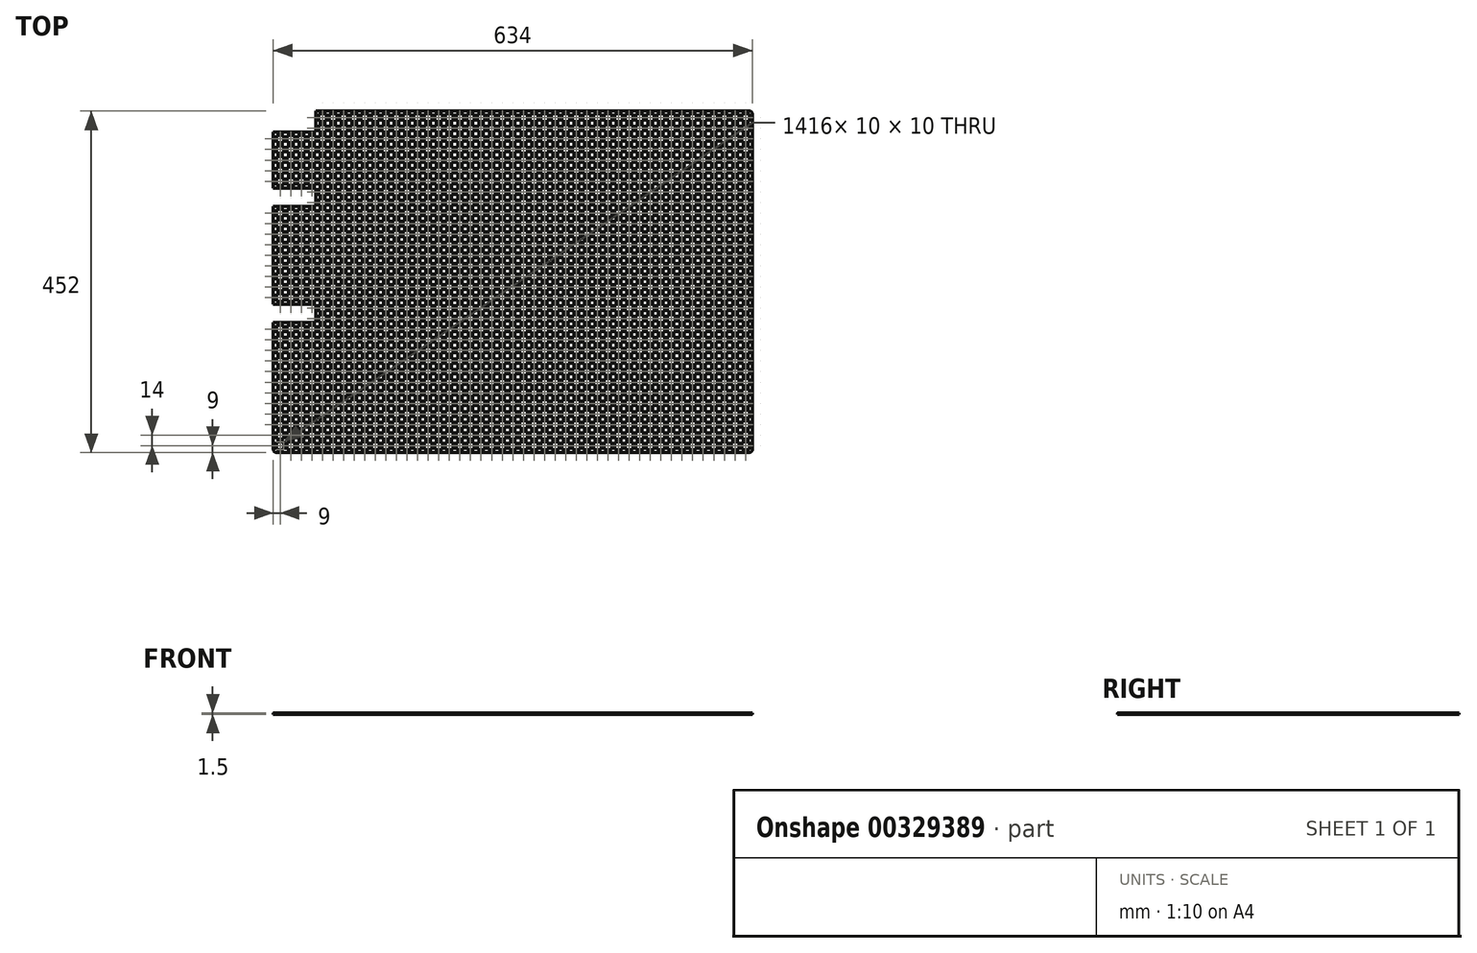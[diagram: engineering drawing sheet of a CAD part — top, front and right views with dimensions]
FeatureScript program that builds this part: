
annotation { "Feature Type Name" : "Feature", "Feature Type Description" : "" }
export const myFeature = defineFeature(function(context is Context, id is Id, definition is map)
    precondition{}
    {
        {
            var Q0;
            Q0=qCreatedBy(makeId("Top.planeOp"),FACE);
            var sketch = newSketch(context, id + "F0", { "sketchPlane" : qUnion([Q0])});
            skLineSegment(sketch, "E0.bottom", {"start": v(-313, 226) * mm, "end": v(313, 226) * mm});
            skLineSegment(sketch, "E0.top", {"start": v(-313, -226) * mm, "end": v(313, -226) * mm});
            skLineSegment(sketch, "E0.left", {"start": v(-317, 222) * mm, "end": v(-317, -222) * mm});
            skLineSegment(sketch, "E0.right", {"start": v(317, 222) * mm, "end": v(317, -222) * mm});
            skLineSegment(sketch, "E1.bottom", {"start": v(-313, -212) * mm, "end": v(-303, -212) * mm});
            skLineSegment(sketch, "E1.top", {"start": v(-313, -222) * mm, "end": v(-303, -222) * mm});
            skLineSegment(sketch, "E1.left", {"start": v(-313, -212) * mm, "end": v(-313, -222) * mm});
            skLineSegment(sketch, "E1.right", {"start": v(-303, -212) * mm, "end": v(-303, -222) * mm});
            skLineSegment(sketch, "E2", {"start": v(-317, 226) * mm, "end": v(317, -226) * mm, "construction": true});
            skLineSegment(sketch, "E3.0.1.0", {"start": v(-313, -198) * mm, "end": v(-313, -208) * mm});
            skLineSegment(sketch, "E3.0.1.1", {"start": v(-313, -208) * mm, "end": v(-303, -208) * mm});
            skLineSegment(sketch, "E3.0.1.2", {"start": v(-313, -198) * mm, "end": v(-303, -198) * mm});
            skLineSegment(sketch, "E3.0.1.3", {"start": v(-303, -198) * mm, "end": v(-303, -208) * mm});
            skLineSegment(sketch, "E3.1.0.0", {"start": v(-299, -212) * mm, "end": v(-299, -222) * mm});
            skLineSegment(sketch, "E3.1.0.1", {"start": v(-299, -222) * mm, "end": v(-289, -222) * mm});
            skLineSegment(sketch, "E3.1.0.2", {"start": v(-299, -212) * mm, "end": v(-289, -212) * mm});
            skLineSegment(sketch, "E3.1.0.3", {"start": v(-289, -212) * mm, "end": v(-289, -222) * mm});
            skLineSegment(sketch, "E3.1.1.0", {"start": v(-299, -198) * mm, "end": v(-299, -208) * mm});
            skLineSegment(sketch, "E3.1.1.1", {"start": v(-299, -208) * mm, "end": v(-289, -208) * mm});
            skLineSegment(sketch, "E3.1.1.2", {"start": v(-299, -198) * mm, "end": v(-289, -198) * mm});
            skLineSegment(sketch, "E3.1.1.3", {"start": v(-289, -198) * mm, "end": v(-289, -208) * mm});
            skLineSegment(sketch, "E3.direction1", {"start": v(-313, -222) * mm, "end": v(-299, -222) * mm, "construction": true});
            skLineSegment(sketch, "E3.direction2", {"start": v(-313, -222) * mm, "end": v(-313, -208) * mm, "construction": true});
            skPoint(sketch, "E4.visualSharp", {"position": v(317, 226) * mm});
            skArc(sketch, "E4.filletArc", {"start": v(317, 222) * mm, "mid": v(315.83, 224.83) * mm, "end": v(313, 226) * mm});
            skPoint(sketch, "E5.visualSharp", {"position": v(-317, 226) * mm});
            skArc(sketch, "E5.filletArc", {"start": v(-313, 226) * mm, "mid": v(-315.83, 224.83) * mm, "end": v(-317, 222) * mm});
            skPoint(sketch, "E6.visualSharp", {"position": v(-317, -226) * mm});
            skArc(sketch, "E6.filletArc", {"start": v(-317, -222) * mm, "mid": v(-315.83, -224.83) * mm, "end": v(-313, -226) * mm});
            skPoint(sketch, "E7.visualSharp", {"position": v(317, -226) * mm});
            skArc(sketch, "E7.filletArc", {"start": v(313, -226) * mm, "mid": v(315.83, -224.83) * mm, "end": v(317, -222) * mm});
            skLineSegment(sketch, "E8.0.0.2", {"start": v(-313, -184) * mm, "end": v(-313, -194) * mm});
            skLineSegment(sketch, "E8.3.0.2", {"start": v(-313, -194) * mm, "end": v(-303, -194) * mm});
            skLineSegment(sketch, "E8.6.0.2", {"start": v(-313, -184) * mm, "end": v(-303, -184) * mm});
            skLineSegment(sketch, "E8.9.0.2", {"start": v(-303, -184) * mm, "end": v(-303, -194) * mm});
            skLineSegment(sketch, "E8.0.0.3", {"start": v(-313, -170) * mm, "end": v(-313, -180) * mm});
            skLineSegment(sketch, "E8.3.0.3", {"start": v(-313, -180) * mm, "end": v(-303, -180) * mm});
            skLineSegment(sketch, "E8.6.0.3", {"start": v(-313, -170) * mm, "end": v(-303, -170) * mm});
            skLineSegment(sketch, "E8.9.0.3", {"start": v(-303, -170) * mm, "end": v(-303, -180) * mm});
            skLineSegment(sketch, "E8.0.0.4", {"start": v(-313, -156) * mm, "end": v(-313, -166) * mm});
            skLineSegment(sketch, "E8.3.0.4", {"start": v(-313, -166) * mm, "end": v(-303, -166) * mm});
            skLineSegment(sketch, "E8.6.0.4", {"start": v(-313, -156) * mm, "end": v(-303, -156) * mm});
            skLineSegment(sketch, "E8.9.0.4", {"start": v(-303, -156) * mm, "end": v(-303, -166) * mm});
            skLineSegment(sketch, "E8.0.0.5", {"start": v(-313, -142) * mm, "end": v(-313, -152) * mm});
            skLineSegment(sketch, "E8.3.0.5", {"start": v(-313, -152) * mm, "end": v(-303, -152) * mm});
            skLineSegment(sketch, "E8.6.0.5", {"start": v(-313, -142) * mm, "end": v(-303, -142) * mm});
            skLineSegment(sketch, "E8.9.0.5", {"start": v(-303, -142) * mm, "end": v(-303, -152) * mm});
            skLineSegment(sketch, "E8.0.0.6", {"start": v(-313, -128) * mm, "end": v(-313, -138) * mm});
            skLineSegment(sketch, "E8.3.0.6", {"start": v(-313, -138) * mm, "end": v(-303, -138) * mm});
            skLineSegment(sketch, "E8.6.0.6", {"start": v(-313, -128) * mm, "end": v(-303, -128) * mm});
            skLineSegment(sketch, "E8.9.0.6", {"start": v(-303, -128) * mm, "end": v(-303, -138) * mm});
            skLineSegment(sketch, "E8.0.0.7", {"start": v(-313, -114) * mm, "end": v(-313, -124) * mm});
            skLineSegment(sketch, "E8.3.0.7", {"start": v(-313, -124) * mm, "end": v(-303, -124) * mm});
            skLineSegment(sketch, "E8.6.0.7", {"start": v(-313, -114) * mm, "end": v(-303, -114) * mm});
            skLineSegment(sketch, "E8.9.0.7", {"start": v(-303, -114) * mm, "end": v(-303, -124) * mm});
            skLineSegment(sketch, "E8.0.0.8", {"start": v(-313, -100) * mm, "end": v(-313, -110) * mm});
            skLineSegment(sketch, "E8.3.0.8", {"start": v(-313, -110) * mm, "end": v(-303, -110) * mm});
            skLineSegment(sketch, "E8.6.0.8", {"start": v(-313, -100) * mm, "end": v(-303, -100) * mm});
            skLineSegment(sketch, "E8.9.0.8", {"start": v(-303, -100) * mm, "end": v(-303, -110) * mm});
            skLineSegment(sketch, "E8.0.0.9", {"start": v(-313, -86) * mm, "end": v(-313, -96) * mm});
            skLineSegment(sketch, "E8.3.0.9", {"start": v(-313, -96) * mm, "end": v(-303, -96) * mm});
            skLineSegment(sketch, "E8.6.0.9", {"start": v(-313, -86) * mm, "end": v(-303, -86) * mm});
            skLineSegment(sketch, "E8.9.0.9", {"start": v(-303, -86) * mm, "end": v(-303, -96) * mm});
            skLineSegment(sketch, "E8.0.0.10", {"start": v(-313, -72) * mm, "end": v(-313, -82) * mm});
            skLineSegment(sketch, "E8.3.0.10", {"start": v(-313, -82) * mm, "end": v(-303, -82) * mm});
            skLineSegment(sketch, "E8.6.0.10", {"start": v(-313, -72) * mm, "end": v(-303, -72) * mm});
            skLineSegment(sketch, "E8.9.0.10", {"start": v(-303, -72) * mm, "end": v(-303, -82) * mm});
            skLineSegment(sketch, "E8.0.0.11", {"start": v(-313, -58) * mm, "end": v(-313, -68) * mm});
            skLineSegment(sketch, "E8.3.0.11", {"start": v(-313, -68) * mm, "end": v(-303, -68) * mm});
            skLineSegment(sketch, "E8.6.0.11", {"start": v(-313, -58) * mm, "end": v(-303, -58) * mm});
            skLineSegment(sketch, "E8.9.0.11", {"start": v(-303, -58) * mm, "end": v(-303, -68) * mm});
            skLineSegment(sketch, "E8.0.0.12", {"start": v(-313, -44) * mm, "end": v(-313, -54) * mm});
            skLineSegment(sketch, "E8.3.0.12", {"start": v(-313, -54) * mm, "end": v(-303, -54) * mm});
            skLineSegment(sketch, "E8.6.0.12", {"start": v(-313, -44) * mm, "end": v(-303, -44) * mm});
            skLineSegment(sketch, "E8.9.0.12", {"start": v(-303, -44) * mm, "end": v(-303, -54) * mm});
            skLineSegment(sketch, "E8.0.0.13", {"start": v(-313, -30) * mm, "end": v(-313, -40) * mm});
            skLineSegment(sketch, "E8.3.0.13", {"start": v(-313, -40) * mm, "end": v(-303, -40) * mm});
            skLineSegment(sketch, "E8.6.0.13", {"start": v(-313, -30) * mm, "end": v(-303, -30) * mm});
            skLineSegment(sketch, "E8.9.0.13", {"start": v(-303, -30) * mm, "end": v(-303, -40) * mm});
            skLineSegment(sketch, "E8.0.0.14", {"start": v(-313, -16) * mm, "end": v(-313, -26) * mm});
            skLineSegment(sketch, "E8.3.0.14", {"start": v(-313, -26) * mm, "end": v(-303, -26) * mm});
            skLineSegment(sketch, "E8.6.0.14", {"start": v(-313, -16) * mm, "end": v(-303, -16) * mm});
            skLineSegment(sketch, "E8.9.0.14", {"start": v(-303, -16) * mm, "end": v(-303, -26) * mm});
            skLineSegment(sketch, "E8.0.0.15", {"start": v(-313, -2) * mm, "end": v(-313, -12) * mm});
            skLineSegment(sketch, "E8.3.0.15", {"start": v(-313, -12) * mm, "end": v(-303, -12) * mm});
            skLineSegment(sketch, "E8.6.0.15", {"start": v(-313, -2) * mm, "end": v(-303, -2) * mm});
            skLineSegment(sketch, "E8.9.0.15", {"start": v(-303, -2) * mm, "end": v(-303, -12) * mm});
            skLineSegment(sketch, "E8.0.0.16", {"start": v(-313, 12) * mm, "end": v(-313, 2) * mm});
            skLineSegment(sketch, "E8.3.0.16", {"start": v(-313, 2) * mm, "end": v(-303, 2) * mm});
            skLineSegment(sketch, "E8.6.0.16", {"start": v(-313, 12) * mm, "end": v(-303, 12) * mm});
            skLineSegment(sketch, "E8.9.0.16", {"start": v(-303, 12) * mm, "end": v(-303, 2) * mm});
            skLineSegment(sketch, "E8.0.0.17", {"start": v(-313, 26) * mm, "end": v(-313, 16) * mm});
            skLineSegment(sketch, "E8.3.0.17", {"start": v(-313, 16) * mm, "end": v(-303, 16) * mm});
            skLineSegment(sketch, "E8.6.0.17", {"start": v(-313, 26) * mm, "end": v(-303, 26) * mm});
            skLineSegment(sketch, "E8.9.0.17", {"start": v(-303, 26) * mm, "end": v(-303, 16) * mm});
            skLineSegment(sketch, "E8.0.0.18", {"start": v(-313, 40) * mm, "end": v(-313, 30) * mm});
            skLineSegment(sketch, "E8.3.0.18", {"start": v(-313, 30) * mm, "end": v(-303, 30) * mm});
            skLineSegment(sketch, "E8.6.0.18", {"start": v(-313, 40) * mm, "end": v(-303, 40) * mm});
            skLineSegment(sketch, "E8.9.0.18", {"start": v(-303, 40) * mm, "end": v(-303, 30) * mm});
            skLineSegment(sketch, "E8.0.0.19", {"start": v(-313, 54) * mm, "end": v(-313, 44) * mm});
            skLineSegment(sketch, "E8.3.0.19", {"start": v(-313, 44) * mm, "end": v(-303, 44) * mm});
            skLineSegment(sketch, "E8.6.0.19", {"start": v(-313, 54) * mm, "end": v(-303, 54) * mm});
            skLineSegment(sketch, "E8.9.0.19", {"start": v(-303, 54) * mm, "end": v(-303, 44) * mm});
            skLineSegment(sketch, "E8.0.0.20", {"start": v(-313, 68) * mm, "end": v(-313, 58) * mm});
            skLineSegment(sketch, "E8.3.0.20", {"start": v(-313, 58) * mm, "end": v(-303, 58) * mm});
            skLineSegment(sketch, "E8.6.0.20", {"start": v(-313, 68) * mm, "end": v(-303, 68) * mm});
            skLineSegment(sketch, "E8.9.0.20", {"start": v(-303, 68) * mm, "end": v(-303, 58) * mm});
            skLineSegment(sketch, "E8.0.0.21", {"start": v(-313, 82) * mm, "end": v(-313, 72) * mm});
            skLineSegment(sketch, "E8.3.0.21", {"start": v(-313, 72) * mm, "end": v(-303, 72) * mm});
            skLineSegment(sketch, "E8.6.0.21", {"start": v(-313, 82) * mm, "end": v(-303, 82) * mm});
            skLineSegment(sketch, "E8.9.0.21", {"start": v(-303, 82) * mm, "end": v(-303, 72) * mm});
            skLineSegment(sketch, "E8.0.0.22", {"start": v(-313, 96) * mm, "end": v(-313, 86) * mm});
            skLineSegment(sketch, "E8.3.0.22", {"start": v(-313, 86) * mm, "end": v(-303, 86) * mm});
            skLineSegment(sketch, "E8.6.0.22", {"start": v(-313, 96) * mm, "end": v(-303, 96) * mm});
            skLineSegment(sketch, "E8.9.0.22", {"start": v(-303, 96) * mm, "end": v(-303, 86) * mm});
            skLineSegment(sketch, "E8.0.0.23", {"start": v(-313, 110) * mm, "end": v(-313, 100) * mm});
            skLineSegment(sketch, "E8.3.0.23", {"start": v(-313, 100) * mm, "end": v(-303, 100) * mm});
            skLineSegment(sketch, "E8.6.0.23", {"start": v(-313, 110) * mm, "end": v(-303, 110) * mm});
            skLineSegment(sketch, "E8.9.0.23", {"start": v(-303, 110) * mm, "end": v(-303, 100) * mm});
            skLineSegment(sketch, "E8.0.0.24", {"start": v(-313, 124) * mm, "end": v(-313, 114) * mm});
            skLineSegment(sketch, "E8.3.0.24", {"start": v(-313, 114) * mm, "end": v(-303, 114) * mm});
            skLineSegment(sketch, "E8.6.0.24", {"start": v(-313, 124) * mm, "end": v(-303, 124) * mm});
            skLineSegment(sketch, "E8.9.0.24", {"start": v(-303, 124) * mm, "end": v(-303, 114) * mm});
            skLineSegment(sketch, "E8.0.0.25", {"start": v(-313, 138) * mm, "end": v(-313, 128) * mm});
            skLineSegment(sketch, "E8.3.0.25", {"start": v(-313, 128) * mm, "end": v(-303, 128) * mm});
            skLineSegment(sketch, "E8.6.0.25", {"start": v(-313, 138) * mm, "end": v(-303, 138) * mm});
            skLineSegment(sketch, "E8.9.0.25", {"start": v(-303, 138) * mm, "end": v(-303, 128) * mm});
            skLineSegment(sketch, "E8.0.0.26", {"start": v(-313, 152) * mm, "end": v(-313, 142) * mm});
            skLineSegment(sketch, "E8.3.0.26", {"start": v(-313, 142) * mm, "end": v(-303, 142) * mm});
            skLineSegment(sketch, "E8.6.0.26", {"start": v(-313, 152) * mm, "end": v(-303, 152) * mm});
            skLineSegment(sketch, "E8.9.0.26", {"start": v(-303, 152) * mm, "end": v(-303, 142) * mm});
            skLineSegment(sketch, "E8.0.0.27", {"start": v(-313, 166) * mm, "end": v(-313, 156) * mm});
            skLineSegment(sketch, "E8.3.0.27", {"start": v(-313, 156) * mm, "end": v(-303, 156) * mm});
            skLineSegment(sketch, "E8.6.0.27", {"start": v(-313, 166) * mm, "end": v(-303, 166) * mm});
            skLineSegment(sketch, "E8.9.0.27", {"start": v(-303, 166) * mm, "end": v(-303, 156) * mm});
            skLineSegment(sketch, "E8.0.0.28", {"start": v(-313, 180) * mm, "end": v(-313, 170) * mm});
            skLineSegment(sketch, "E8.3.0.28", {"start": v(-313, 170) * mm, "end": v(-303, 170) * mm});
            skLineSegment(sketch, "E8.6.0.28", {"start": v(-313, 180) * mm, "end": v(-303, 180) * mm});
            skLineSegment(sketch, "E8.9.0.28", {"start": v(-303, 180) * mm, "end": v(-303, 170) * mm});
            skLineSegment(sketch, "E8.0.0.29", {"start": v(-313, 194) * mm, "end": v(-313, 184) * mm});
            skLineSegment(sketch, "E8.3.0.29", {"start": v(-313, 184) * mm, "end": v(-303, 184) * mm});
            skLineSegment(sketch, "E8.6.0.29", {"start": v(-313, 194) * mm, "end": v(-303, 194) * mm});
            skLineSegment(sketch, "E8.9.0.29", {"start": v(-303, 194) * mm, "end": v(-303, 184) * mm});
            skLineSegment(sketch, "E8.0.0.30", {"start": v(-313, 208) * mm, "end": v(-313, 198) * mm});
            skLineSegment(sketch, "E8.3.0.30", {"start": v(-313, 198) * mm, "end": v(-303, 198) * mm});
            skLineSegment(sketch, "E8.6.0.30", {"start": v(-313, 208) * mm, "end": v(-303, 208) * mm});
            skLineSegment(sketch, "E8.9.0.30", {"start": v(-303, 208) * mm, "end": v(-303, 198) * mm});
            skLineSegment(sketch, "E8.0.0.31", {"start": v(-313, 222) * mm, "end": v(-313, 212) * mm});
            skLineSegment(sketch, "E8.3.0.31", {"start": v(-313, 212) * mm, "end": v(-303, 212) * mm});
            skLineSegment(sketch, "E8.6.0.31", {"start": v(-313, 222) * mm, "end": v(-303, 222) * mm});
            skLineSegment(sketch, "E8.9.0.31", {"start": v(-303, 222) * mm, "end": v(-303, 212) * mm});
            skLineSegment(sketch, "E8.0.1.2", {"start": v(-299, -184) * mm, "end": v(-299, -194) * mm});
            skLineSegment(sketch, "E8.3.1.2", {"start": v(-299, -194) * mm, "end": v(-289, -194) * mm});
            skLineSegment(sketch, "E8.6.1.2", {"start": v(-299, -184) * mm, "end": v(-289, -184) * mm});
            skLineSegment(sketch, "E8.9.1.2", {"start": v(-289, -184) * mm, "end": v(-289, -194) * mm});
            skLineSegment(sketch, "E8.0.1.3", {"start": v(-299, -170) * mm, "end": v(-299, -180) * mm});
            skLineSegment(sketch, "E8.3.1.3", {"start": v(-299, -180) * mm, "end": v(-289, -180) * mm});
            skLineSegment(sketch, "E8.6.1.3", {"start": v(-299, -170) * mm, "end": v(-289, -170) * mm});
            skLineSegment(sketch, "E8.9.1.3", {"start": v(-289, -170) * mm, "end": v(-289, -180) * mm});
            skLineSegment(sketch, "E8.0.1.4", {"start": v(-299, -156) * mm, "end": v(-299, -166) * mm});
            skLineSegment(sketch, "E8.3.1.4", {"start": v(-299, -166) * mm, "end": v(-289, -166) * mm});
            skLineSegment(sketch, "E8.6.1.4", {"start": v(-299, -156) * mm, "end": v(-289, -156) * mm});
            skLineSegment(sketch, "E8.9.1.4", {"start": v(-289, -156) * mm, "end": v(-289, -166) * mm});
            skLineSegment(sketch, "E8.0.1.5", {"start": v(-299, -142) * mm, "end": v(-299, -152) * mm});
            skLineSegment(sketch, "E8.3.1.5", {"start": v(-299, -152) * mm, "end": v(-289, -152) * mm});
            skLineSegment(sketch, "E8.6.1.5", {"start": v(-299, -142) * mm, "end": v(-289, -142) * mm});
            skLineSegment(sketch, "E8.9.1.5", {"start": v(-289, -142) * mm, "end": v(-289, -152) * mm});
            skLineSegment(sketch, "E8.0.1.6", {"start": v(-299, -128) * mm, "end": v(-299, -138) * mm});
            skLineSegment(sketch, "E8.3.1.6", {"start": v(-299, -138) * mm, "end": v(-289, -138) * mm});
            skLineSegment(sketch, "E8.6.1.6", {"start": v(-299, -128) * mm, "end": v(-289, -128) * mm});
            skLineSegment(sketch, "E8.9.1.6", {"start": v(-289, -128) * mm, "end": v(-289, -138) * mm});
            skLineSegment(sketch, "E8.0.1.7", {"start": v(-299, -114) * mm, "end": v(-299, -124) * mm});
            skLineSegment(sketch, "E8.3.1.7", {"start": v(-299, -124) * mm, "end": v(-289, -124) * mm});
            skLineSegment(sketch, "E8.6.1.7", {"start": v(-299, -114) * mm, "end": v(-289, -114) * mm});
            skLineSegment(sketch, "E8.9.1.7", {"start": v(-289, -114) * mm, "end": v(-289, -124) * mm});
            skLineSegment(sketch, "E8.0.1.8", {"start": v(-299, -100) * mm, "end": v(-299, -110) * mm});
            skLineSegment(sketch, "E8.3.1.8", {"start": v(-299, -110) * mm, "end": v(-289, -110) * mm});
            skLineSegment(sketch, "E8.6.1.8", {"start": v(-299, -100) * mm, "end": v(-289, -100) * mm});
            skLineSegment(sketch, "E8.9.1.8", {"start": v(-289, -100) * mm, "end": v(-289, -110) * mm});
            skLineSegment(sketch, "E8.0.1.9", {"start": v(-299, -86) * mm, "end": v(-299, -96) * mm});
            skLineSegment(sketch, "E8.3.1.9", {"start": v(-299, -96) * mm, "end": v(-289, -96) * mm});
            skLineSegment(sketch, "E8.6.1.9", {"start": v(-299, -86) * mm, "end": v(-289, -86) * mm});
            skLineSegment(sketch, "E8.9.1.9", {"start": v(-289, -86) * mm, "end": v(-289, -96) * mm});
            skLineSegment(sketch, "E8.0.1.10", {"start": v(-299, -72) * mm, "end": v(-299, -82) * mm});
            skLineSegment(sketch, "E8.3.1.10", {"start": v(-299, -82) * mm, "end": v(-289, -82) * mm});
            skLineSegment(sketch, "E8.6.1.10", {"start": v(-299, -72) * mm, "end": v(-289, -72) * mm});
            skLineSegment(sketch, "E8.9.1.10", {"start": v(-289, -72) * mm, "end": v(-289, -82) * mm});
            skLineSegment(sketch, "E8.0.1.11", {"start": v(-299, -58) * mm, "end": v(-299, -68) * mm});
            skLineSegment(sketch, "E8.3.1.11", {"start": v(-299, -68) * mm, "end": v(-289, -68) * mm});
            skLineSegment(sketch, "E8.6.1.11", {"start": v(-299, -58) * mm, "end": v(-289, -58) * mm});
            skLineSegment(sketch, "E8.9.1.11", {"start": v(-289, -58) * mm, "end": v(-289, -68) * mm});
            skLineSegment(sketch, "E8.0.1.12", {"start": v(-299, -44) * mm, "end": v(-299, -54) * mm});
            skLineSegment(sketch, "E8.3.1.12", {"start": v(-299, -54) * mm, "end": v(-289, -54) * mm});
            skLineSegment(sketch, "E8.6.1.12", {"start": v(-299, -44) * mm, "end": v(-289, -44) * mm});
            skLineSegment(sketch, "E8.9.1.12", {"start": v(-289, -44) * mm, "end": v(-289, -54) * mm});
            skLineSegment(sketch, "E8.0.1.13", {"start": v(-299, -30) * mm, "end": v(-299, -40) * mm});
            skLineSegment(sketch, "E8.3.1.13", {"start": v(-299, -40) * mm, "end": v(-289, -40) * mm});
            skLineSegment(sketch, "E8.6.1.13", {"start": v(-299, -30) * mm, "end": v(-289, -30) * mm});
            skLineSegment(sketch, "E8.9.1.13", {"start": v(-289, -30) * mm, "end": v(-289, -40) * mm});
            skLineSegment(sketch, "E8.0.1.14", {"start": v(-299, -16) * mm, "end": v(-299, -26) * mm});
            skLineSegment(sketch, "E8.3.1.14", {"start": v(-299, -26) * mm, "end": v(-289, -26) * mm});
            skLineSegment(sketch, "E8.6.1.14", {"start": v(-299, -16) * mm, "end": v(-289, -16) * mm});
            skLineSegment(sketch, "E8.9.1.14", {"start": v(-289, -16) * mm, "end": v(-289, -26) * mm});
            skLineSegment(sketch, "E8.0.1.15", {"start": v(-299, -2) * mm, "end": v(-299, -12) * mm});
            skLineSegment(sketch, "E8.3.1.15", {"start": v(-299, -12) * mm, "end": v(-289, -12) * mm});
            skLineSegment(sketch, "E8.6.1.15", {"start": v(-299, -2) * mm, "end": v(-289, -2) * mm});
            skLineSegment(sketch, "E8.9.1.15", {"start": v(-289, -2) * mm, "end": v(-289, -12) * mm});
            skLineSegment(sketch, "E8.0.1.16", {"start": v(-299, 12) * mm, "end": v(-299, 2) * mm});
            skLineSegment(sketch, "E8.3.1.16", {"start": v(-299, 2) * mm, "end": v(-289, 2) * mm});
            skLineSegment(sketch, "E8.6.1.16", {"start": v(-299, 12) * mm, "end": v(-289, 12) * mm});
            skLineSegment(sketch, "E8.9.1.16", {"start": v(-289, 12) * mm, "end": v(-289, 2) * mm});
            skLineSegment(sketch, "E8.0.1.17", {"start": v(-299, 26) * mm, "end": v(-299, 16) * mm});
            skLineSegment(sketch, "E8.3.1.17", {"start": v(-299, 16) * mm, "end": v(-289, 16) * mm});
            skLineSegment(sketch, "E8.6.1.17", {"start": v(-299, 26) * mm, "end": v(-289, 26) * mm});
            skLineSegment(sketch, "E8.9.1.17", {"start": v(-289, 26) * mm, "end": v(-289, 16) * mm});
            skLineSegment(sketch, "E8.0.1.18", {"start": v(-299, 40) * mm, "end": v(-299, 30) * mm});
            skLineSegment(sketch, "E8.3.1.18", {"start": v(-299, 30) * mm, "end": v(-289, 30) * mm});
            skLineSegment(sketch, "E8.6.1.18", {"start": v(-299, 40) * mm, "end": v(-289, 40) * mm});
            skLineSegment(sketch, "E8.9.1.18", {"start": v(-289, 40) * mm, "end": v(-289, 30) * mm});
            skLineSegment(sketch, "E8.0.1.19", {"start": v(-299, 54) * mm, "end": v(-299, 44) * mm});
            skLineSegment(sketch, "E8.3.1.19", {"start": v(-299, 44) * mm, "end": v(-289, 44) * mm});
            skLineSegment(sketch, "E8.6.1.19", {"start": v(-299, 54) * mm, "end": v(-289, 54) * mm});
            skLineSegment(sketch, "E8.9.1.19", {"start": v(-289, 54) * mm, "end": v(-289, 44) * mm});
            skLineSegment(sketch, "E8.0.1.20", {"start": v(-299, 68) * mm, "end": v(-299, 58) * mm});
            skLineSegment(sketch, "E8.3.1.20", {"start": v(-299, 58) * mm, "end": v(-289, 58) * mm});
            skLineSegment(sketch, "E8.6.1.20", {"start": v(-299, 68) * mm, "end": v(-289, 68) * mm});
            skLineSegment(sketch, "E8.9.1.20", {"start": v(-289, 68) * mm, "end": v(-289, 58) * mm});
            skLineSegment(sketch, "E8.0.1.21", {"start": v(-299, 82) * mm, "end": v(-299, 72) * mm});
            skLineSegment(sketch, "E8.3.1.21", {"start": v(-299, 72) * mm, "end": v(-289, 72) * mm});
            skLineSegment(sketch, "E8.6.1.21", {"start": v(-299, 82) * mm, "end": v(-289, 82) * mm});
            skLineSegment(sketch, "E8.9.1.21", {"start": v(-289, 82) * mm, "end": v(-289, 72) * mm});
            skLineSegment(sketch, "E8.0.1.22", {"start": v(-299, 96) * mm, "end": v(-299, 86) * mm});
            skLineSegment(sketch, "E8.3.1.22", {"start": v(-299, 86) * mm, "end": v(-289, 86) * mm});
            skLineSegment(sketch, "E8.6.1.22", {"start": v(-299, 96) * mm, "end": v(-289, 96) * mm});
            skLineSegment(sketch, "E8.9.1.22", {"start": v(-289, 96) * mm, "end": v(-289, 86) * mm});
            skLineSegment(sketch, "E8.0.1.23", {"start": v(-299, 110) * mm, "end": v(-299, 100) * mm});
            skLineSegment(sketch, "E8.3.1.23", {"start": v(-299, 100) * mm, "end": v(-289, 100) * mm});
            skLineSegment(sketch, "E8.6.1.23", {"start": v(-299, 110) * mm, "end": v(-289, 110) * mm});
            skLineSegment(sketch, "E8.9.1.23", {"start": v(-289, 110) * mm, "end": v(-289, 100) * mm});
            skLineSegment(sketch, "E8.0.1.24", {"start": v(-299, 124) * mm, "end": v(-299, 114) * mm});
            skLineSegment(sketch, "E8.3.1.24", {"start": v(-299, 114) * mm, "end": v(-289, 114) * mm});
            skLineSegment(sketch, "E8.6.1.24", {"start": v(-299, 124) * mm, "end": v(-289, 124) * mm});
            skLineSegment(sketch, "E8.9.1.24", {"start": v(-289, 124) * mm, "end": v(-289, 114) * mm});
            skLineSegment(sketch, "E8.0.1.25", {"start": v(-299, 138) * mm, "end": v(-299, 128) * mm});
            skLineSegment(sketch, "E8.3.1.25", {"start": v(-299, 128) * mm, "end": v(-289, 128) * mm});
            skLineSegment(sketch, "E8.6.1.25", {"start": v(-299, 138) * mm, "end": v(-289, 138) * mm});
            skLineSegment(sketch, "E8.9.1.25", {"start": v(-289, 138) * mm, "end": v(-289, 128) * mm});
            skLineSegment(sketch, "E8.0.1.26", {"start": v(-299, 152) * mm, "end": v(-299, 142) * mm});
            skLineSegment(sketch, "E8.3.1.26", {"start": v(-299, 142) * mm, "end": v(-289, 142) * mm});
            skLineSegment(sketch, "E8.6.1.26", {"start": v(-299, 152) * mm, "end": v(-289, 152) * mm});
            skLineSegment(sketch, "E8.9.1.26", {"start": v(-289, 152) * mm, "end": v(-289, 142) * mm});
            skLineSegment(sketch, "E8.0.1.27", {"start": v(-299, 166) * mm, "end": v(-299, 156) * mm});
            skLineSegment(sketch, "E8.3.1.27", {"start": v(-299, 156) * mm, "end": v(-289, 156) * mm});
            skLineSegment(sketch, "E8.6.1.27", {"start": v(-299, 166) * mm, "end": v(-289, 166) * mm});
            skLineSegment(sketch, "E8.9.1.27", {"start": v(-289, 166) * mm, "end": v(-289, 156) * mm});
            skLineSegment(sketch, "E8.0.1.28", {"start": v(-299, 180) * mm, "end": v(-299, 170) * mm});
            skLineSegment(sketch, "E8.3.1.28", {"start": v(-299, 170) * mm, "end": v(-289, 170) * mm});
            skLineSegment(sketch, "E8.6.1.28", {"start": v(-299, 180) * mm, "end": v(-289, 180) * mm});
            skLineSegment(sketch, "E8.9.1.28", {"start": v(-289, 180) * mm, "end": v(-289, 170) * mm});
            skLineSegment(sketch, "E8.0.1.29", {"start": v(-299, 194) * mm, "end": v(-299, 184) * mm});
            skLineSegment(sketch, "E8.3.1.29", {"start": v(-299, 184) * mm, "end": v(-289, 184) * mm});
            skLineSegment(sketch, "E8.6.1.29", {"start": v(-299, 194) * mm, "end": v(-289, 194) * mm});
            skLineSegment(sketch, "E8.9.1.29", {"start": v(-289, 194) * mm, "end": v(-289, 184) * mm});
            skLineSegment(sketch, "E8.0.1.30", {"start": v(-299, 208) * mm, "end": v(-299, 198) * mm});
            skLineSegment(sketch, "E8.3.1.30", {"start": v(-299, 198) * mm, "end": v(-289, 198) * mm});
            skLineSegment(sketch, "E8.6.1.30", {"start": v(-299, 208) * mm, "end": v(-289, 208) * mm});
            skLineSegment(sketch, "E8.9.1.30", {"start": v(-289, 208) * mm, "end": v(-289, 198) * mm});
            skLineSegment(sketch, "E8.0.1.31", {"start": v(-299, 222) * mm, "end": v(-299, 212) * mm});
            skLineSegment(sketch, "E8.3.1.31", {"start": v(-299, 212) * mm, "end": v(-289, 212) * mm});
            skLineSegment(sketch, "E8.6.1.31", {"start": v(-299, 222) * mm, "end": v(-289, 222) * mm});
            skLineSegment(sketch, "E8.9.1.31", {"start": v(-289, 222) * mm, "end": v(-289, 212) * mm});
            skLineSegment(sketch, "E9.0.2.0", {"start": v(-285, -212) * mm, "end": v(-285, -222) * mm});
            skLineSegment(sketch, "E9.3.2.0", {"start": v(-285, -222) * mm, "end": v(-275, -222) * mm});
            skLineSegment(sketch, "E9.6.2.0", {"start": v(-285, -212) * mm, "end": v(-275, -212) * mm});
            skLineSegment(sketch, "E9.9.2.0", {"start": v(-275, -212) * mm, "end": v(-275, -222) * mm});
            skLineSegment(sketch, "E9.0.2.1", {"start": v(-285, -198) * mm, "end": v(-285, -208) * mm});
            skLineSegment(sketch, "E9.3.2.1", {"start": v(-285, -208) * mm, "end": v(-275, -208) * mm});
            skLineSegment(sketch, "E9.6.2.1", {"start": v(-285, -198) * mm, "end": v(-275, -198) * mm});
            skLineSegment(sketch, "E9.9.2.1", {"start": v(-275, -198) * mm, "end": v(-275, -208) * mm});
            skLineSegment(sketch, "E9.0.2.2", {"start": v(-285, -184) * mm, "end": v(-285, -194) * mm});
            skLineSegment(sketch, "E9.3.2.2", {"start": v(-285, -194) * mm, "end": v(-275, -194) * mm});
            skLineSegment(sketch, "E9.6.2.2", {"start": v(-285, -184) * mm, "end": v(-275, -184) * mm});
            skLineSegment(sketch, "E9.9.2.2", {"start": v(-275, -184) * mm, "end": v(-275, -194) * mm});
            skLineSegment(sketch, "E9.0.2.3", {"start": v(-285, -170) * mm, "end": v(-285, -180) * mm});
            skLineSegment(sketch, "E9.3.2.3", {"start": v(-285, -180) * mm, "end": v(-275, -180) * mm});
            skLineSegment(sketch, "E9.6.2.3", {"start": v(-285, -170) * mm, "end": v(-275, -170) * mm});
            skLineSegment(sketch, "E9.9.2.3", {"start": v(-275, -170) * mm, "end": v(-275, -180) * mm});
            skLineSegment(sketch, "E9.0.2.4", {"start": v(-285, -156) * mm, "end": v(-285, -166) * mm});
            skLineSegment(sketch, "E9.3.2.4", {"start": v(-285, -166) * mm, "end": v(-275, -166) * mm});
            skLineSegment(sketch, "E9.6.2.4", {"start": v(-285, -156) * mm, "end": v(-275, -156) * mm});
            skLineSegment(sketch, "E9.9.2.4", {"start": v(-275, -156) * mm, "end": v(-275, -166) * mm});
            skLineSegment(sketch, "E9.0.2.5", {"start": v(-285, -142) * mm, "end": v(-285, -152) * mm});
            skLineSegment(sketch, "E9.3.2.5", {"start": v(-285, -152) * mm, "end": v(-275, -152) * mm});
            skLineSegment(sketch, "E9.6.2.5", {"start": v(-285, -142) * mm, "end": v(-275, -142) * mm});
            skLineSegment(sketch, "E9.9.2.5", {"start": v(-275, -142) * mm, "end": v(-275, -152) * mm});
            skLineSegment(sketch, "E9.0.2.6", {"start": v(-285, -128) * mm, "end": v(-285, -138) * mm});
            skLineSegment(sketch, "E9.3.2.6", {"start": v(-285, -138) * mm, "end": v(-275, -138) * mm});
            skLineSegment(sketch, "E9.6.2.6", {"start": v(-285, -128) * mm, "end": v(-275, -128) * mm});
            skLineSegment(sketch, "E9.9.2.6", {"start": v(-275, -128) * mm, "end": v(-275, -138) * mm});
            skLineSegment(sketch, "E9.0.2.7", {"start": v(-285, -114) * mm, "end": v(-285, -124) * mm});
            skLineSegment(sketch, "E9.3.2.7", {"start": v(-285, -124) * mm, "end": v(-275, -124) * mm});
            skLineSegment(sketch, "E9.6.2.7", {"start": v(-285, -114) * mm, "end": v(-275, -114) * mm});
            skLineSegment(sketch, "E9.9.2.7", {"start": v(-275, -114) * mm, "end": v(-275, -124) * mm});
            skLineSegment(sketch, "E9.0.2.8", {"start": v(-285, -100) * mm, "end": v(-285, -110) * mm});
            skLineSegment(sketch, "E9.3.2.8", {"start": v(-285, -110) * mm, "end": v(-275, -110) * mm});
            skLineSegment(sketch, "E9.6.2.8", {"start": v(-285, -100) * mm, "end": v(-275, -100) * mm});
            skLineSegment(sketch, "E9.9.2.8", {"start": v(-275, -100) * mm, "end": v(-275, -110) * mm});
            skLineSegment(sketch, "E9.0.2.9", {"start": v(-285, -86) * mm, "end": v(-285, -96) * mm});
            skLineSegment(sketch, "E9.3.2.9", {"start": v(-285, -96) * mm, "end": v(-275, -96) * mm});
            skLineSegment(sketch, "E9.6.2.9", {"start": v(-285, -86) * mm, "end": v(-275, -86) * mm});
            skLineSegment(sketch, "E9.9.2.9", {"start": v(-275, -86) * mm, "end": v(-275, -96) * mm});
            skLineSegment(sketch, "E9.0.2.10", {"start": v(-285, -72) * mm, "end": v(-285, -82) * mm});
            skLineSegment(sketch, "E9.3.2.10", {"start": v(-285, -82) * mm, "end": v(-275, -82) * mm});
            skLineSegment(sketch, "E9.6.2.10", {"start": v(-285, -72) * mm, "end": v(-275, -72) * mm});
            skLineSegment(sketch, "E9.9.2.10", {"start": v(-275, -72) * mm, "end": v(-275, -82) * mm});
            skLineSegment(sketch, "E9.0.2.11", {"start": v(-285, -58) * mm, "end": v(-285, -68) * mm});
            skLineSegment(sketch, "E9.3.2.11", {"start": v(-285, -68) * mm, "end": v(-275, -68) * mm});
            skLineSegment(sketch, "E9.6.2.11", {"start": v(-285, -58) * mm, "end": v(-275, -58) * mm});
            skLineSegment(sketch, "E9.9.2.11", {"start": v(-275, -58) * mm, "end": v(-275, -68) * mm});
            skLineSegment(sketch, "E9.0.2.12", {"start": v(-285, -44) * mm, "end": v(-285, -54) * mm});
            skLineSegment(sketch, "E9.3.2.12", {"start": v(-285, -54) * mm, "end": v(-275, -54) * mm});
            skLineSegment(sketch, "E9.6.2.12", {"start": v(-285, -44) * mm, "end": v(-275, -44) * mm});
            skLineSegment(sketch, "E9.9.2.12", {"start": v(-275, -44) * mm, "end": v(-275, -54) * mm});
            skLineSegment(sketch, "E9.0.2.13", {"start": v(-285, -30) * mm, "end": v(-285, -40) * mm});
            skLineSegment(sketch, "E9.3.2.13", {"start": v(-285, -40) * mm, "end": v(-275, -40) * mm});
            skLineSegment(sketch, "E9.6.2.13", {"start": v(-285, -30) * mm, "end": v(-275, -30) * mm});
            skLineSegment(sketch, "E9.9.2.13", {"start": v(-275, -30) * mm, "end": v(-275, -40) * mm});
            skLineSegment(sketch, "E9.0.2.14", {"start": v(-285, -16) * mm, "end": v(-285, -26) * mm});
            skLineSegment(sketch, "E9.3.2.14", {"start": v(-285, -26) * mm, "end": v(-275, -26) * mm});
            skLineSegment(sketch, "E9.6.2.14", {"start": v(-285, -16) * mm, "end": v(-275, -16) * mm});
            skLineSegment(sketch, "E9.9.2.14", {"start": v(-275, -16) * mm, "end": v(-275, -26) * mm});
            skLineSegment(sketch, "E9.0.2.15", {"start": v(-285, -2) * mm, "end": v(-285, -12) * mm});
            skLineSegment(sketch, "E9.3.2.15", {"start": v(-285, -12) * mm, "end": v(-275, -12) * mm});
            skLineSegment(sketch, "E9.6.2.15", {"start": v(-285, -2) * mm, "end": v(-275, -2) * mm});
            skLineSegment(sketch, "E9.9.2.15", {"start": v(-275, -2) * mm, "end": v(-275, -12) * mm});
            skLineSegment(sketch, "E9.0.2.16", {"start": v(-285, 12) * mm, "end": v(-285, 2) * mm});
            skLineSegment(sketch, "E9.3.2.16", {"start": v(-285, 2) * mm, "end": v(-275, 2) * mm});
            skLineSegment(sketch, "E9.6.2.16", {"start": v(-285, 12) * mm, "end": v(-275, 12) * mm});
            skLineSegment(sketch, "E9.9.2.16", {"start": v(-275, 12) * mm, "end": v(-275, 2) * mm});
            skLineSegment(sketch, "E9.0.2.17", {"start": v(-285, 26) * mm, "end": v(-285, 16) * mm});
            skLineSegment(sketch, "E9.3.2.17", {"start": v(-285, 16) * mm, "end": v(-275, 16) * mm});
            skLineSegment(sketch, "E9.6.2.17", {"start": v(-285, 26) * mm, "end": v(-275, 26) * mm});
            skLineSegment(sketch, "E9.9.2.17", {"start": v(-275, 26) * mm, "end": v(-275, 16) * mm});
            skLineSegment(sketch, "E9.0.2.18", {"start": v(-285, 40) * mm, "end": v(-285, 30) * mm});
            skLineSegment(sketch, "E9.3.2.18", {"start": v(-285, 30) * mm, "end": v(-275, 30) * mm});
            skLineSegment(sketch, "E9.6.2.18", {"start": v(-285, 40) * mm, "end": v(-275, 40) * mm});
            skLineSegment(sketch, "E9.9.2.18", {"start": v(-275, 40) * mm, "end": v(-275, 30) * mm});
            skLineSegment(sketch, "E9.0.2.19", {"start": v(-285, 54) * mm, "end": v(-285, 44) * mm});
            skLineSegment(sketch, "E9.3.2.19", {"start": v(-285, 44) * mm, "end": v(-275, 44) * mm});
            skLineSegment(sketch, "E9.6.2.19", {"start": v(-285, 54) * mm, "end": v(-275, 54) * mm});
            skLineSegment(sketch, "E9.9.2.19", {"start": v(-275, 54) * mm, "end": v(-275, 44) * mm});
            skLineSegment(sketch, "E9.0.2.20", {"start": v(-285, 68) * mm, "end": v(-285, 58) * mm});
            skLineSegment(sketch, "E9.3.2.20", {"start": v(-285, 58) * mm, "end": v(-275, 58) * mm});
            skLineSegment(sketch, "E9.6.2.20", {"start": v(-285, 68) * mm, "end": v(-275, 68) * mm});
            skLineSegment(sketch, "E9.9.2.20", {"start": v(-275, 68) * mm, "end": v(-275, 58) * mm});
            skLineSegment(sketch, "E9.0.2.21", {"start": v(-285, 82) * mm, "end": v(-285, 72) * mm});
            skLineSegment(sketch, "E9.3.2.21", {"start": v(-285, 72) * mm, "end": v(-275, 72) * mm});
            skLineSegment(sketch, "E9.6.2.21", {"start": v(-285, 82) * mm, "end": v(-275, 82) * mm});
            skLineSegment(sketch, "E9.9.2.21", {"start": v(-275, 82) * mm, "end": v(-275, 72) * mm});
            skLineSegment(sketch, "E9.0.2.22", {"start": v(-285, 96) * mm, "end": v(-285, 86) * mm});
            skLineSegment(sketch, "E9.3.2.22", {"start": v(-285, 86) * mm, "end": v(-275, 86) * mm});
            skLineSegment(sketch, "E9.6.2.22", {"start": v(-285, 96) * mm, "end": v(-275, 96) * mm});
            skLineSegment(sketch, "E9.9.2.22", {"start": v(-275, 96) * mm, "end": v(-275, 86) * mm});
            skLineSegment(sketch, "E9.0.2.23", {"start": v(-285, 110) * mm, "end": v(-285, 100) * mm});
            skLineSegment(sketch, "E9.3.2.23", {"start": v(-285, 100) * mm, "end": v(-275, 100) * mm});
            skLineSegment(sketch, "E9.6.2.23", {"start": v(-285, 110) * mm, "end": v(-275, 110) * mm});
            skLineSegment(sketch, "E9.9.2.23", {"start": v(-275, 110) * mm, "end": v(-275, 100) * mm});
            skLineSegment(sketch, "E9.0.2.24", {"start": v(-285, 124) * mm, "end": v(-285, 114) * mm});
            skLineSegment(sketch, "E9.3.2.24", {"start": v(-285, 114) * mm, "end": v(-275, 114) * mm});
            skLineSegment(sketch, "E9.6.2.24", {"start": v(-285, 124) * mm, "end": v(-275, 124) * mm});
            skLineSegment(sketch, "E9.9.2.24", {"start": v(-275, 124) * mm, "end": v(-275, 114) * mm});
            skLineSegment(sketch, "E9.0.2.25", {"start": v(-285, 138) * mm, "end": v(-285, 128) * mm});
            skLineSegment(sketch, "E9.3.2.25", {"start": v(-285, 128) * mm, "end": v(-275, 128) * mm});
            skLineSegment(sketch, "E9.6.2.25", {"start": v(-285, 138) * mm, "end": v(-275, 138) * mm});
            skLineSegment(sketch, "E9.9.2.25", {"start": v(-275, 138) * mm, "end": v(-275, 128) * mm});
            skLineSegment(sketch, "E9.0.2.26", {"start": v(-285, 152) * mm, "end": v(-285, 142) * mm});
            skLineSegment(sketch, "E9.3.2.26", {"start": v(-285, 142) * mm, "end": v(-275, 142) * mm});
            skLineSegment(sketch, "E9.6.2.26", {"start": v(-285, 152) * mm, "end": v(-275, 152) * mm});
            skLineSegment(sketch, "E9.9.2.26", {"start": v(-275, 152) * mm, "end": v(-275, 142) * mm});
            skLineSegment(sketch, "E9.0.2.27", {"start": v(-285, 166) * mm, "end": v(-285, 156) * mm});
            skLineSegment(sketch, "E9.3.2.27", {"start": v(-285, 156) * mm, "end": v(-275, 156) * mm});
            skLineSegment(sketch, "E9.6.2.27", {"start": v(-285, 166) * mm, "end": v(-275, 166) * mm});
            skLineSegment(sketch, "E9.9.2.27", {"start": v(-275, 166) * mm, "end": v(-275, 156) * mm});
            skLineSegment(sketch, "E9.0.2.28", {"start": v(-285, 180) * mm, "end": v(-285, 170) * mm});
            skLineSegment(sketch, "E9.3.2.28", {"start": v(-285, 170) * mm, "end": v(-275, 170) * mm});
            skLineSegment(sketch, "E9.6.2.28", {"start": v(-285, 180) * mm, "end": v(-275, 180) * mm});
            skLineSegment(sketch, "E9.9.2.28", {"start": v(-275, 180) * mm, "end": v(-275, 170) * mm});
            skLineSegment(sketch, "E9.0.2.29", {"start": v(-285, 194) * mm, "end": v(-285, 184) * mm});
            skLineSegment(sketch, "E9.3.2.29", {"start": v(-285, 184) * mm, "end": v(-275, 184) * mm});
            skLineSegment(sketch, "E9.6.2.29", {"start": v(-285, 194) * mm, "end": v(-275, 194) * mm});
            skLineSegment(sketch, "E9.9.2.29", {"start": v(-275, 194) * mm, "end": v(-275, 184) * mm});
            skLineSegment(sketch, "E9.0.2.30", {"start": v(-285, 208) * mm, "end": v(-285, 198) * mm});
            skLineSegment(sketch, "E9.3.2.30", {"start": v(-285, 198) * mm, "end": v(-275, 198) * mm});
            skLineSegment(sketch, "E9.6.2.30", {"start": v(-285, 208) * mm, "end": v(-275, 208) * mm});
            skLineSegment(sketch, "E9.9.2.30", {"start": v(-275, 208) * mm, "end": v(-275, 198) * mm});
            skLineSegment(sketch, "E9.0.2.31", {"start": v(-285, 222) * mm, "end": v(-285, 212) * mm});
            skLineSegment(sketch, "E9.3.2.31", {"start": v(-285, 212) * mm, "end": v(-275, 212) * mm});
            skLineSegment(sketch, "E9.6.2.31", {"start": v(-285, 222) * mm, "end": v(-275, 222) * mm});
            skLineSegment(sketch, "E9.9.2.31", {"start": v(-275, 222) * mm, "end": v(-275, 212) * mm});
            skLineSegment(sketch, "E9.0.3.0", {"start": v(-271, -212) * mm, "end": v(-271, -222) * mm});
            skLineSegment(sketch, "E9.3.3.0", {"start": v(-271, -222) * mm, "end": v(-261, -222) * mm});
            skLineSegment(sketch, "E9.6.3.0", {"start": v(-271, -212) * mm, "end": v(-261, -212) * mm});
            skLineSegment(sketch, "E9.9.3.0", {"start": v(-261, -212) * mm, "end": v(-261, -222) * mm});
            skLineSegment(sketch, "E9.0.3.1", {"start": v(-271, -198) * mm, "end": v(-271, -208) * mm});
            skLineSegment(sketch, "E9.3.3.1", {"start": v(-271, -208) * mm, "end": v(-261, -208) * mm});
            skLineSegment(sketch, "E9.6.3.1", {"start": v(-271, -198) * mm, "end": v(-261, -198) * mm});
            skLineSegment(sketch, "E9.9.3.1", {"start": v(-261, -198) * mm, "end": v(-261, -208) * mm});
            skLineSegment(sketch, "E9.0.3.2", {"start": v(-271, -184) * mm, "end": v(-271, -194) * mm});
            skLineSegment(sketch, "E9.3.3.2", {"start": v(-271, -194) * mm, "end": v(-261, -194) * mm});
            skLineSegment(sketch, "E9.6.3.2", {"start": v(-271, -184) * mm, "end": v(-261, -184) * mm});
            skLineSegment(sketch, "E9.9.3.2", {"start": v(-261, -184) * mm, "end": v(-261, -194) * mm});
            skLineSegment(sketch, "E9.0.3.3", {"start": v(-271, -170) * mm, "end": v(-271, -180) * mm});
            skLineSegment(sketch, "E9.3.3.3", {"start": v(-271, -180) * mm, "end": v(-261, -180) * mm});
            skLineSegment(sketch, "E9.6.3.3", {"start": v(-271, -170) * mm, "end": v(-261, -170) * mm});
            skLineSegment(sketch, "E9.9.3.3", {"start": v(-261, -170) * mm, "end": v(-261, -180) * mm});
            skLineSegment(sketch, "E9.0.3.4", {"start": v(-271, -156) * mm, "end": v(-271, -166) * mm});
            skLineSegment(sketch, "E9.3.3.4", {"start": v(-271, -166) * mm, "end": v(-261, -166) * mm});
            skLineSegment(sketch, "E9.6.3.4", {"start": v(-271, -156) * mm, "end": v(-261, -156) * mm});
            skLineSegment(sketch, "E9.9.3.4", {"start": v(-261, -156) * mm, "end": v(-261, -166) * mm});
            skLineSegment(sketch, "E9.0.3.5", {"start": v(-271, -142) * mm, "end": v(-271, -152) * mm});
            skLineSegment(sketch, "E9.3.3.5", {"start": v(-271, -152) * mm, "end": v(-261, -152) * mm});
            skLineSegment(sketch, "E9.6.3.5", {"start": v(-271, -142) * mm, "end": v(-261, -142) * mm});
            skLineSegment(sketch, "E9.9.3.5", {"start": v(-261, -142) * mm, "end": v(-261, -152) * mm});
            skLineSegment(sketch, "E9.0.3.6", {"start": v(-271, -128) * mm, "end": v(-271, -138) * mm});
            skLineSegment(sketch, "E9.3.3.6", {"start": v(-271, -138) * mm, "end": v(-261, -138) * mm});
            skLineSegment(sketch, "E9.6.3.6", {"start": v(-271, -128) * mm, "end": v(-261, -128) * mm});
            skLineSegment(sketch, "E9.9.3.6", {"start": v(-261, -128) * mm, "end": v(-261, -138) * mm});
            skLineSegment(sketch, "E9.0.3.7", {"start": v(-271, -114) * mm, "end": v(-271, -124) * mm});
            skLineSegment(sketch, "E9.3.3.7", {"start": v(-271, -124) * mm, "end": v(-261, -124) * mm});
            skLineSegment(sketch, "E9.6.3.7", {"start": v(-271, -114) * mm, "end": v(-261, -114) * mm});
            skLineSegment(sketch, "E9.9.3.7", {"start": v(-261, -114) * mm, "end": v(-261, -124) * mm});
            skLineSegment(sketch, "E9.0.3.8", {"start": v(-271, -100) * mm, "end": v(-271, -110) * mm});
            skLineSegment(sketch, "E9.3.3.8", {"start": v(-271, -110) * mm, "end": v(-261, -110) * mm});
            skLineSegment(sketch, "E9.6.3.8", {"start": v(-271, -100) * mm, "end": v(-261, -100) * mm});
            skLineSegment(sketch, "E9.9.3.8", {"start": v(-261, -100) * mm, "end": v(-261, -110) * mm});
            skLineSegment(sketch, "E9.0.3.9", {"start": v(-271, -86) * mm, "end": v(-271, -96) * mm});
            skLineSegment(sketch, "E9.3.3.9", {"start": v(-271, -96) * mm, "end": v(-261, -96) * mm});
            skLineSegment(sketch, "E9.6.3.9", {"start": v(-271, -86) * mm, "end": v(-261, -86) * mm});
            skLineSegment(sketch, "E9.9.3.9", {"start": v(-261, -86) * mm, "end": v(-261, -96) * mm});
            skLineSegment(sketch, "E9.0.3.10", {"start": v(-271, -72) * mm, "end": v(-271, -82) * mm});
            skLineSegment(sketch, "E9.3.3.10", {"start": v(-271, -82) * mm, "end": v(-261, -82) * mm});
            skLineSegment(sketch, "E9.6.3.10", {"start": v(-271, -72) * mm, "end": v(-261, -72) * mm});
            skLineSegment(sketch, "E9.9.3.10", {"start": v(-261, -72) * mm, "end": v(-261, -82) * mm});
            skLineSegment(sketch, "E9.0.3.11", {"start": v(-271, -58) * mm, "end": v(-271, -68) * mm});
            skLineSegment(sketch, "E9.3.3.11", {"start": v(-271, -68) * mm, "end": v(-261, -68) * mm});
            skLineSegment(sketch, "E9.6.3.11", {"start": v(-271, -58) * mm, "end": v(-261, -58) * mm});
            skLineSegment(sketch, "E9.9.3.11", {"start": v(-261, -58) * mm, "end": v(-261, -68) * mm});
            skLineSegment(sketch, "E9.0.3.12", {"start": v(-271, -44) * mm, "end": v(-271, -54) * mm});
            skLineSegment(sketch, "E9.3.3.12", {"start": v(-271, -54) * mm, "end": v(-261, -54) * mm});
            skLineSegment(sketch, "E9.6.3.12", {"start": v(-271, -44) * mm, "end": v(-261, -44) * mm});
            skLineSegment(sketch, "E9.9.3.12", {"start": v(-261, -44) * mm, "end": v(-261, -54) * mm});
            skLineSegment(sketch, "E9.0.3.13", {"start": v(-271, -30) * mm, "end": v(-271, -40) * mm});
            skLineSegment(sketch, "E9.3.3.13", {"start": v(-271, -40) * mm, "end": v(-261, -40) * mm});
            skLineSegment(sketch, "E9.6.3.13", {"start": v(-271, -30) * mm, "end": v(-261, -30) * mm});
            skLineSegment(sketch, "E9.9.3.13", {"start": v(-261, -30) * mm, "end": v(-261, -40) * mm});
            skLineSegment(sketch, "E9.0.3.14", {"start": v(-271, -16) * mm, "end": v(-271, -26) * mm});
            skLineSegment(sketch, "E9.3.3.14", {"start": v(-271, -26) * mm, "end": v(-261, -26) * mm});
            skLineSegment(sketch, "E9.6.3.14", {"start": v(-271, -16) * mm, "end": v(-261, -16) * mm});
            skLineSegment(sketch, "E9.9.3.14", {"start": v(-261, -16) * mm, "end": v(-261, -26) * mm});
            skLineSegment(sketch, "E9.0.3.15", {"start": v(-271, -2) * mm, "end": v(-271, -12) * mm});
            skLineSegment(sketch, "E9.3.3.15", {"start": v(-271, -12) * mm, "end": v(-261, -12) * mm});
            skLineSegment(sketch, "E9.6.3.15", {"start": v(-271, -2) * mm, "end": v(-261, -2) * mm});
            skLineSegment(sketch, "E9.9.3.15", {"start": v(-261, -2) * mm, "end": v(-261, -12) * mm});
            skLineSegment(sketch, "E9.0.3.16", {"start": v(-271, 12) * mm, "end": v(-271, 2) * mm});
            skLineSegment(sketch, "E9.3.3.16", {"start": v(-271, 2) * mm, "end": v(-261, 2) * mm});
            skLineSegment(sketch, "E9.6.3.16", {"start": v(-271, 12) * mm, "end": v(-261, 12) * mm});
            skLineSegment(sketch, "E9.9.3.16", {"start": v(-261, 12) * mm, "end": v(-261, 2) * mm});
            skLineSegment(sketch, "E9.0.3.17", {"start": v(-271, 26) * mm, "end": v(-271, 16) * mm});
            skLineSegment(sketch, "E9.3.3.17", {"start": v(-271, 16) * mm, "end": v(-261, 16) * mm});
            skLineSegment(sketch, "E9.6.3.17", {"start": v(-271, 26) * mm, "end": v(-261, 26) * mm});
            skLineSegment(sketch, "E9.9.3.17", {"start": v(-261, 26) * mm, "end": v(-261, 16) * mm});
            skLineSegment(sketch, "E9.0.3.18", {"start": v(-271, 40) * mm, "end": v(-271, 30) * mm});
            skLineSegment(sketch, "E9.3.3.18", {"start": v(-271, 30) * mm, "end": v(-261, 30) * mm});
            skLineSegment(sketch, "E9.6.3.18", {"start": v(-271, 40) * mm, "end": v(-261, 40) * mm});
            skLineSegment(sketch, "E9.9.3.18", {"start": v(-261, 40) * mm, "end": v(-261, 30) * mm});
            skLineSegment(sketch, "E9.0.3.19", {"start": v(-271, 54) * mm, "end": v(-271, 44) * mm});
            skLineSegment(sketch, "E9.3.3.19", {"start": v(-271, 44) * mm, "end": v(-261, 44) * mm});
            skLineSegment(sketch, "E9.6.3.19", {"start": v(-271, 54) * mm, "end": v(-261, 54) * mm});
            skLineSegment(sketch, "E9.9.3.19", {"start": v(-261, 54) * mm, "end": v(-261, 44) * mm});
            skLineSegment(sketch, "E9.0.3.20", {"start": v(-271, 68) * mm, "end": v(-271, 58) * mm});
            skLineSegment(sketch, "E9.3.3.20", {"start": v(-271, 58) * mm, "end": v(-261, 58) * mm});
            skLineSegment(sketch, "E9.6.3.20", {"start": v(-271, 68) * mm, "end": v(-261, 68) * mm});
            skLineSegment(sketch, "E9.9.3.20", {"start": v(-261, 68) * mm, "end": v(-261, 58) * mm});
            skLineSegment(sketch, "E9.0.3.21", {"start": v(-271, 82) * mm, "end": v(-271, 72) * mm});
            skLineSegment(sketch, "E9.3.3.21", {"start": v(-271, 72) * mm, "end": v(-261, 72) * mm});
            skLineSegment(sketch, "E9.6.3.21", {"start": v(-271, 82) * mm, "end": v(-261, 82) * mm});
            skLineSegment(sketch, "E9.9.3.21", {"start": v(-261, 82) * mm, "end": v(-261, 72) * mm});
            skLineSegment(sketch, "E9.0.3.22", {"start": v(-271, 96) * mm, "end": v(-271, 86) * mm});
            skLineSegment(sketch, "E9.3.3.22", {"start": v(-271, 86) * mm, "end": v(-261, 86) * mm});
            skLineSegment(sketch, "E9.6.3.22", {"start": v(-271, 96) * mm, "end": v(-261, 96) * mm});
            skLineSegment(sketch, "E9.9.3.22", {"start": v(-261, 96) * mm, "end": v(-261, 86) * mm});
            skLineSegment(sketch, "E9.0.3.23", {"start": v(-271, 110) * mm, "end": v(-271, 100) * mm});
            skLineSegment(sketch, "E9.3.3.23", {"start": v(-271, 100) * mm, "end": v(-261, 100) * mm});
            skLineSegment(sketch, "E9.6.3.23", {"start": v(-271, 110) * mm, "end": v(-261, 110) * mm});
            skLineSegment(sketch, "E9.9.3.23", {"start": v(-261, 110) * mm, "end": v(-261, 100) * mm});
            skLineSegment(sketch, "E9.0.3.24", {"start": v(-271, 124) * mm, "end": v(-271, 114) * mm});
            skLineSegment(sketch, "E9.3.3.24", {"start": v(-271, 114) * mm, "end": v(-261, 114) * mm});
            skLineSegment(sketch, "E9.6.3.24", {"start": v(-271, 124) * mm, "end": v(-261, 124) * mm});
            skLineSegment(sketch, "E9.9.3.24", {"start": v(-261, 124) * mm, "end": v(-261, 114) * mm});
            skLineSegment(sketch, "E9.0.3.25", {"start": v(-271, 138) * mm, "end": v(-271, 128) * mm});
            skLineSegment(sketch, "E9.3.3.25", {"start": v(-271, 128) * mm, "end": v(-261, 128) * mm});
            skLineSegment(sketch, "E9.6.3.25", {"start": v(-271, 138) * mm, "end": v(-261, 138) * mm});
            skLineSegment(sketch, "E9.9.3.25", {"start": v(-261, 138) * mm, "end": v(-261, 128) * mm});
            skLineSegment(sketch, "E9.0.3.26", {"start": v(-271, 152) * mm, "end": v(-271, 142) * mm});
            skLineSegment(sketch, "E9.3.3.26", {"start": v(-271, 142) * mm, "end": v(-261, 142) * mm});
            skLineSegment(sketch, "E9.6.3.26", {"start": v(-271, 152) * mm, "end": v(-261, 152) * mm});
            skLineSegment(sketch, "E9.9.3.26", {"start": v(-261, 152) * mm, "end": v(-261, 142) * mm});
            skLineSegment(sketch, "E9.0.3.27", {"start": v(-271, 166) * mm, "end": v(-271, 156) * mm});
            skLineSegment(sketch, "E9.3.3.27", {"start": v(-271, 156) * mm, "end": v(-261, 156) * mm});
            skLineSegment(sketch, "E9.6.3.27", {"start": v(-271, 166) * mm, "end": v(-261, 166) * mm});
            skLineSegment(sketch, "E9.9.3.27", {"start": v(-261, 166) * mm, "end": v(-261, 156) * mm});
            skLineSegment(sketch, "E9.0.3.28", {"start": v(-271, 180) * mm, "end": v(-271, 170) * mm});
            skLineSegment(sketch, "E9.3.3.28", {"start": v(-271, 170) * mm, "end": v(-261, 170) * mm});
            skLineSegment(sketch, "E9.6.3.28", {"start": v(-271, 180) * mm, "end": v(-261, 180) * mm});
            skLineSegment(sketch, "E9.9.3.28", {"start": v(-261, 180) * mm, "end": v(-261, 170) * mm});
            skLineSegment(sketch, "E9.0.3.29", {"start": v(-271, 194) * mm, "end": v(-271, 184) * mm});
            skLineSegment(sketch, "E9.3.3.29", {"start": v(-271, 184) * mm, "end": v(-261, 184) * mm});
            skLineSegment(sketch, "E9.6.3.29", {"start": v(-271, 194) * mm, "end": v(-261, 194) * mm});
            skLineSegment(sketch, "E9.9.3.29", {"start": v(-261, 194) * mm, "end": v(-261, 184) * mm});
            skLineSegment(sketch, "E9.0.3.30", {"start": v(-271, 208) * mm, "end": v(-271, 198) * mm});
            skLineSegment(sketch, "E9.3.3.30", {"start": v(-271, 198) * mm, "end": v(-261, 198) * mm});
            skLineSegment(sketch, "E9.6.3.30", {"start": v(-271, 208) * mm, "end": v(-261, 208) * mm});
            skLineSegment(sketch, "E9.9.3.30", {"start": v(-261, 208) * mm, "end": v(-261, 198) * mm});
            skLineSegment(sketch, "E9.0.3.31", {"start": v(-271, 222) * mm, "end": v(-271, 212) * mm});
            skLineSegment(sketch, "E9.3.3.31", {"start": v(-271, 212) * mm, "end": v(-261, 212) * mm});
            skLineSegment(sketch, "E9.6.3.31", {"start": v(-271, 222) * mm, "end": v(-261, 222) * mm});
            skLineSegment(sketch, "E9.9.3.31", {"start": v(-261, 222) * mm, "end": v(-261, 212) * mm});
            skLineSegment(sketch, "E9.0.4.0", {"start": v(-257, -212) * mm, "end": v(-257, -222) * mm});
            skLineSegment(sketch, "E9.3.4.0", {"start": v(-257, -222) * mm, "end": v(-247, -222) * mm});
            skLineSegment(sketch, "E9.6.4.0", {"start": v(-257, -212) * mm, "end": v(-247, -212) * mm});
            skLineSegment(sketch, "E9.9.4.0", {"start": v(-247, -212) * mm, "end": v(-247, -222) * mm});
            skLineSegment(sketch, "E9.0.4.1", {"start": v(-257, -198) * mm, "end": v(-257, -208) * mm});
            skLineSegment(sketch, "E9.3.4.1", {"start": v(-257, -208) * mm, "end": v(-247, -208) * mm});
            skLineSegment(sketch, "E9.6.4.1", {"start": v(-257, -198) * mm, "end": v(-247, -198) * mm});
            skLineSegment(sketch, "E9.9.4.1", {"start": v(-247, -198) * mm, "end": v(-247, -208) * mm});
            skLineSegment(sketch, "E9.0.4.2", {"start": v(-257, -184) * mm, "end": v(-257, -194) * mm});
            skLineSegment(sketch, "E9.3.4.2", {"start": v(-257, -194) * mm, "end": v(-247, -194) * mm});
            skLineSegment(sketch, "E9.6.4.2", {"start": v(-257, -184) * mm, "end": v(-247, -184) * mm});
            skLineSegment(sketch, "E9.9.4.2", {"start": v(-247, -184) * mm, "end": v(-247, -194) * mm});
            skLineSegment(sketch, "E9.0.4.3", {"start": v(-257, -170) * mm, "end": v(-257, -180) * mm});
            skLineSegment(sketch, "E9.3.4.3", {"start": v(-257, -180) * mm, "end": v(-247, -180) * mm});
            skLineSegment(sketch, "E9.6.4.3", {"start": v(-257, -170) * mm, "end": v(-247, -170) * mm});
            skLineSegment(sketch, "E9.9.4.3", {"start": v(-247, -170) * mm, "end": v(-247, -180) * mm});
            skLineSegment(sketch, "E9.0.4.4", {"start": v(-257, -156) * mm, "end": v(-257, -166) * mm});
            skLineSegment(sketch, "E9.3.4.4", {"start": v(-257, -166) * mm, "end": v(-247, -166) * mm});
            skLineSegment(sketch, "E9.6.4.4", {"start": v(-257, -156) * mm, "end": v(-247, -156) * mm});
            skLineSegment(sketch, "E9.9.4.4", {"start": v(-247, -156) * mm, "end": v(-247, -166) * mm});
            skLineSegment(sketch, "E9.0.4.5", {"start": v(-257, -142) * mm, "end": v(-257, -152) * mm});
            skLineSegment(sketch, "E9.3.4.5", {"start": v(-257, -152) * mm, "end": v(-247, -152) * mm});
            skLineSegment(sketch, "E9.6.4.5", {"start": v(-257, -142) * mm, "end": v(-247, -142) * mm});
            skLineSegment(sketch, "E9.9.4.5", {"start": v(-247, -142) * mm, "end": v(-247, -152) * mm});
            skLineSegment(sketch, "E9.0.4.6", {"start": v(-257, -128) * mm, "end": v(-257, -138) * mm});
            skLineSegment(sketch, "E9.3.4.6", {"start": v(-257, -138) * mm, "end": v(-247, -138) * mm});
            skLineSegment(sketch, "E9.6.4.6", {"start": v(-257, -128) * mm, "end": v(-247, -128) * mm});
            skLineSegment(sketch, "E9.9.4.6", {"start": v(-247, -128) * mm, "end": v(-247, -138) * mm});
            skLineSegment(sketch, "E9.0.4.7", {"start": v(-257, -114) * mm, "end": v(-257, -124) * mm});
            skLineSegment(sketch, "E9.3.4.7", {"start": v(-257, -124) * mm, "end": v(-247, -124) * mm});
            skLineSegment(sketch, "E9.6.4.7", {"start": v(-257, -114) * mm, "end": v(-247, -114) * mm});
            skLineSegment(sketch, "E9.9.4.7", {"start": v(-247, -114) * mm, "end": v(-247, -124) * mm});
            skLineSegment(sketch, "E9.0.4.8", {"start": v(-257, -100) * mm, "end": v(-257, -110) * mm});
            skLineSegment(sketch, "E9.3.4.8", {"start": v(-257, -110) * mm, "end": v(-247, -110) * mm});
            skLineSegment(sketch, "E9.6.4.8", {"start": v(-257, -100) * mm, "end": v(-247, -100) * mm});
            skLineSegment(sketch, "E9.9.4.8", {"start": v(-247, -100) * mm, "end": v(-247, -110) * mm});
            skLineSegment(sketch, "E9.0.4.9", {"start": v(-257, -86) * mm, "end": v(-257, -96) * mm});
            skLineSegment(sketch, "E9.3.4.9", {"start": v(-257, -96) * mm, "end": v(-247, -96) * mm});
            skLineSegment(sketch, "E9.6.4.9", {"start": v(-257, -86) * mm, "end": v(-247, -86) * mm});
            skLineSegment(sketch, "E9.9.4.9", {"start": v(-247, -86) * mm, "end": v(-247, -96) * mm});
            skLineSegment(sketch, "E9.0.4.10", {"start": v(-257, -72) * mm, "end": v(-257, -82) * mm});
            skLineSegment(sketch, "E9.3.4.10", {"start": v(-257, -82) * mm, "end": v(-247, -82) * mm});
            skLineSegment(sketch, "E9.6.4.10", {"start": v(-257, -72) * mm, "end": v(-247, -72) * mm});
            skLineSegment(sketch, "E9.9.4.10", {"start": v(-247, -72) * mm, "end": v(-247, -82) * mm});
            skLineSegment(sketch, "E9.0.4.11", {"start": v(-257, -58) * mm, "end": v(-257, -68) * mm});
            skLineSegment(sketch, "E9.3.4.11", {"start": v(-257, -68) * mm, "end": v(-247, -68) * mm});
            skLineSegment(sketch, "E9.6.4.11", {"start": v(-257, -58) * mm, "end": v(-247, -58) * mm});
            skLineSegment(sketch, "E9.9.4.11", {"start": v(-247, -58) * mm, "end": v(-247, -68) * mm});
            skLineSegment(sketch, "E9.0.4.12", {"start": v(-257, -44) * mm, "end": v(-257, -54) * mm});
            skLineSegment(sketch, "E9.3.4.12", {"start": v(-257, -54) * mm, "end": v(-247, -54) * mm});
            skLineSegment(sketch, "E9.6.4.12", {"start": v(-257, -44) * mm, "end": v(-247, -44) * mm});
            skLineSegment(sketch, "E9.9.4.12", {"start": v(-247, -44) * mm, "end": v(-247, -54) * mm});
            skLineSegment(sketch, "E9.0.4.13", {"start": v(-257, -30) * mm, "end": v(-257, -40) * mm});
            skLineSegment(sketch, "E9.3.4.13", {"start": v(-257, -40) * mm, "end": v(-247, -40) * mm});
            skLineSegment(sketch, "E9.6.4.13", {"start": v(-257, -30) * mm, "end": v(-247, -30) * mm});
            skLineSegment(sketch, "E9.9.4.13", {"start": v(-247, -30) * mm, "end": v(-247, -40) * mm});
            skLineSegment(sketch, "E9.0.4.14", {"start": v(-257, -16) * mm, "end": v(-257, -26) * mm});
            skLineSegment(sketch, "E9.3.4.14", {"start": v(-257, -26) * mm, "end": v(-247, -26) * mm});
            skLineSegment(sketch, "E9.6.4.14", {"start": v(-257, -16) * mm, "end": v(-247, -16) * mm});
            skLineSegment(sketch, "E9.9.4.14", {"start": v(-247, -16) * mm, "end": v(-247, -26) * mm});
            skLineSegment(sketch, "E9.0.4.15", {"start": v(-257, -2) * mm, "end": v(-257, -12) * mm});
            skLineSegment(sketch, "E9.3.4.15", {"start": v(-257, -12) * mm, "end": v(-247, -12) * mm});
            skLineSegment(sketch, "E9.6.4.15", {"start": v(-257, -2) * mm, "end": v(-247, -2) * mm});
            skLineSegment(sketch, "E9.9.4.15", {"start": v(-247, -2) * mm, "end": v(-247, -12) * mm});
            skLineSegment(sketch, "E9.0.4.16", {"start": v(-257, 12) * mm, "end": v(-257, 2) * mm});
            skLineSegment(sketch, "E9.3.4.16", {"start": v(-257, 2) * mm, "end": v(-247, 2) * mm});
            skLineSegment(sketch, "E9.6.4.16", {"start": v(-257, 12) * mm, "end": v(-247, 12) * mm});
            skLineSegment(sketch, "E9.9.4.16", {"start": v(-247, 12) * mm, "end": v(-247, 2) * mm});
            skLineSegment(sketch, "E9.0.4.17", {"start": v(-257, 26) * mm, "end": v(-257, 16) * mm});
            skLineSegment(sketch, "E9.3.4.17", {"start": v(-257, 16) * mm, "end": v(-247, 16) * mm});
            skLineSegment(sketch, "E9.6.4.17", {"start": v(-257, 26) * mm, "end": v(-247, 26) * mm});
            skLineSegment(sketch, "E9.9.4.17", {"start": v(-247, 26) * mm, "end": v(-247, 16) * mm});
            skLineSegment(sketch, "E9.0.4.18", {"start": v(-257, 40) * mm, "end": v(-257, 30) * mm});
            skLineSegment(sketch, "E9.3.4.18", {"start": v(-257, 30) * mm, "end": v(-247, 30) * mm});
            skLineSegment(sketch, "E9.6.4.18", {"start": v(-257, 40) * mm, "end": v(-247, 40) * mm});
            skLineSegment(sketch, "E9.9.4.18", {"start": v(-247, 40) * mm, "end": v(-247, 30) * mm});
            skLineSegment(sketch, "E9.0.4.19", {"start": v(-257, 54) * mm, "end": v(-257, 44) * mm});
            skLineSegment(sketch, "E9.3.4.19", {"start": v(-257, 44) * mm, "end": v(-247, 44) * mm});
            skLineSegment(sketch, "E9.6.4.19", {"start": v(-257, 54) * mm, "end": v(-247, 54) * mm});
            skLineSegment(sketch, "E9.9.4.19", {"start": v(-247, 54) * mm, "end": v(-247, 44) * mm});
            skLineSegment(sketch, "E9.0.4.20", {"start": v(-257, 68) * mm, "end": v(-257, 58) * mm});
            skLineSegment(sketch, "E9.3.4.20", {"start": v(-257, 58) * mm, "end": v(-247, 58) * mm});
            skLineSegment(sketch, "E9.6.4.20", {"start": v(-257, 68) * mm, "end": v(-247, 68) * mm});
            skLineSegment(sketch, "E9.9.4.20", {"start": v(-247, 68) * mm, "end": v(-247, 58) * mm});
            skLineSegment(sketch, "E9.0.4.21", {"start": v(-257, 82) * mm, "end": v(-257, 72) * mm});
            skLineSegment(sketch, "E9.3.4.21", {"start": v(-257, 72) * mm, "end": v(-247, 72) * mm});
            skLineSegment(sketch, "E9.6.4.21", {"start": v(-257, 82) * mm, "end": v(-247, 82) * mm});
            skLineSegment(sketch, "E9.9.4.21", {"start": v(-247, 82) * mm, "end": v(-247, 72) * mm});
            skLineSegment(sketch, "E9.0.4.22", {"start": v(-257, 96) * mm, "end": v(-257, 86) * mm});
            skLineSegment(sketch, "E9.3.4.22", {"start": v(-257, 86) * mm, "end": v(-247, 86) * mm});
            skLineSegment(sketch, "E9.6.4.22", {"start": v(-257, 96) * mm, "end": v(-247, 96) * mm});
            skLineSegment(sketch, "E9.9.4.22", {"start": v(-247, 96) * mm, "end": v(-247, 86) * mm});
            skLineSegment(sketch, "E9.0.4.23", {"start": v(-257, 110) * mm, "end": v(-257, 100) * mm});
            skLineSegment(sketch, "E9.3.4.23", {"start": v(-257, 100) * mm, "end": v(-247, 100) * mm});
            skLineSegment(sketch, "E9.6.4.23", {"start": v(-257, 110) * mm, "end": v(-247, 110) * mm});
            skLineSegment(sketch, "E9.9.4.23", {"start": v(-247, 110) * mm, "end": v(-247, 100) * mm});
            skLineSegment(sketch, "E9.0.4.24", {"start": v(-257, 124) * mm, "end": v(-257, 114) * mm});
            skLineSegment(sketch, "E9.3.4.24", {"start": v(-257, 114) * mm, "end": v(-247, 114) * mm});
            skLineSegment(sketch, "E9.6.4.24", {"start": v(-257, 124) * mm, "end": v(-247, 124) * mm});
            skLineSegment(sketch, "E9.9.4.24", {"start": v(-247, 124) * mm, "end": v(-247, 114) * mm});
            skLineSegment(sketch, "E9.0.4.25", {"start": v(-257, 138) * mm, "end": v(-257, 128) * mm});
            skLineSegment(sketch, "E9.3.4.25", {"start": v(-257, 128) * mm, "end": v(-247, 128) * mm});
            skLineSegment(sketch, "E9.6.4.25", {"start": v(-257, 138) * mm, "end": v(-247, 138) * mm});
            skLineSegment(sketch, "E9.9.4.25", {"start": v(-247, 138) * mm, "end": v(-247, 128) * mm});
            skLineSegment(sketch, "E9.0.4.26", {"start": v(-257, 152) * mm, "end": v(-257, 142) * mm});
            skLineSegment(sketch, "E9.3.4.26", {"start": v(-257, 142) * mm, "end": v(-247, 142) * mm});
            skLineSegment(sketch, "E9.6.4.26", {"start": v(-257, 152) * mm, "end": v(-247, 152) * mm});
            skLineSegment(sketch, "E9.9.4.26", {"start": v(-247, 152) * mm, "end": v(-247, 142) * mm});
            skLineSegment(sketch, "E9.0.4.27", {"start": v(-257, 166) * mm, "end": v(-257, 156) * mm});
            skLineSegment(sketch, "E9.3.4.27", {"start": v(-257, 156) * mm, "end": v(-247, 156) * mm});
            skLineSegment(sketch, "E9.6.4.27", {"start": v(-257, 166) * mm, "end": v(-247, 166) * mm});
            skLineSegment(sketch, "E9.9.4.27", {"start": v(-247, 166) * mm, "end": v(-247, 156) * mm});
            skLineSegment(sketch, "E9.0.4.28", {"start": v(-257, 180) * mm, "end": v(-257, 170) * mm});
            skLineSegment(sketch, "E9.3.4.28", {"start": v(-257, 170) * mm, "end": v(-247, 170) * mm});
            skLineSegment(sketch, "E9.6.4.28", {"start": v(-257, 180) * mm, "end": v(-247, 180) * mm});
            skLineSegment(sketch, "E9.9.4.28", {"start": v(-247, 180) * mm, "end": v(-247, 170) * mm});
            skLineSegment(sketch, "E9.0.4.29", {"start": v(-257, 194) * mm, "end": v(-257, 184) * mm});
            skLineSegment(sketch, "E9.3.4.29", {"start": v(-257, 184) * mm, "end": v(-247, 184) * mm});
            skLineSegment(sketch, "E9.6.4.29", {"start": v(-257, 194) * mm, "end": v(-247, 194) * mm});
            skLineSegment(sketch, "E9.9.4.29", {"start": v(-247, 194) * mm, "end": v(-247, 184) * mm});
            skLineSegment(sketch, "E9.0.4.30", {"start": v(-257, 208) * mm, "end": v(-257, 198) * mm});
            skLineSegment(sketch, "E9.3.4.30", {"start": v(-257, 198) * mm, "end": v(-247, 198) * mm});
            skLineSegment(sketch, "E9.6.4.30", {"start": v(-257, 208) * mm, "end": v(-247, 208) * mm});
            skLineSegment(sketch, "E9.9.4.30", {"start": v(-247, 208) * mm, "end": v(-247, 198) * mm});
            skLineSegment(sketch, "E9.0.4.31", {"start": v(-257, 222) * mm, "end": v(-257, 212) * mm});
            skLineSegment(sketch, "E9.3.4.31", {"start": v(-257, 212) * mm, "end": v(-247, 212) * mm});
            skLineSegment(sketch, "E9.6.4.31", {"start": v(-257, 222) * mm, "end": v(-247, 222) * mm});
            skLineSegment(sketch, "E9.9.4.31", {"start": v(-247, 222) * mm, "end": v(-247, 212) * mm});
            skLineSegment(sketch, "E10.0.5.0", {"start": v(-243, -212) * mm, "end": v(-243, -222) * mm});
            skLineSegment(sketch, "E10.3.5.0", {"start": v(-243, -222) * mm, "end": v(-233, -222) * mm});
            skLineSegment(sketch, "E10.6.5.0", {"start": v(-243, -212) * mm, "end": v(-233, -212) * mm});
            skLineSegment(sketch, "E10.9.5.0", {"start": v(-233, -212) * mm, "end": v(-233, -222) * mm});
            skLineSegment(sketch, "E10.0.5.1", {"start": v(-243, -198) * mm, "end": v(-243, -208) * mm});
            skLineSegment(sketch, "E10.3.5.1", {"start": v(-243, -208) * mm, "end": v(-233, -208) * mm});
            skLineSegment(sketch, "E10.6.5.1", {"start": v(-243, -198) * mm, "end": v(-233, -198) * mm});
            skLineSegment(sketch, "E10.9.5.1", {"start": v(-233, -198) * mm, "end": v(-233, -208) * mm});
            skLineSegment(sketch, "E10.0.5.2", {"start": v(-243, -184) * mm, "end": v(-243, -194) * mm});
            skLineSegment(sketch, "E10.3.5.2", {"start": v(-243, -194) * mm, "end": v(-233, -194) * mm});
            skLineSegment(sketch, "E10.6.5.2", {"start": v(-243, -184) * mm, "end": v(-233, -184) * mm});
            skLineSegment(sketch, "E10.9.5.2", {"start": v(-233, -184) * mm, "end": v(-233, -194) * mm});
            skLineSegment(sketch, "E10.0.5.3", {"start": v(-243, -170) * mm, "end": v(-243, -180) * mm});
            skLineSegment(sketch, "E10.3.5.3", {"start": v(-243, -180) * mm, "end": v(-233, -180) * mm});
            skLineSegment(sketch, "E10.6.5.3", {"start": v(-243, -170) * mm, "end": v(-233, -170) * mm});
            skLineSegment(sketch, "E10.9.5.3", {"start": v(-233, -170) * mm, "end": v(-233, -180) * mm});
            skLineSegment(sketch, "E10.0.5.4", {"start": v(-243, -156) * mm, "end": v(-243, -166) * mm});
            skLineSegment(sketch, "E10.3.5.4", {"start": v(-243, -166) * mm, "end": v(-233, -166) * mm});
            skLineSegment(sketch, "E10.6.5.4", {"start": v(-243, -156) * mm, "end": v(-233, -156) * mm});
            skLineSegment(sketch, "E10.9.5.4", {"start": v(-233, -156) * mm, "end": v(-233, -166) * mm});
            skLineSegment(sketch, "E10.0.5.5", {"start": v(-243, -142) * mm, "end": v(-243, -152) * mm});
            skLineSegment(sketch, "E10.3.5.5", {"start": v(-243, -152) * mm, "end": v(-233, -152) * mm});
            skLineSegment(sketch, "E10.6.5.5", {"start": v(-243, -142) * mm, "end": v(-233, -142) * mm});
            skLineSegment(sketch, "E10.9.5.5", {"start": v(-233, -142) * mm, "end": v(-233, -152) * mm});
            skLineSegment(sketch, "E10.0.5.6", {"start": v(-243, -128) * mm, "end": v(-243, -138) * mm});
            skLineSegment(sketch, "E10.3.5.6", {"start": v(-243, -138) * mm, "end": v(-233, -138) * mm});
            skLineSegment(sketch, "E10.6.5.6", {"start": v(-243, -128) * mm, "end": v(-233, -128) * mm});
            skLineSegment(sketch, "E10.9.5.6", {"start": v(-233, -128) * mm, "end": v(-233, -138) * mm});
            skLineSegment(sketch, "E10.0.5.7", {"start": v(-243, -114) * mm, "end": v(-243, -124) * mm});
            skLineSegment(sketch, "E10.3.5.7", {"start": v(-243, -124) * mm, "end": v(-233, -124) * mm});
            skLineSegment(sketch, "E10.6.5.7", {"start": v(-243, -114) * mm, "end": v(-233, -114) * mm});
            skLineSegment(sketch, "E10.9.5.7", {"start": v(-233, -114) * mm, "end": v(-233, -124) * mm});
            skLineSegment(sketch, "E10.0.5.8", {"start": v(-243, -100) * mm, "end": v(-243, -110) * mm});
            skLineSegment(sketch, "E10.3.5.8", {"start": v(-243, -110) * mm, "end": v(-233, -110) * mm});
            skLineSegment(sketch, "E10.6.5.8", {"start": v(-243, -100) * mm, "end": v(-233, -100) * mm});
            skLineSegment(sketch, "E10.9.5.8", {"start": v(-233, -100) * mm, "end": v(-233, -110) * mm});
            skLineSegment(sketch, "E10.0.5.9", {"start": v(-243, -86) * mm, "end": v(-243, -96) * mm});
            skLineSegment(sketch, "E10.3.5.9", {"start": v(-243, -96) * mm, "end": v(-233, -96) * mm});
            skLineSegment(sketch, "E10.6.5.9", {"start": v(-243, -86) * mm, "end": v(-233, -86) * mm});
            skLineSegment(sketch, "E10.9.5.9", {"start": v(-233, -86) * mm, "end": v(-233, -96) * mm});
            skLineSegment(sketch, "E10.0.5.10", {"start": v(-243, -72) * mm, "end": v(-243, -82) * mm});
            skLineSegment(sketch, "E10.3.5.10", {"start": v(-243, -82) * mm, "end": v(-233, -82) * mm});
            skLineSegment(sketch, "E10.6.5.10", {"start": v(-243, -72) * mm, "end": v(-233, -72) * mm});
            skLineSegment(sketch, "E10.9.5.10", {"start": v(-233, -72) * mm, "end": v(-233, -82) * mm});
            skLineSegment(sketch, "E10.0.5.11", {"start": v(-243, -58) * mm, "end": v(-243, -68) * mm});
            skLineSegment(sketch, "E10.3.5.11", {"start": v(-243, -68) * mm, "end": v(-233, -68) * mm});
            skLineSegment(sketch, "E10.6.5.11", {"start": v(-243, -58) * mm, "end": v(-233, -58) * mm});
            skLineSegment(sketch, "E10.9.5.11", {"start": v(-233, -58) * mm, "end": v(-233, -68) * mm});
            skLineSegment(sketch, "E10.0.5.12", {"start": v(-243, -44) * mm, "end": v(-243, -54) * mm});
            skLineSegment(sketch, "E10.3.5.12", {"start": v(-243, -54) * mm, "end": v(-233, -54) * mm});
            skLineSegment(sketch, "E10.6.5.12", {"start": v(-243, -44) * mm, "end": v(-233, -44) * mm});
            skLineSegment(sketch, "E10.9.5.12", {"start": v(-233, -44) * mm, "end": v(-233, -54) * mm});
            skLineSegment(sketch, "E10.0.5.13", {"start": v(-243, -30) * mm, "end": v(-243, -40) * mm});
            skLineSegment(sketch, "E10.3.5.13", {"start": v(-243, -40) * mm, "end": v(-233, -40) * mm});
            skLineSegment(sketch, "E10.6.5.13", {"start": v(-243, -30) * mm, "end": v(-233, -30) * mm});
            skLineSegment(sketch, "E10.9.5.13", {"start": v(-233, -30) * mm, "end": v(-233, -40) * mm});
            skLineSegment(sketch, "E10.0.5.14", {"start": v(-243, -16) * mm, "end": v(-243, -26) * mm});
            skLineSegment(sketch, "E10.3.5.14", {"start": v(-243, -26) * mm, "end": v(-233, -26) * mm});
            skLineSegment(sketch, "E10.6.5.14", {"start": v(-243, -16) * mm, "end": v(-233, -16) * mm});
            skLineSegment(sketch, "E10.9.5.14", {"start": v(-233, -16) * mm, "end": v(-233, -26) * mm});
            skLineSegment(sketch, "E10.0.5.15", {"start": v(-243, -2) * mm, "end": v(-243, -12) * mm});
            skLineSegment(sketch, "E10.3.5.15", {"start": v(-243, -12) * mm, "end": v(-233, -12) * mm});
            skLineSegment(sketch, "E10.6.5.15", {"start": v(-243, -2) * mm, "end": v(-233, -2) * mm});
            skLineSegment(sketch, "E10.9.5.15", {"start": v(-233, -2) * mm, "end": v(-233, -12) * mm});
            skLineSegment(sketch, "E10.0.5.16", {"start": v(-243, 12) * mm, "end": v(-243, 2) * mm});
            skLineSegment(sketch, "E10.3.5.16", {"start": v(-243, 2) * mm, "end": v(-233, 2) * mm});
            skLineSegment(sketch, "E10.6.5.16", {"start": v(-243, 12) * mm, "end": v(-233, 12) * mm});
            skLineSegment(sketch, "E10.9.5.16", {"start": v(-233, 12) * mm, "end": v(-233, 2) * mm});
            skLineSegment(sketch, "E10.0.5.17", {"start": v(-243, 26) * mm, "end": v(-243, 16) * mm});
            skLineSegment(sketch, "E10.3.5.17", {"start": v(-243, 16) * mm, "end": v(-233, 16) * mm});
            skLineSegment(sketch, "E10.6.5.17", {"start": v(-243, 26) * mm, "end": v(-233, 26) * mm});
            skLineSegment(sketch, "E10.9.5.17", {"start": v(-233, 26) * mm, "end": v(-233, 16) * mm});
            skLineSegment(sketch, "E10.0.5.18", {"start": v(-243, 40) * mm, "end": v(-243, 30) * mm});
            skLineSegment(sketch, "E10.3.5.18", {"start": v(-243, 30) * mm, "end": v(-233, 30) * mm});
            skLineSegment(sketch, "E10.6.5.18", {"start": v(-243, 40) * mm, "end": v(-233, 40) * mm});
            skLineSegment(sketch, "E10.9.5.18", {"start": v(-233, 40) * mm, "end": v(-233, 30) * mm});
            skLineSegment(sketch, "E10.0.5.19", {"start": v(-243, 54) * mm, "end": v(-243, 44) * mm});
            skLineSegment(sketch, "E10.3.5.19", {"start": v(-243, 44) * mm, "end": v(-233, 44) * mm});
            skLineSegment(sketch, "E10.6.5.19", {"start": v(-243, 54) * mm, "end": v(-233, 54) * mm});
            skLineSegment(sketch, "E10.9.5.19", {"start": v(-233, 54) * mm, "end": v(-233, 44) * mm});
            skLineSegment(sketch, "E10.0.5.20", {"start": v(-243, 68) * mm, "end": v(-243, 58) * mm});
            skLineSegment(sketch, "E10.3.5.20", {"start": v(-243, 58) * mm, "end": v(-233, 58) * mm});
            skLineSegment(sketch, "E10.6.5.20", {"start": v(-243, 68) * mm, "end": v(-233, 68) * mm});
            skLineSegment(sketch, "E10.9.5.20", {"start": v(-233, 68) * mm, "end": v(-233, 58) * mm});
            skLineSegment(sketch, "E10.0.5.21", {"start": v(-243, 82) * mm, "end": v(-243, 72) * mm});
            skLineSegment(sketch, "E10.3.5.21", {"start": v(-243, 72) * mm, "end": v(-233, 72) * mm});
            skLineSegment(sketch, "E10.6.5.21", {"start": v(-243, 82) * mm, "end": v(-233, 82) * mm});
            skLineSegment(sketch, "E10.9.5.21", {"start": v(-233, 82) * mm, "end": v(-233, 72) * mm});
            skLineSegment(sketch, "E10.0.5.22", {"start": v(-243, 96) * mm, "end": v(-243, 86) * mm});
            skLineSegment(sketch, "E10.3.5.22", {"start": v(-243, 86) * mm, "end": v(-233, 86) * mm});
            skLineSegment(sketch, "E10.6.5.22", {"start": v(-243, 96) * mm, "end": v(-233, 96) * mm});
            skLineSegment(sketch, "E10.9.5.22", {"start": v(-233, 96) * mm, "end": v(-233, 86) * mm});
            skLineSegment(sketch, "E10.0.5.23", {"start": v(-243, 110) * mm, "end": v(-243, 100) * mm});
            skLineSegment(sketch, "E10.3.5.23", {"start": v(-243, 100) * mm, "end": v(-233, 100) * mm});
            skLineSegment(sketch, "E10.6.5.23", {"start": v(-243, 110) * mm, "end": v(-233, 110) * mm});
            skLineSegment(sketch, "E10.9.5.23", {"start": v(-233, 110) * mm, "end": v(-233, 100) * mm});
            skLineSegment(sketch, "E10.0.5.24", {"start": v(-243, 124) * mm, "end": v(-243, 114) * mm});
            skLineSegment(sketch, "E10.3.5.24", {"start": v(-243, 114) * mm, "end": v(-233, 114) * mm});
            skLineSegment(sketch, "E10.6.5.24", {"start": v(-243, 124) * mm, "end": v(-233, 124) * mm});
            skLineSegment(sketch, "E10.9.5.24", {"start": v(-233, 124) * mm, "end": v(-233, 114) * mm});
            skLineSegment(sketch, "E10.0.5.25", {"start": v(-243, 138) * mm, "end": v(-243, 128) * mm});
            skLineSegment(sketch, "E10.3.5.25", {"start": v(-243, 128) * mm, "end": v(-233, 128) * mm});
            skLineSegment(sketch, "E10.6.5.25", {"start": v(-243, 138) * mm, "end": v(-233, 138) * mm});
            skLineSegment(sketch, "E10.9.5.25", {"start": v(-233, 138) * mm, "end": v(-233, 128) * mm});
            skLineSegment(sketch, "E10.0.5.26", {"start": v(-243, 152) * mm, "end": v(-243, 142) * mm});
            skLineSegment(sketch, "E10.3.5.26", {"start": v(-243, 142) * mm, "end": v(-233, 142) * mm});
            skLineSegment(sketch, "E10.6.5.26", {"start": v(-243, 152) * mm, "end": v(-233, 152) * mm});
            skLineSegment(sketch, "E10.9.5.26", {"start": v(-233, 152) * mm, "end": v(-233, 142) * mm});
            skLineSegment(sketch, "E10.0.5.27", {"start": v(-243, 166) * mm, "end": v(-243, 156) * mm});
            skLineSegment(sketch, "E10.3.5.27", {"start": v(-243, 156) * mm, "end": v(-233, 156) * mm});
            skLineSegment(sketch, "E10.6.5.27", {"start": v(-243, 166) * mm, "end": v(-233, 166) * mm});
            skLineSegment(sketch, "E10.9.5.27", {"start": v(-233, 166) * mm, "end": v(-233, 156) * mm});
            skLineSegment(sketch, "E10.0.5.28", {"start": v(-243, 180) * mm, "end": v(-243, 170) * mm});
            skLineSegment(sketch, "E10.3.5.28", {"start": v(-243, 170) * mm, "end": v(-233, 170) * mm});
            skLineSegment(sketch, "E10.6.5.28", {"start": v(-243, 180) * mm, "end": v(-233, 180) * mm});
            skLineSegment(sketch, "E10.9.5.28", {"start": v(-233, 180) * mm, "end": v(-233, 170) * mm});
            skLineSegment(sketch, "E10.0.5.29", {"start": v(-243, 194) * mm, "end": v(-243, 184) * mm});
            skLineSegment(sketch, "E10.3.5.29", {"start": v(-243, 184) * mm, "end": v(-233, 184) * mm});
            skLineSegment(sketch, "E10.6.5.29", {"start": v(-243, 194) * mm, "end": v(-233, 194) * mm});
            skLineSegment(sketch, "E10.9.5.29", {"start": v(-233, 194) * mm, "end": v(-233, 184) * mm});
            skLineSegment(sketch, "E10.0.5.30", {"start": v(-243, 208) * mm, "end": v(-243, 198) * mm});
            skLineSegment(sketch, "E10.3.5.30", {"start": v(-243, 198) * mm, "end": v(-233, 198) * mm});
            skLineSegment(sketch, "E10.6.5.30", {"start": v(-243, 208) * mm, "end": v(-233, 208) * mm});
            skLineSegment(sketch, "E10.9.5.30", {"start": v(-233, 208) * mm, "end": v(-233, 198) * mm});
            skLineSegment(sketch, "E10.0.5.31", {"start": v(-243, 222) * mm, "end": v(-243, 212) * mm});
            skLineSegment(sketch, "E10.3.5.31", {"start": v(-243, 212) * mm, "end": v(-233, 212) * mm});
            skLineSegment(sketch, "E10.6.5.31", {"start": v(-243, 222) * mm, "end": v(-233, 222) * mm});
            skLineSegment(sketch, "E10.9.5.31", {"start": v(-233, 222) * mm, "end": v(-233, 212) * mm});
            skLineSegment(sketch, "E10.0.6.0", {"start": v(-229, -212) * mm, "end": v(-229, -222) * mm});
            skLineSegment(sketch, "E10.3.6.0", {"start": v(-229, -222) * mm, "end": v(-219, -222) * mm});
            skLineSegment(sketch, "E10.6.6.0", {"start": v(-229, -212) * mm, "end": v(-219, -212) * mm});
            skLineSegment(sketch, "E10.9.6.0", {"start": v(-219, -212) * mm, "end": v(-219, -222) * mm});
            skLineSegment(sketch, "E10.0.6.1", {"start": v(-229, -198) * mm, "end": v(-229, -208) * mm});
            skLineSegment(sketch, "E10.3.6.1", {"start": v(-229, -208) * mm, "end": v(-219, -208) * mm});
            skLineSegment(sketch, "E10.6.6.1", {"start": v(-229, -198) * mm, "end": v(-219, -198) * mm});
            skLineSegment(sketch, "E10.9.6.1", {"start": v(-219, -198) * mm, "end": v(-219, -208) * mm});
            skLineSegment(sketch, "E10.0.6.2", {"start": v(-229, -184) * mm, "end": v(-229, -194) * mm});
            skLineSegment(sketch, "E10.3.6.2", {"start": v(-229, -194) * mm, "end": v(-219, -194) * mm});
            skLineSegment(sketch, "E10.6.6.2", {"start": v(-229, -184) * mm, "end": v(-219, -184) * mm});
            skLineSegment(sketch, "E10.9.6.2", {"start": v(-219, -184) * mm, "end": v(-219, -194) * mm});
            skLineSegment(sketch, "E10.0.6.3", {"start": v(-229, -170) * mm, "end": v(-229, -180) * mm});
            skLineSegment(sketch, "E10.3.6.3", {"start": v(-229, -180) * mm, "end": v(-219, -180) * mm});
            skLineSegment(sketch, "E10.6.6.3", {"start": v(-229, -170) * mm, "end": v(-219, -170) * mm});
            skLineSegment(sketch, "E10.9.6.3", {"start": v(-219, -170) * mm, "end": v(-219, -180) * mm});
            skLineSegment(sketch, "E10.0.6.4", {"start": v(-229, -156) * mm, "end": v(-229, -166) * mm});
            skLineSegment(sketch, "E10.3.6.4", {"start": v(-229, -166) * mm, "end": v(-219, -166) * mm});
            skLineSegment(sketch, "E10.6.6.4", {"start": v(-229, -156) * mm, "end": v(-219, -156) * mm});
            skLineSegment(sketch, "E10.9.6.4", {"start": v(-219, -156) * mm, "end": v(-219, -166) * mm});
            skLineSegment(sketch, "E10.0.6.5", {"start": v(-229, -142) * mm, "end": v(-229, -152) * mm});
            skLineSegment(sketch, "E10.3.6.5", {"start": v(-229, -152) * mm, "end": v(-219, -152) * mm});
            skLineSegment(sketch, "E10.6.6.5", {"start": v(-229, -142) * mm, "end": v(-219, -142) * mm});
            skLineSegment(sketch, "E10.9.6.5", {"start": v(-219, -142) * mm, "end": v(-219, -152) * mm});
            skLineSegment(sketch, "E10.0.6.6", {"start": v(-229, -128) * mm, "end": v(-229, -138) * mm});
            skLineSegment(sketch, "E10.3.6.6", {"start": v(-229, -138) * mm, "end": v(-219, -138) * mm});
            skLineSegment(sketch, "E10.6.6.6", {"start": v(-229, -128) * mm, "end": v(-219, -128) * mm});
            skLineSegment(sketch, "E10.9.6.6", {"start": v(-219, -128) * mm, "end": v(-219, -138) * mm});
            skLineSegment(sketch, "E10.0.6.7", {"start": v(-229, -114) * mm, "end": v(-229, -124) * mm});
            skLineSegment(sketch, "E10.3.6.7", {"start": v(-229, -124) * mm, "end": v(-219, -124) * mm});
            skLineSegment(sketch, "E10.6.6.7", {"start": v(-229, -114) * mm, "end": v(-219, -114) * mm});
            skLineSegment(sketch, "E10.9.6.7", {"start": v(-219, -114) * mm, "end": v(-219, -124) * mm});
            skLineSegment(sketch, "E10.0.6.8", {"start": v(-229, -100) * mm, "end": v(-229, -110) * mm});
            skLineSegment(sketch, "E10.3.6.8", {"start": v(-229, -110) * mm, "end": v(-219, -110) * mm});
            skLineSegment(sketch, "E10.6.6.8", {"start": v(-229, -100) * mm, "end": v(-219, -100) * mm});
            skLineSegment(sketch, "E10.9.6.8", {"start": v(-219, -100) * mm, "end": v(-219, -110) * mm});
            skLineSegment(sketch, "E10.0.6.9", {"start": v(-229, -86) * mm, "end": v(-229, -96) * mm});
            skLineSegment(sketch, "E10.3.6.9", {"start": v(-229, -96) * mm, "end": v(-219, -96) * mm});
            skLineSegment(sketch, "E10.6.6.9", {"start": v(-229, -86) * mm, "end": v(-219, -86) * mm});
            skLineSegment(sketch, "E10.9.6.9", {"start": v(-219, -86) * mm, "end": v(-219, -96) * mm});
            skLineSegment(sketch, "E10.0.6.10", {"start": v(-229, -72) * mm, "end": v(-229, -82) * mm});
            skLineSegment(sketch, "E10.3.6.10", {"start": v(-229, -82) * mm, "end": v(-219, -82) * mm});
            skLineSegment(sketch, "E10.6.6.10", {"start": v(-229, -72) * mm, "end": v(-219, -72) * mm});
            skLineSegment(sketch, "E10.9.6.10", {"start": v(-219, -72) * mm, "end": v(-219, -82) * mm});
            skLineSegment(sketch, "E10.0.6.11", {"start": v(-229, -58) * mm, "end": v(-229, -68) * mm});
            skLineSegment(sketch, "E10.3.6.11", {"start": v(-229, -68) * mm, "end": v(-219, -68) * mm});
            skLineSegment(sketch, "E10.6.6.11", {"start": v(-229, -58) * mm, "end": v(-219, -58) * mm});
            skLineSegment(sketch, "E10.9.6.11", {"start": v(-219, -58) * mm, "end": v(-219, -68) * mm});
            skLineSegment(sketch, "E10.0.6.12", {"start": v(-229, -44) * mm, "end": v(-229, -54) * mm});
            skLineSegment(sketch, "E10.3.6.12", {"start": v(-229, -54) * mm, "end": v(-219, -54) * mm});
            skLineSegment(sketch, "E10.6.6.12", {"start": v(-229, -44) * mm, "end": v(-219, -44) * mm});
            skLineSegment(sketch, "E10.9.6.12", {"start": v(-219, -44) * mm, "end": v(-219, -54) * mm});
            skLineSegment(sketch, "E10.0.6.13", {"start": v(-229, -30) * mm, "end": v(-229, -40) * mm});
            skLineSegment(sketch, "E10.3.6.13", {"start": v(-229, -40) * mm, "end": v(-219, -40) * mm});
            skLineSegment(sketch, "E10.6.6.13", {"start": v(-229, -30) * mm, "end": v(-219, -30) * mm});
            skLineSegment(sketch, "E10.9.6.13", {"start": v(-219, -30) * mm, "end": v(-219, -40) * mm});
            skLineSegment(sketch, "E10.0.6.14", {"start": v(-229, -16) * mm, "end": v(-229, -26) * mm});
            skLineSegment(sketch, "E10.3.6.14", {"start": v(-229, -26) * mm, "end": v(-219, -26) * mm});
            skLineSegment(sketch, "E10.6.6.14", {"start": v(-229, -16) * mm, "end": v(-219, -16) * mm});
            skLineSegment(sketch, "E10.9.6.14", {"start": v(-219, -16) * mm, "end": v(-219, -26) * mm});
            skLineSegment(sketch, "E10.0.6.15", {"start": v(-229, -2) * mm, "end": v(-229, -12) * mm});
            skLineSegment(sketch, "E10.3.6.15", {"start": v(-229, -12) * mm, "end": v(-219, -12) * mm});
            skLineSegment(sketch, "E10.6.6.15", {"start": v(-229, -2) * mm, "end": v(-219, -2) * mm});
            skLineSegment(sketch, "E10.9.6.15", {"start": v(-219, -2) * mm, "end": v(-219, -12) * mm});
            skLineSegment(sketch, "E10.0.6.16", {"start": v(-229, 12) * mm, "end": v(-229, 2) * mm});
            skLineSegment(sketch, "E10.3.6.16", {"start": v(-229, 2) * mm, "end": v(-219, 2) * mm});
            skLineSegment(sketch, "E10.6.6.16", {"start": v(-229, 12) * mm, "end": v(-219, 12) * mm});
            skLineSegment(sketch, "E10.9.6.16", {"start": v(-219, 12) * mm, "end": v(-219, 2) * mm});
            skLineSegment(sketch, "E10.0.6.17", {"start": v(-229, 26) * mm, "end": v(-229, 16) * mm});
            skLineSegment(sketch, "E10.3.6.17", {"start": v(-229, 16) * mm, "end": v(-219, 16) * mm});
            skLineSegment(sketch, "E10.6.6.17", {"start": v(-229, 26) * mm, "end": v(-219, 26) * mm});
            skLineSegment(sketch, "E10.9.6.17", {"start": v(-219, 26) * mm, "end": v(-219, 16) * mm});
            skLineSegment(sketch, "E10.0.6.18", {"start": v(-229, 40) * mm, "end": v(-229, 30) * mm});
            skLineSegment(sketch, "E10.3.6.18", {"start": v(-229, 30) * mm, "end": v(-219, 30) * mm});
            skLineSegment(sketch, "E10.6.6.18", {"start": v(-229, 40) * mm, "end": v(-219, 40) * mm});
            skLineSegment(sketch, "E10.9.6.18", {"start": v(-219, 40) * mm, "end": v(-219, 30) * mm});
            skLineSegment(sketch, "E10.0.6.19", {"start": v(-229, 54) * mm, "end": v(-229, 44) * mm});
            skLineSegment(sketch, "E10.3.6.19", {"start": v(-229, 44) * mm, "end": v(-219, 44) * mm});
            skLineSegment(sketch, "E10.6.6.19", {"start": v(-229, 54) * mm, "end": v(-219, 54) * mm});
            skLineSegment(sketch, "E10.9.6.19", {"start": v(-219, 54) * mm, "end": v(-219, 44) * mm});
            skLineSegment(sketch, "E10.0.6.20", {"start": v(-229, 68) * mm, "end": v(-229, 58) * mm});
            skLineSegment(sketch, "E10.3.6.20", {"start": v(-229, 58) * mm, "end": v(-219, 58) * mm});
            skLineSegment(sketch, "E10.6.6.20", {"start": v(-229, 68) * mm, "end": v(-219, 68) * mm});
            skLineSegment(sketch, "E10.9.6.20", {"start": v(-219, 68) * mm, "end": v(-219, 58) * mm});
            skLineSegment(sketch, "E10.0.6.21", {"start": v(-229, 82) * mm, "end": v(-229, 72) * mm});
            skLineSegment(sketch, "E10.3.6.21", {"start": v(-229, 72) * mm, "end": v(-219, 72) * mm});
            skLineSegment(sketch, "E10.6.6.21", {"start": v(-229, 82) * mm, "end": v(-219, 82) * mm});
            skLineSegment(sketch, "E10.9.6.21", {"start": v(-219, 82) * mm, "end": v(-219, 72) * mm});
            skLineSegment(sketch, "E10.0.6.22", {"start": v(-229, 96) * mm, "end": v(-229, 86) * mm});
            skLineSegment(sketch, "E10.3.6.22", {"start": v(-229, 86) * mm, "end": v(-219, 86) * mm});
            skLineSegment(sketch, "E10.6.6.22", {"start": v(-229, 96) * mm, "end": v(-219, 96) * mm});
            skLineSegment(sketch, "E10.9.6.22", {"start": v(-219, 96) * mm, "end": v(-219, 86) * mm});
            skLineSegment(sketch, "E10.0.6.23", {"start": v(-229, 110) * mm, "end": v(-229, 100) * mm});
            skLineSegment(sketch, "E10.3.6.23", {"start": v(-229, 100) * mm, "end": v(-219, 100) * mm});
            skLineSegment(sketch, "E10.6.6.23", {"start": v(-229, 110) * mm, "end": v(-219, 110) * mm});
            skLineSegment(sketch, "E10.9.6.23", {"start": v(-219, 110) * mm, "end": v(-219, 100) * mm});
            skLineSegment(sketch, "E10.0.6.24", {"start": v(-229, 124) * mm, "end": v(-229, 114) * mm});
            skLineSegment(sketch, "E10.3.6.24", {"start": v(-229, 114) * mm, "end": v(-219, 114) * mm});
            skLineSegment(sketch, "E10.6.6.24", {"start": v(-229, 124) * mm, "end": v(-219, 124) * mm});
            skLineSegment(sketch, "E10.9.6.24", {"start": v(-219, 124) * mm, "end": v(-219, 114) * mm});
            skLineSegment(sketch, "E10.0.6.25", {"start": v(-229, 138) * mm, "end": v(-229, 128) * mm});
            skLineSegment(sketch, "E10.3.6.25", {"start": v(-229, 128) * mm, "end": v(-219, 128) * mm});
            skLineSegment(sketch, "E10.6.6.25", {"start": v(-229, 138) * mm, "end": v(-219, 138) * mm});
            skLineSegment(sketch, "E10.9.6.25", {"start": v(-219, 138) * mm, "end": v(-219, 128) * mm});
            skLineSegment(sketch, "E10.0.6.26", {"start": v(-229, 152) * mm, "end": v(-229, 142) * mm});
            skLineSegment(sketch, "E10.3.6.26", {"start": v(-229, 142) * mm, "end": v(-219, 142) * mm});
            skLineSegment(sketch, "E10.6.6.26", {"start": v(-229, 152) * mm, "end": v(-219, 152) * mm});
            skLineSegment(sketch, "E10.9.6.26", {"start": v(-219, 152) * mm, "end": v(-219, 142) * mm});
            skLineSegment(sketch, "E10.0.6.27", {"start": v(-229, 166) * mm, "end": v(-229, 156) * mm});
            skLineSegment(sketch, "E10.3.6.27", {"start": v(-229, 156) * mm, "end": v(-219, 156) * mm});
            skLineSegment(sketch, "E10.6.6.27", {"start": v(-229, 166) * mm, "end": v(-219, 166) * mm});
            skLineSegment(sketch, "E10.9.6.27", {"start": v(-219, 166) * mm, "end": v(-219, 156) * mm});
            skLineSegment(sketch, "E10.0.6.28", {"start": v(-229, 180) * mm, "end": v(-229, 170) * mm});
            skLineSegment(sketch, "E10.3.6.28", {"start": v(-229, 170) * mm, "end": v(-219, 170) * mm});
            skLineSegment(sketch, "E10.6.6.28", {"start": v(-229, 180) * mm, "end": v(-219, 180) * mm});
            skLineSegment(sketch, "E10.9.6.28", {"start": v(-219, 180) * mm, "end": v(-219, 170) * mm});
            skLineSegment(sketch, "E10.0.6.29", {"start": v(-229, 194) * mm, "end": v(-229, 184) * mm});
            skLineSegment(sketch, "E10.3.6.29", {"start": v(-229, 184) * mm, "end": v(-219, 184) * mm});
            skLineSegment(sketch, "E10.6.6.29", {"start": v(-229, 194) * mm, "end": v(-219, 194) * mm});
            skLineSegment(sketch, "E10.9.6.29", {"start": v(-219, 194) * mm, "end": v(-219, 184) * mm});
            skLineSegment(sketch, "E10.0.6.30", {"start": v(-229, 208) * mm, "end": v(-229, 198) * mm});
            skLineSegment(sketch, "E10.3.6.30", {"start": v(-229, 198) * mm, "end": v(-219, 198) * mm});
            skLineSegment(sketch, "E10.6.6.30", {"start": v(-229, 208) * mm, "end": v(-219, 208) * mm});
            skLineSegment(sketch, "E10.9.6.30", {"start": v(-219, 208) * mm, "end": v(-219, 198) * mm});
            skLineSegment(sketch, "E10.0.6.31", {"start": v(-229, 222) * mm, "end": v(-229, 212) * mm});
            skLineSegment(sketch, "E10.3.6.31", {"start": v(-229, 212) * mm, "end": v(-219, 212) * mm});
            skLineSegment(sketch, "E10.6.6.31", {"start": v(-229, 222) * mm, "end": v(-219, 222) * mm});
            skLineSegment(sketch, "E10.9.6.31", {"start": v(-219, 222) * mm, "end": v(-219, 212) * mm});
            skLineSegment(sketch, "E10.0.7.0", {"start": v(-215, -212) * mm, "end": v(-215, -222) * mm});
            skLineSegment(sketch, "E10.3.7.0", {"start": v(-215, -222) * mm, "end": v(-205, -222) * mm});
            skLineSegment(sketch, "E10.6.7.0", {"start": v(-215, -212) * mm, "end": v(-205, -212) * mm});
            skLineSegment(sketch, "E10.9.7.0", {"start": v(-205, -212) * mm, "end": v(-205, -222) * mm});
            skLineSegment(sketch, "E10.0.7.1", {"start": v(-215, -198) * mm, "end": v(-215, -208) * mm});
            skLineSegment(sketch, "E10.3.7.1", {"start": v(-215, -208) * mm, "end": v(-205, -208) * mm});
            skLineSegment(sketch, "E10.6.7.1", {"start": v(-215, -198) * mm, "end": v(-205, -198) * mm});
            skLineSegment(sketch, "E10.9.7.1", {"start": v(-205, -198) * mm, "end": v(-205, -208) * mm});
            skLineSegment(sketch, "E10.0.7.2", {"start": v(-215, -184) * mm, "end": v(-215, -194) * mm});
            skLineSegment(sketch, "E10.3.7.2", {"start": v(-215, -194) * mm, "end": v(-205, -194) * mm});
            skLineSegment(sketch, "E10.6.7.2", {"start": v(-215, -184) * mm, "end": v(-205, -184) * mm});
            skLineSegment(sketch, "E10.9.7.2", {"start": v(-205, -184) * mm, "end": v(-205, -194) * mm});
            skLineSegment(sketch, "E10.0.7.3", {"start": v(-215, -170) * mm, "end": v(-215, -180) * mm});
            skLineSegment(sketch, "E10.3.7.3", {"start": v(-215, -180) * mm, "end": v(-205, -180) * mm});
            skLineSegment(sketch, "E10.6.7.3", {"start": v(-215, -170) * mm, "end": v(-205, -170) * mm});
            skLineSegment(sketch, "E10.9.7.3", {"start": v(-205, -170) * mm, "end": v(-205, -180) * mm});
            skLineSegment(sketch, "E10.0.7.4", {"start": v(-215, -156) * mm, "end": v(-215, -166) * mm});
            skLineSegment(sketch, "E10.3.7.4", {"start": v(-215, -166) * mm, "end": v(-205, -166) * mm});
            skLineSegment(sketch, "E10.6.7.4", {"start": v(-215, -156) * mm, "end": v(-205, -156) * mm});
            skLineSegment(sketch, "E10.9.7.4", {"start": v(-205, -156) * mm, "end": v(-205, -166) * mm});
            skLineSegment(sketch, "E10.0.7.5", {"start": v(-215, -142) * mm, "end": v(-215, -152) * mm});
            skLineSegment(sketch, "E10.3.7.5", {"start": v(-215, -152) * mm, "end": v(-205, -152) * mm});
            skLineSegment(sketch, "E10.6.7.5", {"start": v(-215, -142) * mm, "end": v(-205, -142) * mm});
            skLineSegment(sketch, "E10.9.7.5", {"start": v(-205, -142) * mm, "end": v(-205, -152) * mm});
            skLineSegment(sketch, "E10.0.7.6", {"start": v(-215, -128) * mm, "end": v(-215, -138) * mm});
            skLineSegment(sketch, "E10.3.7.6", {"start": v(-215, -138) * mm, "end": v(-205, -138) * mm});
            skLineSegment(sketch, "E10.6.7.6", {"start": v(-215, -128) * mm, "end": v(-205, -128) * mm});
            skLineSegment(sketch, "E10.9.7.6", {"start": v(-205, -128) * mm, "end": v(-205, -138) * mm});
            skLineSegment(sketch, "E10.0.7.7", {"start": v(-215, -114) * mm, "end": v(-215, -124) * mm});
            skLineSegment(sketch, "E10.3.7.7", {"start": v(-215, -124) * mm, "end": v(-205, -124) * mm});
            skLineSegment(sketch, "E10.6.7.7", {"start": v(-215, -114) * mm, "end": v(-205, -114) * mm});
            skLineSegment(sketch, "E10.9.7.7", {"start": v(-205, -114) * mm, "end": v(-205, -124) * mm});
            skLineSegment(sketch, "E10.0.7.8", {"start": v(-215, -100) * mm, "end": v(-215, -110) * mm});
            skLineSegment(sketch, "E10.3.7.8", {"start": v(-215, -110) * mm, "end": v(-205, -110) * mm});
            skLineSegment(sketch, "E10.6.7.8", {"start": v(-215, -100) * mm, "end": v(-205, -100) * mm});
            skLineSegment(sketch, "E10.9.7.8", {"start": v(-205, -100) * mm, "end": v(-205, -110) * mm});
            skLineSegment(sketch, "E10.0.7.9", {"start": v(-215, -86) * mm, "end": v(-215, -96) * mm});
            skLineSegment(sketch, "E10.3.7.9", {"start": v(-215, -96) * mm, "end": v(-205, -96) * mm});
            skLineSegment(sketch, "E10.6.7.9", {"start": v(-215, -86) * mm, "end": v(-205, -86) * mm});
            skLineSegment(sketch, "E10.9.7.9", {"start": v(-205, -86) * mm, "end": v(-205, -96) * mm});
            skLineSegment(sketch, "E10.0.7.10", {"start": v(-215, -72) * mm, "end": v(-215, -82) * mm});
            skLineSegment(sketch, "E10.3.7.10", {"start": v(-215, -82) * mm, "end": v(-205, -82) * mm});
            skLineSegment(sketch, "E10.6.7.10", {"start": v(-215, -72) * mm, "end": v(-205, -72) * mm});
            skLineSegment(sketch, "E10.9.7.10", {"start": v(-205, -72) * mm, "end": v(-205, -82) * mm});
            skLineSegment(sketch, "E10.0.7.11", {"start": v(-215, -58) * mm, "end": v(-215, -68) * mm});
            skLineSegment(sketch, "E10.3.7.11", {"start": v(-215, -68) * mm, "end": v(-205, -68) * mm});
            skLineSegment(sketch, "E10.6.7.11", {"start": v(-215, -58) * mm, "end": v(-205, -58) * mm});
            skLineSegment(sketch, "E10.9.7.11", {"start": v(-205, -58) * mm, "end": v(-205, -68) * mm});
            skLineSegment(sketch, "E10.0.7.12", {"start": v(-215, -44) * mm, "end": v(-215, -54) * mm});
            skLineSegment(sketch, "E10.3.7.12", {"start": v(-215, -54) * mm, "end": v(-205, -54) * mm});
            skLineSegment(sketch, "E10.6.7.12", {"start": v(-215, -44) * mm, "end": v(-205, -44) * mm});
            skLineSegment(sketch, "E10.9.7.12", {"start": v(-205, -44) * mm, "end": v(-205, -54) * mm});
            skLineSegment(sketch, "E10.0.7.13", {"start": v(-215, -30) * mm, "end": v(-215, -40) * mm});
            skLineSegment(sketch, "E10.3.7.13", {"start": v(-215, -40) * mm, "end": v(-205, -40) * mm});
            skLineSegment(sketch, "E10.6.7.13", {"start": v(-215, -30) * mm, "end": v(-205, -30) * mm});
            skLineSegment(sketch, "E10.9.7.13", {"start": v(-205, -30) * mm, "end": v(-205, -40) * mm});
            skLineSegment(sketch, "E10.0.7.14", {"start": v(-215, -16) * mm, "end": v(-215, -26) * mm});
            skLineSegment(sketch, "E10.3.7.14", {"start": v(-215, -26) * mm, "end": v(-205, -26) * mm});
            skLineSegment(sketch, "E10.6.7.14", {"start": v(-215, -16) * mm, "end": v(-205, -16) * mm});
            skLineSegment(sketch, "E10.9.7.14", {"start": v(-205, -16) * mm, "end": v(-205, -26) * mm});
            skLineSegment(sketch, "E10.0.7.15", {"start": v(-215, -2) * mm, "end": v(-215, -12) * mm});
            skLineSegment(sketch, "E10.3.7.15", {"start": v(-215, -12) * mm, "end": v(-205, -12) * mm});
            skLineSegment(sketch, "E10.6.7.15", {"start": v(-215, -2) * mm, "end": v(-205, -2) * mm});
            skLineSegment(sketch, "E10.9.7.15", {"start": v(-205, -2) * mm, "end": v(-205, -12) * mm});
            skLineSegment(sketch, "E10.0.7.16", {"start": v(-215, 12) * mm, "end": v(-215, 2) * mm});
            skLineSegment(sketch, "E10.3.7.16", {"start": v(-215, 2) * mm, "end": v(-205, 2) * mm});
            skLineSegment(sketch, "E10.6.7.16", {"start": v(-215, 12) * mm, "end": v(-205, 12) * mm});
            skLineSegment(sketch, "E10.9.7.16", {"start": v(-205, 12) * mm, "end": v(-205, 2) * mm});
            skLineSegment(sketch, "E10.0.7.17", {"start": v(-215, 26) * mm, "end": v(-215, 16) * mm});
            skLineSegment(sketch, "E10.3.7.17", {"start": v(-215, 16) * mm, "end": v(-205, 16) * mm});
            skLineSegment(sketch, "E10.6.7.17", {"start": v(-215, 26) * mm, "end": v(-205, 26) * mm});
            skLineSegment(sketch, "E10.9.7.17", {"start": v(-205, 26) * mm, "end": v(-205, 16) * mm});
            skLineSegment(sketch, "E10.0.7.18", {"start": v(-215, 40) * mm, "end": v(-215, 30) * mm});
            skLineSegment(sketch, "E10.3.7.18", {"start": v(-215, 30) * mm, "end": v(-205, 30) * mm});
            skLineSegment(sketch, "E10.6.7.18", {"start": v(-215, 40) * mm, "end": v(-205, 40) * mm});
            skLineSegment(sketch, "E10.9.7.18", {"start": v(-205, 40) * mm, "end": v(-205, 30) * mm});
            skLineSegment(sketch, "E10.0.7.19", {"start": v(-215, 54) * mm, "end": v(-215, 44) * mm});
            skLineSegment(sketch, "E10.3.7.19", {"start": v(-215, 44) * mm, "end": v(-205, 44) * mm});
            skLineSegment(sketch, "E10.6.7.19", {"start": v(-215, 54) * mm, "end": v(-205, 54) * mm});
            skLineSegment(sketch, "E10.9.7.19", {"start": v(-205, 54) * mm, "end": v(-205, 44) * mm});
            skLineSegment(sketch, "E10.0.7.20", {"start": v(-215, 68) * mm, "end": v(-215, 58) * mm});
            skLineSegment(sketch, "E10.3.7.20", {"start": v(-215, 58) * mm, "end": v(-205, 58) * mm});
            skLineSegment(sketch, "E10.6.7.20", {"start": v(-215, 68) * mm, "end": v(-205, 68) * mm});
            skLineSegment(sketch, "E10.9.7.20", {"start": v(-205, 68) * mm, "end": v(-205, 58) * mm});
            skLineSegment(sketch, "E10.0.7.21", {"start": v(-215, 82) * mm, "end": v(-215, 72) * mm});
            skLineSegment(sketch, "E10.3.7.21", {"start": v(-215, 72) * mm, "end": v(-205, 72) * mm});
            skLineSegment(sketch, "E10.6.7.21", {"start": v(-215, 82) * mm, "end": v(-205, 82) * mm});
            skLineSegment(sketch, "E10.9.7.21", {"start": v(-205, 82) * mm, "end": v(-205, 72) * mm});
            skLineSegment(sketch, "E10.0.7.22", {"start": v(-215, 96) * mm, "end": v(-215, 86) * mm});
            skLineSegment(sketch, "E10.3.7.22", {"start": v(-215, 86) * mm, "end": v(-205, 86) * mm});
            skLineSegment(sketch, "E10.6.7.22", {"start": v(-215, 96) * mm, "end": v(-205, 96) * mm});
            skLineSegment(sketch, "E10.9.7.22", {"start": v(-205, 96) * mm, "end": v(-205, 86) * mm});
            skLineSegment(sketch, "E10.0.7.23", {"start": v(-215, 110) * mm, "end": v(-215, 100) * mm});
            skLineSegment(sketch, "E10.3.7.23", {"start": v(-215, 100) * mm, "end": v(-205, 100) * mm});
            skLineSegment(sketch, "E10.6.7.23", {"start": v(-215, 110) * mm, "end": v(-205, 110) * mm});
            skLineSegment(sketch, "E10.9.7.23", {"start": v(-205, 110) * mm, "end": v(-205, 100) * mm});
            skLineSegment(sketch, "E10.0.7.24", {"start": v(-215, 124) * mm, "end": v(-215, 114) * mm});
            skLineSegment(sketch, "E10.3.7.24", {"start": v(-215, 114) * mm, "end": v(-205, 114) * mm});
            skLineSegment(sketch, "E10.6.7.24", {"start": v(-215, 124) * mm, "end": v(-205, 124) * mm});
            skLineSegment(sketch, "E10.9.7.24", {"start": v(-205, 124) * mm, "end": v(-205, 114) * mm});
            skLineSegment(sketch, "E10.0.7.25", {"start": v(-215, 138) * mm, "end": v(-215, 128) * mm});
            skLineSegment(sketch, "E10.3.7.25", {"start": v(-215, 128) * mm, "end": v(-205, 128) * mm});
            skLineSegment(sketch, "E10.6.7.25", {"start": v(-215, 138) * mm, "end": v(-205, 138) * mm});
            skLineSegment(sketch, "E10.9.7.25", {"start": v(-205, 138) * mm, "end": v(-205, 128) * mm});
            skLineSegment(sketch, "E10.0.7.26", {"start": v(-215, 152) * mm, "end": v(-215, 142) * mm});
            skLineSegment(sketch, "E10.3.7.26", {"start": v(-215, 142) * mm, "end": v(-205, 142) * mm});
            skLineSegment(sketch, "E10.6.7.26", {"start": v(-215, 152) * mm, "end": v(-205, 152) * mm});
            skLineSegment(sketch, "E10.9.7.26", {"start": v(-205, 152) * mm, "end": v(-205, 142) * mm});
            skLineSegment(sketch, "E10.0.7.27", {"start": v(-215, 166) * mm, "end": v(-215, 156) * mm});
            skLineSegment(sketch, "E10.3.7.27", {"start": v(-215, 156) * mm, "end": v(-205, 156) * mm});
            skLineSegment(sketch, "E10.6.7.27", {"start": v(-215, 166) * mm, "end": v(-205, 166) * mm});
            skLineSegment(sketch, "E10.9.7.27", {"start": v(-205, 166) * mm, "end": v(-205, 156) * mm});
            skLineSegment(sketch, "E10.0.7.28", {"start": v(-215, 180) * mm, "end": v(-215, 170) * mm});
            skLineSegment(sketch, "E10.3.7.28", {"start": v(-215, 170) * mm, "end": v(-205, 170) * mm});
            skLineSegment(sketch, "E10.6.7.28", {"start": v(-215, 180) * mm, "end": v(-205, 180) * mm});
            skLineSegment(sketch, "E10.9.7.28", {"start": v(-205, 180) * mm, "end": v(-205, 170) * mm});
            skLineSegment(sketch, "E10.0.7.29", {"start": v(-215, 194) * mm, "end": v(-215, 184) * mm});
            skLineSegment(sketch, "E10.3.7.29", {"start": v(-215, 184) * mm, "end": v(-205, 184) * mm});
            skLineSegment(sketch, "E10.6.7.29", {"start": v(-215, 194) * mm, "end": v(-205, 194) * mm});
            skLineSegment(sketch, "E10.9.7.29", {"start": v(-205, 194) * mm, "end": v(-205, 184) * mm});
            skLineSegment(sketch, "E10.0.7.30", {"start": v(-215, 208) * mm, "end": v(-215, 198) * mm});
            skLineSegment(sketch, "E10.3.7.30", {"start": v(-215, 198) * mm, "end": v(-205, 198) * mm});
            skLineSegment(sketch, "E10.6.7.30", {"start": v(-215, 208) * mm, "end": v(-205, 208) * mm});
            skLineSegment(sketch, "E10.9.7.30", {"start": v(-205, 208) * mm, "end": v(-205, 198) * mm});
            skLineSegment(sketch, "E10.0.7.31", {"start": v(-215, 222) * mm, "end": v(-215, 212) * mm});
            skLineSegment(sketch, "E10.3.7.31", {"start": v(-215, 212) * mm, "end": v(-205, 212) * mm});
            skLineSegment(sketch, "E10.6.7.31", {"start": v(-215, 222) * mm, "end": v(-205, 222) * mm});
            skLineSegment(sketch, "E10.9.7.31", {"start": v(-205, 222) * mm, "end": v(-205, 212) * mm});
            skLineSegment(sketch, "E10.0.8.0", {"start": v(-201, -212) * mm, "end": v(-201, -222) * mm});
            skLineSegment(sketch, "E10.3.8.0", {"start": v(-201, -222) * mm, "end": v(-191, -222) * mm});
            skLineSegment(sketch, "E10.6.8.0", {"start": v(-201, -212) * mm, "end": v(-191, -212) * mm});
            skLineSegment(sketch, "E10.9.8.0", {"start": v(-191, -212) * mm, "end": v(-191, -222) * mm});
            skLineSegment(sketch, "E10.0.8.1", {"start": v(-201, -198) * mm, "end": v(-201, -208) * mm});
            skLineSegment(sketch, "E10.3.8.1", {"start": v(-201, -208) * mm, "end": v(-191, -208) * mm});
            skLineSegment(sketch, "E10.6.8.1", {"start": v(-201, -198) * mm, "end": v(-191, -198) * mm});
            skLineSegment(sketch, "E10.9.8.1", {"start": v(-191, -198) * mm, "end": v(-191, -208) * mm});
            skLineSegment(sketch, "E10.0.8.2", {"start": v(-201, -184) * mm, "end": v(-201, -194) * mm});
            skLineSegment(sketch, "E10.3.8.2", {"start": v(-201, -194) * mm, "end": v(-191, -194) * mm});
            skLineSegment(sketch, "E10.6.8.2", {"start": v(-201, -184) * mm, "end": v(-191, -184) * mm});
            skLineSegment(sketch, "E10.9.8.2", {"start": v(-191, -184) * mm, "end": v(-191, -194) * mm});
            skLineSegment(sketch, "E10.0.8.3", {"start": v(-201, -170) * mm, "end": v(-201, -180) * mm});
            skLineSegment(sketch, "E10.3.8.3", {"start": v(-201, -180) * mm, "end": v(-191, -180) * mm});
            skLineSegment(sketch, "E10.6.8.3", {"start": v(-201, -170) * mm, "end": v(-191, -170) * mm});
            skLineSegment(sketch, "E10.9.8.3", {"start": v(-191, -170) * mm, "end": v(-191, -180) * mm});
            skLineSegment(sketch, "E10.0.8.4", {"start": v(-201, -156) * mm, "end": v(-201, -166) * mm});
            skLineSegment(sketch, "E10.3.8.4", {"start": v(-201, -166) * mm, "end": v(-191, -166) * mm});
            skLineSegment(sketch, "E10.6.8.4", {"start": v(-201, -156) * mm, "end": v(-191, -156) * mm});
            skLineSegment(sketch, "E10.9.8.4", {"start": v(-191, -156) * mm, "end": v(-191, -166) * mm});
            skLineSegment(sketch, "E10.0.8.5", {"start": v(-201, -142) * mm, "end": v(-201, -152) * mm});
            skLineSegment(sketch, "E10.3.8.5", {"start": v(-201, -152) * mm, "end": v(-191, -152) * mm});
            skLineSegment(sketch, "E10.6.8.5", {"start": v(-201, -142) * mm, "end": v(-191, -142) * mm});
            skLineSegment(sketch, "E10.9.8.5", {"start": v(-191, -142) * mm, "end": v(-191, -152) * mm});
            skLineSegment(sketch, "E10.0.8.6", {"start": v(-201, -128) * mm, "end": v(-201, -138) * mm});
            skLineSegment(sketch, "E10.3.8.6", {"start": v(-201, -138) * mm, "end": v(-191, -138) * mm});
            skLineSegment(sketch, "E10.6.8.6", {"start": v(-201, -128) * mm, "end": v(-191, -128) * mm});
            skLineSegment(sketch, "E10.9.8.6", {"start": v(-191, -128) * mm, "end": v(-191, -138) * mm});
            skLineSegment(sketch, "E10.0.8.7", {"start": v(-201, -114) * mm, "end": v(-201, -124) * mm});
            skLineSegment(sketch, "E10.3.8.7", {"start": v(-201, -124) * mm, "end": v(-191, -124) * mm});
            skLineSegment(sketch, "E10.6.8.7", {"start": v(-201, -114) * mm, "end": v(-191, -114) * mm});
            skLineSegment(sketch, "E10.9.8.7", {"start": v(-191, -114) * mm, "end": v(-191, -124) * mm});
            skLineSegment(sketch, "E10.0.8.8", {"start": v(-201, -100) * mm, "end": v(-201, -110) * mm});
            skLineSegment(sketch, "E10.3.8.8", {"start": v(-201, -110) * mm, "end": v(-191, -110) * mm});
            skLineSegment(sketch, "E10.6.8.8", {"start": v(-201, -100) * mm, "end": v(-191, -100) * mm});
            skLineSegment(sketch, "E10.9.8.8", {"start": v(-191, -100) * mm, "end": v(-191, -110) * mm});
            skLineSegment(sketch, "E10.0.8.9", {"start": v(-201, -86) * mm, "end": v(-201, -96) * mm});
            skLineSegment(sketch, "E10.3.8.9", {"start": v(-201, -96) * mm, "end": v(-191, -96) * mm});
            skLineSegment(sketch, "E10.6.8.9", {"start": v(-201, -86) * mm, "end": v(-191, -86) * mm});
            skLineSegment(sketch, "E10.9.8.9", {"start": v(-191, -86) * mm, "end": v(-191, -96) * mm});
            skLineSegment(sketch, "E10.0.8.10", {"start": v(-201, -72) * mm, "end": v(-201, -82) * mm});
            skLineSegment(sketch, "E10.3.8.10", {"start": v(-201, -82) * mm, "end": v(-191, -82) * mm});
            skLineSegment(sketch, "E10.6.8.10", {"start": v(-201, -72) * mm, "end": v(-191, -72) * mm});
            skLineSegment(sketch, "E10.9.8.10", {"start": v(-191, -72) * mm, "end": v(-191, -82) * mm});
            skLineSegment(sketch, "E10.0.8.11", {"start": v(-201, -58) * mm, "end": v(-201, -68) * mm});
            skLineSegment(sketch, "E10.3.8.11", {"start": v(-201, -68) * mm, "end": v(-191, -68) * mm});
            skLineSegment(sketch, "E10.6.8.11", {"start": v(-201, -58) * mm, "end": v(-191, -58) * mm});
            skLineSegment(sketch, "E10.9.8.11", {"start": v(-191, -58) * mm, "end": v(-191, -68) * mm});
            skLineSegment(sketch, "E10.0.8.12", {"start": v(-201, -44) * mm, "end": v(-201, -54) * mm});
            skLineSegment(sketch, "E10.3.8.12", {"start": v(-201, -54) * mm, "end": v(-191, -54) * mm});
            skLineSegment(sketch, "E10.6.8.12", {"start": v(-201, -44) * mm, "end": v(-191, -44) * mm});
            skLineSegment(sketch, "E10.9.8.12", {"start": v(-191, -44) * mm, "end": v(-191, -54) * mm});
            skLineSegment(sketch, "E10.0.8.13", {"start": v(-201, -30) * mm, "end": v(-201, -40) * mm});
            skLineSegment(sketch, "E10.3.8.13", {"start": v(-201, -40) * mm, "end": v(-191, -40) * mm});
            skLineSegment(sketch, "E10.6.8.13", {"start": v(-201, -30) * mm, "end": v(-191, -30) * mm});
            skLineSegment(sketch, "E10.9.8.13", {"start": v(-191, -30) * mm, "end": v(-191, -40) * mm});
            skLineSegment(sketch, "E10.0.8.14", {"start": v(-201, -16) * mm, "end": v(-201, -26) * mm});
            skLineSegment(sketch, "E10.3.8.14", {"start": v(-201, -26) * mm, "end": v(-191, -26) * mm});
            skLineSegment(sketch, "E10.6.8.14", {"start": v(-201, -16) * mm, "end": v(-191, -16) * mm});
            skLineSegment(sketch, "E10.9.8.14", {"start": v(-191, -16) * mm, "end": v(-191, -26) * mm});
            skLineSegment(sketch, "E10.0.8.15", {"start": v(-201, -2) * mm, "end": v(-201, -12) * mm});
            skLineSegment(sketch, "E10.3.8.15", {"start": v(-201, -12) * mm, "end": v(-191, -12) * mm});
            skLineSegment(sketch, "E10.6.8.15", {"start": v(-201, -2) * mm, "end": v(-191, -2) * mm});
            skLineSegment(sketch, "E10.9.8.15", {"start": v(-191, -2) * mm, "end": v(-191, -12) * mm});
            skLineSegment(sketch, "E10.0.8.16", {"start": v(-201, 12) * mm, "end": v(-201, 2) * mm});
            skLineSegment(sketch, "E10.3.8.16", {"start": v(-201, 2) * mm, "end": v(-191, 2) * mm});
            skLineSegment(sketch, "E10.6.8.16", {"start": v(-201, 12) * mm, "end": v(-191, 12) * mm});
            skLineSegment(sketch, "E10.9.8.16", {"start": v(-191, 12) * mm, "end": v(-191, 2) * mm});
            skLineSegment(sketch, "E10.0.8.17", {"start": v(-201, 26) * mm, "end": v(-201, 16) * mm});
            skLineSegment(sketch, "E10.3.8.17", {"start": v(-201, 16) * mm, "end": v(-191, 16) * mm});
            skLineSegment(sketch, "E10.6.8.17", {"start": v(-201, 26) * mm, "end": v(-191, 26) * mm});
            skLineSegment(sketch, "E10.9.8.17", {"start": v(-191, 26) * mm, "end": v(-191, 16) * mm});
            skLineSegment(sketch, "E10.0.8.18", {"start": v(-201, 40) * mm, "end": v(-201, 30) * mm});
            skLineSegment(sketch, "E10.3.8.18", {"start": v(-201, 30) * mm, "end": v(-191, 30) * mm});
            skLineSegment(sketch, "E10.6.8.18", {"start": v(-201, 40) * mm, "end": v(-191, 40) * mm});
            skLineSegment(sketch, "E10.9.8.18", {"start": v(-191, 40) * mm, "end": v(-191, 30) * mm});
            skLineSegment(sketch, "E10.0.8.19", {"start": v(-201, 54) * mm, "end": v(-201, 44) * mm});
            skLineSegment(sketch, "E10.3.8.19", {"start": v(-201, 44) * mm, "end": v(-191, 44) * mm});
            skLineSegment(sketch, "E10.6.8.19", {"start": v(-201, 54) * mm, "end": v(-191, 54) * mm});
            skLineSegment(sketch, "E10.9.8.19", {"start": v(-191, 54) * mm, "end": v(-191, 44) * mm});
            skLineSegment(sketch, "E10.0.8.20", {"start": v(-201, 68) * mm, "end": v(-201, 58) * mm});
            skLineSegment(sketch, "E10.3.8.20", {"start": v(-201, 58) * mm, "end": v(-191, 58) * mm});
            skLineSegment(sketch, "E10.6.8.20", {"start": v(-201, 68) * mm, "end": v(-191, 68) * mm});
            skLineSegment(sketch, "E10.9.8.20", {"start": v(-191, 68) * mm, "end": v(-191, 58) * mm});
            skLineSegment(sketch, "E10.0.8.21", {"start": v(-201, 82) * mm, "end": v(-201, 72) * mm});
            skLineSegment(sketch, "E10.3.8.21", {"start": v(-201, 72) * mm, "end": v(-191, 72) * mm});
            skLineSegment(sketch, "E10.6.8.21", {"start": v(-201, 82) * mm, "end": v(-191, 82) * mm});
            skLineSegment(sketch, "E10.9.8.21", {"start": v(-191, 82) * mm, "end": v(-191, 72) * mm});
            skLineSegment(sketch, "E10.0.8.22", {"start": v(-201, 96) * mm, "end": v(-201, 86) * mm});
            skLineSegment(sketch, "E10.3.8.22", {"start": v(-201, 86) * mm, "end": v(-191, 86) * mm});
            skLineSegment(sketch, "E10.6.8.22", {"start": v(-201, 96) * mm, "end": v(-191, 96) * mm});
            skLineSegment(sketch, "E10.9.8.22", {"start": v(-191, 96) * mm, "end": v(-191, 86) * mm});
            skLineSegment(sketch, "E10.0.8.23", {"start": v(-201, 110) * mm, "end": v(-201, 100) * mm});
            skLineSegment(sketch, "E10.3.8.23", {"start": v(-201, 100) * mm, "end": v(-191, 100) * mm});
            skLineSegment(sketch, "E10.6.8.23", {"start": v(-201, 110) * mm, "end": v(-191, 110) * mm});
            skLineSegment(sketch, "E10.9.8.23", {"start": v(-191, 110) * mm, "end": v(-191, 100) * mm});
            skLineSegment(sketch, "E10.0.8.24", {"start": v(-201, 124) * mm, "end": v(-201, 114) * mm});
            skLineSegment(sketch, "E10.3.8.24", {"start": v(-201, 114) * mm, "end": v(-191, 114) * mm});
            skLineSegment(sketch, "E10.6.8.24", {"start": v(-201, 124) * mm, "end": v(-191, 124) * mm});
            skLineSegment(sketch, "E10.9.8.24", {"start": v(-191, 124) * mm, "end": v(-191, 114) * mm});
            skLineSegment(sketch, "E10.0.8.25", {"start": v(-201, 138) * mm, "end": v(-201, 128) * mm});
            skLineSegment(sketch, "E10.3.8.25", {"start": v(-201, 128) * mm, "end": v(-191, 128) * mm});
            skLineSegment(sketch, "E10.6.8.25", {"start": v(-201, 138) * mm, "end": v(-191, 138) * mm});
            skLineSegment(sketch, "E10.9.8.25", {"start": v(-191, 138) * mm, "end": v(-191, 128) * mm});
            skLineSegment(sketch, "E10.0.8.26", {"start": v(-201, 152) * mm, "end": v(-201, 142) * mm});
            skLineSegment(sketch, "E10.3.8.26", {"start": v(-201, 142) * mm, "end": v(-191, 142) * mm});
            skLineSegment(sketch, "E10.6.8.26", {"start": v(-201, 152) * mm, "end": v(-191, 152) * mm});
            skLineSegment(sketch, "E10.9.8.26", {"start": v(-191, 152) * mm, "end": v(-191, 142) * mm});
            skLineSegment(sketch, "E10.0.8.27", {"start": v(-201, 166) * mm, "end": v(-201, 156) * mm});
            skLineSegment(sketch, "E10.3.8.27", {"start": v(-201, 156) * mm, "end": v(-191, 156) * mm});
            skLineSegment(sketch, "E10.6.8.27", {"start": v(-201, 166) * mm, "end": v(-191, 166) * mm});
            skLineSegment(sketch, "E10.9.8.27", {"start": v(-191, 166) * mm, "end": v(-191, 156) * mm});
            skLineSegment(sketch, "E10.0.8.28", {"start": v(-201, 180) * mm, "end": v(-201, 170) * mm});
            skLineSegment(sketch, "E10.3.8.28", {"start": v(-201, 170) * mm, "end": v(-191, 170) * mm});
            skLineSegment(sketch, "E10.6.8.28", {"start": v(-201, 180) * mm, "end": v(-191, 180) * mm});
            skLineSegment(sketch, "E10.9.8.28", {"start": v(-191, 180) * mm, "end": v(-191, 170) * mm});
            skLineSegment(sketch, "E10.0.8.29", {"start": v(-201, 194) * mm, "end": v(-201, 184) * mm});
            skLineSegment(sketch, "E10.3.8.29", {"start": v(-201, 184) * mm, "end": v(-191, 184) * mm});
            skLineSegment(sketch, "E10.6.8.29", {"start": v(-201, 194) * mm, "end": v(-191, 194) * mm});
            skLineSegment(sketch, "E10.9.8.29", {"start": v(-191, 194) * mm, "end": v(-191, 184) * mm});
            skLineSegment(sketch, "E10.0.8.30", {"start": v(-201, 208) * mm, "end": v(-201, 198) * mm});
            skLineSegment(sketch, "E10.3.8.30", {"start": v(-201, 198) * mm, "end": v(-191, 198) * mm});
            skLineSegment(sketch, "E10.6.8.30", {"start": v(-201, 208) * mm, "end": v(-191, 208) * mm});
            skLineSegment(sketch, "E10.9.8.30", {"start": v(-191, 208) * mm, "end": v(-191, 198) * mm});
            skLineSegment(sketch, "E10.0.8.31", {"start": v(-201, 222) * mm, "end": v(-201, 212) * mm});
            skLineSegment(sketch, "E10.3.8.31", {"start": v(-201, 212) * mm, "end": v(-191, 212) * mm});
            skLineSegment(sketch, "E10.6.8.31", {"start": v(-201, 222) * mm, "end": v(-191, 222) * mm});
            skLineSegment(sketch, "E10.9.8.31", {"start": v(-191, 222) * mm, "end": v(-191, 212) * mm});
            skLineSegment(sketch, "E10.0.9.0", {"start": v(-187, -212) * mm, "end": v(-187, -222) * mm});
            skLineSegment(sketch, "E10.3.9.0", {"start": v(-187, -222) * mm, "end": v(-177, -222) * mm});
            skLineSegment(sketch, "E10.6.9.0", {"start": v(-187, -212) * mm, "end": v(-177, -212) * mm});
            skLineSegment(sketch, "E10.9.9.0", {"start": v(-177, -212) * mm, "end": v(-177, -222) * mm});
            skLineSegment(sketch, "E10.0.9.1", {"start": v(-187, -198) * mm, "end": v(-187, -208) * mm});
            skLineSegment(sketch, "E10.3.9.1", {"start": v(-187, -208) * mm, "end": v(-177, -208) * mm});
            skLineSegment(sketch, "E10.6.9.1", {"start": v(-187, -198) * mm, "end": v(-177, -198) * mm});
            skLineSegment(sketch, "E10.9.9.1", {"start": v(-177, -198) * mm, "end": v(-177, -208) * mm});
            skLineSegment(sketch, "E10.0.9.2", {"start": v(-187, -184) * mm, "end": v(-187, -194) * mm});
            skLineSegment(sketch, "E10.3.9.2", {"start": v(-187, -194) * mm, "end": v(-177, -194) * mm});
            skLineSegment(sketch, "E10.6.9.2", {"start": v(-187, -184) * mm, "end": v(-177, -184) * mm});
            skLineSegment(sketch, "E10.9.9.2", {"start": v(-177, -184) * mm, "end": v(-177, -194) * mm});
            skLineSegment(sketch, "E10.0.9.3", {"start": v(-187, -170) * mm, "end": v(-187, -180) * mm});
            skLineSegment(sketch, "E10.3.9.3", {"start": v(-187, -180) * mm, "end": v(-177, -180) * mm});
            skLineSegment(sketch, "E10.6.9.3", {"start": v(-187, -170) * mm, "end": v(-177, -170) * mm});
            skLineSegment(sketch, "E10.9.9.3", {"start": v(-177, -170) * mm, "end": v(-177, -180) * mm});
            skLineSegment(sketch, "E10.0.9.4", {"start": v(-187, -156) * mm, "end": v(-187, -166) * mm});
            skLineSegment(sketch, "E10.3.9.4", {"start": v(-187, -166) * mm, "end": v(-177, -166) * mm});
            skLineSegment(sketch, "E10.6.9.4", {"start": v(-187, -156) * mm, "end": v(-177, -156) * mm});
            skLineSegment(sketch, "E10.9.9.4", {"start": v(-177, -156) * mm, "end": v(-177, -166) * mm});
            skLineSegment(sketch, "E10.0.9.5", {"start": v(-187, -142) * mm, "end": v(-187, -152) * mm});
            skLineSegment(sketch, "E10.3.9.5", {"start": v(-187, -152) * mm, "end": v(-177, -152) * mm});
            skLineSegment(sketch, "E10.6.9.5", {"start": v(-187, -142) * mm, "end": v(-177, -142) * mm});
            skLineSegment(sketch, "E10.9.9.5", {"start": v(-177, -142) * mm, "end": v(-177, -152) * mm});
            skLineSegment(sketch, "E10.0.9.6", {"start": v(-187, -128) * mm, "end": v(-187, -138) * mm});
            skLineSegment(sketch, "E10.3.9.6", {"start": v(-187, -138) * mm, "end": v(-177, -138) * mm});
            skLineSegment(sketch, "E10.6.9.6", {"start": v(-187, -128) * mm, "end": v(-177, -128) * mm});
            skLineSegment(sketch, "E10.9.9.6", {"start": v(-177, -128) * mm, "end": v(-177, -138) * mm});
            skLineSegment(sketch, "E10.0.9.7", {"start": v(-187, -114) * mm, "end": v(-187, -124) * mm});
            skLineSegment(sketch, "E10.3.9.7", {"start": v(-187, -124) * mm, "end": v(-177, -124) * mm});
            skLineSegment(sketch, "E10.6.9.7", {"start": v(-187, -114) * mm, "end": v(-177, -114) * mm});
            skLineSegment(sketch, "E10.9.9.7", {"start": v(-177, -114) * mm, "end": v(-177, -124) * mm});
            skLineSegment(sketch, "E10.0.9.8", {"start": v(-187, -100) * mm, "end": v(-187, -110) * mm});
            skLineSegment(sketch, "E10.3.9.8", {"start": v(-187, -110) * mm, "end": v(-177, -110) * mm});
            skLineSegment(sketch, "E10.6.9.8", {"start": v(-187, -100) * mm, "end": v(-177, -100) * mm});
            skLineSegment(sketch, "E10.9.9.8", {"start": v(-177, -100) * mm, "end": v(-177, -110) * mm});
            skLineSegment(sketch, "E10.0.9.9", {"start": v(-187, -86) * mm, "end": v(-187, -96) * mm});
            skLineSegment(sketch, "E10.3.9.9", {"start": v(-187, -96) * mm, "end": v(-177, -96) * mm});
            skLineSegment(sketch, "E10.6.9.9", {"start": v(-187, -86) * mm, "end": v(-177, -86) * mm});
            skLineSegment(sketch, "E10.9.9.9", {"start": v(-177, -86) * mm, "end": v(-177, -96) * mm});
            skLineSegment(sketch, "E10.0.9.10", {"start": v(-187, -72) * mm, "end": v(-187, -82) * mm});
            skLineSegment(sketch, "E10.3.9.10", {"start": v(-187, -82) * mm, "end": v(-177, -82) * mm});
            skLineSegment(sketch, "E10.6.9.10", {"start": v(-187, -72) * mm, "end": v(-177, -72) * mm});
            skLineSegment(sketch, "E10.9.9.10", {"start": v(-177, -72) * mm, "end": v(-177, -82) * mm});
            skLineSegment(sketch, "E10.0.9.11", {"start": v(-187, -58) * mm, "end": v(-187, -68) * mm});
            skLineSegment(sketch, "E10.3.9.11", {"start": v(-187, -68) * mm, "end": v(-177, -68) * mm});
            skLineSegment(sketch, "E10.6.9.11", {"start": v(-187, -58) * mm, "end": v(-177, -58) * mm});
            skLineSegment(sketch, "E10.9.9.11", {"start": v(-177, -58) * mm, "end": v(-177, -68) * mm});
            skLineSegment(sketch, "E10.0.9.12", {"start": v(-187, -44) * mm, "end": v(-187, -54) * mm});
            skLineSegment(sketch, "E10.3.9.12", {"start": v(-187, -54) * mm, "end": v(-177, -54) * mm});
            skLineSegment(sketch, "E10.6.9.12", {"start": v(-187, -44) * mm, "end": v(-177, -44) * mm});
            skLineSegment(sketch, "E10.9.9.12", {"start": v(-177, -44) * mm, "end": v(-177, -54) * mm});
            skLineSegment(sketch, "E10.0.9.13", {"start": v(-187, -30) * mm, "end": v(-187, -40) * mm});
            skLineSegment(sketch, "E10.3.9.13", {"start": v(-187, -40) * mm, "end": v(-177, -40) * mm});
            skLineSegment(sketch, "E10.6.9.13", {"start": v(-187, -30) * mm, "end": v(-177, -30) * mm});
            skLineSegment(sketch, "E10.9.9.13", {"start": v(-177, -30) * mm, "end": v(-177, -40) * mm});
            skLineSegment(sketch, "E10.0.9.14", {"start": v(-187, -16) * mm, "end": v(-187, -26) * mm});
            skLineSegment(sketch, "E10.3.9.14", {"start": v(-187, -26) * mm, "end": v(-177, -26) * mm});
            skLineSegment(sketch, "E10.6.9.14", {"start": v(-187, -16) * mm, "end": v(-177, -16) * mm});
            skLineSegment(sketch, "E10.9.9.14", {"start": v(-177, -16) * mm, "end": v(-177, -26) * mm});
            skLineSegment(sketch, "E10.0.9.15", {"start": v(-187, -2) * mm, "end": v(-187, -12) * mm});
            skLineSegment(sketch, "E10.3.9.15", {"start": v(-187, -12) * mm, "end": v(-177, -12) * mm});
            skLineSegment(sketch, "E10.6.9.15", {"start": v(-187, -2) * mm, "end": v(-177, -2) * mm});
            skLineSegment(sketch, "E10.9.9.15", {"start": v(-177, -2) * mm, "end": v(-177, -12) * mm});
            skLineSegment(sketch, "E10.0.9.16", {"start": v(-187, 12) * mm, "end": v(-187, 2) * mm});
            skLineSegment(sketch, "E10.3.9.16", {"start": v(-187, 2) * mm, "end": v(-177, 2) * mm});
            skLineSegment(sketch, "E10.6.9.16", {"start": v(-187, 12) * mm, "end": v(-177, 12) * mm});
            skLineSegment(sketch, "E10.9.9.16", {"start": v(-177, 12) * mm, "end": v(-177, 2) * mm});
            skLineSegment(sketch, "E10.0.9.17", {"start": v(-187, 26) * mm, "end": v(-187, 16) * mm});
            skLineSegment(sketch, "E10.3.9.17", {"start": v(-187, 16) * mm, "end": v(-177, 16) * mm});
            skLineSegment(sketch, "E10.6.9.17", {"start": v(-187, 26) * mm, "end": v(-177, 26) * mm});
            skLineSegment(sketch, "E10.9.9.17", {"start": v(-177, 26) * mm, "end": v(-177, 16) * mm});
            skLineSegment(sketch, "E10.0.9.18", {"start": v(-187, 40) * mm, "end": v(-187, 30) * mm});
            skLineSegment(sketch, "E10.3.9.18", {"start": v(-187, 30) * mm, "end": v(-177, 30) * mm});
            skLineSegment(sketch, "E10.6.9.18", {"start": v(-187, 40) * mm, "end": v(-177, 40) * mm});
            skLineSegment(sketch, "E10.9.9.18", {"start": v(-177, 40) * mm, "end": v(-177, 30) * mm});
            skLineSegment(sketch, "E10.0.9.19", {"start": v(-187, 54) * mm, "end": v(-187, 44) * mm});
            skLineSegment(sketch, "E10.3.9.19", {"start": v(-187, 44) * mm, "end": v(-177, 44) * mm});
            skLineSegment(sketch, "E10.6.9.19", {"start": v(-187, 54) * mm, "end": v(-177, 54) * mm});
            skLineSegment(sketch, "E10.9.9.19", {"start": v(-177, 54) * mm, "end": v(-177, 44) * mm});
            skLineSegment(sketch, "E10.0.9.20", {"start": v(-187, 68) * mm, "end": v(-187, 58) * mm});
            skLineSegment(sketch, "E10.3.9.20", {"start": v(-187, 58) * mm, "end": v(-177, 58) * mm});
            skLineSegment(sketch, "E10.6.9.20", {"start": v(-187, 68) * mm, "end": v(-177, 68) * mm});
            skLineSegment(sketch, "E10.9.9.20", {"start": v(-177, 68) * mm, "end": v(-177, 58) * mm});
            skLineSegment(sketch, "E10.0.9.21", {"start": v(-187, 82) * mm, "end": v(-187, 72) * mm});
            skLineSegment(sketch, "E10.3.9.21", {"start": v(-187, 72) * mm, "end": v(-177, 72) * mm});
            skLineSegment(sketch, "E10.6.9.21", {"start": v(-187, 82) * mm, "end": v(-177, 82) * mm});
            skLineSegment(sketch, "E10.9.9.21", {"start": v(-177, 82) * mm, "end": v(-177, 72) * mm});
            skLineSegment(sketch, "E10.0.9.22", {"start": v(-187, 96) * mm, "end": v(-187, 86) * mm});
            skLineSegment(sketch, "E10.3.9.22", {"start": v(-187, 86) * mm, "end": v(-177, 86) * mm});
            skLineSegment(sketch, "E10.6.9.22", {"start": v(-187, 96) * mm, "end": v(-177, 96) * mm});
            skLineSegment(sketch, "E10.9.9.22", {"start": v(-177, 96) * mm, "end": v(-177, 86) * mm});
            skLineSegment(sketch, "E10.0.9.23", {"start": v(-187, 110) * mm, "end": v(-187, 100) * mm});
            skLineSegment(sketch, "E10.3.9.23", {"start": v(-187, 100) * mm, "end": v(-177, 100) * mm});
            skLineSegment(sketch, "E10.6.9.23", {"start": v(-187, 110) * mm, "end": v(-177, 110) * mm});
            skLineSegment(sketch, "E10.9.9.23", {"start": v(-177, 110) * mm, "end": v(-177, 100) * mm});
            skLineSegment(sketch, "E10.0.9.24", {"start": v(-187, 124) * mm, "end": v(-187, 114) * mm});
            skLineSegment(sketch, "E10.3.9.24", {"start": v(-187, 114) * mm, "end": v(-177, 114) * mm});
            skLineSegment(sketch, "E10.6.9.24", {"start": v(-187, 124) * mm, "end": v(-177, 124) * mm});
            skLineSegment(sketch, "E10.9.9.24", {"start": v(-177, 124) * mm, "end": v(-177, 114) * mm});
            skLineSegment(sketch, "E10.0.9.25", {"start": v(-187, 138) * mm, "end": v(-187, 128) * mm});
            skLineSegment(sketch, "E10.3.9.25", {"start": v(-187, 128) * mm, "end": v(-177, 128) * mm});
            skLineSegment(sketch, "E10.6.9.25", {"start": v(-187, 138) * mm, "end": v(-177, 138) * mm});
            skLineSegment(sketch, "E10.9.9.25", {"start": v(-177, 138) * mm, "end": v(-177, 128) * mm});
            skLineSegment(sketch, "E10.0.9.26", {"start": v(-187, 152) * mm, "end": v(-187, 142) * mm});
            skLineSegment(sketch, "E10.3.9.26", {"start": v(-187, 142) * mm, "end": v(-177, 142) * mm});
            skLineSegment(sketch, "E10.6.9.26", {"start": v(-187, 152) * mm, "end": v(-177, 152) * mm});
            skLineSegment(sketch, "E10.9.9.26", {"start": v(-177, 152) * mm, "end": v(-177, 142) * mm});
            skLineSegment(sketch, "E10.0.9.27", {"start": v(-187, 166) * mm, "end": v(-187, 156) * mm});
            skLineSegment(sketch, "E10.3.9.27", {"start": v(-187, 156) * mm, "end": v(-177, 156) * mm});
            skLineSegment(sketch, "E10.6.9.27", {"start": v(-187, 166) * mm, "end": v(-177, 166) * mm});
            skLineSegment(sketch, "E10.9.9.27", {"start": v(-177, 166) * mm, "end": v(-177, 156) * mm});
            skLineSegment(sketch, "E10.0.9.28", {"start": v(-187, 180) * mm, "end": v(-187, 170) * mm});
            skLineSegment(sketch, "E10.3.9.28", {"start": v(-187, 170) * mm, "end": v(-177, 170) * mm});
            skLineSegment(sketch, "E10.6.9.28", {"start": v(-187, 180) * mm, "end": v(-177, 180) * mm});
            skLineSegment(sketch, "E10.9.9.28", {"start": v(-177, 180) * mm, "end": v(-177, 170) * mm});
            skLineSegment(sketch, "E10.0.9.29", {"start": v(-187, 194) * mm, "end": v(-187, 184) * mm});
            skLineSegment(sketch, "E10.3.9.29", {"start": v(-187, 184) * mm, "end": v(-177, 184) * mm});
            skLineSegment(sketch, "E10.6.9.29", {"start": v(-187, 194) * mm, "end": v(-177, 194) * mm});
            skLineSegment(sketch, "E10.9.9.29", {"start": v(-177, 194) * mm, "end": v(-177, 184) * mm});
            skLineSegment(sketch, "E10.0.9.30", {"start": v(-187, 208) * mm, "end": v(-187, 198) * mm});
            skLineSegment(sketch, "E10.3.9.30", {"start": v(-187, 198) * mm, "end": v(-177, 198) * mm});
            skLineSegment(sketch, "E10.6.9.30", {"start": v(-187, 208) * mm, "end": v(-177, 208) * mm});
            skLineSegment(sketch, "E10.9.9.30", {"start": v(-177, 208) * mm, "end": v(-177, 198) * mm});
            skLineSegment(sketch, "E10.0.9.31", {"start": v(-187, 222) * mm, "end": v(-187, 212) * mm});
            skLineSegment(sketch, "E10.3.9.31", {"start": v(-187, 212) * mm, "end": v(-177, 212) * mm});
            skLineSegment(sketch, "E10.6.9.31", {"start": v(-187, 222) * mm, "end": v(-177, 222) * mm});
            skLineSegment(sketch, "E10.9.9.31", {"start": v(-177, 222) * mm, "end": v(-177, 212) * mm});
            skLineSegment(sketch, "E10.0.10.0", {"start": v(-173, -212) * mm, "end": v(-173, -222) * mm});
            skLineSegment(sketch, "E10.3.10.0", {"start": v(-173, -222) * mm, "end": v(-163, -222) * mm});
            skLineSegment(sketch, "E10.6.10.0", {"start": v(-173, -212) * mm, "end": v(-163, -212) * mm});
            skLineSegment(sketch, "E10.9.10.0", {"start": v(-163, -212) * mm, "end": v(-163, -222) * mm});
            skLineSegment(sketch, "E10.0.10.1", {"start": v(-173, -198) * mm, "end": v(-173, -208) * mm});
            skLineSegment(sketch, "E10.3.10.1", {"start": v(-173, -208) * mm, "end": v(-163, -208) * mm});
            skLineSegment(sketch, "E10.6.10.1", {"start": v(-173, -198) * mm, "end": v(-163, -198) * mm});
            skLineSegment(sketch, "E10.9.10.1", {"start": v(-163, -198) * mm, "end": v(-163, -208) * mm});
            skLineSegment(sketch, "E10.0.10.2", {"start": v(-173, -184) * mm, "end": v(-173, -194) * mm});
            skLineSegment(sketch, "E10.3.10.2", {"start": v(-173, -194) * mm, "end": v(-163, -194) * mm});
            skLineSegment(sketch, "E10.6.10.2", {"start": v(-173, -184) * mm, "end": v(-163, -184) * mm});
            skLineSegment(sketch, "E10.9.10.2", {"start": v(-163, -184) * mm, "end": v(-163, -194) * mm});
            skLineSegment(sketch, "E10.0.10.3", {"start": v(-173, -170) * mm, "end": v(-173, -180) * mm});
            skLineSegment(sketch, "E10.3.10.3", {"start": v(-173, -180) * mm, "end": v(-163, -180) * mm});
            skLineSegment(sketch, "E10.6.10.3", {"start": v(-173, -170) * mm, "end": v(-163, -170) * mm});
            skLineSegment(sketch, "E10.9.10.3", {"start": v(-163, -170) * mm, "end": v(-163, -180) * mm});
            skLineSegment(sketch, "E10.0.10.4", {"start": v(-173, -156) * mm, "end": v(-173, -166) * mm});
            skLineSegment(sketch, "E10.3.10.4", {"start": v(-173, -166) * mm, "end": v(-163, -166) * mm});
            skLineSegment(sketch, "E10.6.10.4", {"start": v(-173, -156) * mm, "end": v(-163, -156) * mm});
            skLineSegment(sketch, "E10.9.10.4", {"start": v(-163, -156) * mm, "end": v(-163, -166) * mm});
            skLineSegment(sketch, "E10.0.10.5", {"start": v(-173, -142) * mm, "end": v(-173, -152) * mm});
            skLineSegment(sketch, "E10.3.10.5", {"start": v(-173, -152) * mm, "end": v(-163, -152) * mm});
            skLineSegment(sketch, "E10.6.10.5", {"start": v(-173, -142) * mm, "end": v(-163, -142) * mm});
            skLineSegment(sketch, "E10.9.10.5", {"start": v(-163, -142) * mm, "end": v(-163, -152) * mm});
            skLineSegment(sketch, "E10.0.10.6", {"start": v(-173, -128) * mm, "end": v(-173, -138) * mm});
            skLineSegment(sketch, "E10.3.10.6", {"start": v(-173, -138) * mm, "end": v(-163, -138) * mm});
            skLineSegment(sketch, "E10.6.10.6", {"start": v(-173, -128) * mm, "end": v(-163, -128) * mm});
            skLineSegment(sketch, "E10.9.10.6", {"start": v(-163, -128) * mm, "end": v(-163, -138) * mm});
            skLineSegment(sketch, "E10.0.10.7", {"start": v(-173, -114) * mm, "end": v(-173, -124) * mm});
            skLineSegment(sketch, "E10.3.10.7", {"start": v(-173, -124) * mm, "end": v(-163, -124) * mm});
            skLineSegment(sketch, "E10.6.10.7", {"start": v(-173, -114) * mm, "end": v(-163, -114) * mm});
            skLineSegment(sketch, "E10.9.10.7", {"start": v(-163, -114) * mm, "end": v(-163, -124) * mm});
            skLineSegment(sketch, "E10.0.10.8", {"start": v(-173, -100) * mm, "end": v(-173, -110) * mm});
            skLineSegment(sketch, "E10.3.10.8", {"start": v(-173, -110) * mm, "end": v(-163, -110) * mm});
            skLineSegment(sketch, "E10.6.10.8", {"start": v(-173, -100) * mm, "end": v(-163, -100) * mm});
            skLineSegment(sketch, "E10.9.10.8", {"start": v(-163, -100) * mm, "end": v(-163, -110) * mm});
            skLineSegment(sketch, "E10.0.10.9", {"start": v(-173, -86) * mm, "end": v(-173, -96) * mm});
            skLineSegment(sketch, "E10.3.10.9", {"start": v(-173, -96) * mm, "end": v(-163, -96) * mm});
            skLineSegment(sketch, "E10.6.10.9", {"start": v(-173, -86) * mm, "end": v(-163, -86) * mm});
            skLineSegment(sketch, "E10.9.10.9", {"start": v(-163, -86) * mm, "end": v(-163, -96) * mm});
            skLineSegment(sketch, "E10.0.10.10", {"start": v(-173, -72) * mm, "end": v(-173, -82) * mm});
            skLineSegment(sketch, "E10.3.10.10", {"start": v(-173, -82) * mm, "end": v(-163, -82) * mm});
            skLineSegment(sketch, "E10.6.10.10", {"start": v(-173, -72) * mm, "end": v(-163, -72) * mm});
            skLineSegment(sketch, "E10.9.10.10", {"start": v(-163, -72) * mm, "end": v(-163, -82) * mm});
            skLineSegment(sketch, "E10.0.10.11", {"start": v(-173, -58) * mm, "end": v(-173, -68) * mm});
            skLineSegment(sketch, "E10.3.10.11", {"start": v(-173, -68) * mm, "end": v(-163, -68) * mm});
            skLineSegment(sketch, "E10.6.10.11", {"start": v(-173, -58) * mm, "end": v(-163, -58) * mm});
            skLineSegment(sketch, "E10.9.10.11", {"start": v(-163, -58) * mm, "end": v(-163, -68) * mm});
            skLineSegment(sketch, "E10.0.10.12", {"start": v(-173, -44) * mm, "end": v(-173, -54) * mm});
            skLineSegment(sketch, "E10.3.10.12", {"start": v(-173, -54) * mm, "end": v(-163, -54) * mm});
            skLineSegment(sketch, "E10.6.10.12", {"start": v(-173, -44) * mm, "end": v(-163, -44) * mm});
            skLineSegment(sketch, "E10.9.10.12", {"start": v(-163, -44) * mm, "end": v(-163, -54) * mm});
            skLineSegment(sketch, "E10.0.10.13", {"start": v(-173, -30) * mm, "end": v(-173, -40) * mm});
            skLineSegment(sketch, "E10.3.10.13", {"start": v(-173, -40) * mm, "end": v(-163, -40) * mm});
            skLineSegment(sketch, "E10.6.10.13", {"start": v(-173, -30) * mm, "end": v(-163, -30) * mm});
            skLineSegment(sketch, "E10.9.10.13", {"start": v(-163, -30) * mm, "end": v(-163, -40) * mm});
            skLineSegment(sketch, "E10.0.10.14", {"start": v(-173, -16) * mm, "end": v(-173, -26) * mm});
            skLineSegment(sketch, "E10.3.10.14", {"start": v(-173, -26) * mm, "end": v(-163, -26) * mm});
            skLineSegment(sketch, "E10.6.10.14", {"start": v(-173, -16) * mm, "end": v(-163, -16) * mm});
            skLineSegment(sketch, "E10.9.10.14", {"start": v(-163, -16) * mm, "end": v(-163, -26) * mm});
            skLineSegment(sketch, "E10.0.10.15", {"start": v(-173, -2) * mm, "end": v(-173, -12) * mm});
            skLineSegment(sketch, "E10.3.10.15", {"start": v(-173, -12) * mm, "end": v(-163, -12) * mm});
            skLineSegment(sketch, "E10.6.10.15", {"start": v(-173, -2) * mm, "end": v(-163, -2) * mm});
            skLineSegment(sketch, "E10.9.10.15", {"start": v(-163, -2) * mm, "end": v(-163, -12) * mm});
            skLineSegment(sketch, "E10.0.10.16", {"start": v(-173, 12) * mm, "end": v(-173, 2) * mm});
            skLineSegment(sketch, "E10.3.10.16", {"start": v(-173, 2) * mm, "end": v(-163, 2) * mm});
            skLineSegment(sketch, "E10.6.10.16", {"start": v(-173, 12) * mm, "end": v(-163, 12) * mm});
            skLineSegment(sketch, "E10.9.10.16", {"start": v(-163, 12) * mm, "end": v(-163, 2) * mm});
            skLineSegment(sketch, "E10.0.10.17", {"start": v(-173, 26) * mm, "end": v(-173, 16) * mm});
            skLineSegment(sketch, "E10.3.10.17", {"start": v(-173, 16) * mm, "end": v(-163, 16) * mm});
            skLineSegment(sketch, "E10.6.10.17", {"start": v(-173, 26) * mm, "end": v(-163, 26) * mm});
            skLineSegment(sketch, "E10.9.10.17", {"start": v(-163, 26) * mm, "end": v(-163, 16) * mm});
            skLineSegment(sketch, "E10.0.10.18", {"start": v(-173, 40) * mm, "end": v(-173, 30) * mm});
            skLineSegment(sketch, "E10.3.10.18", {"start": v(-173, 30) * mm, "end": v(-163, 30) * mm});
            skLineSegment(sketch, "E10.6.10.18", {"start": v(-173, 40) * mm, "end": v(-163, 40) * mm});
            skLineSegment(sketch, "E10.9.10.18", {"start": v(-163, 40) * mm, "end": v(-163, 30) * mm});
            skLineSegment(sketch, "E10.0.10.19", {"start": v(-173, 54) * mm, "end": v(-173, 44) * mm});
            skLineSegment(sketch, "E10.3.10.19", {"start": v(-173, 44) * mm, "end": v(-163, 44) * mm});
            skLineSegment(sketch, "E10.6.10.19", {"start": v(-173, 54) * mm, "end": v(-163, 54) * mm});
            skLineSegment(sketch, "E10.9.10.19", {"start": v(-163, 54) * mm, "end": v(-163, 44) * mm});
            skLineSegment(sketch, "E10.0.10.20", {"start": v(-173, 68) * mm, "end": v(-173, 58) * mm});
            skLineSegment(sketch, "E10.3.10.20", {"start": v(-173, 58) * mm, "end": v(-163, 58) * mm});
            skLineSegment(sketch, "E10.6.10.20", {"start": v(-173, 68) * mm, "end": v(-163, 68) * mm});
            skLineSegment(sketch, "E10.9.10.20", {"start": v(-163, 68) * mm, "end": v(-163, 58) * mm});
            skLineSegment(sketch, "E10.0.10.21", {"start": v(-173, 82) * mm, "end": v(-173, 72) * mm});
            skLineSegment(sketch, "E10.3.10.21", {"start": v(-173, 72) * mm, "end": v(-163, 72) * mm});
            skLineSegment(sketch, "E10.6.10.21", {"start": v(-173, 82) * mm, "end": v(-163, 82) * mm});
            skLineSegment(sketch, "E10.9.10.21", {"start": v(-163, 82) * mm, "end": v(-163, 72) * mm});
            skLineSegment(sketch, "E10.0.10.22", {"start": v(-173, 96) * mm, "end": v(-173, 86) * mm});
            skLineSegment(sketch, "E10.3.10.22", {"start": v(-173, 86) * mm, "end": v(-163, 86) * mm});
            skLineSegment(sketch, "E10.6.10.22", {"start": v(-173, 96) * mm, "end": v(-163, 96) * mm});
            skLineSegment(sketch, "E10.9.10.22", {"start": v(-163, 96) * mm, "end": v(-163, 86) * mm});
            skLineSegment(sketch, "E10.0.10.23", {"start": v(-173, 110) * mm, "end": v(-173, 100) * mm});
            skLineSegment(sketch, "E10.3.10.23", {"start": v(-173, 100) * mm, "end": v(-163, 100) * mm});
            skLineSegment(sketch, "E10.6.10.23", {"start": v(-173, 110) * mm, "end": v(-163, 110) * mm});
            skLineSegment(sketch, "E10.9.10.23", {"start": v(-163, 110) * mm, "end": v(-163, 100) * mm});
            skLineSegment(sketch, "E10.0.10.24", {"start": v(-173, 124) * mm, "end": v(-173, 114) * mm});
            skLineSegment(sketch, "E10.3.10.24", {"start": v(-173, 114) * mm, "end": v(-163, 114) * mm});
            skLineSegment(sketch, "E10.6.10.24", {"start": v(-173, 124) * mm, "end": v(-163, 124) * mm});
            skLineSegment(sketch, "E10.9.10.24", {"start": v(-163, 124) * mm, "end": v(-163, 114) * mm});
            skLineSegment(sketch, "E10.0.10.25", {"start": v(-173, 138) * mm, "end": v(-173, 128) * mm});
            skLineSegment(sketch, "E10.3.10.25", {"start": v(-173, 128) * mm, "end": v(-163, 128) * mm});
            skLineSegment(sketch, "E10.6.10.25", {"start": v(-173, 138) * mm, "end": v(-163, 138) * mm});
            skLineSegment(sketch, "E10.9.10.25", {"start": v(-163, 138) * mm, "end": v(-163, 128) * mm});
            skLineSegment(sketch, "E10.0.10.26", {"start": v(-173, 152) * mm, "end": v(-173, 142) * mm});
            skLineSegment(sketch, "E10.3.10.26", {"start": v(-173, 142) * mm, "end": v(-163, 142) * mm});
            skLineSegment(sketch, "E10.6.10.26", {"start": v(-173, 152) * mm, "end": v(-163, 152) * mm});
            skLineSegment(sketch, "E10.9.10.26", {"start": v(-163, 152) * mm, "end": v(-163, 142) * mm});
            skLineSegment(sketch, "E10.0.10.27", {"start": v(-173, 166) * mm, "end": v(-173, 156) * mm});
            skLineSegment(sketch, "E10.3.10.27", {"start": v(-173, 156) * mm, "end": v(-163, 156) * mm});
            skLineSegment(sketch, "E10.6.10.27", {"start": v(-173, 166) * mm, "end": v(-163, 166) * mm});
            skLineSegment(sketch, "E10.9.10.27", {"start": v(-163, 166) * mm, "end": v(-163, 156) * mm});
            skLineSegment(sketch, "E10.0.10.28", {"start": v(-173, 180) * mm, "end": v(-173, 170) * mm});
            skLineSegment(sketch, "E10.3.10.28", {"start": v(-173, 170) * mm, "end": v(-163, 170) * mm});
            skLineSegment(sketch, "E10.6.10.28", {"start": v(-173, 180) * mm, "end": v(-163, 180) * mm});
            skLineSegment(sketch, "E10.9.10.28", {"start": v(-163, 180) * mm, "end": v(-163, 170) * mm});
            skLineSegment(sketch, "E10.0.10.29", {"start": v(-173, 194) * mm, "end": v(-173, 184) * mm});
            skLineSegment(sketch, "E10.3.10.29", {"start": v(-173, 184) * mm, "end": v(-163, 184) * mm});
            skLineSegment(sketch, "E10.6.10.29", {"start": v(-173, 194) * mm, "end": v(-163, 194) * mm});
            skLineSegment(sketch, "E10.9.10.29", {"start": v(-163, 194) * mm, "end": v(-163, 184) * mm});
            skLineSegment(sketch, "E10.0.10.30", {"start": v(-173, 208) * mm, "end": v(-173, 198) * mm});
            skLineSegment(sketch, "E10.3.10.30", {"start": v(-173, 198) * mm, "end": v(-163, 198) * mm});
            skLineSegment(sketch, "E10.6.10.30", {"start": v(-173, 208) * mm, "end": v(-163, 208) * mm});
            skLineSegment(sketch, "E10.9.10.30", {"start": v(-163, 208) * mm, "end": v(-163, 198) * mm});
            skLineSegment(sketch, "E10.0.10.31", {"start": v(-173, 222) * mm, "end": v(-173, 212) * mm});
            skLineSegment(sketch, "E10.3.10.31", {"start": v(-173, 212) * mm, "end": v(-163, 212) * mm});
            skLineSegment(sketch, "E10.6.10.31", {"start": v(-173, 222) * mm, "end": v(-163, 222) * mm});
            skLineSegment(sketch, "E10.9.10.31", {"start": v(-163, 222) * mm, "end": v(-163, 212) * mm});
            skLineSegment(sketch, "E10.0.11.0", {"start": v(-159, -212) * mm, "end": v(-159, -222) * mm});
            skLineSegment(sketch, "E10.3.11.0", {"start": v(-159, -222) * mm, "end": v(-149, -222) * mm});
            skLineSegment(sketch, "E10.6.11.0", {"start": v(-159, -212) * mm, "end": v(-149, -212) * mm});
            skLineSegment(sketch, "E10.9.11.0", {"start": v(-149, -212) * mm, "end": v(-149, -222) * mm});
            skLineSegment(sketch, "E10.0.11.1", {"start": v(-159, -198) * mm, "end": v(-159, -208) * mm});
            skLineSegment(sketch, "E10.3.11.1", {"start": v(-159, -208) * mm, "end": v(-149, -208) * mm});
            skLineSegment(sketch, "E10.6.11.1", {"start": v(-159, -198) * mm, "end": v(-149, -198) * mm});
            skLineSegment(sketch, "E10.9.11.1", {"start": v(-149, -198) * mm, "end": v(-149, -208) * mm});
            skLineSegment(sketch, "E10.0.11.2", {"start": v(-159, -184) * mm, "end": v(-159, -194) * mm});
            skLineSegment(sketch, "E10.3.11.2", {"start": v(-159, -194) * mm, "end": v(-149, -194) * mm});
            skLineSegment(sketch, "E10.6.11.2", {"start": v(-159, -184) * mm, "end": v(-149, -184) * mm});
            skLineSegment(sketch, "E10.9.11.2", {"start": v(-149, -184) * mm, "end": v(-149, -194) * mm});
            skLineSegment(sketch, "E10.0.11.3", {"start": v(-159, -170) * mm, "end": v(-159, -180) * mm});
            skLineSegment(sketch, "E10.3.11.3", {"start": v(-159, -180) * mm, "end": v(-149, -180) * mm});
            skLineSegment(sketch, "E10.6.11.3", {"start": v(-159, -170) * mm, "end": v(-149, -170) * mm});
            skLineSegment(sketch, "E10.9.11.3", {"start": v(-149, -170) * mm, "end": v(-149, -180) * mm});
            skLineSegment(sketch, "E10.0.11.4", {"start": v(-159, -156) * mm, "end": v(-159, -166) * mm});
            skLineSegment(sketch, "E10.3.11.4", {"start": v(-159, -166) * mm, "end": v(-149, -166) * mm});
            skLineSegment(sketch, "E10.6.11.4", {"start": v(-159, -156) * mm, "end": v(-149, -156) * mm});
            skLineSegment(sketch, "E10.9.11.4", {"start": v(-149, -156) * mm, "end": v(-149, -166) * mm});
            skLineSegment(sketch, "E10.0.11.5", {"start": v(-159, -142) * mm, "end": v(-159, -152) * mm});
            skLineSegment(sketch, "E10.3.11.5", {"start": v(-159, -152) * mm, "end": v(-149, -152) * mm});
            skLineSegment(sketch, "E10.6.11.5", {"start": v(-159, -142) * mm, "end": v(-149, -142) * mm});
            skLineSegment(sketch, "E10.9.11.5", {"start": v(-149, -142) * mm, "end": v(-149, -152) * mm});
            skLineSegment(sketch, "E10.0.11.6", {"start": v(-159, -128) * mm, "end": v(-159, -138) * mm});
            skLineSegment(sketch, "E10.3.11.6", {"start": v(-159, -138) * mm, "end": v(-149, -138) * mm});
            skLineSegment(sketch, "E10.6.11.6", {"start": v(-159, -128) * mm, "end": v(-149, -128) * mm});
            skLineSegment(sketch, "E10.9.11.6", {"start": v(-149, -128) * mm, "end": v(-149, -138) * mm});
            skLineSegment(sketch, "E10.0.11.7", {"start": v(-159, -114) * mm, "end": v(-159, -124) * mm});
            skLineSegment(sketch, "E10.3.11.7", {"start": v(-159, -124) * mm, "end": v(-149, -124) * mm});
            skLineSegment(sketch, "E10.6.11.7", {"start": v(-159, -114) * mm, "end": v(-149, -114) * mm});
            skLineSegment(sketch, "E10.9.11.7", {"start": v(-149, -114) * mm, "end": v(-149, -124) * mm});
            skLineSegment(sketch, "E10.0.11.8", {"start": v(-159, -100) * mm, "end": v(-159, -110) * mm});
            skLineSegment(sketch, "E10.3.11.8", {"start": v(-159, -110) * mm, "end": v(-149, -110) * mm});
            skLineSegment(sketch, "E10.6.11.8", {"start": v(-159, -100) * mm, "end": v(-149, -100) * mm});
            skLineSegment(sketch, "E10.9.11.8", {"start": v(-149, -100) * mm, "end": v(-149, -110) * mm});
            skLineSegment(sketch, "E10.0.11.9", {"start": v(-159, -86) * mm, "end": v(-159, -96) * mm});
            skLineSegment(sketch, "E10.3.11.9", {"start": v(-159, -96) * mm, "end": v(-149, -96) * mm});
            skLineSegment(sketch, "E10.6.11.9", {"start": v(-159, -86) * mm, "end": v(-149, -86) * mm});
            skLineSegment(sketch, "E10.9.11.9", {"start": v(-149, -86) * mm, "end": v(-149, -96) * mm});
            skLineSegment(sketch, "E10.0.11.10", {"start": v(-159, -72) * mm, "end": v(-159, -82) * mm});
            skLineSegment(sketch, "E10.3.11.10", {"start": v(-159, -82) * mm, "end": v(-149, -82) * mm});
            skLineSegment(sketch, "E10.6.11.10", {"start": v(-159, -72) * mm, "end": v(-149, -72) * mm});
            skLineSegment(sketch, "E10.9.11.10", {"start": v(-149, -72) * mm, "end": v(-149, -82) * mm});
            skLineSegment(sketch, "E10.0.11.11", {"start": v(-159, -58) * mm, "end": v(-159, -68) * mm});
            skLineSegment(sketch, "E10.3.11.11", {"start": v(-159, -68) * mm, "end": v(-149, -68) * mm});
            skLineSegment(sketch, "E10.6.11.11", {"start": v(-159, -58) * mm, "end": v(-149, -58) * mm});
            skLineSegment(sketch, "E10.9.11.11", {"start": v(-149, -58) * mm, "end": v(-149, -68) * mm});
            skLineSegment(sketch, "E10.0.11.12", {"start": v(-159, -44) * mm, "end": v(-159, -54) * mm});
            skLineSegment(sketch, "E10.3.11.12", {"start": v(-159, -54) * mm, "end": v(-149, -54) * mm});
            skLineSegment(sketch, "E10.6.11.12", {"start": v(-159, -44) * mm, "end": v(-149, -44) * mm});
            skLineSegment(sketch, "E10.9.11.12", {"start": v(-149, -44) * mm, "end": v(-149, -54) * mm});
            skLineSegment(sketch, "E10.0.11.13", {"start": v(-159, -30) * mm, "end": v(-159, -40) * mm});
            skLineSegment(sketch, "E10.3.11.13", {"start": v(-159, -40) * mm, "end": v(-149, -40) * mm});
            skLineSegment(sketch, "E10.6.11.13", {"start": v(-159, -30) * mm, "end": v(-149, -30) * mm});
            skLineSegment(sketch, "E10.9.11.13", {"start": v(-149, -30) * mm, "end": v(-149, -40) * mm});
            skLineSegment(sketch, "E10.0.11.14", {"start": v(-159, -16) * mm, "end": v(-159, -26) * mm});
            skLineSegment(sketch, "E10.3.11.14", {"start": v(-159, -26) * mm, "end": v(-149, -26) * mm});
            skLineSegment(sketch, "E10.6.11.14", {"start": v(-159, -16) * mm, "end": v(-149, -16) * mm});
            skLineSegment(sketch, "E10.9.11.14", {"start": v(-149, -16) * mm, "end": v(-149, -26) * mm});
            skLineSegment(sketch, "E10.0.11.15", {"start": v(-159, -2) * mm, "end": v(-159, -12) * mm});
            skLineSegment(sketch, "E10.3.11.15", {"start": v(-159, -12) * mm, "end": v(-149, -12) * mm});
            skLineSegment(sketch, "E10.6.11.15", {"start": v(-159, -2) * mm, "end": v(-149, -2) * mm});
            skLineSegment(sketch, "E10.9.11.15", {"start": v(-149, -2) * mm, "end": v(-149, -12) * mm});
            skLineSegment(sketch, "E10.0.11.16", {"start": v(-159, 12) * mm, "end": v(-159, 2) * mm});
            skLineSegment(sketch, "E10.3.11.16", {"start": v(-159, 2) * mm, "end": v(-149, 2) * mm});
            skLineSegment(sketch, "E10.6.11.16", {"start": v(-159, 12) * mm, "end": v(-149, 12) * mm});
            skLineSegment(sketch, "E10.9.11.16", {"start": v(-149, 12) * mm, "end": v(-149, 2) * mm});
            skLineSegment(sketch, "E10.0.11.17", {"start": v(-159, 26) * mm, "end": v(-159, 16) * mm});
            skLineSegment(sketch, "E10.3.11.17", {"start": v(-159, 16) * mm, "end": v(-149, 16) * mm});
            skLineSegment(sketch, "E10.6.11.17", {"start": v(-159, 26) * mm, "end": v(-149, 26) * mm});
            skLineSegment(sketch, "E10.9.11.17", {"start": v(-149, 26) * mm, "end": v(-149, 16) * mm});
            skLineSegment(sketch, "E10.0.11.18", {"start": v(-159, 40) * mm, "end": v(-159, 30) * mm});
            skLineSegment(sketch, "E10.3.11.18", {"start": v(-159, 30) * mm, "end": v(-149, 30) * mm});
            skLineSegment(sketch, "E10.6.11.18", {"start": v(-159, 40) * mm, "end": v(-149, 40) * mm});
            skLineSegment(sketch, "E10.9.11.18", {"start": v(-149, 40) * mm, "end": v(-149, 30) * mm});
            skLineSegment(sketch, "E10.0.11.19", {"start": v(-159, 54) * mm, "end": v(-159, 44) * mm});
            skLineSegment(sketch, "E10.3.11.19", {"start": v(-159, 44) * mm, "end": v(-149, 44) * mm});
            skLineSegment(sketch, "E10.6.11.19", {"start": v(-159, 54) * mm, "end": v(-149, 54) * mm});
            skLineSegment(sketch, "E10.9.11.19", {"start": v(-149, 54) * mm, "end": v(-149, 44) * mm});
            skLineSegment(sketch, "E10.0.11.20", {"start": v(-159, 68) * mm, "end": v(-159, 58) * mm});
            skLineSegment(sketch, "E10.3.11.20", {"start": v(-159, 58) * mm, "end": v(-149, 58) * mm});
            skLineSegment(sketch, "E10.6.11.20", {"start": v(-159, 68) * mm, "end": v(-149, 68) * mm});
            skLineSegment(sketch, "E10.9.11.20", {"start": v(-149, 68) * mm, "end": v(-149, 58) * mm});
            skLineSegment(sketch, "E10.0.11.21", {"start": v(-159, 82) * mm, "end": v(-159, 72) * mm});
            skLineSegment(sketch, "E10.3.11.21", {"start": v(-159, 72) * mm, "end": v(-149, 72) * mm});
            skLineSegment(sketch, "E10.6.11.21", {"start": v(-159, 82) * mm, "end": v(-149, 82) * mm});
            skLineSegment(sketch, "E10.9.11.21", {"start": v(-149, 82) * mm, "end": v(-149, 72) * mm});
            skLineSegment(sketch, "E10.0.11.22", {"start": v(-159, 96) * mm, "end": v(-159, 86) * mm});
            skLineSegment(sketch, "E10.3.11.22", {"start": v(-159, 86) * mm, "end": v(-149, 86) * mm});
            skLineSegment(sketch, "E10.6.11.22", {"start": v(-159, 96) * mm, "end": v(-149, 96) * mm});
            skLineSegment(sketch, "E10.9.11.22", {"start": v(-149, 96) * mm, "end": v(-149, 86) * mm});
            skLineSegment(sketch, "E10.0.11.23", {"start": v(-159, 110) * mm, "end": v(-159, 100) * mm});
            skLineSegment(sketch, "E10.3.11.23", {"start": v(-159, 100) * mm, "end": v(-149, 100) * mm});
            skLineSegment(sketch, "E10.6.11.23", {"start": v(-159, 110) * mm, "end": v(-149, 110) * mm});
            skLineSegment(sketch, "E10.9.11.23", {"start": v(-149, 110) * mm, "end": v(-149, 100) * mm});
            skLineSegment(sketch, "E10.0.11.24", {"start": v(-159, 124) * mm, "end": v(-159, 114) * mm});
            skLineSegment(sketch, "E10.3.11.24", {"start": v(-159, 114) * mm, "end": v(-149, 114) * mm});
            skLineSegment(sketch, "E10.6.11.24", {"start": v(-159, 124) * mm, "end": v(-149, 124) * mm});
            skLineSegment(sketch, "E10.9.11.24", {"start": v(-149, 124) * mm, "end": v(-149, 114) * mm});
            skLineSegment(sketch, "E10.0.11.25", {"start": v(-159, 138) * mm, "end": v(-159, 128) * mm});
            skLineSegment(sketch, "E10.3.11.25", {"start": v(-159, 128) * mm, "end": v(-149, 128) * mm});
            skLineSegment(sketch, "E10.6.11.25", {"start": v(-159, 138) * mm, "end": v(-149, 138) * mm});
            skLineSegment(sketch, "E10.9.11.25", {"start": v(-149, 138) * mm, "end": v(-149, 128) * mm});
            skLineSegment(sketch, "E10.0.11.26", {"start": v(-159, 152) * mm, "end": v(-159, 142) * mm});
            skLineSegment(sketch, "E10.3.11.26", {"start": v(-159, 142) * mm, "end": v(-149, 142) * mm});
            skLineSegment(sketch, "E10.6.11.26", {"start": v(-159, 152) * mm, "end": v(-149, 152) * mm});
            skLineSegment(sketch, "E10.9.11.26", {"start": v(-149, 152) * mm, "end": v(-149, 142) * mm});
            skLineSegment(sketch, "E10.0.11.27", {"start": v(-159, 166) * mm, "end": v(-159, 156) * mm});
            skLineSegment(sketch, "E10.3.11.27", {"start": v(-159, 156) * mm, "end": v(-149, 156) * mm});
            skLineSegment(sketch, "E10.6.11.27", {"start": v(-159, 166) * mm, "end": v(-149, 166) * mm});
            skLineSegment(sketch, "E10.9.11.27", {"start": v(-149, 166) * mm, "end": v(-149, 156) * mm});
            skLineSegment(sketch, "E10.0.11.28", {"start": v(-159, 180) * mm, "end": v(-159, 170) * mm});
            skLineSegment(sketch, "E10.3.11.28", {"start": v(-159, 170) * mm, "end": v(-149, 170) * mm});
            skLineSegment(sketch, "E10.6.11.28", {"start": v(-159, 180) * mm, "end": v(-149, 180) * mm});
            skLineSegment(sketch, "E10.9.11.28", {"start": v(-149, 180) * mm, "end": v(-149, 170) * mm});
            skLineSegment(sketch, "E10.0.11.29", {"start": v(-159, 194) * mm, "end": v(-159, 184) * mm});
            skLineSegment(sketch, "E10.3.11.29", {"start": v(-159, 184) * mm, "end": v(-149, 184) * mm});
            skLineSegment(sketch, "E10.6.11.29", {"start": v(-159, 194) * mm, "end": v(-149, 194) * mm});
            skLineSegment(sketch, "E10.9.11.29", {"start": v(-149, 194) * mm, "end": v(-149, 184) * mm});
            skLineSegment(sketch, "E10.0.11.30", {"start": v(-159, 208) * mm, "end": v(-159, 198) * mm});
            skLineSegment(sketch, "E10.3.11.30", {"start": v(-159, 198) * mm, "end": v(-149, 198) * mm});
            skLineSegment(sketch, "E10.6.11.30", {"start": v(-159, 208) * mm, "end": v(-149, 208) * mm});
            skLineSegment(sketch, "E10.9.11.30", {"start": v(-149, 208) * mm, "end": v(-149, 198) * mm});
            skLineSegment(sketch, "E10.0.11.31", {"start": v(-159, 222) * mm, "end": v(-159, 212) * mm});
            skLineSegment(sketch, "E10.3.11.31", {"start": v(-159, 212) * mm, "end": v(-149, 212) * mm});
            skLineSegment(sketch, "E10.6.11.31", {"start": v(-159, 222) * mm, "end": v(-149, 222) * mm});
            skLineSegment(sketch, "E10.9.11.31", {"start": v(-149, 222) * mm, "end": v(-149, 212) * mm});
            skLineSegment(sketch, "E10.0.12.0", {"start": v(-145, -212) * mm, "end": v(-145, -222) * mm});
            skLineSegment(sketch, "E10.3.12.0", {"start": v(-145, -222) * mm, "end": v(-135, -222) * mm});
            skLineSegment(sketch, "E10.6.12.0", {"start": v(-145, -212) * mm, "end": v(-135, -212) * mm});
            skLineSegment(sketch, "E10.9.12.0", {"start": v(-135, -212) * mm, "end": v(-135, -222) * mm});
            skLineSegment(sketch, "E10.0.12.1", {"start": v(-145, -198) * mm, "end": v(-145, -208) * mm});
            skLineSegment(sketch, "E10.3.12.1", {"start": v(-145, -208) * mm, "end": v(-135, -208) * mm});
            skLineSegment(sketch, "E10.6.12.1", {"start": v(-145, -198) * mm, "end": v(-135, -198) * mm});
            skLineSegment(sketch, "E10.9.12.1", {"start": v(-135, -198) * mm, "end": v(-135, -208) * mm});
            skLineSegment(sketch, "E10.0.12.2", {"start": v(-145, -184) * mm, "end": v(-145, -194) * mm});
            skLineSegment(sketch, "E10.3.12.2", {"start": v(-145, -194) * mm, "end": v(-135, -194) * mm});
            skLineSegment(sketch, "E10.6.12.2", {"start": v(-145, -184) * mm, "end": v(-135, -184) * mm});
            skLineSegment(sketch, "E10.9.12.2", {"start": v(-135, -184) * mm, "end": v(-135, -194) * mm});
            skLineSegment(sketch, "E10.0.12.3", {"start": v(-145, -170) * mm, "end": v(-145, -180) * mm});
            skLineSegment(sketch, "E10.3.12.3", {"start": v(-145, -180) * mm, "end": v(-135, -180) * mm});
            skLineSegment(sketch, "E10.6.12.3", {"start": v(-145, -170) * mm, "end": v(-135, -170) * mm});
            skLineSegment(sketch, "E10.9.12.3", {"start": v(-135, -170) * mm, "end": v(-135, -180) * mm});
            skLineSegment(sketch, "E10.0.12.4", {"start": v(-145, -156) * mm, "end": v(-145, -166) * mm});
            skLineSegment(sketch, "E10.3.12.4", {"start": v(-145, -166) * mm, "end": v(-135, -166) * mm});
            skLineSegment(sketch, "E10.6.12.4", {"start": v(-145, -156) * mm, "end": v(-135, -156) * mm});
            skLineSegment(sketch, "E10.9.12.4", {"start": v(-135, -156) * mm, "end": v(-135, -166) * mm});
            skLineSegment(sketch, "E10.0.12.5", {"start": v(-145, -142) * mm, "end": v(-145, -152) * mm});
            skLineSegment(sketch, "E10.3.12.5", {"start": v(-145, -152) * mm, "end": v(-135, -152) * mm});
            skLineSegment(sketch, "E10.6.12.5", {"start": v(-145, -142) * mm, "end": v(-135, -142) * mm});
            skLineSegment(sketch, "E10.9.12.5", {"start": v(-135, -142) * mm, "end": v(-135, -152) * mm});
            skLineSegment(sketch, "E10.0.12.6", {"start": v(-145, -128) * mm, "end": v(-145, -138) * mm});
            skLineSegment(sketch, "E10.3.12.6", {"start": v(-145, -138) * mm, "end": v(-135, -138) * mm});
            skLineSegment(sketch, "E10.6.12.6", {"start": v(-145, -128) * mm, "end": v(-135, -128) * mm});
            skLineSegment(sketch, "E10.9.12.6", {"start": v(-135, -128) * mm, "end": v(-135, -138) * mm});
            skLineSegment(sketch, "E10.0.12.7", {"start": v(-145, -114) * mm, "end": v(-145, -124) * mm});
            skLineSegment(sketch, "E10.3.12.7", {"start": v(-145, -124) * mm, "end": v(-135, -124) * mm});
            skLineSegment(sketch, "E10.6.12.7", {"start": v(-145, -114) * mm, "end": v(-135, -114) * mm});
            skLineSegment(sketch, "E10.9.12.7", {"start": v(-135, -114) * mm, "end": v(-135, -124) * mm});
            skLineSegment(sketch, "E10.0.12.8", {"start": v(-145, -100) * mm, "end": v(-145, -110) * mm});
            skLineSegment(sketch, "E10.3.12.8", {"start": v(-145, -110) * mm, "end": v(-135, -110) * mm});
            skLineSegment(sketch, "E10.6.12.8", {"start": v(-145, -100) * mm, "end": v(-135, -100) * mm});
            skLineSegment(sketch, "E10.9.12.8", {"start": v(-135, -100) * mm, "end": v(-135, -110) * mm});
            skLineSegment(sketch, "E10.0.12.9", {"start": v(-145, -86) * mm, "end": v(-145, -96) * mm});
            skLineSegment(sketch, "E10.3.12.9", {"start": v(-145, -96) * mm, "end": v(-135, -96) * mm});
            skLineSegment(sketch, "E10.6.12.9", {"start": v(-145, -86) * mm, "end": v(-135, -86) * mm});
            skLineSegment(sketch, "E10.9.12.9", {"start": v(-135, -86) * mm, "end": v(-135, -96) * mm});
            skLineSegment(sketch, "E10.0.12.10", {"start": v(-145, -72) * mm, "end": v(-145, -82) * mm});
            skLineSegment(sketch, "E10.3.12.10", {"start": v(-145, -82) * mm, "end": v(-135, -82) * mm});
            skLineSegment(sketch, "E10.6.12.10", {"start": v(-145, -72) * mm, "end": v(-135, -72) * mm});
            skLineSegment(sketch, "E10.9.12.10", {"start": v(-135, -72) * mm, "end": v(-135, -82) * mm});
            skLineSegment(sketch, "E10.0.12.11", {"start": v(-145, -58) * mm, "end": v(-145, -68) * mm});
            skLineSegment(sketch, "E10.3.12.11", {"start": v(-145, -68) * mm, "end": v(-135, -68) * mm});
            skLineSegment(sketch, "E10.6.12.11", {"start": v(-145, -58) * mm, "end": v(-135, -58) * mm});
            skLineSegment(sketch, "E10.9.12.11", {"start": v(-135, -58) * mm, "end": v(-135, -68) * mm});
            skLineSegment(sketch, "E10.0.12.12", {"start": v(-145, -44) * mm, "end": v(-145, -54) * mm});
            skLineSegment(sketch, "E10.3.12.12", {"start": v(-145, -54) * mm, "end": v(-135, -54) * mm});
            skLineSegment(sketch, "E10.6.12.12", {"start": v(-145, -44) * mm, "end": v(-135, -44) * mm});
            skLineSegment(sketch, "E10.9.12.12", {"start": v(-135, -44) * mm, "end": v(-135, -54) * mm});
            skLineSegment(sketch, "E10.0.12.13", {"start": v(-145, -30) * mm, "end": v(-145, -40) * mm});
            skLineSegment(sketch, "E10.3.12.13", {"start": v(-145, -40) * mm, "end": v(-135, -40) * mm});
            skLineSegment(sketch, "E10.6.12.13", {"start": v(-145, -30) * mm, "end": v(-135, -30) * mm});
            skLineSegment(sketch, "E10.9.12.13", {"start": v(-135, -30) * mm, "end": v(-135, -40) * mm});
            skLineSegment(sketch, "E10.0.12.14", {"start": v(-145, -16) * mm, "end": v(-145, -26) * mm});
            skLineSegment(sketch, "E10.3.12.14", {"start": v(-145, -26) * mm, "end": v(-135, -26) * mm});
            skLineSegment(sketch, "E10.6.12.14", {"start": v(-145, -16) * mm, "end": v(-135, -16) * mm});
            skLineSegment(sketch, "E10.9.12.14", {"start": v(-135, -16) * mm, "end": v(-135, -26) * mm});
            skLineSegment(sketch, "E10.0.12.15", {"start": v(-145, -2) * mm, "end": v(-145, -12) * mm});
            skLineSegment(sketch, "E10.3.12.15", {"start": v(-145, -12) * mm, "end": v(-135, -12) * mm});
            skLineSegment(sketch, "E10.6.12.15", {"start": v(-145, -2) * mm, "end": v(-135, -2) * mm});
            skLineSegment(sketch, "E10.9.12.15", {"start": v(-135, -2) * mm, "end": v(-135, -12) * mm});
            skLineSegment(sketch, "E10.0.12.16", {"start": v(-145, 12) * mm, "end": v(-145, 2) * mm});
            skLineSegment(sketch, "E10.3.12.16", {"start": v(-145, 2) * mm, "end": v(-135, 2) * mm});
            skLineSegment(sketch, "E10.6.12.16", {"start": v(-145, 12) * mm, "end": v(-135, 12) * mm});
            skLineSegment(sketch, "E10.9.12.16", {"start": v(-135, 12) * mm, "end": v(-135, 2) * mm});
            skLineSegment(sketch, "E10.0.12.17", {"start": v(-145, 26) * mm, "end": v(-145, 16) * mm});
            skLineSegment(sketch, "E10.3.12.17", {"start": v(-145, 16) * mm, "end": v(-135, 16) * mm});
            skLineSegment(sketch, "E10.6.12.17", {"start": v(-145, 26) * mm, "end": v(-135, 26) * mm});
            skLineSegment(sketch, "E10.9.12.17", {"start": v(-135, 26) * mm, "end": v(-135, 16) * mm});
            skLineSegment(sketch, "E10.0.12.18", {"start": v(-145, 40) * mm, "end": v(-145, 30) * mm});
            skLineSegment(sketch, "E10.3.12.18", {"start": v(-145, 30) * mm, "end": v(-135, 30) * mm});
            skLineSegment(sketch, "E10.6.12.18", {"start": v(-145, 40) * mm, "end": v(-135, 40) * mm});
            skLineSegment(sketch, "E10.9.12.18", {"start": v(-135, 40) * mm, "end": v(-135, 30) * mm});
            skLineSegment(sketch, "E10.0.12.19", {"start": v(-145, 54) * mm, "end": v(-145, 44) * mm});
            skLineSegment(sketch, "E10.3.12.19", {"start": v(-145, 44) * mm, "end": v(-135, 44) * mm});
            skLineSegment(sketch, "E10.6.12.19", {"start": v(-145, 54) * mm, "end": v(-135, 54) * mm});
            skLineSegment(sketch, "E10.9.12.19", {"start": v(-135, 54) * mm, "end": v(-135, 44) * mm});
            skLineSegment(sketch, "E10.0.12.20", {"start": v(-145, 68) * mm, "end": v(-145, 58) * mm});
            skLineSegment(sketch, "E10.3.12.20", {"start": v(-145, 58) * mm, "end": v(-135, 58) * mm});
            skLineSegment(sketch, "E10.6.12.20", {"start": v(-145, 68) * mm, "end": v(-135, 68) * mm});
            skLineSegment(sketch, "E10.9.12.20", {"start": v(-135, 68) * mm, "end": v(-135, 58) * mm});
            skLineSegment(sketch, "E10.0.12.21", {"start": v(-145, 82) * mm, "end": v(-145, 72) * mm});
            skLineSegment(sketch, "E10.3.12.21", {"start": v(-145, 72) * mm, "end": v(-135, 72) * mm});
            skLineSegment(sketch, "E10.6.12.21", {"start": v(-145, 82) * mm, "end": v(-135, 82) * mm});
            skLineSegment(sketch, "E10.9.12.21", {"start": v(-135, 82) * mm, "end": v(-135, 72) * mm});
            skLineSegment(sketch, "E10.0.12.22", {"start": v(-145, 96) * mm, "end": v(-145, 86) * mm});
            skLineSegment(sketch, "E10.3.12.22", {"start": v(-145, 86) * mm, "end": v(-135, 86) * mm});
            skLineSegment(sketch, "E10.6.12.22", {"start": v(-145, 96) * mm, "end": v(-135, 96) * mm});
            skLineSegment(sketch, "E10.9.12.22", {"start": v(-135, 96) * mm, "end": v(-135, 86) * mm});
            skLineSegment(sketch, "E10.0.12.23", {"start": v(-145, 110) * mm, "end": v(-145, 100) * mm});
            skLineSegment(sketch, "E10.3.12.23", {"start": v(-145, 100) * mm, "end": v(-135, 100) * mm});
            skLineSegment(sketch, "E10.6.12.23", {"start": v(-145, 110) * mm, "end": v(-135, 110) * mm});
            skLineSegment(sketch, "E10.9.12.23", {"start": v(-135, 110) * mm, "end": v(-135, 100) * mm});
            skLineSegment(sketch, "E10.0.12.24", {"start": v(-145, 124) * mm, "end": v(-145, 114) * mm});
            skLineSegment(sketch, "E10.3.12.24", {"start": v(-145, 114) * mm, "end": v(-135, 114) * mm});
            skLineSegment(sketch, "E10.6.12.24", {"start": v(-145, 124) * mm, "end": v(-135, 124) * mm});
            skLineSegment(sketch, "E10.9.12.24", {"start": v(-135, 124) * mm, "end": v(-135, 114) * mm});
            skLineSegment(sketch, "E10.0.12.25", {"start": v(-145, 138) * mm, "end": v(-145, 128) * mm});
            skLineSegment(sketch, "E10.3.12.25", {"start": v(-145, 128) * mm, "end": v(-135, 128) * mm});
            skLineSegment(sketch, "E10.6.12.25", {"start": v(-145, 138) * mm, "end": v(-135, 138) * mm});
            skLineSegment(sketch, "E10.9.12.25", {"start": v(-135, 138) * mm, "end": v(-135, 128) * mm});
            skLineSegment(sketch, "E10.0.12.26", {"start": v(-145, 152) * mm, "end": v(-145, 142) * mm});
            skLineSegment(sketch, "E10.3.12.26", {"start": v(-145, 142) * mm, "end": v(-135, 142) * mm});
            skLineSegment(sketch, "E10.6.12.26", {"start": v(-145, 152) * mm, "end": v(-135, 152) * mm});
            skLineSegment(sketch, "E10.9.12.26", {"start": v(-135, 152) * mm, "end": v(-135, 142) * mm});
            skLineSegment(sketch, "E10.0.12.27", {"start": v(-145, 166) * mm, "end": v(-145, 156) * mm});
            skLineSegment(sketch, "E10.3.12.27", {"start": v(-145, 156) * mm, "end": v(-135, 156) * mm});
            skLineSegment(sketch, "E10.6.12.27", {"start": v(-145, 166) * mm, "end": v(-135, 166) * mm});
            skLineSegment(sketch, "E10.9.12.27", {"start": v(-135, 166) * mm, "end": v(-135, 156) * mm});
            skLineSegment(sketch, "E10.0.12.28", {"start": v(-145, 180) * mm, "end": v(-145, 170) * mm});
            skLineSegment(sketch, "E10.3.12.28", {"start": v(-145, 170) * mm, "end": v(-135, 170) * mm});
            skLineSegment(sketch, "E10.6.12.28", {"start": v(-145, 180) * mm, "end": v(-135, 180) * mm});
            skLineSegment(sketch, "E10.9.12.28", {"start": v(-135, 180) * mm, "end": v(-135, 170) * mm});
            skLineSegment(sketch, "E10.0.12.29", {"start": v(-145, 194) * mm, "end": v(-145, 184) * mm});
            skLineSegment(sketch, "E10.3.12.29", {"start": v(-145, 184) * mm, "end": v(-135, 184) * mm});
            skLineSegment(sketch, "E10.6.12.29", {"start": v(-145, 194) * mm, "end": v(-135, 194) * mm});
            skLineSegment(sketch, "E10.9.12.29", {"start": v(-135, 194) * mm, "end": v(-135, 184) * mm});
            skLineSegment(sketch, "E10.0.12.30", {"start": v(-145, 208) * mm, "end": v(-145, 198) * mm});
            skLineSegment(sketch, "E10.3.12.30", {"start": v(-145, 198) * mm, "end": v(-135, 198) * mm});
            skLineSegment(sketch, "E10.6.12.30", {"start": v(-145, 208) * mm, "end": v(-135, 208) * mm});
            skLineSegment(sketch, "E10.9.12.30", {"start": v(-135, 208) * mm, "end": v(-135, 198) * mm});
            skLineSegment(sketch, "E10.0.12.31", {"start": v(-145, 222) * mm, "end": v(-145, 212) * mm});
            skLineSegment(sketch, "E10.3.12.31", {"start": v(-145, 212) * mm, "end": v(-135, 212) * mm});
            skLineSegment(sketch, "E10.6.12.31", {"start": v(-145, 222) * mm, "end": v(-135, 222) * mm});
            skLineSegment(sketch, "E10.9.12.31", {"start": v(-135, 222) * mm, "end": v(-135, 212) * mm});
            skLineSegment(sketch, "E10.0.13.0", {"start": v(-131, -212) * mm, "end": v(-131, -222) * mm});
            skLineSegment(sketch, "E10.3.13.0", {"start": v(-131, -222) * mm, "end": v(-121, -222) * mm});
            skLineSegment(sketch, "E10.6.13.0", {"start": v(-131, -212) * mm, "end": v(-121, -212) * mm});
            skLineSegment(sketch, "E10.9.13.0", {"start": v(-121, -212) * mm, "end": v(-121, -222) * mm});
            skLineSegment(sketch, "E10.0.13.1", {"start": v(-131, -198) * mm, "end": v(-131, -208) * mm});
            skLineSegment(sketch, "E10.3.13.1", {"start": v(-131, -208) * mm, "end": v(-121, -208) * mm});
            skLineSegment(sketch, "E10.6.13.1", {"start": v(-131, -198) * mm, "end": v(-121, -198) * mm});
            skLineSegment(sketch, "E10.9.13.1", {"start": v(-121, -198) * mm, "end": v(-121, -208) * mm});
            skLineSegment(sketch, "E10.0.13.2", {"start": v(-131, -184) * mm, "end": v(-131, -194) * mm});
            skLineSegment(sketch, "E10.3.13.2", {"start": v(-131, -194) * mm, "end": v(-121, -194) * mm});
            skLineSegment(sketch, "E10.6.13.2", {"start": v(-131, -184) * mm, "end": v(-121, -184) * mm});
            skLineSegment(sketch, "E10.9.13.2", {"start": v(-121, -184) * mm, "end": v(-121, -194) * mm});
            skLineSegment(sketch, "E10.0.13.3", {"start": v(-131, -170) * mm, "end": v(-131, -180) * mm});
            skLineSegment(sketch, "E10.3.13.3", {"start": v(-131, -180) * mm, "end": v(-121, -180) * mm});
            skLineSegment(sketch, "E10.6.13.3", {"start": v(-131, -170) * mm, "end": v(-121, -170) * mm});
            skLineSegment(sketch, "E10.9.13.3", {"start": v(-121, -170) * mm, "end": v(-121, -180) * mm});
            skLineSegment(sketch, "E10.0.13.4", {"start": v(-131, -156) * mm, "end": v(-131, -166) * mm});
            skLineSegment(sketch, "E10.3.13.4", {"start": v(-131, -166) * mm, "end": v(-121, -166) * mm});
            skLineSegment(sketch, "E10.6.13.4", {"start": v(-131, -156) * mm, "end": v(-121, -156) * mm});
            skLineSegment(sketch, "E10.9.13.4", {"start": v(-121, -156) * mm, "end": v(-121, -166) * mm});
            skLineSegment(sketch, "E10.0.13.5", {"start": v(-131, -142) * mm, "end": v(-131, -152) * mm});
            skLineSegment(sketch, "E10.3.13.5", {"start": v(-131, -152) * mm, "end": v(-121, -152) * mm});
            skLineSegment(sketch, "E10.6.13.5", {"start": v(-131, -142) * mm, "end": v(-121, -142) * mm});
            skLineSegment(sketch, "E10.9.13.5", {"start": v(-121, -142) * mm, "end": v(-121, -152) * mm});
            skLineSegment(sketch, "E10.0.13.6", {"start": v(-131, -128) * mm, "end": v(-131, -138) * mm});
            skLineSegment(sketch, "E10.3.13.6", {"start": v(-131, -138) * mm, "end": v(-121, -138) * mm});
            skLineSegment(sketch, "E10.6.13.6", {"start": v(-131, -128) * mm, "end": v(-121, -128) * mm});
            skLineSegment(sketch, "E10.9.13.6", {"start": v(-121, -128) * mm, "end": v(-121, -138) * mm});
            skLineSegment(sketch, "E10.0.13.7", {"start": v(-131, -114) * mm, "end": v(-131, -124) * mm});
            skLineSegment(sketch, "E10.3.13.7", {"start": v(-131, -124) * mm, "end": v(-121, -124) * mm});
            skLineSegment(sketch, "E10.6.13.7", {"start": v(-131, -114) * mm, "end": v(-121, -114) * mm});
            skLineSegment(sketch, "E10.9.13.7", {"start": v(-121, -114) * mm, "end": v(-121, -124) * mm});
            skLineSegment(sketch, "E10.0.13.8", {"start": v(-131, -100) * mm, "end": v(-131, -110) * mm});
            skLineSegment(sketch, "E10.3.13.8", {"start": v(-131, -110) * mm, "end": v(-121, -110) * mm});
            skLineSegment(sketch, "E10.6.13.8", {"start": v(-131, -100) * mm, "end": v(-121, -100) * mm});
            skLineSegment(sketch, "E10.9.13.8", {"start": v(-121, -100) * mm, "end": v(-121, -110) * mm});
            skLineSegment(sketch, "E10.0.13.9", {"start": v(-131, -86) * mm, "end": v(-131, -96) * mm});
            skLineSegment(sketch, "E10.3.13.9", {"start": v(-131, -96) * mm, "end": v(-121, -96) * mm});
            skLineSegment(sketch, "E10.6.13.9", {"start": v(-131, -86) * mm, "end": v(-121, -86) * mm});
            skLineSegment(sketch, "E10.9.13.9", {"start": v(-121, -86) * mm, "end": v(-121, -96) * mm});
            skLineSegment(sketch, "E10.0.13.10", {"start": v(-131, -72) * mm, "end": v(-131, -82) * mm});
            skLineSegment(sketch, "E10.3.13.10", {"start": v(-131, -82) * mm, "end": v(-121, -82) * mm});
            skLineSegment(sketch, "E10.6.13.10", {"start": v(-131, -72) * mm, "end": v(-121, -72) * mm});
            skLineSegment(sketch, "E10.9.13.10", {"start": v(-121, -72) * mm, "end": v(-121, -82) * mm});
            skLineSegment(sketch, "E10.0.13.11", {"start": v(-131, -58) * mm, "end": v(-131, -68) * mm});
            skLineSegment(sketch, "E10.3.13.11", {"start": v(-131, -68) * mm, "end": v(-121, -68) * mm});
            skLineSegment(sketch, "E10.6.13.11", {"start": v(-131, -58) * mm, "end": v(-121, -58) * mm});
            skLineSegment(sketch, "E10.9.13.11", {"start": v(-121, -58) * mm, "end": v(-121, -68) * mm});
            skLineSegment(sketch, "E10.0.13.12", {"start": v(-131, -44) * mm, "end": v(-131, -54) * mm});
            skLineSegment(sketch, "E10.3.13.12", {"start": v(-131, -54) * mm, "end": v(-121, -54) * mm});
            skLineSegment(sketch, "E10.6.13.12", {"start": v(-131, -44) * mm, "end": v(-121, -44) * mm});
            skLineSegment(sketch, "E10.9.13.12", {"start": v(-121, -44) * mm, "end": v(-121, -54) * mm});
            skLineSegment(sketch, "E10.0.13.13", {"start": v(-131, -30) * mm, "end": v(-131, -40) * mm});
            skLineSegment(sketch, "E10.3.13.13", {"start": v(-131, -40) * mm, "end": v(-121, -40) * mm});
            skLineSegment(sketch, "E10.6.13.13", {"start": v(-131, -30) * mm, "end": v(-121, -30) * mm});
            skLineSegment(sketch, "E10.9.13.13", {"start": v(-121, -30) * mm, "end": v(-121, -40) * mm});
            skLineSegment(sketch, "E10.0.13.14", {"start": v(-131, -16) * mm, "end": v(-131, -26) * mm});
            skLineSegment(sketch, "E10.3.13.14", {"start": v(-131, -26) * mm, "end": v(-121, -26) * mm});
            skLineSegment(sketch, "E10.6.13.14", {"start": v(-131, -16) * mm, "end": v(-121, -16) * mm});
            skLineSegment(sketch, "E10.9.13.14", {"start": v(-121, -16) * mm, "end": v(-121, -26) * mm});
            skLineSegment(sketch, "E10.0.13.15", {"start": v(-131, -2) * mm, "end": v(-131, -12) * mm});
            skLineSegment(sketch, "E10.3.13.15", {"start": v(-131, -12) * mm, "end": v(-121, -12) * mm});
            skLineSegment(sketch, "E10.6.13.15", {"start": v(-131, -2) * mm, "end": v(-121, -2) * mm});
            skLineSegment(sketch, "E10.9.13.15", {"start": v(-121, -2) * mm, "end": v(-121, -12) * mm});
            skLineSegment(sketch, "E10.0.13.16", {"start": v(-131, 12) * mm, "end": v(-131, 2) * mm});
            skLineSegment(sketch, "E10.3.13.16", {"start": v(-131, 2) * mm, "end": v(-121, 2) * mm});
            skLineSegment(sketch, "E10.6.13.16", {"start": v(-131, 12) * mm, "end": v(-121, 12) * mm});
            skLineSegment(sketch, "E10.9.13.16", {"start": v(-121, 12) * mm, "end": v(-121, 2) * mm});
            skLineSegment(sketch, "E10.0.13.17", {"start": v(-131, 26) * mm, "end": v(-131, 16) * mm});
            skLineSegment(sketch, "E10.3.13.17", {"start": v(-131, 16) * mm, "end": v(-121, 16) * mm});
            skLineSegment(sketch, "E10.6.13.17", {"start": v(-131, 26) * mm, "end": v(-121, 26) * mm});
            skLineSegment(sketch, "E10.9.13.17", {"start": v(-121, 26) * mm, "end": v(-121, 16) * mm});
            skLineSegment(sketch, "E10.0.13.18", {"start": v(-131, 40) * mm, "end": v(-131, 30) * mm});
            skLineSegment(sketch, "E10.3.13.18", {"start": v(-131, 30) * mm, "end": v(-121, 30) * mm});
            skLineSegment(sketch, "E10.6.13.18", {"start": v(-131, 40) * mm, "end": v(-121, 40) * mm});
            skLineSegment(sketch, "E10.9.13.18", {"start": v(-121, 40) * mm, "end": v(-121, 30) * mm});
            skLineSegment(sketch, "E10.0.13.19", {"start": v(-131, 54) * mm, "end": v(-131, 44) * mm});
            skLineSegment(sketch, "E10.3.13.19", {"start": v(-131, 44) * mm, "end": v(-121, 44) * mm});
            skLineSegment(sketch, "E10.6.13.19", {"start": v(-131, 54) * mm, "end": v(-121, 54) * mm});
            skLineSegment(sketch, "E10.9.13.19", {"start": v(-121, 54) * mm, "end": v(-121, 44) * mm});
            skLineSegment(sketch, "E10.0.13.20", {"start": v(-131, 68) * mm, "end": v(-131, 58) * mm});
            skLineSegment(sketch, "E10.3.13.20", {"start": v(-131, 58) * mm, "end": v(-121, 58) * mm});
            skLineSegment(sketch, "E10.6.13.20", {"start": v(-131, 68) * mm, "end": v(-121, 68) * mm});
            skLineSegment(sketch, "E10.9.13.20", {"start": v(-121, 68) * mm, "end": v(-121, 58) * mm});
            skLineSegment(sketch, "E10.0.13.21", {"start": v(-131, 82) * mm, "end": v(-131, 72) * mm});
            skLineSegment(sketch, "E10.3.13.21", {"start": v(-131, 72) * mm, "end": v(-121, 72) * mm});
            skLineSegment(sketch, "E10.6.13.21", {"start": v(-131, 82) * mm, "end": v(-121, 82) * mm});
            skLineSegment(sketch, "E10.9.13.21", {"start": v(-121, 82) * mm, "end": v(-121, 72) * mm});
            skLineSegment(sketch, "E10.0.13.22", {"start": v(-131, 96) * mm, "end": v(-131, 86) * mm});
            skLineSegment(sketch, "E10.3.13.22", {"start": v(-131, 86) * mm, "end": v(-121, 86) * mm});
            skLineSegment(sketch, "E10.6.13.22", {"start": v(-131, 96) * mm, "end": v(-121, 96) * mm});
            skLineSegment(sketch, "E10.9.13.22", {"start": v(-121, 96) * mm, "end": v(-121, 86) * mm});
            skLineSegment(sketch, "E10.0.13.23", {"start": v(-131, 110) * mm, "end": v(-131, 100) * mm});
            skLineSegment(sketch, "E10.3.13.23", {"start": v(-131, 100) * mm, "end": v(-121, 100) * mm});
            skLineSegment(sketch, "E10.6.13.23", {"start": v(-131, 110) * mm, "end": v(-121, 110) * mm});
            skLineSegment(sketch, "E10.9.13.23", {"start": v(-121, 110) * mm, "end": v(-121, 100) * mm});
            skLineSegment(sketch, "E10.0.13.24", {"start": v(-131, 124) * mm, "end": v(-131, 114) * mm});
            skLineSegment(sketch, "E10.3.13.24", {"start": v(-131, 114) * mm, "end": v(-121, 114) * mm});
            skLineSegment(sketch, "E10.6.13.24", {"start": v(-131, 124) * mm, "end": v(-121, 124) * mm});
            skLineSegment(sketch, "E10.9.13.24", {"start": v(-121, 124) * mm, "end": v(-121, 114) * mm});
            skLineSegment(sketch, "E10.0.13.25", {"start": v(-131, 138) * mm, "end": v(-131, 128) * mm});
            skLineSegment(sketch, "E10.3.13.25", {"start": v(-131, 128) * mm, "end": v(-121, 128) * mm});
            skLineSegment(sketch, "E10.6.13.25", {"start": v(-131, 138) * mm, "end": v(-121, 138) * mm});
            skLineSegment(sketch, "E10.9.13.25", {"start": v(-121, 138) * mm, "end": v(-121, 128) * mm});
            skLineSegment(sketch, "E10.0.13.26", {"start": v(-131, 152) * mm, "end": v(-131, 142) * mm});
            skLineSegment(sketch, "E10.3.13.26", {"start": v(-131, 142) * mm, "end": v(-121, 142) * mm});
            skLineSegment(sketch, "E10.6.13.26", {"start": v(-131, 152) * mm, "end": v(-121, 152) * mm});
            skLineSegment(sketch, "E10.9.13.26", {"start": v(-121, 152) * mm, "end": v(-121, 142) * mm});
            skLineSegment(sketch, "E10.0.13.27", {"start": v(-131, 166) * mm, "end": v(-131, 156) * mm});
            skLineSegment(sketch, "E10.3.13.27", {"start": v(-131, 156) * mm, "end": v(-121, 156) * mm});
            skLineSegment(sketch, "E10.6.13.27", {"start": v(-131, 166) * mm, "end": v(-121, 166) * mm});
            skLineSegment(sketch, "E10.9.13.27", {"start": v(-121, 166) * mm, "end": v(-121, 156) * mm});
            skLineSegment(sketch, "E10.0.13.28", {"start": v(-131, 180) * mm, "end": v(-131, 170) * mm});
            skLineSegment(sketch, "E10.3.13.28", {"start": v(-131, 170) * mm, "end": v(-121, 170) * mm});
            skLineSegment(sketch, "E10.6.13.28", {"start": v(-131, 180) * mm, "end": v(-121, 180) * mm});
            skLineSegment(sketch, "E10.9.13.28", {"start": v(-121, 180) * mm, "end": v(-121, 170) * mm});
            skLineSegment(sketch, "E10.0.13.29", {"start": v(-131, 194) * mm, "end": v(-131, 184) * mm});
            skLineSegment(sketch, "E10.3.13.29", {"start": v(-131, 184) * mm, "end": v(-121, 184) * mm});
            skLineSegment(sketch, "E10.6.13.29", {"start": v(-131, 194) * mm, "end": v(-121, 194) * mm});
            skLineSegment(sketch, "E10.9.13.29", {"start": v(-121, 194) * mm, "end": v(-121, 184) * mm});
            skLineSegment(sketch, "E10.0.13.30", {"start": v(-131, 208) * mm, "end": v(-131, 198) * mm});
            skLineSegment(sketch, "E10.3.13.30", {"start": v(-131, 198) * mm, "end": v(-121, 198) * mm});
            skLineSegment(sketch, "E10.6.13.30", {"start": v(-131, 208) * mm, "end": v(-121, 208) * mm});
            skLineSegment(sketch, "E10.9.13.30", {"start": v(-121, 208) * mm, "end": v(-121, 198) * mm});
            skLineSegment(sketch, "E10.0.13.31", {"start": v(-131, 222) * mm, "end": v(-131, 212) * mm});
            skLineSegment(sketch, "E10.3.13.31", {"start": v(-131, 212) * mm, "end": v(-121, 212) * mm});
            skLineSegment(sketch, "E10.6.13.31", {"start": v(-131, 222) * mm, "end": v(-121, 222) * mm});
            skLineSegment(sketch, "E10.9.13.31", {"start": v(-121, 222) * mm, "end": v(-121, 212) * mm});
            skLineSegment(sketch, "E10.0.14.0", {"start": v(-117, -212) * mm, "end": v(-117, -222) * mm});
            skLineSegment(sketch, "E10.3.14.0", {"start": v(-117, -222) * mm, "end": v(-107, -222) * mm});
            skLineSegment(sketch, "E10.6.14.0", {"start": v(-117, -212) * mm, "end": v(-107, -212) * mm});
            skLineSegment(sketch, "E10.9.14.0", {"start": v(-107, -212) * mm, "end": v(-107, -222) * mm});
            skLineSegment(sketch, "E10.0.14.1", {"start": v(-117, -198) * mm, "end": v(-117, -208) * mm});
            skLineSegment(sketch, "E10.3.14.1", {"start": v(-117, -208) * mm, "end": v(-107, -208) * mm});
            skLineSegment(sketch, "E10.6.14.1", {"start": v(-117, -198) * mm, "end": v(-107, -198) * mm});
            skLineSegment(sketch, "E10.9.14.1", {"start": v(-107, -198) * mm, "end": v(-107, -208) * mm});
            skLineSegment(sketch, "E10.0.14.2", {"start": v(-117, -184) * mm, "end": v(-117, -194) * mm});
            skLineSegment(sketch, "E10.3.14.2", {"start": v(-117, -194) * mm, "end": v(-107, -194) * mm});
            skLineSegment(sketch, "E10.6.14.2", {"start": v(-117, -184) * mm, "end": v(-107, -184) * mm});
            skLineSegment(sketch, "E10.9.14.2", {"start": v(-107, -184) * mm, "end": v(-107, -194) * mm});
            skLineSegment(sketch, "E10.0.14.3", {"start": v(-117, -170) * mm, "end": v(-117, -180) * mm});
            skLineSegment(sketch, "E10.3.14.3", {"start": v(-117, -180) * mm, "end": v(-107, -180) * mm});
            skLineSegment(sketch, "E10.6.14.3", {"start": v(-117, -170) * mm, "end": v(-107, -170) * mm});
            skLineSegment(sketch, "E10.9.14.3", {"start": v(-107, -170) * mm, "end": v(-107, -180) * mm});
            skLineSegment(sketch, "E10.0.14.4", {"start": v(-117, -156) * mm, "end": v(-117, -166) * mm});
            skLineSegment(sketch, "E10.3.14.4", {"start": v(-117, -166) * mm, "end": v(-107, -166) * mm});
            skLineSegment(sketch, "E10.6.14.4", {"start": v(-117, -156) * mm, "end": v(-107, -156) * mm});
            skLineSegment(sketch, "E10.9.14.4", {"start": v(-107, -156) * mm, "end": v(-107, -166) * mm});
            skLineSegment(sketch, "E10.0.14.5", {"start": v(-117, -142) * mm, "end": v(-117, -152) * mm});
            skLineSegment(sketch, "E10.3.14.5", {"start": v(-117, -152) * mm, "end": v(-107, -152) * mm});
            skLineSegment(sketch, "E10.6.14.5", {"start": v(-117, -142) * mm, "end": v(-107, -142) * mm});
            skLineSegment(sketch, "E10.9.14.5", {"start": v(-107, -142) * mm, "end": v(-107, -152) * mm});
            skLineSegment(sketch, "E10.0.14.6", {"start": v(-117, -128) * mm, "end": v(-117, -138) * mm});
            skLineSegment(sketch, "E10.3.14.6", {"start": v(-117, -138) * mm, "end": v(-107, -138) * mm});
            skLineSegment(sketch, "E10.6.14.6", {"start": v(-117, -128) * mm, "end": v(-107, -128) * mm});
            skLineSegment(sketch, "E10.9.14.6", {"start": v(-107, -128) * mm, "end": v(-107, -138) * mm});
            skLineSegment(sketch, "E10.0.14.7", {"start": v(-117, -114) * mm, "end": v(-117, -124) * mm});
            skLineSegment(sketch, "E10.3.14.7", {"start": v(-117, -124) * mm, "end": v(-107, -124) * mm});
            skLineSegment(sketch, "E10.6.14.7", {"start": v(-117, -114) * mm, "end": v(-107, -114) * mm});
            skLineSegment(sketch, "E10.9.14.7", {"start": v(-107, -114) * mm, "end": v(-107, -124) * mm});
            skLineSegment(sketch, "E10.0.14.8", {"start": v(-117, -100) * mm, "end": v(-117, -110) * mm});
            skLineSegment(sketch, "E10.3.14.8", {"start": v(-117, -110) * mm, "end": v(-107, -110) * mm});
            skLineSegment(sketch, "E10.6.14.8", {"start": v(-117, -100) * mm, "end": v(-107, -100) * mm});
            skLineSegment(sketch, "E10.9.14.8", {"start": v(-107, -100) * mm, "end": v(-107, -110) * mm});
            skLineSegment(sketch, "E10.0.14.9", {"start": v(-117, -86) * mm, "end": v(-117, -96) * mm});
            skLineSegment(sketch, "E10.3.14.9", {"start": v(-117, -96) * mm, "end": v(-107, -96) * mm});
            skLineSegment(sketch, "E10.6.14.9", {"start": v(-117, -86) * mm, "end": v(-107, -86) * mm});
            skLineSegment(sketch, "E10.9.14.9", {"start": v(-107, -86) * mm, "end": v(-107, -96) * mm});
            skLineSegment(sketch, "E10.0.14.10", {"start": v(-117, -72) * mm, "end": v(-117, -82) * mm});
            skLineSegment(sketch, "E10.3.14.10", {"start": v(-117, -82) * mm, "end": v(-107, -82) * mm});
            skLineSegment(sketch, "E10.6.14.10", {"start": v(-117, -72) * mm, "end": v(-107, -72) * mm});
            skLineSegment(sketch, "E10.9.14.10", {"start": v(-107, -72) * mm, "end": v(-107, -82) * mm});
            skLineSegment(sketch, "E10.0.14.11", {"start": v(-117, -58) * mm, "end": v(-117, -68) * mm});
            skLineSegment(sketch, "E10.3.14.11", {"start": v(-117, -68) * mm, "end": v(-107, -68) * mm});
            skLineSegment(sketch, "E10.6.14.11", {"start": v(-117, -58) * mm, "end": v(-107, -58) * mm});
            skLineSegment(sketch, "E10.9.14.11", {"start": v(-107, -58) * mm, "end": v(-107, -68) * mm});
            skLineSegment(sketch, "E10.0.14.12", {"start": v(-117, -44) * mm, "end": v(-117, -54) * mm});
            skLineSegment(sketch, "E10.3.14.12", {"start": v(-117, -54) * mm, "end": v(-107, -54) * mm});
            skLineSegment(sketch, "E10.6.14.12", {"start": v(-117, -44) * mm, "end": v(-107, -44) * mm});
            skLineSegment(sketch, "E10.9.14.12", {"start": v(-107, -44) * mm, "end": v(-107, -54) * mm});
            skLineSegment(sketch, "E10.0.14.13", {"start": v(-117, -30) * mm, "end": v(-117, -40) * mm});
            skLineSegment(sketch, "E10.3.14.13", {"start": v(-117, -40) * mm, "end": v(-107, -40) * mm});
            skLineSegment(sketch, "E10.6.14.13", {"start": v(-117, -30) * mm, "end": v(-107, -30) * mm});
            skLineSegment(sketch, "E10.9.14.13", {"start": v(-107, -30) * mm, "end": v(-107, -40) * mm});
            skLineSegment(sketch, "E10.0.14.14", {"start": v(-117, -16) * mm, "end": v(-117, -26) * mm});
            skLineSegment(sketch, "E10.3.14.14", {"start": v(-117, -26) * mm, "end": v(-107, -26) * mm});
            skLineSegment(sketch, "E10.6.14.14", {"start": v(-117, -16) * mm, "end": v(-107, -16) * mm});
            skLineSegment(sketch, "E10.9.14.14", {"start": v(-107, -16) * mm, "end": v(-107, -26) * mm});
            skLineSegment(sketch, "E10.0.14.15", {"start": v(-117, -2) * mm, "end": v(-117, -12) * mm});
            skLineSegment(sketch, "E10.3.14.15", {"start": v(-117, -12) * mm, "end": v(-107, -12) * mm});
            skLineSegment(sketch, "E10.6.14.15", {"start": v(-117, -2) * mm, "end": v(-107, -2) * mm});
            skLineSegment(sketch, "E10.9.14.15", {"start": v(-107, -2) * mm, "end": v(-107, -12) * mm});
            skLineSegment(sketch, "E10.0.14.16", {"start": v(-117, 12) * mm, "end": v(-117, 2) * mm});
            skLineSegment(sketch, "E10.3.14.16", {"start": v(-117, 2) * mm, "end": v(-107, 2) * mm});
            skLineSegment(sketch, "E10.6.14.16", {"start": v(-117, 12) * mm, "end": v(-107, 12) * mm});
            skLineSegment(sketch, "E10.9.14.16", {"start": v(-107, 12) * mm, "end": v(-107, 2) * mm});
            skLineSegment(sketch, "E10.0.14.17", {"start": v(-117, 26) * mm, "end": v(-117, 16) * mm});
            skLineSegment(sketch, "E10.3.14.17", {"start": v(-117, 16) * mm, "end": v(-107, 16) * mm});
            skLineSegment(sketch, "E10.6.14.17", {"start": v(-117, 26) * mm, "end": v(-107, 26) * mm});
            skLineSegment(sketch, "E10.9.14.17", {"start": v(-107, 26) * mm, "end": v(-107, 16) * mm});
            skLineSegment(sketch, "E10.0.14.18", {"start": v(-117, 40) * mm, "end": v(-117, 30) * mm});
            skLineSegment(sketch, "E10.3.14.18", {"start": v(-117, 30) * mm, "end": v(-107, 30) * mm});
            skLineSegment(sketch, "E10.6.14.18", {"start": v(-117, 40) * mm, "end": v(-107, 40) * mm});
            skLineSegment(sketch, "E10.9.14.18", {"start": v(-107, 40) * mm, "end": v(-107, 30) * mm});
            skLineSegment(sketch, "E10.0.14.19", {"start": v(-117, 54) * mm, "end": v(-117, 44) * mm});
            skLineSegment(sketch, "E10.3.14.19", {"start": v(-117, 44) * mm, "end": v(-107, 44) * mm});
            skLineSegment(sketch, "E10.6.14.19", {"start": v(-117, 54) * mm, "end": v(-107, 54) * mm});
            skLineSegment(sketch, "E10.9.14.19", {"start": v(-107, 54) * mm, "end": v(-107, 44) * mm});
            skLineSegment(sketch, "E10.0.14.20", {"start": v(-117, 68) * mm, "end": v(-117, 58) * mm});
            skLineSegment(sketch, "E10.3.14.20", {"start": v(-117, 58) * mm, "end": v(-107, 58) * mm});
            skLineSegment(sketch, "E10.6.14.20", {"start": v(-117, 68) * mm, "end": v(-107, 68) * mm});
            skLineSegment(sketch, "E10.9.14.20", {"start": v(-107, 68) * mm, "end": v(-107, 58) * mm});
            skLineSegment(sketch, "E10.0.14.21", {"start": v(-117, 82) * mm, "end": v(-117, 72) * mm});
            skLineSegment(sketch, "E10.3.14.21", {"start": v(-117, 72) * mm, "end": v(-107, 72) * mm});
            skLineSegment(sketch, "E10.6.14.21", {"start": v(-117, 82) * mm, "end": v(-107, 82) * mm});
            skLineSegment(sketch, "E10.9.14.21", {"start": v(-107, 82) * mm, "end": v(-107, 72) * mm});
            skLineSegment(sketch, "E10.0.14.22", {"start": v(-117, 96) * mm, "end": v(-117, 86) * mm});
            skLineSegment(sketch, "E10.3.14.22", {"start": v(-117, 86) * mm, "end": v(-107, 86) * mm});
            skLineSegment(sketch, "E10.6.14.22", {"start": v(-117, 96) * mm, "end": v(-107, 96) * mm});
            skLineSegment(sketch, "E10.9.14.22", {"start": v(-107, 96) * mm, "end": v(-107, 86) * mm});
            skLineSegment(sketch, "E10.0.14.23", {"start": v(-117, 110) * mm, "end": v(-117, 100) * mm});
            skLineSegment(sketch, "E10.3.14.23", {"start": v(-117, 100) * mm, "end": v(-107, 100) * mm});
            skLineSegment(sketch, "E10.6.14.23", {"start": v(-117, 110) * mm, "end": v(-107, 110) * mm});
            skLineSegment(sketch, "E10.9.14.23", {"start": v(-107, 110) * mm, "end": v(-107, 100) * mm});
            skLineSegment(sketch, "E10.0.14.24", {"start": v(-117, 124) * mm, "end": v(-117, 114) * mm});
            skLineSegment(sketch, "E10.3.14.24", {"start": v(-117, 114) * mm, "end": v(-107, 114) * mm});
            skLineSegment(sketch, "E10.6.14.24", {"start": v(-117, 124) * mm, "end": v(-107, 124) * mm});
            skLineSegment(sketch, "E10.9.14.24", {"start": v(-107, 124) * mm, "end": v(-107, 114) * mm});
            skLineSegment(sketch, "E10.0.14.25", {"start": v(-117, 138) * mm, "end": v(-117, 128) * mm});
            skLineSegment(sketch, "E10.3.14.25", {"start": v(-117, 128) * mm, "end": v(-107, 128) * mm});
            skLineSegment(sketch, "E10.6.14.25", {"start": v(-117, 138) * mm, "end": v(-107, 138) * mm});
            skLineSegment(sketch, "E10.9.14.25", {"start": v(-107, 138) * mm, "end": v(-107, 128) * mm});
            skLineSegment(sketch, "E10.0.14.26", {"start": v(-117, 152) * mm, "end": v(-117, 142) * mm});
            skLineSegment(sketch, "E10.3.14.26", {"start": v(-117, 142) * mm, "end": v(-107, 142) * mm});
            skLineSegment(sketch, "E10.6.14.26", {"start": v(-117, 152) * mm, "end": v(-107, 152) * mm});
            skLineSegment(sketch, "E10.9.14.26", {"start": v(-107, 152) * mm, "end": v(-107, 142) * mm});
            skLineSegment(sketch, "E10.0.14.27", {"start": v(-117, 166) * mm, "end": v(-117, 156) * mm});
            skLineSegment(sketch, "E10.3.14.27", {"start": v(-117, 156) * mm, "end": v(-107, 156) * mm});
            skLineSegment(sketch, "E10.6.14.27", {"start": v(-117, 166) * mm, "end": v(-107, 166) * mm});
            skLineSegment(sketch, "E10.9.14.27", {"start": v(-107, 166) * mm, "end": v(-107, 156) * mm});
            skLineSegment(sketch, "E10.0.14.28", {"start": v(-117, 180) * mm, "end": v(-117, 170) * mm});
            skLineSegment(sketch, "E10.3.14.28", {"start": v(-117, 170) * mm, "end": v(-107, 170) * mm});
            skLineSegment(sketch, "E10.6.14.28", {"start": v(-117, 180) * mm, "end": v(-107, 180) * mm});
            skLineSegment(sketch, "E10.9.14.28", {"start": v(-107, 180) * mm, "end": v(-107, 170) * mm});
            skLineSegment(sketch, "E10.0.14.29", {"start": v(-117, 194) * mm, "end": v(-117, 184) * mm});
            skLineSegment(sketch, "E10.3.14.29", {"start": v(-117, 184) * mm, "end": v(-107, 184) * mm});
            skLineSegment(sketch, "E10.6.14.29", {"start": v(-117, 194) * mm, "end": v(-107, 194) * mm});
            skLineSegment(sketch, "E10.9.14.29", {"start": v(-107, 194) * mm, "end": v(-107, 184) * mm});
            skLineSegment(sketch, "E10.0.14.30", {"start": v(-117, 208) * mm, "end": v(-117, 198) * mm});
            skLineSegment(sketch, "E10.3.14.30", {"start": v(-117, 198) * mm, "end": v(-107, 198) * mm});
            skLineSegment(sketch, "E10.6.14.30", {"start": v(-117, 208) * mm, "end": v(-107, 208) * mm});
            skLineSegment(sketch, "E10.9.14.30", {"start": v(-107, 208) * mm, "end": v(-107, 198) * mm});
            skLineSegment(sketch, "E10.0.14.31", {"start": v(-117, 222) * mm, "end": v(-117, 212) * mm});
            skLineSegment(sketch, "E10.3.14.31", {"start": v(-117, 212) * mm, "end": v(-107, 212) * mm});
            skLineSegment(sketch, "E10.6.14.31", {"start": v(-117, 222) * mm, "end": v(-107, 222) * mm});
            skLineSegment(sketch, "E10.9.14.31", {"start": v(-107, 222) * mm, "end": v(-107, 212) * mm});
            skLineSegment(sketch, "E11.bottom", {"start": v(-103, -212) * mm, "end": v(-93, -212) * mm});
            skLineSegment(sketch, "E11.top", {"start": v(-103, -222) * mm, "end": v(-93, -222) * mm});
            skLineSegment(sketch, "E11.left", {"start": v(-103, -212) * mm, "end": v(-103, -222) * mm});
            skLineSegment(sketch, "E11.right", {"start": v(-93, -212) * mm, "end": v(-93, -222) * mm});
            skLineSegment(sketch, "E12.0.1.0", {"start": v(-103, -198) * mm, "end": v(-93, -198) * mm});
            skLineSegment(sketch, "E12.0.1.1", {"start": v(-93, -198) * mm, "end": v(-93, -208) * mm});
            skLineSegment(sketch, "E12.0.1.2", {"start": v(-103, -208) * mm, "end": v(-93, -208) * mm});
            skLineSegment(sketch, "E12.0.1.3", {"start": v(-103, -198) * mm, "end": v(-103, -208) * mm});
            skLineSegment(sketch, "E12.0.2.0", {"start": v(-103, -184) * mm, "end": v(-93, -184) * mm});
            skLineSegment(sketch, "E12.0.2.1", {"start": v(-93, -184) * mm, "end": v(-93, -194) * mm});
            skLineSegment(sketch, "E12.0.2.2", {"start": v(-103, -194) * mm, "end": v(-93, -194) * mm});
            skLineSegment(sketch, "E12.0.2.3", {"start": v(-103, -184) * mm, "end": v(-103, -194) * mm});
            skLineSegment(sketch, "E12.0.3.0", {"start": v(-103, -170) * mm, "end": v(-93, -170) * mm});
            skLineSegment(sketch, "E12.0.3.1", {"start": v(-93, -170) * mm, "end": v(-93, -180) * mm});
            skLineSegment(sketch, "E12.0.3.2", {"start": v(-103, -180) * mm, "end": v(-93, -180) * mm});
            skLineSegment(sketch, "E12.0.3.3", {"start": v(-103, -170) * mm, "end": v(-103, -180) * mm});
            skLineSegment(sketch, "E12.0.4.0", {"start": v(-103, -156) * mm, "end": v(-93, -156) * mm});
            skLineSegment(sketch, "E12.0.4.1", {"start": v(-93, -156) * mm, "end": v(-93, -166) * mm});
            skLineSegment(sketch, "E12.0.4.2", {"start": v(-103, -166) * mm, "end": v(-93, -166) * mm});
            skLineSegment(sketch, "E12.0.4.3", {"start": v(-103, -156) * mm, "end": v(-103, -166) * mm});
            skLineSegment(sketch, "E12.0.5.0", {"start": v(-103, -142) * mm, "end": v(-93, -142) * mm});
            skLineSegment(sketch, "E12.0.5.1", {"start": v(-93, -142) * mm, "end": v(-93, -152) * mm});
            skLineSegment(sketch, "E12.0.5.2", {"start": v(-103, -152) * mm, "end": v(-93, -152) * mm});
            skLineSegment(sketch, "E12.0.5.3", {"start": v(-103, -142) * mm, "end": v(-103, -152) * mm});
            skLineSegment(sketch, "E12.0.6.0", {"start": v(-103, -128) * mm, "end": v(-93, -128) * mm});
            skLineSegment(sketch, "E12.0.6.1", {"start": v(-93, -128) * mm, "end": v(-93, -138) * mm});
            skLineSegment(sketch, "E12.0.6.2", {"start": v(-103, -138) * mm, "end": v(-93, -138) * mm});
            skLineSegment(sketch, "E12.0.6.3", {"start": v(-103, -128) * mm, "end": v(-103, -138) * mm});
            skLineSegment(sketch, "E12.0.7.0", {"start": v(-103, -114) * mm, "end": v(-93, -114) * mm});
            skLineSegment(sketch, "E12.0.7.1", {"start": v(-93, -114) * mm, "end": v(-93, -124) * mm});
            skLineSegment(sketch, "E12.0.7.2", {"start": v(-103, -124) * mm, "end": v(-93, -124) * mm});
            skLineSegment(sketch, "E12.0.7.3", {"start": v(-103, -114) * mm, "end": v(-103, -124) * mm});
            skLineSegment(sketch, "E12.0.8.0", {"start": v(-103, -100) * mm, "end": v(-93, -100) * mm});
            skLineSegment(sketch, "E12.0.8.1", {"start": v(-93, -100) * mm, "end": v(-93, -110) * mm});
            skLineSegment(sketch, "E12.0.8.2", {"start": v(-103, -110) * mm, "end": v(-93, -110) * mm});
            skLineSegment(sketch, "E12.0.8.3", {"start": v(-103, -100) * mm, "end": v(-103, -110) * mm});
            skLineSegment(sketch, "E12.0.9.0", {"start": v(-103, -86) * mm, "end": v(-93, -86) * mm});
            skLineSegment(sketch, "E12.0.9.1", {"start": v(-93, -86) * mm, "end": v(-93, -96) * mm});
            skLineSegment(sketch, "E12.0.9.2", {"start": v(-103, -96) * mm, "end": v(-93, -96) * mm});
            skLineSegment(sketch, "E12.0.9.3", {"start": v(-103, -86) * mm, "end": v(-103, -96) * mm});
            skLineSegment(sketch, "E12.0.10.0", {"start": v(-103, -72) * mm, "end": v(-93, -72) * mm});
            skLineSegment(sketch, "E12.0.10.1", {"start": v(-93, -72) * mm, "end": v(-93, -82) * mm});
            skLineSegment(sketch, "E12.0.10.2", {"start": v(-103, -82) * mm, "end": v(-93, -82) * mm});
            skLineSegment(sketch, "E12.0.10.3", {"start": v(-103, -72) * mm, "end": v(-103, -82) * mm});
            skLineSegment(sketch, "E12.0.11.0", {"start": v(-103, -58) * mm, "end": v(-93, -58) * mm});
            skLineSegment(sketch, "E12.0.11.1", {"start": v(-93, -58) * mm, "end": v(-93, -68) * mm});
            skLineSegment(sketch, "E12.0.11.2", {"start": v(-103, -68) * mm, "end": v(-93, -68) * mm});
            skLineSegment(sketch, "E12.0.11.3", {"start": v(-103, -58) * mm, "end": v(-103, -68) * mm});
            skLineSegment(sketch, "E12.0.12.0", {"start": v(-103, -44) * mm, "end": v(-93, -44) * mm});
            skLineSegment(sketch, "E12.0.12.1", {"start": v(-93, -44) * mm, "end": v(-93, -54) * mm});
            skLineSegment(sketch, "E12.0.12.2", {"start": v(-103, -54) * mm, "end": v(-93, -54) * mm});
            skLineSegment(sketch, "E12.0.12.3", {"start": v(-103, -44) * mm, "end": v(-103, -54) * mm});
            skLineSegment(sketch, "E12.0.13.0", {"start": v(-103, -30) * mm, "end": v(-93, -30) * mm});
            skLineSegment(sketch, "E12.0.13.1", {"start": v(-93, -30) * mm, "end": v(-93, -40) * mm});
            skLineSegment(sketch, "E12.0.13.2", {"start": v(-103, -40) * mm, "end": v(-93, -40) * mm});
            skLineSegment(sketch, "E12.0.13.3", {"start": v(-103, -30) * mm, "end": v(-103, -40) * mm});
            skLineSegment(sketch, "E12.0.14.0", {"start": v(-103, -16) * mm, "end": v(-93, -16) * mm});
            skLineSegment(sketch, "E12.0.14.1", {"start": v(-93, -16) * mm, "end": v(-93, -26) * mm});
            skLineSegment(sketch, "E12.0.14.2", {"start": v(-103, -26) * mm, "end": v(-93, -26) * mm});
            skLineSegment(sketch, "E12.0.14.3", {"start": v(-103, -16) * mm, "end": v(-103, -26) * mm});
            skLineSegment(sketch, "E12.0.15.0", {"start": v(-103, -2) * mm, "end": v(-93, -2) * mm});
            skLineSegment(sketch, "E12.0.15.1", {"start": v(-93, -2) * mm, "end": v(-93, -12) * mm});
            skLineSegment(sketch, "E12.0.15.2", {"start": v(-103, -12) * mm, "end": v(-93, -12) * mm});
            skLineSegment(sketch, "E12.0.15.3", {"start": v(-103, -2) * mm, "end": v(-103, -12) * mm});
            skLineSegment(sketch, "E12.0.16.0", {"start": v(-103, 12) * mm, "end": v(-93, 12) * mm});
            skLineSegment(sketch, "E12.0.16.1", {"start": v(-93, 12) * mm, "end": v(-93, 2) * mm});
            skLineSegment(sketch, "E12.0.16.2", {"start": v(-103, 2) * mm, "end": v(-93, 2) * mm});
            skLineSegment(sketch, "E12.0.16.3", {"start": v(-103, 12) * mm, "end": v(-103, 2) * mm});
            skLineSegment(sketch, "E12.0.17.0", {"start": v(-103, 26) * mm, "end": v(-93, 26) * mm});
            skLineSegment(sketch, "E12.0.17.1", {"start": v(-93, 26) * mm, "end": v(-93, 16) * mm});
            skLineSegment(sketch, "E12.0.17.2", {"start": v(-103, 16) * mm, "end": v(-93, 16) * mm});
            skLineSegment(sketch, "E12.0.17.3", {"start": v(-103, 26) * mm, "end": v(-103, 16) * mm});
            skLineSegment(sketch, "E12.0.18.0", {"start": v(-103, 40) * mm, "end": v(-93, 40) * mm});
            skLineSegment(sketch, "E12.0.18.1", {"start": v(-93, 40) * mm, "end": v(-93, 30) * mm});
            skLineSegment(sketch, "E12.0.18.2", {"start": v(-103, 30) * mm, "end": v(-93, 30) * mm});
            skLineSegment(sketch, "E12.0.18.3", {"start": v(-103, 40) * mm, "end": v(-103, 30) * mm});
            skLineSegment(sketch, "E12.0.19.0", {"start": v(-103, 54) * mm, "end": v(-93, 54) * mm});
            skLineSegment(sketch, "E12.0.19.1", {"start": v(-93, 54) * mm, "end": v(-93, 44) * mm});
            skLineSegment(sketch, "E12.0.19.2", {"start": v(-103, 44) * mm, "end": v(-93, 44) * mm});
            skLineSegment(sketch, "E12.0.19.3", {"start": v(-103, 54) * mm, "end": v(-103, 44) * mm});
            skLineSegment(sketch, "E12.0.20.0", {"start": v(-103, 68) * mm, "end": v(-93, 68) * mm});
            skLineSegment(sketch, "E12.0.20.1", {"start": v(-93, 68) * mm, "end": v(-93, 58) * mm});
            skLineSegment(sketch, "E12.0.20.2", {"start": v(-103, 58) * mm, "end": v(-93, 58) * mm});
            skLineSegment(sketch, "E12.0.20.3", {"start": v(-103, 68) * mm, "end": v(-103, 58) * mm});
            skLineSegment(sketch, "E12.0.21.0", {"start": v(-103, 82) * mm, "end": v(-93, 82) * mm});
            skLineSegment(sketch, "E12.0.21.1", {"start": v(-93, 82) * mm, "end": v(-93, 72) * mm});
            skLineSegment(sketch, "E12.0.21.2", {"start": v(-103, 72) * mm, "end": v(-93, 72) * mm});
            skLineSegment(sketch, "E12.0.21.3", {"start": v(-103, 82) * mm, "end": v(-103, 72) * mm});
            skLineSegment(sketch, "E12.0.22.0", {"start": v(-103, 96) * mm, "end": v(-93, 96) * mm});
            skLineSegment(sketch, "E12.0.22.1", {"start": v(-93, 96) * mm, "end": v(-93, 86) * mm});
            skLineSegment(sketch, "E12.0.22.2", {"start": v(-103, 86) * mm, "end": v(-93, 86) * mm});
            skLineSegment(sketch, "E12.0.22.3", {"start": v(-103, 96) * mm, "end": v(-103, 86) * mm});
            skLineSegment(sketch, "E12.0.23.0", {"start": v(-103, 110) * mm, "end": v(-93, 110) * mm});
            skLineSegment(sketch, "E12.0.23.1", {"start": v(-93, 110) * mm, "end": v(-93, 100) * mm});
            skLineSegment(sketch, "E12.0.23.2", {"start": v(-103, 100) * mm, "end": v(-93, 100) * mm});
            skLineSegment(sketch, "E12.0.23.3", {"start": v(-103, 110) * mm, "end": v(-103, 100) * mm});
            skLineSegment(sketch, "E12.0.24.0", {"start": v(-103, 124) * mm, "end": v(-93, 124) * mm});
            skLineSegment(sketch, "E12.0.24.1", {"start": v(-93, 124) * mm, "end": v(-93, 114) * mm});
            skLineSegment(sketch, "E12.0.24.2", {"start": v(-103, 114) * mm, "end": v(-93, 114) * mm});
            skLineSegment(sketch, "E12.0.24.3", {"start": v(-103, 124) * mm, "end": v(-103, 114) * mm});
            skLineSegment(sketch, "E12.0.25.0", {"start": v(-103, 138) * mm, "end": v(-93, 138) * mm});
            skLineSegment(sketch, "E12.0.25.1", {"start": v(-93, 138) * mm, "end": v(-93, 128) * mm});
            skLineSegment(sketch, "E12.0.25.2", {"start": v(-103, 128) * mm, "end": v(-93, 128) * mm});
            skLineSegment(sketch, "E12.0.25.3", {"start": v(-103, 138) * mm, "end": v(-103, 128) * mm});
            skLineSegment(sketch, "E12.0.26.0", {"start": v(-103, 152) * mm, "end": v(-93, 152) * mm});
            skLineSegment(sketch, "E12.0.26.1", {"start": v(-93, 152) * mm, "end": v(-93, 142) * mm});
            skLineSegment(sketch, "E12.0.26.2", {"start": v(-103, 142) * mm, "end": v(-93, 142) * mm});
            skLineSegment(sketch, "E12.0.26.3", {"start": v(-103, 152) * mm, "end": v(-103, 142) * mm});
            skLineSegment(sketch, "E12.0.27.0", {"start": v(-103, 166) * mm, "end": v(-93, 166) * mm});
            skLineSegment(sketch, "E12.0.27.1", {"start": v(-93, 166) * mm, "end": v(-93, 156) * mm});
            skLineSegment(sketch, "E12.0.27.2", {"start": v(-103, 156) * mm, "end": v(-93, 156) * mm});
            skLineSegment(sketch, "E12.0.27.3", {"start": v(-103, 166) * mm, "end": v(-103, 156) * mm});
            skLineSegment(sketch, "E12.0.28.0", {"start": v(-103, 180) * mm, "end": v(-93, 180) * mm});
            skLineSegment(sketch, "E12.0.28.1", {"start": v(-93, 180) * mm, "end": v(-93, 170) * mm});
            skLineSegment(sketch, "E12.0.28.2", {"start": v(-103, 170) * mm, "end": v(-93, 170) * mm});
            skLineSegment(sketch, "E12.0.28.3", {"start": v(-103, 180) * mm, "end": v(-103, 170) * mm});
            skLineSegment(sketch, "E12.0.29.0", {"start": v(-103, 194) * mm, "end": v(-93, 194) * mm});
            skLineSegment(sketch, "E12.0.29.1", {"start": v(-93, 194) * mm, "end": v(-93, 184) * mm});
            skLineSegment(sketch, "E12.0.29.2", {"start": v(-103, 184) * mm, "end": v(-93, 184) * mm});
            skLineSegment(sketch, "E12.0.29.3", {"start": v(-103, 194) * mm, "end": v(-103, 184) * mm});
            skLineSegment(sketch, "E12.0.30.0", {"start": v(-103, 208) * mm, "end": v(-93, 208) * mm});
            skLineSegment(sketch, "E12.0.30.1", {"start": v(-93, 208) * mm, "end": v(-93, 198) * mm});
            skLineSegment(sketch, "E12.0.30.2", {"start": v(-103, 198) * mm, "end": v(-93, 198) * mm});
            skLineSegment(sketch, "E12.0.30.3", {"start": v(-103, 208) * mm, "end": v(-103, 198) * mm});
            skLineSegment(sketch, "E12.0.31.0", {"start": v(-103, 222) * mm, "end": v(-93, 222) * mm});
            skLineSegment(sketch, "E12.0.31.1", {"start": v(-93, 222) * mm, "end": v(-93, 212) * mm});
            skLineSegment(sketch, "E12.0.31.2", {"start": v(-103, 212) * mm, "end": v(-93, 212) * mm});
            skLineSegment(sketch, "E12.0.31.3", {"start": v(-103, 222) * mm, "end": v(-103, 212) * mm});
            skLineSegment(sketch, "E12.1.0.0", {"start": v(-89, -212) * mm, "end": v(-79, -212) * mm});
            skLineSegment(sketch, "E12.1.0.1", {"start": v(-79, -212) * mm, "end": v(-79, -222) * mm});
            skLineSegment(sketch, "E12.1.0.2", {"start": v(-89, -222) * mm, "end": v(-79, -222) * mm});
            skLineSegment(sketch, "E12.1.0.3", {"start": v(-89, -212) * mm, "end": v(-89, -222) * mm});
            skLineSegment(sketch, "E12.1.1.0", {"start": v(-89, -198) * mm, "end": v(-79, -198) * mm});
            skLineSegment(sketch, "E12.1.1.1", {"start": v(-79, -198) * mm, "end": v(-79, -208) * mm});
            skLineSegment(sketch, "E12.1.1.2", {"start": v(-89, -208) * mm, "end": v(-79, -208) * mm});
            skLineSegment(sketch, "E12.1.1.3", {"start": v(-89, -198) * mm, "end": v(-89, -208) * mm});
            skLineSegment(sketch, "E12.1.2.0", {"start": v(-89, -184) * mm, "end": v(-79, -184) * mm});
            skLineSegment(sketch, "E12.1.2.1", {"start": v(-79, -184) * mm, "end": v(-79, -194) * mm});
            skLineSegment(sketch, "E12.1.2.2", {"start": v(-89, -194) * mm, "end": v(-79, -194) * mm});
            skLineSegment(sketch, "E12.1.2.3", {"start": v(-89, -184) * mm, "end": v(-89, -194) * mm});
            skLineSegment(sketch, "E12.1.3.0", {"start": v(-89, -170) * mm, "end": v(-79, -170) * mm});
            skLineSegment(sketch, "E12.1.3.1", {"start": v(-79, -170) * mm, "end": v(-79, -180) * mm});
            skLineSegment(sketch, "E12.1.3.2", {"start": v(-89, -180) * mm, "end": v(-79, -180) * mm});
            skLineSegment(sketch, "E12.1.3.3", {"start": v(-89, -170) * mm, "end": v(-89, -180) * mm});
            skLineSegment(sketch, "E12.1.4.0", {"start": v(-89, -156) * mm, "end": v(-79, -156) * mm});
            skLineSegment(sketch, "E12.1.4.1", {"start": v(-79, -156) * mm, "end": v(-79, -166) * mm});
            skLineSegment(sketch, "E12.1.4.2", {"start": v(-89, -166) * mm, "end": v(-79, -166) * mm});
            skLineSegment(sketch, "E12.1.4.3", {"start": v(-89, -156) * mm, "end": v(-89, -166) * mm});
            skLineSegment(sketch, "E12.1.5.0", {"start": v(-89, -142) * mm, "end": v(-79, -142) * mm});
            skLineSegment(sketch, "E12.1.5.1", {"start": v(-79, -142) * mm, "end": v(-79, -152) * mm});
            skLineSegment(sketch, "E12.1.5.2", {"start": v(-89, -152) * mm, "end": v(-79, -152) * mm});
            skLineSegment(sketch, "E12.1.5.3", {"start": v(-89, -142) * mm, "end": v(-89, -152) * mm});
            skLineSegment(sketch, "E12.1.6.0", {"start": v(-89, -128) * mm, "end": v(-79, -128) * mm});
            skLineSegment(sketch, "E12.1.6.1", {"start": v(-79, -128) * mm, "end": v(-79, -138) * mm});
            skLineSegment(sketch, "E12.1.6.2", {"start": v(-89, -138) * mm, "end": v(-79, -138) * mm});
            skLineSegment(sketch, "E12.1.6.3", {"start": v(-89, -128) * mm, "end": v(-89, -138) * mm});
            skLineSegment(sketch, "E12.1.7.0", {"start": v(-89, -114) * mm, "end": v(-79, -114) * mm});
            skLineSegment(sketch, "E12.1.7.1", {"start": v(-79, -114) * mm, "end": v(-79, -124) * mm});
            skLineSegment(sketch, "E12.1.7.2", {"start": v(-89, -124) * mm, "end": v(-79, -124) * mm});
            skLineSegment(sketch, "E12.1.7.3", {"start": v(-89, -114) * mm, "end": v(-89, -124) * mm});
            skLineSegment(sketch, "E12.1.8.0", {"start": v(-89, -100) * mm, "end": v(-79, -100) * mm});
            skLineSegment(sketch, "E12.1.8.1", {"start": v(-79, -100) * mm, "end": v(-79, -110) * mm});
            skLineSegment(sketch, "E12.1.8.2", {"start": v(-89, -110) * mm, "end": v(-79, -110) * mm});
            skLineSegment(sketch, "E12.1.8.3", {"start": v(-89, -100) * mm, "end": v(-89, -110) * mm});
            skLineSegment(sketch, "E12.1.9.0", {"start": v(-89, -86) * mm, "end": v(-79, -86) * mm});
            skLineSegment(sketch, "E12.1.9.1", {"start": v(-79, -86) * mm, "end": v(-79, -96) * mm});
            skLineSegment(sketch, "E12.1.9.2", {"start": v(-89, -96) * mm, "end": v(-79, -96) * mm});
            skLineSegment(sketch, "E12.1.9.3", {"start": v(-89, -86) * mm, "end": v(-89, -96) * mm});
            skLineSegment(sketch, "E12.1.10.0", {"start": v(-89, -72) * mm, "end": v(-79, -72) * mm});
            skLineSegment(sketch, "E12.1.10.1", {"start": v(-79, -72) * mm, "end": v(-79, -82) * mm});
            skLineSegment(sketch, "E12.1.10.2", {"start": v(-89, -82) * mm, "end": v(-79, -82) * mm});
            skLineSegment(sketch, "E12.1.10.3", {"start": v(-89, -72) * mm, "end": v(-89, -82) * mm});
            skLineSegment(sketch, "E12.1.11.0", {"start": v(-89, -58) * mm, "end": v(-79, -58) * mm});
            skLineSegment(sketch, "E12.1.11.1", {"start": v(-79, -58) * mm, "end": v(-79, -68) * mm});
            skLineSegment(sketch, "E12.1.11.2", {"start": v(-89, -68) * mm, "end": v(-79, -68) * mm});
            skLineSegment(sketch, "E12.1.11.3", {"start": v(-89, -58) * mm, "end": v(-89, -68) * mm});
            skLineSegment(sketch, "E12.1.12.0", {"start": v(-89, -44) * mm, "end": v(-79, -44) * mm});
            skLineSegment(sketch, "E12.1.12.1", {"start": v(-79, -44) * mm, "end": v(-79, -54) * mm});
            skLineSegment(sketch, "E12.1.12.2", {"start": v(-89, -54) * mm, "end": v(-79, -54) * mm});
            skLineSegment(sketch, "E12.1.12.3", {"start": v(-89, -44) * mm, "end": v(-89, -54) * mm});
            skLineSegment(sketch, "E12.1.13.0", {"start": v(-89, -30) * mm, "end": v(-79, -30) * mm});
            skLineSegment(sketch, "E12.1.13.1", {"start": v(-79, -30) * mm, "end": v(-79, -40) * mm});
            skLineSegment(sketch, "E12.1.13.2", {"start": v(-89, -40) * mm, "end": v(-79, -40) * mm});
            skLineSegment(sketch, "E12.1.13.3", {"start": v(-89, -30) * mm, "end": v(-89, -40) * mm});
            skLineSegment(sketch, "E12.1.14.0", {"start": v(-89, -16) * mm, "end": v(-79, -16) * mm});
            skLineSegment(sketch, "E12.1.14.1", {"start": v(-79, -16) * mm, "end": v(-79, -26) * mm});
            skLineSegment(sketch, "E12.1.14.2", {"start": v(-89, -26) * mm, "end": v(-79, -26) * mm});
            skLineSegment(sketch, "E12.1.14.3", {"start": v(-89, -16) * mm, "end": v(-89, -26) * mm});
            skLineSegment(sketch, "E12.1.15.0", {"start": v(-89, -2) * mm, "end": v(-79, -2) * mm});
            skLineSegment(sketch, "E12.1.15.1", {"start": v(-79, -2) * mm, "end": v(-79, -12) * mm});
            skLineSegment(sketch, "E12.1.15.2", {"start": v(-89, -12) * mm, "end": v(-79, -12) * mm});
            skLineSegment(sketch, "E12.1.15.3", {"start": v(-89, -2) * mm, "end": v(-89, -12) * mm});
            skLineSegment(sketch, "E12.1.16.0", {"start": v(-89, 12) * mm, "end": v(-79, 12) * mm});
            skLineSegment(sketch, "E12.1.16.1", {"start": v(-79, 12) * mm, "end": v(-79, 2) * mm});
            skLineSegment(sketch, "E12.1.16.2", {"start": v(-89, 2) * mm, "end": v(-79, 2) * mm});
            skLineSegment(sketch, "E12.1.16.3", {"start": v(-89, 12) * mm, "end": v(-89, 2) * mm});
            skLineSegment(sketch, "E12.1.17.0", {"start": v(-89, 26) * mm, "end": v(-79, 26) * mm});
            skLineSegment(sketch, "E12.1.17.1", {"start": v(-79, 26) * mm, "end": v(-79, 16) * mm});
            skLineSegment(sketch, "E12.1.17.2", {"start": v(-89, 16) * mm, "end": v(-79, 16) * mm});
            skLineSegment(sketch, "E12.1.17.3", {"start": v(-89, 26) * mm, "end": v(-89, 16) * mm});
            skLineSegment(sketch, "E12.1.18.0", {"start": v(-89, 40) * mm, "end": v(-79, 40) * mm});
            skLineSegment(sketch, "E12.1.18.1", {"start": v(-79, 40) * mm, "end": v(-79, 30) * mm});
            skLineSegment(sketch, "E12.1.18.2", {"start": v(-89, 30) * mm, "end": v(-79, 30) * mm});
            skLineSegment(sketch, "E12.1.18.3", {"start": v(-89, 40) * mm, "end": v(-89, 30) * mm});
            skLineSegment(sketch, "E12.1.19.0", {"start": v(-89, 54) * mm, "end": v(-79, 54) * mm});
            skLineSegment(sketch, "E12.1.19.1", {"start": v(-79, 54) * mm, "end": v(-79, 44) * mm});
            skLineSegment(sketch, "E12.1.19.2", {"start": v(-89, 44) * mm, "end": v(-79, 44) * mm});
            skLineSegment(sketch, "E12.1.19.3", {"start": v(-89, 54) * mm, "end": v(-89, 44) * mm});
            skLineSegment(sketch, "E12.1.20.0", {"start": v(-89, 68) * mm, "end": v(-79, 68) * mm});
            skLineSegment(sketch, "E12.1.20.1", {"start": v(-79, 68) * mm, "end": v(-79, 58) * mm});
            skLineSegment(sketch, "E12.1.20.2", {"start": v(-89, 58) * mm, "end": v(-79, 58) * mm});
            skLineSegment(sketch, "E12.1.20.3", {"start": v(-89, 68) * mm, "end": v(-89, 58) * mm});
            skLineSegment(sketch, "E12.1.21.0", {"start": v(-89, 82) * mm, "end": v(-79, 82) * mm});
            skLineSegment(sketch, "E12.1.21.1", {"start": v(-79, 82) * mm, "end": v(-79, 72) * mm});
            skLineSegment(sketch, "E12.1.21.2", {"start": v(-89, 72) * mm, "end": v(-79, 72) * mm});
            skLineSegment(sketch, "E12.1.21.3", {"start": v(-89, 82) * mm, "end": v(-89, 72) * mm});
            skLineSegment(sketch, "E12.1.22.0", {"start": v(-89, 96) * mm, "end": v(-79, 96) * mm});
            skLineSegment(sketch, "E12.1.22.1", {"start": v(-79, 96) * mm, "end": v(-79, 86) * mm});
            skLineSegment(sketch, "E12.1.22.2", {"start": v(-89, 86) * mm, "end": v(-79, 86) * mm});
            skLineSegment(sketch, "E12.1.22.3", {"start": v(-89, 96) * mm, "end": v(-89, 86) * mm});
            skLineSegment(sketch, "E12.1.23.0", {"start": v(-89, 110) * mm, "end": v(-79, 110) * mm});
            skLineSegment(sketch, "E12.1.23.1", {"start": v(-79, 110) * mm, "end": v(-79, 100) * mm});
            skLineSegment(sketch, "E12.1.23.2", {"start": v(-89, 100) * mm, "end": v(-79, 100) * mm});
            skLineSegment(sketch, "E12.1.23.3", {"start": v(-89, 110) * mm, "end": v(-89, 100) * mm});
            skLineSegment(sketch, "E12.1.24.0", {"start": v(-89, 124) * mm, "end": v(-79, 124) * mm});
            skLineSegment(sketch, "E12.1.24.1", {"start": v(-79, 124) * mm, "end": v(-79, 114) * mm});
            skLineSegment(sketch, "E12.1.24.2", {"start": v(-89, 114) * mm, "end": v(-79, 114) * mm});
            skLineSegment(sketch, "E12.1.24.3", {"start": v(-89, 124) * mm, "end": v(-89, 114) * mm});
            skLineSegment(sketch, "E12.1.25.0", {"start": v(-89, 138) * mm, "end": v(-79, 138) * mm});
            skLineSegment(sketch, "E12.1.25.1", {"start": v(-79, 138) * mm, "end": v(-79, 128) * mm});
            skLineSegment(sketch, "E12.1.25.2", {"start": v(-89, 128) * mm, "end": v(-79, 128) * mm});
            skLineSegment(sketch, "E12.1.25.3", {"start": v(-89, 138) * mm, "end": v(-89, 128) * mm});
            skLineSegment(sketch, "E12.1.26.0", {"start": v(-89, 152) * mm, "end": v(-79, 152) * mm});
            skLineSegment(sketch, "E12.1.26.1", {"start": v(-79, 152) * mm, "end": v(-79, 142) * mm});
            skLineSegment(sketch, "E12.1.26.2", {"start": v(-89, 142) * mm, "end": v(-79, 142) * mm});
            skLineSegment(sketch, "E12.1.26.3", {"start": v(-89, 152) * mm, "end": v(-89, 142) * mm});
            skLineSegment(sketch, "E12.1.27.0", {"start": v(-89, 166) * mm, "end": v(-79, 166) * mm});
            skLineSegment(sketch, "E12.1.27.1", {"start": v(-79, 166) * mm, "end": v(-79, 156) * mm});
            skLineSegment(sketch, "E12.1.27.2", {"start": v(-89, 156) * mm, "end": v(-79, 156) * mm});
            skLineSegment(sketch, "E12.1.27.3", {"start": v(-89, 166) * mm, "end": v(-89, 156) * mm});
            skLineSegment(sketch, "E12.1.28.0", {"start": v(-89, 180) * mm, "end": v(-79, 180) * mm});
            skLineSegment(sketch, "E12.1.28.1", {"start": v(-79, 180) * mm, "end": v(-79, 170) * mm});
            skLineSegment(sketch, "E12.1.28.2", {"start": v(-89, 170) * mm, "end": v(-79, 170) * mm});
            skLineSegment(sketch, "E12.1.28.3", {"start": v(-89, 180) * mm, "end": v(-89, 170) * mm});
            skLineSegment(sketch, "E12.1.29.0", {"start": v(-89, 194) * mm, "end": v(-79, 194) * mm});
            skLineSegment(sketch, "E12.1.29.1", {"start": v(-79, 194) * mm, "end": v(-79, 184) * mm});
            skLineSegment(sketch, "E12.1.29.2", {"start": v(-89, 184) * mm, "end": v(-79, 184) * mm});
            skLineSegment(sketch, "E12.1.29.3", {"start": v(-89, 194) * mm, "end": v(-89, 184) * mm});
            skLineSegment(sketch, "E12.1.30.0", {"start": v(-89, 208) * mm, "end": v(-79, 208) * mm});
            skLineSegment(sketch, "E12.1.30.1", {"start": v(-79, 208) * mm, "end": v(-79, 198) * mm});
            skLineSegment(sketch, "E12.1.30.2", {"start": v(-89, 198) * mm, "end": v(-79, 198) * mm});
            skLineSegment(sketch, "E12.1.30.3", {"start": v(-89, 208) * mm, "end": v(-89, 198) * mm});
            skLineSegment(sketch, "E12.1.31.0", {"start": v(-89, 222) * mm, "end": v(-79, 222) * mm});
            skLineSegment(sketch, "E12.1.31.1", {"start": v(-79, 222) * mm, "end": v(-79, 212) * mm});
            skLineSegment(sketch, "E12.1.31.2", {"start": v(-89, 212) * mm, "end": v(-79, 212) * mm});
            skLineSegment(sketch, "E12.1.31.3", {"start": v(-89, 222) * mm, "end": v(-89, 212) * mm});
            skLineSegment(sketch, "E12.2.0.0", {"start": v(-75, -212) * mm, "end": v(-65, -212) * mm});
            skLineSegment(sketch, "E12.2.0.1", {"start": v(-65, -212) * mm, "end": v(-65, -222) * mm});
            skLineSegment(sketch, "E12.2.0.2", {"start": v(-75, -222) * mm, "end": v(-65, -222) * mm});
            skLineSegment(sketch, "E12.2.0.3", {"start": v(-75, -212) * mm, "end": v(-75, -222) * mm});
            skLineSegment(sketch, "E12.2.1.0", {"start": v(-75, -198) * mm, "end": v(-65, -198) * mm});
            skLineSegment(sketch, "E12.2.1.1", {"start": v(-65, -198) * mm, "end": v(-65, -208) * mm});
            skLineSegment(sketch, "E12.2.1.2", {"start": v(-75, -208) * mm, "end": v(-65, -208) * mm});
            skLineSegment(sketch, "E12.2.1.3", {"start": v(-75, -198) * mm, "end": v(-75, -208) * mm});
            skLineSegment(sketch, "E12.2.2.0", {"start": v(-75, -184) * mm, "end": v(-65, -184) * mm});
            skLineSegment(sketch, "E12.2.2.1", {"start": v(-65, -184) * mm, "end": v(-65, -194) * mm});
            skLineSegment(sketch, "E12.2.2.2", {"start": v(-75, -194) * mm, "end": v(-65, -194) * mm});
            skLineSegment(sketch, "E12.2.2.3", {"start": v(-75, -184) * mm, "end": v(-75, -194) * mm});
            skLineSegment(sketch, "E12.2.3.0", {"start": v(-75, -170) * mm, "end": v(-65, -170) * mm});
            skLineSegment(sketch, "E12.2.3.1", {"start": v(-65, -170) * mm, "end": v(-65, -180) * mm});
            skLineSegment(sketch, "E12.2.3.2", {"start": v(-75, -180) * mm, "end": v(-65, -180) * mm});
            skLineSegment(sketch, "E12.2.3.3", {"start": v(-75, -170) * mm, "end": v(-75, -180) * mm});
            skLineSegment(sketch, "E12.2.4.0", {"start": v(-75, -156) * mm, "end": v(-65, -156) * mm});
            skLineSegment(sketch, "E12.2.4.1", {"start": v(-65, -156) * mm, "end": v(-65, -166) * mm});
            skLineSegment(sketch, "E12.2.4.2", {"start": v(-75, -166) * mm, "end": v(-65, -166) * mm});
            skLineSegment(sketch, "E12.2.4.3", {"start": v(-75, -156) * mm, "end": v(-75, -166) * mm});
            skLineSegment(sketch, "E12.2.5.0", {"start": v(-75, -142) * mm, "end": v(-65, -142) * mm});
            skLineSegment(sketch, "E12.2.5.1", {"start": v(-65, -142) * mm, "end": v(-65, -152) * mm});
            skLineSegment(sketch, "E12.2.5.2", {"start": v(-75, -152) * mm, "end": v(-65, -152) * mm});
            skLineSegment(sketch, "E12.2.5.3", {"start": v(-75, -142) * mm, "end": v(-75, -152) * mm});
            skLineSegment(sketch, "E12.2.6.0", {"start": v(-75, -128) * mm, "end": v(-65, -128) * mm});
            skLineSegment(sketch, "E12.2.6.1", {"start": v(-65, -128) * mm, "end": v(-65, -138) * mm});
            skLineSegment(sketch, "E12.2.6.2", {"start": v(-75, -138) * mm, "end": v(-65, -138) * mm});
            skLineSegment(sketch, "E12.2.6.3", {"start": v(-75, -128) * mm, "end": v(-75, -138) * mm});
            skLineSegment(sketch, "E12.2.7.0", {"start": v(-75, -114) * mm, "end": v(-65, -114) * mm});
            skLineSegment(sketch, "E12.2.7.1", {"start": v(-65, -114) * mm, "end": v(-65, -124) * mm});
            skLineSegment(sketch, "E12.2.7.2", {"start": v(-75, -124) * mm, "end": v(-65, -124) * mm});
            skLineSegment(sketch, "E12.2.7.3", {"start": v(-75, -114) * mm, "end": v(-75, -124) * mm});
            skLineSegment(sketch, "E12.2.8.0", {"start": v(-75, -100) * mm, "end": v(-65, -100) * mm});
            skLineSegment(sketch, "E12.2.8.1", {"start": v(-65, -100) * mm, "end": v(-65, -110) * mm});
            skLineSegment(sketch, "E12.2.8.2", {"start": v(-75, -110) * mm, "end": v(-65, -110) * mm});
            skLineSegment(sketch, "E12.2.8.3", {"start": v(-75, -100) * mm, "end": v(-75, -110) * mm});
            skLineSegment(sketch, "E12.2.9.0", {"start": v(-75, -86) * mm, "end": v(-65, -86) * mm});
            skLineSegment(sketch, "E12.2.9.1", {"start": v(-65, -86) * mm, "end": v(-65, -96) * mm});
            skLineSegment(sketch, "E12.2.9.2", {"start": v(-75, -96) * mm, "end": v(-65, -96) * mm});
            skLineSegment(sketch, "E12.2.9.3", {"start": v(-75, -86) * mm, "end": v(-75, -96) * mm});
            skLineSegment(sketch, "E12.2.10.0", {"start": v(-75, -72) * mm, "end": v(-65, -72) * mm});
            skLineSegment(sketch, "E12.2.10.1", {"start": v(-65, -72) * mm, "end": v(-65, -82) * mm});
            skLineSegment(sketch, "E12.2.10.2", {"start": v(-75, -82) * mm, "end": v(-65, -82) * mm});
            skLineSegment(sketch, "E12.2.10.3", {"start": v(-75, -72) * mm, "end": v(-75, -82) * mm});
            skLineSegment(sketch, "E12.2.11.0", {"start": v(-75, -58) * mm, "end": v(-65, -58) * mm});
            skLineSegment(sketch, "E12.2.11.1", {"start": v(-65, -58) * mm, "end": v(-65, -68) * mm});
            skLineSegment(sketch, "E12.2.11.2", {"start": v(-75, -68) * mm, "end": v(-65, -68) * mm});
            skLineSegment(sketch, "E12.2.11.3", {"start": v(-75, -58) * mm, "end": v(-75, -68) * mm});
            skLineSegment(sketch, "E12.2.12.0", {"start": v(-75, -44) * mm, "end": v(-65, -44) * mm});
            skLineSegment(sketch, "E12.2.12.1", {"start": v(-65, -44) * mm, "end": v(-65, -54) * mm});
            skLineSegment(sketch, "E12.2.12.2", {"start": v(-75, -54) * mm, "end": v(-65, -54) * mm});
            skLineSegment(sketch, "E12.2.12.3", {"start": v(-75, -44) * mm, "end": v(-75, -54) * mm});
            skLineSegment(sketch, "E12.2.13.0", {"start": v(-75, -30) * mm, "end": v(-65, -30) * mm});
            skLineSegment(sketch, "E12.2.13.1", {"start": v(-65, -30) * mm, "end": v(-65, -40) * mm});
            skLineSegment(sketch, "E12.2.13.2", {"start": v(-75, -40) * mm, "end": v(-65, -40) * mm});
            skLineSegment(sketch, "E12.2.13.3", {"start": v(-75, -30) * mm, "end": v(-75, -40) * mm});
            skLineSegment(sketch, "E12.2.14.0", {"start": v(-75, -16) * mm, "end": v(-65, -16) * mm});
            skLineSegment(sketch, "E12.2.14.1", {"start": v(-65, -16) * mm, "end": v(-65, -26) * mm});
            skLineSegment(sketch, "E12.2.14.2", {"start": v(-75, -26) * mm, "end": v(-65, -26) * mm});
            skLineSegment(sketch, "E12.2.14.3", {"start": v(-75, -16) * mm, "end": v(-75, -26) * mm});
            skLineSegment(sketch, "E12.2.15.0", {"start": v(-75, -2) * mm, "end": v(-65, -2) * mm});
            skLineSegment(sketch, "E12.2.15.1", {"start": v(-65, -2) * mm, "end": v(-65, -12) * mm});
            skLineSegment(sketch, "E12.2.15.2", {"start": v(-75, -12) * mm, "end": v(-65, -12) * mm});
            skLineSegment(sketch, "E12.2.15.3", {"start": v(-75, -2) * mm, "end": v(-75, -12) * mm});
            skLineSegment(sketch, "E12.2.16.0", {"start": v(-75, 12) * mm, "end": v(-65, 12) * mm});
            skLineSegment(sketch, "E12.2.16.1", {"start": v(-65, 12) * mm, "end": v(-65, 2) * mm});
            skLineSegment(sketch, "E12.2.16.2", {"start": v(-75, 2) * mm, "end": v(-65, 2) * mm});
            skLineSegment(sketch, "E12.2.16.3", {"start": v(-75, 12) * mm, "end": v(-75, 2) * mm});
            skLineSegment(sketch, "E12.2.17.0", {"start": v(-75, 26) * mm, "end": v(-65, 26) * mm});
            skLineSegment(sketch, "E12.2.17.1", {"start": v(-65, 26) * mm, "end": v(-65, 16) * mm});
            skLineSegment(sketch, "E12.2.17.2", {"start": v(-75, 16) * mm, "end": v(-65, 16) * mm});
            skLineSegment(sketch, "E12.2.17.3", {"start": v(-75, 26) * mm, "end": v(-75, 16) * mm});
            skLineSegment(sketch, "E12.2.18.0", {"start": v(-75, 40) * mm, "end": v(-65, 40) * mm});
            skLineSegment(sketch, "E12.2.18.1", {"start": v(-65, 40) * mm, "end": v(-65, 30) * mm});
            skLineSegment(sketch, "E12.2.18.2", {"start": v(-75, 30) * mm, "end": v(-65, 30) * mm});
            skLineSegment(sketch, "E12.2.18.3", {"start": v(-75, 40) * mm, "end": v(-75, 30) * mm});
            skLineSegment(sketch, "E12.2.19.0", {"start": v(-75, 54) * mm, "end": v(-65, 54) * mm});
            skLineSegment(sketch, "E12.2.19.1", {"start": v(-65, 54) * mm, "end": v(-65, 44) * mm});
            skLineSegment(sketch, "E12.2.19.2", {"start": v(-75, 44) * mm, "end": v(-65, 44) * mm});
            skLineSegment(sketch, "E12.2.19.3", {"start": v(-75, 54) * mm, "end": v(-75, 44) * mm});
            skLineSegment(sketch, "E12.2.20.0", {"start": v(-75, 68) * mm, "end": v(-65, 68) * mm});
            skLineSegment(sketch, "E12.2.20.1", {"start": v(-65, 68) * mm, "end": v(-65, 58) * mm});
            skLineSegment(sketch, "E12.2.20.2", {"start": v(-75, 58) * mm, "end": v(-65, 58) * mm});
            skLineSegment(sketch, "E12.2.20.3", {"start": v(-75, 68) * mm, "end": v(-75, 58) * mm});
            skLineSegment(sketch, "E12.2.21.0", {"start": v(-75, 82) * mm, "end": v(-65, 82) * mm});
            skLineSegment(sketch, "E12.2.21.1", {"start": v(-65, 82) * mm, "end": v(-65, 72) * mm});
            skLineSegment(sketch, "E12.2.21.2", {"start": v(-75, 72) * mm, "end": v(-65, 72) * mm});
            skLineSegment(sketch, "E12.2.21.3", {"start": v(-75, 82) * mm, "end": v(-75, 72) * mm});
            skLineSegment(sketch, "E12.2.22.0", {"start": v(-75, 96) * mm, "end": v(-65, 96) * mm});
            skLineSegment(sketch, "E12.2.22.1", {"start": v(-65, 96) * mm, "end": v(-65, 86) * mm});
            skLineSegment(sketch, "E12.2.22.2", {"start": v(-75, 86) * mm, "end": v(-65, 86) * mm});
            skLineSegment(sketch, "E12.2.22.3", {"start": v(-75, 96) * mm, "end": v(-75, 86) * mm});
            skLineSegment(sketch, "E12.2.23.0", {"start": v(-75, 110) * mm, "end": v(-65, 110) * mm});
            skLineSegment(sketch, "E12.2.23.1", {"start": v(-65, 110) * mm, "end": v(-65, 100) * mm});
            skLineSegment(sketch, "E12.2.23.2", {"start": v(-75, 100) * mm, "end": v(-65, 100) * mm});
            skLineSegment(sketch, "E12.2.23.3", {"start": v(-75, 110) * mm, "end": v(-75, 100) * mm});
            skLineSegment(sketch, "E12.2.24.0", {"start": v(-75, 124) * mm, "end": v(-65, 124) * mm});
            skLineSegment(sketch, "E12.2.24.1", {"start": v(-65, 124) * mm, "end": v(-65, 114) * mm});
            skLineSegment(sketch, "E12.2.24.2", {"start": v(-75, 114) * mm, "end": v(-65, 114) * mm});
            skLineSegment(sketch, "E12.2.24.3", {"start": v(-75, 124) * mm, "end": v(-75, 114) * mm});
            skLineSegment(sketch, "E12.2.25.0", {"start": v(-75, 138) * mm, "end": v(-65, 138) * mm});
            skLineSegment(sketch, "E12.2.25.1", {"start": v(-65, 138) * mm, "end": v(-65, 128) * mm});
            skLineSegment(sketch, "E12.2.25.2", {"start": v(-75, 128) * mm, "end": v(-65, 128) * mm});
            skLineSegment(sketch, "E12.2.25.3", {"start": v(-75, 138) * mm, "end": v(-75, 128) * mm});
            skLineSegment(sketch, "E12.2.26.0", {"start": v(-75, 152) * mm, "end": v(-65, 152) * mm});
            skLineSegment(sketch, "E12.2.26.1", {"start": v(-65, 152) * mm, "end": v(-65, 142) * mm});
            skLineSegment(sketch, "E12.2.26.2", {"start": v(-75, 142) * mm, "end": v(-65, 142) * mm});
            skLineSegment(sketch, "E12.2.26.3", {"start": v(-75, 152) * mm, "end": v(-75, 142) * mm});
            skLineSegment(sketch, "E12.2.27.0", {"start": v(-75, 166) * mm, "end": v(-65, 166) * mm});
            skLineSegment(sketch, "E12.2.27.1", {"start": v(-65, 166) * mm, "end": v(-65, 156) * mm});
            skLineSegment(sketch, "E12.2.27.2", {"start": v(-75, 156) * mm, "end": v(-65, 156) * mm});
            skLineSegment(sketch, "E12.2.27.3", {"start": v(-75, 166) * mm, "end": v(-75, 156) * mm});
            skLineSegment(sketch, "E12.2.28.0", {"start": v(-75, 180) * mm, "end": v(-65, 180) * mm});
            skLineSegment(sketch, "E12.2.28.1", {"start": v(-65, 180) * mm, "end": v(-65, 170) * mm});
            skLineSegment(sketch, "E12.2.28.2", {"start": v(-75, 170) * mm, "end": v(-65, 170) * mm});
            skLineSegment(sketch, "E12.2.28.3", {"start": v(-75, 180) * mm, "end": v(-75, 170) * mm});
            skLineSegment(sketch, "E12.2.29.0", {"start": v(-75, 194) * mm, "end": v(-65, 194) * mm});
            skLineSegment(sketch, "E12.2.29.1", {"start": v(-65, 194) * mm, "end": v(-65, 184) * mm});
            skLineSegment(sketch, "E12.2.29.2", {"start": v(-75, 184) * mm, "end": v(-65, 184) * mm});
            skLineSegment(sketch, "E12.2.29.3", {"start": v(-75, 194) * mm, "end": v(-75, 184) * mm});
            skLineSegment(sketch, "E12.2.30.0", {"start": v(-75, 208) * mm, "end": v(-65, 208) * mm});
            skLineSegment(sketch, "E12.2.30.1", {"start": v(-65, 208) * mm, "end": v(-65, 198) * mm});
            skLineSegment(sketch, "E12.2.30.2", {"start": v(-75, 198) * mm, "end": v(-65, 198) * mm});
            skLineSegment(sketch, "E12.2.30.3", {"start": v(-75, 208) * mm, "end": v(-75, 198) * mm});
            skLineSegment(sketch, "E12.2.31.0", {"start": v(-75, 222) * mm, "end": v(-65, 222) * mm});
            skLineSegment(sketch, "E12.2.31.1", {"start": v(-65, 222) * mm, "end": v(-65, 212) * mm});
            skLineSegment(sketch, "E12.2.31.2", {"start": v(-75, 212) * mm, "end": v(-65, 212) * mm});
            skLineSegment(sketch, "E12.2.31.3", {"start": v(-75, 222) * mm, "end": v(-75, 212) * mm});
            skLineSegment(sketch, "E12.3.0.0", {"start": v(-61, -212) * mm, "end": v(-51, -212) * mm});
            skLineSegment(sketch, "E12.3.0.1", {"start": v(-51, -212) * mm, "end": v(-51, -222) * mm});
            skLineSegment(sketch, "E12.3.0.2", {"start": v(-61, -222) * mm, "end": v(-51, -222) * mm});
            skLineSegment(sketch, "E12.3.0.3", {"start": v(-61, -212) * mm, "end": v(-61, -222) * mm});
            skLineSegment(sketch, "E12.3.1.0", {"start": v(-61, -198) * mm, "end": v(-51, -198) * mm});
            skLineSegment(sketch, "E12.3.1.1", {"start": v(-51, -198) * mm, "end": v(-51, -208) * mm});
            skLineSegment(sketch, "E12.3.1.2", {"start": v(-61, -208) * mm, "end": v(-51, -208) * mm});
            skLineSegment(sketch, "E12.3.1.3", {"start": v(-61, -198) * mm, "end": v(-61, -208) * mm});
            skLineSegment(sketch, "E12.3.2.0", {"start": v(-61, -184) * mm, "end": v(-51, -184) * mm});
            skLineSegment(sketch, "E12.3.2.1", {"start": v(-51, -184) * mm, "end": v(-51, -194) * mm});
            skLineSegment(sketch, "E12.3.2.2", {"start": v(-61, -194) * mm, "end": v(-51, -194) * mm});
            skLineSegment(sketch, "E12.3.2.3", {"start": v(-61, -184) * mm, "end": v(-61, -194) * mm});
            skLineSegment(sketch, "E12.3.3.0", {"start": v(-61, -170) * mm, "end": v(-51, -170) * mm});
            skLineSegment(sketch, "E12.3.3.1", {"start": v(-51, -170) * mm, "end": v(-51, -180) * mm});
            skLineSegment(sketch, "E12.3.3.2", {"start": v(-61, -180) * mm, "end": v(-51, -180) * mm});
            skLineSegment(sketch, "E12.3.3.3", {"start": v(-61, -170) * mm, "end": v(-61, -180) * mm});
            skLineSegment(sketch, "E12.3.4.0", {"start": v(-61, -156) * mm, "end": v(-51, -156) * mm});
            skLineSegment(sketch, "E12.3.4.1", {"start": v(-51, -156) * mm, "end": v(-51, -166) * mm});
            skLineSegment(sketch, "E12.3.4.2", {"start": v(-61, -166) * mm, "end": v(-51, -166) * mm});
            skLineSegment(sketch, "E12.3.4.3", {"start": v(-61, -156) * mm, "end": v(-61, -166) * mm});
            skLineSegment(sketch, "E12.3.5.0", {"start": v(-61, -142) * mm, "end": v(-51, -142) * mm});
            skLineSegment(sketch, "E12.3.5.1", {"start": v(-51, -142) * mm, "end": v(-51, -152) * mm});
            skLineSegment(sketch, "E12.3.5.2", {"start": v(-61, -152) * mm, "end": v(-51, -152) * mm});
            skLineSegment(sketch, "E12.3.5.3", {"start": v(-61, -142) * mm, "end": v(-61, -152) * mm});
            skLineSegment(sketch, "E12.3.6.0", {"start": v(-61, -128) * mm, "end": v(-51, -128) * mm});
            skLineSegment(sketch, "E12.3.6.1", {"start": v(-51, -128) * mm, "end": v(-51, -138) * mm});
            skLineSegment(sketch, "E12.3.6.2", {"start": v(-61, -138) * mm, "end": v(-51, -138) * mm});
            skLineSegment(sketch, "E12.3.6.3", {"start": v(-61, -128) * mm, "end": v(-61, -138) * mm});
            skLineSegment(sketch, "E12.3.7.0", {"start": v(-61, -114) * mm, "end": v(-51, -114) * mm});
            skLineSegment(sketch, "E12.3.7.1", {"start": v(-51, -114) * mm, "end": v(-51, -124) * mm});
            skLineSegment(sketch, "E12.3.7.2", {"start": v(-61, -124) * mm, "end": v(-51, -124) * mm});
            skLineSegment(sketch, "E12.3.7.3", {"start": v(-61, -114) * mm, "end": v(-61, -124) * mm});
            skLineSegment(sketch, "E12.3.8.0", {"start": v(-61, -100) * mm, "end": v(-51, -100) * mm});
            skLineSegment(sketch, "E12.3.8.1", {"start": v(-51, -100) * mm, "end": v(-51, -110) * mm});
            skLineSegment(sketch, "E12.3.8.2", {"start": v(-61, -110) * mm, "end": v(-51, -110) * mm});
            skLineSegment(sketch, "E12.3.8.3", {"start": v(-61, -100) * mm, "end": v(-61, -110) * mm});
            skLineSegment(sketch, "E12.3.9.0", {"start": v(-61, -86) * mm, "end": v(-51, -86) * mm});
            skLineSegment(sketch, "E12.3.9.1", {"start": v(-51, -86) * mm, "end": v(-51, -96) * mm});
            skLineSegment(sketch, "E12.3.9.2", {"start": v(-61, -96) * mm, "end": v(-51, -96) * mm});
            skLineSegment(sketch, "E12.3.9.3", {"start": v(-61, -86) * mm, "end": v(-61, -96) * mm});
            skLineSegment(sketch, "E12.3.10.0", {"start": v(-61, -72) * mm, "end": v(-51, -72) * mm});
            skLineSegment(sketch, "E12.3.10.1", {"start": v(-51, -72) * mm, "end": v(-51, -82) * mm});
            skLineSegment(sketch, "E12.3.10.2", {"start": v(-61, -82) * mm, "end": v(-51, -82) * mm});
            skLineSegment(sketch, "E12.3.10.3", {"start": v(-61, -72) * mm, "end": v(-61, -82) * mm});
            skLineSegment(sketch, "E12.3.11.0", {"start": v(-61, -58) * mm, "end": v(-51, -58) * mm});
            skLineSegment(sketch, "E12.3.11.1", {"start": v(-51, -58) * mm, "end": v(-51, -68) * mm});
            skLineSegment(sketch, "E12.3.11.2", {"start": v(-61, -68) * mm, "end": v(-51, -68) * mm});
            skLineSegment(sketch, "E12.3.11.3", {"start": v(-61, -58) * mm, "end": v(-61, -68) * mm});
            skLineSegment(sketch, "E12.3.12.0", {"start": v(-61, -44) * mm, "end": v(-51, -44) * mm});
            skLineSegment(sketch, "E12.3.12.1", {"start": v(-51, -44) * mm, "end": v(-51, -54) * mm});
            skLineSegment(sketch, "E12.3.12.2", {"start": v(-61, -54) * mm, "end": v(-51, -54) * mm});
            skLineSegment(sketch, "E12.3.12.3", {"start": v(-61, -44) * mm, "end": v(-61, -54) * mm});
            skLineSegment(sketch, "E12.3.13.0", {"start": v(-61, -30) * mm, "end": v(-51, -30) * mm});
            skLineSegment(sketch, "E12.3.13.1", {"start": v(-51, -30) * mm, "end": v(-51, -40) * mm});
            skLineSegment(sketch, "E12.3.13.2", {"start": v(-61, -40) * mm, "end": v(-51, -40) * mm});
            skLineSegment(sketch, "E12.3.13.3", {"start": v(-61, -30) * mm, "end": v(-61, -40) * mm});
            skLineSegment(sketch, "E12.3.14.0", {"start": v(-61, -16) * mm, "end": v(-51, -16) * mm});
            skLineSegment(sketch, "E12.3.14.1", {"start": v(-51, -16) * mm, "end": v(-51, -26) * mm});
            skLineSegment(sketch, "E12.3.14.2", {"start": v(-61, -26) * mm, "end": v(-51, -26) * mm});
            skLineSegment(sketch, "E12.3.14.3", {"start": v(-61, -16) * mm, "end": v(-61, -26) * mm});
            skLineSegment(sketch, "E12.3.15.0", {"start": v(-61, -2) * mm, "end": v(-51, -2) * mm});
            skLineSegment(sketch, "E12.3.15.1", {"start": v(-51, -2) * mm, "end": v(-51, -12) * mm});
            skLineSegment(sketch, "E12.3.15.2", {"start": v(-61, -12) * mm, "end": v(-51, -12) * mm});
            skLineSegment(sketch, "E12.3.15.3", {"start": v(-61, -2) * mm, "end": v(-61, -12) * mm});
            skLineSegment(sketch, "E12.3.16.0", {"start": v(-61, 12) * mm, "end": v(-51, 12) * mm});
            skLineSegment(sketch, "E12.3.16.1", {"start": v(-51, 12) * mm, "end": v(-51, 2) * mm});
            skLineSegment(sketch, "E12.3.16.2", {"start": v(-61, 2) * mm, "end": v(-51, 2) * mm});
            skLineSegment(sketch, "E12.3.16.3", {"start": v(-61, 12) * mm, "end": v(-61, 2) * mm});
            skLineSegment(sketch, "E12.3.17.0", {"start": v(-61, 26) * mm, "end": v(-51, 26) * mm});
            skLineSegment(sketch, "E12.3.17.1", {"start": v(-51, 26) * mm, "end": v(-51, 16) * mm});
            skLineSegment(sketch, "E12.3.17.2", {"start": v(-61, 16) * mm, "end": v(-51, 16) * mm});
            skLineSegment(sketch, "E12.3.17.3", {"start": v(-61, 26) * mm, "end": v(-61, 16) * mm});
            skLineSegment(sketch, "E12.3.18.0", {"start": v(-61, 40) * mm, "end": v(-51, 40) * mm});
            skLineSegment(sketch, "E12.3.18.1", {"start": v(-51, 40) * mm, "end": v(-51, 30) * mm});
            skLineSegment(sketch, "E12.3.18.2", {"start": v(-61, 30) * mm, "end": v(-51, 30) * mm});
            skLineSegment(sketch, "E12.3.18.3", {"start": v(-61, 40) * mm, "end": v(-61, 30) * mm});
            skLineSegment(sketch, "E12.3.19.0", {"start": v(-61, 54) * mm, "end": v(-51, 54) * mm});
            skLineSegment(sketch, "E12.3.19.1", {"start": v(-51, 54) * mm, "end": v(-51, 44) * mm});
            skLineSegment(sketch, "E12.3.19.2", {"start": v(-61, 44) * mm, "end": v(-51, 44) * mm});
            skLineSegment(sketch, "E12.3.19.3", {"start": v(-61, 54) * mm, "end": v(-61, 44) * mm});
            skLineSegment(sketch, "E12.3.20.0", {"start": v(-61, 68) * mm, "end": v(-51, 68) * mm});
            skLineSegment(sketch, "E12.3.20.1", {"start": v(-51, 68) * mm, "end": v(-51, 58) * mm});
            skLineSegment(sketch, "E12.3.20.2", {"start": v(-61, 58) * mm, "end": v(-51, 58) * mm});
            skLineSegment(sketch, "E12.3.20.3", {"start": v(-61, 68) * mm, "end": v(-61, 58) * mm});
            skLineSegment(sketch, "E12.3.21.0", {"start": v(-61, 82) * mm, "end": v(-51, 82) * mm});
            skLineSegment(sketch, "E12.3.21.1", {"start": v(-51, 82) * mm, "end": v(-51, 72) * mm});
            skLineSegment(sketch, "E12.3.21.2", {"start": v(-61, 72) * mm, "end": v(-51, 72) * mm});
            skLineSegment(sketch, "E12.3.21.3", {"start": v(-61, 82) * mm, "end": v(-61, 72) * mm});
            skLineSegment(sketch, "E12.3.22.0", {"start": v(-61, 96) * mm, "end": v(-51, 96) * mm});
            skLineSegment(sketch, "E12.3.22.1", {"start": v(-51, 96) * mm, "end": v(-51, 86) * mm});
            skLineSegment(sketch, "E12.3.22.2", {"start": v(-61, 86) * mm, "end": v(-51, 86) * mm});
            skLineSegment(sketch, "E12.3.22.3", {"start": v(-61, 96) * mm, "end": v(-61, 86) * mm});
            skLineSegment(sketch, "E12.3.23.0", {"start": v(-61, 110) * mm, "end": v(-51, 110) * mm});
            skLineSegment(sketch, "E12.3.23.1", {"start": v(-51, 110) * mm, "end": v(-51, 100) * mm});
            skLineSegment(sketch, "E12.3.23.2", {"start": v(-61, 100) * mm, "end": v(-51, 100) * mm});
            skLineSegment(sketch, "E12.3.23.3", {"start": v(-61, 110) * mm, "end": v(-61, 100) * mm});
            skLineSegment(sketch, "E12.3.24.0", {"start": v(-61, 124) * mm, "end": v(-51, 124) * mm});
            skLineSegment(sketch, "E12.3.24.1", {"start": v(-51, 124) * mm, "end": v(-51, 114) * mm});
            skLineSegment(sketch, "E12.3.24.2", {"start": v(-61, 114) * mm, "end": v(-51, 114) * mm});
            skLineSegment(sketch, "E12.3.24.3", {"start": v(-61, 124) * mm, "end": v(-61, 114) * mm});
            skLineSegment(sketch, "E12.3.25.0", {"start": v(-61, 138) * mm, "end": v(-51, 138) * mm});
            skLineSegment(sketch, "E12.3.25.1", {"start": v(-51, 138) * mm, "end": v(-51, 128) * mm});
            skLineSegment(sketch, "E12.3.25.2", {"start": v(-61, 128) * mm, "end": v(-51, 128) * mm});
            skLineSegment(sketch, "E12.3.25.3", {"start": v(-61, 138) * mm, "end": v(-61, 128) * mm});
            skLineSegment(sketch, "E12.3.26.0", {"start": v(-61, 152) * mm, "end": v(-51, 152) * mm});
            skLineSegment(sketch, "E12.3.26.1", {"start": v(-51, 152) * mm, "end": v(-51, 142) * mm});
            skLineSegment(sketch, "E12.3.26.2", {"start": v(-61, 142) * mm, "end": v(-51, 142) * mm});
            skLineSegment(sketch, "E12.3.26.3", {"start": v(-61, 152) * mm, "end": v(-61, 142) * mm});
            skLineSegment(sketch, "E12.3.27.0", {"start": v(-61, 166) * mm, "end": v(-51, 166) * mm});
            skLineSegment(sketch, "E12.3.27.1", {"start": v(-51, 166) * mm, "end": v(-51, 156) * mm});
            skLineSegment(sketch, "E12.3.27.2", {"start": v(-61, 156) * mm, "end": v(-51, 156) * mm});
            skLineSegment(sketch, "E12.3.27.3", {"start": v(-61, 166) * mm, "end": v(-61, 156) * mm});
            skLineSegment(sketch, "E12.3.28.0", {"start": v(-61, 180) * mm, "end": v(-51, 180) * mm});
            skLineSegment(sketch, "E12.3.28.1", {"start": v(-51, 180) * mm, "end": v(-51, 170) * mm});
            skLineSegment(sketch, "E12.3.28.2", {"start": v(-61, 170) * mm, "end": v(-51, 170) * mm});
            skLineSegment(sketch, "E12.3.28.3", {"start": v(-61, 180) * mm, "end": v(-61, 170) * mm});
            skLineSegment(sketch, "E12.3.29.0", {"start": v(-61, 194) * mm, "end": v(-51, 194) * mm});
            skLineSegment(sketch, "E12.3.29.1", {"start": v(-51, 194) * mm, "end": v(-51, 184) * mm});
            skLineSegment(sketch, "E12.3.29.2", {"start": v(-61, 184) * mm, "end": v(-51, 184) * mm});
            skLineSegment(sketch, "E12.3.29.3", {"start": v(-61, 194) * mm, "end": v(-61, 184) * mm});
            skLineSegment(sketch, "E12.3.30.0", {"start": v(-61, 208) * mm, "end": v(-51, 208) * mm});
            skLineSegment(sketch, "E12.3.30.1", {"start": v(-51, 208) * mm, "end": v(-51, 198) * mm});
            skLineSegment(sketch, "E12.3.30.2", {"start": v(-61, 198) * mm, "end": v(-51, 198) * mm});
            skLineSegment(sketch, "E12.3.30.3", {"start": v(-61, 208) * mm, "end": v(-61, 198) * mm});
            skLineSegment(sketch, "E12.3.31.0", {"start": v(-61, 222) * mm, "end": v(-51, 222) * mm});
            skLineSegment(sketch, "E12.3.31.1", {"start": v(-51, 222) * mm, "end": v(-51, 212) * mm});
            skLineSegment(sketch, "E12.3.31.2", {"start": v(-61, 212) * mm, "end": v(-51, 212) * mm});
            skLineSegment(sketch, "E12.3.31.3", {"start": v(-61, 222) * mm, "end": v(-61, 212) * mm});
            skLineSegment(sketch, "E12.4.0.0", {"start": v(-47, -212) * mm, "end": v(-37, -212) * mm});
            skLineSegment(sketch, "E12.4.0.1", {"start": v(-37, -212) * mm, "end": v(-37, -222) * mm});
            skLineSegment(sketch, "E12.4.0.2", {"start": v(-47, -222) * mm, "end": v(-37, -222) * mm});
            skLineSegment(sketch, "E12.4.0.3", {"start": v(-47, -212) * mm, "end": v(-47, -222) * mm});
            skLineSegment(sketch, "E12.4.1.0", {"start": v(-47, -198) * mm, "end": v(-37, -198) * mm});
            skLineSegment(sketch, "E12.4.1.1", {"start": v(-37, -198) * mm, "end": v(-37, -208) * mm});
            skLineSegment(sketch, "E12.4.1.2", {"start": v(-47, -208) * mm, "end": v(-37, -208) * mm});
            skLineSegment(sketch, "E12.4.1.3", {"start": v(-47, -198) * mm, "end": v(-47, -208) * mm});
            skLineSegment(sketch, "E12.4.2.0", {"start": v(-47, -184) * mm, "end": v(-37, -184) * mm});
            skLineSegment(sketch, "E12.4.2.1", {"start": v(-37, -184) * mm, "end": v(-37, -194) * mm});
            skLineSegment(sketch, "E12.4.2.2", {"start": v(-47, -194) * mm, "end": v(-37, -194) * mm});
            skLineSegment(sketch, "E12.4.2.3", {"start": v(-47, -184) * mm, "end": v(-47, -194) * mm});
            skLineSegment(sketch, "E12.4.3.0", {"start": v(-47, -170) * mm, "end": v(-37, -170) * mm});
            skLineSegment(sketch, "E12.4.3.1", {"start": v(-37, -170) * mm, "end": v(-37, -180) * mm});
            skLineSegment(sketch, "E12.4.3.2", {"start": v(-47, -180) * mm, "end": v(-37, -180) * mm});
            skLineSegment(sketch, "E12.4.3.3", {"start": v(-47, -170) * mm, "end": v(-47, -180) * mm});
            skLineSegment(sketch, "E12.4.4.0", {"start": v(-47, -156) * mm, "end": v(-37, -156) * mm});
            skLineSegment(sketch, "E12.4.4.1", {"start": v(-37, -156) * mm, "end": v(-37, -166) * mm});
            skLineSegment(sketch, "E12.4.4.2", {"start": v(-47, -166) * mm, "end": v(-37, -166) * mm});
            skLineSegment(sketch, "E12.4.4.3", {"start": v(-47, -156) * mm, "end": v(-47, -166) * mm});
            skLineSegment(sketch, "E12.4.5.0", {"start": v(-47, -142) * mm, "end": v(-37, -142) * mm});
            skLineSegment(sketch, "E12.4.5.1", {"start": v(-37, -142) * mm, "end": v(-37, -152) * mm});
            skLineSegment(sketch, "E12.4.5.2", {"start": v(-47, -152) * mm, "end": v(-37, -152) * mm});
            skLineSegment(sketch, "E12.4.5.3", {"start": v(-47, -142) * mm, "end": v(-47, -152) * mm});
            skLineSegment(sketch, "E12.4.6.0", {"start": v(-47, -128) * mm, "end": v(-37, -128) * mm});
            skLineSegment(sketch, "E12.4.6.1", {"start": v(-37, -128) * mm, "end": v(-37, -138) * mm});
            skLineSegment(sketch, "E12.4.6.2", {"start": v(-47, -138) * mm, "end": v(-37, -138) * mm});
            skLineSegment(sketch, "E12.4.6.3", {"start": v(-47, -128) * mm, "end": v(-47, -138) * mm});
            skLineSegment(sketch, "E12.4.7.0", {"start": v(-47, -114) * mm, "end": v(-37, -114) * mm});
            skLineSegment(sketch, "E12.4.7.1", {"start": v(-37, -114) * mm, "end": v(-37, -124) * mm});
            skLineSegment(sketch, "E12.4.7.2", {"start": v(-47, -124) * mm, "end": v(-37, -124) * mm});
            skLineSegment(sketch, "E12.4.7.3", {"start": v(-47, -114) * mm, "end": v(-47, -124) * mm});
            skLineSegment(sketch, "E12.4.8.0", {"start": v(-47, -100) * mm, "end": v(-37, -100) * mm});
            skLineSegment(sketch, "E12.4.8.1", {"start": v(-37, -100) * mm, "end": v(-37, -110) * mm});
            skLineSegment(sketch, "E12.4.8.2", {"start": v(-47, -110) * mm, "end": v(-37, -110) * mm});
            skLineSegment(sketch, "E12.4.8.3", {"start": v(-47, -100) * mm, "end": v(-47, -110) * mm});
            skLineSegment(sketch, "E12.4.9.0", {"start": v(-47, -86) * mm, "end": v(-37, -86) * mm});
            skLineSegment(sketch, "E12.4.9.1", {"start": v(-37, -86) * mm, "end": v(-37, -96) * mm});
            skLineSegment(sketch, "E12.4.9.2", {"start": v(-47, -96) * mm, "end": v(-37, -96) * mm});
            skLineSegment(sketch, "E12.4.9.3", {"start": v(-47, -86) * mm, "end": v(-47, -96) * mm});
            skLineSegment(sketch, "E12.4.10.0", {"start": v(-47, -72) * mm, "end": v(-37, -72) * mm});
            skLineSegment(sketch, "E12.4.10.1", {"start": v(-37, -72) * mm, "end": v(-37, -82) * mm});
            skLineSegment(sketch, "E12.4.10.2", {"start": v(-47, -82) * mm, "end": v(-37, -82) * mm});
            skLineSegment(sketch, "E12.4.10.3", {"start": v(-47, -72) * mm, "end": v(-47, -82) * mm});
            skLineSegment(sketch, "E12.4.11.0", {"start": v(-47, -58) * mm, "end": v(-37, -58) * mm});
            skLineSegment(sketch, "E12.4.11.1", {"start": v(-37, -58) * mm, "end": v(-37, -68) * mm});
            skLineSegment(sketch, "E12.4.11.2", {"start": v(-47, -68) * mm, "end": v(-37, -68) * mm});
            skLineSegment(sketch, "E12.4.11.3", {"start": v(-47, -58) * mm, "end": v(-47, -68) * mm});
            skLineSegment(sketch, "E12.4.12.0", {"start": v(-47, -44) * mm, "end": v(-37, -44) * mm});
            skLineSegment(sketch, "E12.4.12.1", {"start": v(-37, -44) * mm, "end": v(-37, -54) * mm});
            skLineSegment(sketch, "E12.4.12.2", {"start": v(-47, -54) * mm, "end": v(-37, -54) * mm});
            skLineSegment(sketch, "E12.4.12.3", {"start": v(-47, -44) * mm, "end": v(-47, -54) * mm});
            skLineSegment(sketch, "E12.4.13.0", {"start": v(-47, -30) * mm, "end": v(-37, -30) * mm});
            skLineSegment(sketch, "E12.4.13.1", {"start": v(-37, -30) * mm, "end": v(-37, -40) * mm});
            skLineSegment(sketch, "E12.4.13.2", {"start": v(-47, -40) * mm, "end": v(-37, -40) * mm});
            skLineSegment(sketch, "E12.4.13.3", {"start": v(-47, -30) * mm, "end": v(-47, -40) * mm});
            skLineSegment(sketch, "E12.4.14.0", {"start": v(-47, -16) * mm, "end": v(-37, -16) * mm});
            skLineSegment(sketch, "E12.4.14.1", {"start": v(-37, -16) * mm, "end": v(-37, -26) * mm});
            skLineSegment(sketch, "E12.4.14.2", {"start": v(-47, -26) * mm, "end": v(-37, -26) * mm});
            skLineSegment(sketch, "E12.4.14.3", {"start": v(-47, -16) * mm, "end": v(-47, -26) * mm});
            skLineSegment(sketch, "E12.4.15.0", {"start": v(-47, -2) * mm, "end": v(-37, -2) * mm});
            skLineSegment(sketch, "E12.4.15.1", {"start": v(-37, -2) * mm, "end": v(-37, -12) * mm});
            skLineSegment(sketch, "E12.4.15.2", {"start": v(-47, -12) * mm, "end": v(-37, -12) * mm});
            skLineSegment(sketch, "E12.4.15.3", {"start": v(-47, -2) * mm, "end": v(-47, -12) * mm});
            skLineSegment(sketch, "E12.4.16.0", {"start": v(-47, 12) * mm, "end": v(-37, 12) * mm});
            skLineSegment(sketch, "E12.4.16.1", {"start": v(-37, 12) * mm, "end": v(-37, 2) * mm});
            skLineSegment(sketch, "E12.4.16.2", {"start": v(-47, 2) * mm, "end": v(-37, 2) * mm});
            skLineSegment(sketch, "E12.4.16.3", {"start": v(-47, 12) * mm, "end": v(-47, 2) * mm});
            skLineSegment(sketch, "E12.4.17.0", {"start": v(-47, 26) * mm, "end": v(-37, 26) * mm});
            skLineSegment(sketch, "E12.4.17.1", {"start": v(-37, 26) * mm, "end": v(-37, 16) * mm});
            skLineSegment(sketch, "E12.4.17.2", {"start": v(-47, 16) * mm, "end": v(-37, 16) * mm});
            skLineSegment(sketch, "E12.4.17.3", {"start": v(-47, 26) * mm, "end": v(-47, 16) * mm});
            skLineSegment(sketch, "E12.4.18.0", {"start": v(-47, 40) * mm, "end": v(-37, 40) * mm});
            skLineSegment(sketch, "E12.4.18.1", {"start": v(-37, 40) * mm, "end": v(-37, 30) * mm});
            skLineSegment(sketch, "E12.4.18.2", {"start": v(-47, 30) * mm, "end": v(-37, 30) * mm});
            skLineSegment(sketch, "E12.4.18.3", {"start": v(-47, 40) * mm, "end": v(-47, 30) * mm});
            skLineSegment(sketch, "E12.4.19.0", {"start": v(-47, 54) * mm, "end": v(-37, 54) * mm});
            skLineSegment(sketch, "E12.4.19.1", {"start": v(-37, 54) * mm, "end": v(-37, 44) * mm});
            skLineSegment(sketch, "E12.4.19.2", {"start": v(-47, 44) * mm, "end": v(-37, 44) * mm});
            skLineSegment(sketch, "E12.4.19.3", {"start": v(-47, 54) * mm, "end": v(-47, 44) * mm});
            skLineSegment(sketch, "E12.4.20.0", {"start": v(-47, 68) * mm, "end": v(-37, 68) * mm});
            skLineSegment(sketch, "E12.4.20.1", {"start": v(-37, 68) * mm, "end": v(-37, 58) * mm});
            skLineSegment(sketch, "E12.4.20.2", {"start": v(-47, 58) * mm, "end": v(-37, 58) * mm});
            skLineSegment(sketch, "E12.4.20.3", {"start": v(-47, 68) * mm, "end": v(-47, 58) * mm});
            skLineSegment(sketch, "E12.4.21.0", {"start": v(-47, 82) * mm, "end": v(-37, 82) * mm});
            skLineSegment(sketch, "E12.4.21.1", {"start": v(-37, 82) * mm, "end": v(-37, 72) * mm});
            skLineSegment(sketch, "E12.4.21.2", {"start": v(-47, 72) * mm, "end": v(-37, 72) * mm});
            skLineSegment(sketch, "E12.4.21.3", {"start": v(-47, 82) * mm, "end": v(-47, 72) * mm});
            skLineSegment(sketch, "E12.4.22.0", {"start": v(-47, 96) * mm, "end": v(-37, 96) * mm});
            skLineSegment(sketch, "E12.4.22.1", {"start": v(-37, 96) * mm, "end": v(-37, 86) * mm});
            skLineSegment(sketch, "E12.4.22.2", {"start": v(-47, 86) * mm, "end": v(-37, 86) * mm});
            skLineSegment(sketch, "E12.4.22.3", {"start": v(-47, 96) * mm, "end": v(-47, 86) * mm});
            skLineSegment(sketch, "E12.4.23.0", {"start": v(-47, 110) * mm, "end": v(-37, 110) * mm});
            skLineSegment(sketch, "E12.4.23.1", {"start": v(-37, 110) * mm, "end": v(-37, 100) * mm});
            skLineSegment(sketch, "E12.4.23.2", {"start": v(-47, 100) * mm, "end": v(-37, 100) * mm});
            skLineSegment(sketch, "E12.4.23.3", {"start": v(-47, 110) * mm, "end": v(-47, 100) * mm});
            skLineSegment(sketch, "E12.4.24.0", {"start": v(-47, 124) * mm, "end": v(-37, 124) * mm});
            skLineSegment(sketch, "E12.4.24.1", {"start": v(-37, 124) * mm, "end": v(-37, 114) * mm});
            skLineSegment(sketch, "E12.4.24.2", {"start": v(-47, 114) * mm, "end": v(-37, 114) * mm});
            skLineSegment(sketch, "E12.4.24.3", {"start": v(-47, 124) * mm, "end": v(-47, 114) * mm});
            skLineSegment(sketch, "E12.4.25.0", {"start": v(-47, 138) * mm, "end": v(-37, 138) * mm});
            skLineSegment(sketch, "E12.4.25.1", {"start": v(-37, 138) * mm, "end": v(-37, 128) * mm});
            skLineSegment(sketch, "E12.4.25.2", {"start": v(-47, 128) * mm, "end": v(-37, 128) * mm});
            skLineSegment(sketch, "E12.4.25.3", {"start": v(-47, 138) * mm, "end": v(-47, 128) * mm});
            skLineSegment(sketch, "E12.4.26.0", {"start": v(-47, 152) * mm, "end": v(-37, 152) * mm});
            skLineSegment(sketch, "E12.4.26.1", {"start": v(-37, 152) * mm, "end": v(-37, 142) * mm});
            skLineSegment(sketch, "E12.4.26.2", {"start": v(-47, 142) * mm, "end": v(-37, 142) * mm});
            skLineSegment(sketch, "E12.4.26.3", {"start": v(-47, 152) * mm, "end": v(-47, 142) * mm});
            skLineSegment(sketch, "E12.4.27.0", {"start": v(-47, 166) * mm, "end": v(-37, 166) * mm});
            skLineSegment(sketch, "E12.4.27.1", {"start": v(-37, 166) * mm, "end": v(-37, 156) * mm});
            skLineSegment(sketch, "E12.4.27.2", {"start": v(-47, 156) * mm, "end": v(-37, 156) * mm});
            skLineSegment(sketch, "E12.4.27.3", {"start": v(-47, 166) * mm, "end": v(-47, 156) * mm});
            skLineSegment(sketch, "E12.4.28.0", {"start": v(-47, 180) * mm, "end": v(-37, 180) * mm});
            skLineSegment(sketch, "E12.4.28.1", {"start": v(-37, 180) * mm, "end": v(-37, 170) * mm});
            skLineSegment(sketch, "E12.4.28.2", {"start": v(-47, 170) * mm, "end": v(-37, 170) * mm});
            skLineSegment(sketch, "E12.4.28.3", {"start": v(-47, 180) * mm, "end": v(-47, 170) * mm});
            skLineSegment(sketch, "E12.4.29.0", {"start": v(-47, 194) * mm, "end": v(-37, 194) * mm});
            skLineSegment(sketch, "E12.4.29.1", {"start": v(-37, 194) * mm, "end": v(-37, 184) * mm});
            skLineSegment(sketch, "E12.4.29.2", {"start": v(-47, 184) * mm, "end": v(-37, 184) * mm});
            skLineSegment(sketch, "E12.4.29.3", {"start": v(-47, 194) * mm, "end": v(-47, 184) * mm});
            skLineSegment(sketch, "E12.4.30.0", {"start": v(-47, 208) * mm, "end": v(-37, 208) * mm});
            skLineSegment(sketch, "E12.4.30.1", {"start": v(-37, 208) * mm, "end": v(-37, 198) * mm});
            skLineSegment(sketch, "E12.4.30.2", {"start": v(-47, 198) * mm, "end": v(-37, 198) * mm});
            skLineSegment(sketch, "E12.4.30.3", {"start": v(-47, 208) * mm, "end": v(-47, 198) * mm});
            skLineSegment(sketch, "E12.4.31.0", {"start": v(-47, 222) * mm, "end": v(-37, 222) * mm});
            skLineSegment(sketch, "E12.4.31.1", {"start": v(-37, 222) * mm, "end": v(-37, 212) * mm});
            skLineSegment(sketch, "E12.4.31.2", {"start": v(-47, 212) * mm, "end": v(-37, 212) * mm});
            skLineSegment(sketch, "E12.4.31.3", {"start": v(-47, 222) * mm, "end": v(-47, 212) * mm});
            skLineSegment(sketch, "E12.5.0.0", {"start": v(-33, -212) * mm, "end": v(-23, -212) * mm});
            skLineSegment(sketch, "E12.5.0.1", {"start": v(-23, -212) * mm, "end": v(-23, -222) * mm});
            skLineSegment(sketch, "E12.5.0.2", {"start": v(-33, -222) * mm, "end": v(-23, -222) * mm});
            skLineSegment(sketch, "E12.5.0.3", {"start": v(-33, -212) * mm, "end": v(-33, -222) * mm});
            skLineSegment(sketch, "E12.5.1.0", {"start": v(-33, -198) * mm, "end": v(-23, -198) * mm});
            skLineSegment(sketch, "E12.5.1.1", {"start": v(-23, -198) * mm, "end": v(-23, -208) * mm});
            skLineSegment(sketch, "E12.5.1.2", {"start": v(-33, -208) * mm, "end": v(-23, -208) * mm});
            skLineSegment(sketch, "E12.5.1.3", {"start": v(-33, -198) * mm, "end": v(-33, -208) * mm});
            skLineSegment(sketch, "E12.5.2.0", {"start": v(-33, -184) * mm, "end": v(-23, -184) * mm});
            skLineSegment(sketch, "E12.5.2.1", {"start": v(-23, -184) * mm, "end": v(-23, -194) * mm});
            skLineSegment(sketch, "E12.5.2.2", {"start": v(-33, -194) * mm, "end": v(-23, -194) * mm});
            skLineSegment(sketch, "E12.5.2.3", {"start": v(-33, -184) * mm, "end": v(-33, -194) * mm});
            skLineSegment(sketch, "E12.5.3.0", {"start": v(-33, -170) * mm, "end": v(-23, -170) * mm});
            skLineSegment(sketch, "E12.5.3.1", {"start": v(-23, -170) * mm, "end": v(-23, -180) * mm});
            skLineSegment(sketch, "E12.5.3.2", {"start": v(-33, -180) * mm, "end": v(-23, -180) * mm});
            skLineSegment(sketch, "E12.5.3.3", {"start": v(-33, -170) * mm, "end": v(-33, -180) * mm});
            skLineSegment(sketch, "E12.5.4.0", {"start": v(-33, -156) * mm, "end": v(-23, -156) * mm});
            skLineSegment(sketch, "E12.5.4.1", {"start": v(-23, -156) * mm, "end": v(-23, -166) * mm});
            skLineSegment(sketch, "E12.5.4.2", {"start": v(-33, -166) * mm, "end": v(-23, -166) * mm});
            skLineSegment(sketch, "E12.5.4.3", {"start": v(-33, -156) * mm, "end": v(-33, -166) * mm});
            skLineSegment(sketch, "E12.5.5.0", {"start": v(-33, -142) * mm, "end": v(-23, -142) * mm});
            skLineSegment(sketch, "E12.5.5.1", {"start": v(-23, -142) * mm, "end": v(-23, -152) * mm});
            skLineSegment(sketch, "E12.5.5.2", {"start": v(-33, -152) * mm, "end": v(-23, -152) * mm});
            skLineSegment(sketch, "E12.5.5.3", {"start": v(-33, -142) * mm, "end": v(-33, -152) * mm});
            skLineSegment(sketch, "E12.5.6.0", {"start": v(-33, -128) * mm, "end": v(-23, -128) * mm});
            skLineSegment(sketch, "E12.5.6.1", {"start": v(-23, -128) * mm, "end": v(-23, -138) * mm});
            skLineSegment(sketch, "E12.5.6.2", {"start": v(-33, -138) * mm, "end": v(-23, -138) * mm});
            skLineSegment(sketch, "E12.5.6.3", {"start": v(-33, -128) * mm, "end": v(-33, -138) * mm});
            skLineSegment(sketch, "E12.5.7.0", {"start": v(-33, -114) * mm, "end": v(-23, -114) * mm});
            skLineSegment(sketch, "E12.5.7.1", {"start": v(-23, -114) * mm, "end": v(-23, -124) * mm});
            skLineSegment(sketch, "E12.5.7.2", {"start": v(-33, -124) * mm, "end": v(-23, -124) * mm});
            skLineSegment(sketch, "E12.5.7.3", {"start": v(-33, -114) * mm, "end": v(-33, -124) * mm});
            skLineSegment(sketch, "E12.5.8.0", {"start": v(-33, -100) * mm, "end": v(-23, -100) * mm});
            skLineSegment(sketch, "E12.5.8.1", {"start": v(-23, -100) * mm, "end": v(-23, -110) * mm});
            skLineSegment(sketch, "E12.5.8.2", {"start": v(-33, -110) * mm, "end": v(-23, -110) * mm});
            skLineSegment(sketch, "E12.5.8.3", {"start": v(-33, -100) * mm, "end": v(-33, -110) * mm});
            skLineSegment(sketch, "E12.5.9.0", {"start": v(-33, -86) * mm, "end": v(-23, -86) * mm});
            skLineSegment(sketch, "E12.5.9.1", {"start": v(-23, -86) * mm, "end": v(-23, -96) * mm});
            skLineSegment(sketch, "E12.5.9.2", {"start": v(-33, -96) * mm, "end": v(-23, -96) * mm});
            skLineSegment(sketch, "E12.5.9.3", {"start": v(-33, -86) * mm, "end": v(-33, -96) * mm});
            skLineSegment(sketch, "E12.5.10.0", {"start": v(-33, -72) * mm, "end": v(-23, -72) * mm});
            skLineSegment(sketch, "E12.5.10.1", {"start": v(-23, -72) * mm, "end": v(-23, -82) * mm});
            skLineSegment(sketch, "E12.5.10.2", {"start": v(-33, -82) * mm, "end": v(-23, -82) * mm});
            skLineSegment(sketch, "E12.5.10.3", {"start": v(-33, -72) * mm, "end": v(-33, -82) * mm});
            skLineSegment(sketch, "E12.5.11.0", {"start": v(-33, -58) * mm, "end": v(-23, -58) * mm});
            skLineSegment(sketch, "E12.5.11.1", {"start": v(-23, -58) * mm, "end": v(-23, -68) * mm});
            skLineSegment(sketch, "E12.5.11.2", {"start": v(-33, -68) * mm, "end": v(-23, -68) * mm});
            skLineSegment(sketch, "E12.5.11.3", {"start": v(-33, -58) * mm, "end": v(-33, -68) * mm});
            skLineSegment(sketch, "E12.5.12.0", {"start": v(-33, -44) * mm, "end": v(-23, -44) * mm});
            skLineSegment(sketch, "E12.5.12.1", {"start": v(-23, -44) * mm, "end": v(-23, -54) * mm});
            skLineSegment(sketch, "E12.5.12.2", {"start": v(-33, -54) * mm, "end": v(-23, -54) * mm});
            skLineSegment(sketch, "E12.5.12.3", {"start": v(-33, -44) * mm, "end": v(-33, -54) * mm});
            skLineSegment(sketch, "E12.5.13.0", {"start": v(-33, -30) * mm, "end": v(-23, -30) * mm});
            skLineSegment(sketch, "E12.5.13.1", {"start": v(-23, -30) * mm, "end": v(-23, -40) * mm});
            skLineSegment(sketch, "E12.5.13.2", {"start": v(-33, -40) * mm, "end": v(-23, -40) * mm});
            skLineSegment(sketch, "E12.5.13.3", {"start": v(-33, -30) * mm, "end": v(-33, -40) * mm});
            skLineSegment(sketch, "E12.5.14.0", {"start": v(-33, -16) * mm, "end": v(-23, -16) * mm});
            skLineSegment(sketch, "E12.5.14.1", {"start": v(-23, -16) * mm, "end": v(-23, -26) * mm});
            skLineSegment(sketch, "E12.5.14.2", {"start": v(-33, -26) * mm, "end": v(-23, -26) * mm});
            skLineSegment(sketch, "E12.5.14.3", {"start": v(-33, -16) * mm, "end": v(-33, -26) * mm});
            skLineSegment(sketch, "E12.5.15.0", {"start": v(-33, -2) * mm, "end": v(-23, -2) * mm});
            skLineSegment(sketch, "E12.5.15.1", {"start": v(-23, -2) * mm, "end": v(-23, -12) * mm});
            skLineSegment(sketch, "E12.5.15.2", {"start": v(-33, -12) * mm, "end": v(-23, -12) * mm});
            skLineSegment(sketch, "E12.5.15.3", {"start": v(-33, -2) * mm, "end": v(-33, -12) * mm});
            skLineSegment(sketch, "E12.5.16.0", {"start": v(-33, 12) * mm, "end": v(-23, 12) * mm});
            skLineSegment(sketch, "E12.5.16.1", {"start": v(-23, 12) * mm, "end": v(-23, 2) * mm});
            skLineSegment(sketch, "E12.5.16.2", {"start": v(-33, 2) * mm, "end": v(-23, 2) * mm});
            skLineSegment(sketch, "E12.5.16.3", {"start": v(-33, 12) * mm, "end": v(-33, 2) * mm});
            skLineSegment(sketch, "E12.5.17.0", {"start": v(-33, 26) * mm, "end": v(-23, 26) * mm});
            skLineSegment(sketch, "E12.5.17.1", {"start": v(-23, 26) * mm, "end": v(-23, 16) * mm});
            skLineSegment(sketch, "E12.5.17.2", {"start": v(-33, 16) * mm, "end": v(-23, 16) * mm});
            skLineSegment(sketch, "E12.5.17.3", {"start": v(-33, 26) * mm, "end": v(-33, 16) * mm});
            skLineSegment(sketch, "E12.5.18.0", {"start": v(-33, 40) * mm, "end": v(-23, 40) * mm});
            skLineSegment(sketch, "E12.5.18.1", {"start": v(-23, 40) * mm, "end": v(-23, 30) * mm});
            skLineSegment(sketch, "E12.5.18.2", {"start": v(-33, 30) * mm, "end": v(-23, 30) * mm});
            skLineSegment(sketch, "E12.5.18.3", {"start": v(-33, 40) * mm, "end": v(-33, 30) * mm});
            skLineSegment(sketch, "E12.5.19.0", {"start": v(-33, 54) * mm, "end": v(-23, 54) * mm});
            skLineSegment(sketch, "E12.5.19.1", {"start": v(-23, 54) * mm, "end": v(-23, 44) * mm});
            skLineSegment(sketch, "E12.5.19.2", {"start": v(-33, 44) * mm, "end": v(-23, 44) * mm});
            skLineSegment(sketch, "E12.5.19.3", {"start": v(-33, 54) * mm, "end": v(-33, 44) * mm});
            skLineSegment(sketch, "E12.5.20.0", {"start": v(-33, 68) * mm, "end": v(-23, 68) * mm});
            skLineSegment(sketch, "E12.5.20.1", {"start": v(-23, 68) * mm, "end": v(-23, 58) * mm});
            skLineSegment(sketch, "E12.5.20.2", {"start": v(-33, 58) * mm, "end": v(-23, 58) * mm});
            skLineSegment(sketch, "E12.5.20.3", {"start": v(-33, 68) * mm, "end": v(-33, 58) * mm});
            skLineSegment(sketch, "E12.5.21.0", {"start": v(-33, 82) * mm, "end": v(-23, 82) * mm});
            skLineSegment(sketch, "E12.5.21.1", {"start": v(-23, 82) * mm, "end": v(-23, 72) * mm});
            skLineSegment(sketch, "E12.5.21.2", {"start": v(-33, 72) * mm, "end": v(-23, 72) * mm});
            skLineSegment(sketch, "E12.5.21.3", {"start": v(-33, 82) * mm, "end": v(-33, 72) * mm});
            skLineSegment(sketch, "E12.5.22.0", {"start": v(-33, 96) * mm, "end": v(-23, 96) * mm});
            skLineSegment(sketch, "E12.5.22.1", {"start": v(-23, 96) * mm, "end": v(-23, 86) * mm});
            skLineSegment(sketch, "E12.5.22.2", {"start": v(-33, 86) * mm, "end": v(-23, 86) * mm});
            skLineSegment(sketch, "E12.5.22.3", {"start": v(-33, 96) * mm, "end": v(-33, 86) * mm});
            skLineSegment(sketch, "E12.5.23.0", {"start": v(-33, 110) * mm, "end": v(-23, 110) * mm});
            skLineSegment(sketch, "E12.5.23.1", {"start": v(-23, 110) * mm, "end": v(-23, 100) * mm});
            skLineSegment(sketch, "E12.5.23.2", {"start": v(-33, 100) * mm, "end": v(-23, 100) * mm});
            skLineSegment(sketch, "E12.5.23.3", {"start": v(-33, 110) * mm, "end": v(-33, 100) * mm});
            skLineSegment(sketch, "E12.5.24.0", {"start": v(-33, 124) * mm, "end": v(-23, 124) * mm});
            skLineSegment(sketch, "E12.5.24.1", {"start": v(-23, 124) * mm, "end": v(-23, 114) * mm});
            skLineSegment(sketch, "E12.5.24.2", {"start": v(-33, 114) * mm, "end": v(-23, 114) * mm});
            skLineSegment(sketch, "E12.5.24.3", {"start": v(-33, 124) * mm, "end": v(-33, 114) * mm});
            skLineSegment(sketch, "E12.5.25.0", {"start": v(-33, 138) * mm, "end": v(-23, 138) * mm});
            skLineSegment(sketch, "E12.5.25.1", {"start": v(-23, 138) * mm, "end": v(-23, 128) * mm});
            skLineSegment(sketch, "E12.5.25.2", {"start": v(-33, 128) * mm, "end": v(-23, 128) * mm});
            skLineSegment(sketch, "E12.5.25.3", {"start": v(-33, 138) * mm, "end": v(-33, 128) * mm});
            skLineSegment(sketch, "E12.5.26.0", {"start": v(-33, 152) * mm, "end": v(-23, 152) * mm});
            skLineSegment(sketch, "E12.5.26.1", {"start": v(-23, 152) * mm, "end": v(-23, 142) * mm});
            skLineSegment(sketch, "E12.5.26.2", {"start": v(-33, 142) * mm, "end": v(-23, 142) * mm});
            skLineSegment(sketch, "E12.5.26.3", {"start": v(-33, 152) * mm, "end": v(-33, 142) * mm});
            skLineSegment(sketch, "E12.5.27.0", {"start": v(-33, 166) * mm, "end": v(-23, 166) * mm});
            skLineSegment(sketch, "E12.5.27.1", {"start": v(-23, 166) * mm, "end": v(-23, 156) * mm});
            skLineSegment(sketch, "E12.5.27.2", {"start": v(-33, 156) * mm, "end": v(-23, 156) * mm});
            skLineSegment(sketch, "E12.5.27.3", {"start": v(-33, 166) * mm, "end": v(-33, 156) * mm});
            skLineSegment(sketch, "E12.5.28.0", {"start": v(-33, 180) * mm, "end": v(-23, 180) * mm});
            skLineSegment(sketch, "E12.5.28.1", {"start": v(-23, 180) * mm, "end": v(-23, 170) * mm});
            skLineSegment(sketch, "E12.5.28.2", {"start": v(-33, 170) * mm, "end": v(-23, 170) * mm});
            skLineSegment(sketch, "E12.5.28.3", {"start": v(-33, 180) * mm, "end": v(-33, 170) * mm});
            skLineSegment(sketch, "E12.5.29.0", {"start": v(-33, 194) * mm, "end": v(-23, 194) * mm});
            skLineSegment(sketch, "E12.5.29.1", {"start": v(-23, 194) * mm, "end": v(-23, 184) * mm});
            skLineSegment(sketch, "E12.5.29.2", {"start": v(-33, 184) * mm, "end": v(-23, 184) * mm});
            skLineSegment(sketch, "E12.5.29.3", {"start": v(-33, 194) * mm, "end": v(-33, 184) * mm});
            skLineSegment(sketch, "E12.5.30.0", {"start": v(-33, 208) * mm, "end": v(-23, 208) * mm});
            skLineSegment(sketch, "E12.5.30.1", {"start": v(-23, 208) * mm, "end": v(-23, 198) * mm});
            skLineSegment(sketch, "E12.5.30.2", {"start": v(-33, 198) * mm, "end": v(-23, 198) * mm});
            skLineSegment(sketch, "E12.5.30.3", {"start": v(-33, 208) * mm, "end": v(-33, 198) * mm});
            skLineSegment(sketch, "E12.5.31.0", {"start": v(-33, 222) * mm, "end": v(-23, 222) * mm});
            skLineSegment(sketch, "E12.5.31.1", {"start": v(-23, 222) * mm, "end": v(-23, 212) * mm});
            skLineSegment(sketch, "E12.5.31.2", {"start": v(-33, 212) * mm, "end": v(-23, 212) * mm});
            skLineSegment(sketch, "E12.5.31.3", {"start": v(-33, 222) * mm, "end": v(-33, 212) * mm});
            skLineSegment(sketch, "E12.6.0.0", {"start": v(-19, -212) * mm, "end": v(-9, -212) * mm});
            skLineSegment(sketch, "E12.6.0.1", {"start": v(-9, -212) * mm, "end": v(-9, -222) * mm});
            skLineSegment(sketch, "E12.6.0.2", {"start": v(-19, -222) * mm, "end": v(-9, -222) * mm});
            skLineSegment(sketch, "E12.6.0.3", {"start": v(-19, -212) * mm, "end": v(-19, -222) * mm});
            skLineSegment(sketch, "E12.6.1.0", {"start": v(-19, -198) * mm, "end": v(-9, -198) * mm});
            skLineSegment(sketch, "E12.6.1.1", {"start": v(-9, -198) * mm, "end": v(-9, -208) * mm});
            skLineSegment(sketch, "E12.6.1.2", {"start": v(-19, -208) * mm, "end": v(-9, -208) * mm});
            skLineSegment(sketch, "E12.6.1.3", {"start": v(-19, -198) * mm, "end": v(-19, -208) * mm});
            skLineSegment(sketch, "E12.6.2.0", {"start": v(-19, -184) * mm, "end": v(-9, -184) * mm});
            skLineSegment(sketch, "E12.6.2.1", {"start": v(-9, -184) * mm, "end": v(-9, -194) * mm});
            skLineSegment(sketch, "E12.6.2.2", {"start": v(-19, -194) * mm, "end": v(-9, -194) * mm});
            skLineSegment(sketch, "E12.6.2.3", {"start": v(-19, -184) * mm, "end": v(-19, -194) * mm});
            skLineSegment(sketch, "E12.6.3.0", {"start": v(-19, -170) * mm, "end": v(-9, -170) * mm});
            skLineSegment(sketch, "E12.6.3.1", {"start": v(-9, -170) * mm, "end": v(-9, -180) * mm});
            skLineSegment(sketch, "E12.6.3.2", {"start": v(-19, -180) * mm, "end": v(-9, -180) * mm});
            skLineSegment(sketch, "E12.6.3.3", {"start": v(-19, -170) * mm, "end": v(-19, -180) * mm});
            skLineSegment(sketch, "E12.6.4.0", {"start": v(-19, -156) * mm, "end": v(-9, -156) * mm});
            skLineSegment(sketch, "E12.6.4.1", {"start": v(-9, -156) * mm, "end": v(-9, -166) * mm});
            skLineSegment(sketch, "E12.6.4.2", {"start": v(-19, -166) * mm, "end": v(-9, -166) * mm});
            skLineSegment(sketch, "E12.6.4.3", {"start": v(-19, -156) * mm, "end": v(-19, -166) * mm});
            skLineSegment(sketch, "E12.6.5.0", {"start": v(-19, -142) * mm, "end": v(-9, -142) * mm});
            skLineSegment(sketch, "E12.6.5.1", {"start": v(-9, -142) * mm, "end": v(-9, -152) * mm});
            skLineSegment(sketch, "E12.6.5.2", {"start": v(-19, -152) * mm, "end": v(-9, -152) * mm});
            skLineSegment(sketch, "E12.6.5.3", {"start": v(-19, -142) * mm, "end": v(-19, -152) * mm});
            skLineSegment(sketch, "E12.6.6.0", {"start": v(-19, -128) * mm, "end": v(-9, -128) * mm});
            skLineSegment(sketch, "E12.6.6.1", {"start": v(-9, -128) * mm, "end": v(-9, -138) * mm});
            skLineSegment(sketch, "E12.6.6.2", {"start": v(-19, -138) * mm, "end": v(-9, -138) * mm});
            skLineSegment(sketch, "E12.6.6.3", {"start": v(-19, -128) * mm, "end": v(-19, -138) * mm});
            skLineSegment(sketch, "E12.6.7.0", {"start": v(-19, -114) * mm, "end": v(-9, -114) * mm});
            skLineSegment(sketch, "E12.6.7.1", {"start": v(-9, -114) * mm, "end": v(-9, -124) * mm});
            skLineSegment(sketch, "E12.6.7.2", {"start": v(-19, -124) * mm, "end": v(-9, -124) * mm});
            skLineSegment(sketch, "E12.6.7.3", {"start": v(-19, -114) * mm, "end": v(-19, -124) * mm});
            skLineSegment(sketch, "E12.6.8.0", {"start": v(-19, -100) * mm, "end": v(-9, -100) * mm});
            skLineSegment(sketch, "E12.6.8.1", {"start": v(-9, -100) * mm, "end": v(-9, -110) * mm});
            skLineSegment(sketch, "E12.6.8.2", {"start": v(-19, -110) * mm, "end": v(-9, -110) * mm});
            skLineSegment(sketch, "E12.6.8.3", {"start": v(-19, -100) * mm, "end": v(-19, -110) * mm});
            skLineSegment(sketch, "E12.6.9.0", {"start": v(-19, -86) * mm, "end": v(-9, -86) * mm});
            skLineSegment(sketch, "E12.6.9.1", {"start": v(-9, -86) * mm, "end": v(-9, -96) * mm});
            skLineSegment(sketch, "E12.6.9.2", {"start": v(-19, -96) * mm, "end": v(-9, -96) * mm});
            skLineSegment(sketch, "E12.6.9.3", {"start": v(-19, -86) * mm, "end": v(-19, -96) * mm});
            skLineSegment(sketch, "E12.6.10.0", {"start": v(-19, -72) * mm, "end": v(-9, -72) * mm});
            skLineSegment(sketch, "E12.6.10.1", {"start": v(-9, -72) * mm, "end": v(-9, -82) * mm});
            skLineSegment(sketch, "E12.6.10.2", {"start": v(-19, -82) * mm, "end": v(-9, -82) * mm});
            skLineSegment(sketch, "E12.6.10.3", {"start": v(-19, -72) * mm, "end": v(-19, -82) * mm});
            skLineSegment(sketch, "E12.6.11.0", {"start": v(-19, -58) * mm, "end": v(-9, -58) * mm});
            skLineSegment(sketch, "E12.6.11.1", {"start": v(-9, -58) * mm, "end": v(-9, -68) * mm});
            skLineSegment(sketch, "E12.6.11.2", {"start": v(-19, -68) * mm, "end": v(-9, -68) * mm});
            skLineSegment(sketch, "E12.6.11.3", {"start": v(-19, -58) * mm, "end": v(-19, -68) * mm});
            skLineSegment(sketch, "E12.6.12.0", {"start": v(-19, -44) * mm, "end": v(-9, -44) * mm});
            skLineSegment(sketch, "E12.6.12.1", {"start": v(-9, -44) * mm, "end": v(-9, -54) * mm});
            skLineSegment(sketch, "E12.6.12.2", {"start": v(-19, -54) * mm, "end": v(-9, -54) * mm});
            skLineSegment(sketch, "E12.6.12.3", {"start": v(-19, -44) * mm, "end": v(-19, -54) * mm});
            skLineSegment(sketch, "E12.6.13.0", {"start": v(-19, -30) * mm, "end": v(-9, -30) * mm});
            skLineSegment(sketch, "E12.6.13.1", {"start": v(-9, -30) * mm, "end": v(-9, -40) * mm});
            skLineSegment(sketch, "E12.6.13.2", {"start": v(-19, -40) * mm, "end": v(-9, -40) * mm});
            skLineSegment(sketch, "E12.6.13.3", {"start": v(-19, -30) * mm, "end": v(-19, -40) * mm});
            skLineSegment(sketch, "E12.6.14.0", {"start": v(-19, -16) * mm, "end": v(-9, -16) * mm});
            skLineSegment(sketch, "E12.6.14.1", {"start": v(-9, -16) * mm, "end": v(-9, -26) * mm});
            skLineSegment(sketch, "E12.6.14.2", {"start": v(-19, -26) * mm, "end": v(-9, -26) * mm});
            skLineSegment(sketch, "E12.6.14.3", {"start": v(-19, -16) * mm, "end": v(-19, -26) * mm});
            skLineSegment(sketch, "E12.6.15.0", {"start": v(-19, -2) * mm, "end": v(-9, -2) * mm});
            skLineSegment(sketch, "E12.6.15.1", {"start": v(-9, -2) * mm, "end": v(-9, -12) * mm});
            skLineSegment(sketch, "E12.6.15.2", {"start": v(-19, -12) * mm, "end": v(-9, -12) * mm});
            skLineSegment(sketch, "E12.6.15.3", {"start": v(-19, -2) * mm, "end": v(-19, -12) * mm});
            skLineSegment(sketch, "E12.6.16.0", {"start": v(-19, 12) * mm, "end": v(-9, 12) * mm});
            skLineSegment(sketch, "E12.6.16.1", {"start": v(-9, 12) * mm, "end": v(-9, 2) * mm});
            skLineSegment(sketch, "E12.6.16.2", {"start": v(-19, 2) * mm, "end": v(-9, 2) * mm});
            skLineSegment(sketch, "E12.6.16.3", {"start": v(-19, 12) * mm, "end": v(-19, 2) * mm});
            skLineSegment(sketch, "E12.6.17.0", {"start": v(-19, 26) * mm, "end": v(-9, 26) * mm});
            skLineSegment(sketch, "E12.6.17.1", {"start": v(-9, 26) * mm, "end": v(-9, 16) * mm});
            skLineSegment(sketch, "E12.6.17.2", {"start": v(-19, 16) * mm, "end": v(-9, 16) * mm});
            skLineSegment(sketch, "E12.6.17.3", {"start": v(-19, 26) * mm, "end": v(-19, 16) * mm});
            skLineSegment(sketch, "E12.6.18.0", {"start": v(-19, 40) * mm, "end": v(-9, 40) * mm});
            skLineSegment(sketch, "E12.6.18.1", {"start": v(-9, 40) * mm, "end": v(-9, 30) * mm});
            skLineSegment(sketch, "E12.6.18.2", {"start": v(-19, 30) * mm, "end": v(-9, 30) * mm});
            skLineSegment(sketch, "E12.6.18.3", {"start": v(-19, 40) * mm, "end": v(-19, 30) * mm});
            skLineSegment(sketch, "E12.6.19.0", {"start": v(-19, 54) * mm, "end": v(-9, 54) * mm});
            skLineSegment(sketch, "E12.6.19.1", {"start": v(-9, 54) * mm, "end": v(-9, 44) * mm});
            skLineSegment(sketch, "E12.6.19.2", {"start": v(-19, 44) * mm, "end": v(-9, 44) * mm});
            skLineSegment(sketch, "E12.6.19.3", {"start": v(-19, 54) * mm, "end": v(-19, 44) * mm});
            skLineSegment(sketch, "E12.6.20.0", {"start": v(-19, 68) * mm, "end": v(-9, 68) * mm});
            skLineSegment(sketch, "E12.6.20.1", {"start": v(-9, 68) * mm, "end": v(-9, 58) * mm});
            skLineSegment(sketch, "E12.6.20.2", {"start": v(-19, 58) * mm, "end": v(-9, 58) * mm});
            skLineSegment(sketch, "E12.6.20.3", {"start": v(-19, 68) * mm, "end": v(-19, 58) * mm});
            skLineSegment(sketch, "E12.6.21.0", {"start": v(-19, 82) * mm, "end": v(-9, 82) * mm});
            skLineSegment(sketch, "E12.6.21.1", {"start": v(-9, 82) * mm, "end": v(-9, 72) * mm});
            skLineSegment(sketch, "E12.6.21.2", {"start": v(-19, 72) * mm, "end": v(-9, 72) * mm});
            skLineSegment(sketch, "E12.6.21.3", {"start": v(-19, 82) * mm, "end": v(-19, 72) * mm});
            skLineSegment(sketch, "E12.6.22.0", {"start": v(-19, 96) * mm, "end": v(-9, 96) * mm});
            skLineSegment(sketch, "E12.6.22.1", {"start": v(-9, 96) * mm, "end": v(-9, 86) * mm});
            skLineSegment(sketch, "E12.6.22.2", {"start": v(-19, 86) * mm, "end": v(-9, 86) * mm});
            skLineSegment(sketch, "E12.6.22.3", {"start": v(-19, 96) * mm, "end": v(-19, 86) * mm});
            skLineSegment(sketch, "E12.6.23.0", {"start": v(-19, 110) * mm, "end": v(-9, 110) * mm});
            skLineSegment(sketch, "E12.6.23.1", {"start": v(-9, 110) * mm, "end": v(-9, 100) * mm});
            skLineSegment(sketch, "E12.6.23.2", {"start": v(-19, 100) * mm, "end": v(-9, 100) * mm});
            skLineSegment(sketch, "E12.6.23.3", {"start": v(-19, 110) * mm, "end": v(-19, 100) * mm});
            skLineSegment(sketch, "E12.6.24.0", {"start": v(-19, 124) * mm, "end": v(-9, 124) * mm});
            skLineSegment(sketch, "E12.6.24.1", {"start": v(-9, 124) * mm, "end": v(-9, 114) * mm});
            skLineSegment(sketch, "E12.6.24.2", {"start": v(-19, 114) * mm, "end": v(-9, 114) * mm});
            skLineSegment(sketch, "E12.6.24.3", {"start": v(-19, 124) * mm, "end": v(-19, 114) * mm});
            skLineSegment(sketch, "E12.6.25.0", {"start": v(-19, 138) * mm, "end": v(-9, 138) * mm});
            skLineSegment(sketch, "E12.6.25.1", {"start": v(-9, 138) * mm, "end": v(-9, 128) * mm});
            skLineSegment(sketch, "E12.6.25.2", {"start": v(-19, 128) * mm, "end": v(-9, 128) * mm});
            skLineSegment(sketch, "E12.6.25.3", {"start": v(-19, 138) * mm, "end": v(-19, 128) * mm});
            skLineSegment(sketch, "E12.6.26.0", {"start": v(-19, 152) * mm, "end": v(-9, 152) * mm});
            skLineSegment(sketch, "E12.6.26.1", {"start": v(-9, 152) * mm, "end": v(-9, 142) * mm});
            skLineSegment(sketch, "E12.6.26.2", {"start": v(-19, 142) * mm, "end": v(-9, 142) * mm});
            skLineSegment(sketch, "E12.6.26.3", {"start": v(-19, 152) * mm, "end": v(-19, 142) * mm});
            skLineSegment(sketch, "E12.6.27.0", {"start": v(-19, 166) * mm, "end": v(-9, 166) * mm});
            skLineSegment(sketch, "E12.6.27.1", {"start": v(-9, 166) * mm, "end": v(-9, 156) * mm});
            skLineSegment(sketch, "E12.6.27.2", {"start": v(-19, 156) * mm, "end": v(-9, 156) * mm});
            skLineSegment(sketch, "E12.6.27.3", {"start": v(-19, 166) * mm, "end": v(-19, 156) * mm});
            skLineSegment(sketch, "E12.6.28.0", {"start": v(-19, 180) * mm, "end": v(-9, 180) * mm});
            skLineSegment(sketch, "E12.6.28.1", {"start": v(-9, 180) * mm, "end": v(-9, 170) * mm});
            skLineSegment(sketch, "E12.6.28.2", {"start": v(-19, 170) * mm, "end": v(-9, 170) * mm});
            skLineSegment(sketch, "E12.6.28.3", {"start": v(-19, 180) * mm, "end": v(-19, 170) * mm});
            skLineSegment(sketch, "E12.6.29.0", {"start": v(-19, 194) * mm, "end": v(-9, 194) * mm});
            skLineSegment(sketch, "E12.6.29.1", {"start": v(-9, 194) * mm, "end": v(-9, 184) * mm});
            skLineSegment(sketch, "E12.6.29.2", {"start": v(-19, 184) * mm, "end": v(-9, 184) * mm});
            skLineSegment(sketch, "E12.6.29.3", {"start": v(-19, 194) * mm, "end": v(-19, 184) * mm});
            skLineSegment(sketch, "E12.6.30.0", {"start": v(-19, 208) * mm, "end": v(-9, 208) * mm});
            skLineSegment(sketch, "E12.6.30.1", {"start": v(-9, 208) * mm, "end": v(-9, 198) * mm});
            skLineSegment(sketch, "E12.6.30.2", {"start": v(-19, 198) * mm, "end": v(-9, 198) * mm});
            skLineSegment(sketch, "E12.6.30.3", {"start": v(-19, 208) * mm, "end": v(-19, 198) * mm});
            skLineSegment(sketch, "E12.6.31.0", {"start": v(-19, 222) * mm, "end": v(-9, 222) * mm});
            skLineSegment(sketch, "E12.6.31.1", {"start": v(-9, 222) * mm, "end": v(-9, 212) * mm});
            skLineSegment(sketch, "E12.6.31.2", {"start": v(-19, 212) * mm, "end": v(-9, 212) * mm});
            skLineSegment(sketch, "E12.6.31.3", {"start": v(-19, 222) * mm, "end": v(-19, 212) * mm});
            skLineSegment(sketch, "E12.7.0.0", {"start": v(-5, -212) * mm, "end": v(5, -212) * mm});
            skLineSegment(sketch, "E12.7.0.1", {"start": v(5, -212) * mm, "end": v(5, -222) * mm});
            skLineSegment(sketch, "E12.7.0.2", {"start": v(-5, -222) * mm, "end": v(5, -222) * mm});
            skLineSegment(sketch, "E12.7.0.3", {"start": v(-5, -212) * mm, "end": v(-5, -222) * mm});
            skLineSegment(sketch, "E12.7.1.0", {"start": v(-5, -198) * mm, "end": v(5, -198) * mm});
            skLineSegment(sketch, "E12.7.1.1", {"start": v(5, -198) * mm, "end": v(5, -208) * mm});
            skLineSegment(sketch, "E12.7.1.2", {"start": v(-5, -208) * mm, "end": v(5, -208) * mm});
            skLineSegment(sketch, "E12.7.1.3", {"start": v(-5, -198) * mm, "end": v(-5, -208) * mm});
            skLineSegment(sketch, "E12.7.2.0", {"start": v(-5, -184) * mm, "end": v(5, -184) * mm});
            skLineSegment(sketch, "E12.7.2.1", {"start": v(5, -184) * mm, "end": v(5, -194) * mm});
            skLineSegment(sketch, "E12.7.2.2", {"start": v(-5, -194) * mm, "end": v(5, -194) * mm});
            skLineSegment(sketch, "E12.7.2.3", {"start": v(-5, -184) * mm, "end": v(-5, -194) * mm});
            skLineSegment(sketch, "E12.7.3.0", {"start": v(-5, -170) * mm, "end": v(5, -170) * mm});
            skLineSegment(sketch, "E12.7.3.1", {"start": v(5, -170) * mm, "end": v(5, -180) * mm});
            skLineSegment(sketch, "E12.7.3.2", {"start": v(-5, -180) * mm, "end": v(5, -180) * mm});
            skLineSegment(sketch, "E12.7.3.3", {"start": v(-5, -170) * mm, "end": v(-5, -180) * mm});
            skLineSegment(sketch, "E12.7.4.0", {"start": v(-5, -156) * mm, "end": v(5, -156) * mm});
            skLineSegment(sketch, "E12.7.4.1", {"start": v(5, -156) * mm, "end": v(5, -166) * mm});
            skLineSegment(sketch, "E12.7.4.2", {"start": v(-5, -166) * mm, "end": v(5, -166) * mm});
            skLineSegment(sketch, "E12.7.4.3", {"start": v(-5, -156) * mm, "end": v(-5, -166) * mm});
            skLineSegment(sketch, "E12.7.5.0", {"start": v(-5, -142) * mm, "end": v(5, -142) * mm});
            skLineSegment(sketch, "E12.7.5.1", {"start": v(5, -142) * mm, "end": v(5, -152) * mm});
            skLineSegment(sketch, "E12.7.5.2", {"start": v(-5, -152) * mm, "end": v(5, -152) * mm});
            skLineSegment(sketch, "E12.7.5.3", {"start": v(-5, -142) * mm, "end": v(-5, -152) * mm});
            skLineSegment(sketch, "E12.7.6.0", {"start": v(-5, -128) * mm, "end": v(5, -128) * mm});
            skLineSegment(sketch, "E12.7.6.1", {"start": v(5, -128) * mm, "end": v(5, -138) * mm});
            skLineSegment(sketch, "E12.7.6.2", {"start": v(-5, -138) * mm, "end": v(5, -138) * mm});
            skLineSegment(sketch, "E12.7.6.3", {"start": v(-5, -128) * mm, "end": v(-5, -138) * mm});
            skLineSegment(sketch, "E12.7.7.0", {"start": v(-5, -114) * mm, "end": v(5, -114) * mm});
            skLineSegment(sketch, "E12.7.7.1", {"start": v(5, -114) * mm, "end": v(5, -124) * mm});
            skLineSegment(sketch, "E12.7.7.2", {"start": v(-5, -124) * mm, "end": v(5, -124) * mm});
            skLineSegment(sketch, "E12.7.7.3", {"start": v(-5, -114) * mm, "end": v(-5, -124) * mm});
            skLineSegment(sketch, "E12.7.8.0", {"start": v(-5, -100) * mm, "end": v(5, -100) * mm});
            skLineSegment(sketch, "E12.7.8.1", {"start": v(5, -100) * mm, "end": v(5, -110) * mm});
            skLineSegment(sketch, "E12.7.8.2", {"start": v(-5, -110) * mm, "end": v(5, -110) * mm});
            skLineSegment(sketch, "E12.7.8.3", {"start": v(-5, -100) * mm, "end": v(-5, -110) * mm});
            skLineSegment(sketch, "E12.7.9.0", {"start": v(-5, -86) * mm, "end": v(5, -86) * mm});
            skLineSegment(sketch, "E12.7.9.1", {"start": v(5, -86) * mm, "end": v(5, -96) * mm});
            skLineSegment(sketch, "E12.7.9.2", {"start": v(-5, -96) * mm, "end": v(5, -96) * mm});
            skLineSegment(sketch, "E12.7.9.3", {"start": v(-5, -86) * mm, "end": v(-5, -96) * mm});
            skLineSegment(sketch, "E12.7.10.0", {"start": v(-5, -72) * mm, "end": v(5, -72) * mm});
            skLineSegment(sketch, "E12.7.10.1", {"start": v(5, -72) * mm, "end": v(5, -82) * mm});
            skLineSegment(sketch, "E12.7.10.2", {"start": v(-5, -82) * mm, "end": v(5, -82) * mm});
            skLineSegment(sketch, "E12.7.10.3", {"start": v(-5, -72) * mm, "end": v(-5, -82) * mm});
            skLineSegment(sketch, "E12.7.11.0", {"start": v(-5, -58) * mm, "end": v(5, -58) * mm});
            skLineSegment(sketch, "E12.7.11.1", {"start": v(5, -58) * mm, "end": v(5, -68) * mm});
            skLineSegment(sketch, "E12.7.11.2", {"start": v(-5, -68) * mm, "end": v(5, -68) * mm});
            skLineSegment(sketch, "E12.7.11.3", {"start": v(-5, -58) * mm, "end": v(-5, -68) * mm});
            skLineSegment(sketch, "E12.7.12.0", {"start": v(-5, -44) * mm, "end": v(5, -44) * mm});
            skLineSegment(sketch, "E12.7.12.1", {"start": v(5, -44) * mm, "end": v(5, -54) * mm});
            skLineSegment(sketch, "E12.7.12.2", {"start": v(-5, -54) * mm, "end": v(5, -54) * mm});
            skLineSegment(sketch, "E12.7.12.3", {"start": v(-5, -44) * mm, "end": v(-5, -54) * mm});
            skLineSegment(sketch, "E12.7.13.0", {"start": v(-5, -30) * mm, "end": v(5, -30) * mm});
            skLineSegment(sketch, "E12.7.13.1", {"start": v(5, -30) * mm, "end": v(5, -40) * mm});
            skLineSegment(sketch, "E12.7.13.2", {"start": v(-5, -40) * mm, "end": v(5, -40) * mm});
            skLineSegment(sketch, "E12.7.13.3", {"start": v(-5, -30) * mm, "end": v(-5, -40) * mm});
            skLineSegment(sketch, "E12.7.14.0", {"start": v(-5, -16) * mm, "end": v(5, -16) * mm});
            skLineSegment(sketch, "E12.7.14.1", {"start": v(5, -16) * mm, "end": v(5, -26) * mm});
            skLineSegment(sketch, "E12.7.14.2", {"start": v(-5, -26) * mm, "end": v(5, -26) * mm});
            skLineSegment(sketch, "E12.7.14.3", {"start": v(-5, -16) * mm, "end": v(-5, -26) * mm});
            skLineSegment(sketch, "E12.7.15.0", {"start": v(-5, -2) * mm, "end": v(5, -2) * mm});
            skLineSegment(sketch, "E12.7.15.1", {"start": v(5, -2) * mm, "end": v(5, -12) * mm});
            skLineSegment(sketch, "E12.7.15.2", {"start": v(-5, -12) * mm, "end": v(5, -12) * mm});
            skLineSegment(sketch, "E12.7.15.3", {"start": v(-5, -2) * mm, "end": v(-5, -12) * mm});
            skLineSegment(sketch, "E12.7.16.0", {"start": v(-5, 12) * mm, "end": v(5, 12) * mm});
            skLineSegment(sketch, "E12.7.16.1", {"start": v(5, 12) * mm, "end": v(5, 2) * mm});
            skLineSegment(sketch, "E12.7.16.2", {"start": v(-5, 2) * mm, "end": v(5, 2) * mm});
            skLineSegment(sketch, "E12.7.16.3", {"start": v(-5, 12) * mm, "end": v(-5, 2) * mm});
            skLineSegment(sketch, "E12.7.17.0", {"start": v(-5, 26) * mm, "end": v(5, 26) * mm});
            skLineSegment(sketch, "E12.7.17.1", {"start": v(5, 26) * mm, "end": v(5, 16) * mm});
            skLineSegment(sketch, "E12.7.17.2", {"start": v(-5, 16) * mm, "end": v(5, 16) * mm});
            skLineSegment(sketch, "E12.7.17.3", {"start": v(-5, 26) * mm, "end": v(-5, 16) * mm});
            skLineSegment(sketch, "E12.7.18.0", {"start": v(-5, 40) * mm, "end": v(5, 40) * mm});
            skLineSegment(sketch, "E12.7.18.1", {"start": v(5, 40) * mm, "end": v(5, 30) * mm});
            skLineSegment(sketch, "E12.7.18.2", {"start": v(-5, 30) * mm, "end": v(5, 30) * mm});
            skLineSegment(sketch, "E12.7.18.3", {"start": v(-5, 40) * mm, "end": v(-5, 30) * mm});
            skLineSegment(sketch, "E12.7.19.0", {"start": v(-5, 54) * mm, "end": v(5, 54) * mm});
            skLineSegment(sketch, "E12.7.19.1", {"start": v(5, 54) * mm, "end": v(5, 44) * mm});
            skLineSegment(sketch, "E12.7.19.2", {"start": v(-5, 44) * mm, "end": v(5, 44) * mm});
            skLineSegment(sketch, "E12.7.19.3", {"start": v(-5, 54) * mm, "end": v(-5, 44) * mm});
            skLineSegment(sketch, "E12.7.20.0", {"start": v(-5, 68) * mm, "end": v(5, 68) * mm});
            skLineSegment(sketch, "E12.7.20.1", {"start": v(5, 68) * mm, "end": v(5, 58) * mm});
            skLineSegment(sketch, "E12.7.20.2", {"start": v(-5, 58) * mm, "end": v(5, 58) * mm});
            skLineSegment(sketch, "E12.7.20.3", {"start": v(-5, 68) * mm, "end": v(-5, 58) * mm});
            skLineSegment(sketch, "E12.7.21.0", {"start": v(-5, 82) * mm, "end": v(5, 82) * mm});
            skLineSegment(sketch, "E12.7.21.1", {"start": v(5, 82) * mm, "end": v(5, 72) * mm});
            skLineSegment(sketch, "E12.7.21.2", {"start": v(-5, 72) * mm, "end": v(5, 72) * mm});
            skLineSegment(sketch, "E12.7.21.3", {"start": v(-5, 82) * mm, "end": v(-5, 72) * mm});
            skLineSegment(sketch, "E12.7.22.0", {"start": v(-5, 96) * mm, "end": v(5, 96) * mm});
            skLineSegment(sketch, "E12.7.22.1", {"start": v(5, 96) * mm, "end": v(5, 86) * mm});
            skLineSegment(sketch, "E12.7.22.2", {"start": v(-5, 86) * mm, "end": v(5, 86) * mm});
            skLineSegment(sketch, "E12.7.22.3", {"start": v(-5, 96) * mm, "end": v(-5, 86) * mm});
            skLineSegment(sketch, "E12.7.23.0", {"start": v(-5, 110) * mm, "end": v(5, 110) * mm});
            skLineSegment(sketch, "E12.7.23.1", {"start": v(5, 110) * mm, "end": v(5, 100) * mm});
            skLineSegment(sketch, "E12.7.23.2", {"start": v(-5, 100) * mm, "end": v(5, 100) * mm});
            skLineSegment(sketch, "E12.7.23.3", {"start": v(-5, 110) * mm, "end": v(-5, 100) * mm});
            skLineSegment(sketch, "E12.7.24.0", {"start": v(-5, 124) * mm, "end": v(5, 124) * mm});
            skLineSegment(sketch, "E12.7.24.1", {"start": v(5, 124) * mm, "end": v(5, 114) * mm});
            skLineSegment(sketch, "E12.7.24.2", {"start": v(-5, 114) * mm, "end": v(5, 114) * mm});
            skLineSegment(sketch, "E12.7.24.3", {"start": v(-5, 124) * mm, "end": v(-5, 114) * mm});
            skLineSegment(sketch, "E12.7.25.0", {"start": v(-5, 138) * mm, "end": v(5, 138) * mm});
            skLineSegment(sketch, "E12.7.25.1", {"start": v(5, 138) * mm, "end": v(5, 128) * mm});
            skLineSegment(sketch, "E12.7.25.2", {"start": v(-5, 128) * mm, "end": v(5, 128) * mm});
            skLineSegment(sketch, "E12.7.25.3", {"start": v(-5, 138) * mm, "end": v(-5, 128) * mm});
            skLineSegment(sketch, "E12.7.26.0", {"start": v(-5, 152) * mm, "end": v(5, 152) * mm});
            skLineSegment(sketch, "E12.7.26.1", {"start": v(5, 152) * mm, "end": v(5, 142) * mm});
            skLineSegment(sketch, "E12.7.26.2", {"start": v(-5, 142) * mm, "end": v(5, 142) * mm});
            skLineSegment(sketch, "E12.7.26.3", {"start": v(-5, 152) * mm, "end": v(-5, 142) * mm});
            skLineSegment(sketch, "E12.7.27.0", {"start": v(-5, 166) * mm, "end": v(5, 166) * mm});
            skLineSegment(sketch, "E12.7.27.1", {"start": v(5, 166) * mm, "end": v(5, 156) * mm});
            skLineSegment(sketch, "E12.7.27.2", {"start": v(-5, 156) * mm, "end": v(5, 156) * mm});
            skLineSegment(sketch, "E12.7.27.3", {"start": v(-5, 166) * mm, "end": v(-5, 156) * mm});
            skLineSegment(sketch, "E12.7.28.0", {"start": v(-5, 180) * mm, "end": v(5, 180) * mm});
            skLineSegment(sketch, "E12.7.28.1", {"start": v(5, 180) * mm, "end": v(5, 170) * mm});
            skLineSegment(sketch, "E12.7.28.2", {"start": v(-5, 170) * mm, "end": v(5, 170) * mm});
            skLineSegment(sketch, "E12.7.28.3", {"start": v(-5, 180) * mm, "end": v(-5, 170) * mm});
            skLineSegment(sketch, "E12.7.29.0", {"start": v(-5, 194) * mm, "end": v(5, 194) * mm});
            skLineSegment(sketch, "E12.7.29.1", {"start": v(5, 194) * mm, "end": v(5, 184) * mm});
            skLineSegment(sketch, "E12.7.29.2", {"start": v(-5, 184) * mm, "end": v(5, 184) * mm});
            skLineSegment(sketch, "E12.7.29.3", {"start": v(-5, 194) * mm, "end": v(-5, 184) * mm});
            skLineSegment(sketch, "E12.7.30.0", {"start": v(-5, 208) * mm, "end": v(5, 208) * mm});
            skLineSegment(sketch, "E12.7.30.1", {"start": v(5, 208) * mm, "end": v(5, 198) * mm});
            skLineSegment(sketch, "E12.7.30.2", {"start": v(-5, 198) * mm, "end": v(5, 198) * mm});
            skLineSegment(sketch, "E12.7.30.3", {"start": v(-5, 208) * mm, "end": v(-5, 198) * mm});
            skLineSegment(sketch, "E12.7.31.0", {"start": v(-5, 222) * mm, "end": v(5, 222) * mm});
            skLineSegment(sketch, "E12.7.31.1", {"start": v(5, 222) * mm, "end": v(5, 212) * mm});
            skLineSegment(sketch, "E12.7.31.2", {"start": v(-5, 212) * mm, "end": v(5, 212) * mm});
            skLineSegment(sketch, "E12.7.31.3", {"start": v(-5, 222) * mm, "end": v(-5, 212) * mm});
            skLineSegment(sketch, "E12.8.0.0", {"start": v(9, -212) * mm, "end": v(19, -212) * mm});
            skLineSegment(sketch, "E12.8.0.1", {"start": v(19, -212) * mm, "end": v(19, -222) * mm});
            skLineSegment(sketch, "E12.8.0.2", {"start": v(9, -222) * mm, "end": v(19, -222) * mm});
            skLineSegment(sketch, "E12.8.0.3", {"start": v(9, -212) * mm, "end": v(9, -222) * mm});
            skLineSegment(sketch, "E12.8.1.0", {"start": v(9, -198) * mm, "end": v(19, -198) * mm});
            skLineSegment(sketch, "E12.8.1.1", {"start": v(19, -198) * mm, "end": v(19, -208) * mm});
            skLineSegment(sketch, "E12.8.1.2", {"start": v(9, -208) * mm, "end": v(19, -208) * mm});
            skLineSegment(sketch, "E12.8.1.3", {"start": v(9, -198) * mm, "end": v(9, -208) * mm});
            skLineSegment(sketch, "E12.8.2.0", {"start": v(9, -184) * mm, "end": v(19, -184) * mm});
            skLineSegment(sketch, "E12.8.2.1", {"start": v(19, -184) * mm, "end": v(19, -194) * mm});
            skLineSegment(sketch, "E12.8.2.2", {"start": v(9, -194) * mm, "end": v(19, -194) * mm});
            skLineSegment(sketch, "E12.8.2.3", {"start": v(9, -184) * mm, "end": v(9, -194) * mm});
            skLineSegment(sketch, "E12.8.3.0", {"start": v(9, -170) * mm, "end": v(19, -170) * mm});
            skLineSegment(sketch, "E12.8.3.1", {"start": v(19, -170) * mm, "end": v(19, -180) * mm});
            skLineSegment(sketch, "E12.8.3.2", {"start": v(9, -180) * mm, "end": v(19, -180) * mm});
            skLineSegment(sketch, "E12.8.3.3", {"start": v(9, -170) * mm, "end": v(9, -180) * mm});
            skLineSegment(sketch, "E12.8.4.0", {"start": v(9, -156) * mm, "end": v(19, -156) * mm});
            skLineSegment(sketch, "E12.8.4.1", {"start": v(19, -156) * mm, "end": v(19, -166) * mm});
            skLineSegment(sketch, "E12.8.4.2", {"start": v(9, -166) * mm, "end": v(19, -166) * mm});
            skLineSegment(sketch, "E12.8.4.3", {"start": v(9, -156) * mm, "end": v(9, -166) * mm});
            skLineSegment(sketch, "E12.8.5.0", {"start": v(9, -142) * mm, "end": v(19, -142) * mm});
            skLineSegment(sketch, "E12.8.5.1", {"start": v(19, -142) * mm, "end": v(19, -152) * mm});
            skLineSegment(sketch, "E12.8.5.2", {"start": v(9, -152) * mm, "end": v(19, -152) * mm});
            skLineSegment(sketch, "E12.8.5.3", {"start": v(9, -142) * mm, "end": v(9, -152) * mm});
            skLineSegment(sketch, "E12.8.6.0", {"start": v(9, -128) * mm, "end": v(19, -128) * mm});
            skLineSegment(sketch, "E12.8.6.1", {"start": v(19, -128) * mm, "end": v(19, -138) * mm});
            skLineSegment(sketch, "E12.8.6.2", {"start": v(9, -138) * mm, "end": v(19, -138) * mm});
            skLineSegment(sketch, "E12.8.6.3", {"start": v(9, -128) * mm, "end": v(9, -138) * mm});
            skLineSegment(sketch, "E12.8.7.0", {"start": v(9, -114) * mm, "end": v(19, -114) * mm});
            skLineSegment(sketch, "E12.8.7.1", {"start": v(19, -114) * mm, "end": v(19, -124) * mm});
            skLineSegment(sketch, "E12.8.7.2", {"start": v(9, -124) * mm, "end": v(19, -124) * mm});
            skLineSegment(sketch, "E12.8.7.3", {"start": v(9, -114) * mm, "end": v(9, -124) * mm});
            skLineSegment(sketch, "E12.8.8.0", {"start": v(9, -100) * mm, "end": v(19, -100) * mm});
            skLineSegment(sketch, "E12.8.8.1", {"start": v(19, -100) * mm, "end": v(19, -110) * mm});
            skLineSegment(sketch, "E12.8.8.2", {"start": v(9, -110) * mm, "end": v(19, -110) * mm});
            skLineSegment(sketch, "E12.8.8.3", {"start": v(9, -100) * mm, "end": v(9, -110) * mm});
            skLineSegment(sketch, "E12.8.9.0", {"start": v(9, -86) * mm, "end": v(19, -86) * mm});
            skLineSegment(sketch, "E12.8.9.1", {"start": v(19, -86) * mm, "end": v(19, -96) * mm});
            skLineSegment(sketch, "E12.8.9.2", {"start": v(9, -96) * mm, "end": v(19, -96) * mm});
            skLineSegment(sketch, "E12.8.9.3", {"start": v(9, -86) * mm, "end": v(9, -96) * mm});
            skLineSegment(sketch, "E12.8.10.0", {"start": v(9, -72) * mm, "end": v(19, -72) * mm});
            skLineSegment(sketch, "E12.8.10.1", {"start": v(19, -72) * mm, "end": v(19, -82) * mm});
            skLineSegment(sketch, "E12.8.10.2", {"start": v(9, -82) * mm, "end": v(19, -82) * mm});
            skLineSegment(sketch, "E12.8.10.3", {"start": v(9, -72) * mm, "end": v(9, -82) * mm});
            skLineSegment(sketch, "E12.8.11.0", {"start": v(9, -58) * mm, "end": v(19, -58) * mm});
            skLineSegment(sketch, "E12.8.11.1", {"start": v(19, -58) * mm, "end": v(19, -68) * mm});
            skLineSegment(sketch, "E12.8.11.2", {"start": v(9, -68) * mm, "end": v(19, -68) * mm});
            skLineSegment(sketch, "E12.8.11.3", {"start": v(9, -58) * mm, "end": v(9, -68) * mm});
            skLineSegment(sketch, "E12.8.12.0", {"start": v(9, -44) * mm, "end": v(19, -44) * mm});
            skLineSegment(sketch, "E12.8.12.1", {"start": v(19, -44) * mm, "end": v(19, -54) * mm});
            skLineSegment(sketch, "E12.8.12.2", {"start": v(9, -54) * mm, "end": v(19, -54) * mm});
            skLineSegment(sketch, "E12.8.12.3", {"start": v(9, -44) * mm, "end": v(9, -54) * mm});
            skLineSegment(sketch, "E12.8.13.0", {"start": v(9, -30) * mm, "end": v(19, -30) * mm});
            skLineSegment(sketch, "E12.8.13.1", {"start": v(19, -30) * mm, "end": v(19, -40) * mm});
            skLineSegment(sketch, "E12.8.13.2", {"start": v(9, -40) * mm, "end": v(19, -40) * mm});
            skLineSegment(sketch, "E12.8.13.3", {"start": v(9, -30) * mm, "end": v(9, -40) * mm});
            skLineSegment(sketch, "E12.8.14.0", {"start": v(9, -16) * mm, "end": v(19, -16) * mm});
            skLineSegment(sketch, "E12.8.14.1", {"start": v(19, -16) * mm, "end": v(19, -26) * mm});
            skLineSegment(sketch, "E12.8.14.2", {"start": v(9, -26) * mm, "end": v(19, -26) * mm});
            skLineSegment(sketch, "E12.8.14.3", {"start": v(9, -16) * mm, "end": v(9, -26) * mm});
            skLineSegment(sketch, "E12.8.15.0", {"start": v(9, -2) * mm, "end": v(19, -2) * mm});
            skLineSegment(sketch, "E12.8.15.1", {"start": v(19, -2) * mm, "end": v(19, -12) * mm});
            skLineSegment(sketch, "E12.8.15.2", {"start": v(9, -12) * mm, "end": v(19, -12) * mm});
            skLineSegment(sketch, "E12.8.15.3", {"start": v(9, -2) * mm, "end": v(9, -12) * mm});
            skLineSegment(sketch, "E12.8.16.0", {"start": v(9, 12) * mm, "end": v(19, 12) * mm});
            skLineSegment(sketch, "E12.8.16.1", {"start": v(19, 12) * mm, "end": v(19, 2) * mm});
            skLineSegment(sketch, "E12.8.16.2", {"start": v(9, 2) * mm, "end": v(19, 2) * mm});
            skLineSegment(sketch, "E12.8.16.3", {"start": v(9, 12) * mm, "end": v(9, 2) * mm});
            skLineSegment(sketch, "E12.8.17.0", {"start": v(9, 26) * mm, "end": v(19, 26) * mm});
            skLineSegment(sketch, "E12.8.17.1", {"start": v(19, 26) * mm, "end": v(19, 16) * mm});
            skLineSegment(sketch, "E12.8.17.2", {"start": v(9, 16) * mm, "end": v(19, 16) * mm});
            skLineSegment(sketch, "E12.8.17.3", {"start": v(9, 26) * mm, "end": v(9, 16) * mm});
            skLineSegment(sketch, "E12.8.18.0", {"start": v(9, 40) * mm, "end": v(19, 40) * mm});
            skLineSegment(sketch, "E12.8.18.1", {"start": v(19, 40) * mm, "end": v(19, 30) * mm});
            skLineSegment(sketch, "E12.8.18.2", {"start": v(9, 30) * mm, "end": v(19, 30) * mm});
            skLineSegment(sketch, "E12.8.18.3", {"start": v(9, 40) * mm, "end": v(9, 30) * mm});
            skLineSegment(sketch, "E12.8.19.0", {"start": v(9, 54) * mm, "end": v(19, 54) * mm});
            skLineSegment(sketch, "E12.8.19.1", {"start": v(19, 54) * mm, "end": v(19, 44) * mm});
            skLineSegment(sketch, "E12.8.19.2", {"start": v(9, 44) * mm, "end": v(19, 44) * mm});
            skLineSegment(sketch, "E12.8.19.3", {"start": v(9, 54) * mm, "end": v(9, 44) * mm});
            skLineSegment(sketch, "E12.8.20.0", {"start": v(9, 68) * mm, "end": v(19, 68) * mm});
            skLineSegment(sketch, "E12.8.20.1", {"start": v(19, 68) * mm, "end": v(19, 58) * mm});
            skLineSegment(sketch, "E12.8.20.2", {"start": v(9, 58) * mm, "end": v(19, 58) * mm});
            skLineSegment(sketch, "E12.8.20.3", {"start": v(9, 68) * mm, "end": v(9, 58) * mm});
            skLineSegment(sketch, "E12.8.21.0", {"start": v(9, 82) * mm, "end": v(19, 82) * mm});
            skLineSegment(sketch, "E12.8.21.1", {"start": v(19, 82) * mm, "end": v(19, 72) * mm});
            skLineSegment(sketch, "E12.8.21.2", {"start": v(9, 72) * mm, "end": v(19, 72) * mm});
            skLineSegment(sketch, "E12.8.21.3", {"start": v(9, 82) * mm, "end": v(9, 72) * mm});
            skLineSegment(sketch, "E12.8.22.0", {"start": v(9, 96) * mm, "end": v(19, 96) * mm});
            skLineSegment(sketch, "E12.8.22.1", {"start": v(19, 96) * mm, "end": v(19, 86) * mm});
            skLineSegment(sketch, "E12.8.22.2", {"start": v(9, 86) * mm, "end": v(19, 86) * mm});
            skLineSegment(sketch, "E12.8.22.3", {"start": v(9, 96) * mm, "end": v(9, 86) * mm});
            skLineSegment(sketch, "E12.8.23.0", {"start": v(9, 110) * mm, "end": v(19, 110) * mm});
            skLineSegment(sketch, "E12.8.23.1", {"start": v(19, 110) * mm, "end": v(19, 100) * mm});
            skLineSegment(sketch, "E12.8.23.2", {"start": v(9, 100) * mm, "end": v(19, 100) * mm});
            skLineSegment(sketch, "E12.8.23.3", {"start": v(9, 110) * mm, "end": v(9, 100) * mm});
            skLineSegment(sketch, "E12.8.24.0", {"start": v(9, 124) * mm, "end": v(19, 124) * mm});
            skLineSegment(sketch, "E12.8.24.1", {"start": v(19, 124) * mm, "end": v(19, 114) * mm});
            skLineSegment(sketch, "E12.8.24.2", {"start": v(9, 114) * mm, "end": v(19, 114) * mm});
            skLineSegment(sketch, "E12.8.24.3", {"start": v(9, 124) * mm, "end": v(9, 114) * mm});
            skLineSegment(sketch, "E12.8.25.0", {"start": v(9, 138) * mm, "end": v(19, 138) * mm});
            skLineSegment(sketch, "E12.8.25.1", {"start": v(19, 138) * mm, "end": v(19, 128) * mm});
            skLineSegment(sketch, "E12.8.25.2", {"start": v(9, 128) * mm, "end": v(19, 128) * mm});
            skLineSegment(sketch, "E12.8.25.3", {"start": v(9, 138) * mm, "end": v(9, 128) * mm});
            skLineSegment(sketch, "E12.8.26.0", {"start": v(9, 152) * mm, "end": v(19, 152) * mm});
            skLineSegment(sketch, "E12.8.26.1", {"start": v(19, 152) * mm, "end": v(19, 142) * mm});
            skLineSegment(sketch, "E12.8.26.2", {"start": v(9, 142) * mm, "end": v(19, 142) * mm});
            skLineSegment(sketch, "E12.8.26.3", {"start": v(9, 152) * mm, "end": v(9, 142) * mm});
            skLineSegment(sketch, "E12.8.27.0", {"start": v(9, 166) * mm, "end": v(19, 166) * mm});
            skLineSegment(sketch, "E12.8.27.1", {"start": v(19, 166) * mm, "end": v(19, 156) * mm});
            skLineSegment(sketch, "E12.8.27.2", {"start": v(9, 156) * mm, "end": v(19, 156) * mm});
            skLineSegment(sketch, "E12.8.27.3", {"start": v(9, 166) * mm, "end": v(9, 156) * mm});
            skLineSegment(sketch, "E12.8.28.0", {"start": v(9, 180) * mm, "end": v(19, 180) * mm});
            skLineSegment(sketch, "E12.8.28.1", {"start": v(19, 180) * mm, "end": v(19, 170) * mm});
            skLineSegment(sketch, "E12.8.28.2", {"start": v(9, 170) * mm, "end": v(19, 170) * mm});
            skLineSegment(sketch, "E12.8.28.3", {"start": v(9, 180) * mm, "end": v(9, 170) * mm});
            skLineSegment(sketch, "E12.8.29.0", {"start": v(9, 194) * mm, "end": v(19, 194) * mm});
            skLineSegment(sketch, "E12.8.29.1", {"start": v(19, 194) * mm, "end": v(19, 184) * mm});
            skLineSegment(sketch, "E12.8.29.2", {"start": v(9, 184) * mm, "end": v(19, 184) * mm});
            skLineSegment(sketch, "E12.8.29.3", {"start": v(9, 194) * mm, "end": v(9, 184) * mm});
            skLineSegment(sketch, "E12.8.30.0", {"start": v(9, 208) * mm, "end": v(19, 208) * mm});
            skLineSegment(sketch, "E12.8.30.1", {"start": v(19, 208) * mm, "end": v(19, 198) * mm});
            skLineSegment(sketch, "E12.8.30.2", {"start": v(9, 198) * mm, "end": v(19, 198) * mm});
            skLineSegment(sketch, "E12.8.30.3", {"start": v(9, 208) * mm, "end": v(9, 198) * mm});
            skLineSegment(sketch, "E12.8.31.0", {"start": v(9, 222) * mm, "end": v(19, 222) * mm});
            skLineSegment(sketch, "E12.8.31.1", {"start": v(19, 222) * mm, "end": v(19, 212) * mm});
            skLineSegment(sketch, "E12.8.31.2", {"start": v(9, 212) * mm, "end": v(19, 212) * mm});
            skLineSegment(sketch, "E12.8.31.3", {"start": v(9, 222) * mm, "end": v(9, 212) * mm});
            skLineSegment(sketch, "E12.9.0.0", {"start": v(23, -212) * mm, "end": v(33, -212) * mm});
            skLineSegment(sketch, "E12.9.0.1", {"start": v(33, -212) * mm, "end": v(33, -222) * mm});
            skLineSegment(sketch, "E12.9.0.2", {"start": v(23, -222) * mm, "end": v(33, -222) * mm});
            skLineSegment(sketch, "E12.9.0.3", {"start": v(23, -212) * mm, "end": v(23, -222) * mm});
            skLineSegment(sketch, "E12.9.1.0", {"start": v(23, -198) * mm, "end": v(33, -198) * mm});
            skLineSegment(sketch, "E12.9.1.1", {"start": v(33, -198) * mm, "end": v(33, -208) * mm});
            skLineSegment(sketch, "E12.9.1.2", {"start": v(23, -208) * mm, "end": v(33, -208) * mm});
            skLineSegment(sketch, "E12.9.1.3", {"start": v(23, -198) * mm, "end": v(23, -208) * mm});
            skLineSegment(sketch, "E12.9.2.0", {"start": v(23, -184) * mm, "end": v(33, -184) * mm});
            skLineSegment(sketch, "E12.9.2.1", {"start": v(33, -184) * mm, "end": v(33, -194) * mm});
            skLineSegment(sketch, "E12.9.2.2", {"start": v(23, -194) * mm, "end": v(33, -194) * mm});
            skLineSegment(sketch, "E12.9.2.3", {"start": v(23, -184) * mm, "end": v(23, -194) * mm});
            skLineSegment(sketch, "E12.9.3.0", {"start": v(23, -170) * mm, "end": v(33, -170) * mm});
            skLineSegment(sketch, "E12.9.3.1", {"start": v(33, -170) * mm, "end": v(33, -180) * mm});
            skLineSegment(sketch, "E12.9.3.2", {"start": v(23, -180) * mm, "end": v(33, -180) * mm});
            skLineSegment(sketch, "E12.9.3.3", {"start": v(23, -170) * mm, "end": v(23, -180) * mm});
            skLineSegment(sketch, "E12.9.4.0", {"start": v(23, -156) * mm, "end": v(33, -156) * mm});
            skLineSegment(sketch, "E12.9.4.1", {"start": v(33, -156) * mm, "end": v(33, -166) * mm});
            skLineSegment(sketch, "E12.9.4.2", {"start": v(23, -166) * mm, "end": v(33, -166) * mm});
            skLineSegment(sketch, "E12.9.4.3", {"start": v(23, -156) * mm, "end": v(23, -166) * mm});
            skLineSegment(sketch, "E12.9.5.0", {"start": v(23, -142) * mm, "end": v(33, -142) * mm});
            skLineSegment(sketch, "E12.9.5.1", {"start": v(33, -142) * mm, "end": v(33, -152) * mm});
            skLineSegment(sketch, "E12.9.5.2", {"start": v(23, -152) * mm, "end": v(33, -152) * mm});
            skLineSegment(sketch, "E12.9.5.3", {"start": v(23, -142) * mm, "end": v(23, -152) * mm});
            skLineSegment(sketch, "E12.9.6.0", {"start": v(23, -128) * mm, "end": v(33, -128) * mm});
            skLineSegment(sketch, "E12.9.6.1", {"start": v(33, -128) * mm, "end": v(33, -138) * mm});
            skLineSegment(sketch, "E12.9.6.2", {"start": v(23, -138) * mm, "end": v(33, -138) * mm});
            skLineSegment(sketch, "E12.9.6.3", {"start": v(23, -128) * mm, "end": v(23, -138) * mm});
            skLineSegment(sketch, "E12.9.7.0", {"start": v(23, -114) * mm, "end": v(33, -114) * mm});
            skLineSegment(sketch, "E12.9.7.1", {"start": v(33, -114) * mm, "end": v(33, -124) * mm});
            skLineSegment(sketch, "E12.9.7.2", {"start": v(23, -124) * mm, "end": v(33, -124) * mm});
            skLineSegment(sketch, "E12.9.7.3", {"start": v(23, -114) * mm, "end": v(23, -124) * mm});
            skLineSegment(sketch, "E12.9.8.0", {"start": v(23, -100) * mm, "end": v(33, -100) * mm});
            skLineSegment(sketch, "E12.9.8.1", {"start": v(33, -100) * mm, "end": v(33, -110) * mm});
            skLineSegment(sketch, "E12.9.8.2", {"start": v(23, -110) * mm, "end": v(33, -110) * mm});
            skLineSegment(sketch, "E12.9.8.3", {"start": v(23, -100) * mm, "end": v(23, -110) * mm});
            skLineSegment(sketch, "E12.9.9.0", {"start": v(23, -86) * mm, "end": v(33, -86) * mm});
            skLineSegment(sketch, "E12.9.9.1", {"start": v(33, -86) * mm, "end": v(33, -96) * mm});
            skLineSegment(sketch, "E12.9.9.2", {"start": v(23, -96) * mm, "end": v(33, -96) * mm});
            skLineSegment(sketch, "E12.9.9.3", {"start": v(23, -86) * mm, "end": v(23, -96) * mm});
            skLineSegment(sketch, "E12.9.10.0", {"start": v(23, -72) * mm, "end": v(33, -72) * mm});
            skLineSegment(sketch, "E12.9.10.1", {"start": v(33, -72) * mm, "end": v(33, -82) * mm});
            skLineSegment(sketch, "E12.9.10.2", {"start": v(23, -82) * mm, "end": v(33, -82) * mm});
            skLineSegment(sketch, "E12.9.10.3", {"start": v(23, -72) * mm, "end": v(23, -82) * mm});
            skLineSegment(sketch, "E12.9.11.0", {"start": v(23, -58) * mm, "end": v(33, -58) * mm});
            skLineSegment(sketch, "E12.9.11.1", {"start": v(33, -58) * mm, "end": v(33, -68) * mm});
            skLineSegment(sketch, "E12.9.11.2", {"start": v(23, -68) * mm, "end": v(33, -68) * mm});
            skLineSegment(sketch, "E12.9.11.3", {"start": v(23, -58) * mm, "end": v(23, -68) * mm});
            skLineSegment(sketch, "E12.9.12.0", {"start": v(23, -44) * mm, "end": v(33, -44) * mm});
            skLineSegment(sketch, "E12.9.12.1", {"start": v(33, -44) * mm, "end": v(33, -54) * mm});
            skLineSegment(sketch, "E12.9.12.2", {"start": v(23, -54) * mm, "end": v(33, -54) * mm});
            skLineSegment(sketch, "E12.9.12.3", {"start": v(23, -44) * mm, "end": v(23, -54) * mm});
            skLineSegment(sketch, "E12.9.13.0", {"start": v(23, -30) * mm, "end": v(33, -30) * mm});
            skLineSegment(sketch, "E12.9.13.1", {"start": v(33, -30) * mm, "end": v(33, -40) * mm});
            skLineSegment(sketch, "E12.9.13.2", {"start": v(23, -40) * mm, "end": v(33, -40) * mm});
            skLineSegment(sketch, "E12.9.13.3", {"start": v(23, -30) * mm, "end": v(23, -40) * mm});
            skLineSegment(sketch, "E12.9.14.0", {"start": v(23, -16) * mm, "end": v(33, -16) * mm});
            skLineSegment(sketch, "E12.9.14.1", {"start": v(33, -16) * mm, "end": v(33, -26) * mm});
            skLineSegment(sketch, "E12.9.14.2", {"start": v(23, -26) * mm, "end": v(33, -26) * mm});
            skLineSegment(sketch, "E12.9.14.3", {"start": v(23, -16) * mm, "end": v(23, -26) * mm});
            skLineSegment(sketch, "E12.9.15.0", {"start": v(23, -2) * mm, "end": v(33, -2) * mm});
            skLineSegment(sketch, "E12.9.15.1", {"start": v(33, -2) * mm, "end": v(33, -12) * mm});
            skLineSegment(sketch, "E12.9.15.2", {"start": v(23, -12) * mm, "end": v(33, -12) * mm});
            skLineSegment(sketch, "E12.9.15.3", {"start": v(23, -2) * mm, "end": v(23, -12) * mm});
            skLineSegment(sketch, "E12.9.16.0", {"start": v(23, 12) * mm, "end": v(33, 12) * mm});
            skLineSegment(sketch, "E12.9.16.1", {"start": v(33, 12) * mm, "end": v(33, 2) * mm});
            skLineSegment(sketch, "E12.9.16.2", {"start": v(23, 2) * mm, "end": v(33, 2) * mm});
            skLineSegment(sketch, "E12.9.16.3", {"start": v(23, 12) * mm, "end": v(23, 2) * mm});
            skLineSegment(sketch, "E12.9.17.0", {"start": v(23, 26) * mm, "end": v(33, 26) * mm});
            skLineSegment(sketch, "E12.9.17.1", {"start": v(33, 26) * mm, "end": v(33, 16) * mm});
            skLineSegment(sketch, "E12.9.17.2", {"start": v(23, 16) * mm, "end": v(33, 16) * mm});
            skLineSegment(sketch, "E12.9.17.3", {"start": v(23, 26) * mm, "end": v(23, 16) * mm});
            skLineSegment(sketch, "E12.9.18.0", {"start": v(23, 40) * mm, "end": v(33, 40) * mm});
            skLineSegment(sketch, "E12.9.18.1", {"start": v(33, 40) * mm, "end": v(33, 30) * mm});
            skLineSegment(sketch, "E12.9.18.2", {"start": v(23, 30) * mm, "end": v(33, 30) * mm});
            skLineSegment(sketch, "E12.9.18.3", {"start": v(23, 40) * mm, "end": v(23, 30) * mm});
            skLineSegment(sketch, "E12.9.19.0", {"start": v(23, 54) * mm, "end": v(33, 54) * mm});
            skLineSegment(sketch, "E12.9.19.1", {"start": v(33, 54) * mm, "end": v(33, 44) * mm});
            skLineSegment(sketch, "E12.9.19.2", {"start": v(23, 44) * mm, "end": v(33, 44) * mm});
            skLineSegment(sketch, "E12.9.19.3", {"start": v(23, 54) * mm, "end": v(23, 44) * mm});
            skLineSegment(sketch, "E12.9.20.0", {"start": v(23, 68) * mm, "end": v(33, 68) * mm});
            skLineSegment(sketch, "E12.9.20.1", {"start": v(33, 68) * mm, "end": v(33, 58) * mm});
            skLineSegment(sketch, "E12.9.20.2", {"start": v(23, 58) * mm, "end": v(33, 58) * mm});
            skLineSegment(sketch, "E12.9.20.3", {"start": v(23, 68) * mm, "end": v(23, 58) * mm});
            skLineSegment(sketch, "E12.9.21.0", {"start": v(23, 82) * mm, "end": v(33, 82) * mm});
            skLineSegment(sketch, "E12.9.21.1", {"start": v(33, 82) * mm, "end": v(33, 72) * mm});
            skLineSegment(sketch, "E12.9.21.2", {"start": v(23, 72) * mm, "end": v(33, 72) * mm});
            skLineSegment(sketch, "E12.9.21.3", {"start": v(23, 82) * mm, "end": v(23, 72) * mm});
            skLineSegment(sketch, "E12.9.22.0", {"start": v(23, 96) * mm, "end": v(33, 96) * mm});
            skLineSegment(sketch, "E12.9.22.1", {"start": v(33, 96) * mm, "end": v(33, 86) * mm});
            skLineSegment(sketch, "E12.9.22.2", {"start": v(23, 86) * mm, "end": v(33, 86) * mm});
            skLineSegment(sketch, "E12.9.22.3", {"start": v(23, 96) * mm, "end": v(23, 86) * mm});
            skLineSegment(sketch, "E12.9.23.0", {"start": v(23, 110) * mm, "end": v(33, 110) * mm});
            skLineSegment(sketch, "E12.9.23.1", {"start": v(33, 110) * mm, "end": v(33, 100) * mm});
            skLineSegment(sketch, "E12.9.23.2", {"start": v(23, 100) * mm, "end": v(33, 100) * mm});
            skLineSegment(sketch, "E12.9.23.3", {"start": v(23, 110) * mm, "end": v(23, 100) * mm});
            skLineSegment(sketch, "E12.9.24.0", {"start": v(23, 124) * mm, "end": v(33, 124) * mm});
            skLineSegment(sketch, "E12.9.24.1", {"start": v(33, 124) * mm, "end": v(33, 114) * mm});
            skLineSegment(sketch, "E12.9.24.2", {"start": v(23, 114) * mm, "end": v(33, 114) * mm});
            skLineSegment(sketch, "E12.9.24.3", {"start": v(23, 124) * mm, "end": v(23, 114) * mm});
            skLineSegment(sketch, "E12.9.25.0", {"start": v(23, 138) * mm, "end": v(33, 138) * mm});
            skLineSegment(sketch, "E12.9.25.1", {"start": v(33, 138) * mm, "end": v(33, 128) * mm});
            skLineSegment(sketch, "E12.9.25.2", {"start": v(23, 128) * mm, "end": v(33, 128) * mm});
            skLineSegment(sketch, "E12.9.25.3", {"start": v(23, 138) * mm, "end": v(23, 128) * mm});
            skLineSegment(sketch, "E12.9.26.0", {"start": v(23, 152) * mm, "end": v(33, 152) * mm});
            skLineSegment(sketch, "E12.9.26.1", {"start": v(33, 152) * mm, "end": v(33, 142) * mm});
            skLineSegment(sketch, "E12.9.26.2", {"start": v(23, 142) * mm, "end": v(33, 142) * mm});
            skLineSegment(sketch, "E12.9.26.3", {"start": v(23, 152) * mm, "end": v(23, 142) * mm});
            skLineSegment(sketch, "E12.9.27.0", {"start": v(23, 166) * mm, "end": v(33, 166) * mm});
            skLineSegment(sketch, "E12.9.27.1", {"start": v(33, 166) * mm, "end": v(33, 156) * mm});
            skLineSegment(sketch, "E12.9.27.2", {"start": v(23, 156) * mm, "end": v(33, 156) * mm});
            skLineSegment(sketch, "E12.9.27.3", {"start": v(23, 166) * mm, "end": v(23, 156) * mm});
            skLineSegment(sketch, "E12.9.28.0", {"start": v(23, 180) * mm, "end": v(33, 180) * mm});
            skLineSegment(sketch, "E12.9.28.1", {"start": v(33, 180) * mm, "end": v(33, 170) * mm});
            skLineSegment(sketch, "E12.9.28.2", {"start": v(23, 170) * mm, "end": v(33, 170) * mm});
            skLineSegment(sketch, "E12.9.28.3", {"start": v(23, 180) * mm, "end": v(23, 170) * mm});
            skLineSegment(sketch, "E12.9.29.0", {"start": v(23, 194) * mm, "end": v(33, 194) * mm});
            skLineSegment(sketch, "E12.9.29.1", {"start": v(33, 194) * mm, "end": v(33, 184) * mm});
            skLineSegment(sketch, "E12.9.29.2", {"start": v(23, 184) * mm, "end": v(33, 184) * mm});
            skLineSegment(sketch, "E12.9.29.3", {"start": v(23, 194) * mm, "end": v(23, 184) * mm});
            skLineSegment(sketch, "E12.9.30.0", {"start": v(23, 208) * mm, "end": v(33, 208) * mm});
            skLineSegment(sketch, "E12.9.30.1", {"start": v(33, 208) * mm, "end": v(33, 198) * mm});
            skLineSegment(sketch, "E12.9.30.2", {"start": v(23, 198) * mm, "end": v(33, 198) * mm});
            skLineSegment(sketch, "E12.9.30.3", {"start": v(23, 208) * mm, "end": v(23, 198) * mm});
            skLineSegment(sketch, "E12.9.31.0", {"start": v(23, 222) * mm, "end": v(33, 222) * mm});
            skLineSegment(sketch, "E12.9.31.1", {"start": v(33, 222) * mm, "end": v(33, 212) * mm});
            skLineSegment(sketch, "E12.9.31.2", {"start": v(23, 212) * mm, "end": v(33, 212) * mm});
            skLineSegment(sketch, "E12.9.31.3", {"start": v(23, 222) * mm, "end": v(23, 212) * mm});
            skLineSegment(sketch, "E12.10.0.0", {"start": v(37, -212) * mm, "end": v(47, -212) * mm});
            skLineSegment(sketch, "E12.10.0.1", {"start": v(47, -212) * mm, "end": v(47, -222) * mm});
            skLineSegment(sketch, "E12.10.0.2", {"start": v(37, -222) * mm, "end": v(47, -222) * mm});
            skLineSegment(sketch, "E12.10.0.3", {"start": v(37, -212) * mm, "end": v(37, -222) * mm});
            skLineSegment(sketch, "E12.10.1.0", {"start": v(37, -198) * mm, "end": v(47, -198) * mm});
            skLineSegment(sketch, "E12.10.1.1", {"start": v(47, -198) * mm, "end": v(47, -208) * mm});
            skLineSegment(sketch, "E12.10.1.2", {"start": v(37, -208) * mm, "end": v(47, -208) * mm});
            skLineSegment(sketch, "E12.10.1.3", {"start": v(37, -198) * mm, "end": v(37, -208) * mm});
            skLineSegment(sketch, "E12.10.2.0", {"start": v(37, -184) * mm, "end": v(47, -184) * mm});
            skLineSegment(sketch, "E12.10.2.1", {"start": v(47, -184) * mm, "end": v(47, -194) * mm});
            skLineSegment(sketch, "E12.10.2.2", {"start": v(37, -194) * mm, "end": v(47, -194) * mm});
            skLineSegment(sketch, "E12.10.2.3", {"start": v(37, -184) * mm, "end": v(37, -194) * mm});
            skLineSegment(sketch, "E12.10.3.0", {"start": v(37, -170) * mm, "end": v(47, -170) * mm});
            skLineSegment(sketch, "E12.10.3.1", {"start": v(47, -170) * mm, "end": v(47, -180) * mm});
            skLineSegment(sketch, "E12.10.3.2", {"start": v(37, -180) * mm, "end": v(47, -180) * mm});
            skLineSegment(sketch, "E12.10.3.3", {"start": v(37, -170) * mm, "end": v(37, -180) * mm});
            skLineSegment(sketch, "E12.10.4.0", {"start": v(37, -156) * mm, "end": v(47, -156) * mm});
            skLineSegment(sketch, "E12.10.4.1", {"start": v(47, -156) * mm, "end": v(47, -166) * mm});
            skLineSegment(sketch, "E12.10.4.2", {"start": v(37, -166) * mm, "end": v(47, -166) * mm});
            skLineSegment(sketch, "E12.10.4.3", {"start": v(37, -156) * mm, "end": v(37, -166) * mm});
            skLineSegment(sketch, "E12.10.5.0", {"start": v(37, -142) * mm, "end": v(47, -142) * mm});
            skLineSegment(sketch, "E12.10.5.1", {"start": v(47, -142) * mm, "end": v(47, -152) * mm});
            skLineSegment(sketch, "E12.10.5.2", {"start": v(37, -152) * mm, "end": v(47, -152) * mm});
            skLineSegment(sketch, "E12.10.5.3", {"start": v(37, -142) * mm, "end": v(37, -152) * mm});
            skLineSegment(sketch, "E12.10.6.0", {"start": v(37, -128) * mm, "end": v(47, -128) * mm});
            skLineSegment(sketch, "E12.10.6.1", {"start": v(47, -128) * mm, "end": v(47, -138) * mm});
            skLineSegment(sketch, "E12.10.6.2", {"start": v(37, -138) * mm, "end": v(47, -138) * mm});
            skLineSegment(sketch, "E12.10.6.3", {"start": v(37, -128) * mm, "end": v(37, -138) * mm});
            skLineSegment(sketch, "E12.10.7.0", {"start": v(37, -114) * mm, "end": v(47, -114) * mm});
            skLineSegment(sketch, "E12.10.7.1", {"start": v(47, -114) * mm, "end": v(47, -124) * mm});
            skLineSegment(sketch, "E12.10.7.2", {"start": v(37, -124) * mm, "end": v(47, -124) * mm});
            skLineSegment(sketch, "E12.10.7.3", {"start": v(37, -114) * mm, "end": v(37, -124) * mm});
            skLineSegment(sketch, "E12.10.8.0", {"start": v(37, -100) * mm, "end": v(47, -100) * mm});
            skLineSegment(sketch, "E12.10.8.1", {"start": v(47, -100) * mm, "end": v(47, -110) * mm});
            skLineSegment(sketch, "E12.10.8.2", {"start": v(37, -110) * mm, "end": v(47, -110) * mm});
            skLineSegment(sketch, "E12.10.8.3", {"start": v(37, -100) * mm, "end": v(37, -110) * mm});
            skLineSegment(sketch, "E12.10.9.0", {"start": v(37, -86) * mm, "end": v(47, -86) * mm});
            skLineSegment(sketch, "E12.10.9.1", {"start": v(47, -86) * mm, "end": v(47, -96) * mm});
            skLineSegment(sketch, "E12.10.9.2", {"start": v(37, -96) * mm, "end": v(47, -96) * mm});
            skLineSegment(sketch, "E12.10.9.3", {"start": v(37, -86) * mm, "end": v(37, -96) * mm});
            skLineSegment(sketch, "E12.10.10.0", {"start": v(37, -72) * mm, "end": v(47, -72) * mm});
            skLineSegment(sketch, "E12.10.10.1", {"start": v(47, -72) * mm, "end": v(47, -82) * mm});
            skLineSegment(sketch, "E12.10.10.2", {"start": v(37, -82) * mm, "end": v(47, -82) * mm});
            skLineSegment(sketch, "E12.10.10.3", {"start": v(37, -72) * mm, "end": v(37, -82) * mm});
            skLineSegment(sketch, "E12.10.11.0", {"start": v(37, -58) * mm, "end": v(47, -58) * mm});
            skLineSegment(sketch, "E12.10.11.1", {"start": v(47, -58) * mm, "end": v(47, -68) * mm});
            skLineSegment(sketch, "E12.10.11.2", {"start": v(37, -68) * mm, "end": v(47, -68) * mm});
            skLineSegment(sketch, "E12.10.11.3", {"start": v(37, -58) * mm, "end": v(37, -68) * mm});
            skLineSegment(sketch, "E12.10.12.0", {"start": v(37, -44) * mm, "end": v(47, -44) * mm});
            skLineSegment(sketch, "E12.10.12.1", {"start": v(47, -44) * mm, "end": v(47, -54) * mm});
            skLineSegment(sketch, "E12.10.12.2", {"start": v(37, -54) * mm, "end": v(47, -54) * mm});
            skLineSegment(sketch, "E12.10.12.3", {"start": v(37, -44) * mm, "end": v(37, -54) * mm});
            skLineSegment(sketch, "E12.10.13.0", {"start": v(37, -30) * mm, "end": v(47, -30) * mm});
            skLineSegment(sketch, "E12.10.13.1", {"start": v(47, -30) * mm, "end": v(47, -40) * mm});
            skLineSegment(sketch, "E12.10.13.2", {"start": v(37, -40) * mm, "end": v(47, -40) * mm});
            skLineSegment(sketch, "E12.10.13.3", {"start": v(37, -30) * mm, "end": v(37, -40) * mm});
            skLineSegment(sketch, "E12.10.14.0", {"start": v(37, -16) * mm, "end": v(47, -16) * mm});
            skLineSegment(sketch, "E12.10.14.1", {"start": v(47, -16) * mm, "end": v(47, -26) * mm});
            skLineSegment(sketch, "E12.10.14.2", {"start": v(37, -26) * mm, "end": v(47, -26) * mm});
            skLineSegment(sketch, "E12.10.14.3", {"start": v(37, -16) * mm, "end": v(37, -26) * mm});
            skLineSegment(sketch, "E12.10.15.0", {"start": v(37, -2) * mm, "end": v(47, -2) * mm});
            skLineSegment(sketch, "E12.10.15.1", {"start": v(47, -2) * mm, "end": v(47, -12) * mm});
            skLineSegment(sketch, "E12.10.15.2", {"start": v(37, -12) * mm, "end": v(47, -12) * mm});
            skLineSegment(sketch, "E12.10.15.3", {"start": v(37, -2) * mm, "end": v(37, -12) * mm});
            skLineSegment(sketch, "E12.10.16.0", {"start": v(37, 12) * mm, "end": v(47, 12) * mm});
            skLineSegment(sketch, "E12.10.16.1", {"start": v(47, 12) * mm, "end": v(47, 2) * mm});
            skLineSegment(sketch, "E12.10.16.2", {"start": v(37, 2) * mm, "end": v(47, 2) * mm});
            skLineSegment(sketch, "E12.10.16.3", {"start": v(37, 12) * mm, "end": v(37, 2) * mm});
            skLineSegment(sketch, "E12.10.17.0", {"start": v(37, 26) * mm, "end": v(47, 26) * mm});
            skLineSegment(sketch, "E12.10.17.1", {"start": v(47, 26) * mm, "end": v(47, 16) * mm});
            skLineSegment(sketch, "E12.10.17.2", {"start": v(37, 16) * mm, "end": v(47, 16) * mm});
            skLineSegment(sketch, "E12.10.17.3", {"start": v(37, 26) * mm, "end": v(37, 16) * mm});
            skLineSegment(sketch, "E12.10.18.0", {"start": v(37, 40) * mm, "end": v(47, 40) * mm});
            skLineSegment(sketch, "E12.10.18.1", {"start": v(47, 40) * mm, "end": v(47, 30) * mm});
            skLineSegment(sketch, "E12.10.18.2", {"start": v(37, 30) * mm, "end": v(47, 30) * mm});
            skLineSegment(sketch, "E12.10.18.3", {"start": v(37, 40) * mm, "end": v(37, 30) * mm});
            skLineSegment(sketch, "E12.10.19.0", {"start": v(37, 54) * mm, "end": v(47, 54) * mm});
            skLineSegment(sketch, "E12.10.19.1", {"start": v(47, 54) * mm, "end": v(47, 44) * mm});
            skLineSegment(sketch, "E12.10.19.2", {"start": v(37, 44) * mm, "end": v(47, 44) * mm});
            skLineSegment(sketch, "E12.10.19.3", {"start": v(37, 54) * mm, "end": v(37, 44) * mm});
            skLineSegment(sketch, "E12.10.20.0", {"start": v(37, 68) * mm, "end": v(47, 68) * mm});
            skLineSegment(sketch, "E12.10.20.1", {"start": v(47, 68) * mm, "end": v(47, 58) * mm});
            skLineSegment(sketch, "E12.10.20.2", {"start": v(37, 58) * mm, "end": v(47, 58) * mm});
            skLineSegment(sketch, "E12.10.20.3", {"start": v(37, 68) * mm, "end": v(37, 58) * mm});
            skLineSegment(sketch, "E12.10.21.0", {"start": v(37, 82) * mm, "end": v(47, 82) * mm});
            skLineSegment(sketch, "E12.10.21.1", {"start": v(47, 82) * mm, "end": v(47, 72) * mm});
            skLineSegment(sketch, "E12.10.21.2", {"start": v(37, 72) * mm, "end": v(47, 72) * mm});
            skLineSegment(sketch, "E12.10.21.3", {"start": v(37, 82) * mm, "end": v(37, 72) * mm});
            skLineSegment(sketch, "E12.10.22.0", {"start": v(37, 96) * mm, "end": v(47, 96) * mm});
            skLineSegment(sketch, "E12.10.22.1", {"start": v(47, 96) * mm, "end": v(47, 86) * mm});
            skLineSegment(sketch, "E12.10.22.2", {"start": v(37, 86) * mm, "end": v(47, 86) * mm});
            skLineSegment(sketch, "E12.10.22.3", {"start": v(37, 96) * mm, "end": v(37, 86) * mm});
            skLineSegment(sketch, "E12.10.23.0", {"start": v(37, 110) * mm, "end": v(47, 110) * mm});
            skLineSegment(sketch, "E12.10.23.1", {"start": v(47, 110) * mm, "end": v(47, 100) * mm});
            skLineSegment(sketch, "E12.10.23.2", {"start": v(37, 100) * mm, "end": v(47, 100) * mm});
            skLineSegment(sketch, "E12.10.23.3", {"start": v(37, 110) * mm, "end": v(37, 100) * mm});
            skLineSegment(sketch, "E12.10.24.0", {"start": v(37, 124) * mm, "end": v(47, 124) * mm});
            skLineSegment(sketch, "E12.10.24.1", {"start": v(47, 124) * mm, "end": v(47, 114) * mm});
            skLineSegment(sketch, "E12.10.24.2", {"start": v(37, 114) * mm, "end": v(47, 114) * mm});
            skLineSegment(sketch, "E12.10.24.3", {"start": v(37, 124) * mm, "end": v(37, 114) * mm});
            skLineSegment(sketch, "E12.10.25.0", {"start": v(37, 138) * mm, "end": v(47, 138) * mm});
            skLineSegment(sketch, "E12.10.25.1", {"start": v(47, 138) * mm, "end": v(47, 128) * mm});
            skLineSegment(sketch, "E12.10.25.2", {"start": v(37, 128) * mm, "end": v(47, 128) * mm});
            skLineSegment(sketch, "E12.10.25.3", {"start": v(37, 138) * mm, "end": v(37, 128) * mm});
            skLineSegment(sketch, "E12.10.26.0", {"start": v(37, 152) * mm, "end": v(47, 152) * mm});
            skLineSegment(sketch, "E12.10.26.1", {"start": v(47, 152) * mm, "end": v(47, 142) * mm});
            skLineSegment(sketch, "E12.10.26.2", {"start": v(37, 142) * mm, "end": v(47, 142) * mm});
            skLineSegment(sketch, "E12.10.26.3", {"start": v(37, 152) * mm, "end": v(37, 142) * mm});
            skLineSegment(sketch, "E12.10.27.0", {"start": v(37, 166) * mm, "end": v(47, 166) * mm});
            skLineSegment(sketch, "E12.10.27.1", {"start": v(47, 166) * mm, "end": v(47, 156) * mm});
            skLineSegment(sketch, "E12.10.27.2", {"start": v(37, 156) * mm, "end": v(47, 156) * mm});
            skLineSegment(sketch, "E12.10.27.3", {"start": v(37, 166) * mm, "end": v(37, 156) * mm});
            skLineSegment(sketch, "E12.10.28.0", {"start": v(37, 180) * mm, "end": v(47, 180) * mm});
            skLineSegment(sketch, "E12.10.28.1", {"start": v(47, 180) * mm, "end": v(47, 170) * mm});
            skLineSegment(sketch, "E12.10.28.2", {"start": v(37, 170) * mm, "end": v(47, 170) * mm});
            skLineSegment(sketch, "E12.10.28.3", {"start": v(37, 180) * mm, "end": v(37, 170) * mm});
            skLineSegment(sketch, "E12.10.29.0", {"start": v(37, 194) * mm, "end": v(47, 194) * mm});
            skLineSegment(sketch, "E12.10.29.1", {"start": v(47, 194) * mm, "end": v(47, 184) * mm});
            skLineSegment(sketch, "E12.10.29.2", {"start": v(37, 184) * mm, "end": v(47, 184) * mm});
            skLineSegment(sketch, "E12.10.29.3", {"start": v(37, 194) * mm, "end": v(37, 184) * mm});
            skLineSegment(sketch, "E12.10.30.0", {"start": v(37, 208) * mm, "end": v(47, 208) * mm});
            skLineSegment(sketch, "E12.10.30.1", {"start": v(47, 208) * mm, "end": v(47, 198) * mm});
            skLineSegment(sketch, "E12.10.30.2", {"start": v(37, 198) * mm, "end": v(47, 198) * mm});
            skLineSegment(sketch, "E12.10.30.3", {"start": v(37, 208) * mm, "end": v(37, 198) * mm});
            skLineSegment(sketch, "E12.10.31.0", {"start": v(37, 222) * mm, "end": v(47, 222) * mm});
            skLineSegment(sketch, "E12.10.31.1", {"start": v(47, 222) * mm, "end": v(47, 212) * mm});
            skLineSegment(sketch, "E12.10.31.2", {"start": v(37, 212) * mm, "end": v(47, 212) * mm});
            skLineSegment(sketch, "E12.10.31.3", {"start": v(37, 222) * mm, "end": v(37, 212) * mm});
            skLineSegment(sketch, "E12.11.0.0", {"start": v(51, -212) * mm, "end": v(61, -212) * mm});
            skLineSegment(sketch, "E12.11.0.1", {"start": v(61, -212) * mm, "end": v(61, -222) * mm});
            skLineSegment(sketch, "E12.11.0.2", {"start": v(51, -222) * mm, "end": v(61, -222) * mm});
            skLineSegment(sketch, "E12.11.0.3", {"start": v(51, -212) * mm, "end": v(51, -222) * mm});
            skLineSegment(sketch, "E12.11.1.0", {"start": v(51, -198) * mm, "end": v(61, -198) * mm});
            skLineSegment(sketch, "E12.11.1.1", {"start": v(61, -198) * mm, "end": v(61, -208) * mm});
            skLineSegment(sketch, "E12.11.1.2", {"start": v(51, -208) * mm, "end": v(61, -208) * mm});
            skLineSegment(sketch, "E12.11.1.3", {"start": v(51, -198) * mm, "end": v(51, -208) * mm});
            skLineSegment(sketch, "E12.11.2.0", {"start": v(51, -184) * mm, "end": v(61, -184) * mm});
            skLineSegment(sketch, "E12.11.2.1", {"start": v(61, -184) * mm, "end": v(61, -194) * mm});
            skLineSegment(sketch, "E12.11.2.2", {"start": v(51, -194) * mm, "end": v(61, -194) * mm});
            skLineSegment(sketch, "E12.11.2.3", {"start": v(51, -184) * mm, "end": v(51, -194) * mm});
            skLineSegment(sketch, "E12.11.3.0", {"start": v(51, -170) * mm, "end": v(61, -170) * mm});
            skLineSegment(sketch, "E12.11.3.1", {"start": v(61, -170) * mm, "end": v(61, -180) * mm});
            skLineSegment(sketch, "E12.11.3.2", {"start": v(51, -180) * mm, "end": v(61, -180) * mm});
            skLineSegment(sketch, "E12.11.3.3", {"start": v(51, -170) * mm, "end": v(51, -180) * mm});
            skLineSegment(sketch, "E12.11.4.0", {"start": v(51, -156) * mm, "end": v(61, -156) * mm});
            skLineSegment(sketch, "E12.11.4.1", {"start": v(61, -156) * mm, "end": v(61, -166) * mm});
            skLineSegment(sketch, "E12.11.4.2", {"start": v(51, -166) * mm, "end": v(61, -166) * mm});
            skLineSegment(sketch, "E12.11.4.3", {"start": v(51, -156) * mm, "end": v(51, -166) * mm});
            skLineSegment(sketch, "E12.11.5.0", {"start": v(51, -142) * mm, "end": v(61, -142) * mm});
            skLineSegment(sketch, "E12.11.5.1", {"start": v(61, -142) * mm, "end": v(61, -152) * mm});
            skLineSegment(sketch, "E12.11.5.2", {"start": v(51, -152) * mm, "end": v(61, -152) * mm});
            skLineSegment(sketch, "E12.11.5.3", {"start": v(51, -142) * mm, "end": v(51, -152) * mm});
            skLineSegment(sketch, "E12.11.6.0", {"start": v(51, -128) * mm, "end": v(61, -128) * mm});
            skLineSegment(sketch, "E12.11.6.1", {"start": v(61, -128) * mm, "end": v(61, -138) * mm});
            skLineSegment(sketch, "E12.11.6.2", {"start": v(51, -138) * mm, "end": v(61, -138) * mm});
            skLineSegment(sketch, "E12.11.6.3", {"start": v(51, -128) * mm, "end": v(51, -138) * mm});
            skLineSegment(sketch, "E12.11.7.0", {"start": v(51, -114) * mm, "end": v(61, -114) * mm});
            skLineSegment(sketch, "E12.11.7.1", {"start": v(61, -114) * mm, "end": v(61, -124) * mm});
            skLineSegment(sketch, "E12.11.7.2", {"start": v(51, -124) * mm, "end": v(61, -124) * mm});
            skLineSegment(sketch, "E12.11.7.3", {"start": v(51, -114) * mm, "end": v(51, -124) * mm});
            skLineSegment(sketch, "E12.11.8.0", {"start": v(51, -100) * mm, "end": v(61, -100) * mm});
            skLineSegment(sketch, "E12.11.8.1", {"start": v(61, -100) * mm, "end": v(61, -110) * mm});
            skLineSegment(sketch, "E12.11.8.2", {"start": v(51, -110) * mm, "end": v(61, -110) * mm});
            skLineSegment(sketch, "E12.11.8.3", {"start": v(51, -100) * mm, "end": v(51, -110) * mm});
            skLineSegment(sketch, "E12.11.9.0", {"start": v(51, -86) * mm, "end": v(61, -86) * mm});
            skLineSegment(sketch, "E12.11.9.1", {"start": v(61, -86) * mm, "end": v(61, -96) * mm});
            skLineSegment(sketch, "E12.11.9.2", {"start": v(51, -96) * mm, "end": v(61, -96) * mm});
            skLineSegment(sketch, "E12.11.9.3", {"start": v(51, -86) * mm, "end": v(51, -96) * mm});
            skLineSegment(sketch, "E12.11.10.0", {"start": v(51, -72) * mm, "end": v(61, -72) * mm});
            skLineSegment(sketch, "E12.11.10.1", {"start": v(61, -72) * mm, "end": v(61, -82) * mm});
            skLineSegment(sketch, "E12.11.10.2", {"start": v(51, -82) * mm, "end": v(61, -82) * mm});
            skLineSegment(sketch, "E12.11.10.3", {"start": v(51, -72) * mm, "end": v(51, -82) * mm});
            skLineSegment(sketch, "E12.11.11.0", {"start": v(51, -58) * mm, "end": v(61, -58) * mm});
            skLineSegment(sketch, "E12.11.11.1", {"start": v(61, -58) * mm, "end": v(61, -68) * mm});
            skLineSegment(sketch, "E12.11.11.2", {"start": v(51, -68) * mm, "end": v(61, -68) * mm});
            skLineSegment(sketch, "E12.11.11.3", {"start": v(51, -58) * mm, "end": v(51, -68) * mm});
            skLineSegment(sketch, "E12.11.12.0", {"start": v(51, -44) * mm, "end": v(61, -44) * mm});
            skLineSegment(sketch, "E12.11.12.1", {"start": v(61, -44) * mm, "end": v(61, -54) * mm});
            skLineSegment(sketch, "E12.11.12.2", {"start": v(51, -54) * mm, "end": v(61, -54) * mm});
            skLineSegment(sketch, "E12.11.12.3", {"start": v(51, -44) * mm, "end": v(51, -54) * mm});
            skLineSegment(sketch, "E12.11.13.0", {"start": v(51, -30) * mm, "end": v(61, -30) * mm});
            skLineSegment(sketch, "E12.11.13.1", {"start": v(61, -30) * mm, "end": v(61, -40) * mm});
            skLineSegment(sketch, "E12.11.13.2", {"start": v(51, -40) * mm, "end": v(61, -40) * mm});
            skLineSegment(sketch, "E12.11.13.3", {"start": v(51, -30) * mm, "end": v(51, -40) * mm});
            skLineSegment(sketch, "E12.11.14.0", {"start": v(51, -16) * mm, "end": v(61, -16) * mm});
            skLineSegment(sketch, "E12.11.14.1", {"start": v(61, -16) * mm, "end": v(61, -26) * mm});
            skLineSegment(sketch, "E12.11.14.2", {"start": v(51, -26) * mm, "end": v(61, -26) * mm});
            skLineSegment(sketch, "E12.11.14.3", {"start": v(51, -16) * mm, "end": v(51, -26) * mm});
            skLineSegment(sketch, "E12.11.15.0", {"start": v(51, -2) * mm, "end": v(61, -2) * mm});
            skLineSegment(sketch, "E12.11.15.1", {"start": v(61, -2) * mm, "end": v(61, -12) * mm});
            skLineSegment(sketch, "E12.11.15.2", {"start": v(51, -12) * mm, "end": v(61, -12) * mm});
            skLineSegment(sketch, "E12.11.15.3", {"start": v(51, -2) * mm, "end": v(51, -12) * mm});
            skLineSegment(sketch, "E12.11.16.0", {"start": v(51, 12) * mm, "end": v(61, 12) * mm});
            skLineSegment(sketch, "E12.11.16.1", {"start": v(61, 12) * mm, "end": v(61, 2) * mm});
            skLineSegment(sketch, "E12.11.16.2", {"start": v(51, 2) * mm, "end": v(61, 2) * mm});
            skLineSegment(sketch, "E12.11.16.3", {"start": v(51, 12) * mm, "end": v(51, 2) * mm});
            skLineSegment(sketch, "E12.11.17.0", {"start": v(51, 26) * mm, "end": v(61, 26) * mm});
            skLineSegment(sketch, "E12.11.17.1", {"start": v(61, 26) * mm, "end": v(61, 16) * mm});
            skLineSegment(sketch, "E12.11.17.2", {"start": v(51, 16) * mm, "end": v(61, 16) * mm});
            skLineSegment(sketch, "E12.11.17.3", {"start": v(51, 26) * mm, "end": v(51, 16) * mm});
            skLineSegment(sketch, "E12.11.18.0", {"start": v(51, 40) * mm, "end": v(61, 40) * mm});
            skLineSegment(sketch, "E12.11.18.1", {"start": v(61, 40) * mm, "end": v(61, 30) * mm});
            skLineSegment(sketch, "E12.11.18.2", {"start": v(51, 30) * mm, "end": v(61, 30) * mm});
            skLineSegment(sketch, "E12.11.18.3", {"start": v(51, 40) * mm, "end": v(51, 30) * mm});
            skLineSegment(sketch, "E12.11.19.0", {"start": v(51, 54) * mm, "end": v(61, 54) * mm});
            skLineSegment(sketch, "E12.11.19.1", {"start": v(61, 54) * mm, "end": v(61, 44) * mm});
            skLineSegment(sketch, "E12.11.19.2", {"start": v(51, 44) * mm, "end": v(61, 44) * mm});
            skLineSegment(sketch, "E12.11.19.3", {"start": v(51, 54) * mm, "end": v(51, 44) * mm});
            skLineSegment(sketch, "E12.11.20.0", {"start": v(51, 68) * mm, "end": v(61, 68) * mm});
            skLineSegment(sketch, "E12.11.20.1", {"start": v(61, 68) * mm, "end": v(61, 58) * mm});
            skLineSegment(sketch, "E12.11.20.2", {"start": v(51, 58) * mm, "end": v(61, 58) * mm});
            skLineSegment(sketch, "E12.11.20.3", {"start": v(51, 68) * mm, "end": v(51, 58) * mm});
            skLineSegment(sketch, "E12.11.21.0", {"start": v(51, 82) * mm, "end": v(61, 82) * mm});
            skLineSegment(sketch, "E12.11.21.1", {"start": v(61, 82) * mm, "end": v(61, 72) * mm});
            skLineSegment(sketch, "E12.11.21.2", {"start": v(51, 72) * mm, "end": v(61, 72) * mm});
            skLineSegment(sketch, "E12.11.21.3", {"start": v(51, 82) * mm, "end": v(51, 72) * mm});
            skLineSegment(sketch, "E12.11.22.0", {"start": v(51, 96) * mm, "end": v(61, 96) * mm});
            skLineSegment(sketch, "E12.11.22.1", {"start": v(61, 96) * mm, "end": v(61, 86) * mm});
            skLineSegment(sketch, "E12.11.22.2", {"start": v(51, 86) * mm, "end": v(61, 86) * mm});
            skLineSegment(sketch, "E12.11.22.3", {"start": v(51, 96) * mm, "end": v(51, 86) * mm});
            skLineSegment(sketch, "E12.11.23.0", {"start": v(51, 110) * mm, "end": v(61, 110) * mm});
            skLineSegment(sketch, "E12.11.23.1", {"start": v(61, 110) * mm, "end": v(61, 100) * mm});
            skLineSegment(sketch, "E12.11.23.2", {"start": v(51, 100) * mm, "end": v(61, 100) * mm});
            skLineSegment(sketch, "E12.11.23.3", {"start": v(51, 110) * mm, "end": v(51, 100) * mm});
            skLineSegment(sketch, "E12.11.24.0", {"start": v(51, 124) * mm, "end": v(61, 124) * mm});
            skLineSegment(sketch, "E12.11.24.1", {"start": v(61, 124) * mm, "end": v(61, 114) * mm});
            skLineSegment(sketch, "E12.11.24.2", {"start": v(51, 114) * mm, "end": v(61, 114) * mm});
            skLineSegment(sketch, "E12.11.24.3", {"start": v(51, 124) * mm, "end": v(51, 114) * mm});
            skLineSegment(sketch, "E12.11.25.0", {"start": v(51, 138) * mm, "end": v(61, 138) * mm});
            skLineSegment(sketch, "E12.11.25.1", {"start": v(61, 138) * mm, "end": v(61, 128) * mm});
            skLineSegment(sketch, "E12.11.25.2", {"start": v(51, 128) * mm, "end": v(61, 128) * mm});
            skLineSegment(sketch, "E12.11.25.3", {"start": v(51, 138) * mm, "end": v(51, 128) * mm});
            skLineSegment(sketch, "E12.11.26.0", {"start": v(51, 152) * mm, "end": v(61, 152) * mm});
            skLineSegment(sketch, "E12.11.26.1", {"start": v(61, 152) * mm, "end": v(61, 142) * mm});
            skLineSegment(sketch, "E12.11.26.2", {"start": v(51, 142) * mm, "end": v(61, 142) * mm});
            skLineSegment(sketch, "E12.11.26.3", {"start": v(51, 152) * mm, "end": v(51, 142) * mm});
            skLineSegment(sketch, "E12.11.27.0", {"start": v(51, 166) * mm, "end": v(61, 166) * mm});
            skLineSegment(sketch, "E12.11.27.1", {"start": v(61, 166) * mm, "end": v(61, 156) * mm});
            skLineSegment(sketch, "E12.11.27.2", {"start": v(51, 156) * mm, "end": v(61, 156) * mm});
            skLineSegment(sketch, "E12.11.27.3", {"start": v(51, 166) * mm, "end": v(51, 156) * mm});
            skLineSegment(sketch, "E12.11.28.0", {"start": v(51, 180) * mm, "end": v(61, 180) * mm});
            skLineSegment(sketch, "E12.11.28.1", {"start": v(61, 180) * mm, "end": v(61, 170) * mm});
            skLineSegment(sketch, "E12.11.28.2", {"start": v(51, 170) * mm, "end": v(61, 170) * mm});
            skLineSegment(sketch, "E12.11.28.3", {"start": v(51, 180) * mm, "end": v(51, 170) * mm});
            skLineSegment(sketch, "E12.11.29.0", {"start": v(51, 194) * mm, "end": v(61, 194) * mm});
            skLineSegment(sketch, "E12.11.29.1", {"start": v(61, 194) * mm, "end": v(61, 184) * mm});
            skLineSegment(sketch, "E12.11.29.2", {"start": v(51, 184) * mm, "end": v(61, 184) * mm});
            skLineSegment(sketch, "E12.11.29.3", {"start": v(51, 194) * mm, "end": v(51, 184) * mm});
            skLineSegment(sketch, "E12.11.30.0", {"start": v(51, 208) * mm, "end": v(61, 208) * mm});
            skLineSegment(sketch, "E12.11.30.1", {"start": v(61, 208) * mm, "end": v(61, 198) * mm});
            skLineSegment(sketch, "E12.11.30.2", {"start": v(51, 198) * mm, "end": v(61, 198) * mm});
            skLineSegment(sketch, "E12.11.30.3", {"start": v(51, 208) * mm, "end": v(51, 198) * mm});
            skLineSegment(sketch, "E12.11.31.0", {"start": v(51, 222) * mm, "end": v(61, 222) * mm});
            skLineSegment(sketch, "E12.11.31.1", {"start": v(61, 222) * mm, "end": v(61, 212) * mm});
            skLineSegment(sketch, "E12.11.31.2", {"start": v(51, 212) * mm, "end": v(61, 212) * mm});
            skLineSegment(sketch, "E12.11.31.3", {"start": v(51, 222) * mm, "end": v(51, 212) * mm});
            skLineSegment(sketch, "E12.12.0.0", {"start": v(65, -212) * mm, "end": v(75, -212) * mm});
            skLineSegment(sketch, "E12.12.0.1", {"start": v(75, -212) * mm, "end": v(75, -222) * mm});
            skLineSegment(sketch, "E12.12.0.2", {"start": v(65, -222) * mm, "end": v(75, -222) * mm});
            skLineSegment(sketch, "E12.12.0.3", {"start": v(65, -212) * mm, "end": v(65, -222) * mm});
            skLineSegment(sketch, "E12.12.1.0", {"start": v(65, -198) * mm, "end": v(75, -198) * mm});
            skLineSegment(sketch, "E12.12.1.1", {"start": v(75, -198) * mm, "end": v(75, -208) * mm});
            skLineSegment(sketch, "E12.12.1.2", {"start": v(65, -208) * mm, "end": v(75, -208) * mm});
            skLineSegment(sketch, "E12.12.1.3", {"start": v(65, -198) * mm, "end": v(65, -208) * mm});
            skLineSegment(sketch, "E12.12.2.0", {"start": v(65, -184) * mm, "end": v(75, -184) * mm});
            skLineSegment(sketch, "E12.12.2.1", {"start": v(75, -184) * mm, "end": v(75, -194) * mm});
            skLineSegment(sketch, "E12.12.2.2", {"start": v(65, -194) * mm, "end": v(75, -194) * mm});
            skLineSegment(sketch, "E12.12.2.3", {"start": v(65, -184) * mm, "end": v(65, -194) * mm});
            skLineSegment(sketch, "E12.12.3.0", {"start": v(65, -170) * mm, "end": v(75, -170) * mm});
            skLineSegment(sketch, "E12.12.3.1", {"start": v(75, -170) * mm, "end": v(75, -180) * mm});
            skLineSegment(sketch, "E12.12.3.2", {"start": v(65, -180) * mm, "end": v(75, -180) * mm});
            skLineSegment(sketch, "E12.12.3.3", {"start": v(65, -170) * mm, "end": v(65, -180) * mm});
            skLineSegment(sketch, "E12.12.4.0", {"start": v(65, -156) * mm, "end": v(75, -156) * mm});
            skLineSegment(sketch, "E12.12.4.1", {"start": v(75, -156) * mm, "end": v(75, -166) * mm});
            skLineSegment(sketch, "E12.12.4.2", {"start": v(65, -166) * mm, "end": v(75, -166) * mm});
            skLineSegment(sketch, "E12.12.4.3", {"start": v(65, -156) * mm, "end": v(65, -166) * mm});
            skLineSegment(sketch, "E12.12.5.0", {"start": v(65, -142) * mm, "end": v(75, -142) * mm});
            skLineSegment(sketch, "E12.12.5.1", {"start": v(75, -142) * mm, "end": v(75, -152) * mm});
            skLineSegment(sketch, "E12.12.5.2", {"start": v(65, -152) * mm, "end": v(75, -152) * mm});
            skLineSegment(sketch, "E12.12.5.3", {"start": v(65, -142) * mm, "end": v(65, -152) * mm});
            skLineSegment(sketch, "E12.12.6.0", {"start": v(65, -128) * mm, "end": v(75, -128) * mm});
            skLineSegment(sketch, "E12.12.6.1", {"start": v(75, -128) * mm, "end": v(75, -138) * mm});
            skLineSegment(sketch, "E12.12.6.2", {"start": v(65, -138) * mm, "end": v(75, -138) * mm});
            skLineSegment(sketch, "E12.12.6.3", {"start": v(65, -128) * mm, "end": v(65, -138) * mm});
            skLineSegment(sketch, "E12.12.7.0", {"start": v(65, -114) * mm, "end": v(75, -114) * mm});
            skLineSegment(sketch, "E12.12.7.1", {"start": v(75, -114) * mm, "end": v(75, -124) * mm});
            skLineSegment(sketch, "E12.12.7.2", {"start": v(65, -124) * mm, "end": v(75, -124) * mm});
            skLineSegment(sketch, "E12.12.7.3", {"start": v(65, -114) * mm, "end": v(65, -124) * mm});
            skLineSegment(sketch, "E12.12.8.0", {"start": v(65, -100) * mm, "end": v(75, -100) * mm});
            skLineSegment(sketch, "E12.12.8.1", {"start": v(75, -100) * mm, "end": v(75, -110) * mm});
            skLineSegment(sketch, "E12.12.8.2", {"start": v(65, -110) * mm, "end": v(75, -110) * mm});
            skLineSegment(sketch, "E12.12.8.3", {"start": v(65, -100) * mm, "end": v(65, -110) * mm});
            skLineSegment(sketch, "E12.12.9.0", {"start": v(65, -86) * mm, "end": v(75, -86) * mm});
            skLineSegment(sketch, "E12.12.9.1", {"start": v(75, -86) * mm, "end": v(75, -96) * mm});
            skLineSegment(sketch, "E12.12.9.2", {"start": v(65, -96) * mm, "end": v(75, -96) * mm});
            skLineSegment(sketch, "E12.12.9.3", {"start": v(65, -86) * mm, "end": v(65, -96) * mm});
            skLineSegment(sketch, "E12.12.10.0", {"start": v(65, -72) * mm, "end": v(75, -72) * mm});
            skLineSegment(sketch, "E12.12.10.1", {"start": v(75, -72) * mm, "end": v(75, -82) * mm});
            skLineSegment(sketch, "E12.12.10.2", {"start": v(65, -82) * mm, "end": v(75, -82) * mm});
            skLineSegment(sketch, "E12.12.10.3", {"start": v(65, -72) * mm, "end": v(65, -82) * mm});
            skLineSegment(sketch, "E12.12.11.0", {"start": v(65, -58) * mm, "end": v(75, -58) * mm});
            skLineSegment(sketch, "E12.12.11.1", {"start": v(75, -58) * mm, "end": v(75, -68) * mm});
            skLineSegment(sketch, "E12.12.11.2", {"start": v(65, -68) * mm, "end": v(75, -68) * mm});
            skLineSegment(sketch, "E12.12.11.3", {"start": v(65, -58) * mm, "end": v(65, -68) * mm});
            skLineSegment(sketch, "E12.12.12.0", {"start": v(65, -44) * mm, "end": v(75, -44) * mm});
            skLineSegment(sketch, "E12.12.12.1", {"start": v(75, -44) * mm, "end": v(75, -54) * mm});
            skLineSegment(sketch, "E12.12.12.2", {"start": v(65, -54) * mm, "end": v(75, -54) * mm});
            skLineSegment(sketch, "E12.12.12.3", {"start": v(65, -44) * mm, "end": v(65, -54) * mm});
            skLineSegment(sketch, "E12.12.13.0", {"start": v(65, -30) * mm, "end": v(75, -30) * mm});
            skLineSegment(sketch, "E12.12.13.1", {"start": v(75, -30) * mm, "end": v(75, -40) * mm});
            skLineSegment(sketch, "E12.12.13.2", {"start": v(65, -40) * mm, "end": v(75, -40) * mm});
            skLineSegment(sketch, "E12.12.13.3", {"start": v(65, -30) * mm, "end": v(65, -40) * mm});
            skLineSegment(sketch, "E12.12.14.0", {"start": v(65, -16) * mm, "end": v(75, -16) * mm});
            skLineSegment(sketch, "E12.12.14.1", {"start": v(75, -16) * mm, "end": v(75, -26) * mm});
            skLineSegment(sketch, "E12.12.14.2", {"start": v(65, -26) * mm, "end": v(75, -26) * mm});
            skLineSegment(sketch, "E12.12.14.3", {"start": v(65, -16) * mm, "end": v(65, -26) * mm});
            skLineSegment(sketch, "E12.12.15.0", {"start": v(65, -2) * mm, "end": v(75, -2) * mm});
            skLineSegment(sketch, "E12.12.15.1", {"start": v(75, -2) * mm, "end": v(75, -12) * mm});
            skLineSegment(sketch, "E12.12.15.2", {"start": v(65, -12) * mm, "end": v(75, -12) * mm});
            skLineSegment(sketch, "E12.12.15.3", {"start": v(65, -2) * mm, "end": v(65, -12) * mm});
            skLineSegment(sketch, "E12.12.16.0", {"start": v(65, 12) * mm, "end": v(75, 12) * mm});
            skLineSegment(sketch, "E12.12.16.1", {"start": v(75, 12) * mm, "end": v(75, 2) * mm});
            skLineSegment(sketch, "E12.12.16.2", {"start": v(65, 2) * mm, "end": v(75, 2) * mm});
            skLineSegment(sketch, "E12.12.16.3", {"start": v(65, 12) * mm, "end": v(65, 2) * mm});
            skLineSegment(sketch, "E12.12.17.0", {"start": v(65, 26) * mm, "end": v(75, 26) * mm});
            skLineSegment(sketch, "E12.12.17.1", {"start": v(75, 26) * mm, "end": v(75, 16) * mm});
            skLineSegment(sketch, "E12.12.17.2", {"start": v(65, 16) * mm, "end": v(75, 16) * mm});
            skLineSegment(sketch, "E12.12.17.3", {"start": v(65, 26) * mm, "end": v(65, 16) * mm});
            skLineSegment(sketch, "E12.12.18.0", {"start": v(65, 40) * mm, "end": v(75, 40) * mm});
            skLineSegment(sketch, "E12.12.18.1", {"start": v(75, 40) * mm, "end": v(75, 30) * mm});
            skLineSegment(sketch, "E12.12.18.2", {"start": v(65, 30) * mm, "end": v(75, 30) * mm});
            skLineSegment(sketch, "E12.12.18.3", {"start": v(65, 40) * mm, "end": v(65, 30) * mm});
            skLineSegment(sketch, "E12.12.19.0", {"start": v(65, 54) * mm, "end": v(75, 54) * mm});
            skLineSegment(sketch, "E12.12.19.1", {"start": v(75, 54) * mm, "end": v(75, 44) * mm});
            skLineSegment(sketch, "E12.12.19.2", {"start": v(65, 44) * mm, "end": v(75, 44) * mm});
            skLineSegment(sketch, "E12.12.19.3", {"start": v(65, 54) * mm, "end": v(65, 44) * mm});
            skLineSegment(sketch, "E12.12.20.0", {"start": v(65, 68) * mm, "end": v(75, 68) * mm});
            skLineSegment(sketch, "E12.12.20.1", {"start": v(75, 68) * mm, "end": v(75, 58) * mm});
            skLineSegment(sketch, "E12.12.20.2", {"start": v(65, 58) * mm, "end": v(75, 58) * mm});
            skLineSegment(sketch, "E12.12.20.3", {"start": v(65, 68) * mm, "end": v(65, 58) * mm});
            skLineSegment(sketch, "E12.12.21.0", {"start": v(65, 82) * mm, "end": v(75, 82) * mm});
            skLineSegment(sketch, "E12.12.21.1", {"start": v(75, 82) * mm, "end": v(75, 72) * mm});
            skLineSegment(sketch, "E12.12.21.2", {"start": v(65, 72) * mm, "end": v(75, 72) * mm});
            skLineSegment(sketch, "E12.12.21.3", {"start": v(65, 82) * mm, "end": v(65, 72) * mm});
            skLineSegment(sketch, "E12.12.22.0", {"start": v(65, 96) * mm, "end": v(75, 96) * mm});
            skLineSegment(sketch, "E12.12.22.1", {"start": v(75, 96) * mm, "end": v(75, 86) * mm});
            skLineSegment(sketch, "E12.12.22.2", {"start": v(65, 86) * mm, "end": v(75, 86) * mm});
            skLineSegment(sketch, "E12.12.22.3", {"start": v(65, 96) * mm, "end": v(65, 86) * mm});
            skLineSegment(sketch, "E12.12.23.0", {"start": v(65, 110) * mm, "end": v(75, 110) * mm});
            skLineSegment(sketch, "E12.12.23.1", {"start": v(75, 110) * mm, "end": v(75, 100) * mm});
            skLineSegment(sketch, "E12.12.23.2", {"start": v(65, 100) * mm, "end": v(75, 100) * mm});
            skLineSegment(sketch, "E12.12.23.3", {"start": v(65, 110) * mm, "end": v(65, 100) * mm});
            skLineSegment(sketch, "E12.12.24.0", {"start": v(65, 124) * mm, "end": v(75, 124) * mm});
            skLineSegment(sketch, "E12.12.24.1", {"start": v(75, 124) * mm, "end": v(75, 114) * mm});
            skLineSegment(sketch, "E12.12.24.2", {"start": v(65, 114) * mm, "end": v(75, 114) * mm});
            skLineSegment(sketch, "E12.12.24.3", {"start": v(65, 124) * mm, "end": v(65, 114) * mm});
            skLineSegment(sketch, "E12.12.25.0", {"start": v(65, 138) * mm, "end": v(75, 138) * mm});
            skLineSegment(sketch, "E12.12.25.1", {"start": v(75, 138) * mm, "end": v(75, 128) * mm});
            skLineSegment(sketch, "E12.12.25.2", {"start": v(65, 128) * mm, "end": v(75, 128) * mm});
            skLineSegment(sketch, "E12.12.25.3", {"start": v(65, 138) * mm, "end": v(65, 128) * mm});
            skLineSegment(sketch, "E12.12.26.0", {"start": v(65, 152) * mm, "end": v(75, 152) * mm});
            skLineSegment(sketch, "E12.12.26.1", {"start": v(75, 152) * mm, "end": v(75, 142) * mm});
            skLineSegment(sketch, "E12.12.26.2", {"start": v(65, 142) * mm, "end": v(75, 142) * mm});
            skLineSegment(sketch, "E12.12.26.3", {"start": v(65, 152) * mm, "end": v(65, 142) * mm});
            skLineSegment(sketch, "E12.12.27.0", {"start": v(65, 166) * mm, "end": v(75, 166) * mm});
            skLineSegment(sketch, "E12.12.27.1", {"start": v(75, 166) * mm, "end": v(75, 156) * mm});
            skLineSegment(sketch, "E12.12.27.2", {"start": v(65, 156) * mm, "end": v(75, 156) * mm});
            skLineSegment(sketch, "E12.12.27.3", {"start": v(65, 166) * mm, "end": v(65, 156) * mm});
            skLineSegment(sketch, "E12.12.28.0", {"start": v(65, 180) * mm, "end": v(75, 180) * mm});
            skLineSegment(sketch, "E12.12.28.1", {"start": v(75, 180) * mm, "end": v(75, 170) * mm});
            skLineSegment(sketch, "E12.12.28.2", {"start": v(65, 170) * mm, "end": v(75, 170) * mm});
            skLineSegment(sketch, "E12.12.28.3", {"start": v(65, 180) * mm, "end": v(65, 170) * mm});
            skLineSegment(sketch, "E12.12.29.0", {"start": v(65, 194) * mm, "end": v(75, 194) * mm});
            skLineSegment(sketch, "E12.12.29.1", {"start": v(75, 194) * mm, "end": v(75, 184) * mm});
            skLineSegment(sketch, "E12.12.29.2", {"start": v(65, 184) * mm, "end": v(75, 184) * mm});
            skLineSegment(sketch, "E12.12.29.3", {"start": v(65, 194) * mm, "end": v(65, 184) * mm});
            skLineSegment(sketch, "E12.12.30.0", {"start": v(65, 208) * mm, "end": v(75, 208) * mm});
            skLineSegment(sketch, "E12.12.30.1", {"start": v(75, 208) * mm, "end": v(75, 198) * mm});
            skLineSegment(sketch, "E12.12.30.2", {"start": v(65, 198) * mm, "end": v(75, 198) * mm});
            skLineSegment(sketch, "E12.12.30.3", {"start": v(65, 208) * mm, "end": v(65, 198) * mm});
            skLineSegment(sketch, "E12.12.31.0", {"start": v(65, 222) * mm, "end": v(75, 222) * mm});
            skLineSegment(sketch, "E12.12.31.1", {"start": v(75, 222) * mm, "end": v(75, 212) * mm});
            skLineSegment(sketch, "E12.12.31.2", {"start": v(65, 212) * mm, "end": v(75, 212) * mm});
            skLineSegment(sketch, "E12.12.31.3", {"start": v(65, 222) * mm, "end": v(65, 212) * mm});
            skLineSegment(sketch, "E12.13.0.0", {"start": v(79, -212) * mm, "end": v(89, -212) * mm});
            skLineSegment(sketch, "E12.13.0.1", {"start": v(89, -212) * mm, "end": v(89, -222) * mm});
            skLineSegment(sketch, "E12.13.0.2", {"start": v(79, -222) * mm, "end": v(89, -222) * mm});
            skLineSegment(sketch, "E12.13.0.3", {"start": v(79, -212) * mm, "end": v(79, -222) * mm});
            skLineSegment(sketch, "E12.13.1.0", {"start": v(79, -198) * mm, "end": v(89, -198) * mm});
            skLineSegment(sketch, "E12.13.1.1", {"start": v(89, -198) * mm, "end": v(89, -208) * mm});
            skLineSegment(sketch, "E12.13.1.2", {"start": v(79, -208) * mm, "end": v(89, -208) * mm});
            skLineSegment(sketch, "E12.13.1.3", {"start": v(79, -198) * mm, "end": v(79, -208) * mm});
            skLineSegment(sketch, "E12.13.2.0", {"start": v(79, -184) * mm, "end": v(89, -184) * mm});
            skLineSegment(sketch, "E12.13.2.1", {"start": v(89, -184) * mm, "end": v(89, -194) * mm});
            skLineSegment(sketch, "E12.13.2.2", {"start": v(79, -194) * mm, "end": v(89, -194) * mm});
            skLineSegment(sketch, "E12.13.2.3", {"start": v(79, -184) * mm, "end": v(79, -194) * mm});
            skLineSegment(sketch, "E12.13.3.0", {"start": v(79, -170) * mm, "end": v(89, -170) * mm});
            skLineSegment(sketch, "E12.13.3.1", {"start": v(89, -170) * mm, "end": v(89, -180) * mm});
            skLineSegment(sketch, "E12.13.3.2", {"start": v(79, -180) * mm, "end": v(89, -180) * mm});
            skLineSegment(sketch, "E12.13.3.3", {"start": v(79, -170) * mm, "end": v(79, -180) * mm});
            skLineSegment(sketch, "E12.13.4.0", {"start": v(79, -156) * mm, "end": v(89, -156) * mm});
            skLineSegment(sketch, "E12.13.4.1", {"start": v(89, -156) * mm, "end": v(89, -166) * mm});
            skLineSegment(sketch, "E12.13.4.2", {"start": v(79, -166) * mm, "end": v(89, -166) * mm});
            skLineSegment(sketch, "E12.13.4.3", {"start": v(79, -156) * mm, "end": v(79, -166) * mm});
            skLineSegment(sketch, "E12.13.5.0", {"start": v(79, -142) * mm, "end": v(89, -142) * mm});
            skLineSegment(sketch, "E12.13.5.1", {"start": v(89, -142) * mm, "end": v(89, -152) * mm});
            skLineSegment(sketch, "E12.13.5.2", {"start": v(79, -152) * mm, "end": v(89, -152) * mm});
            skLineSegment(sketch, "E12.13.5.3", {"start": v(79, -142) * mm, "end": v(79, -152) * mm});
            skLineSegment(sketch, "E12.13.6.0", {"start": v(79, -128) * mm, "end": v(89, -128) * mm});
            skLineSegment(sketch, "E12.13.6.1", {"start": v(89, -128) * mm, "end": v(89, -138) * mm});
            skLineSegment(sketch, "E12.13.6.2", {"start": v(79, -138) * mm, "end": v(89, -138) * mm});
            skLineSegment(sketch, "E12.13.6.3", {"start": v(79, -128) * mm, "end": v(79, -138) * mm});
            skLineSegment(sketch, "E12.13.7.0", {"start": v(79, -114) * mm, "end": v(89, -114) * mm});
            skLineSegment(sketch, "E12.13.7.1", {"start": v(89, -114) * mm, "end": v(89, -124) * mm});
            skLineSegment(sketch, "E12.13.7.2", {"start": v(79, -124) * mm, "end": v(89, -124) * mm});
            skLineSegment(sketch, "E12.13.7.3", {"start": v(79, -114) * mm, "end": v(79, -124) * mm});
            skLineSegment(sketch, "E12.13.8.0", {"start": v(79, -100) * mm, "end": v(89, -100) * mm});
            skLineSegment(sketch, "E12.13.8.1", {"start": v(89, -100) * mm, "end": v(89, -110) * mm});
            skLineSegment(sketch, "E12.13.8.2", {"start": v(79, -110) * mm, "end": v(89, -110) * mm});
            skLineSegment(sketch, "E12.13.8.3", {"start": v(79, -100) * mm, "end": v(79, -110) * mm});
            skLineSegment(sketch, "E12.13.9.0", {"start": v(79, -86) * mm, "end": v(89, -86) * mm});
            skLineSegment(sketch, "E12.13.9.1", {"start": v(89, -86) * mm, "end": v(89, -96) * mm});
            skLineSegment(sketch, "E12.13.9.2", {"start": v(79, -96) * mm, "end": v(89, -96) * mm});
            skLineSegment(sketch, "E12.13.9.3", {"start": v(79, -86) * mm, "end": v(79, -96) * mm});
            skLineSegment(sketch, "E12.13.10.0", {"start": v(79, -72) * mm, "end": v(89, -72) * mm});
            skLineSegment(sketch, "E12.13.10.1", {"start": v(89, -72) * mm, "end": v(89, -82) * mm});
            skLineSegment(sketch, "E12.13.10.2", {"start": v(79, -82) * mm, "end": v(89, -82) * mm});
            skLineSegment(sketch, "E12.13.10.3", {"start": v(79, -72) * mm, "end": v(79, -82) * mm});
            skLineSegment(sketch, "E12.13.11.0", {"start": v(79, -58) * mm, "end": v(89, -58) * mm});
            skLineSegment(sketch, "E12.13.11.1", {"start": v(89, -58) * mm, "end": v(89, -68) * mm});
            skLineSegment(sketch, "E12.13.11.2", {"start": v(79, -68) * mm, "end": v(89, -68) * mm});
            skLineSegment(sketch, "E12.13.11.3", {"start": v(79, -58) * mm, "end": v(79, -68) * mm});
            skLineSegment(sketch, "E12.13.12.0", {"start": v(79, -44) * mm, "end": v(89, -44) * mm});
            skLineSegment(sketch, "E12.13.12.1", {"start": v(89, -44) * mm, "end": v(89, -54) * mm});
            skLineSegment(sketch, "E12.13.12.2", {"start": v(79, -54) * mm, "end": v(89, -54) * mm});
            skLineSegment(sketch, "E12.13.12.3", {"start": v(79, -44) * mm, "end": v(79, -54) * mm});
            skLineSegment(sketch, "E12.13.13.0", {"start": v(79, -30) * mm, "end": v(89, -30) * mm});
            skLineSegment(sketch, "E12.13.13.1", {"start": v(89, -30) * mm, "end": v(89, -40) * mm});
            skLineSegment(sketch, "E12.13.13.2", {"start": v(79, -40) * mm, "end": v(89, -40) * mm});
            skLineSegment(sketch, "E12.13.13.3", {"start": v(79, -30) * mm, "end": v(79, -40) * mm});
            skLineSegment(sketch, "E12.13.14.0", {"start": v(79, -16) * mm, "end": v(89, -16) * mm});
            skLineSegment(sketch, "E12.13.14.1", {"start": v(89, -16) * mm, "end": v(89, -26) * mm});
            skLineSegment(sketch, "E12.13.14.2", {"start": v(79, -26) * mm, "end": v(89, -26) * mm});
            skLineSegment(sketch, "E12.13.14.3", {"start": v(79, -16) * mm, "end": v(79, -26) * mm});
            skLineSegment(sketch, "E12.13.15.0", {"start": v(79, -2) * mm, "end": v(89, -2) * mm});
            skLineSegment(sketch, "E12.13.15.1", {"start": v(89, -2) * mm, "end": v(89, -12) * mm});
            skLineSegment(sketch, "E12.13.15.2", {"start": v(79, -12) * mm, "end": v(89, -12) * mm});
            skLineSegment(sketch, "E12.13.15.3", {"start": v(79, -2) * mm, "end": v(79, -12) * mm});
            skLineSegment(sketch, "E12.13.16.0", {"start": v(79, 12) * mm, "end": v(89, 12) * mm});
            skLineSegment(sketch, "E12.13.16.1", {"start": v(89, 12) * mm, "end": v(89, 2) * mm});
            skLineSegment(sketch, "E12.13.16.2", {"start": v(79, 2) * mm, "end": v(89, 2) * mm});
            skLineSegment(sketch, "E12.13.16.3", {"start": v(79, 12) * mm, "end": v(79, 2) * mm});
            skLineSegment(sketch, "E12.13.17.0", {"start": v(79, 26) * mm, "end": v(89, 26) * mm});
            skLineSegment(sketch, "E12.13.17.1", {"start": v(89, 26) * mm, "end": v(89, 16) * mm});
            skLineSegment(sketch, "E12.13.17.2", {"start": v(79, 16) * mm, "end": v(89, 16) * mm});
            skLineSegment(sketch, "E12.13.17.3", {"start": v(79, 26) * mm, "end": v(79, 16) * mm});
            skLineSegment(sketch, "E12.13.18.0", {"start": v(79, 40) * mm, "end": v(89, 40) * mm});
            skLineSegment(sketch, "E12.13.18.1", {"start": v(89, 40) * mm, "end": v(89, 30) * mm});
            skLineSegment(sketch, "E12.13.18.2", {"start": v(79, 30) * mm, "end": v(89, 30) * mm});
            skLineSegment(sketch, "E12.13.18.3", {"start": v(79, 40) * mm, "end": v(79, 30) * mm});
            skLineSegment(sketch, "E12.13.19.0", {"start": v(79, 54) * mm, "end": v(89, 54) * mm});
            skLineSegment(sketch, "E12.13.19.1", {"start": v(89, 54) * mm, "end": v(89, 44) * mm});
            skLineSegment(sketch, "E12.13.19.2", {"start": v(79, 44) * mm, "end": v(89, 44) * mm});
            skLineSegment(sketch, "E12.13.19.3", {"start": v(79, 54) * mm, "end": v(79, 44) * mm});
            skLineSegment(sketch, "E12.13.20.0", {"start": v(79, 68) * mm, "end": v(89, 68) * mm});
            skLineSegment(sketch, "E12.13.20.1", {"start": v(89, 68) * mm, "end": v(89, 58) * mm});
            skLineSegment(sketch, "E12.13.20.2", {"start": v(79, 58) * mm, "end": v(89, 58) * mm});
            skLineSegment(sketch, "E12.13.20.3", {"start": v(79, 68) * mm, "end": v(79, 58) * mm});
            skLineSegment(sketch, "E12.13.21.0", {"start": v(79, 82) * mm, "end": v(89, 82) * mm});
            skLineSegment(sketch, "E12.13.21.1", {"start": v(89, 82) * mm, "end": v(89, 72) * mm});
            skLineSegment(sketch, "E12.13.21.2", {"start": v(79, 72) * mm, "end": v(89, 72) * mm});
            skLineSegment(sketch, "E12.13.21.3", {"start": v(79, 82) * mm, "end": v(79, 72) * mm});
            skLineSegment(sketch, "E12.13.22.0", {"start": v(79, 96) * mm, "end": v(89, 96) * mm});
            skLineSegment(sketch, "E12.13.22.1", {"start": v(89, 96) * mm, "end": v(89, 86) * mm});
            skLineSegment(sketch, "E12.13.22.2", {"start": v(79, 86) * mm, "end": v(89, 86) * mm});
            skLineSegment(sketch, "E12.13.22.3", {"start": v(79, 96) * mm, "end": v(79, 86) * mm});
            skLineSegment(sketch, "E12.13.23.0", {"start": v(79, 110) * mm, "end": v(89, 110) * mm});
            skLineSegment(sketch, "E12.13.23.1", {"start": v(89, 110) * mm, "end": v(89, 100) * mm});
            skLineSegment(sketch, "E12.13.23.2", {"start": v(79, 100) * mm, "end": v(89, 100) * mm});
            skLineSegment(sketch, "E12.13.23.3", {"start": v(79, 110) * mm, "end": v(79, 100) * mm});
            skLineSegment(sketch, "E12.13.24.0", {"start": v(79, 124) * mm, "end": v(89, 124) * mm});
            skLineSegment(sketch, "E12.13.24.1", {"start": v(89, 124) * mm, "end": v(89, 114) * mm});
            skLineSegment(sketch, "E12.13.24.2", {"start": v(79, 114) * mm, "end": v(89, 114) * mm});
            skLineSegment(sketch, "E12.13.24.3", {"start": v(79, 124) * mm, "end": v(79, 114) * mm});
            skLineSegment(sketch, "E12.13.25.0", {"start": v(79, 138) * mm, "end": v(89, 138) * mm});
            skLineSegment(sketch, "E12.13.25.1", {"start": v(89, 138) * mm, "end": v(89, 128) * mm});
            skLineSegment(sketch, "E12.13.25.2", {"start": v(79, 128) * mm, "end": v(89, 128) * mm});
            skLineSegment(sketch, "E12.13.25.3", {"start": v(79, 138) * mm, "end": v(79, 128) * mm});
            skLineSegment(sketch, "E12.13.26.0", {"start": v(79, 152) * mm, "end": v(89, 152) * mm});
            skLineSegment(sketch, "E12.13.26.1", {"start": v(89, 152) * mm, "end": v(89, 142) * mm});
            skLineSegment(sketch, "E12.13.26.2", {"start": v(79, 142) * mm, "end": v(89, 142) * mm});
            skLineSegment(sketch, "E12.13.26.3", {"start": v(79, 152) * mm, "end": v(79, 142) * mm});
            skLineSegment(sketch, "E12.13.27.0", {"start": v(79, 166) * mm, "end": v(89, 166) * mm});
            skLineSegment(sketch, "E12.13.27.1", {"start": v(89, 166) * mm, "end": v(89, 156) * mm});
            skLineSegment(sketch, "E12.13.27.2", {"start": v(79, 156) * mm, "end": v(89, 156) * mm});
            skLineSegment(sketch, "E12.13.27.3", {"start": v(79, 166) * mm, "end": v(79, 156) * mm});
            skLineSegment(sketch, "E12.13.28.0", {"start": v(79, 180) * mm, "end": v(89, 180) * mm});
            skLineSegment(sketch, "E12.13.28.1", {"start": v(89, 180) * mm, "end": v(89, 170) * mm});
            skLineSegment(sketch, "E12.13.28.2", {"start": v(79, 170) * mm, "end": v(89, 170) * mm});
            skLineSegment(sketch, "E12.13.28.3", {"start": v(79, 180) * mm, "end": v(79, 170) * mm});
            skLineSegment(sketch, "E12.13.29.0", {"start": v(79, 194) * mm, "end": v(89, 194) * mm});
            skLineSegment(sketch, "E12.13.29.1", {"start": v(89, 194) * mm, "end": v(89, 184) * mm});
            skLineSegment(sketch, "E12.13.29.2", {"start": v(79, 184) * mm, "end": v(89, 184) * mm});
            skLineSegment(sketch, "E12.13.29.3", {"start": v(79, 194) * mm, "end": v(79, 184) * mm});
            skLineSegment(sketch, "E12.13.30.0", {"start": v(79, 208) * mm, "end": v(89, 208) * mm});
            skLineSegment(sketch, "E12.13.30.1", {"start": v(89, 208) * mm, "end": v(89, 198) * mm});
            skLineSegment(sketch, "E12.13.30.2", {"start": v(79, 198) * mm, "end": v(89, 198) * mm});
            skLineSegment(sketch, "E12.13.30.3", {"start": v(79, 208) * mm, "end": v(79, 198) * mm});
            skLineSegment(sketch, "E12.13.31.0", {"start": v(79, 222) * mm, "end": v(89, 222) * mm});
            skLineSegment(sketch, "E12.13.31.1", {"start": v(89, 222) * mm, "end": v(89, 212) * mm});
            skLineSegment(sketch, "E12.13.31.2", {"start": v(79, 212) * mm, "end": v(89, 212) * mm});
            skLineSegment(sketch, "E12.13.31.3", {"start": v(79, 222) * mm, "end": v(79, 212) * mm});
            skLineSegment(sketch, "E12.14.0.0", {"start": v(93, -212) * mm, "end": v(103, -212) * mm});
            skLineSegment(sketch, "E12.14.0.1", {"start": v(103, -212) * mm, "end": v(103, -222) * mm});
            skLineSegment(sketch, "E12.14.0.2", {"start": v(93, -222) * mm, "end": v(103, -222) * mm});
            skLineSegment(sketch, "E12.14.0.3", {"start": v(93, -212) * mm, "end": v(93, -222) * mm});
            skLineSegment(sketch, "E12.14.1.0", {"start": v(93, -198) * mm, "end": v(103, -198) * mm});
            skLineSegment(sketch, "E12.14.1.1", {"start": v(103, -198) * mm, "end": v(103, -208) * mm});
            skLineSegment(sketch, "E12.14.1.2", {"start": v(93, -208) * mm, "end": v(103, -208) * mm});
            skLineSegment(sketch, "E12.14.1.3", {"start": v(93, -198) * mm, "end": v(93, -208) * mm});
            skLineSegment(sketch, "E12.14.2.0", {"start": v(93, -184) * mm, "end": v(103, -184) * mm});
            skLineSegment(sketch, "E12.14.2.1", {"start": v(103, -184) * mm, "end": v(103, -194) * mm});
            skLineSegment(sketch, "E12.14.2.2", {"start": v(93, -194) * mm, "end": v(103, -194) * mm});
            skLineSegment(sketch, "E12.14.2.3", {"start": v(93, -184) * mm, "end": v(93, -194) * mm});
            skLineSegment(sketch, "E12.14.3.0", {"start": v(93, -170) * mm, "end": v(103, -170) * mm});
            skLineSegment(sketch, "E12.14.3.1", {"start": v(103, -170) * mm, "end": v(103, -180) * mm});
            skLineSegment(sketch, "E12.14.3.2", {"start": v(93, -180) * mm, "end": v(103, -180) * mm});
            skLineSegment(sketch, "E12.14.3.3", {"start": v(93, -170) * mm, "end": v(93, -180) * mm});
            skLineSegment(sketch, "E12.14.4.0", {"start": v(93, -156) * mm, "end": v(103, -156) * mm});
            skLineSegment(sketch, "E12.14.4.1", {"start": v(103, -156) * mm, "end": v(103, -166) * mm});
            skLineSegment(sketch, "E12.14.4.2", {"start": v(93, -166) * mm, "end": v(103, -166) * mm});
            skLineSegment(sketch, "E12.14.4.3", {"start": v(93, -156) * mm, "end": v(93, -166) * mm});
            skLineSegment(sketch, "E12.14.5.0", {"start": v(93, -142) * mm, "end": v(103, -142) * mm});
            skLineSegment(sketch, "E12.14.5.1", {"start": v(103, -142) * mm, "end": v(103, -152) * mm});
            skLineSegment(sketch, "E12.14.5.2", {"start": v(93, -152) * mm, "end": v(103, -152) * mm});
            skLineSegment(sketch, "E12.14.5.3", {"start": v(93, -142) * mm, "end": v(93, -152) * mm});
            skLineSegment(sketch, "E12.14.6.0", {"start": v(93, -128) * mm, "end": v(103, -128) * mm});
            skLineSegment(sketch, "E12.14.6.1", {"start": v(103, -128) * mm, "end": v(103, -138) * mm});
            skLineSegment(sketch, "E12.14.6.2", {"start": v(93, -138) * mm, "end": v(103, -138) * mm});
            skLineSegment(sketch, "E12.14.6.3", {"start": v(93, -128) * mm, "end": v(93, -138) * mm});
            skLineSegment(sketch, "E12.14.7.0", {"start": v(93, -114) * mm, "end": v(103, -114) * mm});
            skLineSegment(sketch, "E12.14.7.1", {"start": v(103, -114) * mm, "end": v(103, -124) * mm});
            skLineSegment(sketch, "E12.14.7.2", {"start": v(93, -124) * mm, "end": v(103, -124) * mm});
            skLineSegment(sketch, "E12.14.7.3", {"start": v(93, -114) * mm, "end": v(93, -124) * mm});
            skLineSegment(sketch, "E12.14.8.0", {"start": v(93, -100) * mm, "end": v(103, -100) * mm});
            skLineSegment(sketch, "E12.14.8.1", {"start": v(103, -100) * mm, "end": v(103, -110) * mm});
            skLineSegment(sketch, "E12.14.8.2", {"start": v(93, -110) * mm, "end": v(103, -110) * mm});
            skLineSegment(sketch, "E12.14.8.3", {"start": v(93, -100) * mm, "end": v(93, -110) * mm});
            skLineSegment(sketch, "E12.14.9.0", {"start": v(93, -86) * mm, "end": v(103, -86) * mm});
            skLineSegment(sketch, "E12.14.9.1", {"start": v(103, -86) * mm, "end": v(103, -96) * mm});
            skLineSegment(sketch, "E12.14.9.2", {"start": v(93, -96) * mm, "end": v(103, -96) * mm});
            skLineSegment(sketch, "E12.14.9.3", {"start": v(93, -86) * mm, "end": v(93, -96) * mm});
            skLineSegment(sketch, "E12.14.10.0", {"start": v(93, -72) * mm, "end": v(103, -72) * mm});
            skLineSegment(sketch, "E12.14.10.1", {"start": v(103, -72) * mm, "end": v(103, -82) * mm});
            skLineSegment(sketch, "E12.14.10.2", {"start": v(93, -82) * mm, "end": v(103, -82) * mm});
            skLineSegment(sketch, "E12.14.10.3", {"start": v(93, -72) * mm, "end": v(93, -82) * mm});
            skLineSegment(sketch, "E12.14.11.0", {"start": v(93, -58) * mm, "end": v(103, -58) * mm});
            skLineSegment(sketch, "E12.14.11.1", {"start": v(103, -58) * mm, "end": v(103, -68) * mm});
            skLineSegment(sketch, "E12.14.11.2", {"start": v(93, -68) * mm, "end": v(103, -68) * mm});
            skLineSegment(sketch, "E12.14.11.3", {"start": v(93, -58) * mm, "end": v(93, -68) * mm});
            skLineSegment(sketch, "E12.14.12.0", {"start": v(93, -44) * mm, "end": v(103, -44) * mm});
            skLineSegment(sketch, "E12.14.12.1", {"start": v(103, -44) * mm, "end": v(103, -54) * mm});
            skLineSegment(sketch, "E12.14.12.2", {"start": v(93, -54) * mm, "end": v(103, -54) * mm});
            skLineSegment(sketch, "E12.14.12.3", {"start": v(93, -44) * mm, "end": v(93, -54) * mm});
            skLineSegment(sketch, "E12.14.13.0", {"start": v(93, -30) * mm, "end": v(103, -30) * mm});
            skLineSegment(sketch, "E12.14.13.1", {"start": v(103, -30) * mm, "end": v(103, -40) * mm});
            skLineSegment(sketch, "E12.14.13.2", {"start": v(93, -40) * mm, "end": v(103, -40) * mm});
            skLineSegment(sketch, "E12.14.13.3", {"start": v(93, -30) * mm, "end": v(93, -40) * mm});
            skLineSegment(sketch, "E12.14.14.0", {"start": v(93, -16) * mm, "end": v(103, -16) * mm});
            skLineSegment(sketch, "E12.14.14.1", {"start": v(103, -16) * mm, "end": v(103, -26) * mm});
            skLineSegment(sketch, "E12.14.14.2", {"start": v(93, -26) * mm, "end": v(103, -26) * mm});
            skLineSegment(sketch, "E12.14.14.3", {"start": v(93, -16) * mm, "end": v(93, -26) * mm});
            skLineSegment(sketch, "E12.14.15.0", {"start": v(93, -2) * mm, "end": v(103, -2) * mm});
            skLineSegment(sketch, "E12.14.15.1", {"start": v(103, -2) * mm, "end": v(103, -12) * mm});
            skLineSegment(sketch, "E12.14.15.2", {"start": v(93, -12) * mm, "end": v(103, -12) * mm});
            skLineSegment(sketch, "E12.14.15.3", {"start": v(93, -2) * mm, "end": v(93, -12) * mm});
            skLineSegment(sketch, "E12.14.16.0", {"start": v(93, 12) * mm, "end": v(103, 12) * mm});
            skLineSegment(sketch, "E12.14.16.1", {"start": v(103, 12) * mm, "end": v(103, 2) * mm});
            skLineSegment(sketch, "E12.14.16.2", {"start": v(93, 2) * mm, "end": v(103, 2) * mm});
            skLineSegment(sketch, "E12.14.16.3", {"start": v(93, 12) * mm, "end": v(93, 2) * mm});
            skLineSegment(sketch, "E12.14.17.0", {"start": v(93, 26) * mm, "end": v(103, 26) * mm});
            skLineSegment(sketch, "E12.14.17.1", {"start": v(103, 26) * mm, "end": v(103, 16) * mm});
            skLineSegment(sketch, "E12.14.17.2", {"start": v(93, 16) * mm, "end": v(103, 16) * mm});
            skLineSegment(sketch, "E12.14.17.3", {"start": v(93, 26) * mm, "end": v(93, 16) * mm});
            skLineSegment(sketch, "E12.14.18.0", {"start": v(93, 40) * mm, "end": v(103, 40) * mm});
            skLineSegment(sketch, "E12.14.18.1", {"start": v(103, 40) * mm, "end": v(103, 30) * mm});
            skLineSegment(sketch, "E12.14.18.2", {"start": v(93, 30) * mm, "end": v(103, 30) * mm});
            skLineSegment(sketch, "E12.14.18.3", {"start": v(93, 40) * mm, "end": v(93, 30) * mm});
            skLineSegment(sketch, "E12.14.19.0", {"start": v(93, 54) * mm, "end": v(103, 54) * mm});
            skLineSegment(sketch, "E12.14.19.1", {"start": v(103, 54) * mm, "end": v(103, 44) * mm});
            skLineSegment(sketch, "E12.14.19.2", {"start": v(93, 44) * mm, "end": v(103, 44) * mm});
            skLineSegment(sketch, "E12.14.19.3", {"start": v(93, 54) * mm, "end": v(93, 44) * mm});
            skLineSegment(sketch, "E12.14.20.0", {"start": v(93, 68) * mm, "end": v(103, 68) * mm});
            skLineSegment(sketch, "E12.14.20.1", {"start": v(103, 68) * mm, "end": v(103, 58) * mm});
            skLineSegment(sketch, "E12.14.20.2", {"start": v(93, 58) * mm, "end": v(103, 58) * mm});
            skLineSegment(sketch, "E12.14.20.3", {"start": v(93, 68) * mm, "end": v(93, 58) * mm});
            skLineSegment(sketch, "E12.14.21.0", {"start": v(93, 82) * mm, "end": v(103, 82) * mm});
            skLineSegment(sketch, "E12.14.21.1", {"start": v(103, 82) * mm, "end": v(103, 72) * mm});
            skLineSegment(sketch, "E12.14.21.2", {"start": v(93, 72) * mm, "end": v(103, 72) * mm});
            skLineSegment(sketch, "E12.14.21.3", {"start": v(93, 82) * mm, "end": v(93, 72) * mm});
            skLineSegment(sketch, "E12.14.22.0", {"start": v(93, 96) * mm, "end": v(103, 96) * mm});
            skLineSegment(sketch, "E12.14.22.1", {"start": v(103, 96) * mm, "end": v(103, 86) * mm});
            skLineSegment(sketch, "E12.14.22.2", {"start": v(93, 86) * mm, "end": v(103, 86) * mm});
            skLineSegment(sketch, "E12.14.22.3", {"start": v(93, 96) * mm, "end": v(93, 86) * mm});
            skLineSegment(sketch, "E12.14.23.0", {"start": v(93, 110) * mm, "end": v(103, 110) * mm});
            skLineSegment(sketch, "E12.14.23.1", {"start": v(103, 110) * mm, "end": v(103, 100) * mm});
            skLineSegment(sketch, "E12.14.23.2", {"start": v(93, 100) * mm, "end": v(103, 100) * mm});
            skLineSegment(sketch, "E12.14.23.3", {"start": v(93, 110) * mm, "end": v(93, 100) * mm});
            skLineSegment(sketch, "E12.14.24.0", {"start": v(93, 124) * mm, "end": v(103, 124) * mm});
            skLineSegment(sketch, "E12.14.24.1", {"start": v(103, 124) * mm, "end": v(103, 114) * mm});
            skLineSegment(sketch, "E12.14.24.2", {"start": v(93, 114) * mm, "end": v(103, 114) * mm});
            skLineSegment(sketch, "E12.14.24.3", {"start": v(93, 124) * mm, "end": v(93, 114) * mm});
            skLineSegment(sketch, "E12.14.25.0", {"start": v(93, 138) * mm, "end": v(103, 138) * mm});
            skLineSegment(sketch, "E12.14.25.1", {"start": v(103, 138) * mm, "end": v(103, 128) * mm});
            skLineSegment(sketch, "E12.14.25.2", {"start": v(93, 128) * mm, "end": v(103, 128) * mm});
            skLineSegment(sketch, "E12.14.25.3", {"start": v(93, 138) * mm, "end": v(93, 128) * mm});
            skLineSegment(sketch, "E12.14.26.0", {"start": v(93, 152) * mm, "end": v(103, 152) * mm});
            skLineSegment(sketch, "E12.14.26.1", {"start": v(103, 152) * mm, "end": v(103, 142) * mm});
            skLineSegment(sketch, "E12.14.26.2", {"start": v(93, 142) * mm, "end": v(103, 142) * mm});
            skLineSegment(sketch, "E12.14.26.3", {"start": v(93, 152) * mm, "end": v(93, 142) * mm});
            skLineSegment(sketch, "E12.14.27.0", {"start": v(93, 166) * mm, "end": v(103, 166) * mm});
            skLineSegment(sketch, "E12.14.27.1", {"start": v(103, 166) * mm, "end": v(103, 156) * mm});
            skLineSegment(sketch, "E12.14.27.2", {"start": v(93, 156) * mm, "end": v(103, 156) * mm});
            skLineSegment(sketch, "E12.14.27.3", {"start": v(93, 166) * mm, "end": v(93, 156) * mm});
            skLineSegment(sketch, "E12.14.28.0", {"start": v(93, 180) * mm, "end": v(103, 180) * mm});
            skLineSegment(sketch, "E12.14.28.1", {"start": v(103, 180) * mm, "end": v(103, 170) * mm});
            skLineSegment(sketch, "E12.14.28.2", {"start": v(93, 170) * mm, "end": v(103, 170) * mm});
            skLineSegment(sketch, "E12.14.28.3", {"start": v(93, 180) * mm, "end": v(93, 170) * mm});
            skLineSegment(sketch, "E12.14.29.0", {"start": v(93, 194) * mm, "end": v(103, 194) * mm});
            skLineSegment(sketch, "E12.14.29.1", {"start": v(103, 194) * mm, "end": v(103, 184) * mm});
            skLineSegment(sketch, "E12.14.29.2", {"start": v(93, 184) * mm, "end": v(103, 184) * mm});
            skLineSegment(sketch, "E12.14.29.3", {"start": v(93, 194) * mm, "end": v(93, 184) * mm});
            skLineSegment(sketch, "E12.14.30.0", {"start": v(93, 208) * mm, "end": v(103, 208) * mm});
            skLineSegment(sketch, "E12.14.30.1", {"start": v(103, 208) * mm, "end": v(103, 198) * mm});
            skLineSegment(sketch, "E12.14.30.2", {"start": v(93, 198) * mm, "end": v(103, 198) * mm});
            skLineSegment(sketch, "E12.14.30.3", {"start": v(93, 208) * mm, "end": v(93, 198) * mm});
            skLineSegment(sketch, "E12.14.31.0", {"start": v(93, 222) * mm, "end": v(103, 222) * mm});
            skLineSegment(sketch, "E12.14.31.1", {"start": v(103, 222) * mm, "end": v(103, 212) * mm});
            skLineSegment(sketch, "E12.14.31.2", {"start": v(93, 212) * mm, "end": v(103, 212) * mm});
            skLineSegment(sketch, "E12.14.31.3", {"start": v(93, 222) * mm, "end": v(93, 212) * mm});
            skLineSegment(sketch, "E12.direction1", {"start": v(-103, -222) * mm, "end": v(-89, -222) * mm, "construction": true});
            skLineSegment(sketch, "E12.direction2", {"start": v(-103, -222) * mm, "end": v(-103, -208) * mm, "construction": true});
            skLineSegment(sketch, "E13.bottom", {"start": v(107, -222) * mm, "end": v(117, -222) * mm});
            skLineSegment(sketch, "E13.top", {"start": v(107, -212) * mm, "end": v(117, -212) * mm});
            skLineSegment(sketch, "E13.left", {"start": v(107, -222) * mm, "end": v(107, -212) * mm});
            skLineSegment(sketch, "E13.right", {"start": v(117, -222) * mm, "end": v(117, -212) * mm});
            skLineSegment(sketch, "E14.0.1.0", {"start": v(117, -208) * mm, "end": v(117, -198) * mm});
            skLineSegment(sketch, "E14.0.1.1", {"start": v(107, -208) * mm, "end": v(107, -198) * mm});
            skLineSegment(sketch, "E14.0.1.2", {"start": v(107, -198) * mm, "end": v(117, -198) * mm});
            skLineSegment(sketch, "E14.0.1.3", {"start": v(107, -208) * mm, "end": v(117, -208) * mm});
            skLineSegment(sketch, "E14.0.2.0", {"start": v(117, -194) * mm, "end": v(117, -184) * mm});
            skLineSegment(sketch, "E14.0.2.1", {"start": v(107, -194) * mm, "end": v(107, -184) * mm});
            skLineSegment(sketch, "E14.0.2.2", {"start": v(107, -184) * mm, "end": v(117, -184) * mm});
            skLineSegment(sketch, "E14.0.2.3", {"start": v(107, -194) * mm, "end": v(117, -194) * mm});
            skLineSegment(sketch, "E14.0.3.0", {"start": v(117, -180) * mm, "end": v(117, -170) * mm});
            skLineSegment(sketch, "E14.0.3.1", {"start": v(107, -180) * mm, "end": v(107, -170) * mm});
            skLineSegment(sketch, "E14.0.3.2", {"start": v(107, -170) * mm, "end": v(117, -170) * mm});
            skLineSegment(sketch, "E14.0.3.3", {"start": v(107, -180) * mm, "end": v(117, -180) * mm});
            skLineSegment(sketch, "E14.0.4.0", {"start": v(117, -166) * mm, "end": v(117, -156) * mm});
            skLineSegment(sketch, "E14.0.4.1", {"start": v(107, -166) * mm, "end": v(107, -156) * mm});
            skLineSegment(sketch, "E14.0.4.2", {"start": v(107, -156) * mm, "end": v(117, -156) * mm});
            skLineSegment(sketch, "E14.0.4.3", {"start": v(107, -166) * mm, "end": v(117, -166) * mm});
            skLineSegment(sketch, "E14.0.5.0", {"start": v(117, -152) * mm, "end": v(117, -142) * mm});
            skLineSegment(sketch, "E14.0.5.1", {"start": v(107, -152) * mm, "end": v(107, -142) * mm});
            skLineSegment(sketch, "E14.0.5.2", {"start": v(107, -142) * mm, "end": v(117, -142) * mm});
            skLineSegment(sketch, "E14.0.5.3", {"start": v(107, -152) * mm, "end": v(117, -152) * mm});
            skLineSegment(sketch, "E14.0.6.0", {"start": v(117, -138) * mm, "end": v(117, -128) * mm});
            skLineSegment(sketch, "E14.0.6.1", {"start": v(107, -138) * mm, "end": v(107, -128) * mm});
            skLineSegment(sketch, "E14.0.6.2", {"start": v(107, -128) * mm, "end": v(117, -128) * mm});
            skLineSegment(sketch, "E14.0.6.3", {"start": v(107, -138) * mm, "end": v(117, -138) * mm});
            skLineSegment(sketch, "E14.0.7.0", {"start": v(117, -124) * mm, "end": v(117, -114) * mm});
            skLineSegment(sketch, "E14.0.7.1", {"start": v(107, -124) * mm, "end": v(107, -114) * mm});
            skLineSegment(sketch, "E14.0.7.2", {"start": v(107, -114) * mm, "end": v(117, -114) * mm});
            skLineSegment(sketch, "E14.0.7.3", {"start": v(107, -124) * mm, "end": v(117, -124) * mm});
            skLineSegment(sketch, "E14.0.8.0", {"start": v(117, -110) * mm, "end": v(117, -100) * mm});
            skLineSegment(sketch, "E14.0.8.1", {"start": v(107, -110) * mm, "end": v(107, -100) * mm});
            skLineSegment(sketch, "E14.0.8.2", {"start": v(107, -100) * mm, "end": v(117, -100) * mm});
            skLineSegment(sketch, "E14.0.8.3", {"start": v(107, -110) * mm, "end": v(117, -110) * mm});
            skLineSegment(sketch, "E14.0.9.0", {"start": v(117, -96) * mm, "end": v(117, -86) * mm});
            skLineSegment(sketch, "E14.0.9.1", {"start": v(107, -96) * mm, "end": v(107, -86) * mm});
            skLineSegment(sketch, "E14.0.9.2", {"start": v(107, -86) * mm, "end": v(117, -86) * mm});
            skLineSegment(sketch, "E14.0.9.3", {"start": v(107, -96) * mm, "end": v(117, -96) * mm});
            skLineSegment(sketch, "E14.0.10.0", {"start": v(117, -82) * mm, "end": v(117, -72) * mm});
            skLineSegment(sketch, "E14.0.10.1", {"start": v(107, -82) * mm, "end": v(107, -72) * mm});
            skLineSegment(sketch, "E14.0.10.2", {"start": v(107, -72) * mm, "end": v(117, -72) * mm});
            skLineSegment(sketch, "E14.0.10.3", {"start": v(107, -82) * mm, "end": v(117, -82) * mm});
            skLineSegment(sketch, "E14.0.11.0", {"start": v(117, -68) * mm, "end": v(117, -58) * mm});
            skLineSegment(sketch, "E14.0.11.1", {"start": v(107, -68) * mm, "end": v(107, -58) * mm});
            skLineSegment(sketch, "E14.0.11.2", {"start": v(107, -58) * mm, "end": v(117, -58) * mm});
            skLineSegment(sketch, "E14.0.11.3", {"start": v(107, -68) * mm, "end": v(117, -68) * mm});
            skLineSegment(sketch, "E14.0.12.0", {"start": v(117, -54) * mm, "end": v(117, -44) * mm});
            skLineSegment(sketch, "E14.0.12.1", {"start": v(107, -54) * mm, "end": v(107, -44) * mm});
            skLineSegment(sketch, "E14.0.12.2", {"start": v(107, -44) * mm, "end": v(117, -44) * mm});
            skLineSegment(sketch, "E14.0.12.3", {"start": v(107, -54) * mm, "end": v(117, -54) * mm});
            skLineSegment(sketch, "E14.0.13.0", {"start": v(117, -40) * mm, "end": v(117, -30) * mm});
            skLineSegment(sketch, "E14.0.13.1", {"start": v(107, -40) * mm, "end": v(107, -30) * mm});
            skLineSegment(sketch, "E14.0.13.2", {"start": v(107, -30) * mm, "end": v(117, -30) * mm});
            skLineSegment(sketch, "E14.0.13.3", {"start": v(107, -40) * mm, "end": v(117, -40) * mm});
            skLineSegment(sketch, "E14.0.14.0", {"start": v(117, -26) * mm, "end": v(117, -16) * mm});
            skLineSegment(sketch, "E14.0.14.1", {"start": v(107, -26) * mm, "end": v(107, -16) * mm});
            skLineSegment(sketch, "E14.0.14.2", {"start": v(107, -16) * mm, "end": v(117, -16) * mm});
            skLineSegment(sketch, "E14.0.14.3", {"start": v(107, -26) * mm, "end": v(117, -26) * mm});
            skLineSegment(sketch, "E14.0.15.0", {"start": v(117, -12) * mm, "end": v(117, -2) * mm});
            skLineSegment(sketch, "E14.0.15.1", {"start": v(107, -12) * mm, "end": v(107, -2) * mm});
            skLineSegment(sketch, "E14.0.15.2", {"start": v(107, -2) * mm, "end": v(117, -2) * mm});
            skLineSegment(sketch, "E14.0.15.3", {"start": v(107, -12) * mm, "end": v(117, -12) * mm});
            skLineSegment(sketch, "E14.0.16.0", {"start": v(117, 2) * mm, "end": v(117, 12) * mm});
            skLineSegment(sketch, "E14.0.16.1", {"start": v(107, 2) * mm, "end": v(107, 12) * mm});
            skLineSegment(sketch, "E14.0.16.2", {"start": v(107, 12) * mm, "end": v(117, 12) * mm});
            skLineSegment(sketch, "E14.0.16.3", {"start": v(107, 2) * mm, "end": v(117, 2) * mm});
            skLineSegment(sketch, "E14.0.17.0", {"start": v(117, 16) * mm, "end": v(117, 26) * mm});
            skLineSegment(sketch, "E14.0.17.1", {"start": v(107, 16) * mm, "end": v(107, 26) * mm});
            skLineSegment(sketch, "E14.0.17.2", {"start": v(107, 26) * mm, "end": v(117, 26) * mm});
            skLineSegment(sketch, "E14.0.17.3", {"start": v(107, 16) * mm, "end": v(117, 16) * mm});
            skLineSegment(sketch, "E14.0.18.0", {"start": v(117, 30) * mm, "end": v(117, 40) * mm});
            skLineSegment(sketch, "E14.0.18.1", {"start": v(107, 30) * mm, "end": v(107, 40) * mm});
            skLineSegment(sketch, "E14.0.18.2", {"start": v(107, 40) * mm, "end": v(117, 40) * mm});
            skLineSegment(sketch, "E14.0.18.3", {"start": v(107, 30) * mm, "end": v(117, 30) * mm});
            skLineSegment(sketch, "E14.0.19.0", {"start": v(117, 44) * mm, "end": v(117, 54) * mm});
            skLineSegment(sketch, "E14.0.19.1", {"start": v(107, 44) * mm, "end": v(107, 54) * mm});
            skLineSegment(sketch, "E14.0.19.2", {"start": v(107, 54) * mm, "end": v(117, 54) * mm});
            skLineSegment(sketch, "E14.0.19.3", {"start": v(107, 44) * mm, "end": v(117, 44) * mm});
            skLineSegment(sketch, "E14.0.20.0", {"start": v(117, 58) * mm, "end": v(117, 68) * mm});
            skLineSegment(sketch, "E14.0.20.1", {"start": v(107, 58) * mm, "end": v(107, 68) * mm});
            skLineSegment(sketch, "E14.0.20.2", {"start": v(107, 68) * mm, "end": v(117, 68) * mm});
            skLineSegment(sketch, "E14.0.20.3", {"start": v(107, 58) * mm, "end": v(117, 58) * mm});
            skLineSegment(sketch, "E14.0.21.0", {"start": v(117, 72) * mm, "end": v(117, 82) * mm});
            skLineSegment(sketch, "E14.0.21.1", {"start": v(107, 72) * mm, "end": v(107, 82) * mm});
            skLineSegment(sketch, "E14.0.21.2", {"start": v(107, 82) * mm, "end": v(117, 82) * mm});
            skLineSegment(sketch, "E14.0.21.3", {"start": v(107, 72) * mm, "end": v(117, 72) * mm});
            skLineSegment(sketch, "E14.0.22.0", {"start": v(117, 86) * mm, "end": v(117, 96) * mm});
            skLineSegment(sketch, "E14.0.22.1", {"start": v(107, 86) * mm, "end": v(107, 96) * mm});
            skLineSegment(sketch, "E14.0.22.2", {"start": v(107, 96) * mm, "end": v(117, 96) * mm});
            skLineSegment(sketch, "E14.0.22.3", {"start": v(107, 86) * mm, "end": v(117, 86) * mm});
            skLineSegment(sketch, "E14.0.23.0", {"start": v(117, 100) * mm, "end": v(117, 110) * mm});
            skLineSegment(sketch, "E14.0.23.1", {"start": v(107, 100) * mm, "end": v(107, 110) * mm});
            skLineSegment(sketch, "E14.0.23.2", {"start": v(107, 110) * mm, "end": v(117, 110) * mm});
            skLineSegment(sketch, "E14.0.23.3", {"start": v(107, 100) * mm, "end": v(117, 100) * mm});
            skLineSegment(sketch, "E14.0.24.0", {"start": v(117, 114) * mm, "end": v(117, 124) * mm});
            skLineSegment(sketch, "E14.0.24.1", {"start": v(107, 114) * mm, "end": v(107, 124) * mm});
            skLineSegment(sketch, "E14.0.24.2", {"start": v(107, 124) * mm, "end": v(117, 124) * mm});
            skLineSegment(sketch, "E14.0.24.3", {"start": v(107, 114) * mm, "end": v(117, 114) * mm});
            skLineSegment(sketch, "E14.0.25.0", {"start": v(117, 128) * mm, "end": v(117, 138) * mm});
            skLineSegment(sketch, "E14.0.25.1", {"start": v(107, 128) * mm, "end": v(107, 138) * mm});
            skLineSegment(sketch, "E14.0.25.2", {"start": v(107, 138) * mm, "end": v(117, 138) * mm});
            skLineSegment(sketch, "E14.0.25.3", {"start": v(107, 128) * mm, "end": v(117, 128) * mm});
            skLineSegment(sketch, "E14.0.26.0", {"start": v(117, 142) * mm, "end": v(117, 152) * mm});
            skLineSegment(sketch, "E14.0.26.1", {"start": v(107, 142) * mm, "end": v(107, 152) * mm});
            skLineSegment(sketch, "E14.0.26.2", {"start": v(107, 152) * mm, "end": v(117, 152) * mm});
            skLineSegment(sketch, "E14.0.26.3", {"start": v(107, 142) * mm, "end": v(117, 142) * mm});
            skLineSegment(sketch, "E14.0.27.0", {"start": v(117, 156) * mm, "end": v(117, 166) * mm});
            skLineSegment(sketch, "E14.0.27.1", {"start": v(107, 156) * mm, "end": v(107, 166) * mm});
            skLineSegment(sketch, "E14.0.27.2", {"start": v(107, 166) * mm, "end": v(117, 166) * mm});
            skLineSegment(sketch, "E14.0.27.3", {"start": v(107, 156) * mm, "end": v(117, 156) * mm});
            skLineSegment(sketch, "E14.0.28.0", {"start": v(117, 170) * mm, "end": v(117, 180) * mm});
            skLineSegment(sketch, "E14.0.28.1", {"start": v(107, 170) * mm, "end": v(107, 180) * mm});
            skLineSegment(sketch, "E14.0.28.2", {"start": v(107, 180) * mm, "end": v(117, 180) * mm});
            skLineSegment(sketch, "E14.0.28.3", {"start": v(107, 170) * mm, "end": v(117, 170) * mm});
            skLineSegment(sketch, "E14.0.29.0", {"start": v(117, 184) * mm, "end": v(117, 194) * mm});
            skLineSegment(sketch, "E14.0.29.1", {"start": v(107, 184) * mm, "end": v(107, 194) * mm});
            skLineSegment(sketch, "E14.0.29.2", {"start": v(107, 194) * mm, "end": v(117, 194) * mm});
            skLineSegment(sketch, "E14.0.29.3", {"start": v(107, 184) * mm, "end": v(117, 184) * mm});
            skLineSegment(sketch, "E14.0.30.0", {"start": v(117, 198) * mm, "end": v(117, 208) * mm});
            skLineSegment(sketch, "E14.0.30.1", {"start": v(107, 198) * mm, "end": v(107, 208) * mm});
            skLineSegment(sketch, "E14.0.30.2", {"start": v(107, 208) * mm, "end": v(117, 208) * mm});
            skLineSegment(sketch, "E14.0.30.3", {"start": v(107, 198) * mm, "end": v(117, 198) * mm});
            skLineSegment(sketch, "E14.0.31.0", {"start": v(117, 212) * mm, "end": v(117, 222) * mm});
            skLineSegment(sketch, "E14.0.31.1", {"start": v(107, 212) * mm, "end": v(107, 222) * mm});
            skLineSegment(sketch, "E14.0.31.2", {"start": v(107, 222) * mm, "end": v(117, 222) * mm});
            skLineSegment(sketch, "E14.0.31.3", {"start": v(107, 212) * mm, "end": v(117, 212) * mm});
            skLineSegment(sketch, "E14.1.0.0", {"start": v(131, -222) * mm, "end": v(131, -212) * mm});
            skLineSegment(sketch, "E14.1.0.1", {"start": v(121, -222) * mm, "end": v(121, -212) * mm});
            skLineSegment(sketch, "E14.1.0.2", {"start": v(121, -212) * mm, "end": v(131, -212) * mm});
            skLineSegment(sketch, "E14.1.0.3", {"start": v(121, -222) * mm, "end": v(131, -222) * mm});
            skLineSegment(sketch, "E14.1.1.0", {"start": v(131, -208) * mm, "end": v(131, -198) * mm});
            skLineSegment(sketch, "E14.1.1.1", {"start": v(121, -208) * mm, "end": v(121, -198) * mm});
            skLineSegment(sketch, "E14.1.1.2", {"start": v(121, -198) * mm, "end": v(131, -198) * mm});
            skLineSegment(sketch, "E14.1.1.3", {"start": v(121, -208) * mm, "end": v(131, -208) * mm});
            skLineSegment(sketch, "E14.1.2.0", {"start": v(131, -194) * mm, "end": v(131, -184) * mm});
            skLineSegment(sketch, "E14.1.2.1", {"start": v(121, -194) * mm, "end": v(121, -184) * mm});
            skLineSegment(sketch, "E14.1.2.2", {"start": v(121, -184) * mm, "end": v(131, -184) * mm});
            skLineSegment(sketch, "E14.1.2.3", {"start": v(121, -194) * mm, "end": v(131, -194) * mm});
            skLineSegment(sketch, "E14.1.3.0", {"start": v(131, -180) * mm, "end": v(131, -170) * mm});
            skLineSegment(sketch, "E14.1.3.1", {"start": v(121, -180) * mm, "end": v(121, -170) * mm});
            skLineSegment(sketch, "E14.1.3.2", {"start": v(121, -170) * mm, "end": v(131, -170) * mm});
            skLineSegment(sketch, "E14.1.3.3", {"start": v(121, -180) * mm, "end": v(131, -180) * mm});
            skLineSegment(sketch, "E14.1.4.0", {"start": v(131, -166) * mm, "end": v(131, -156) * mm});
            skLineSegment(sketch, "E14.1.4.1", {"start": v(121, -166) * mm, "end": v(121, -156) * mm});
            skLineSegment(sketch, "E14.1.4.2", {"start": v(121, -156) * mm, "end": v(131, -156) * mm});
            skLineSegment(sketch, "E14.1.4.3", {"start": v(121, -166) * mm, "end": v(131, -166) * mm});
            skLineSegment(sketch, "E14.1.5.0", {"start": v(131, -152) * mm, "end": v(131, -142) * mm});
            skLineSegment(sketch, "E14.1.5.1", {"start": v(121, -152) * mm, "end": v(121, -142) * mm});
            skLineSegment(sketch, "E14.1.5.2", {"start": v(121, -142) * mm, "end": v(131, -142) * mm});
            skLineSegment(sketch, "E14.1.5.3", {"start": v(121, -152) * mm, "end": v(131, -152) * mm});
            skLineSegment(sketch, "E14.1.6.0", {"start": v(131, -138) * mm, "end": v(131, -128) * mm});
            skLineSegment(sketch, "E14.1.6.1", {"start": v(121, -138) * mm, "end": v(121, -128) * mm});
            skLineSegment(sketch, "E14.1.6.2", {"start": v(121, -128) * mm, "end": v(131, -128) * mm});
            skLineSegment(sketch, "E14.1.6.3", {"start": v(121, -138) * mm, "end": v(131, -138) * mm});
            skLineSegment(sketch, "E14.1.7.0", {"start": v(131, -124) * mm, "end": v(131, -114) * mm});
            skLineSegment(sketch, "E14.1.7.1", {"start": v(121, -124) * mm, "end": v(121, -114) * mm});
            skLineSegment(sketch, "E14.1.7.2", {"start": v(121, -114) * mm, "end": v(131, -114) * mm});
            skLineSegment(sketch, "E14.1.7.3", {"start": v(121, -124) * mm, "end": v(131, -124) * mm});
            skLineSegment(sketch, "E14.1.8.0", {"start": v(131, -110) * mm, "end": v(131, -100) * mm});
            skLineSegment(sketch, "E14.1.8.1", {"start": v(121, -110) * mm, "end": v(121, -100) * mm});
            skLineSegment(sketch, "E14.1.8.2", {"start": v(121, -100) * mm, "end": v(131, -100) * mm});
            skLineSegment(sketch, "E14.1.8.3", {"start": v(121, -110) * mm, "end": v(131, -110) * mm});
            skLineSegment(sketch, "E14.1.9.0", {"start": v(131, -96) * mm, "end": v(131, -86) * mm});
            skLineSegment(sketch, "E14.1.9.1", {"start": v(121, -96) * mm, "end": v(121, -86) * mm});
            skLineSegment(sketch, "E14.1.9.2", {"start": v(121, -86) * mm, "end": v(131, -86) * mm});
            skLineSegment(sketch, "E14.1.9.3", {"start": v(121, -96) * mm, "end": v(131, -96) * mm});
            skLineSegment(sketch, "E14.1.10.0", {"start": v(131, -82) * mm, "end": v(131, -72) * mm});
            skLineSegment(sketch, "E14.1.10.1", {"start": v(121, -82) * mm, "end": v(121, -72) * mm});
            skLineSegment(sketch, "E14.1.10.2", {"start": v(121, -72) * mm, "end": v(131, -72) * mm});
            skLineSegment(sketch, "E14.1.10.3", {"start": v(121, -82) * mm, "end": v(131, -82) * mm});
            skLineSegment(sketch, "E14.1.11.0", {"start": v(131, -68) * mm, "end": v(131, -58) * mm});
            skLineSegment(sketch, "E14.1.11.1", {"start": v(121, -68) * mm, "end": v(121, -58) * mm});
            skLineSegment(sketch, "E14.1.11.2", {"start": v(121, -58) * mm, "end": v(131, -58) * mm});
            skLineSegment(sketch, "E14.1.11.3", {"start": v(121, -68) * mm, "end": v(131, -68) * mm});
            skLineSegment(sketch, "E14.1.12.0", {"start": v(131, -54) * mm, "end": v(131, -44) * mm});
            skLineSegment(sketch, "E14.1.12.1", {"start": v(121, -54) * mm, "end": v(121, -44) * mm});
            skLineSegment(sketch, "E14.1.12.2", {"start": v(121, -44) * mm, "end": v(131, -44) * mm});
            skLineSegment(sketch, "E14.1.12.3", {"start": v(121, -54) * mm, "end": v(131, -54) * mm});
            skLineSegment(sketch, "E14.1.13.0", {"start": v(131, -40) * mm, "end": v(131, -30) * mm});
            skLineSegment(sketch, "E14.1.13.1", {"start": v(121, -40) * mm, "end": v(121, -30) * mm});
            skLineSegment(sketch, "E14.1.13.2", {"start": v(121, -30) * mm, "end": v(131, -30) * mm});
            skLineSegment(sketch, "E14.1.13.3", {"start": v(121, -40) * mm, "end": v(131, -40) * mm});
            skLineSegment(sketch, "E14.1.14.0", {"start": v(131, -26) * mm, "end": v(131, -16) * mm});
            skLineSegment(sketch, "E14.1.14.1", {"start": v(121, -26) * mm, "end": v(121, -16) * mm});
            skLineSegment(sketch, "E14.1.14.2", {"start": v(121, -16) * mm, "end": v(131, -16) * mm});
            skLineSegment(sketch, "E14.1.14.3", {"start": v(121, -26) * mm, "end": v(131, -26) * mm});
            skLineSegment(sketch, "E14.1.15.0", {"start": v(131, -12) * mm, "end": v(131, -2) * mm});
            skLineSegment(sketch, "E14.1.15.1", {"start": v(121, -12) * mm, "end": v(121, -2) * mm});
            skLineSegment(sketch, "E14.1.15.2", {"start": v(121, -2) * mm, "end": v(131, -2) * mm});
            skLineSegment(sketch, "E14.1.15.3", {"start": v(121, -12) * mm, "end": v(131, -12) * mm});
            skLineSegment(sketch, "E14.1.16.0", {"start": v(131, 2) * mm, "end": v(131, 12) * mm});
            skLineSegment(sketch, "E14.1.16.1", {"start": v(121, 2) * mm, "end": v(121, 12) * mm});
            skLineSegment(sketch, "E14.1.16.2", {"start": v(121, 12) * mm, "end": v(131, 12) * mm});
            skLineSegment(sketch, "E14.1.16.3", {"start": v(121, 2) * mm, "end": v(131, 2) * mm});
            skLineSegment(sketch, "E14.1.17.0", {"start": v(131, 16) * mm, "end": v(131, 26) * mm});
            skLineSegment(sketch, "E14.1.17.1", {"start": v(121, 16) * mm, "end": v(121, 26) * mm});
            skLineSegment(sketch, "E14.1.17.2", {"start": v(121, 26) * mm, "end": v(131, 26) * mm});
            skLineSegment(sketch, "E14.1.17.3", {"start": v(121, 16) * mm, "end": v(131, 16) * mm});
            skLineSegment(sketch, "E14.1.18.0", {"start": v(131, 30) * mm, "end": v(131, 40) * mm});
            skLineSegment(sketch, "E14.1.18.1", {"start": v(121, 30) * mm, "end": v(121, 40) * mm});
            skLineSegment(sketch, "E14.1.18.2", {"start": v(121, 40) * mm, "end": v(131, 40) * mm});
            skLineSegment(sketch, "E14.1.18.3", {"start": v(121, 30) * mm, "end": v(131, 30) * mm});
            skLineSegment(sketch, "E14.1.19.0", {"start": v(131, 44) * mm, "end": v(131, 54) * mm});
            skLineSegment(sketch, "E14.1.19.1", {"start": v(121, 44) * mm, "end": v(121, 54) * mm});
            skLineSegment(sketch, "E14.1.19.2", {"start": v(121, 54) * mm, "end": v(131, 54) * mm});
            skLineSegment(sketch, "E14.1.19.3", {"start": v(121, 44) * mm, "end": v(131, 44) * mm});
            skLineSegment(sketch, "E14.1.20.0", {"start": v(131, 58) * mm, "end": v(131, 68) * mm});
            skLineSegment(sketch, "E14.1.20.1", {"start": v(121, 58) * mm, "end": v(121, 68) * mm});
            skLineSegment(sketch, "E14.1.20.2", {"start": v(121, 68) * mm, "end": v(131, 68) * mm});
            skLineSegment(sketch, "E14.1.20.3", {"start": v(121, 58) * mm, "end": v(131, 58) * mm});
            skLineSegment(sketch, "E14.1.21.0", {"start": v(131, 72) * mm, "end": v(131, 82) * mm});
            skLineSegment(sketch, "E14.1.21.1", {"start": v(121, 72) * mm, "end": v(121, 82) * mm});
            skLineSegment(sketch, "E14.1.21.2", {"start": v(121, 82) * mm, "end": v(131, 82) * mm});
            skLineSegment(sketch, "E14.1.21.3", {"start": v(121, 72) * mm, "end": v(131, 72) * mm});
            skLineSegment(sketch, "E14.1.22.0", {"start": v(131, 86) * mm, "end": v(131, 96) * mm});
            skLineSegment(sketch, "E14.1.22.1", {"start": v(121, 86) * mm, "end": v(121, 96) * mm});
            skLineSegment(sketch, "E14.1.22.2", {"start": v(121, 96) * mm, "end": v(131, 96) * mm});
            skLineSegment(sketch, "E14.1.22.3", {"start": v(121, 86) * mm, "end": v(131, 86) * mm});
            skLineSegment(sketch, "E14.1.23.0", {"start": v(131, 100) * mm, "end": v(131, 110) * mm});
            skLineSegment(sketch, "E14.1.23.1", {"start": v(121, 100) * mm, "end": v(121, 110) * mm});
            skLineSegment(sketch, "E14.1.23.2", {"start": v(121, 110) * mm, "end": v(131, 110) * mm});
            skLineSegment(sketch, "E14.1.23.3", {"start": v(121, 100) * mm, "end": v(131, 100) * mm});
            skLineSegment(sketch, "E14.1.24.0", {"start": v(131, 114) * mm, "end": v(131, 124) * mm});
            skLineSegment(sketch, "E14.1.24.1", {"start": v(121, 114) * mm, "end": v(121, 124) * mm});
            skLineSegment(sketch, "E14.1.24.2", {"start": v(121, 124) * mm, "end": v(131, 124) * mm});
            skLineSegment(sketch, "E14.1.24.3", {"start": v(121, 114) * mm, "end": v(131, 114) * mm});
            skLineSegment(sketch, "E14.1.25.0", {"start": v(131, 128) * mm, "end": v(131, 138) * mm});
            skLineSegment(sketch, "E14.1.25.1", {"start": v(121, 128) * mm, "end": v(121, 138) * mm});
            skLineSegment(sketch, "E14.1.25.2", {"start": v(121, 138) * mm, "end": v(131, 138) * mm});
            skLineSegment(sketch, "E14.1.25.3", {"start": v(121, 128) * mm, "end": v(131, 128) * mm});
            skLineSegment(sketch, "E14.1.26.0", {"start": v(131, 142) * mm, "end": v(131, 152) * mm});
            skLineSegment(sketch, "E14.1.26.1", {"start": v(121, 142) * mm, "end": v(121, 152) * mm});
            skLineSegment(sketch, "E14.1.26.2", {"start": v(121, 152) * mm, "end": v(131, 152) * mm});
            skLineSegment(sketch, "E14.1.26.3", {"start": v(121, 142) * mm, "end": v(131, 142) * mm});
            skLineSegment(sketch, "E14.1.27.0", {"start": v(131, 156) * mm, "end": v(131, 166) * mm});
            skLineSegment(sketch, "E14.1.27.1", {"start": v(121, 156) * mm, "end": v(121, 166) * mm});
            skLineSegment(sketch, "E14.1.27.2", {"start": v(121, 166) * mm, "end": v(131, 166) * mm});
            skLineSegment(sketch, "E14.1.27.3", {"start": v(121, 156) * mm, "end": v(131, 156) * mm});
            skLineSegment(sketch, "E14.1.28.0", {"start": v(131, 170) * mm, "end": v(131, 180) * mm});
            skLineSegment(sketch, "E14.1.28.1", {"start": v(121, 170) * mm, "end": v(121, 180) * mm});
            skLineSegment(sketch, "E14.1.28.2", {"start": v(121, 180) * mm, "end": v(131, 180) * mm});
            skLineSegment(sketch, "E14.1.28.3", {"start": v(121, 170) * mm, "end": v(131, 170) * mm});
            skLineSegment(sketch, "E14.1.29.0", {"start": v(131, 184) * mm, "end": v(131, 194) * mm});
            skLineSegment(sketch, "E14.1.29.1", {"start": v(121, 184) * mm, "end": v(121, 194) * mm});
            skLineSegment(sketch, "E14.1.29.2", {"start": v(121, 194) * mm, "end": v(131, 194) * mm});
            skLineSegment(sketch, "E14.1.29.3", {"start": v(121, 184) * mm, "end": v(131, 184) * mm});
            skLineSegment(sketch, "E14.1.30.0", {"start": v(131, 198) * mm, "end": v(131, 208) * mm});
            skLineSegment(sketch, "E14.1.30.1", {"start": v(121, 198) * mm, "end": v(121, 208) * mm});
            skLineSegment(sketch, "E14.1.30.2", {"start": v(121, 208) * mm, "end": v(131, 208) * mm});
            skLineSegment(sketch, "E14.1.30.3", {"start": v(121, 198) * mm, "end": v(131, 198) * mm});
            skLineSegment(sketch, "E14.1.31.0", {"start": v(131, 212) * mm, "end": v(131, 222) * mm});
            skLineSegment(sketch, "E14.1.31.1", {"start": v(121, 212) * mm, "end": v(121, 222) * mm});
            skLineSegment(sketch, "E14.1.31.2", {"start": v(121, 222) * mm, "end": v(131, 222) * mm});
            skLineSegment(sketch, "E14.1.31.3", {"start": v(121, 212) * mm, "end": v(131, 212) * mm});
            skLineSegment(sketch, "E14.2.0.0", {"start": v(145, -222) * mm, "end": v(145, -212) * mm});
            skLineSegment(sketch, "E14.2.0.1", {"start": v(135, -222) * mm, "end": v(135, -212) * mm});
            skLineSegment(sketch, "E14.2.0.2", {"start": v(135, -212) * mm, "end": v(145, -212) * mm});
            skLineSegment(sketch, "E14.2.0.3", {"start": v(135, -222) * mm, "end": v(145, -222) * mm});
            skLineSegment(sketch, "E14.2.1.0", {"start": v(145, -208) * mm, "end": v(145, -198) * mm});
            skLineSegment(sketch, "E14.2.1.1", {"start": v(135, -208) * mm, "end": v(135, -198) * mm});
            skLineSegment(sketch, "E14.2.1.2", {"start": v(135, -198) * mm, "end": v(145, -198) * mm});
            skLineSegment(sketch, "E14.2.1.3", {"start": v(135, -208) * mm, "end": v(145, -208) * mm});
            skLineSegment(sketch, "E14.2.2.0", {"start": v(145, -194) * mm, "end": v(145, -184) * mm});
            skLineSegment(sketch, "E14.2.2.1", {"start": v(135, -194) * mm, "end": v(135, -184) * mm});
            skLineSegment(sketch, "E14.2.2.2", {"start": v(135, -184) * mm, "end": v(145, -184) * mm});
            skLineSegment(sketch, "E14.2.2.3", {"start": v(135, -194) * mm, "end": v(145, -194) * mm});
            skLineSegment(sketch, "E14.2.3.0", {"start": v(145, -180) * mm, "end": v(145, -170) * mm});
            skLineSegment(sketch, "E14.2.3.1", {"start": v(135, -180) * mm, "end": v(135, -170) * mm});
            skLineSegment(sketch, "E14.2.3.2", {"start": v(135, -170) * mm, "end": v(145, -170) * mm});
            skLineSegment(sketch, "E14.2.3.3", {"start": v(135, -180) * mm, "end": v(145, -180) * mm});
            skLineSegment(sketch, "E14.2.4.0", {"start": v(145, -166) * mm, "end": v(145, -156) * mm});
            skLineSegment(sketch, "E14.2.4.1", {"start": v(135, -166) * mm, "end": v(135, -156) * mm});
            skLineSegment(sketch, "E14.2.4.2", {"start": v(135, -156) * mm, "end": v(145, -156) * mm});
            skLineSegment(sketch, "E14.2.4.3", {"start": v(135, -166) * mm, "end": v(145, -166) * mm});
            skLineSegment(sketch, "E14.2.5.0", {"start": v(145, -152) * mm, "end": v(145, -142) * mm});
            skLineSegment(sketch, "E14.2.5.1", {"start": v(135, -152) * mm, "end": v(135, -142) * mm});
            skLineSegment(sketch, "E14.2.5.2", {"start": v(135, -142) * mm, "end": v(145, -142) * mm});
            skLineSegment(sketch, "E14.2.5.3", {"start": v(135, -152) * mm, "end": v(145, -152) * mm});
            skLineSegment(sketch, "E14.2.6.0", {"start": v(145, -138) * mm, "end": v(145, -128) * mm});
            skLineSegment(sketch, "E14.2.6.1", {"start": v(135, -138) * mm, "end": v(135, -128) * mm});
            skLineSegment(sketch, "E14.2.6.2", {"start": v(135, -128) * mm, "end": v(145, -128) * mm});
            skLineSegment(sketch, "E14.2.6.3", {"start": v(135, -138) * mm, "end": v(145, -138) * mm});
            skLineSegment(sketch, "E14.2.7.0", {"start": v(145, -124) * mm, "end": v(145, -114) * mm});
            skLineSegment(sketch, "E14.2.7.1", {"start": v(135, -124) * mm, "end": v(135, -114) * mm});
            skLineSegment(sketch, "E14.2.7.2", {"start": v(135, -114) * mm, "end": v(145, -114) * mm});
            skLineSegment(sketch, "E14.2.7.3", {"start": v(135, -124) * mm, "end": v(145, -124) * mm});
            skLineSegment(sketch, "E14.2.8.0", {"start": v(145, -110) * mm, "end": v(145, -100) * mm});
            skLineSegment(sketch, "E14.2.8.1", {"start": v(135, -110) * mm, "end": v(135, -100) * mm});
            skLineSegment(sketch, "E14.2.8.2", {"start": v(135, -100) * mm, "end": v(145, -100) * mm});
            skLineSegment(sketch, "E14.2.8.3", {"start": v(135, -110) * mm, "end": v(145, -110) * mm});
            skLineSegment(sketch, "E14.2.9.0", {"start": v(145, -96) * mm, "end": v(145, -86) * mm});
            skLineSegment(sketch, "E14.2.9.1", {"start": v(135, -96) * mm, "end": v(135, -86) * mm});
            skLineSegment(sketch, "E14.2.9.2", {"start": v(135, -86) * mm, "end": v(145, -86) * mm});
            skLineSegment(sketch, "E14.2.9.3", {"start": v(135, -96) * mm, "end": v(145, -96) * mm});
            skLineSegment(sketch, "E14.2.10.0", {"start": v(145, -82) * mm, "end": v(145, -72) * mm});
            skLineSegment(sketch, "E14.2.10.1", {"start": v(135, -82) * mm, "end": v(135, -72) * mm});
            skLineSegment(sketch, "E14.2.10.2", {"start": v(135, -72) * mm, "end": v(145, -72) * mm});
            skLineSegment(sketch, "E14.2.10.3", {"start": v(135, -82) * mm, "end": v(145, -82) * mm});
            skLineSegment(sketch, "E14.2.11.0", {"start": v(145, -68) * mm, "end": v(145, -58) * mm});
            skLineSegment(sketch, "E14.2.11.1", {"start": v(135, -68) * mm, "end": v(135, -58) * mm});
            skLineSegment(sketch, "E14.2.11.2", {"start": v(135, -58) * mm, "end": v(145, -58) * mm});
            skLineSegment(sketch, "E14.2.11.3", {"start": v(135, -68) * mm, "end": v(145, -68) * mm});
            skLineSegment(sketch, "E14.2.12.0", {"start": v(145, -54) * mm, "end": v(145, -44) * mm});
            skLineSegment(sketch, "E14.2.12.1", {"start": v(135, -54) * mm, "end": v(135, -44) * mm});
            skLineSegment(sketch, "E14.2.12.2", {"start": v(135, -44) * mm, "end": v(145, -44) * mm});
            skLineSegment(sketch, "E14.2.12.3", {"start": v(135, -54) * mm, "end": v(145, -54) * mm});
            skLineSegment(sketch, "E14.2.13.0", {"start": v(145, -40) * mm, "end": v(145, -30) * mm});
            skLineSegment(sketch, "E14.2.13.1", {"start": v(135, -40) * mm, "end": v(135, -30) * mm});
            skLineSegment(sketch, "E14.2.13.2", {"start": v(135, -30) * mm, "end": v(145, -30) * mm});
            skLineSegment(sketch, "E14.2.13.3", {"start": v(135, -40) * mm, "end": v(145, -40) * mm});
            skLineSegment(sketch, "E14.2.14.0", {"start": v(145, -26) * mm, "end": v(145, -16) * mm});
            skLineSegment(sketch, "E14.2.14.1", {"start": v(135, -26) * mm, "end": v(135, -16) * mm});
            skLineSegment(sketch, "E14.2.14.2", {"start": v(135, -16) * mm, "end": v(145, -16) * mm});
            skLineSegment(sketch, "E14.2.14.3", {"start": v(135, -26) * mm, "end": v(145, -26) * mm});
            skLineSegment(sketch, "E14.2.15.0", {"start": v(145, -12) * mm, "end": v(145, -2) * mm});
            skLineSegment(sketch, "E14.2.15.1", {"start": v(135, -12) * mm, "end": v(135, -2) * mm});
            skLineSegment(sketch, "E14.2.15.2", {"start": v(135, -2) * mm, "end": v(145, -2) * mm});
            skLineSegment(sketch, "E14.2.15.3", {"start": v(135, -12) * mm, "end": v(145, -12) * mm});
            skLineSegment(sketch, "E14.2.16.0", {"start": v(145, 2) * mm, "end": v(145, 12) * mm});
            skLineSegment(sketch, "E14.2.16.1", {"start": v(135, 2) * mm, "end": v(135, 12) * mm});
            skLineSegment(sketch, "E14.2.16.2", {"start": v(135, 12) * mm, "end": v(145, 12) * mm});
            skLineSegment(sketch, "E14.2.16.3", {"start": v(135, 2) * mm, "end": v(145, 2) * mm});
            skLineSegment(sketch, "E14.2.17.0", {"start": v(145, 16) * mm, "end": v(145, 26) * mm});
            skLineSegment(sketch, "E14.2.17.1", {"start": v(135, 16) * mm, "end": v(135, 26) * mm});
            skLineSegment(sketch, "E14.2.17.2", {"start": v(135, 26) * mm, "end": v(145, 26) * mm});
            skLineSegment(sketch, "E14.2.17.3", {"start": v(135, 16) * mm, "end": v(145, 16) * mm});
            skLineSegment(sketch, "E14.2.18.0", {"start": v(145, 30) * mm, "end": v(145, 40) * mm});
            skLineSegment(sketch, "E14.2.18.1", {"start": v(135, 30) * mm, "end": v(135, 40) * mm});
            skLineSegment(sketch, "E14.2.18.2", {"start": v(135, 40) * mm, "end": v(145, 40) * mm});
            skLineSegment(sketch, "E14.2.18.3", {"start": v(135, 30) * mm, "end": v(145, 30) * mm});
            skLineSegment(sketch, "E14.2.19.0", {"start": v(145, 44) * mm, "end": v(145, 54) * mm});
            skLineSegment(sketch, "E14.2.19.1", {"start": v(135, 44) * mm, "end": v(135, 54) * mm});
            skLineSegment(sketch, "E14.2.19.2", {"start": v(135, 54) * mm, "end": v(145, 54) * mm});
            skLineSegment(sketch, "E14.2.19.3", {"start": v(135, 44) * mm, "end": v(145, 44) * mm});
            skLineSegment(sketch, "E14.2.20.0", {"start": v(145, 58) * mm, "end": v(145, 68) * mm});
            skLineSegment(sketch, "E14.2.20.1", {"start": v(135, 58) * mm, "end": v(135, 68) * mm});
            skLineSegment(sketch, "E14.2.20.2", {"start": v(135, 68) * mm, "end": v(145, 68) * mm});
            skLineSegment(sketch, "E14.2.20.3", {"start": v(135, 58) * mm, "end": v(145, 58) * mm});
            skLineSegment(sketch, "E14.2.21.0", {"start": v(145, 72) * mm, "end": v(145, 82) * mm});
            skLineSegment(sketch, "E14.2.21.1", {"start": v(135, 72) * mm, "end": v(135, 82) * mm});
            skLineSegment(sketch, "E14.2.21.2", {"start": v(135, 82) * mm, "end": v(145, 82) * mm});
            skLineSegment(sketch, "E14.2.21.3", {"start": v(135, 72) * mm, "end": v(145, 72) * mm});
            skLineSegment(sketch, "E14.2.22.0", {"start": v(145, 86) * mm, "end": v(145, 96) * mm});
            skLineSegment(sketch, "E14.2.22.1", {"start": v(135, 86) * mm, "end": v(135, 96) * mm});
            skLineSegment(sketch, "E14.2.22.2", {"start": v(135, 96) * mm, "end": v(145, 96) * mm});
            skLineSegment(sketch, "E14.2.22.3", {"start": v(135, 86) * mm, "end": v(145, 86) * mm});
            skLineSegment(sketch, "E14.2.23.0", {"start": v(145, 100) * mm, "end": v(145, 110) * mm});
            skLineSegment(sketch, "E14.2.23.1", {"start": v(135, 100) * mm, "end": v(135, 110) * mm});
            skLineSegment(sketch, "E14.2.23.2", {"start": v(135, 110) * mm, "end": v(145, 110) * mm});
            skLineSegment(sketch, "E14.2.23.3", {"start": v(135, 100) * mm, "end": v(145, 100) * mm});
            skLineSegment(sketch, "E14.2.24.0", {"start": v(145, 114) * mm, "end": v(145, 124) * mm});
            skLineSegment(sketch, "E14.2.24.1", {"start": v(135, 114) * mm, "end": v(135, 124) * mm});
            skLineSegment(sketch, "E14.2.24.2", {"start": v(135, 124) * mm, "end": v(145, 124) * mm});
            skLineSegment(sketch, "E14.2.24.3", {"start": v(135, 114) * mm, "end": v(145, 114) * mm});
            skLineSegment(sketch, "E14.2.25.0", {"start": v(145, 128) * mm, "end": v(145, 138) * mm});
            skLineSegment(sketch, "E14.2.25.1", {"start": v(135, 128) * mm, "end": v(135, 138) * mm});
            skLineSegment(sketch, "E14.2.25.2", {"start": v(135, 138) * mm, "end": v(145, 138) * mm});
            skLineSegment(sketch, "E14.2.25.3", {"start": v(135, 128) * mm, "end": v(145, 128) * mm});
            skLineSegment(sketch, "E14.2.26.0", {"start": v(145, 142) * mm, "end": v(145, 152) * mm});
            skLineSegment(sketch, "E14.2.26.1", {"start": v(135, 142) * mm, "end": v(135, 152) * mm});
            skLineSegment(sketch, "E14.2.26.2", {"start": v(135, 152) * mm, "end": v(145, 152) * mm});
            skLineSegment(sketch, "E14.2.26.3", {"start": v(135, 142) * mm, "end": v(145, 142) * mm});
            skLineSegment(sketch, "E14.2.27.0", {"start": v(145, 156) * mm, "end": v(145, 166) * mm});
            skLineSegment(sketch, "E14.2.27.1", {"start": v(135, 156) * mm, "end": v(135, 166) * mm});
            skLineSegment(sketch, "E14.2.27.2", {"start": v(135, 166) * mm, "end": v(145, 166) * mm});
            skLineSegment(sketch, "E14.2.27.3", {"start": v(135, 156) * mm, "end": v(145, 156) * mm});
            skLineSegment(sketch, "E14.2.28.0", {"start": v(145, 170) * mm, "end": v(145, 180) * mm});
            skLineSegment(sketch, "E14.2.28.1", {"start": v(135, 170) * mm, "end": v(135, 180) * mm});
            skLineSegment(sketch, "E14.2.28.2", {"start": v(135, 180) * mm, "end": v(145, 180) * mm});
            skLineSegment(sketch, "E14.2.28.3", {"start": v(135, 170) * mm, "end": v(145, 170) * mm});
            skLineSegment(sketch, "E14.2.29.0", {"start": v(145, 184) * mm, "end": v(145, 194) * mm});
            skLineSegment(sketch, "E14.2.29.1", {"start": v(135, 184) * mm, "end": v(135, 194) * mm});
            skLineSegment(sketch, "E14.2.29.2", {"start": v(135, 194) * mm, "end": v(145, 194) * mm});
            skLineSegment(sketch, "E14.2.29.3", {"start": v(135, 184) * mm, "end": v(145, 184) * mm});
            skLineSegment(sketch, "E14.2.30.0", {"start": v(145, 198) * mm, "end": v(145, 208) * mm});
            skLineSegment(sketch, "E14.2.30.1", {"start": v(135, 198) * mm, "end": v(135, 208) * mm});
            skLineSegment(sketch, "E14.2.30.2", {"start": v(135, 208) * mm, "end": v(145, 208) * mm});
            skLineSegment(sketch, "E14.2.30.3", {"start": v(135, 198) * mm, "end": v(145, 198) * mm});
            skLineSegment(sketch, "E14.2.31.0", {"start": v(145, 212) * mm, "end": v(145, 222) * mm});
            skLineSegment(sketch, "E14.2.31.1", {"start": v(135, 212) * mm, "end": v(135, 222) * mm});
            skLineSegment(sketch, "E14.2.31.2", {"start": v(135, 222) * mm, "end": v(145, 222) * mm});
            skLineSegment(sketch, "E14.2.31.3", {"start": v(135, 212) * mm, "end": v(145, 212) * mm});
            skLineSegment(sketch, "E14.3.0.0", {"start": v(159, -222) * mm, "end": v(159, -212) * mm});
            skLineSegment(sketch, "E14.3.0.1", {"start": v(149, -222) * mm, "end": v(149, -212) * mm});
            skLineSegment(sketch, "E14.3.0.2", {"start": v(149, -212) * mm, "end": v(159, -212) * mm});
            skLineSegment(sketch, "E14.3.0.3", {"start": v(149, -222) * mm, "end": v(159, -222) * mm});
            skLineSegment(sketch, "E14.3.1.0", {"start": v(159, -208) * mm, "end": v(159, -198) * mm});
            skLineSegment(sketch, "E14.3.1.1", {"start": v(149, -208) * mm, "end": v(149, -198) * mm});
            skLineSegment(sketch, "E14.3.1.2", {"start": v(149, -198) * mm, "end": v(159, -198) * mm});
            skLineSegment(sketch, "E14.3.1.3", {"start": v(149, -208) * mm, "end": v(159, -208) * mm});
            skLineSegment(sketch, "E14.3.2.0", {"start": v(159, -194) * mm, "end": v(159, -184) * mm});
            skLineSegment(sketch, "E14.3.2.1", {"start": v(149, -194) * mm, "end": v(149, -184) * mm});
            skLineSegment(sketch, "E14.3.2.2", {"start": v(149, -184) * mm, "end": v(159, -184) * mm});
            skLineSegment(sketch, "E14.3.2.3", {"start": v(149, -194) * mm, "end": v(159, -194) * mm});
            skLineSegment(sketch, "E14.3.3.0", {"start": v(159, -180) * mm, "end": v(159, -170) * mm});
            skLineSegment(sketch, "E14.3.3.1", {"start": v(149, -180) * mm, "end": v(149, -170) * mm});
            skLineSegment(sketch, "E14.3.3.2", {"start": v(149, -170) * mm, "end": v(159, -170) * mm});
            skLineSegment(sketch, "E14.3.3.3", {"start": v(149, -180) * mm, "end": v(159, -180) * mm});
            skLineSegment(sketch, "E14.3.4.0", {"start": v(159, -166) * mm, "end": v(159, -156) * mm});
            skLineSegment(sketch, "E14.3.4.1", {"start": v(149, -166) * mm, "end": v(149, -156) * mm});
            skLineSegment(sketch, "E14.3.4.2", {"start": v(149, -156) * mm, "end": v(159, -156) * mm});
            skLineSegment(sketch, "E14.3.4.3", {"start": v(149, -166) * mm, "end": v(159, -166) * mm});
            skLineSegment(sketch, "E14.3.5.0", {"start": v(159, -152) * mm, "end": v(159, -142) * mm});
            skLineSegment(sketch, "E14.3.5.1", {"start": v(149, -152) * mm, "end": v(149, -142) * mm});
            skLineSegment(sketch, "E14.3.5.2", {"start": v(149, -142) * mm, "end": v(159, -142) * mm});
            skLineSegment(sketch, "E14.3.5.3", {"start": v(149, -152) * mm, "end": v(159, -152) * mm});
            skLineSegment(sketch, "E14.3.6.0", {"start": v(159, -138) * mm, "end": v(159, -128) * mm});
            skLineSegment(sketch, "E14.3.6.1", {"start": v(149, -138) * mm, "end": v(149, -128) * mm});
            skLineSegment(sketch, "E14.3.6.2", {"start": v(149, -128) * mm, "end": v(159, -128) * mm});
            skLineSegment(sketch, "E14.3.6.3", {"start": v(149, -138) * mm, "end": v(159, -138) * mm});
            skLineSegment(sketch, "E14.3.7.0", {"start": v(159, -124) * mm, "end": v(159, -114) * mm});
            skLineSegment(sketch, "E14.3.7.1", {"start": v(149, -124) * mm, "end": v(149, -114) * mm});
            skLineSegment(sketch, "E14.3.7.2", {"start": v(149, -114) * mm, "end": v(159, -114) * mm});
            skLineSegment(sketch, "E14.3.7.3", {"start": v(149, -124) * mm, "end": v(159, -124) * mm});
            skLineSegment(sketch, "E14.3.8.0", {"start": v(159, -110) * mm, "end": v(159, -100) * mm});
            skLineSegment(sketch, "E14.3.8.1", {"start": v(149, -110) * mm, "end": v(149, -100) * mm});
            skLineSegment(sketch, "E14.3.8.2", {"start": v(149, -100) * mm, "end": v(159, -100) * mm});
            skLineSegment(sketch, "E14.3.8.3", {"start": v(149, -110) * mm, "end": v(159, -110) * mm});
            skLineSegment(sketch, "E14.3.9.0", {"start": v(159, -96) * mm, "end": v(159, -86) * mm});
            skLineSegment(sketch, "E14.3.9.1", {"start": v(149, -96) * mm, "end": v(149, -86) * mm});
            skLineSegment(sketch, "E14.3.9.2", {"start": v(149, -86) * mm, "end": v(159, -86) * mm});
            skLineSegment(sketch, "E14.3.9.3", {"start": v(149, -96) * mm, "end": v(159, -96) * mm});
            skLineSegment(sketch, "E14.3.10.0", {"start": v(159, -82) * mm, "end": v(159, -72) * mm});
            skLineSegment(sketch, "E14.3.10.1", {"start": v(149, -82) * mm, "end": v(149, -72) * mm});
            skLineSegment(sketch, "E14.3.10.2", {"start": v(149, -72) * mm, "end": v(159, -72) * mm});
            skLineSegment(sketch, "E14.3.10.3", {"start": v(149, -82) * mm, "end": v(159, -82) * mm});
            skLineSegment(sketch, "E14.3.11.0", {"start": v(159, -68) * mm, "end": v(159, -58) * mm});
            skLineSegment(sketch, "E14.3.11.1", {"start": v(149, -68) * mm, "end": v(149, -58) * mm});
            skLineSegment(sketch, "E14.3.11.2", {"start": v(149, -58) * mm, "end": v(159, -58) * mm});
            skLineSegment(sketch, "E14.3.11.3", {"start": v(149, -68) * mm, "end": v(159, -68) * mm});
            skLineSegment(sketch, "E14.3.12.0", {"start": v(159, -54) * mm, "end": v(159, -44) * mm});
            skLineSegment(sketch, "E14.3.12.1", {"start": v(149, -54) * mm, "end": v(149, -44) * mm});
            skLineSegment(sketch, "E14.3.12.2", {"start": v(149, -44) * mm, "end": v(159, -44) * mm});
            skLineSegment(sketch, "E14.3.12.3", {"start": v(149, -54) * mm, "end": v(159, -54) * mm});
            skLineSegment(sketch, "E14.3.13.0", {"start": v(159, -40) * mm, "end": v(159, -30) * mm});
            skLineSegment(sketch, "E14.3.13.1", {"start": v(149, -40) * mm, "end": v(149, -30) * mm});
            skLineSegment(sketch, "E14.3.13.2", {"start": v(149, -30) * mm, "end": v(159, -30) * mm});
            skLineSegment(sketch, "E14.3.13.3", {"start": v(149, -40) * mm, "end": v(159, -40) * mm});
            skLineSegment(sketch, "E14.3.14.0", {"start": v(159, -26) * mm, "end": v(159, -16) * mm});
            skLineSegment(sketch, "E14.3.14.1", {"start": v(149, -26) * mm, "end": v(149, -16) * mm});
            skLineSegment(sketch, "E14.3.14.2", {"start": v(149, -16) * mm, "end": v(159, -16) * mm});
            skLineSegment(sketch, "E14.3.14.3", {"start": v(149, -26) * mm, "end": v(159, -26) * mm});
            skLineSegment(sketch, "E14.3.15.0", {"start": v(159, -12) * mm, "end": v(159, -2) * mm});
            skLineSegment(sketch, "E14.3.15.1", {"start": v(149, -12) * mm, "end": v(149, -2) * mm});
            skLineSegment(sketch, "E14.3.15.2", {"start": v(149, -2) * mm, "end": v(159, -2) * mm});
            skLineSegment(sketch, "E14.3.15.3", {"start": v(149, -12) * mm, "end": v(159, -12) * mm});
            skLineSegment(sketch, "E14.3.16.0", {"start": v(159, 2) * mm, "end": v(159, 12) * mm});
            skLineSegment(sketch, "E14.3.16.1", {"start": v(149, 2) * mm, "end": v(149, 12) * mm});
            skLineSegment(sketch, "E14.3.16.2", {"start": v(149, 12) * mm, "end": v(159, 12) * mm});
            skLineSegment(sketch, "E14.3.16.3", {"start": v(149, 2) * mm, "end": v(159, 2) * mm});
            skLineSegment(sketch, "E14.3.17.0", {"start": v(159, 16) * mm, "end": v(159, 26) * mm});
            skLineSegment(sketch, "E14.3.17.1", {"start": v(149, 16) * mm, "end": v(149, 26) * mm});
            skLineSegment(sketch, "E14.3.17.2", {"start": v(149, 26) * mm, "end": v(159, 26) * mm});
            skLineSegment(sketch, "E14.3.17.3", {"start": v(149, 16) * mm, "end": v(159, 16) * mm});
            skLineSegment(sketch, "E14.3.18.0", {"start": v(159, 30) * mm, "end": v(159, 40) * mm});
            skLineSegment(sketch, "E14.3.18.1", {"start": v(149, 30) * mm, "end": v(149, 40) * mm});
            skLineSegment(sketch, "E14.3.18.2", {"start": v(149, 40) * mm, "end": v(159, 40) * mm});
            skLineSegment(sketch, "E14.3.18.3", {"start": v(149, 30) * mm, "end": v(159, 30) * mm});
            skLineSegment(sketch, "E14.3.19.0", {"start": v(159, 44) * mm, "end": v(159, 54) * mm});
            skLineSegment(sketch, "E14.3.19.1", {"start": v(149, 44) * mm, "end": v(149, 54) * mm});
            skLineSegment(sketch, "E14.3.19.2", {"start": v(149, 54) * mm, "end": v(159, 54) * mm});
            skLineSegment(sketch, "E14.3.19.3", {"start": v(149, 44) * mm, "end": v(159, 44) * mm});
            skLineSegment(sketch, "E14.3.20.0", {"start": v(159, 58) * mm, "end": v(159, 68) * mm});
            skLineSegment(sketch, "E14.3.20.1", {"start": v(149, 58) * mm, "end": v(149, 68) * mm});
            skLineSegment(sketch, "E14.3.20.2", {"start": v(149, 68) * mm, "end": v(159, 68) * mm});
            skLineSegment(sketch, "E14.3.20.3", {"start": v(149, 58) * mm, "end": v(159, 58) * mm});
            skLineSegment(sketch, "E14.3.21.0", {"start": v(159, 72) * mm, "end": v(159, 82) * mm});
            skLineSegment(sketch, "E14.3.21.1", {"start": v(149, 72) * mm, "end": v(149, 82) * mm});
            skLineSegment(sketch, "E14.3.21.2", {"start": v(149, 82) * mm, "end": v(159, 82) * mm});
            skLineSegment(sketch, "E14.3.21.3", {"start": v(149, 72) * mm, "end": v(159, 72) * mm});
            skLineSegment(sketch, "E14.3.22.0", {"start": v(159, 86) * mm, "end": v(159, 96) * mm});
            skLineSegment(sketch, "E14.3.22.1", {"start": v(149, 86) * mm, "end": v(149, 96) * mm});
            skLineSegment(sketch, "E14.3.22.2", {"start": v(149, 96) * mm, "end": v(159, 96) * mm});
            skLineSegment(sketch, "E14.3.22.3", {"start": v(149, 86) * mm, "end": v(159, 86) * mm});
            skLineSegment(sketch, "E14.3.23.0", {"start": v(159, 100) * mm, "end": v(159, 110) * mm});
            skLineSegment(sketch, "E14.3.23.1", {"start": v(149, 100) * mm, "end": v(149, 110) * mm});
            skLineSegment(sketch, "E14.3.23.2", {"start": v(149, 110) * mm, "end": v(159, 110) * mm});
            skLineSegment(sketch, "E14.3.23.3", {"start": v(149, 100) * mm, "end": v(159, 100) * mm});
            skLineSegment(sketch, "E14.3.24.0", {"start": v(159, 114) * mm, "end": v(159, 124) * mm});
            skLineSegment(sketch, "E14.3.24.1", {"start": v(149, 114) * mm, "end": v(149, 124) * mm});
            skLineSegment(sketch, "E14.3.24.2", {"start": v(149, 124) * mm, "end": v(159, 124) * mm});
            skLineSegment(sketch, "E14.3.24.3", {"start": v(149, 114) * mm, "end": v(159, 114) * mm});
            skLineSegment(sketch, "E14.3.25.0", {"start": v(159, 128) * mm, "end": v(159, 138) * mm});
            skLineSegment(sketch, "E14.3.25.1", {"start": v(149, 128) * mm, "end": v(149, 138) * mm});
            skLineSegment(sketch, "E14.3.25.2", {"start": v(149, 138) * mm, "end": v(159, 138) * mm});
            skLineSegment(sketch, "E14.3.25.3", {"start": v(149, 128) * mm, "end": v(159, 128) * mm});
            skLineSegment(sketch, "E14.3.26.0", {"start": v(159, 142) * mm, "end": v(159, 152) * mm});
            skLineSegment(sketch, "E14.3.26.1", {"start": v(149, 142) * mm, "end": v(149, 152) * mm});
            skLineSegment(sketch, "E14.3.26.2", {"start": v(149, 152) * mm, "end": v(159, 152) * mm});
            skLineSegment(sketch, "E14.3.26.3", {"start": v(149, 142) * mm, "end": v(159, 142) * mm});
            skLineSegment(sketch, "E14.3.27.0", {"start": v(159, 156) * mm, "end": v(159, 166) * mm});
            skLineSegment(sketch, "E14.3.27.1", {"start": v(149, 156) * mm, "end": v(149, 166) * mm});
            skLineSegment(sketch, "E14.3.27.2", {"start": v(149, 166) * mm, "end": v(159, 166) * mm});
            skLineSegment(sketch, "E14.3.27.3", {"start": v(149, 156) * mm, "end": v(159, 156) * mm});
            skLineSegment(sketch, "E14.3.28.0", {"start": v(159, 170) * mm, "end": v(159, 180) * mm});
            skLineSegment(sketch, "E14.3.28.1", {"start": v(149, 170) * mm, "end": v(149, 180) * mm});
            skLineSegment(sketch, "E14.3.28.2", {"start": v(149, 180) * mm, "end": v(159, 180) * mm});
            skLineSegment(sketch, "E14.3.28.3", {"start": v(149, 170) * mm, "end": v(159, 170) * mm});
            skLineSegment(sketch, "E14.3.29.0", {"start": v(159, 184) * mm, "end": v(159, 194) * mm});
            skLineSegment(sketch, "E14.3.29.1", {"start": v(149, 184) * mm, "end": v(149, 194) * mm});
            skLineSegment(sketch, "E14.3.29.2", {"start": v(149, 194) * mm, "end": v(159, 194) * mm});
            skLineSegment(sketch, "E14.3.29.3", {"start": v(149, 184) * mm, "end": v(159, 184) * mm});
            skLineSegment(sketch, "E14.3.30.0", {"start": v(159, 198) * mm, "end": v(159, 208) * mm});
            skLineSegment(sketch, "E14.3.30.1", {"start": v(149, 198) * mm, "end": v(149, 208) * mm});
            skLineSegment(sketch, "E14.3.30.2", {"start": v(149, 208) * mm, "end": v(159, 208) * mm});
            skLineSegment(sketch, "E14.3.30.3", {"start": v(149, 198) * mm, "end": v(159, 198) * mm});
            skLineSegment(sketch, "E14.3.31.0", {"start": v(159, 212) * mm, "end": v(159, 222) * mm});
            skLineSegment(sketch, "E14.3.31.1", {"start": v(149, 212) * mm, "end": v(149, 222) * mm});
            skLineSegment(sketch, "E14.3.31.2", {"start": v(149, 222) * mm, "end": v(159, 222) * mm});
            skLineSegment(sketch, "E14.3.31.3", {"start": v(149, 212) * mm, "end": v(159, 212) * mm});
            skLineSegment(sketch, "E14.4.0.0", {"start": v(173, -222) * mm, "end": v(173, -212) * mm});
            skLineSegment(sketch, "E14.4.0.1", {"start": v(163, -222) * mm, "end": v(163, -212) * mm});
            skLineSegment(sketch, "E14.4.0.2", {"start": v(163, -212) * mm, "end": v(173, -212) * mm});
            skLineSegment(sketch, "E14.4.0.3", {"start": v(163, -222) * mm, "end": v(173, -222) * mm});
            skLineSegment(sketch, "E14.4.1.0", {"start": v(173, -208) * mm, "end": v(173, -198) * mm});
            skLineSegment(sketch, "E14.4.1.1", {"start": v(163, -208) * mm, "end": v(163, -198) * mm});
            skLineSegment(sketch, "E14.4.1.2", {"start": v(163, -198) * mm, "end": v(173, -198) * mm});
            skLineSegment(sketch, "E14.4.1.3", {"start": v(163, -208) * mm, "end": v(173, -208) * mm});
            skLineSegment(sketch, "E14.4.2.0", {"start": v(173, -194) * mm, "end": v(173, -184) * mm});
            skLineSegment(sketch, "E14.4.2.1", {"start": v(163, -194) * mm, "end": v(163, -184) * mm});
            skLineSegment(sketch, "E14.4.2.2", {"start": v(163, -184) * mm, "end": v(173, -184) * mm});
            skLineSegment(sketch, "E14.4.2.3", {"start": v(163, -194) * mm, "end": v(173, -194) * mm});
            skLineSegment(sketch, "E14.4.3.0", {"start": v(173, -180) * mm, "end": v(173, -170) * mm});
            skLineSegment(sketch, "E14.4.3.1", {"start": v(163, -180) * mm, "end": v(163, -170) * mm});
            skLineSegment(sketch, "E14.4.3.2", {"start": v(163, -170) * mm, "end": v(173, -170) * mm});
            skLineSegment(sketch, "E14.4.3.3", {"start": v(163, -180) * mm, "end": v(173, -180) * mm});
            skLineSegment(sketch, "E14.4.4.0", {"start": v(173, -166) * mm, "end": v(173, -156) * mm});
            skLineSegment(sketch, "E14.4.4.1", {"start": v(163, -166) * mm, "end": v(163, -156) * mm});
            skLineSegment(sketch, "E14.4.4.2", {"start": v(163, -156) * mm, "end": v(173, -156) * mm});
            skLineSegment(sketch, "E14.4.4.3", {"start": v(163, -166) * mm, "end": v(173, -166) * mm});
            skLineSegment(sketch, "E14.4.5.0", {"start": v(173, -152) * mm, "end": v(173, -142) * mm});
            skLineSegment(sketch, "E14.4.5.1", {"start": v(163, -152) * mm, "end": v(163, -142) * mm});
            skLineSegment(sketch, "E14.4.5.2", {"start": v(163, -142) * mm, "end": v(173, -142) * mm});
            skLineSegment(sketch, "E14.4.5.3", {"start": v(163, -152) * mm, "end": v(173, -152) * mm});
            skLineSegment(sketch, "E14.4.6.0", {"start": v(173, -138) * mm, "end": v(173, -128) * mm});
            skLineSegment(sketch, "E14.4.6.1", {"start": v(163, -138) * mm, "end": v(163, -128) * mm});
            skLineSegment(sketch, "E14.4.6.2", {"start": v(163, -128) * mm, "end": v(173, -128) * mm});
            skLineSegment(sketch, "E14.4.6.3", {"start": v(163, -138) * mm, "end": v(173, -138) * mm});
            skLineSegment(sketch, "E14.4.7.0", {"start": v(173, -124) * mm, "end": v(173, -114) * mm});
            skLineSegment(sketch, "E14.4.7.1", {"start": v(163, -124) * mm, "end": v(163, -114) * mm});
            skLineSegment(sketch, "E14.4.7.2", {"start": v(163, -114) * mm, "end": v(173, -114) * mm});
            skLineSegment(sketch, "E14.4.7.3", {"start": v(163, -124) * mm, "end": v(173, -124) * mm});
            skLineSegment(sketch, "E14.4.8.0", {"start": v(173, -110) * mm, "end": v(173, -100) * mm});
            skLineSegment(sketch, "E14.4.8.1", {"start": v(163, -110) * mm, "end": v(163, -100) * mm});
            skLineSegment(sketch, "E14.4.8.2", {"start": v(163, -100) * mm, "end": v(173, -100) * mm});
            skLineSegment(sketch, "E14.4.8.3", {"start": v(163, -110) * mm, "end": v(173, -110) * mm});
            skLineSegment(sketch, "E14.4.9.0", {"start": v(173, -96) * mm, "end": v(173, -86) * mm});
            skLineSegment(sketch, "E14.4.9.1", {"start": v(163, -96) * mm, "end": v(163, -86) * mm});
            skLineSegment(sketch, "E14.4.9.2", {"start": v(163, -86) * mm, "end": v(173, -86) * mm});
            skLineSegment(sketch, "E14.4.9.3", {"start": v(163, -96) * mm, "end": v(173, -96) * mm});
            skLineSegment(sketch, "E14.4.10.0", {"start": v(173, -82) * mm, "end": v(173, -72) * mm});
            skLineSegment(sketch, "E14.4.10.1", {"start": v(163, -82) * mm, "end": v(163, -72) * mm});
            skLineSegment(sketch, "E14.4.10.2", {"start": v(163, -72) * mm, "end": v(173, -72) * mm});
            skLineSegment(sketch, "E14.4.10.3", {"start": v(163, -82) * mm, "end": v(173, -82) * mm});
            skLineSegment(sketch, "E14.4.11.0", {"start": v(173, -68) * mm, "end": v(173, -58) * mm});
            skLineSegment(sketch, "E14.4.11.1", {"start": v(163, -68) * mm, "end": v(163, -58) * mm});
            skLineSegment(sketch, "E14.4.11.2", {"start": v(163, -58) * mm, "end": v(173, -58) * mm});
            skLineSegment(sketch, "E14.4.11.3", {"start": v(163, -68) * mm, "end": v(173, -68) * mm});
            skLineSegment(sketch, "E14.4.12.0", {"start": v(173, -54) * mm, "end": v(173, -44) * mm});
            skLineSegment(sketch, "E14.4.12.1", {"start": v(163, -54) * mm, "end": v(163, -44) * mm});
            skLineSegment(sketch, "E14.4.12.2", {"start": v(163, -44) * mm, "end": v(173, -44) * mm});
            skLineSegment(sketch, "E14.4.12.3", {"start": v(163, -54) * mm, "end": v(173, -54) * mm});
            skLineSegment(sketch, "E14.4.13.0", {"start": v(173, -40) * mm, "end": v(173, -30) * mm});
            skLineSegment(sketch, "E14.4.13.1", {"start": v(163, -40) * mm, "end": v(163, -30) * mm});
            skLineSegment(sketch, "E14.4.13.2", {"start": v(163, -30) * mm, "end": v(173, -30) * mm});
            skLineSegment(sketch, "E14.4.13.3", {"start": v(163, -40) * mm, "end": v(173, -40) * mm});
            skLineSegment(sketch, "E14.4.14.0", {"start": v(173, -26) * mm, "end": v(173, -16) * mm});
            skLineSegment(sketch, "E14.4.14.1", {"start": v(163, -26) * mm, "end": v(163, -16) * mm});
            skLineSegment(sketch, "E14.4.14.2", {"start": v(163, -16) * mm, "end": v(173, -16) * mm});
            skLineSegment(sketch, "E14.4.14.3", {"start": v(163, -26) * mm, "end": v(173, -26) * mm});
            skLineSegment(sketch, "E14.4.15.0", {"start": v(173, -12) * mm, "end": v(173, -2) * mm});
            skLineSegment(sketch, "E14.4.15.1", {"start": v(163, -12) * mm, "end": v(163, -2) * mm});
            skLineSegment(sketch, "E14.4.15.2", {"start": v(163, -2) * mm, "end": v(173, -2) * mm});
            skLineSegment(sketch, "E14.4.15.3", {"start": v(163, -12) * mm, "end": v(173, -12) * mm});
            skLineSegment(sketch, "E14.4.16.0", {"start": v(173, 2) * mm, "end": v(173, 12) * mm});
            skLineSegment(sketch, "E14.4.16.1", {"start": v(163, 2) * mm, "end": v(163, 12) * mm});
            skLineSegment(sketch, "E14.4.16.2", {"start": v(163, 12) * mm, "end": v(173, 12) * mm});
            skLineSegment(sketch, "E14.4.16.3", {"start": v(163, 2) * mm, "end": v(173, 2) * mm});
            skLineSegment(sketch, "E14.4.17.0", {"start": v(173, 16) * mm, "end": v(173, 26) * mm});
            skLineSegment(sketch, "E14.4.17.1", {"start": v(163, 16) * mm, "end": v(163, 26) * mm});
            skLineSegment(sketch, "E14.4.17.2", {"start": v(163, 26) * mm, "end": v(173, 26) * mm});
            skLineSegment(sketch, "E14.4.17.3", {"start": v(163, 16) * mm, "end": v(173, 16) * mm});
            skLineSegment(sketch, "E14.4.18.0", {"start": v(173, 30) * mm, "end": v(173, 40) * mm});
            skLineSegment(sketch, "E14.4.18.1", {"start": v(163, 30) * mm, "end": v(163, 40) * mm});
            skLineSegment(sketch, "E14.4.18.2", {"start": v(163, 40) * mm, "end": v(173, 40) * mm});
            skLineSegment(sketch, "E14.4.18.3", {"start": v(163, 30) * mm, "end": v(173, 30) * mm});
            skLineSegment(sketch, "E14.4.19.0", {"start": v(173, 44) * mm, "end": v(173, 54) * mm});
            skLineSegment(sketch, "E14.4.19.1", {"start": v(163, 44) * mm, "end": v(163, 54) * mm});
            skLineSegment(sketch, "E14.4.19.2", {"start": v(163, 54) * mm, "end": v(173, 54) * mm});
            skLineSegment(sketch, "E14.4.19.3", {"start": v(163, 44) * mm, "end": v(173, 44) * mm});
            skLineSegment(sketch, "E14.4.20.0", {"start": v(173, 58) * mm, "end": v(173, 68) * mm});
            skLineSegment(sketch, "E14.4.20.1", {"start": v(163, 58) * mm, "end": v(163, 68) * mm});
            skLineSegment(sketch, "E14.4.20.2", {"start": v(163, 68) * mm, "end": v(173, 68) * mm});
            skLineSegment(sketch, "E14.4.20.3", {"start": v(163, 58) * mm, "end": v(173, 58) * mm});
            skLineSegment(sketch, "E14.4.21.0", {"start": v(173, 72) * mm, "end": v(173, 82) * mm});
            skLineSegment(sketch, "E14.4.21.1", {"start": v(163, 72) * mm, "end": v(163, 82) * mm});
            skLineSegment(sketch, "E14.4.21.2", {"start": v(163, 82) * mm, "end": v(173, 82) * mm});
            skLineSegment(sketch, "E14.4.21.3", {"start": v(163, 72) * mm, "end": v(173, 72) * mm});
            skLineSegment(sketch, "E14.4.22.0", {"start": v(173, 86) * mm, "end": v(173, 96) * mm});
            skLineSegment(sketch, "E14.4.22.1", {"start": v(163, 86) * mm, "end": v(163, 96) * mm});
            skLineSegment(sketch, "E14.4.22.2", {"start": v(163, 96) * mm, "end": v(173, 96) * mm});
            skLineSegment(sketch, "E14.4.22.3", {"start": v(163, 86) * mm, "end": v(173, 86) * mm});
            skLineSegment(sketch, "E14.4.23.0", {"start": v(173, 100) * mm, "end": v(173, 110) * mm});
            skLineSegment(sketch, "E14.4.23.1", {"start": v(163, 100) * mm, "end": v(163, 110) * mm});
            skLineSegment(sketch, "E14.4.23.2", {"start": v(163, 110) * mm, "end": v(173, 110) * mm});
            skLineSegment(sketch, "E14.4.23.3", {"start": v(163, 100) * mm, "end": v(173, 100) * mm});
            skLineSegment(sketch, "E14.4.24.0", {"start": v(173, 114) * mm, "end": v(173, 124) * mm});
            skLineSegment(sketch, "E14.4.24.1", {"start": v(163, 114) * mm, "end": v(163, 124) * mm});
            skLineSegment(sketch, "E14.4.24.2", {"start": v(163, 124) * mm, "end": v(173, 124) * mm});
            skLineSegment(sketch, "E14.4.24.3", {"start": v(163, 114) * mm, "end": v(173, 114) * mm});
            skLineSegment(sketch, "E14.4.25.0", {"start": v(173, 128) * mm, "end": v(173, 138) * mm});
            skLineSegment(sketch, "E14.4.25.1", {"start": v(163, 128) * mm, "end": v(163, 138) * mm});
            skLineSegment(sketch, "E14.4.25.2", {"start": v(163, 138) * mm, "end": v(173, 138) * mm});
            skLineSegment(sketch, "E14.4.25.3", {"start": v(163, 128) * mm, "end": v(173, 128) * mm});
            skLineSegment(sketch, "E14.4.26.0", {"start": v(173, 142) * mm, "end": v(173, 152) * mm});
            skLineSegment(sketch, "E14.4.26.1", {"start": v(163, 142) * mm, "end": v(163, 152) * mm});
            skLineSegment(sketch, "E14.4.26.2", {"start": v(163, 152) * mm, "end": v(173, 152) * mm});
            skLineSegment(sketch, "E14.4.26.3", {"start": v(163, 142) * mm, "end": v(173, 142) * mm});
            skLineSegment(sketch, "E14.4.27.0", {"start": v(173, 156) * mm, "end": v(173, 166) * mm});
            skLineSegment(sketch, "E14.4.27.1", {"start": v(163, 156) * mm, "end": v(163, 166) * mm});
            skLineSegment(sketch, "E14.4.27.2", {"start": v(163, 166) * mm, "end": v(173, 166) * mm});
            skLineSegment(sketch, "E14.4.27.3", {"start": v(163, 156) * mm, "end": v(173, 156) * mm});
            skLineSegment(sketch, "E14.4.28.0", {"start": v(173, 170) * mm, "end": v(173, 180) * mm});
            skLineSegment(sketch, "E14.4.28.1", {"start": v(163, 170) * mm, "end": v(163, 180) * mm});
            skLineSegment(sketch, "E14.4.28.2", {"start": v(163, 180) * mm, "end": v(173, 180) * mm});
            skLineSegment(sketch, "E14.4.28.3", {"start": v(163, 170) * mm, "end": v(173, 170) * mm});
            skLineSegment(sketch, "E14.4.29.0", {"start": v(173, 184) * mm, "end": v(173, 194) * mm});
            skLineSegment(sketch, "E14.4.29.1", {"start": v(163, 184) * mm, "end": v(163, 194) * mm});
            skLineSegment(sketch, "E14.4.29.2", {"start": v(163, 194) * mm, "end": v(173, 194) * mm});
            skLineSegment(sketch, "E14.4.29.3", {"start": v(163, 184) * mm, "end": v(173, 184) * mm});
            skLineSegment(sketch, "E14.4.30.0", {"start": v(173, 198) * mm, "end": v(173, 208) * mm});
            skLineSegment(sketch, "E14.4.30.1", {"start": v(163, 198) * mm, "end": v(163, 208) * mm});
            skLineSegment(sketch, "E14.4.30.2", {"start": v(163, 208) * mm, "end": v(173, 208) * mm});
            skLineSegment(sketch, "E14.4.30.3", {"start": v(163, 198) * mm, "end": v(173, 198) * mm});
            skLineSegment(sketch, "E14.4.31.0", {"start": v(173, 212) * mm, "end": v(173, 222) * mm});
            skLineSegment(sketch, "E14.4.31.1", {"start": v(163, 212) * mm, "end": v(163, 222) * mm});
            skLineSegment(sketch, "E14.4.31.2", {"start": v(163, 222) * mm, "end": v(173, 222) * mm});
            skLineSegment(sketch, "E14.4.31.3", {"start": v(163, 212) * mm, "end": v(173, 212) * mm});
            skLineSegment(sketch, "E14.5.0.0", {"start": v(187, -222) * mm, "end": v(187, -212) * mm});
            skLineSegment(sketch, "E14.5.0.1", {"start": v(177, -222) * mm, "end": v(177, -212) * mm});
            skLineSegment(sketch, "E14.5.0.2", {"start": v(177, -212) * mm, "end": v(187, -212) * mm});
            skLineSegment(sketch, "E14.5.0.3", {"start": v(177, -222) * mm, "end": v(187, -222) * mm});
            skLineSegment(sketch, "E14.5.1.0", {"start": v(187, -208) * mm, "end": v(187, -198) * mm});
            skLineSegment(sketch, "E14.5.1.1", {"start": v(177, -208) * mm, "end": v(177, -198) * mm});
            skLineSegment(sketch, "E14.5.1.2", {"start": v(177, -198) * mm, "end": v(187, -198) * mm});
            skLineSegment(sketch, "E14.5.1.3", {"start": v(177, -208) * mm, "end": v(187, -208) * mm});
            skLineSegment(sketch, "E14.5.2.0", {"start": v(187, -194) * mm, "end": v(187, -184) * mm});
            skLineSegment(sketch, "E14.5.2.1", {"start": v(177, -194) * mm, "end": v(177, -184) * mm});
            skLineSegment(sketch, "E14.5.2.2", {"start": v(177, -184) * mm, "end": v(187, -184) * mm});
            skLineSegment(sketch, "E14.5.2.3", {"start": v(177, -194) * mm, "end": v(187, -194) * mm});
            skLineSegment(sketch, "E14.5.3.0", {"start": v(187, -180) * mm, "end": v(187, -170) * mm});
            skLineSegment(sketch, "E14.5.3.1", {"start": v(177, -180) * mm, "end": v(177, -170) * mm});
            skLineSegment(sketch, "E14.5.3.2", {"start": v(177, -170) * mm, "end": v(187, -170) * mm});
            skLineSegment(sketch, "E14.5.3.3", {"start": v(177, -180) * mm, "end": v(187, -180) * mm});
            skLineSegment(sketch, "E14.5.4.0", {"start": v(187, -166) * mm, "end": v(187, -156) * mm});
            skLineSegment(sketch, "E14.5.4.1", {"start": v(177, -166) * mm, "end": v(177, -156) * mm});
            skLineSegment(sketch, "E14.5.4.2", {"start": v(177, -156) * mm, "end": v(187, -156) * mm});
            skLineSegment(sketch, "E14.5.4.3", {"start": v(177, -166) * mm, "end": v(187, -166) * mm});
            skLineSegment(sketch, "E14.5.5.0", {"start": v(187, -152) * mm, "end": v(187, -142) * mm});
            skLineSegment(sketch, "E14.5.5.1", {"start": v(177, -152) * mm, "end": v(177, -142) * mm});
            skLineSegment(sketch, "E14.5.5.2", {"start": v(177, -142) * mm, "end": v(187, -142) * mm});
            skLineSegment(sketch, "E14.5.5.3", {"start": v(177, -152) * mm, "end": v(187, -152) * mm});
            skLineSegment(sketch, "E14.5.6.0", {"start": v(187, -138) * mm, "end": v(187, -128) * mm});
            skLineSegment(sketch, "E14.5.6.1", {"start": v(177, -138) * mm, "end": v(177, -128) * mm});
            skLineSegment(sketch, "E14.5.6.2", {"start": v(177, -128) * mm, "end": v(187, -128) * mm});
            skLineSegment(sketch, "E14.5.6.3", {"start": v(177, -138) * mm, "end": v(187, -138) * mm});
            skLineSegment(sketch, "E14.5.7.0", {"start": v(187, -124) * mm, "end": v(187, -114) * mm});
            skLineSegment(sketch, "E14.5.7.1", {"start": v(177, -124) * mm, "end": v(177, -114) * mm});
            skLineSegment(sketch, "E14.5.7.2", {"start": v(177, -114) * mm, "end": v(187, -114) * mm});
            skLineSegment(sketch, "E14.5.7.3", {"start": v(177, -124) * mm, "end": v(187, -124) * mm});
            skLineSegment(sketch, "E14.5.8.0", {"start": v(187, -110) * mm, "end": v(187, -100) * mm});
            skLineSegment(sketch, "E14.5.8.1", {"start": v(177, -110) * mm, "end": v(177, -100) * mm});
            skLineSegment(sketch, "E14.5.8.2", {"start": v(177, -100) * mm, "end": v(187, -100) * mm});
            skLineSegment(sketch, "E14.5.8.3", {"start": v(177, -110) * mm, "end": v(187, -110) * mm});
            skLineSegment(sketch, "E14.5.9.0", {"start": v(187, -96) * mm, "end": v(187, -86) * mm});
            skLineSegment(sketch, "E14.5.9.1", {"start": v(177, -96) * mm, "end": v(177, -86) * mm});
            skLineSegment(sketch, "E14.5.9.2", {"start": v(177, -86) * mm, "end": v(187, -86) * mm});
            skLineSegment(sketch, "E14.5.9.3", {"start": v(177, -96) * mm, "end": v(187, -96) * mm});
            skLineSegment(sketch, "E14.5.10.0", {"start": v(187, -82) * mm, "end": v(187, -72) * mm});
            skLineSegment(sketch, "E14.5.10.1", {"start": v(177, -82) * mm, "end": v(177, -72) * mm});
            skLineSegment(sketch, "E14.5.10.2", {"start": v(177, -72) * mm, "end": v(187, -72) * mm});
            skLineSegment(sketch, "E14.5.10.3", {"start": v(177, -82) * mm, "end": v(187, -82) * mm});
            skLineSegment(sketch, "E14.5.11.0", {"start": v(187, -68) * mm, "end": v(187, -58) * mm});
            skLineSegment(sketch, "E14.5.11.1", {"start": v(177, -68) * mm, "end": v(177, -58) * mm});
            skLineSegment(sketch, "E14.5.11.2", {"start": v(177, -58) * mm, "end": v(187, -58) * mm});
            skLineSegment(sketch, "E14.5.11.3", {"start": v(177, -68) * mm, "end": v(187, -68) * mm});
            skLineSegment(sketch, "E14.5.12.0", {"start": v(187, -54) * mm, "end": v(187, -44) * mm});
            skLineSegment(sketch, "E14.5.12.1", {"start": v(177, -54) * mm, "end": v(177, -44) * mm});
            skLineSegment(sketch, "E14.5.12.2", {"start": v(177, -44) * mm, "end": v(187, -44) * mm});
            skLineSegment(sketch, "E14.5.12.3", {"start": v(177, -54) * mm, "end": v(187, -54) * mm});
            skLineSegment(sketch, "E14.5.13.0", {"start": v(187, -40) * mm, "end": v(187, -30) * mm});
            skLineSegment(sketch, "E14.5.13.1", {"start": v(177, -40) * mm, "end": v(177, -30) * mm});
            skLineSegment(sketch, "E14.5.13.2", {"start": v(177, -30) * mm, "end": v(187, -30) * mm});
            skLineSegment(sketch, "E14.5.13.3", {"start": v(177, -40) * mm, "end": v(187, -40) * mm});
            skLineSegment(sketch, "E14.5.14.0", {"start": v(187, -26) * mm, "end": v(187, -16) * mm});
            skLineSegment(sketch, "E14.5.14.1", {"start": v(177, -26) * mm, "end": v(177, -16) * mm});
            skLineSegment(sketch, "E14.5.14.2", {"start": v(177, -16) * mm, "end": v(187, -16) * mm});
            skLineSegment(sketch, "E14.5.14.3", {"start": v(177, -26) * mm, "end": v(187, -26) * mm});
            skLineSegment(sketch, "E14.5.15.0", {"start": v(187, -12) * mm, "end": v(187, -2) * mm});
            skLineSegment(sketch, "E14.5.15.1", {"start": v(177, -12) * mm, "end": v(177, -2) * mm});
            skLineSegment(sketch, "E14.5.15.2", {"start": v(177, -2) * mm, "end": v(187, -2) * mm});
            skLineSegment(sketch, "E14.5.15.3", {"start": v(177, -12) * mm, "end": v(187, -12) * mm});
            skLineSegment(sketch, "E14.5.16.0", {"start": v(187, 2) * mm, "end": v(187, 12) * mm});
            skLineSegment(sketch, "E14.5.16.1", {"start": v(177, 2) * mm, "end": v(177, 12) * mm});
            skLineSegment(sketch, "E14.5.16.2", {"start": v(177, 12) * mm, "end": v(187, 12) * mm});
            skLineSegment(sketch, "E14.5.16.3", {"start": v(177, 2) * mm, "end": v(187, 2) * mm});
            skLineSegment(sketch, "E14.5.17.0", {"start": v(187, 16) * mm, "end": v(187, 26) * mm});
            skLineSegment(sketch, "E14.5.17.1", {"start": v(177, 16) * mm, "end": v(177, 26) * mm});
            skLineSegment(sketch, "E14.5.17.2", {"start": v(177, 26) * mm, "end": v(187, 26) * mm});
            skLineSegment(sketch, "E14.5.17.3", {"start": v(177, 16) * mm, "end": v(187, 16) * mm});
            skLineSegment(sketch, "E14.5.18.0", {"start": v(187, 30) * mm, "end": v(187, 40) * mm});
            skLineSegment(sketch, "E14.5.18.1", {"start": v(177, 30) * mm, "end": v(177, 40) * mm});
            skLineSegment(sketch, "E14.5.18.2", {"start": v(177, 40) * mm, "end": v(187, 40) * mm});
            skLineSegment(sketch, "E14.5.18.3", {"start": v(177, 30) * mm, "end": v(187, 30) * mm});
            skLineSegment(sketch, "E14.5.19.0", {"start": v(187, 44) * mm, "end": v(187, 54) * mm});
            skLineSegment(sketch, "E14.5.19.1", {"start": v(177, 44) * mm, "end": v(177, 54) * mm});
            skLineSegment(sketch, "E14.5.19.2", {"start": v(177, 54) * mm, "end": v(187, 54) * mm});
            skLineSegment(sketch, "E14.5.19.3", {"start": v(177, 44) * mm, "end": v(187, 44) * mm});
            skLineSegment(sketch, "E14.5.20.0", {"start": v(187, 58) * mm, "end": v(187, 68) * mm});
            skLineSegment(sketch, "E14.5.20.1", {"start": v(177, 58) * mm, "end": v(177, 68) * mm});
            skLineSegment(sketch, "E14.5.20.2", {"start": v(177, 68) * mm, "end": v(187, 68) * mm});
            skLineSegment(sketch, "E14.5.20.3", {"start": v(177, 58) * mm, "end": v(187, 58) * mm});
            skLineSegment(sketch, "E14.5.21.0", {"start": v(187, 72) * mm, "end": v(187, 82) * mm});
            skLineSegment(sketch, "E14.5.21.1", {"start": v(177, 72) * mm, "end": v(177, 82) * mm});
            skLineSegment(sketch, "E14.5.21.2", {"start": v(177, 82) * mm, "end": v(187, 82) * mm});
            skLineSegment(sketch, "E14.5.21.3", {"start": v(177, 72) * mm, "end": v(187, 72) * mm});
            skLineSegment(sketch, "E14.5.22.0", {"start": v(187, 86) * mm, "end": v(187, 96) * mm});
            skLineSegment(sketch, "E14.5.22.1", {"start": v(177, 86) * mm, "end": v(177, 96) * mm});
            skLineSegment(sketch, "E14.5.22.2", {"start": v(177, 96) * mm, "end": v(187, 96) * mm});
            skLineSegment(sketch, "E14.5.22.3", {"start": v(177, 86) * mm, "end": v(187, 86) * mm});
            skLineSegment(sketch, "E14.5.23.0", {"start": v(187, 100) * mm, "end": v(187, 110) * mm});
            skLineSegment(sketch, "E14.5.23.1", {"start": v(177, 100) * mm, "end": v(177, 110) * mm});
            skLineSegment(sketch, "E14.5.23.2", {"start": v(177, 110) * mm, "end": v(187, 110) * mm});
            skLineSegment(sketch, "E14.5.23.3", {"start": v(177, 100) * mm, "end": v(187, 100) * mm});
            skLineSegment(sketch, "E14.5.24.0", {"start": v(187, 114) * mm, "end": v(187, 124) * mm});
            skLineSegment(sketch, "E14.5.24.1", {"start": v(177, 114) * mm, "end": v(177, 124) * mm});
            skLineSegment(sketch, "E14.5.24.2", {"start": v(177, 124) * mm, "end": v(187, 124) * mm});
            skLineSegment(sketch, "E14.5.24.3", {"start": v(177, 114) * mm, "end": v(187, 114) * mm});
            skLineSegment(sketch, "E14.5.25.0", {"start": v(187, 128) * mm, "end": v(187, 138) * mm});
            skLineSegment(sketch, "E14.5.25.1", {"start": v(177, 128) * mm, "end": v(177, 138) * mm});
            skLineSegment(sketch, "E14.5.25.2", {"start": v(177, 138) * mm, "end": v(187, 138) * mm});
            skLineSegment(sketch, "E14.5.25.3", {"start": v(177, 128) * mm, "end": v(187, 128) * mm});
            skLineSegment(sketch, "E14.5.26.0", {"start": v(187, 142) * mm, "end": v(187, 152) * mm});
            skLineSegment(sketch, "E14.5.26.1", {"start": v(177, 142) * mm, "end": v(177, 152) * mm});
            skLineSegment(sketch, "E14.5.26.2", {"start": v(177, 152) * mm, "end": v(187, 152) * mm});
            skLineSegment(sketch, "E14.5.26.3", {"start": v(177, 142) * mm, "end": v(187, 142) * mm});
            skLineSegment(sketch, "E14.5.27.0", {"start": v(187, 156) * mm, "end": v(187, 166) * mm});
            skLineSegment(sketch, "E14.5.27.1", {"start": v(177, 156) * mm, "end": v(177, 166) * mm});
            skLineSegment(sketch, "E14.5.27.2", {"start": v(177, 166) * mm, "end": v(187, 166) * mm});
            skLineSegment(sketch, "E14.5.27.3", {"start": v(177, 156) * mm, "end": v(187, 156) * mm});
            skLineSegment(sketch, "E14.5.28.0", {"start": v(187, 170) * mm, "end": v(187, 180) * mm});
            skLineSegment(sketch, "E14.5.28.1", {"start": v(177, 170) * mm, "end": v(177, 180) * mm});
            skLineSegment(sketch, "E14.5.28.2", {"start": v(177, 180) * mm, "end": v(187, 180) * mm});
            skLineSegment(sketch, "E14.5.28.3", {"start": v(177, 170) * mm, "end": v(187, 170) * mm});
            skLineSegment(sketch, "E14.5.29.0", {"start": v(187, 184) * mm, "end": v(187, 194) * mm});
            skLineSegment(sketch, "E14.5.29.1", {"start": v(177, 184) * mm, "end": v(177, 194) * mm});
            skLineSegment(sketch, "E14.5.29.2", {"start": v(177, 194) * mm, "end": v(187, 194) * mm});
            skLineSegment(sketch, "E14.5.29.3", {"start": v(177, 184) * mm, "end": v(187, 184) * mm});
            skLineSegment(sketch, "E14.5.30.0", {"start": v(187, 198) * mm, "end": v(187, 208) * mm});
            skLineSegment(sketch, "E14.5.30.1", {"start": v(177, 198) * mm, "end": v(177, 208) * mm});
            skLineSegment(sketch, "E14.5.30.2", {"start": v(177, 208) * mm, "end": v(187, 208) * mm});
            skLineSegment(sketch, "E14.5.30.3", {"start": v(177, 198) * mm, "end": v(187, 198) * mm});
            skLineSegment(sketch, "E14.5.31.0", {"start": v(187, 212) * mm, "end": v(187, 222) * mm});
            skLineSegment(sketch, "E14.5.31.1", {"start": v(177, 212) * mm, "end": v(177, 222) * mm});
            skLineSegment(sketch, "E14.5.31.2", {"start": v(177, 222) * mm, "end": v(187, 222) * mm});
            skLineSegment(sketch, "E14.5.31.3", {"start": v(177, 212) * mm, "end": v(187, 212) * mm});
            skLineSegment(sketch, "E14.6.0.0", {"start": v(201, -222) * mm, "end": v(201, -212) * mm});
            skLineSegment(sketch, "E14.6.0.1", {"start": v(191, -222) * mm, "end": v(191, -212) * mm});
            skLineSegment(sketch, "E14.6.0.2", {"start": v(191, -212) * mm, "end": v(201, -212) * mm});
            skLineSegment(sketch, "E14.6.0.3", {"start": v(191, -222) * mm, "end": v(201, -222) * mm});
            skLineSegment(sketch, "E14.6.1.0", {"start": v(201, -208) * mm, "end": v(201, -198) * mm});
            skLineSegment(sketch, "E14.6.1.1", {"start": v(191, -208) * mm, "end": v(191, -198) * mm});
            skLineSegment(sketch, "E14.6.1.2", {"start": v(191, -198) * mm, "end": v(201, -198) * mm});
            skLineSegment(sketch, "E14.6.1.3", {"start": v(191, -208) * mm, "end": v(201, -208) * mm});
            skLineSegment(sketch, "E14.6.2.0", {"start": v(201, -194) * mm, "end": v(201, -184) * mm});
            skLineSegment(sketch, "E14.6.2.1", {"start": v(191, -194) * mm, "end": v(191, -184) * mm});
            skLineSegment(sketch, "E14.6.2.2", {"start": v(191, -184) * mm, "end": v(201, -184) * mm});
            skLineSegment(sketch, "E14.6.2.3", {"start": v(191, -194) * mm, "end": v(201, -194) * mm});
            skLineSegment(sketch, "E14.6.3.0", {"start": v(201, -180) * mm, "end": v(201, -170) * mm});
            skLineSegment(sketch, "E14.6.3.1", {"start": v(191, -180) * mm, "end": v(191, -170) * mm});
            skLineSegment(sketch, "E14.6.3.2", {"start": v(191, -170) * mm, "end": v(201, -170) * mm});
            skLineSegment(sketch, "E14.6.3.3", {"start": v(191, -180) * mm, "end": v(201, -180) * mm});
            skLineSegment(sketch, "E14.6.4.0", {"start": v(201, -166) * mm, "end": v(201, -156) * mm});
            skLineSegment(sketch, "E14.6.4.1", {"start": v(191, -166) * mm, "end": v(191, -156) * mm});
            skLineSegment(sketch, "E14.6.4.2", {"start": v(191, -156) * mm, "end": v(201, -156) * mm});
            skLineSegment(sketch, "E14.6.4.3", {"start": v(191, -166) * mm, "end": v(201, -166) * mm});
            skLineSegment(sketch, "E14.6.5.0", {"start": v(201, -152) * mm, "end": v(201, -142) * mm});
            skLineSegment(sketch, "E14.6.5.1", {"start": v(191, -152) * mm, "end": v(191, -142) * mm});
            skLineSegment(sketch, "E14.6.5.2", {"start": v(191, -142) * mm, "end": v(201, -142) * mm});
            skLineSegment(sketch, "E14.6.5.3", {"start": v(191, -152) * mm, "end": v(201, -152) * mm});
            skLineSegment(sketch, "E14.6.6.0", {"start": v(201, -138) * mm, "end": v(201, -128) * mm});
            skLineSegment(sketch, "E14.6.6.1", {"start": v(191, -138) * mm, "end": v(191, -128) * mm});
            skLineSegment(sketch, "E14.6.6.2", {"start": v(191, -128) * mm, "end": v(201, -128) * mm});
            skLineSegment(sketch, "E14.6.6.3", {"start": v(191, -138) * mm, "end": v(201, -138) * mm});
            skLineSegment(sketch, "E14.6.7.0", {"start": v(201, -124) * mm, "end": v(201, -114) * mm});
            skLineSegment(sketch, "E14.6.7.1", {"start": v(191, -124) * mm, "end": v(191, -114) * mm});
            skLineSegment(sketch, "E14.6.7.2", {"start": v(191, -114) * mm, "end": v(201, -114) * mm});
            skLineSegment(sketch, "E14.6.7.3", {"start": v(191, -124) * mm, "end": v(201, -124) * mm});
            skLineSegment(sketch, "E14.6.8.0", {"start": v(201, -110) * mm, "end": v(201, -100) * mm});
            skLineSegment(sketch, "E14.6.8.1", {"start": v(191, -110) * mm, "end": v(191, -100) * mm});
            skLineSegment(sketch, "E14.6.8.2", {"start": v(191, -100) * mm, "end": v(201, -100) * mm});
            skLineSegment(sketch, "E14.6.8.3", {"start": v(191, -110) * mm, "end": v(201, -110) * mm});
            skLineSegment(sketch, "E14.6.9.0", {"start": v(201, -96) * mm, "end": v(201, -86) * mm});
            skLineSegment(sketch, "E14.6.9.1", {"start": v(191, -96) * mm, "end": v(191, -86) * mm});
            skLineSegment(sketch, "E14.6.9.2", {"start": v(191, -86) * mm, "end": v(201, -86) * mm});
            skLineSegment(sketch, "E14.6.9.3", {"start": v(191, -96) * mm, "end": v(201, -96) * mm});
            skLineSegment(sketch, "E14.6.10.0", {"start": v(201, -82) * mm, "end": v(201, -72) * mm});
            skLineSegment(sketch, "E14.6.10.1", {"start": v(191, -82) * mm, "end": v(191, -72) * mm});
            skLineSegment(sketch, "E14.6.10.2", {"start": v(191, -72) * mm, "end": v(201, -72) * mm});
            skLineSegment(sketch, "E14.6.10.3", {"start": v(191, -82) * mm, "end": v(201, -82) * mm});
            skLineSegment(sketch, "E14.6.11.0", {"start": v(201, -68) * mm, "end": v(201, -58) * mm});
            skLineSegment(sketch, "E14.6.11.1", {"start": v(191, -68) * mm, "end": v(191, -58) * mm});
            skLineSegment(sketch, "E14.6.11.2", {"start": v(191, -58) * mm, "end": v(201, -58) * mm});
            skLineSegment(sketch, "E14.6.11.3", {"start": v(191, -68) * mm, "end": v(201, -68) * mm});
            skLineSegment(sketch, "E14.6.12.0", {"start": v(201, -54) * mm, "end": v(201, -44) * mm});
            skLineSegment(sketch, "E14.6.12.1", {"start": v(191, -54) * mm, "end": v(191, -44) * mm});
            skLineSegment(sketch, "E14.6.12.2", {"start": v(191, -44) * mm, "end": v(201, -44) * mm});
            skLineSegment(sketch, "E14.6.12.3", {"start": v(191, -54) * mm, "end": v(201, -54) * mm});
            skLineSegment(sketch, "E14.6.13.0", {"start": v(201, -40) * mm, "end": v(201, -30) * mm});
            skLineSegment(sketch, "E14.6.13.1", {"start": v(191, -40) * mm, "end": v(191, -30) * mm});
            skLineSegment(sketch, "E14.6.13.2", {"start": v(191, -30) * mm, "end": v(201, -30) * mm});
            skLineSegment(sketch, "E14.6.13.3", {"start": v(191, -40) * mm, "end": v(201, -40) * mm});
            skLineSegment(sketch, "E14.6.14.0", {"start": v(201, -26) * mm, "end": v(201, -16) * mm});
            skLineSegment(sketch, "E14.6.14.1", {"start": v(191, -26) * mm, "end": v(191, -16) * mm});
            skLineSegment(sketch, "E14.6.14.2", {"start": v(191, -16) * mm, "end": v(201, -16) * mm});
            skLineSegment(sketch, "E14.6.14.3", {"start": v(191, -26) * mm, "end": v(201, -26) * mm});
            skLineSegment(sketch, "E14.6.15.0", {"start": v(201, -12) * mm, "end": v(201, -2) * mm});
            skLineSegment(sketch, "E14.6.15.1", {"start": v(191, -12) * mm, "end": v(191, -2) * mm});
            skLineSegment(sketch, "E14.6.15.2", {"start": v(191, -2) * mm, "end": v(201, -2) * mm});
            skLineSegment(sketch, "E14.6.15.3", {"start": v(191, -12) * mm, "end": v(201, -12) * mm});
            skLineSegment(sketch, "E14.6.16.0", {"start": v(201, 2) * mm, "end": v(201, 12) * mm});
            skLineSegment(sketch, "E14.6.16.1", {"start": v(191, 2) * mm, "end": v(191, 12) * mm});
            skLineSegment(sketch, "E14.6.16.2", {"start": v(191, 12) * mm, "end": v(201, 12) * mm});
            skLineSegment(sketch, "E14.6.16.3", {"start": v(191, 2) * mm, "end": v(201, 2) * mm});
            skLineSegment(sketch, "E14.6.17.0", {"start": v(201, 16) * mm, "end": v(201, 26) * mm});
            skLineSegment(sketch, "E14.6.17.1", {"start": v(191, 16) * mm, "end": v(191, 26) * mm});
            skLineSegment(sketch, "E14.6.17.2", {"start": v(191, 26) * mm, "end": v(201, 26) * mm});
            skLineSegment(sketch, "E14.6.17.3", {"start": v(191, 16) * mm, "end": v(201, 16) * mm});
            skLineSegment(sketch, "E14.6.18.0", {"start": v(201, 30) * mm, "end": v(201, 40) * mm});
            skLineSegment(sketch, "E14.6.18.1", {"start": v(191, 30) * mm, "end": v(191, 40) * mm});
            skLineSegment(sketch, "E14.6.18.2", {"start": v(191, 40) * mm, "end": v(201, 40) * mm});
            skLineSegment(sketch, "E14.6.18.3", {"start": v(191, 30) * mm, "end": v(201, 30) * mm});
            skLineSegment(sketch, "E14.6.19.0", {"start": v(201, 44) * mm, "end": v(201, 54) * mm});
            skLineSegment(sketch, "E14.6.19.1", {"start": v(191, 44) * mm, "end": v(191, 54) * mm});
            skLineSegment(sketch, "E14.6.19.2", {"start": v(191, 54) * mm, "end": v(201, 54) * mm});
            skLineSegment(sketch, "E14.6.19.3", {"start": v(191, 44) * mm, "end": v(201, 44) * mm});
            skLineSegment(sketch, "E14.6.20.0", {"start": v(201, 58) * mm, "end": v(201, 68) * mm});
            skLineSegment(sketch, "E14.6.20.1", {"start": v(191, 58) * mm, "end": v(191, 68) * mm});
            skLineSegment(sketch, "E14.6.20.2", {"start": v(191, 68) * mm, "end": v(201, 68) * mm});
            skLineSegment(sketch, "E14.6.20.3", {"start": v(191, 58) * mm, "end": v(201, 58) * mm});
            skLineSegment(sketch, "E14.6.21.0", {"start": v(201, 72) * mm, "end": v(201, 82) * mm});
            skLineSegment(sketch, "E14.6.21.1", {"start": v(191, 72) * mm, "end": v(191, 82) * mm});
            skLineSegment(sketch, "E14.6.21.2", {"start": v(191, 82) * mm, "end": v(201, 82) * mm});
            skLineSegment(sketch, "E14.6.21.3", {"start": v(191, 72) * mm, "end": v(201, 72) * mm});
            skLineSegment(sketch, "E14.6.22.0", {"start": v(201, 86) * mm, "end": v(201, 96) * mm});
            skLineSegment(sketch, "E14.6.22.1", {"start": v(191, 86) * mm, "end": v(191, 96) * mm});
            skLineSegment(sketch, "E14.6.22.2", {"start": v(191, 96) * mm, "end": v(201, 96) * mm});
            skLineSegment(sketch, "E14.6.22.3", {"start": v(191, 86) * mm, "end": v(201, 86) * mm});
            skLineSegment(sketch, "E14.6.23.0", {"start": v(201, 100) * mm, "end": v(201, 110) * mm});
            skLineSegment(sketch, "E14.6.23.1", {"start": v(191, 100) * mm, "end": v(191, 110) * mm});
            skLineSegment(sketch, "E14.6.23.2", {"start": v(191, 110) * mm, "end": v(201, 110) * mm});
            skLineSegment(sketch, "E14.6.23.3", {"start": v(191, 100) * mm, "end": v(201, 100) * mm});
            skLineSegment(sketch, "E14.6.24.0", {"start": v(201, 114) * mm, "end": v(201, 124) * mm});
            skLineSegment(sketch, "E14.6.24.1", {"start": v(191, 114) * mm, "end": v(191, 124) * mm});
            skLineSegment(sketch, "E14.6.24.2", {"start": v(191, 124) * mm, "end": v(201, 124) * mm});
            skLineSegment(sketch, "E14.6.24.3", {"start": v(191, 114) * mm, "end": v(201, 114) * mm});
            skLineSegment(sketch, "E14.6.25.0", {"start": v(201, 128) * mm, "end": v(201, 138) * mm});
            skLineSegment(sketch, "E14.6.25.1", {"start": v(191, 128) * mm, "end": v(191, 138) * mm});
            skLineSegment(sketch, "E14.6.25.2", {"start": v(191, 138) * mm, "end": v(201, 138) * mm});
            skLineSegment(sketch, "E14.6.25.3", {"start": v(191, 128) * mm, "end": v(201, 128) * mm});
            skLineSegment(sketch, "E14.6.26.0", {"start": v(201, 142) * mm, "end": v(201, 152) * mm});
            skLineSegment(sketch, "E14.6.26.1", {"start": v(191, 142) * mm, "end": v(191, 152) * mm});
            skLineSegment(sketch, "E14.6.26.2", {"start": v(191, 152) * mm, "end": v(201, 152) * mm});
            skLineSegment(sketch, "E14.6.26.3", {"start": v(191, 142) * mm, "end": v(201, 142) * mm});
            skLineSegment(sketch, "E14.6.27.0", {"start": v(201, 156) * mm, "end": v(201, 166) * mm});
            skLineSegment(sketch, "E14.6.27.1", {"start": v(191, 156) * mm, "end": v(191, 166) * mm});
            skLineSegment(sketch, "E14.6.27.2", {"start": v(191, 166) * mm, "end": v(201, 166) * mm});
            skLineSegment(sketch, "E14.6.27.3", {"start": v(191, 156) * mm, "end": v(201, 156) * mm});
            skLineSegment(sketch, "E14.6.28.0", {"start": v(201, 170) * mm, "end": v(201, 180) * mm});
            skLineSegment(sketch, "E14.6.28.1", {"start": v(191, 170) * mm, "end": v(191, 180) * mm});
            skLineSegment(sketch, "E14.6.28.2", {"start": v(191, 180) * mm, "end": v(201, 180) * mm});
            skLineSegment(sketch, "E14.6.28.3", {"start": v(191, 170) * mm, "end": v(201, 170) * mm});
            skLineSegment(sketch, "E14.6.29.0", {"start": v(201, 184) * mm, "end": v(201, 194) * mm});
            skLineSegment(sketch, "E14.6.29.1", {"start": v(191, 184) * mm, "end": v(191, 194) * mm});
            skLineSegment(sketch, "E14.6.29.2", {"start": v(191, 194) * mm, "end": v(201, 194) * mm});
            skLineSegment(sketch, "E14.6.29.3", {"start": v(191, 184) * mm, "end": v(201, 184) * mm});
            skLineSegment(sketch, "E14.6.30.0", {"start": v(201, 198) * mm, "end": v(201, 208) * mm});
            skLineSegment(sketch, "E14.6.30.1", {"start": v(191, 198) * mm, "end": v(191, 208) * mm});
            skLineSegment(sketch, "E14.6.30.2", {"start": v(191, 208) * mm, "end": v(201, 208) * mm});
            skLineSegment(sketch, "E14.6.30.3", {"start": v(191, 198) * mm, "end": v(201, 198) * mm});
            skLineSegment(sketch, "E14.6.31.0", {"start": v(201, 212) * mm, "end": v(201, 222) * mm});
            skLineSegment(sketch, "E14.6.31.1", {"start": v(191, 212) * mm, "end": v(191, 222) * mm});
            skLineSegment(sketch, "E14.6.31.2", {"start": v(191, 222) * mm, "end": v(201, 222) * mm});
            skLineSegment(sketch, "E14.6.31.3", {"start": v(191, 212) * mm, "end": v(201, 212) * mm});
            skLineSegment(sketch, "E14.7.0.0", {"start": v(215, -222) * mm, "end": v(215, -212) * mm});
            skLineSegment(sketch, "E14.7.0.1", {"start": v(205, -222) * mm, "end": v(205, -212) * mm});
            skLineSegment(sketch, "E14.7.0.2", {"start": v(205, -212) * mm, "end": v(215, -212) * mm});
            skLineSegment(sketch, "E14.7.0.3", {"start": v(205, -222) * mm, "end": v(215, -222) * mm});
            skLineSegment(sketch, "E14.7.1.0", {"start": v(215, -208) * mm, "end": v(215, -198) * mm});
            skLineSegment(sketch, "E14.7.1.1", {"start": v(205, -208) * mm, "end": v(205, -198) * mm});
            skLineSegment(sketch, "E14.7.1.2", {"start": v(205, -198) * mm, "end": v(215, -198) * mm});
            skLineSegment(sketch, "E14.7.1.3", {"start": v(205, -208) * mm, "end": v(215, -208) * mm});
            skLineSegment(sketch, "E14.7.2.0", {"start": v(215, -194) * mm, "end": v(215, -184) * mm});
            skLineSegment(sketch, "E14.7.2.1", {"start": v(205, -194) * mm, "end": v(205, -184) * mm});
            skLineSegment(sketch, "E14.7.2.2", {"start": v(205, -184) * mm, "end": v(215, -184) * mm});
            skLineSegment(sketch, "E14.7.2.3", {"start": v(205, -194) * mm, "end": v(215, -194) * mm});
            skLineSegment(sketch, "E14.7.3.0", {"start": v(215, -180) * mm, "end": v(215, -170) * mm});
            skLineSegment(sketch, "E14.7.3.1", {"start": v(205, -180) * mm, "end": v(205, -170) * mm});
            skLineSegment(sketch, "E14.7.3.2", {"start": v(205, -170) * mm, "end": v(215, -170) * mm});
            skLineSegment(sketch, "E14.7.3.3", {"start": v(205, -180) * mm, "end": v(215, -180) * mm});
            skLineSegment(sketch, "E14.7.4.0", {"start": v(215, -166) * mm, "end": v(215, -156) * mm});
            skLineSegment(sketch, "E14.7.4.1", {"start": v(205, -166) * mm, "end": v(205, -156) * mm});
            skLineSegment(sketch, "E14.7.4.2", {"start": v(205, -156) * mm, "end": v(215, -156) * mm});
            skLineSegment(sketch, "E14.7.4.3", {"start": v(205, -166) * mm, "end": v(215, -166) * mm});
            skLineSegment(sketch, "E14.7.5.0", {"start": v(215, -152) * mm, "end": v(215, -142) * mm});
            skLineSegment(sketch, "E14.7.5.1", {"start": v(205, -152) * mm, "end": v(205, -142) * mm});
            skLineSegment(sketch, "E14.7.5.2", {"start": v(205, -142) * mm, "end": v(215, -142) * mm});
            skLineSegment(sketch, "E14.7.5.3", {"start": v(205, -152) * mm, "end": v(215, -152) * mm});
            skLineSegment(sketch, "E14.7.6.0", {"start": v(215, -138) * mm, "end": v(215, -128) * mm});
            skLineSegment(sketch, "E14.7.6.1", {"start": v(205, -138) * mm, "end": v(205, -128) * mm});
            skLineSegment(sketch, "E14.7.6.2", {"start": v(205, -128) * mm, "end": v(215, -128) * mm});
            skLineSegment(sketch, "E14.7.6.3", {"start": v(205, -138) * mm, "end": v(215, -138) * mm});
            skLineSegment(sketch, "E14.7.7.0", {"start": v(215, -124) * mm, "end": v(215, -114) * mm});
            skLineSegment(sketch, "E14.7.7.1", {"start": v(205, -124) * mm, "end": v(205, -114) * mm});
            skLineSegment(sketch, "E14.7.7.2", {"start": v(205, -114) * mm, "end": v(215, -114) * mm});
            skLineSegment(sketch, "E14.7.7.3", {"start": v(205, -124) * mm, "end": v(215, -124) * mm});
            skLineSegment(sketch, "E14.7.8.0", {"start": v(215, -110) * mm, "end": v(215, -100) * mm});
            skLineSegment(sketch, "E14.7.8.1", {"start": v(205, -110) * mm, "end": v(205, -100) * mm});
            skLineSegment(sketch, "E14.7.8.2", {"start": v(205, -100) * mm, "end": v(215, -100) * mm});
            skLineSegment(sketch, "E14.7.8.3", {"start": v(205, -110) * mm, "end": v(215, -110) * mm});
            skLineSegment(sketch, "E14.7.9.0", {"start": v(215, -96) * mm, "end": v(215, -86) * mm});
            skLineSegment(sketch, "E14.7.9.1", {"start": v(205, -96) * mm, "end": v(205, -86) * mm});
            skLineSegment(sketch, "E14.7.9.2", {"start": v(205, -86) * mm, "end": v(215, -86) * mm});
            skLineSegment(sketch, "E14.7.9.3", {"start": v(205, -96) * mm, "end": v(215, -96) * mm});
            skLineSegment(sketch, "E14.7.10.0", {"start": v(215, -82) * mm, "end": v(215, -72) * mm});
            skLineSegment(sketch, "E14.7.10.1", {"start": v(205, -82) * mm, "end": v(205, -72) * mm});
            skLineSegment(sketch, "E14.7.10.2", {"start": v(205, -72) * mm, "end": v(215, -72) * mm});
            skLineSegment(sketch, "E14.7.10.3", {"start": v(205, -82) * mm, "end": v(215, -82) * mm});
            skLineSegment(sketch, "E14.7.11.0", {"start": v(215, -68) * mm, "end": v(215, -58) * mm});
            skLineSegment(sketch, "E14.7.11.1", {"start": v(205, -68) * mm, "end": v(205, -58) * mm});
            skLineSegment(sketch, "E14.7.11.2", {"start": v(205, -58) * mm, "end": v(215, -58) * mm});
            skLineSegment(sketch, "E14.7.11.3", {"start": v(205, -68) * mm, "end": v(215, -68) * mm});
            skLineSegment(sketch, "E14.7.12.0", {"start": v(215, -54) * mm, "end": v(215, -44) * mm});
            skLineSegment(sketch, "E14.7.12.1", {"start": v(205, -54) * mm, "end": v(205, -44) * mm});
            skLineSegment(sketch, "E14.7.12.2", {"start": v(205, -44) * mm, "end": v(215, -44) * mm});
            skLineSegment(sketch, "E14.7.12.3", {"start": v(205, -54) * mm, "end": v(215, -54) * mm});
            skLineSegment(sketch, "E14.7.13.0", {"start": v(215, -40) * mm, "end": v(215, -30) * mm});
            skLineSegment(sketch, "E14.7.13.1", {"start": v(205, -40) * mm, "end": v(205, -30) * mm});
            skLineSegment(sketch, "E14.7.13.2", {"start": v(205, -30) * mm, "end": v(215, -30) * mm});
            skLineSegment(sketch, "E14.7.13.3", {"start": v(205, -40) * mm, "end": v(215, -40) * mm});
            skLineSegment(sketch, "E14.7.14.0", {"start": v(215, -26) * mm, "end": v(215, -16) * mm});
            skLineSegment(sketch, "E14.7.14.1", {"start": v(205, -26) * mm, "end": v(205, -16) * mm});
            skLineSegment(sketch, "E14.7.14.2", {"start": v(205, -16) * mm, "end": v(215, -16) * mm});
            skLineSegment(sketch, "E14.7.14.3", {"start": v(205, -26) * mm, "end": v(215, -26) * mm});
            skLineSegment(sketch, "E14.7.15.0", {"start": v(215, -12) * mm, "end": v(215, -2) * mm});
            skLineSegment(sketch, "E14.7.15.1", {"start": v(205, -12) * mm, "end": v(205, -2) * mm});
            skLineSegment(sketch, "E14.7.15.2", {"start": v(205, -2) * mm, "end": v(215, -2) * mm});
            skLineSegment(sketch, "E14.7.15.3", {"start": v(205, -12) * mm, "end": v(215, -12) * mm});
            skLineSegment(sketch, "E14.7.16.0", {"start": v(215, 2) * mm, "end": v(215, 12) * mm});
            skLineSegment(sketch, "E14.7.16.1", {"start": v(205, 2) * mm, "end": v(205, 12) * mm});
            skLineSegment(sketch, "E14.7.16.2", {"start": v(205, 12) * mm, "end": v(215, 12) * mm});
            skLineSegment(sketch, "E14.7.16.3", {"start": v(205, 2) * mm, "end": v(215, 2) * mm});
            skLineSegment(sketch, "E14.7.17.0", {"start": v(215, 16) * mm, "end": v(215, 26) * mm});
            skLineSegment(sketch, "E14.7.17.1", {"start": v(205, 16) * mm, "end": v(205, 26) * mm});
            skLineSegment(sketch, "E14.7.17.2", {"start": v(205, 26) * mm, "end": v(215, 26) * mm});
            skLineSegment(sketch, "E14.7.17.3", {"start": v(205, 16) * mm, "end": v(215, 16) * mm});
            skLineSegment(sketch, "E14.7.18.0", {"start": v(215, 30) * mm, "end": v(215, 40) * mm});
            skLineSegment(sketch, "E14.7.18.1", {"start": v(205, 30) * mm, "end": v(205, 40) * mm});
            skLineSegment(sketch, "E14.7.18.2", {"start": v(205, 40) * mm, "end": v(215, 40) * mm});
            skLineSegment(sketch, "E14.7.18.3", {"start": v(205, 30) * mm, "end": v(215, 30) * mm});
            skLineSegment(sketch, "E14.7.19.0", {"start": v(215, 44) * mm, "end": v(215, 54) * mm});
            skLineSegment(sketch, "E14.7.19.1", {"start": v(205, 44) * mm, "end": v(205, 54) * mm});
            skLineSegment(sketch, "E14.7.19.2", {"start": v(205, 54) * mm, "end": v(215, 54) * mm});
            skLineSegment(sketch, "E14.7.19.3", {"start": v(205, 44) * mm, "end": v(215, 44) * mm});
            skLineSegment(sketch, "E14.7.20.0", {"start": v(215, 58) * mm, "end": v(215, 68) * mm});
            skLineSegment(sketch, "E14.7.20.1", {"start": v(205, 58) * mm, "end": v(205, 68) * mm});
            skLineSegment(sketch, "E14.7.20.2", {"start": v(205, 68) * mm, "end": v(215, 68) * mm});
            skLineSegment(sketch, "E14.7.20.3", {"start": v(205, 58) * mm, "end": v(215, 58) * mm});
            skLineSegment(sketch, "E14.7.21.0", {"start": v(215, 72) * mm, "end": v(215, 82) * mm});
            skLineSegment(sketch, "E14.7.21.1", {"start": v(205, 72) * mm, "end": v(205, 82) * mm});
            skLineSegment(sketch, "E14.7.21.2", {"start": v(205, 82) * mm, "end": v(215, 82) * mm});
            skLineSegment(sketch, "E14.7.21.3", {"start": v(205, 72) * mm, "end": v(215, 72) * mm});
            skLineSegment(sketch, "E14.7.22.0", {"start": v(215, 86) * mm, "end": v(215, 96) * mm});
            skLineSegment(sketch, "E14.7.22.1", {"start": v(205, 86) * mm, "end": v(205, 96) * mm});
            skLineSegment(sketch, "E14.7.22.2", {"start": v(205, 96) * mm, "end": v(215, 96) * mm});
            skLineSegment(sketch, "E14.7.22.3", {"start": v(205, 86) * mm, "end": v(215, 86) * mm});
            skLineSegment(sketch, "E14.7.23.0", {"start": v(215, 100) * mm, "end": v(215, 110) * mm});
            skLineSegment(sketch, "E14.7.23.1", {"start": v(205, 100) * mm, "end": v(205, 110) * mm});
            skLineSegment(sketch, "E14.7.23.2", {"start": v(205, 110) * mm, "end": v(215, 110) * mm});
            skLineSegment(sketch, "E14.7.23.3", {"start": v(205, 100) * mm, "end": v(215, 100) * mm});
            skLineSegment(sketch, "E14.7.24.0", {"start": v(215, 114) * mm, "end": v(215, 124) * mm});
            skLineSegment(sketch, "E14.7.24.1", {"start": v(205, 114) * mm, "end": v(205, 124) * mm});
            skLineSegment(sketch, "E14.7.24.2", {"start": v(205, 124) * mm, "end": v(215, 124) * mm});
            skLineSegment(sketch, "E14.7.24.3", {"start": v(205, 114) * mm, "end": v(215, 114) * mm});
            skLineSegment(sketch, "E14.7.25.0", {"start": v(215, 128) * mm, "end": v(215, 138) * mm});
            skLineSegment(sketch, "E14.7.25.1", {"start": v(205, 128) * mm, "end": v(205, 138) * mm});
            skLineSegment(sketch, "E14.7.25.2", {"start": v(205, 138) * mm, "end": v(215, 138) * mm});
            skLineSegment(sketch, "E14.7.25.3", {"start": v(205, 128) * mm, "end": v(215, 128) * mm});
            skLineSegment(sketch, "E14.7.26.0", {"start": v(215, 142) * mm, "end": v(215, 152) * mm});
            skLineSegment(sketch, "E14.7.26.1", {"start": v(205, 142) * mm, "end": v(205, 152) * mm});
            skLineSegment(sketch, "E14.7.26.2", {"start": v(205, 152) * mm, "end": v(215, 152) * mm});
            skLineSegment(sketch, "E14.7.26.3", {"start": v(205, 142) * mm, "end": v(215, 142) * mm});
            skLineSegment(sketch, "E14.7.27.0", {"start": v(215, 156) * mm, "end": v(215, 166) * mm});
            skLineSegment(sketch, "E14.7.27.1", {"start": v(205, 156) * mm, "end": v(205, 166) * mm});
            skLineSegment(sketch, "E14.7.27.2", {"start": v(205, 166) * mm, "end": v(215, 166) * mm});
            skLineSegment(sketch, "E14.7.27.3", {"start": v(205, 156) * mm, "end": v(215, 156) * mm});
            skLineSegment(sketch, "E14.7.28.0", {"start": v(215, 170) * mm, "end": v(215, 180) * mm});
            skLineSegment(sketch, "E14.7.28.1", {"start": v(205, 170) * mm, "end": v(205, 180) * mm});
            skLineSegment(sketch, "E14.7.28.2", {"start": v(205, 180) * mm, "end": v(215, 180) * mm});
            skLineSegment(sketch, "E14.7.28.3", {"start": v(205, 170) * mm, "end": v(215, 170) * mm});
            skLineSegment(sketch, "E14.7.29.0", {"start": v(215, 184) * mm, "end": v(215, 194) * mm});
            skLineSegment(sketch, "E14.7.29.1", {"start": v(205, 184) * mm, "end": v(205, 194) * mm});
            skLineSegment(sketch, "E14.7.29.2", {"start": v(205, 194) * mm, "end": v(215, 194) * mm});
            skLineSegment(sketch, "E14.7.29.3", {"start": v(205, 184) * mm, "end": v(215, 184) * mm});
            skLineSegment(sketch, "E14.7.30.0", {"start": v(215, 198) * mm, "end": v(215, 208) * mm});
            skLineSegment(sketch, "E14.7.30.1", {"start": v(205, 198) * mm, "end": v(205, 208) * mm});
            skLineSegment(sketch, "E14.7.30.2", {"start": v(205, 208) * mm, "end": v(215, 208) * mm});
            skLineSegment(sketch, "E14.7.30.3", {"start": v(205, 198) * mm, "end": v(215, 198) * mm});
            skLineSegment(sketch, "E14.7.31.0", {"start": v(215, 212) * mm, "end": v(215, 222) * mm});
            skLineSegment(sketch, "E14.7.31.1", {"start": v(205, 212) * mm, "end": v(205, 222) * mm});
            skLineSegment(sketch, "E14.7.31.2", {"start": v(205, 222) * mm, "end": v(215, 222) * mm});
            skLineSegment(sketch, "E14.7.31.3", {"start": v(205, 212) * mm, "end": v(215, 212) * mm});
            skLineSegment(sketch, "E14.8.0.0", {"start": v(229, -222) * mm, "end": v(229, -212) * mm});
            skLineSegment(sketch, "E14.8.0.1", {"start": v(219, -222) * mm, "end": v(219, -212) * mm});
            skLineSegment(sketch, "E14.8.0.2", {"start": v(219, -212) * mm, "end": v(229, -212) * mm});
            skLineSegment(sketch, "E14.8.0.3", {"start": v(219, -222) * mm, "end": v(229, -222) * mm});
            skLineSegment(sketch, "E14.8.1.0", {"start": v(229, -208) * mm, "end": v(229, -198) * mm});
            skLineSegment(sketch, "E14.8.1.1", {"start": v(219, -208) * mm, "end": v(219, -198) * mm});
            skLineSegment(sketch, "E14.8.1.2", {"start": v(219, -198) * mm, "end": v(229, -198) * mm});
            skLineSegment(sketch, "E14.8.1.3", {"start": v(219, -208) * mm, "end": v(229, -208) * mm});
            skLineSegment(sketch, "E14.8.2.0", {"start": v(229, -194) * mm, "end": v(229, -184) * mm});
            skLineSegment(sketch, "E14.8.2.1", {"start": v(219, -194) * mm, "end": v(219, -184) * mm});
            skLineSegment(sketch, "E14.8.2.2", {"start": v(219, -184) * mm, "end": v(229, -184) * mm});
            skLineSegment(sketch, "E14.8.2.3", {"start": v(219, -194) * mm, "end": v(229, -194) * mm});
            skLineSegment(sketch, "E14.8.3.0", {"start": v(229, -180) * mm, "end": v(229, -170) * mm});
            skLineSegment(sketch, "E14.8.3.1", {"start": v(219, -180) * mm, "end": v(219, -170) * mm});
            skLineSegment(sketch, "E14.8.3.2", {"start": v(219, -170) * mm, "end": v(229, -170) * mm});
            skLineSegment(sketch, "E14.8.3.3", {"start": v(219, -180) * mm, "end": v(229, -180) * mm});
            skLineSegment(sketch, "E14.8.4.0", {"start": v(229, -166) * mm, "end": v(229, -156) * mm});
            skLineSegment(sketch, "E14.8.4.1", {"start": v(219, -166) * mm, "end": v(219, -156) * mm});
            skLineSegment(sketch, "E14.8.4.2", {"start": v(219, -156) * mm, "end": v(229, -156) * mm});
            skLineSegment(sketch, "E14.8.4.3", {"start": v(219, -166) * mm, "end": v(229, -166) * mm});
            skLineSegment(sketch, "E14.8.5.0", {"start": v(229, -152) * mm, "end": v(229, -142) * mm});
            skLineSegment(sketch, "E14.8.5.1", {"start": v(219, -152) * mm, "end": v(219, -142) * mm});
            skLineSegment(sketch, "E14.8.5.2", {"start": v(219, -142) * mm, "end": v(229, -142) * mm});
            skLineSegment(sketch, "E14.8.5.3", {"start": v(219, -152) * mm, "end": v(229, -152) * mm});
            skLineSegment(sketch, "E14.8.6.0", {"start": v(229, -138) * mm, "end": v(229, -128) * mm});
            skLineSegment(sketch, "E14.8.6.1", {"start": v(219, -138) * mm, "end": v(219, -128) * mm});
            skLineSegment(sketch, "E14.8.6.2", {"start": v(219, -128) * mm, "end": v(229, -128) * mm});
            skLineSegment(sketch, "E14.8.6.3", {"start": v(219, -138) * mm, "end": v(229, -138) * mm});
            skLineSegment(sketch, "E14.8.7.0", {"start": v(229, -124) * mm, "end": v(229, -114) * mm});
            skLineSegment(sketch, "E14.8.7.1", {"start": v(219, -124) * mm, "end": v(219, -114) * mm});
            skLineSegment(sketch, "E14.8.7.2", {"start": v(219, -114) * mm, "end": v(229, -114) * mm});
            skLineSegment(sketch, "E14.8.7.3", {"start": v(219, -124) * mm, "end": v(229, -124) * mm});
            skLineSegment(sketch, "E14.8.8.0", {"start": v(229, -110) * mm, "end": v(229, -100) * mm});
            skLineSegment(sketch, "E14.8.8.1", {"start": v(219, -110) * mm, "end": v(219, -100) * mm});
            skLineSegment(sketch, "E14.8.8.2", {"start": v(219, -100) * mm, "end": v(229, -100) * mm});
            skLineSegment(sketch, "E14.8.8.3", {"start": v(219, -110) * mm, "end": v(229, -110) * mm});
            skLineSegment(sketch, "E14.8.9.0", {"start": v(229, -96) * mm, "end": v(229, -86) * mm});
            skLineSegment(sketch, "E14.8.9.1", {"start": v(219, -96) * mm, "end": v(219, -86) * mm});
            skLineSegment(sketch, "E14.8.9.2", {"start": v(219, -86) * mm, "end": v(229, -86) * mm});
            skLineSegment(sketch, "E14.8.9.3", {"start": v(219, -96) * mm, "end": v(229, -96) * mm});
            skLineSegment(sketch, "E14.8.10.0", {"start": v(229, -82) * mm, "end": v(229, -72) * mm});
            skLineSegment(sketch, "E14.8.10.1", {"start": v(219, -82) * mm, "end": v(219, -72) * mm});
            skLineSegment(sketch, "E14.8.10.2", {"start": v(219, -72) * mm, "end": v(229, -72) * mm});
            skLineSegment(sketch, "E14.8.10.3", {"start": v(219, -82) * mm, "end": v(229, -82) * mm});
            skLineSegment(sketch, "E14.8.11.0", {"start": v(229, -68) * mm, "end": v(229, -58) * mm});
            skLineSegment(sketch, "E14.8.11.1", {"start": v(219, -68) * mm, "end": v(219, -58) * mm});
            skLineSegment(sketch, "E14.8.11.2", {"start": v(219, -58) * mm, "end": v(229, -58) * mm});
            skLineSegment(sketch, "E14.8.11.3", {"start": v(219, -68) * mm, "end": v(229, -68) * mm});
            skLineSegment(sketch, "E14.8.12.0", {"start": v(229, -54) * mm, "end": v(229, -44) * mm});
            skLineSegment(sketch, "E14.8.12.1", {"start": v(219, -54) * mm, "end": v(219, -44) * mm});
            skLineSegment(sketch, "E14.8.12.2", {"start": v(219, -44) * mm, "end": v(229, -44) * mm});
            skLineSegment(sketch, "E14.8.12.3", {"start": v(219, -54) * mm, "end": v(229, -54) * mm});
            skLineSegment(sketch, "E14.8.13.0", {"start": v(229, -40) * mm, "end": v(229, -30) * mm});
            skLineSegment(sketch, "E14.8.13.1", {"start": v(219, -40) * mm, "end": v(219, -30) * mm});
            skLineSegment(sketch, "E14.8.13.2", {"start": v(219, -30) * mm, "end": v(229, -30) * mm});
            skLineSegment(sketch, "E14.8.13.3", {"start": v(219, -40) * mm, "end": v(229, -40) * mm});
            skLineSegment(sketch, "E14.8.14.0", {"start": v(229, -26) * mm, "end": v(229, -16) * mm});
            skLineSegment(sketch, "E14.8.14.1", {"start": v(219, -26) * mm, "end": v(219, -16) * mm});
            skLineSegment(sketch, "E14.8.14.2", {"start": v(219, -16) * mm, "end": v(229, -16) * mm});
            skLineSegment(sketch, "E14.8.14.3", {"start": v(219, -26) * mm, "end": v(229, -26) * mm});
            skLineSegment(sketch, "E14.8.15.0", {"start": v(229, -12) * mm, "end": v(229, -2) * mm});
            skLineSegment(sketch, "E14.8.15.1", {"start": v(219, -12) * mm, "end": v(219, -2) * mm});
            skLineSegment(sketch, "E14.8.15.2", {"start": v(219, -2) * mm, "end": v(229, -2) * mm});
            skLineSegment(sketch, "E14.8.15.3", {"start": v(219, -12) * mm, "end": v(229, -12) * mm});
            skLineSegment(sketch, "E14.8.16.0", {"start": v(229, 2) * mm, "end": v(229, 12) * mm});
            skLineSegment(sketch, "E14.8.16.1", {"start": v(219, 2) * mm, "end": v(219, 12) * mm});
            skLineSegment(sketch, "E14.8.16.2", {"start": v(219, 12) * mm, "end": v(229, 12) * mm});
            skLineSegment(sketch, "E14.8.16.3", {"start": v(219, 2) * mm, "end": v(229, 2) * mm});
            skLineSegment(sketch, "E14.8.17.0", {"start": v(229, 16) * mm, "end": v(229, 26) * mm});
            skLineSegment(sketch, "E14.8.17.1", {"start": v(219, 16) * mm, "end": v(219, 26) * mm});
            skLineSegment(sketch, "E14.8.17.2", {"start": v(219, 26) * mm, "end": v(229, 26) * mm});
            skLineSegment(sketch, "E14.8.17.3", {"start": v(219, 16) * mm, "end": v(229, 16) * mm});
            skLineSegment(sketch, "E14.8.18.0", {"start": v(229, 30) * mm, "end": v(229, 40) * mm});
            skLineSegment(sketch, "E14.8.18.1", {"start": v(219, 30) * mm, "end": v(219, 40) * mm});
            skLineSegment(sketch, "E14.8.18.2", {"start": v(219, 40) * mm, "end": v(229, 40) * mm});
            skLineSegment(sketch, "E14.8.18.3", {"start": v(219, 30) * mm, "end": v(229, 30) * mm});
            skLineSegment(sketch, "E14.8.19.0", {"start": v(229, 44) * mm, "end": v(229, 54) * mm});
            skLineSegment(sketch, "E14.8.19.1", {"start": v(219, 44) * mm, "end": v(219, 54) * mm});
            skLineSegment(sketch, "E14.8.19.2", {"start": v(219, 54) * mm, "end": v(229, 54) * mm});
            skLineSegment(sketch, "E14.8.19.3", {"start": v(219, 44) * mm, "end": v(229, 44) * mm});
            skLineSegment(sketch, "E14.8.20.0", {"start": v(229, 58) * mm, "end": v(229, 68) * mm});
            skLineSegment(sketch, "E14.8.20.1", {"start": v(219, 58) * mm, "end": v(219, 68) * mm});
            skLineSegment(sketch, "E14.8.20.2", {"start": v(219, 68) * mm, "end": v(229, 68) * mm});
            skLineSegment(sketch, "E14.8.20.3", {"start": v(219, 58) * mm, "end": v(229, 58) * mm});
            skLineSegment(sketch, "E14.8.21.0", {"start": v(229, 72) * mm, "end": v(229, 82) * mm});
            skLineSegment(sketch, "E14.8.21.1", {"start": v(219, 72) * mm, "end": v(219, 82) * mm});
            skLineSegment(sketch, "E14.8.21.2", {"start": v(219, 82) * mm, "end": v(229, 82) * mm});
            skLineSegment(sketch, "E14.8.21.3", {"start": v(219, 72) * mm, "end": v(229, 72) * mm});
            skLineSegment(sketch, "E14.8.22.0", {"start": v(229, 86) * mm, "end": v(229, 96) * mm});
            skLineSegment(sketch, "E14.8.22.1", {"start": v(219, 86) * mm, "end": v(219, 96) * mm});
            skLineSegment(sketch, "E14.8.22.2", {"start": v(219, 96) * mm, "end": v(229, 96) * mm});
            skLineSegment(sketch, "E14.8.22.3", {"start": v(219, 86) * mm, "end": v(229, 86) * mm});
            skLineSegment(sketch, "E14.8.23.0", {"start": v(229, 100) * mm, "end": v(229, 110) * mm});
            skLineSegment(sketch, "E14.8.23.1", {"start": v(219, 100) * mm, "end": v(219, 110) * mm});
            skLineSegment(sketch, "E14.8.23.2", {"start": v(219, 110) * mm, "end": v(229, 110) * mm});
            skLineSegment(sketch, "E14.8.23.3", {"start": v(219, 100) * mm, "end": v(229, 100) * mm});
            skLineSegment(sketch, "E14.8.24.0", {"start": v(229, 114) * mm, "end": v(229, 124) * mm});
            skLineSegment(sketch, "E14.8.24.1", {"start": v(219, 114) * mm, "end": v(219, 124) * mm});
            skLineSegment(sketch, "E14.8.24.2", {"start": v(219, 124) * mm, "end": v(229, 124) * mm});
            skLineSegment(sketch, "E14.8.24.3", {"start": v(219, 114) * mm, "end": v(229, 114) * mm});
            skLineSegment(sketch, "E14.8.25.0", {"start": v(229, 128) * mm, "end": v(229, 138) * mm});
            skLineSegment(sketch, "E14.8.25.1", {"start": v(219, 128) * mm, "end": v(219, 138) * mm});
            skLineSegment(sketch, "E14.8.25.2", {"start": v(219, 138) * mm, "end": v(229, 138) * mm});
            skLineSegment(sketch, "E14.8.25.3", {"start": v(219, 128) * mm, "end": v(229, 128) * mm});
            skLineSegment(sketch, "E14.8.26.0", {"start": v(229, 142) * mm, "end": v(229, 152) * mm});
            skLineSegment(sketch, "E14.8.26.1", {"start": v(219, 142) * mm, "end": v(219, 152) * mm});
            skLineSegment(sketch, "E14.8.26.2", {"start": v(219, 152) * mm, "end": v(229, 152) * mm});
            skLineSegment(sketch, "E14.8.26.3", {"start": v(219, 142) * mm, "end": v(229, 142) * mm});
            skLineSegment(sketch, "E14.8.27.0", {"start": v(229, 156) * mm, "end": v(229, 166) * mm});
            skLineSegment(sketch, "E14.8.27.1", {"start": v(219, 156) * mm, "end": v(219, 166) * mm});
            skLineSegment(sketch, "E14.8.27.2", {"start": v(219, 166) * mm, "end": v(229, 166) * mm});
            skLineSegment(sketch, "E14.8.27.3", {"start": v(219, 156) * mm, "end": v(229, 156) * mm});
            skLineSegment(sketch, "E14.8.28.0", {"start": v(229, 170) * mm, "end": v(229, 180) * mm});
            skLineSegment(sketch, "E14.8.28.1", {"start": v(219, 170) * mm, "end": v(219, 180) * mm});
            skLineSegment(sketch, "E14.8.28.2", {"start": v(219, 180) * mm, "end": v(229, 180) * mm});
            skLineSegment(sketch, "E14.8.28.3", {"start": v(219, 170) * mm, "end": v(229, 170) * mm});
            skLineSegment(sketch, "E14.8.29.0", {"start": v(229, 184) * mm, "end": v(229, 194) * mm});
            skLineSegment(sketch, "E14.8.29.1", {"start": v(219, 184) * mm, "end": v(219, 194) * mm});
            skLineSegment(sketch, "E14.8.29.2", {"start": v(219, 194) * mm, "end": v(229, 194) * mm});
            skLineSegment(sketch, "E14.8.29.3", {"start": v(219, 184) * mm, "end": v(229, 184) * mm});
            skLineSegment(sketch, "E14.8.30.0", {"start": v(229, 198) * mm, "end": v(229, 208) * mm});
            skLineSegment(sketch, "E14.8.30.1", {"start": v(219, 198) * mm, "end": v(219, 208) * mm});
            skLineSegment(sketch, "E14.8.30.2", {"start": v(219, 208) * mm, "end": v(229, 208) * mm});
            skLineSegment(sketch, "E14.8.30.3", {"start": v(219, 198) * mm, "end": v(229, 198) * mm});
            skLineSegment(sketch, "E14.8.31.0", {"start": v(229, 212) * mm, "end": v(229, 222) * mm});
            skLineSegment(sketch, "E14.8.31.1", {"start": v(219, 212) * mm, "end": v(219, 222) * mm});
            skLineSegment(sketch, "E14.8.31.2", {"start": v(219, 222) * mm, "end": v(229, 222) * mm});
            skLineSegment(sketch, "E14.8.31.3", {"start": v(219, 212) * mm, "end": v(229, 212) * mm});
            skLineSegment(sketch, "E14.9.0.0", {"start": v(243, -222) * mm, "end": v(243, -212) * mm});
            skLineSegment(sketch, "E14.9.0.1", {"start": v(233, -222) * mm, "end": v(233, -212) * mm});
            skLineSegment(sketch, "E14.9.0.2", {"start": v(233, -212) * mm, "end": v(243, -212) * mm});
            skLineSegment(sketch, "E14.9.0.3", {"start": v(233, -222) * mm, "end": v(243, -222) * mm});
            skLineSegment(sketch, "E14.9.1.0", {"start": v(243, -208) * mm, "end": v(243, -198) * mm});
            skLineSegment(sketch, "E14.9.1.1", {"start": v(233, -208) * mm, "end": v(233, -198) * mm});
            skLineSegment(sketch, "E14.9.1.2", {"start": v(233, -198) * mm, "end": v(243, -198) * mm});
            skLineSegment(sketch, "E14.9.1.3", {"start": v(233, -208) * mm, "end": v(243, -208) * mm});
            skLineSegment(sketch, "E14.9.2.0", {"start": v(243, -194) * mm, "end": v(243, -184) * mm});
            skLineSegment(sketch, "E14.9.2.1", {"start": v(233, -194) * mm, "end": v(233, -184) * mm});
            skLineSegment(sketch, "E14.9.2.2", {"start": v(233, -184) * mm, "end": v(243, -184) * mm});
            skLineSegment(sketch, "E14.9.2.3", {"start": v(233, -194) * mm, "end": v(243, -194) * mm});
            skLineSegment(sketch, "E14.9.3.0", {"start": v(243, -180) * mm, "end": v(243, -170) * mm});
            skLineSegment(sketch, "E14.9.3.1", {"start": v(233, -180) * mm, "end": v(233, -170) * mm});
            skLineSegment(sketch, "E14.9.3.2", {"start": v(233, -170) * mm, "end": v(243, -170) * mm});
            skLineSegment(sketch, "E14.9.3.3", {"start": v(233, -180) * mm, "end": v(243, -180) * mm});
            skLineSegment(sketch, "E14.9.4.0", {"start": v(243, -166) * mm, "end": v(243, -156) * mm});
            skLineSegment(sketch, "E14.9.4.1", {"start": v(233, -166) * mm, "end": v(233, -156) * mm});
            skLineSegment(sketch, "E14.9.4.2", {"start": v(233, -156) * mm, "end": v(243, -156) * mm});
            skLineSegment(sketch, "E14.9.4.3", {"start": v(233, -166) * mm, "end": v(243, -166) * mm});
            skLineSegment(sketch, "E14.9.5.0", {"start": v(243, -152) * mm, "end": v(243, -142) * mm});
            skLineSegment(sketch, "E14.9.5.1", {"start": v(233, -152) * mm, "end": v(233, -142) * mm});
            skLineSegment(sketch, "E14.9.5.2", {"start": v(233, -142) * mm, "end": v(243, -142) * mm});
            skLineSegment(sketch, "E14.9.5.3", {"start": v(233, -152) * mm, "end": v(243, -152) * mm});
            skLineSegment(sketch, "E14.9.6.0", {"start": v(243, -138) * mm, "end": v(243, -128) * mm});
            skLineSegment(sketch, "E14.9.6.1", {"start": v(233, -138) * mm, "end": v(233, -128) * mm});
            skLineSegment(sketch, "E14.9.6.2", {"start": v(233, -128) * mm, "end": v(243, -128) * mm});
            skLineSegment(sketch, "E14.9.6.3", {"start": v(233, -138) * mm, "end": v(243, -138) * mm});
            skLineSegment(sketch, "E14.9.7.0", {"start": v(243, -124) * mm, "end": v(243, -114) * mm});
            skLineSegment(sketch, "E14.9.7.1", {"start": v(233, -124) * mm, "end": v(233, -114) * mm});
            skLineSegment(sketch, "E14.9.7.2", {"start": v(233, -114) * mm, "end": v(243, -114) * mm});
            skLineSegment(sketch, "E14.9.7.3", {"start": v(233, -124) * mm, "end": v(243, -124) * mm});
            skLineSegment(sketch, "E14.9.8.0", {"start": v(243, -110) * mm, "end": v(243, -100) * mm});
            skLineSegment(sketch, "E14.9.8.1", {"start": v(233, -110) * mm, "end": v(233, -100) * mm});
            skLineSegment(sketch, "E14.9.8.2", {"start": v(233, -100) * mm, "end": v(243, -100) * mm});
            skLineSegment(sketch, "E14.9.8.3", {"start": v(233, -110) * mm, "end": v(243, -110) * mm});
            skLineSegment(sketch, "E14.9.9.0", {"start": v(243, -96) * mm, "end": v(243, -86) * mm});
            skLineSegment(sketch, "E14.9.9.1", {"start": v(233, -96) * mm, "end": v(233, -86) * mm});
            skLineSegment(sketch, "E14.9.9.2", {"start": v(233, -86) * mm, "end": v(243, -86) * mm});
            skLineSegment(sketch, "E14.9.9.3", {"start": v(233, -96) * mm, "end": v(243, -96) * mm});
            skLineSegment(sketch, "E14.9.10.0", {"start": v(243, -82) * mm, "end": v(243, -72) * mm});
            skLineSegment(sketch, "E14.9.10.1", {"start": v(233, -82) * mm, "end": v(233, -72) * mm});
            skLineSegment(sketch, "E14.9.10.2", {"start": v(233, -72) * mm, "end": v(243, -72) * mm});
            skLineSegment(sketch, "E14.9.10.3", {"start": v(233, -82) * mm, "end": v(243, -82) * mm});
            skLineSegment(sketch, "E14.9.11.0", {"start": v(243, -68) * mm, "end": v(243, -58) * mm});
            skLineSegment(sketch, "E14.9.11.1", {"start": v(233, -68) * mm, "end": v(233, -58) * mm});
            skLineSegment(sketch, "E14.9.11.2", {"start": v(233, -58) * mm, "end": v(243, -58) * mm});
            skLineSegment(sketch, "E14.9.11.3", {"start": v(233, -68) * mm, "end": v(243, -68) * mm});
            skLineSegment(sketch, "E14.9.12.0", {"start": v(243, -54) * mm, "end": v(243, -44) * mm});
            skLineSegment(sketch, "E14.9.12.1", {"start": v(233, -54) * mm, "end": v(233, -44) * mm});
            skLineSegment(sketch, "E14.9.12.2", {"start": v(233, -44) * mm, "end": v(243, -44) * mm});
            skLineSegment(sketch, "E14.9.12.3", {"start": v(233, -54) * mm, "end": v(243, -54) * mm});
            skLineSegment(sketch, "E14.9.13.0", {"start": v(243, -40) * mm, "end": v(243, -30) * mm});
            skLineSegment(sketch, "E14.9.13.1", {"start": v(233, -40) * mm, "end": v(233, -30) * mm});
            skLineSegment(sketch, "E14.9.13.2", {"start": v(233, -30) * mm, "end": v(243, -30) * mm});
            skLineSegment(sketch, "E14.9.13.3", {"start": v(233, -40) * mm, "end": v(243, -40) * mm});
            skLineSegment(sketch, "E14.9.14.0", {"start": v(243, -26) * mm, "end": v(243, -16) * mm});
            skLineSegment(sketch, "E14.9.14.1", {"start": v(233, -26) * mm, "end": v(233, -16) * mm});
            skLineSegment(sketch, "E14.9.14.2", {"start": v(233, -16) * mm, "end": v(243, -16) * mm});
            skLineSegment(sketch, "E14.9.14.3", {"start": v(233, -26) * mm, "end": v(243, -26) * mm});
            skLineSegment(sketch, "E14.9.15.0", {"start": v(243, -12) * mm, "end": v(243, -2) * mm});
            skLineSegment(sketch, "E14.9.15.1", {"start": v(233, -12) * mm, "end": v(233, -2) * mm});
            skLineSegment(sketch, "E14.9.15.2", {"start": v(233, -2) * mm, "end": v(243, -2) * mm});
            skLineSegment(sketch, "E14.9.15.3", {"start": v(233, -12) * mm, "end": v(243, -12) * mm});
            skLineSegment(sketch, "E14.9.16.0", {"start": v(243, 2) * mm, "end": v(243, 12) * mm});
            skLineSegment(sketch, "E14.9.16.1", {"start": v(233, 2) * mm, "end": v(233, 12) * mm});
            skLineSegment(sketch, "E14.9.16.2", {"start": v(233, 12) * mm, "end": v(243, 12) * mm});
            skLineSegment(sketch, "E14.9.16.3", {"start": v(233, 2) * mm, "end": v(243, 2) * mm});
            skLineSegment(sketch, "E14.9.17.0", {"start": v(243, 16) * mm, "end": v(243, 26) * mm});
            skLineSegment(sketch, "E14.9.17.1", {"start": v(233, 16) * mm, "end": v(233, 26) * mm});
            skLineSegment(sketch, "E14.9.17.2", {"start": v(233, 26) * mm, "end": v(243, 26) * mm});
            skLineSegment(sketch, "E14.9.17.3", {"start": v(233, 16) * mm, "end": v(243, 16) * mm});
            skLineSegment(sketch, "E14.9.18.0", {"start": v(243, 30) * mm, "end": v(243, 40) * mm});
            skLineSegment(sketch, "E14.9.18.1", {"start": v(233, 30) * mm, "end": v(233, 40) * mm});
            skLineSegment(sketch, "E14.9.18.2", {"start": v(233, 40) * mm, "end": v(243, 40) * mm});
            skLineSegment(sketch, "E14.9.18.3", {"start": v(233, 30) * mm, "end": v(243, 30) * mm});
            skLineSegment(sketch, "E14.9.19.0", {"start": v(243, 44) * mm, "end": v(243, 54) * mm});
            skLineSegment(sketch, "E14.9.19.1", {"start": v(233, 44) * mm, "end": v(233, 54) * mm});
            skLineSegment(sketch, "E14.9.19.2", {"start": v(233, 54) * mm, "end": v(243, 54) * mm});
            skLineSegment(sketch, "E14.9.19.3", {"start": v(233, 44) * mm, "end": v(243, 44) * mm});
            skLineSegment(sketch, "E14.9.20.0", {"start": v(243, 58) * mm, "end": v(243, 68) * mm});
            skLineSegment(sketch, "E14.9.20.1", {"start": v(233, 58) * mm, "end": v(233, 68) * mm});
            skLineSegment(sketch, "E14.9.20.2", {"start": v(233, 68) * mm, "end": v(243, 68) * mm});
            skLineSegment(sketch, "E14.9.20.3", {"start": v(233, 58) * mm, "end": v(243, 58) * mm});
            skLineSegment(sketch, "E14.9.21.0", {"start": v(243, 72) * mm, "end": v(243, 82) * mm});
            skLineSegment(sketch, "E14.9.21.1", {"start": v(233, 72) * mm, "end": v(233, 82) * mm});
            skLineSegment(sketch, "E14.9.21.2", {"start": v(233, 82) * mm, "end": v(243, 82) * mm});
            skLineSegment(sketch, "E14.9.21.3", {"start": v(233, 72) * mm, "end": v(243, 72) * mm});
            skLineSegment(sketch, "E14.9.22.0", {"start": v(243, 86) * mm, "end": v(243, 96) * mm});
            skLineSegment(sketch, "E14.9.22.1", {"start": v(233, 86) * mm, "end": v(233, 96) * mm});
            skLineSegment(sketch, "E14.9.22.2", {"start": v(233, 96) * mm, "end": v(243, 96) * mm});
            skLineSegment(sketch, "E14.9.22.3", {"start": v(233, 86) * mm, "end": v(243, 86) * mm});
            skLineSegment(sketch, "E14.9.23.0", {"start": v(243, 100) * mm, "end": v(243, 110) * mm});
            skLineSegment(sketch, "E14.9.23.1", {"start": v(233, 100) * mm, "end": v(233, 110) * mm});
            skLineSegment(sketch, "E14.9.23.2", {"start": v(233, 110) * mm, "end": v(243, 110) * mm});
            skLineSegment(sketch, "E14.9.23.3", {"start": v(233, 100) * mm, "end": v(243, 100) * mm});
            skLineSegment(sketch, "E14.9.24.0", {"start": v(243, 114) * mm, "end": v(243, 124) * mm});
            skLineSegment(sketch, "E14.9.24.1", {"start": v(233, 114) * mm, "end": v(233, 124) * mm});
            skLineSegment(sketch, "E14.9.24.2", {"start": v(233, 124) * mm, "end": v(243, 124) * mm});
            skLineSegment(sketch, "E14.9.24.3", {"start": v(233, 114) * mm, "end": v(243, 114) * mm});
            skLineSegment(sketch, "E14.9.25.0", {"start": v(243, 128) * mm, "end": v(243, 138) * mm});
            skLineSegment(sketch, "E14.9.25.1", {"start": v(233, 128) * mm, "end": v(233, 138) * mm});
            skLineSegment(sketch, "E14.9.25.2", {"start": v(233, 138) * mm, "end": v(243, 138) * mm});
            skLineSegment(sketch, "E14.9.25.3", {"start": v(233, 128) * mm, "end": v(243, 128) * mm});
            skLineSegment(sketch, "E14.9.26.0", {"start": v(243, 142) * mm, "end": v(243, 152) * mm});
            skLineSegment(sketch, "E14.9.26.1", {"start": v(233, 142) * mm, "end": v(233, 152) * mm});
            skLineSegment(sketch, "E14.9.26.2", {"start": v(233, 152) * mm, "end": v(243, 152) * mm});
            skLineSegment(sketch, "E14.9.26.3", {"start": v(233, 142) * mm, "end": v(243, 142) * mm});
            skLineSegment(sketch, "E14.9.27.0", {"start": v(243, 156) * mm, "end": v(243, 166) * mm});
            skLineSegment(sketch, "E14.9.27.1", {"start": v(233, 156) * mm, "end": v(233, 166) * mm});
            skLineSegment(sketch, "E14.9.27.2", {"start": v(233, 166) * mm, "end": v(243, 166) * mm});
            skLineSegment(sketch, "E14.9.27.3", {"start": v(233, 156) * mm, "end": v(243, 156) * mm});
            skLineSegment(sketch, "E14.9.28.0", {"start": v(243, 170) * mm, "end": v(243, 180) * mm});
            skLineSegment(sketch, "E14.9.28.1", {"start": v(233, 170) * mm, "end": v(233, 180) * mm});
            skLineSegment(sketch, "E14.9.28.2", {"start": v(233, 180) * mm, "end": v(243, 180) * mm});
            skLineSegment(sketch, "E14.9.28.3", {"start": v(233, 170) * mm, "end": v(243, 170) * mm});
            skLineSegment(sketch, "E14.9.29.0", {"start": v(243, 184) * mm, "end": v(243, 194) * mm});
            skLineSegment(sketch, "E14.9.29.1", {"start": v(233, 184) * mm, "end": v(233, 194) * mm});
            skLineSegment(sketch, "E14.9.29.2", {"start": v(233, 194) * mm, "end": v(243, 194) * mm});
            skLineSegment(sketch, "E14.9.29.3", {"start": v(233, 184) * mm, "end": v(243, 184) * mm});
            skLineSegment(sketch, "E14.9.30.0", {"start": v(243, 198) * mm, "end": v(243, 208) * mm});
            skLineSegment(sketch, "E14.9.30.1", {"start": v(233, 198) * mm, "end": v(233, 208) * mm});
            skLineSegment(sketch, "E14.9.30.2", {"start": v(233, 208) * mm, "end": v(243, 208) * mm});
            skLineSegment(sketch, "E14.9.30.3", {"start": v(233, 198) * mm, "end": v(243, 198) * mm});
            skLineSegment(sketch, "E14.9.31.0", {"start": v(243, 212) * mm, "end": v(243, 222) * mm});
            skLineSegment(sketch, "E14.9.31.1", {"start": v(233, 212) * mm, "end": v(233, 222) * mm});
            skLineSegment(sketch, "E14.9.31.2", {"start": v(233, 222) * mm, "end": v(243, 222) * mm});
            skLineSegment(sketch, "E14.9.31.3", {"start": v(233, 212) * mm, "end": v(243, 212) * mm});
            skLineSegment(sketch, "E14.10.0.0", {"start": v(257, -222) * mm, "end": v(257, -212) * mm});
            skLineSegment(sketch, "E14.10.0.1", {"start": v(247, -222) * mm, "end": v(247, -212) * mm});
            skLineSegment(sketch, "E14.10.0.2", {"start": v(247, -212) * mm, "end": v(257, -212) * mm});
            skLineSegment(sketch, "E14.10.0.3", {"start": v(247, -222) * mm, "end": v(257, -222) * mm});
            skLineSegment(sketch, "E14.10.1.0", {"start": v(257, -208) * mm, "end": v(257, -198) * mm});
            skLineSegment(sketch, "E14.10.1.1", {"start": v(247, -208) * mm, "end": v(247, -198) * mm});
            skLineSegment(sketch, "E14.10.1.2", {"start": v(247, -198) * mm, "end": v(257, -198) * mm});
            skLineSegment(sketch, "E14.10.1.3", {"start": v(247, -208) * mm, "end": v(257, -208) * mm});
            skLineSegment(sketch, "E14.10.2.0", {"start": v(257, -194) * mm, "end": v(257, -184) * mm});
            skLineSegment(sketch, "E14.10.2.1", {"start": v(247, -194) * mm, "end": v(247, -184) * mm});
            skLineSegment(sketch, "E14.10.2.2", {"start": v(247, -184) * mm, "end": v(257, -184) * mm});
            skLineSegment(sketch, "E14.10.2.3", {"start": v(247, -194) * mm, "end": v(257, -194) * mm});
            skLineSegment(sketch, "E14.10.3.0", {"start": v(257, -180) * mm, "end": v(257, -170) * mm});
            skLineSegment(sketch, "E14.10.3.1", {"start": v(247, -180) * mm, "end": v(247, -170) * mm});
            skLineSegment(sketch, "E14.10.3.2", {"start": v(247, -170) * mm, "end": v(257, -170) * mm});
            skLineSegment(sketch, "E14.10.3.3", {"start": v(247, -180) * mm, "end": v(257, -180) * mm});
            skLineSegment(sketch, "E14.10.4.0", {"start": v(257, -166) * mm, "end": v(257, -156) * mm});
            skLineSegment(sketch, "E14.10.4.1", {"start": v(247, -166) * mm, "end": v(247, -156) * mm});
            skLineSegment(sketch, "E14.10.4.2", {"start": v(247, -156) * mm, "end": v(257, -156) * mm});
            skLineSegment(sketch, "E14.10.4.3", {"start": v(247, -166) * mm, "end": v(257, -166) * mm});
            skLineSegment(sketch, "E14.10.5.0", {"start": v(257, -152) * mm, "end": v(257, -142) * mm});
            skLineSegment(sketch, "E14.10.5.1", {"start": v(247, -152) * mm, "end": v(247, -142) * mm});
            skLineSegment(sketch, "E14.10.5.2", {"start": v(247, -142) * mm, "end": v(257, -142) * mm});
            skLineSegment(sketch, "E14.10.5.3", {"start": v(247, -152) * mm, "end": v(257, -152) * mm});
            skLineSegment(sketch, "E14.10.6.0", {"start": v(257, -138) * mm, "end": v(257, -128) * mm});
            skLineSegment(sketch, "E14.10.6.1", {"start": v(247, -138) * mm, "end": v(247, -128) * mm});
            skLineSegment(sketch, "E14.10.6.2", {"start": v(247, -128) * mm, "end": v(257, -128) * mm});
            skLineSegment(sketch, "E14.10.6.3", {"start": v(247, -138) * mm, "end": v(257, -138) * mm});
            skLineSegment(sketch, "E14.10.7.0", {"start": v(257, -124) * mm, "end": v(257, -114) * mm});
            skLineSegment(sketch, "E14.10.7.1", {"start": v(247, -124) * mm, "end": v(247, -114) * mm});
            skLineSegment(sketch, "E14.10.7.2", {"start": v(247, -114) * mm, "end": v(257, -114) * mm});
            skLineSegment(sketch, "E14.10.7.3", {"start": v(247, -124) * mm, "end": v(257, -124) * mm});
            skLineSegment(sketch, "E14.10.8.0", {"start": v(257, -110) * mm, "end": v(257, -100) * mm});
            skLineSegment(sketch, "E14.10.8.1", {"start": v(247, -110) * mm, "end": v(247, -100) * mm});
            skLineSegment(sketch, "E14.10.8.2", {"start": v(247, -100) * mm, "end": v(257, -100) * mm});
            skLineSegment(sketch, "E14.10.8.3", {"start": v(247, -110) * mm, "end": v(257, -110) * mm});
            skLineSegment(sketch, "E14.10.9.0", {"start": v(257, -96) * mm, "end": v(257, -86) * mm});
            skLineSegment(sketch, "E14.10.9.1", {"start": v(247, -96) * mm, "end": v(247, -86) * mm});
            skLineSegment(sketch, "E14.10.9.2", {"start": v(247, -86) * mm, "end": v(257, -86) * mm});
            skLineSegment(sketch, "E14.10.9.3", {"start": v(247, -96) * mm, "end": v(257, -96) * mm});
            skLineSegment(sketch, "E14.10.10.0", {"start": v(257, -82) * mm, "end": v(257, -72) * mm});
            skLineSegment(sketch, "E14.10.10.1", {"start": v(247, -82) * mm, "end": v(247, -72) * mm});
            skLineSegment(sketch, "E14.10.10.2", {"start": v(247, -72) * mm, "end": v(257, -72) * mm});
            skLineSegment(sketch, "E14.10.10.3", {"start": v(247, -82) * mm, "end": v(257, -82) * mm});
            skLineSegment(sketch, "E14.10.11.0", {"start": v(257, -68) * mm, "end": v(257, -58) * mm});
            skLineSegment(sketch, "E14.10.11.1", {"start": v(247, -68) * mm, "end": v(247, -58) * mm});
            skLineSegment(sketch, "E14.10.11.2", {"start": v(247, -58) * mm, "end": v(257, -58) * mm});
            skLineSegment(sketch, "E14.10.11.3", {"start": v(247, -68) * mm, "end": v(257, -68) * mm});
            skLineSegment(sketch, "E14.10.12.0", {"start": v(257, -54) * mm, "end": v(257, -44) * mm});
            skLineSegment(sketch, "E14.10.12.1", {"start": v(247, -54) * mm, "end": v(247, -44) * mm});
            skLineSegment(sketch, "E14.10.12.2", {"start": v(247, -44) * mm, "end": v(257, -44) * mm});
            skLineSegment(sketch, "E14.10.12.3", {"start": v(247, -54) * mm, "end": v(257, -54) * mm});
            skLineSegment(sketch, "E14.10.13.0", {"start": v(257, -40) * mm, "end": v(257, -30) * mm});
            skLineSegment(sketch, "E14.10.13.1", {"start": v(247, -40) * mm, "end": v(247, -30) * mm});
            skLineSegment(sketch, "E14.10.13.2", {"start": v(247, -30) * mm, "end": v(257, -30) * mm});
            skLineSegment(sketch, "E14.10.13.3", {"start": v(247, -40) * mm, "end": v(257, -40) * mm});
            skLineSegment(sketch, "E14.10.14.0", {"start": v(257, -26) * mm, "end": v(257, -16) * mm});
            skLineSegment(sketch, "E14.10.14.1", {"start": v(247, -26) * mm, "end": v(247, -16) * mm});
            skLineSegment(sketch, "E14.10.14.2", {"start": v(247, -16) * mm, "end": v(257, -16) * mm});
            skLineSegment(sketch, "E14.10.14.3", {"start": v(247, -26) * mm, "end": v(257, -26) * mm});
            skLineSegment(sketch, "E14.10.15.0", {"start": v(257, -12) * mm, "end": v(257, -2) * mm});
            skLineSegment(sketch, "E14.10.15.1", {"start": v(247, -12) * mm, "end": v(247, -2) * mm});
            skLineSegment(sketch, "E14.10.15.2", {"start": v(247, -2) * mm, "end": v(257, -2) * mm});
            skLineSegment(sketch, "E14.10.15.3", {"start": v(247, -12) * mm, "end": v(257, -12) * mm});
            skLineSegment(sketch, "E14.10.16.0", {"start": v(257, 2) * mm, "end": v(257, 12) * mm});
            skLineSegment(sketch, "E14.10.16.1", {"start": v(247, 2) * mm, "end": v(247, 12) * mm});
            skLineSegment(sketch, "E14.10.16.2", {"start": v(247, 12) * mm, "end": v(257, 12) * mm});
            skLineSegment(sketch, "E14.10.16.3", {"start": v(247, 2) * mm, "end": v(257, 2) * mm});
            skLineSegment(sketch, "E14.10.17.0", {"start": v(257, 16) * mm, "end": v(257, 26) * mm});
            skLineSegment(sketch, "E14.10.17.1", {"start": v(247, 16) * mm, "end": v(247, 26) * mm});
            skLineSegment(sketch, "E14.10.17.2", {"start": v(247, 26) * mm, "end": v(257, 26) * mm});
            skLineSegment(sketch, "E14.10.17.3", {"start": v(247, 16) * mm, "end": v(257, 16) * mm});
            skLineSegment(sketch, "E14.10.18.0", {"start": v(257, 30) * mm, "end": v(257, 40) * mm});
            skLineSegment(sketch, "E14.10.18.1", {"start": v(247, 30) * mm, "end": v(247, 40) * mm});
            skLineSegment(sketch, "E14.10.18.2", {"start": v(247, 40) * mm, "end": v(257, 40) * mm});
            skLineSegment(sketch, "E14.10.18.3", {"start": v(247, 30) * mm, "end": v(257, 30) * mm});
            skLineSegment(sketch, "E14.10.19.0", {"start": v(257, 44) * mm, "end": v(257, 54) * mm});
            skLineSegment(sketch, "E14.10.19.1", {"start": v(247, 44) * mm, "end": v(247, 54) * mm});
            skLineSegment(sketch, "E14.10.19.2", {"start": v(247, 54) * mm, "end": v(257, 54) * mm});
            skLineSegment(sketch, "E14.10.19.3", {"start": v(247, 44) * mm, "end": v(257, 44) * mm});
            skLineSegment(sketch, "E14.10.20.0", {"start": v(257, 58) * mm, "end": v(257, 68) * mm});
            skLineSegment(sketch, "E14.10.20.1", {"start": v(247, 58) * mm, "end": v(247, 68) * mm});
            skLineSegment(sketch, "E14.10.20.2", {"start": v(247, 68) * mm, "end": v(257, 68) * mm});
            skLineSegment(sketch, "E14.10.20.3", {"start": v(247, 58) * mm, "end": v(257, 58) * mm});
            skLineSegment(sketch, "E14.10.21.0", {"start": v(257, 72) * mm, "end": v(257, 82) * mm});
            skLineSegment(sketch, "E14.10.21.1", {"start": v(247, 72) * mm, "end": v(247, 82) * mm});
            skLineSegment(sketch, "E14.10.21.2", {"start": v(247, 82) * mm, "end": v(257, 82) * mm});
            skLineSegment(sketch, "E14.10.21.3", {"start": v(247, 72) * mm, "end": v(257, 72) * mm});
            skLineSegment(sketch, "E14.10.22.0", {"start": v(257, 86) * mm, "end": v(257, 96) * mm});
            skLineSegment(sketch, "E14.10.22.1", {"start": v(247, 86) * mm, "end": v(247, 96) * mm});
            skLineSegment(sketch, "E14.10.22.2", {"start": v(247, 96) * mm, "end": v(257, 96) * mm});
            skLineSegment(sketch, "E14.10.22.3", {"start": v(247, 86) * mm, "end": v(257, 86) * mm});
            skLineSegment(sketch, "E14.10.23.0", {"start": v(257, 100) * mm, "end": v(257, 110) * mm});
            skLineSegment(sketch, "E14.10.23.1", {"start": v(247, 100) * mm, "end": v(247, 110) * mm});
            skLineSegment(sketch, "E14.10.23.2", {"start": v(247, 110) * mm, "end": v(257, 110) * mm});
            skLineSegment(sketch, "E14.10.23.3", {"start": v(247, 100) * mm, "end": v(257, 100) * mm});
            skLineSegment(sketch, "E14.10.24.0", {"start": v(257, 114) * mm, "end": v(257, 124) * mm});
            skLineSegment(sketch, "E14.10.24.1", {"start": v(247, 114) * mm, "end": v(247, 124) * mm});
            skLineSegment(sketch, "E14.10.24.2", {"start": v(247, 124) * mm, "end": v(257, 124) * mm});
            skLineSegment(sketch, "E14.10.24.3", {"start": v(247, 114) * mm, "end": v(257, 114) * mm});
            skLineSegment(sketch, "E14.10.25.0", {"start": v(257, 128) * mm, "end": v(257, 138) * mm});
            skLineSegment(sketch, "E14.10.25.1", {"start": v(247, 128) * mm, "end": v(247, 138) * mm});
            skLineSegment(sketch, "E14.10.25.2", {"start": v(247, 138) * mm, "end": v(257, 138) * mm});
            skLineSegment(sketch, "E14.10.25.3", {"start": v(247, 128) * mm, "end": v(257, 128) * mm});
            skLineSegment(sketch, "E14.10.26.0", {"start": v(257, 142) * mm, "end": v(257, 152) * mm});
            skLineSegment(sketch, "E14.10.26.1", {"start": v(247, 142) * mm, "end": v(247, 152) * mm});
            skLineSegment(sketch, "E14.10.26.2", {"start": v(247, 152) * mm, "end": v(257, 152) * mm});
            skLineSegment(sketch, "E14.10.26.3", {"start": v(247, 142) * mm, "end": v(257, 142) * mm});
            skLineSegment(sketch, "E14.10.27.0", {"start": v(257, 156) * mm, "end": v(257, 166) * mm});
            skLineSegment(sketch, "E14.10.27.1", {"start": v(247, 156) * mm, "end": v(247, 166) * mm});
            skLineSegment(sketch, "E14.10.27.2", {"start": v(247, 166) * mm, "end": v(257, 166) * mm});
            skLineSegment(sketch, "E14.10.27.3", {"start": v(247, 156) * mm, "end": v(257, 156) * mm});
            skLineSegment(sketch, "E14.10.28.0", {"start": v(257, 170) * mm, "end": v(257, 180) * mm});
            skLineSegment(sketch, "E14.10.28.1", {"start": v(247, 170) * mm, "end": v(247, 180) * mm});
            skLineSegment(sketch, "E14.10.28.2", {"start": v(247, 180) * mm, "end": v(257, 180) * mm});
            skLineSegment(sketch, "E14.10.28.3", {"start": v(247, 170) * mm, "end": v(257, 170) * mm});
            skLineSegment(sketch, "E14.10.29.0", {"start": v(257, 184) * mm, "end": v(257, 194) * mm});
            skLineSegment(sketch, "E14.10.29.1", {"start": v(247, 184) * mm, "end": v(247, 194) * mm});
            skLineSegment(sketch, "E14.10.29.2", {"start": v(247, 194) * mm, "end": v(257, 194) * mm});
            skLineSegment(sketch, "E14.10.29.3", {"start": v(247, 184) * mm, "end": v(257, 184) * mm});
            skLineSegment(sketch, "E14.10.30.0", {"start": v(257, 198) * mm, "end": v(257, 208) * mm});
            skLineSegment(sketch, "E14.10.30.1", {"start": v(247, 198) * mm, "end": v(247, 208) * mm});
            skLineSegment(sketch, "E14.10.30.2", {"start": v(247, 208) * mm, "end": v(257, 208) * mm});
            skLineSegment(sketch, "E14.10.30.3", {"start": v(247, 198) * mm, "end": v(257, 198) * mm});
            skLineSegment(sketch, "E14.10.31.0", {"start": v(257, 212) * mm, "end": v(257, 222) * mm});
            skLineSegment(sketch, "E14.10.31.1", {"start": v(247, 212) * mm, "end": v(247, 222) * mm});
            skLineSegment(sketch, "E14.10.31.2", {"start": v(247, 222) * mm, "end": v(257, 222) * mm});
            skLineSegment(sketch, "E14.10.31.3", {"start": v(247, 212) * mm, "end": v(257, 212) * mm});
            skLineSegment(sketch, "E14.11.0.0", {"start": v(271, -222) * mm, "end": v(271, -212) * mm});
            skLineSegment(sketch, "E14.11.0.1", {"start": v(261, -222) * mm, "end": v(261, -212) * mm});
            skLineSegment(sketch, "E14.11.0.2", {"start": v(261, -212) * mm, "end": v(271, -212) * mm});
            skLineSegment(sketch, "E14.11.0.3", {"start": v(261, -222) * mm, "end": v(271, -222) * mm});
            skLineSegment(sketch, "E14.11.1.0", {"start": v(271, -208) * mm, "end": v(271, -198) * mm});
            skLineSegment(sketch, "E14.11.1.1", {"start": v(261, -208) * mm, "end": v(261, -198) * mm});
            skLineSegment(sketch, "E14.11.1.2", {"start": v(261, -198) * mm, "end": v(271, -198) * mm});
            skLineSegment(sketch, "E14.11.1.3", {"start": v(261, -208) * mm, "end": v(271, -208) * mm});
            skLineSegment(sketch, "E14.11.2.0", {"start": v(271, -194) * mm, "end": v(271, -184) * mm});
            skLineSegment(sketch, "E14.11.2.1", {"start": v(261, -194) * mm, "end": v(261, -184) * mm});
            skLineSegment(sketch, "E14.11.2.2", {"start": v(261, -184) * mm, "end": v(271, -184) * mm});
            skLineSegment(sketch, "E14.11.2.3", {"start": v(261, -194) * mm, "end": v(271, -194) * mm});
            skLineSegment(sketch, "E14.11.3.0", {"start": v(271, -180) * mm, "end": v(271, -170) * mm});
            skLineSegment(sketch, "E14.11.3.1", {"start": v(261, -180) * mm, "end": v(261, -170) * mm});
            skLineSegment(sketch, "E14.11.3.2", {"start": v(261, -170) * mm, "end": v(271, -170) * mm});
            skLineSegment(sketch, "E14.11.3.3", {"start": v(261, -180) * mm, "end": v(271, -180) * mm});
            skLineSegment(sketch, "E14.11.4.0", {"start": v(271, -166) * mm, "end": v(271, -156) * mm});
            skLineSegment(sketch, "E14.11.4.1", {"start": v(261, -166) * mm, "end": v(261, -156) * mm});
            skLineSegment(sketch, "E14.11.4.2", {"start": v(261, -156) * mm, "end": v(271, -156) * mm});
            skLineSegment(sketch, "E14.11.4.3", {"start": v(261, -166) * mm, "end": v(271, -166) * mm});
            skLineSegment(sketch, "E14.11.5.0", {"start": v(271, -152) * mm, "end": v(271, -142) * mm});
            skLineSegment(sketch, "E14.11.5.1", {"start": v(261, -152) * mm, "end": v(261, -142) * mm});
            skLineSegment(sketch, "E14.11.5.2", {"start": v(261, -142) * mm, "end": v(271, -142) * mm});
            skLineSegment(sketch, "E14.11.5.3", {"start": v(261, -152) * mm, "end": v(271, -152) * mm});
            skLineSegment(sketch, "E14.11.6.0", {"start": v(271, -138) * mm, "end": v(271, -128) * mm});
            skLineSegment(sketch, "E14.11.6.1", {"start": v(261, -138) * mm, "end": v(261, -128) * mm});
            skLineSegment(sketch, "E14.11.6.2", {"start": v(261, -128) * mm, "end": v(271, -128) * mm});
            skLineSegment(sketch, "E14.11.6.3", {"start": v(261, -138) * mm, "end": v(271, -138) * mm});
            skLineSegment(sketch, "E14.11.7.0", {"start": v(271, -124) * mm, "end": v(271, -114) * mm});
            skLineSegment(sketch, "E14.11.7.1", {"start": v(261, -124) * mm, "end": v(261, -114) * mm});
            skLineSegment(sketch, "E14.11.7.2", {"start": v(261, -114) * mm, "end": v(271, -114) * mm});
            skLineSegment(sketch, "E14.11.7.3", {"start": v(261, -124) * mm, "end": v(271, -124) * mm});
            skLineSegment(sketch, "E14.11.8.0", {"start": v(271, -110) * mm, "end": v(271, -100) * mm});
            skLineSegment(sketch, "E14.11.8.1", {"start": v(261, -110) * mm, "end": v(261, -100) * mm});
            skLineSegment(sketch, "E14.11.8.2", {"start": v(261, -100) * mm, "end": v(271, -100) * mm});
            skLineSegment(sketch, "E14.11.8.3", {"start": v(261, -110) * mm, "end": v(271, -110) * mm});
            skLineSegment(sketch, "E14.11.9.0", {"start": v(271, -96) * mm, "end": v(271, -86) * mm});
            skLineSegment(sketch, "E14.11.9.1", {"start": v(261, -96) * mm, "end": v(261, -86) * mm});
            skLineSegment(sketch, "E14.11.9.2", {"start": v(261, -86) * mm, "end": v(271, -86) * mm});
            skLineSegment(sketch, "E14.11.9.3", {"start": v(261, -96) * mm, "end": v(271, -96) * mm});
            skLineSegment(sketch, "E14.11.10.0", {"start": v(271, -82) * mm, "end": v(271, -72) * mm});
            skLineSegment(sketch, "E14.11.10.1", {"start": v(261, -82) * mm, "end": v(261, -72) * mm});
            skLineSegment(sketch, "E14.11.10.2", {"start": v(261, -72) * mm, "end": v(271, -72) * mm});
            skLineSegment(sketch, "E14.11.10.3", {"start": v(261, -82) * mm, "end": v(271, -82) * mm});
            skLineSegment(sketch, "E14.11.11.0", {"start": v(271, -68) * mm, "end": v(271, -58) * mm});
            skLineSegment(sketch, "E14.11.11.1", {"start": v(261, -68) * mm, "end": v(261, -58) * mm});
            skLineSegment(sketch, "E14.11.11.2", {"start": v(261, -58) * mm, "end": v(271, -58) * mm});
            skLineSegment(sketch, "E14.11.11.3", {"start": v(261, -68) * mm, "end": v(271, -68) * mm});
            skLineSegment(sketch, "E14.11.12.0", {"start": v(271, -54) * mm, "end": v(271, -44) * mm});
            skLineSegment(sketch, "E14.11.12.1", {"start": v(261, -54) * mm, "end": v(261, -44) * mm});
            skLineSegment(sketch, "E14.11.12.2", {"start": v(261, -44) * mm, "end": v(271, -44) * mm});
            skLineSegment(sketch, "E14.11.12.3", {"start": v(261, -54) * mm, "end": v(271, -54) * mm});
            skLineSegment(sketch, "E14.11.13.0", {"start": v(271, -40) * mm, "end": v(271, -30) * mm});
            skLineSegment(sketch, "E14.11.13.1", {"start": v(261, -40) * mm, "end": v(261, -30) * mm});
            skLineSegment(sketch, "E14.11.13.2", {"start": v(261, -30) * mm, "end": v(271, -30) * mm});
            skLineSegment(sketch, "E14.11.13.3", {"start": v(261, -40) * mm, "end": v(271, -40) * mm});
            skLineSegment(sketch, "E14.11.14.0", {"start": v(271, -26) * mm, "end": v(271, -16) * mm});
            skLineSegment(sketch, "E14.11.14.1", {"start": v(261, -26) * mm, "end": v(261, -16) * mm});
            skLineSegment(sketch, "E14.11.14.2", {"start": v(261, -16) * mm, "end": v(271, -16) * mm});
            skLineSegment(sketch, "E14.11.14.3", {"start": v(261, -26) * mm, "end": v(271, -26) * mm});
            skLineSegment(sketch, "E14.11.15.0", {"start": v(271, -12) * mm, "end": v(271, -2) * mm});
            skLineSegment(sketch, "E14.11.15.1", {"start": v(261, -12) * mm, "end": v(261, -2) * mm});
            skLineSegment(sketch, "E14.11.15.2", {"start": v(261, -2) * mm, "end": v(271, -2) * mm});
            skLineSegment(sketch, "E14.11.15.3", {"start": v(261, -12) * mm, "end": v(271, -12) * mm});
            skLineSegment(sketch, "E14.11.16.0", {"start": v(271, 2) * mm, "end": v(271, 12) * mm});
            skLineSegment(sketch, "E14.11.16.1", {"start": v(261, 2) * mm, "end": v(261, 12) * mm});
            skLineSegment(sketch, "E14.11.16.2", {"start": v(261, 12) * mm, "end": v(271, 12) * mm});
            skLineSegment(sketch, "E14.11.16.3", {"start": v(261, 2) * mm, "end": v(271, 2) * mm});
            skLineSegment(sketch, "E14.11.17.0", {"start": v(271, 16) * mm, "end": v(271, 26) * mm});
            skLineSegment(sketch, "E14.11.17.1", {"start": v(261, 16) * mm, "end": v(261, 26) * mm});
            skLineSegment(sketch, "E14.11.17.2", {"start": v(261, 26) * mm, "end": v(271, 26) * mm});
            skLineSegment(sketch, "E14.11.17.3", {"start": v(261, 16) * mm, "end": v(271, 16) * mm});
            skLineSegment(sketch, "E14.11.18.0", {"start": v(271, 30) * mm, "end": v(271, 40) * mm});
            skLineSegment(sketch, "E14.11.18.1", {"start": v(261, 30) * mm, "end": v(261, 40) * mm});
            skLineSegment(sketch, "E14.11.18.2", {"start": v(261, 40) * mm, "end": v(271, 40) * mm});
            skLineSegment(sketch, "E14.11.18.3", {"start": v(261, 30) * mm, "end": v(271, 30) * mm});
            skLineSegment(sketch, "E14.11.19.0", {"start": v(271, 44) * mm, "end": v(271, 54) * mm});
            skLineSegment(sketch, "E14.11.19.1", {"start": v(261, 44) * mm, "end": v(261, 54) * mm});
            skLineSegment(sketch, "E14.11.19.2", {"start": v(261, 54) * mm, "end": v(271, 54) * mm});
            skLineSegment(sketch, "E14.11.19.3", {"start": v(261, 44) * mm, "end": v(271, 44) * mm});
            skLineSegment(sketch, "E14.11.20.0", {"start": v(271, 58) * mm, "end": v(271, 68) * mm});
            skLineSegment(sketch, "E14.11.20.1", {"start": v(261, 58) * mm, "end": v(261, 68) * mm});
            skLineSegment(sketch, "E14.11.20.2", {"start": v(261, 68) * mm, "end": v(271, 68) * mm});
            skLineSegment(sketch, "E14.11.20.3", {"start": v(261, 58) * mm, "end": v(271, 58) * mm});
            skLineSegment(sketch, "E14.11.21.0", {"start": v(271, 72) * mm, "end": v(271, 82) * mm});
            skLineSegment(sketch, "E14.11.21.1", {"start": v(261, 72) * mm, "end": v(261, 82) * mm});
            skLineSegment(sketch, "E14.11.21.2", {"start": v(261, 82) * mm, "end": v(271, 82) * mm});
            skLineSegment(sketch, "E14.11.21.3", {"start": v(261, 72) * mm, "end": v(271, 72) * mm});
            skLineSegment(sketch, "E14.11.22.0", {"start": v(271, 86) * mm, "end": v(271, 96) * mm});
            skLineSegment(sketch, "E14.11.22.1", {"start": v(261, 86) * mm, "end": v(261, 96) * mm});
            skLineSegment(sketch, "E14.11.22.2", {"start": v(261, 96) * mm, "end": v(271, 96) * mm});
            skLineSegment(sketch, "E14.11.22.3", {"start": v(261, 86) * mm, "end": v(271, 86) * mm});
            skLineSegment(sketch, "E14.11.23.0", {"start": v(271, 100) * mm, "end": v(271, 110) * mm});
            skLineSegment(sketch, "E14.11.23.1", {"start": v(261, 100) * mm, "end": v(261, 110) * mm});
            skLineSegment(sketch, "E14.11.23.2", {"start": v(261, 110) * mm, "end": v(271, 110) * mm});
            skLineSegment(sketch, "E14.11.23.3", {"start": v(261, 100) * mm, "end": v(271, 100) * mm});
            skLineSegment(sketch, "E14.11.24.0", {"start": v(271, 114) * mm, "end": v(271, 124) * mm});
            skLineSegment(sketch, "E14.11.24.1", {"start": v(261, 114) * mm, "end": v(261, 124) * mm});
            skLineSegment(sketch, "E14.11.24.2", {"start": v(261, 124) * mm, "end": v(271, 124) * mm});
            skLineSegment(sketch, "E14.11.24.3", {"start": v(261, 114) * mm, "end": v(271, 114) * mm});
            skLineSegment(sketch, "E14.11.25.0", {"start": v(271, 128) * mm, "end": v(271, 138) * mm});
            skLineSegment(sketch, "E14.11.25.1", {"start": v(261, 128) * mm, "end": v(261, 138) * mm});
            skLineSegment(sketch, "E14.11.25.2", {"start": v(261, 138) * mm, "end": v(271, 138) * mm});
            skLineSegment(sketch, "E14.11.25.3", {"start": v(261, 128) * mm, "end": v(271, 128) * mm});
            skLineSegment(sketch, "E14.11.26.0", {"start": v(271, 142) * mm, "end": v(271, 152) * mm});
            skLineSegment(sketch, "E14.11.26.1", {"start": v(261, 142) * mm, "end": v(261, 152) * mm});
            skLineSegment(sketch, "E14.11.26.2", {"start": v(261, 152) * mm, "end": v(271, 152) * mm});
            skLineSegment(sketch, "E14.11.26.3", {"start": v(261, 142) * mm, "end": v(271, 142) * mm});
            skLineSegment(sketch, "E14.11.27.0", {"start": v(271, 156) * mm, "end": v(271, 166) * mm});
            skLineSegment(sketch, "E14.11.27.1", {"start": v(261, 156) * mm, "end": v(261, 166) * mm});
            skLineSegment(sketch, "E14.11.27.2", {"start": v(261, 166) * mm, "end": v(271, 166) * mm});
            skLineSegment(sketch, "E14.11.27.3", {"start": v(261, 156) * mm, "end": v(271, 156) * mm});
            skLineSegment(sketch, "E14.11.28.0", {"start": v(271, 170) * mm, "end": v(271, 180) * mm});
            skLineSegment(sketch, "E14.11.28.1", {"start": v(261, 170) * mm, "end": v(261, 180) * mm});
            skLineSegment(sketch, "E14.11.28.2", {"start": v(261, 180) * mm, "end": v(271, 180) * mm});
            skLineSegment(sketch, "E14.11.28.3", {"start": v(261, 170) * mm, "end": v(271, 170) * mm});
            skLineSegment(sketch, "E14.11.29.0", {"start": v(271, 184) * mm, "end": v(271, 194) * mm});
            skLineSegment(sketch, "E14.11.29.1", {"start": v(261, 184) * mm, "end": v(261, 194) * mm});
            skLineSegment(sketch, "E14.11.29.2", {"start": v(261, 194) * mm, "end": v(271, 194) * mm});
            skLineSegment(sketch, "E14.11.29.3", {"start": v(261, 184) * mm, "end": v(271, 184) * mm});
            skLineSegment(sketch, "E14.11.30.0", {"start": v(271, 198) * mm, "end": v(271, 208) * mm});
            skLineSegment(sketch, "E14.11.30.1", {"start": v(261, 198) * mm, "end": v(261, 208) * mm});
            skLineSegment(sketch, "E14.11.30.2", {"start": v(261, 208) * mm, "end": v(271, 208) * mm});
            skLineSegment(sketch, "E14.11.30.3", {"start": v(261, 198) * mm, "end": v(271, 198) * mm});
            skLineSegment(sketch, "E14.11.31.0", {"start": v(271, 212) * mm, "end": v(271, 222) * mm});
            skLineSegment(sketch, "E14.11.31.1", {"start": v(261, 212) * mm, "end": v(261, 222) * mm});
            skLineSegment(sketch, "E14.11.31.2", {"start": v(261, 222) * mm, "end": v(271, 222) * mm});
            skLineSegment(sketch, "E14.11.31.3", {"start": v(261, 212) * mm, "end": v(271, 212) * mm});
            skLineSegment(sketch, "E14.12.0.0", {"start": v(285, -222) * mm, "end": v(285, -212) * mm});
            skLineSegment(sketch, "E14.12.0.1", {"start": v(275, -222) * mm, "end": v(275, -212) * mm});
            skLineSegment(sketch, "E14.12.0.2", {"start": v(275, -212) * mm, "end": v(285, -212) * mm});
            skLineSegment(sketch, "E14.12.0.3", {"start": v(275, -222) * mm, "end": v(285, -222) * mm});
            skLineSegment(sketch, "E14.12.1.0", {"start": v(285, -208) * mm, "end": v(285, -198) * mm});
            skLineSegment(sketch, "E14.12.1.1", {"start": v(275, -208) * mm, "end": v(275, -198) * mm});
            skLineSegment(sketch, "E14.12.1.2", {"start": v(275, -198) * mm, "end": v(285, -198) * mm});
            skLineSegment(sketch, "E14.12.1.3", {"start": v(275, -208) * mm, "end": v(285, -208) * mm});
            skLineSegment(sketch, "E14.12.2.0", {"start": v(285, -194) * mm, "end": v(285, -184) * mm});
            skLineSegment(sketch, "E14.12.2.1", {"start": v(275, -194) * mm, "end": v(275, -184) * mm});
            skLineSegment(sketch, "E14.12.2.2", {"start": v(275, -184) * mm, "end": v(285, -184) * mm});
            skLineSegment(sketch, "E14.12.2.3", {"start": v(275, -194) * mm, "end": v(285, -194) * mm});
            skLineSegment(sketch, "E14.12.3.0", {"start": v(285, -180) * mm, "end": v(285, -170) * mm});
            skLineSegment(sketch, "E14.12.3.1", {"start": v(275, -180) * mm, "end": v(275, -170) * mm});
            skLineSegment(sketch, "E14.12.3.2", {"start": v(275, -170) * mm, "end": v(285, -170) * mm});
            skLineSegment(sketch, "E14.12.3.3", {"start": v(275, -180) * mm, "end": v(285, -180) * mm});
            skLineSegment(sketch, "E14.12.4.0", {"start": v(285, -166) * mm, "end": v(285, -156) * mm});
            skLineSegment(sketch, "E14.12.4.1", {"start": v(275, -166) * mm, "end": v(275, -156) * mm});
            skLineSegment(sketch, "E14.12.4.2", {"start": v(275, -156) * mm, "end": v(285, -156) * mm});
            skLineSegment(sketch, "E14.12.4.3", {"start": v(275, -166) * mm, "end": v(285, -166) * mm});
            skLineSegment(sketch, "E14.12.5.0", {"start": v(285, -152) * mm, "end": v(285, -142) * mm});
            skLineSegment(sketch, "E14.12.5.1", {"start": v(275, -152) * mm, "end": v(275, -142) * mm});
            skLineSegment(sketch, "E14.12.5.2", {"start": v(275, -142) * mm, "end": v(285, -142) * mm});
            skLineSegment(sketch, "E14.12.5.3", {"start": v(275, -152) * mm, "end": v(285, -152) * mm});
            skLineSegment(sketch, "E14.12.6.0", {"start": v(285, -138) * mm, "end": v(285, -128) * mm});
            skLineSegment(sketch, "E14.12.6.1", {"start": v(275, -138) * mm, "end": v(275, -128) * mm});
            skLineSegment(sketch, "E14.12.6.2", {"start": v(275, -128) * mm, "end": v(285, -128) * mm});
            skLineSegment(sketch, "E14.12.6.3", {"start": v(275, -138) * mm, "end": v(285, -138) * mm});
            skLineSegment(sketch, "E14.12.7.0", {"start": v(285, -124) * mm, "end": v(285, -114) * mm});
            skLineSegment(sketch, "E14.12.7.1", {"start": v(275, -124) * mm, "end": v(275, -114) * mm});
            skLineSegment(sketch, "E14.12.7.2", {"start": v(275, -114) * mm, "end": v(285, -114) * mm});
            skLineSegment(sketch, "E14.12.7.3", {"start": v(275, -124) * mm, "end": v(285, -124) * mm});
            skLineSegment(sketch, "E14.12.8.0", {"start": v(285, -110) * mm, "end": v(285, -100) * mm});
            skLineSegment(sketch, "E14.12.8.1", {"start": v(275, -110) * mm, "end": v(275, -100) * mm});
            skLineSegment(sketch, "E14.12.8.2", {"start": v(275, -100) * mm, "end": v(285, -100) * mm});
            skLineSegment(sketch, "E14.12.8.3", {"start": v(275, -110) * mm, "end": v(285, -110) * mm});
            skLineSegment(sketch, "E14.12.9.0", {"start": v(285, -96) * mm, "end": v(285, -86) * mm});
            skLineSegment(sketch, "E14.12.9.1", {"start": v(275, -96) * mm, "end": v(275, -86) * mm});
            skLineSegment(sketch, "E14.12.9.2", {"start": v(275, -86) * mm, "end": v(285, -86) * mm});
            skLineSegment(sketch, "E14.12.9.3", {"start": v(275, -96) * mm, "end": v(285, -96) * mm});
            skLineSegment(sketch, "E14.12.10.0", {"start": v(285, -82) * mm, "end": v(285, -72) * mm});
            skLineSegment(sketch, "E14.12.10.1", {"start": v(275, -82) * mm, "end": v(275, -72) * mm});
            skLineSegment(sketch, "E14.12.10.2", {"start": v(275, -72) * mm, "end": v(285, -72) * mm});
            skLineSegment(sketch, "E14.12.10.3", {"start": v(275, -82) * mm, "end": v(285, -82) * mm});
            skLineSegment(sketch, "E14.12.11.0", {"start": v(285, -68) * mm, "end": v(285, -58) * mm});
            skLineSegment(sketch, "E14.12.11.1", {"start": v(275, -68) * mm, "end": v(275, -58) * mm});
            skLineSegment(sketch, "E14.12.11.2", {"start": v(275, -58) * mm, "end": v(285, -58) * mm});
            skLineSegment(sketch, "E14.12.11.3", {"start": v(275, -68) * mm, "end": v(285, -68) * mm});
            skLineSegment(sketch, "E14.12.12.0", {"start": v(285, -54) * mm, "end": v(285, -44) * mm});
            skLineSegment(sketch, "E14.12.12.1", {"start": v(275, -54) * mm, "end": v(275, -44) * mm});
            skLineSegment(sketch, "E14.12.12.2", {"start": v(275, -44) * mm, "end": v(285, -44) * mm});
            skLineSegment(sketch, "E14.12.12.3", {"start": v(275, -54) * mm, "end": v(285, -54) * mm});
            skLineSegment(sketch, "E14.12.13.0", {"start": v(285, -40) * mm, "end": v(285, -30) * mm});
            skLineSegment(sketch, "E14.12.13.1", {"start": v(275, -40) * mm, "end": v(275, -30) * mm});
            skLineSegment(sketch, "E14.12.13.2", {"start": v(275, -30) * mm, "end": v(285, -30) * mm});
            skLineSegment(sketch, "E14.12.13.3", {"start": v(275, -40) * mm, "end": v(285, -40) * mm});
            skLineSegment(sketch, "E14.12.14.0", {"start": v(285, -26) * mm, "end": v(285, -16) * mm});
            skLineSegment(sketch, "E14.12.14.1", {"start": v(275, -26) * mm, "end": v(275, -16) * mm});
            skLineSegment(sketch, "E14.12.14.2", {"start": v(275, -16) * mm, "end": v(285, -16) * mm});
            skLineSegment(sketch, "E14.12.14.3", {"start": v(275, -26) * mm, "end": v(285, -26) * mm});
            skLineSegment(sketch, "E14.12.15.0", {"start": v(285, -12) * mm, "end": v(285, -2) * mm});
            skLineSegment(sketch, "E14.12.15.1", {"start": v(275, -12) * mm, "end": v(275, -2) * mm});
            skLineSegment(sketch, "E14.12.15.2", {"start": v(275, -2) * mm, "end": v(285, -2) * mm});
            skLineSegment(sketch, "E14.12.15.3", {"start": v(275, -12) * mm, "end": v(285, -12) * mm});
            skLineSegment(sketch, "E14.12.16.0", {"start": v(285, 2) * mm, "end": v(285, 12) * mm});
            skLineSegment(sketch, "E14.12.16.1", {"start": v(275, 2) * mm, "end": v(275, 12) * mm});
            skLineSegment(sketch, "E14.12.16.2", {"start": v(275, 12) * mm, "end": v(285, 12) * mm});
            skLineSegment(sketch, "E14.12.16.3", {"start": v(275, 2) * mm, "end": v(285, 2) * mm});
            skLineSegment(sketch, "E14.12.17.0", {"start": v(285, 16) * mm, "end": v(285, 26) * mm});
            skLineSegment(sketch, "E14.12.17.1", {"start": v(275, 16) * mm, "end": v(275, 26) * mm});
            skLineSegment(sketch, "E14.12.17.2", {"start": v(275, 26) * mm, "end": v(285, 26) * mm});
            skLineSegment(sketch, "E14.12.17.3", {"start": v(275, 16) * mm, "end": v(285, 16) * mm});
            skLineSegment(sketch, "E14.12.18.0", {"start": v(285, 30) * mm, "end": v(285, 40) * mm});
            skLineSegment(sketch, "E14.12.18.1", {"start": v(275, 30) * mm, "end": v(275, 40) * mm});
            skLineSegment(sketch, "E14.12.18.2", {"start": v(275, 40) * mm, "end": v(285, 40) * mm});
            skLineSegment(sketch, "E14.12.18.3", {"start": v(275, 30) * mm, "end": v(285, 30) * mm});
            skLineSegment(sketch, "E14.12.19.0", {"start": v(285, 44) * mm, "end": v(285, 54) * mm});
            skLineSegment(sketch, "E14.12.19.1", {"start": v(275, 44) * mm, "end": v(275, 54) * mm});
            skLineSegment(sketch, "E14.12.19.2", {"start": v(275, 54) * mm, "end": v(285, 54) * mm});
            skLineSegment(sketch, "E14.12.19.3", {"start": v(275, 44) * mm, "end": v(285, 44) * mm});
            skLineSegment(sketch, "E14.12.20.0", {"start": v(285, 58) * mm, "end": v(285, 68) * mm});
            skLineSegment(sketch, "E14.12.20.1", {"start": v(275, 58) * mm, "end": v(275, 68) * mm});
            skLineSegment(sketch, "E14.12.20.2", {"start": v(275, 68) * mm, "end": v(285, 68) * mm});
            skLineSegment(sketch, "E14.12.20.3", {"start": v(275, 58) * mm, "end": v(285, 58) * mm});
            skLineSegment(sketch, "E14.12.21.0", {"start": v(285, 72) * mm, "end": v(285, 82) * mm});
            skLineSegment(sketch, "E14.12.21.1", {"start": v(275, 72) * mm, "end": v(275, 82) * mm});
            skLineSegment(sketch, "E14.12.21.2", {"start": v(275, 82) * mm, "end": v(285, 82) * mm});
            skLineSegment(sketch, "E14.12.21.3", {"start": v(275, 72) * mm, "end": v(285, 72) * mm});
            skLineSegment(sketch, "E14.12.22.0", {"start": v(285, 86) * mm, "end": v(285, 96) * mm});
            skLineSegment(sketch, "E14.12.22.1", {"start": v(275, 86) * mm, "end": v(275, 96) * mm});
            skLineSegment(sketch, "E14.12.22.2", {"start": v(275, 96) * mm, "end": v(285, 96) * mm});
            skLineSegment(sketch, "E14.12.22.3", {"start": v(275, 86) * mm, "end": v(285, 86) * mm});
            skLineSegment(sketch, "E14.12.23.0", {"start": v(285, 100) * mm, "end": v(285, 110) * mm});
            skLineSegment(sketch, "E14.12.23.1", {"start": v(275, 100) * mm, "end": v(275, 110) * mm});
            skLineSegment(sketch, "E14.12.23.2", {"start": v(275, 110) * mm, "end": v(285, 110) * mm});
            skLineSegment(sketch, "E14.12.23.3", {"start": v(275, 100) * mm, "end": v(285, 100) * mm});
            skLineSegment(sketch, "E14.12.24.0", {"start": v(285, 114) * mm, "end": v(285, 124) * mm});
            skLineSegment(sketch, "E14.12.24.1", {"start": v(275, 114) * mm, "end": v(275, 124) * mm});
            skLineSegment(sketch, "E14.12.24.2", {"start": v(275, 124) * mm, "end": v(285, 124) * mm});
            skLineSegment(sketch, "E14.12.24.3", {"start": v(275, 114) * mm, "end": v(285, 114) * mm});
            skLineSegment(sketch, "E14.12.25.0", {"start": v(285, 128) * mm, "end": v(285, 138) * mm});
            skLineSegment(sketch, "E14.12.25.1", {"start": v(275, 128) * mm, "end": v(275, 138) * mm});
            skLineSegment(sketch, "E14.12.25.2", {"start": v(275, 138) * mm, "end": v(285, 138) * mm});
            skLineSegment(sketch, "E14.12.25.3", {"start": v(275, 128) * mm, "end": v(285, 128) * mm});
            skLineSegment(sketch, "E14.12.26.0", {"start": v(285, 142) * mm, "end": v(285, 152) * mm});
            skLineSegment(sketch, "E14.12.26.1", {"start": v(275, 142) * mm, "end": v(275, 152) * mm});
            skLineSegment(sketch, "E14.12.26.2", {"start": v(275, 152) * mm, "end": v(285, 152) * mm});
            skLineSegment(sketch, "E14.12.26.3", {"start": v(275, 142) * mm, "end": v(285, 142) * mm});
            skLineSegment(sketch, "E14.12.27.0", {"start": v(285, 156) * mm, "end": v(285, 166) * mm});
            skLineSegment(sketch, "E14.12.27.1", {"start": v(275, 156) * mm, "end": v(275, 166) * mm});
            skLineSegment(sketch, "E14.12.27.2", {"start": v(275, 166) * mm, "end": v(285, 166) * mm});
            skLineSegment(sketch, "E14.12.27.3", {"start": v(275, 156) * mm, "end": v(285, 156) * mm});
            skLineSegment(sketch, "E14.12.28.0", {"start": v(285, 170) * mm, "end": v(285, 180) * mm});
            skLineSegment(sketch, "E14.12.28.1", {"start": v(275, 170) * mm, "end": v(275, 180) * mm});
            skLineSegment(sketch, "E14.12.28.2", {"start": v(275, 180) * mm, "end": v(285, 180) * mm});
            skLineSegment(sketch, "E14.12.28.3", {"start": v(275, 170) * mm, "end": v(285, 170) * mm});
            skLineSegment(sketch, "E14.12.29.0", {"start": v(285, 184) * mm, "end": v(285, 194) * mm});
            skLineSegment(sketch, "E14.12.29.1", {"start": v(275, 184) * mm, "end": v(275, 194) * mm});
            skLineSegment(sketch, "E14.12.29.2", {"start": v(275, 194) * mm, "end": v(285, 194) * mm});
            skLineSegment(sketch, "E14.12.29.3", {"start": v(275, 184) * mm, "end": v(285, 184) * mm});
            skLineSegment(sketch, "E14.12.30.0", {"start": v(285, 198) * mm, "end": v(285, 208) * mm});
            skLineSegment(sketch, "E14.12.30.1", {"start": v(275, 198) * mm, "end": v(275, 208) * mm});
            skLineSegment(sketch, "E14.12.30.2", {"start": v(275, 208) * mm, "end": v(285, 208) * mm});
            skLineSegment(sketch, "E14.12.30.3", {"start": v(275, 198) * mm, "end": v(285, 198) * mm});
            skLineSegment(sketch, "E14.12.31.0", {"start": v(285, 212) * mm, "end": v(285, 222) * mm});
            skLineSegment(sketch, "E14.12.31.1", {"start": v(275, 212) * mm, "end": v(275, 222) * mm});
            skLineSegment(sketch, "E14.12.31.2", {"start": v(275, 222) * mm, "end": v(285, 222) * mm});
            skLineSegment(sketch, "E14.12.31.3", {"start": v(275, 212) * mm, "end": v(285, 212) * mm});
            skLineSegment(sketch, "E14.13.0.0", {"start": v(299, -222) * mm, "end": v(299, -212) * mm});
            skLineSegment(sketch, "E14.13.0.1", {"start": v(289, -222) * mm, "end": v(289, -212) * mm});
            skLineSegment(sketch, "E14.13.0.2", {"start": v(289, -212) * mm, "end": v(299, -212) * mm});
            skLineSegment(sketch, "E14.13.0.3", {"start": v(289, -222) * mm, "end": v(299, -222) * mm});
            skLineSegment(sketch, "E14.13.1.0", {"start": v(299, -208) * mm, "end": v(299, -198) * mm});
            skLineSegment(sketch, "E14.13.1.1", {"start": v(289, -208) * mm, "end": v(289, -198) * mm});
            skLineSegment(sketch, "E14.13.1.2", {"start": v(289, -198) * mm, "end": v(299, -198) * mm});
            skLineSegment(sketch, "E14.13.1.3", {"start": v(289, -208) * mm, "end": v(299, -208) * mm});
            skLineSegment(sketch, "E14.13.2.0", {"start": v(299, -194) * mm, "end": v(299, -184) * mm});
            skLineSegment(sketch, "E14.13.2.1", {"start": v(289, -194) * mm, "end": v(289, -184) * mm});
            skLineSegment(sketch, "E14.13.2.2", {"start": v(289, -184) * mm, "end": v(299, -184) * mm});
            skLineSegment(sketch, "E14.13.2.3", {"start": v(289, -194) * mm, "end": v(299, -194) * mm});
            skLineSegment(sketch, "E14.13.3.0", {"start": v(299, -180) * mm, "end": v(299, -170) * mm});
            skLineSegment(sketch, "E14.13.3.1", {"start": v(289, -180) * mm, "end": v(289, -170) * mm});
            skLineSegment(sketch, "E14.13.3.2", {"start": v(289, -170) * mm, "end": v(299, -170) * mm});
            skLineSegment(sketch, "E14.13.3.3", {"start": v(289, -180) * mm, "end": v(299, -180) * mm});
            skLineSegment(sketch, "E14.13.4.0", {"start": v(299, -166) * mm, "end": v(299, -156) * mm});
            skLineSegment(sketch, "E14.13.4.1", {"start": v(289, -166) * mm, "end": v(289, -156) * mm});
            skLineSegment(sketch, "E14.13.4.2", {"start": v(289, -156) * mm, "end": v(299, -156) * mm});
            skLineSegment(sketch, "E14.13.4.3", {"start": v(289, -166) * mm, "end": v(299, -166) * mm});
            skLineSegment(sketch, "E14.13.5.0", {"start": v(299, -152) * mm, "end": v(299, -142) * mm});
            skLineSegment(sketch, "E14.13.5.1", {"start": v(289, -152) * mm, "end": v(289, -142) * mm});
            skLineSegment(sketch, "E14.13.5.2", {"start": v(289, -142) * mm, "end": v(299, -142) * mm});
            skLineSegment(sketch, "E14.13.5.3", {"start": v(289, -152) * mm, "end": v(299, -152) * mm});
            skLineSegment(sketch, "E14.13.6.0", {"start": v(299, -138) * mm, "end": v(299, -128) * mm});
            skLineSegment(sketch, "E14.13.6.1", {"start": v(289, -138) * mm, "end": v(289, -128) * mm});
            skLineSegment(sketch, "E14.13.6.2", {"start": v(289, -128) * mm, "end": v(299, -128) * mm});
            skLineSegment(sketch, "E14.13.6.3", {"start": v(289, -138) * mm, "end": v(299, -138) * mm});
            skLineSegment(sketch, "E14.13.7.0", {"start": v(299, -124) * mm, "end": v(299, -114) * mm});
            skLineSegment(sketch, "E14.13.7.1", {"start": v(289, -124) * mm, "end": v(289, -114) * mm});
            skLineSegment(sketch, "E14.13.7.2", {"start": v(289, -114) * mm, "end": v(299, -114) * mm});
            skLineSegment(sketch, "E14.13.7.3", {"start": v(289, -124) * mm, "end": v(299, -124) * mm});
            skLineSegment(sketch, "E14.13.8.0", {"start": v(299, -110) * mm, "end": v(299, -100) * mm});
            skLineSegment(sketch, "E14.13.8.1", {"start": v(289, -110) * mm, "end": v(289, -100) * mm});
            skLineSegment(sketch, "E14.13.8.2", {"start": v(289, -100) * mm, "end": v(299, -100) * mm});
            skLineSegment(sketch, "E14.13.8.3", {"start": v(289, -110) * mm, "end": v(299, -110) * mm});
            skLineSegment(sketch, "E14.13.9.0", {"start": v(299, -96) * mm, "end": v(299, -86) * mm});
            skLineSegment(sketch, "E14.13.9.1", {"start": v(289, -96) * mm, "end": v(289, -86) * mm});
            skLineSegment(sketch, "E14.13.9.2", {"start": v(289, -86) * mm, "end": v(299, -86) * mm});
            skLineSegment(sketch, "E14.13.9.3", {"start": v(289, -96) * mm, "end": v(299, -96) * mm});
            skLineSegment(sketch, "E14.13.10.0", {"start": v(299, -82) * mm, "end": v(299, -72) * mm});
            skLineSegment(sketch, "E14.13.10.1", {"start": v(289, -82) * mm, "end": v(289, -72) * mm});
            skLineSegment(sketch, "E14.13.10.2", {"start": v(289, -72) * mm, "end": v(299, -72) * mm});
            skLineSegment(sketch, "E14.13.10.3", {"start": v(289, -82) * mm, "end": v(299, -82) * mm});
            skLineSegment(sketch, "E14.13.11.0", {"start": v(299, -68) * mm, "end": v(299, -58) * mm});
            skLineSegment(sketch, "E14.13.11.1", {"start": v(289, -68) * mm, "end": v(289, -58) * mm});
            skLineSegment(sketch, "E14.13.11.2", {"start": v(289, -58) * mm, "end": v(299, -58) * mm});
            skLineSegment(sketch, "E14.13.11.3", {"start": v(289, -68) * mm, "end": v(299, -68) * mm});
            skLineSegment(sketch, "E14.13.12.0", {"start": v(299, -54) * mm, "end": v(299, -44) * mm});
            skLineSegment(sketch, "E14.13.12.1", {"start": v(289, -54) * mm, "end": v(289, -44) * mm});
            skLineSegment(sketch, "E14.13.12.2", {"start": v(289, -44) * mm, "end": v(299, -44) * mm});
            skLineSegment(sketch, "E14.13.12.3", {"start": v(289, -54) * mm, "end": v(299, -54) * mm});
            skLineSegment(sketch, "E14.13.13.0", {"start": v(299, -40) * mm, "end": v(299, -30) * mm});
            skLineSegment(sketch, "E14.13.13.1", {"start": v(289, -40) * mm, "end": v(289, -30) * mm});
            skLineSegment(sketch, "E14.13.13.2", {"start": v(289, -30) * mm, "end": v(299, -30) * mm});
            skLineSegment(sketch, "E14.13.13.3", {"start": v(289, -40) * mm, "end": v(299, -40) * mm});
            skLineSegment(sketch, "E14.13.14.0", {"start": v(299, -26) * mm, "end": v(299, -16) * mm});
            skLineSegment(sketch, "E14.13.14.1", {"start": v(289, -26) * mm, "end": v(289, -16) * mm});
            skLineSegment(sketch, "E14.13.14.2", {"start": v(289, -16) * mm, "end": v(299, -16) * mm});
            skLineSegment(sketch, "E14.13.14.3", {"start": v(289, -26) * mm, "end": v(299, -26) * mm});
            skLineSegment(sketch, "E14.13.15.0", {"start": v(299, -12) * mm, "end": v(299, -2) * mm});
            skLineSegment(sketch, "E14.13.15.1", {"start": v(289, -12) * mm, "end": v(289, -2) * mm});
            skLineSegment(sketch, "E14.13.15.2", {"start": v(289, -2) * mm, "end": v(299, -2) * mm});
            skLineSegment(sketch, "E14.13.15.3", {"start": v(289, -12) * mm, "end": v(299, -12) * mm});
            skLineSegment(sketch, "E14.13.16.0", {"start": v(299, 2) * mm, "end": v(299, 12) * mm});
            skLineSegment(sketch, "E14.13.16.1", {"start": v(289, 2) * mm, "end": v(289, 12) * mm});
            skLineSegment(sketch, "E14.13.16.2", {"start": v(289, 12) * mm, "end": v(299, 12) * mm});
            skLineSegment(sketch, "E14.13.16.3", {"start": v(289, 2) * mm, "end": v(299, 2) * mm});
            skLineSegment(sketch, "E14.13.17.0", {"start": v(299, 16) * mm, "end": v(299, 26) * mm});
            skLineSegment(sketch, "E14.13.17.1", {"start": v(289, 16) * mm, "end": v(289, 26) * mm});
            skLineSegment(sketch, "E14.13.17.2", {"start": v(289, 26) * mm, "end": v(299, 26) * mm});
            skLineSegment(sketch, "E14.13.17.3", {"start": v(289, 16) * mm, "end": v(299, 16) * mm});
            skLineSegment(sketch, "E14.13.18.0", {"start": v(299, 30) * mm, "end": v(299, 40) * mm});
            skLineSegment(sketch, "E14.13.18.1", {"start": v(289, 30) * mm, "end": v(289, 40) * mm});
            skLineSegment(sketch, "E14.13.18.2", {"start": v(289, 40) * mm, "end": v(299, 40) * mm});
            skLineSegment(sketch, "E14.13.18.3", {"start": v(289, 30) * mm, "end": v(299, 30) * mm});
            skLineSegment(sketch, "E14.13.19.0", {"start": v(299, 44) * mm, "end": v(299, 54) * mm});
            skLineSegment(sketch, "E14.13.19.1", {"start": v(289, 44) * mm, "end": v(289, 54) * mm});
            skLineSegment(sketch, "E14.13.19.2", {"start": v(289, 54) * mm, "end": v(299, 54) * mm});
            skLineSegment(sketch, "E14.13.19.3", {"start": v(289, 44) * mm, "end": v(299, 44) * mm});
            skLineSegment(sketch, "E14.13.20.0", {"start": v(299, 58) * mm, "end": v(299, 68) * mm});
            skLineSegment(sketch, "E14.13.20.1", {"start": v(289, 58) * mm, "end": v(289, 68) * mm});
            skLineSegment(sketch, "E14.13.20.2", {"start": v(289, 68) * mm, "end": v(299, 68) * mm});
            skLineSegment(sketch, "E14.13.20.3", {"start": v(289, 58) * mm, "end": v(299, 58) * mm});
            skLineSegment(sketch, "E14.13.21.0", {"start": v(299, 72) * mm, "end": v(299, 82) * mm});
            skLineSegment(sketch, "E14.13.21.1", {"start": v(289, 72) * mm, "end": v(289, 82) * mm});
            skLineSegment(sketch, "E14.13.21.2", {"start": v(289, 82) * mm, "end": v(299, 82) * mm});
            skLineSegment(sketch, "E14.13.21.3", {"start": v(289, 72) * mm, "end": v(299, 72) * mm});
            skLineSegment(sketch, "E14.13.22.0", {"start": v(299, 86) * mm, "end": v(299, 96) * mm});
            skLineSegment(sketch, "E14.13.22.1", {"start": v(289, 86) * mm, "end": v(289, 96) * mm});
            skLineSegment(sketch, "E14.13.22.2", {"start": v(289, 96) * mm, "end": v(299, 96) * mm});
            skLineSegment(sketch, "E14.13.22.3", {"start": v(289, 86) * mm, "end": v(299, 86) * mm});
            skLineSegment(sketch, "E14.13.23.0", {"start": v(299, 100) * mm, "end": v(299, 110) * mm});
            skLineSegment(sketch, "E14.13.23.1", {"start": v(289, 100) * mm, "end": v(289, 110) * mm});
            skLineSegment(sketch, "E14.13.23.2", {"start": v(289, 110) * mm, "end": v(299, 110) * mm});
            skLineSegment(sketch, "E14.13.23.3", {"start": v(289, 100) * mm, "end": v(299, 100) * mm});
            skLineSegment(sketch, "E14.13.24.0", {"start": v(299, 114) * mm, "end": v(299, 124) * mm});
            skLineSegment(sketch, "E14.13.24.1", {"start": v(289, 114) * mm, "end": v(289, 124) * mm});
            skLineSegment(sketch, "E14.13.24.2", {"start": v(289, 124) * mm, "end": v(299, 124) * mm});
            skLineSegment(sketch, "E14.13.24.3", {"start": v(289, 114) * mm, "end": v(299, 114) * mm});
            skLineSegment(sketch, "E14.13.25.0", {"start": v(299, 128) * mm, "end": v(299, 138) * mm});
            skLineSegment(sketch, "E14.13.25.1", {"start": v(289, 128) * mm, "end": v(289, 138) * mm});
            skLineSegment(sketch, "E14.13.25.2", {"start": v(289, 138) * mm, "end": v(299, 138) * mm});
            skLineSegment(sketch, "E14.13.25.3", {"start": v(289, 128) * mm, "end": v(299, 128) * mm});
            skLineSegment(sketch, "E14.13.26.0", {"start": v(299, 142) * mm, "end": v(299, 152) * mm});
            skLineSegment(sketch, "E14.13.26.1", {"start": v(289, 142) * mm, "end": v(289, 152) * mm});
            skLineSegment(sketch, "E14.13.26.2", {"start": v(289, 152) * mm, "end": v(299, 152) * mm});
            skLineSegment(sketch, "E14.13.26.3", {"start": v(289, 142) * mm, "end": v(299, 142) * mm});
            skLineSegment(sketch, "E14.13.27.0", {"start": v(299, 156) * mm, "end": v(299, 166) * mm});
            skLineSegment(sketch, "E14.13.27.1", {"start": v(289, 156) * mm, "end": v(289, 166) * mm});
            skLineSegment(sketch, "E14.13.27.2", {"start": v(289, 166) * mm, "end": v(299, 166) * mm});
            skLineSegment(sketch, "E14.13.27.3", {"start": v(289, 156) * mm, "end": v(299, 156) * mm});
            skLineSegment(sketch, "E14.13.28.0", {"start": v(299, 170) * mm, "end": v(299, 180) * mm});
            skLineSegment(sketch, "E14.13.28.1", {"start": v(289, 170) * mm, "end": v(289, 180) * mm});
            skLineSegment(sketch, "E14.13.28.2", {"start": v(289, 180) * mm, "end": v(299, 180) * mm});
            skLineSegment(sketch, "E14.13.28.3", {"start": v(289, 170) * mm, "end": v(299, 170) * mm});
            skLineSegment(sketch, "E14.13.29.0", {"start": v(299, 184) * mm, "end": v(299, 194) * mm});
            skLineSegment(sketch, "E14.13.29.1", {"start": v(289, 184) * mm, "end": v(289, 194) * mm});
            skLineSegment(sketch, "E14.13.29.2", {"start": v(289, 194) * mm, "end": v(299, 194) * mm});
            skLineSegment(sketch, "E14.13.29.3", {"start": v(289, 184) * mm, "end": v(299, 184) * mm});
            skLineSegment(sketch, "E14.13.30.0", {"start": v(299, 198) * mm, "end": v(299, 208) * mm});
            skLineSegment(sketch, "E14.13.30.1", {"start": v(289, 198) * mm, "end": v(289, 208) * mm});
            skLineSegment(sketch, "E14.13.30.2", {"start": v(289, 208) * mm, "end": v(299, 208) * mm});
            skLineSegment(sketch, "E14.13.30.3", {"start": v(289, 198) * mm, "end": v(299, 198) * mm});
            skLineSegment(sketch, "E14.13.31.0", {"start": v(299, 212) * mm, "end": v(299, 222) * mm});
            skLineSegment(sketch, "E14.13.31.1", {"start": v(289, 212) * mm, "end": v(289, 222) * mm});
            skLineSegment(sketch, "E14.13.31.2", {"start": v(289, 222) * mm, "end": v(299, 222) * mm});
            skLineSegment(sketch, "E14.13.31.3", {"start": v(289, 212) * mm, "end": v(299, 212) * mm});
            skLineSegment(sketch, "E14.14.0.0", {"start": v(313, -222) * mm, "end": v(313, -212) * mm});
            skLineSegment(sketch, "E14.14.0.1", {"start": v(303, -222) * mm, "end": v(303, -212) * mm});
            skLineSegment(sketch, "E14.14.0.2", {"start": v(303, -212) * mm, "end": v(313, -212) * mm});
            skLineSegment(sketch, "E14.14.0.3", {"start": v(303, -222) * mm, "end": v(313, -222) * mm});
            skLineSegment(sketch, "E14.14.1.0", {"start": v(313, -208) * mm, "end": v(313, -198) * mm});
            skLineSegment(sketch, "E14.14.1.1", {"start": v(303, -208) * mm, "end": v(303, -198) * mm});
            skLineSegment(sketch, "E14.14.1.2", {"start": v(303, -198) * mm, "end": v(313, -198) * mm});
            skLineSegment(sketch, "E14.14.1.3", {"start": v(303, -208) * mm, "end": v(313, -208) * mm});
            skLineSegment(sketch, "E14.14.2.0", {"start": v(313, -194) * mm, "end": v(313, -184) * mm});
            skLineSegment(sketch, "E14.14.2.1", {"start": v(303, -194) * mm, "end": v(303, -184) * mm});
            skLineSegment(sketch, "E14.14.2.2", {"start": v(303, -184) * mm, "end": v(313, -184) * mm});
            skLineSegment(sketch, "E14.14.2.3", {"start": v(303, -194) * mm, "end": v(313, -194) * mm});
            skLineSegment(sketch, "E14.14.3.0", {"start": v(313, -180) * mm, "end": v(313, -170) * mm});
            skLineSegment(sketch, "E14.14.3.1", {"start": v(303, -180) * mm, "end": v(303, -170) * mm});
            skLineSegment(sketch, "E14.14.3.2", {"start": v(303, -170) * mm, "end": v(313, -170) * mm});
            skLineSegment(sketch, "E14.14.3.3", {"start": v(303, -180) * mm, "end": v(313, -180) * mm});
            skLineSegment(sketch, "E14.14.4.0", {"start": v(313, -166) * mm, "end": v(313, -156) * mm});
            skLineSegment(sketch, "E14.14.4.1", {"start": v(303, -166) * mm, "end": v(303, -156) * mm});
            skLineSegment(sketch, "E14.14.4.2", {"start": v(303, -156) * mm, "end": v(313, -156) * mm});
            skLineSegment(sketch, "E14.14.4.3", {"start": v(303, -166) * mm, "end": v(313, -166) * mm});
            skLineSegment(sketch, "E14.14.5.0", {"start": v(313, -152) * mm, "end": v(313, -142) * mm});
            skLineSegment(sketch, "E14.14.5.1", {"start": v(303, -152) * mm, "end": v(303, -142) * mm});
            skLineSegment(sketch, "E14.14.5.2", {"start": v(303, -142) * mm, "end": v(313, -142) * mm});
            skLineSegment(sketch, "E14.14.5.3", {"start": v(303, -152) * mm, "end": v(313, -152) * mm});
            skLineSegment(sketch, "E14.14.6.0", {"start": v(313, -138) * mm, "end": v(313, -128) * mm});
            skLineSegment(sketch, "E14.14.6.1", {"start": v(303, -138) * mm, "end": v(303, -128) * mm});
            skLineSegment(sketch, "E14.14.6.2", {"start": v(303, -128) * mm, "end": v(313, -128) * mm});
            skLineSegment(sketch, "E14.14.6.3", {"start": v(303, -138) * mm, "end": v(313, -138) * mm});
            skLineSegment(sketch, "E14.14.7.0", {"start": v(313, -124) * mm, "end": v(313, -114) * mm});
            skLineSegment(sketch, "E14.14.7.1", {"start": v(303, -124) * mm, "end": v(303, -114) * mm});
            skLineSegment(sketch, "E14.14.7.2", {"start": v(303, -114) * mm, "end": v(313, -114) * mm});
            skLineSegment(sketch, "E14.14.7.3", {"start": v(303, -124) * mm, "end": v(313, -124) * mm});
            skLineSegment(sketch, "E14.14.8.0", {"start": v(313, -110) * mm, "end": v(313, -100) * mm});
            skLineSegment(sketch, "E14.14.8.1", {"start": v(303, -110) * mm, "end": v(303, -100) * mm});
            skLineSegment(sketch, "E14.14.8.2", {"start": v(303, -100) * mm, "end": v(313, -100) * mm});
            skLineSegment(sketch, "E14.14.8.3", {"start": v(303, -110) * mm, "end": v(313, -110) * mm});
            skLineSegment(sketch, "E14.14.9.0", {"start": v(313, -96) * mm, "end": v(313, -86) * mm});
            skLineSegment(sketch, "E14.14.9.1", {"start": v(303, -96) * mm, "end": v(303, -86) * mm});
            skLineSegment(sketch, "E14.14.9.2", {"start": v(303, -86) * mm, "end": v(313, -86) * mm});
            skLineSegment(sketch, "E14.14.9.3", {"start": v(303, -96) * mm, "end": v(313, -96) * mm});
            skLineSegment(sketch, "E14.14.10.0", {"start": v(313, -82) * mm, "end": v(313, -72) * mm});
            skLineSegment(sketch, "E14.14.10.1", {"start": v(303, -82) * mm, "end": v(303, -72) * mm});
            skLineSegment(sketch, "E14.14.10.2", {"start": v(303, -72) * mm, "end": v(313, -72) * mm});
            skLineSegment(sketch, "E14.14.10.3", {"start": v(303, -82) * mm, "end": v(313, -82) * mm});
            skLineSegment(sketch, "E14.14.11.0", {"start": v(313, -68) * mm, "end": v(313, -58) * mm});
            skLineSegment(sketch, "E14.14.11.1", {"start": v(303, -68) * mm, "end": v(303, -58) * mm});
            skLineSegment(sketch, "E14.14.11.2", {"start": v(303, -58) * mm, "end": v(313, -58) * mm});
            skLineSegment(sketch, "E14.14.11.3", {"start": v(303, -68) * mm, "end": v(313, -68) * mm});
            skLineSegment(sketch, "E14.14.12.0", {"start": v(313, -54) * mm, "end": v(313, -44) * mm});
            skLineSegment(sketch, "E14.14.12.1", {"start": v(303, -54) * mm, "end": v(303, -44) * mm});
            skLineSegment(sketch, "E14.14.12.2", {"start": v(303, -44) * mm, "end": v(313, -44) * mm});
            skLineSegment(sketch, "E14.14.12.3", {"start": v(303, -54) * mm, "end": v(313, -54) * mm});
            skLineSegment(sketch, "E14.14.13.0", {"start": v(313, -40) * mm, "end": v(313, -30) * mm});
            skLineSegment(sketch, "E14.14.13.1", {"start": v(303, -40) * mm, "end": v(303, -30) * mm});
            skLineSegment(sketch, "E14.14.13.2", {"start": v(303, -30) * mm, "end": v(313, -30) * mm});
            skLineSegment(sketch, "E14.14.13.3", {"start": v(303, -40) * mm, "end": v(313, -40) * mm});
            skLineSegment(sketch, "E14.14.14.0", {"start": v(313, -26) * mm, "end": v(313, -16) * mm});
            skLineSegment(sketch, "E14.14.14.1", {"start": v(303, -26) * mm, "end": v(303, -16) * mm});
            skLineSegment(sketch, "E14.14.14.2", {"start": v(303, -16) * mm, "end": v(313, -16) * mm});
            skLineSegment(sketch, "E14.14.14.3", {"start": v(303, -26) * mm, "end": v(313, -26) * mm});
            skLineSegment(sketch, "E14.14.15.0", {"start": v(313, -12) * mm, "end": v(313, -2) * mm});
            skLineSegment(sketch, "E14.14.15.1", {"start": v(303, -12) * mm, "end": v(303, -2) * mm});
            skLineSegment(sketch, "E14.14.15.2", {"start": v(303, -2) * mm, "end": v(313, -2) * mm});
            skLineSegment(sketch, "E14.14.15.3", {"start": v(303, -12) * mm, "end": v(313, -12) * mm});
            skLineSegment(sketch, "E14.14.16.0", {"start": v(313, 2) * mm, "end": v(313, 12) * mm});
            skLineSegment(sketch, "E14.14.16.1", {"start": v(303, 2) * mm, "end": v(303, 12) * mm});
            skLineSegment(sketch, "E14.14.16.2", {"start": v(303, 12) * mm, "end": v(313, 12) * mm});
            skLineSegment(sketch, "E14.14.16.3", {"start": v(303, 2) * mm, "end": v(313, 2) * mm});
            skLineSegment(sketch, "E14.14.17.0", {"start": v(313, 16) * mm, "end": v(313, 26) * mm});
            skLineSegment(sketch, "E14.14.17.1", {"start": v(303, 16) * mm, "end": v(303, 26) * mm});
            skLineSegment(sketch, "E14.14.17.2", {"start": v(303, 26) * mm, "end": v(313, 26) * mm});
            skLineSegment(sketch, "E14.14.17.3", {"start": v(303, 16) * mm, "end": v(313, 16) * mm});
            skLineSegment(sketch, "E14.14.18.0", {"start": v(313, 30) * mm, "end": v(313, 40) * mm});
            skLineSegment(sketch, "E14.14.18.1", {"start": v(303, 30) * mm, "end": v(303, 40) * mm});
            skLineSegment(sketch, "E14.14.18.2", {"start": v(303, 40) * mm, "end": v(313, 40) * mm});
            skLineSegment(sketch, "E14.14.18.3", {"start": v(303, 30) * mm, "end": v(313, 30) * mm});
            skLineSegment(sketch, "E14.14.19.0", {"start": v(313, 44) * mm, "end": v(313, 54) * mm});
            skLineSegment(sketch, "E14.14.19.1", {"start": v(303, 44) * mm, "end": v(303, 54) * mm});
            skLineSegment(sketch, "E14.14.19.2", {"start": v(303, 54) * mm, "end": v(313, 54) * mm});
            skLineSegment(sketch, "E14.14.19.3", {"start": v(303, 44) * mm, "end": v(313, 44) * mm});
            skLineSegment(sketch, "E14.14.20.0", {"start": v(313, 58) * mm, "end": v(313, 68) * mm});
            skLineSegment(sketch, "E14.14.20.1", {"start": v(303, 58) * mm, "end": v(303, 68) * mm});
            skLineSegment(sketch, "E14.14.20.2", {"start": v(303, 68) * mm, "end": v(313, 68) * mm});
            skLineSegment(sketch, "E14.14.20.3", {"start": v(303, 58) * mm, "end": v(313, 58) * mm});
            skLineSegment(sketch, "E14.14.21.0", {"start": v(313, 72) * mm, "end": v(313, 82) * mm});
            skLineSegment(sketch, "E14.14.21.1", {"start": v(303, 72) * mm, "end": v(303, 82) * mm});
            skLineSegment(sketch, "E14.14.21.2", {"start": v(303, 82) * mm, "end": v(313, 82) * mm});
            skLineSegment(sketch, "E14.14.21.3", {"start": v(303, 72) * mm, "end": v(313, 72) * mm});
            skLineSegment(sketch, "E14.14.22.0", {"start": v(313, 86) * mm, "end": v(313, 96) * mm});
            skLineSegment(sketch, "E14.14.22.1", {"start": v(303, 86) * mm, "end": v(303, 96) * mm});
            skLineSegment(sketch, "E14.14.22.2", {"start": v(303, 96) * mm, "end": v(313, 96) * mm});
            skLineSegment(sketch, "E14.14.22.3", {"start": v(303, 86) * mm, "end": v(313, 86) * mm});
            skLineSegment(sketch, "E14.14.23.0", {"start": v(313, 100) * mm, "end": v(313, 110) * mm});
            skLineSegment(sketch, "E14.14.23.1", {"start": v(303, 100) * mm, "end": v(303, 110) * mm});
            skLineSegment(sketch, "E14.14.23.2", {"start": v(303, 110) * mm, "end": v(313, 110) * mm});
            skLineSegment(sketch, "E14.14.23.3", {"start": v(303, 100) * mm, "end": v(313, 100) * mm});
            skLineSegment(sketch, "E14.14.24.0", {"start": v(313, 114) * mm, "end": v(313, 124) * mm});
            skLineSegment(sketch, "E14.14.24.1", {"start": v(303, 114) * mm, "end": v(303, 124) * mm});
            skLineSegment(sketch, "E14.14.24.2", {"start": v(303, 124) * mm, "end": v(313, 124) * mm});
            skLineSegment(sketch, "E14.14.24.3", {"start": v(303, 114) * mm, "end": v(313, 114) * mm});
            skLineSegment(sketch, "E14.14.25.0", {"start": v(313, 128) * mm, "end": v(313, 138) * mm});
            skLineSegment(sketch, "E14.14.25.1", {"start": v(303, 128) * mm, "end": v(303, 138) * mm});
            skLineSegment(sketch, "E14.14.25.2", {"start": v(303, 138) * mm, "end": v(313, 138) * mm});
            skLineSegment(sketch, "E14.14.25.3", {"start": v(303, 128) * mm, "end": v(313, 128) * mm});
            skLineSegment(sketch, "E14.14.26.0", {"start": v(313, 142) * mm, "end": v(313, 152) * mm});
            skLineSegment(sketch, "E14.14.26.1", {"start": v(303, 142) * mm, "end": v(303, 152) * mm});
            skLineSegment(sketch, "E14.14.26.2", {"start": v(303, 152) * mm, "end": v(313, 152) * mm});
            skLineSegment(sketch, "E14.14.26.3", {"start": v(303, 142) * mm, "end": v(313, 142) * mm});
            skLineSegment(sketch, "E14.14.27.0", {"start": v(313, 156) * mm, "end": v(313, 166) * mm});
            skLineSegment(sketch, "E14.14.27.1", {"start": v(303, 156) * mm, "end": v(303, 166) * mm});
            skLineSegment(sketch, "E14.14.27.2", {"start": v(303, 166) * mm, "end": v(313, 166) * mm});
            skLineSegment(sketch, "E14.14.27.3", {"start": v(303, 156) * mm, "end": v(313, 156) * mm});
            skLineSegment(sketch, "E14.14.28.0", {"start": v(313, 170) * mm, "end": v(313, 180) * mm});
            skLineSegment(sketch, "E14.14.28.1", {"start": v(303, 170) * mm, "end": v(303, 180) * mm});
            skLineSegment(sketch, "E14.14.28.2", {"start": v(303, 180) * mm, "end": v(313, 180) * mm});
            skLineSegment(sketch, "E14.14.28.3", {"start": v(303, 170) * mm, "end": v(313, 170) * mm});
            skLineSegment(sketch, "E14.14.29.0", {"start": v(313, 184) * mm, "end": v(313, 194) * mm});
            skLineSegment(sketch, "E14.14.29.1", {"start": v(303, 184) * mm, "end": v(303, 194) * mm});
            skLineSegment(sketch, "E14.14.29.2", {"start": v(303, 194) * mm, "end": v(313, 194) * mm});
            skLineSegment(sketch, "E14.14.29.3", {"start": v(303, 184) * mm, "end": v(313, 184) * mm});
            skLineSegment(sketch, "E14.14.30.0", {"start": v(313, 198) * mm, "end": v(313, 208) * mm});
            skLineSegment(sketch, "E14.14.30.1", {"start": v(303, 198) * mm, "end": v(303, 208) * mm});
            skLineSegment(sketch, "E14.14.30.2", {"start": v(303, 208) * mm, "end": v(313, 208) * mm});
            skLineSegment(sketch, "E14.14.30.3", {"start": v(303, 198) * mm, "end": v(313, 198) * mm});
            skLineSegment(sketch, "E14.14.31.0", {"start": v(313, 212) * mm, "end": v(313, 222) * mm});
            skLineSegment(sketch, "E14.14.31.1", {"start": v(303, 212) * mm, "end": v(303, 222) * mm});
            skLineSegment(sketch, "E14.14.31.2", {"start": v(303, 222) * mm, "end": v(313, 222) * mm});
            skLineSegment(sketch, "E14.14.31.3", {"start": v(303, 212) * mm, "end": v(313, 212) * mm});
            skLineSegment(sketch, "E14.direction1", {"start": v(107, -222) * mm, "end": v(121, -222) * mm, "construction": true});
            skLineSegment(sketch, "E14.direction2", {"start": v(107, -222) * mm, "end": v(107, -208) * mm, "construction": true});
            skSolve(sketch);
        }
        {
            var Q0;
            Q0 = qSketchRegion(id + "F0", true);
            extrude(context, id + "F1", {"entities" : qUnion([Q0]), "oppositeDirection" : true, "depth" : 1.5 * mm});
        }
        {
            var Q0;
            Q0=makeQuery(id+"F1.opExtrude","CAP_FACE",FACE,{"disambiguationData":[OSD([sQuery(id+"F0.wireOp",EDGE,"E0.bottom"),sQuery(id+"F0.wireOp",EDGE,"E0.top"),sQuery(id+"F0.wireOp",EDGE,"E0.left"),sQuery(id+"F0.wireOp",EDGE,"E0.right"),sQuery(id+"F0.wireOp",EDGE,"E1.bottom"),sQuery(id+"F0.wireOp",EDGE,"E1.top"),sQuery(id+"F0.wireOp",EDGE,"E1.left"),sQuery(id+"F0.wireOp",EDGE,"E1.right"),sQuery(id+"F0.wireOp",EDGE,"E3.0.1.0"),sQuery(id+"F0.wireOp",EDGE,"E3.0.1.1"),sQuery(id+"F0.wireOp",EDGE,"E3.0.1.2"),sQuery(id+"F0.wireOp",EDGE,"E3.0.1.3"),sQuery(id+"F0.wireOp",EDGE,"E3.1.0.0"),sQuery(id+"F0.wireOp",EDGE,"E3.1.0.1"),sQuery(id+"F0.wireOp",EDGE,"E3.1.0.2"),sQuery(id+"F0.wireOp",EDGE,"E3.1.0.3"),sQuery(id+"F0.wireOp",EDGE,"E3.1.1.0"),sQuery(id+"F0.wireOp",EDGE,"E3.1.1.1"),sQuery(id+"F0.wireOp",EDGE,"E3.1.1.2"),sQuery(id+"F0.wireOp",EDGE,"E3.1.1.3"),sQuery(id+"F0.wireOp",EDGE,"E4.filletArc"),sQuery(id+"F0.wireOp",EDGE,"E5.filletArc"),sQuery(id+"F0.wireOp",EDGE,"E6.filletArc"),sQuery(id+"F0.wireOp",EDGE,"E7.filletArc"),sQuery(id+"F0.wireOp",EDGE,"E8.0.0.2"),sQuery(id+"F0.wireOp",EDGE,"E8.3.0.2"),sQuery(id+"F0.wireOp",EDGE,"E8.6.0.2"),sQuery(id+"F0.wireOp",EDGE,"E8.9.0.2"),sQuery(id+"F0.wireOp",EDGE,"E8.0.0.3"),sQuery(id+"F0.wireOp",EDGE,"E8.3.0.3"),sQuery(id+"F0.wireOp",EDGE,"E8.6.0.3"),sQuery(id+"F0.wireOp",EDGE,"E8.9.0.3"),sQuery(id+"F0.wireOp",EDGE,"E8.0.0.4"),sQuery(id+"F0.wireOp",EDGE,"E8.3.0.4"),sQuery(id+"F0.wireOp",EDGE,"E8.6.0.4"),sQuery(id+"F0.wireOp",EDGE,"E8.9.0.4"),sQuery(id+"F0.wireOp",EDGE,"E8.0.0.5"),sQuery(id+"F0.wireOp",EDGE,"E8.3.0.5"),sQuery(id+"F0.wireOp",EDGE,"E8.6.0.5"),sQuery(id+"F0.wireOp",EDGE,"E8.9.0.5"),sQuery(id+"F0.wireOp",EDGE,"E8.0.0.6"),sQuery(id+"F0.wireOp",EDGE,"E8.3.0.6"),sQuery(id+"F0.wireOp",EDGE,"E8.6.0.6"),sQuery(id+"F0.wireOp",EDGE,"E8.9.0.6"),sQuery(id+"F0.wireOp",EDGE,"E8.0.0.7"),sQuery(id+"F0.wireOp",EDGE,"E8.3.0.7"),sQuery(id+"F0.wireOp",EDGE,"E8.6.0.7"),sQuery(id+"F0.wireOp",EDGE,"E8.9.0.7"),sQuery(id+"F0.wireOp",EDGE,"E8.0.0.8"),sQuery(id+"F0.wireOp",EDGE,"E8.3.0.8"),sQuery(id+"F0.wireOp",EDGE,"E8.6.0.8"),sQuery(id+"F0.wireOp",EDGE,"E8.9.0.8"),sQuery(id+"F0.wireOp",EDGE,"E8.0.0.9"),sQuery(id+"F0.wireOp",EDGE,"E8.3.0.9"),sQuery(id+"F0.wireOp",EDGE,"E8.6.0.9"),sQuery(id+"F0.wireOp",EDGE,"E8.9.0.9"),sQuery(id+"F0.wireOp",EDGE,"E8.0.0.10"),sQuery(id+"F0.wireOp",EDGE,"E8.3.0.10"),sQuery(id+"F0.wireOp",EDGE,"E8.6.0.10"),sQuery(id+"F0.wireOp",EDGE,"E8.9.0.10"),sQuery(id+"F0.wireOp",EDGE,"E8.0.0.11"),sQuery(id+"F0.wireOp",EDGE,"E8.3.0.11"),sQuery(id+"F0.wireOp",EDGE,"E8.6.0.11"),sQuery(id+"F0.wireOp",EDGE,"E8.9.0.11"),sQuery(id+"F0.wireOp",EDGE,"E8.0.0.12"),sQuery(id+"F0.wireOp",EDGE,"E8.3.0.12"),sQuery(id+"F0.wireOp",EDGE,"E8.6.0.12"),sQuery(id+"F0.wireOp",EDGE,"E8.9.0.12"),sQuery(id+"F0.wireOp",EDGE,"E8.0.0.13"),sQuery(id+"F0.wireOp",EDGE,"E8.3.0.13"),sQuery(id+"F0.wireOp",EDGE,"E8.6.0.13"),sQuery(id+"F0.wireOp",EDGE,"E8.9.0.13"),sQuery(id+"F0.wireOp",EDGE,"E8.0.0.14"),sQuery(id+"F0.wireOp",EDGE,"E8.3.0.14"),sQuery(id+"F0.wireOp",EDGE,"E8.6.0.14"),sQuery(id+"F0.wireOp",EDGE,"E8.9.0.14"),sQuery(id+"F0.wireOp",EDGE,"E8.0.0.15"),sQuery(id+"F0.wireOp",EDGE,"E8.3.0.15"),sQuery(id+"F0.wireOp",EDGE,"E8.6.0.15"),sQuery(id+"F0.wireOp",EDGE,"E8.9.0.15"),sQuery(id+"F0.wireOp",EDGE,"E8.0.0.16"),sQuery(id+"F0.wireOp",EDGE,"E8.3.0.16"),sQuery(id+"F0.wireOp",EDGE,"E8.6.0.16"),sQuery(id+"F0.wireOp",EDGE,"E8.9.0.16"),sQuery(id+"F0.wireOp",EDGE,"E8.0.0.17"),sQuery(id+"F0.wireOp",EDGE,"E8.3.0.17"),sQuery(id+"F0.wireOp",EDGE,"E8.6.0.17"),sQuery(id+"F0.wireOp",EDGE,"E8.9.0.17"),sQuery(id+"F0.wireOp",EDGE,"E8.0.0.18"),sQuery(id+"F0.wireOp",EDGE,"E8.3.0.18"),sQuery(id+"F0.wireOp",EDGE,"E8.6.0.18"),sQuery(id+"F0.wireOp",EDGE,"E8.9.0.18"),sQuery(id+"F0.wireOp",EDGE,"E8.0.0.19"),sQuery(id+"F0.wireOp",EDGE,"E8.3.0.19"),sQuery(id+"F0.wireOp",EDGE,"E8.6.0.19"),sQuery(id+"F0.wireOp",EDGE,"E8.9.0.19"),sQuery(id+"F0.wireOp",EDGE,"E8.0.0.20"),sQuery(id+"F0.wireOp",EDGE,"E8.3.0.20"),sQuery(id+"F0.wireOp",EDGE,"E8.6.0.20"),sQuery(id+"F0.wireOp",EDGE,"E8.9.0.20"),sQuery(id+"F0.wireOp",EDGE,"E8.0.0.21"),sQuery(id+"F0.wireOp",EDGE,"E8.3.0.21"),sQuery(id+"F0.wireOp",EDGE,"E8.6.0.21"),sQuery(id+"F0.wireOp",EDGE,"E8.9.0.21"),sQuery(id+"F0.wireOp",EDGE,"E8.0.0.22"),sQuery(id+"F0.wireOp",EDGE,"E8.3.0.22"),sQuery(id+"F0.wireOp",EDGE,"E8.6.0.22"),sQuery(id+"F0.wireOp",EDGE,"E8.9.0.22"),sQuery(id+"F0.wireOp",EDGE,"E8.0.0.23"),sQuery(id+"F0.wireOp",EDGE,"E8.3.0.23"),sQuery(id+"F0.wireOp",EDGE,"E8.6.0.23"),sQuery(id+"F0.wireOp",EDGE,"E8.9.0.23"),sQuery(id+"F0.wireOp",EDGE,"E8.0.0.24"),sQuery(id+"F0.wireOp",EDGE,"E8.3.0.24"),sQuery(id+"F0.wireOp",EDGE,"E8.6.0.24"),sQuery(id+"F0.wireOp",EDGE,"E8.9.0.24"),sQuery(id+"F0.wireOp",EDGE,"E8.0.0.25"),sQuery(id+"F0.wireOp",EDGE,"E8.3.0.25"),sQuery(id+"F0.wireOp",EDGE,"E8.6.0.25"),sQuery(id+"F0.wireOp",EDGE,"E8.9.0.25"),sQuery(id+"F0.wireOp",EDGE,"E8.0.0.26"),sQuery(id+"F0.wireOp",EDGE,"E8.3.0.26"),sQuery(id+"F0.wireOp",EDGE,"E8.6.0.26"),sQuery(id+"F0.wireOp",EDGE,"E8.9.0.26"),sQuery(id+"F0.wireOp",EDGE,"E8.0.0.27"),sQuery(id+"F0.wireOp",EDGE,"E8.3.0.27"),sQuery(id+"F0.wireOp",EDGE,"E8.6.0.27"),sQuery(id+"F0.wireOp",EDGE,"E8.9.0.27"),sQuery(id+"F0.wireOp",EDGE,"E8.0.0.28"),sQuery(id+"F0.wireOp",EDGE,"E8.3.0.28"),sQuery(id+"F0.wireOp",EDGE,"E8.6.0.28"),sQuery(id+"F0.wireOp",EDGE,"E8.9.0.28"),sQuery(id+"F0.wireOp",EDGE,"E8.0.0.29"),sQuery(id+"F0.wireOp",EDGE,"E8.3.0.29"),sQuery(id+"F0.wireOp",EDGE,"E8.6.0.29"),sQuery(id+"F0.wireOp",EDGE,"E8.9.0.29"),sQuery(id+"F0.wireOp",EDGE,"E8.0.0.30"),sQuery(id+"F0.wireOp",EDGE,"E8.3.0.30"),sQuery(id+"F0.wireOp",EDGE,"E8.6.0.30"),sQuery(id+"F0.wireOp",EDGE,"E8.9.0.30"),sQuery(id+"F0.wireOp",EDGE,"E8.0.0.31"),sQuery(id+"F0.wireOp",EDGE,"E8.3.0.31"),sQuery(id+"F0.wireOp",EDGE,"E8.6.0.31"),sQuery(id+"F0.wireOp",EDGE,"E8.9.0.31"),sQuery(id+"F0.wireOp",EDGE,"E8.0.1.2"),sQuery(id+"F0.wireOp",EDGE,"E8.3.1.2"),sQuery(id+"F0.wireOp",EDGE,"E8.6.1.2"),sQuery(id+"F0.wireOp",EDGE,"E8.9.1.2"),sQuery(id+"F0.wireOp",EDGE,"E8.0.1.3"),sQuery(id+"F0.wireOp",EDGE,"E8.3.1.3"),sQuery(id+"F0.wireOp",EDGE,"E8.6.1.3"),sQuery(id+"F0.wireOp",EDGE,"E8.9.1.3"),sQuery(id+"F0.wireOp",EDGE,"E8.0.1.4"),sQuery(id+"F0.wireOp",EDGE,"E8.3.1.4"),sQuery(id+"F0.wireOp",EDGE,"E8.6.1.4"),sQuery(id+"F0.wireOp",EDGE,"E8.9.1.4"),sQuery(id+"F0.wireOp",EDGE,"E8.0.1.5"),sQuery(id+"F0.wireOp",EDGE,"E8.3.1.5"),sQuery(id+"F0.wireOp",EDGE,"E8.6.1.5"),sQuery(id+"F0.wireOp",EDGE,"E8.9.1.5"),sQuery(id+"F0.wireOp",EDGE,"E8.0.1.6"),sQuery(id+"F0.wireOp",EDGE,"E8.3.1.6"),sQuery(id+"F0.wireOp",EDGE,"E8.6.1.6"),sQuery(id+"F0.wireOp",EDGE,"E8.9.1.6"),sQuery(id+"F0.wireOp",EDGE,"E8.0.1.7"),sQuery(id+"F0.wireOp",EDGE,"E8.3.1.7"),sQuery(id+"F0.wireOp",EDGE,"E8.6.1.7"),sQuery(id+"F0.wireOp",EDGE,"E8.9.1.7"),sQuery(id+"F0.wireOp",EDGE,"E8.0.1.8"),sQuery(id+"F0.wireOp",EDGE,"E8.3.1.8"),sQuery(id+"F0.wireOp",EDGE,"E8.6.1.8"),sQuery(id+"F0.wireOp",EDGE,"E8.9.1.8"),sQuery(id+"F0.wireOp",EDGE,"E8.0.1.9"),sQuery(id+"F0.wireOp",EDGE,"E8.3.1.9"),sQuery(id+"F0.wireOp",EDGE,"E8.6.1.9"),sQuery(id+"F0.wireOp",EDGE,"E8.9.1.9"),sQuery(id+"F0.wireOp",EDGE,"E8.0.1.10"),sQuery(id+"F0.wireOp",EDGE,"E8.3.1.10"),sQuery(id+"F0.wireOp",EDGE,"E8.6.1.10"),sQuery(id+"F0.wireOp",EDGE,"E8.9.1.10"),sQuery(id+"F0.wireOp",EDGE,"E8.0.1.11"),sQuery(id+"F0.wireOp",EDGE,"E8.3.1.11"),sQuery(id+"F0.wireOp",EDGE,"E8.6.1.11"),sQuery(id+"F0.wireOp",EDGE,"E8.9.1.11"),sQuery(id+"F0.wireOp",EDGE,"E8.0.1.12"),sQuery(id+"F0.wireOp",EDGE,"E8.3.1.12"),sQuery(id+"F0.wireOp",EDGE,"E8.6.1.12"),sQuery(id+"F0.wireOp",EDGE,"E8.9.1.12"),sQuery(id+"F0.wireOp",EDGE,"E8.0.1.13"),sQuery(id+"F0.wireOp",EDGE,"E8.3.1.13"),sQuery(id+"F0.wireOp",EDGE,"E8.6.1.13"),sQuery(id+"F0.wireOp",EDGE,"E8.9.1.13"),sQuery(id+"F0.wireOp",EDGE,"E8.0.1.14"),sQuery(id+"F0.wireOp",EDGE,"E8.3.1.14"),sQuery(id+"F0.wireOp",EDGE,"E8.6.1.14"),sQuery(id+"F0.wireOp",EDGE,"E8.9.1.14"),sQuery(id+"F0.wireOp",EDGE,"E8.0.1.15"),sQuery(id+"F0.wireOp",EDGE,"E8.3.1.15"),sQuery(id+"F0.wireOp",EDGE,"E8.6.1.15"),sQuery(id+"F0.wireOp",EDGE,"E8.9.1.15"),sQuery(id+"F0.wireOp",EDGE,"E8.0.1.16"),sQuery(id+"F0.wireOp",EDGE,"E8.3.1.16"),sQuery(id+"F0.wireOp",EDGE,"E8.6.1.16"),sQuery(id+"F0.wireOp",EDGE,"E8.9.1.16"),sQuery(id+"F0.wireOp",EDGE,"E8.0.1.17"),sQuery(id+"F0.wireOp",EDGE,"E8.3.1.17"),sQuery(id+"F0.wireOp",EDGE,"E8.6.1.17"),sQuery(id+"F0.wireOp",EDGE,"E8.9.1.17"),sQuery(id+"F0.wireOp",EDGE,"E8.0.1.18"),sQuery(id+"F0.wireOp",EDGE,"E8.3.1.18"),sQuery(id+"F0.wireOp",EDGE,"E8.6.1.18"),sQuery(id+"F0.wireOp",EDGE,"E8.9.1.18"),sQuery(id+"F0.wireOp",EDGE,"E8.0.1.19"),sQuery(id+"F0.wireOp",EDGE,"E8.3.1.19"),sQuery(id+"F0.wireOp",EDGE,"E8.6.1.19"),sQuery(id+"F0.wireOp",EDGE,"E8.9.1.19"),sQuery(id+"F0.wireOp",EDGE,"E8.0.1.20"),sQuery(id+"F0.wireOp",EDGE,"E8.3.1.20"),sQuery(id+"F0.wireOp",EDGE,"E8.6.1.20"),sQuery(id+"F0.wireOp",EDGE,"E8.9.1.20"),sQuery(id+"F0.wireOp",EDGE,"E8.0.1.21"),sQuery(id+"F0.wireOp",EDGE,"E8.3.1.21"),sQuery(id+"F0.wireOp",EDGE,"E8.6.1.21"),sQuery(id+"F0.wireOp",EDGE,"E8.9.1.21"),sQuery(id+"F0.wireOp",EDGE,"E8.0.1.22"),sQuery(id+"F0.wireOp",EDGE,"E8.3.1.22"),sQuery(id+"F0.wireOp",EDGE,"E8.6.1.22"),sQuery(id+"F0.wireOp",EDGE,"E8.9.1.22"),sQuery(id+"F0.wireOp",EDGE,"E8.0.1.23"),sQuery(id+"F0.wireOp",EDGE,"E8.3.1.23"),sQuery(id+"F0.wireOp",EDGE,"E8.6.1.23"),sQuery(id+"F0.wireOp",EDGE,"E8.9.1.23"),sQuery(id+"F0.wireOp",EDGE,"E8.0.1.24"),sQuery(id+"F0.wireOp",EDGE,"E8.3.1.24"),sQuery(id+"F0.wireOp",EDGE,"E8.6.1.24"),sQuery(id+"F0.wireOp",EDGE,"E8.9.1.24"),sQuery(id+"F0.wireOp",EDGE,"E8.0.1.25"),sQuery(id+"F0.wireOp",EDGE,"E8.3.1.25"),sQuery(id+"F0.wireOp",EDGE,"E8.6.1.25"),sQuery(id+"F0.wireOp",EDGE,"E8.9.1.25"),sQuery(id+"F0.wireOp",EDGE,"E8.0.1.26"),sQuery(id+"F0.wireOp",EDGE,"E8.3.1.26"),sQuery(id+"F0.wireOp",EDGE,"E8.6.1.26"),sQuery(id+"F0.wireOp",EDGE,"E8.9.1.26"),sQuery(id+"F0.wireOp",EDGE,"E8.0.1.27"),sQuery(id+"F0.wireOp",EDGE,"E8.3.1.27"),sQuery(id+"F0.wireOp",EDGE,"E8.6.1.27"),sQuery(id+"F0.wireOp",EDGE,"E8.9.1.27"),sQuery(id+"F0.wireOp",EDGE,"E8.0.1.28"),sQuery(id+"F0.wireOp",EDGE,"E8.3.1.28"),sQuery(id+"F0.wireOp",EDGE,"E8.6.1.28"),sQuery(id+"F0.wireOp",EDGE,"E8.9.1.28"),sQuery(id+"F0.wireOp",EDGE,"E8.0.1.29"),sQuery(id+"F0.wireOp",EDGE,"E8.3.1.29"),sQuery(id+"F0.wireOp",EDGE,"E8.6.1.29"),sQuery(id+"F0.wireOp",EDGE,"E8.9.1.29"),sQuery(id+"F0.wireOp",EDGE,"E8.0.1.30"),sQuery(id+"F0.wireOp",EDGE,"E8.3.1.30"),sQuery(id+"F0.wireOp",EDGE,"E8.6.1.30"),sQuery(id+"F0.wireOp",EDGE,"E8.9.1.30"),sQuery(id+"F0.wireOp",EDGE,"E8.0.1.31"),sQuery(id+"F0.wireOp",EDGE,"E8.3.1.31"),sQuery(id+"F0.wireOp",EDGE,"E8.6.1.31"),sQuery(id+"F0.wireOp",EDGE,"E8.9.1.31"),sQuery(id+"F0.wireOp",EDGE,"E9.0.2.0"),sQuery(id+"F0.wireOp",EDGE,"E9.3.2.0"),sQuery(id+"F0.wireOp",EDGE,"E9.6.2.0"),sQuery(id+"F0.wireOp",EDGE,"E9.9.2.0"),sQuery(id+"F0.wireOp",EDGE,"E9.0.2.1"),sQuery(id+"F0.wireOp",EDGE,"E9.3.2.1"),sQuery(id+"F0.wireOp",EDGE,"E9.6.2.1"),sQuery(id+"F0.wireOp",EDGE,"E9.9.2.1"),sQuery(id+"F0.wireOp",EDGE,"E9.0.2.2"),sQuery(id+"F0.wireOp",EDGE,"E9.3.2.2"),sQuery(id+"F0.wireOp",EDGE,"E9.6.2.2"),sQuery(id+"F0.wireOp",EDGE,"E9.9.2.2"),sQuery(id+"F0.wireOp",EDGE,"E9.0.2.3"),sQuery(id+"F0.wireOp",EDGE,"E9.3.2.3"),sQuery(id+"F0.wireOp",EDGE,"E9.6.2.3"),sQuery(id+"F0.wireOp",EDGE,"E9.9.2.3"),sQuery(id+"F0.wireOp",EDGE,"E9.0.2.4"),sQuery(id+"F0.wireOp",EDGE,"E9.3.2.4"),sQuery(id+"F0.wireOp",EDGE,"E9.6.2.4"),sQuery(id+"F0.wireOp",EDGE,"E9.9.2.4"),sQuery(id+"F0.wireOp",EDGE,"E9.0.2.5"),sQuery(id+"F0.wireOp",EDGE,"E9.3.2.5"),sQuery(id+"F0.wireOp",EDGE,"E9.6.2.5"),sQuery(id+"F0.wireOp",EDGE,"E9.9.2.5"),sQuery(id+"F0.wireOp",EDGE,"E9.0.2.6"),sQuery(id+"F0.wireOp",EDGE,"E9.3.2.6"),sQuery(id+"F0.wireOp",EDGE,"E9.6.2.6"),sQuery(id+"F0.wireOp",EDGE,"E9.9.2.6"),sQuery(id+"F0.wireOp",EDGE,"E9.0.2.7"),sQuery(id+"F0.wireOp",EDGE,"E9.3.2.7"),sQuery(id+"F0.wireOp",EDGE,"E9.6.2.7"),sQuery(id+"F0.wireOp",EDGE,"E9.9.2.7"),sQuery(id+"F0.wireOp",EDGE,"E9.0.2.8"),sQuery(id+"F0.wireOp",EDGE,"E9.3.2.8"),sQuery(id+"F0.wireOp",EDGE,"E9.6.2.8"),sQuery(id+"F0.wireOp",EDGE,"E9.9.2.8"),sQuery(id+"F0.wireOp",EDGE,"E9.0.2.9"),sQuery(id+"F0.wireOp",EDGE,"E9.3.2.9"),sQuery(id+"F0.wireOp",EDGE,"E9.6.2.9"),sQuery(id+"F0.wireOp",EDGE,"E9.9.2.9"),sQuery(id+"F0.wireOp",EDGE,"E9.0.2.10"),sQuery(id+"F0.wireOp",EDGE,"E9.3.2.10"),sQuery(id+"F0.wireOp",EDGE,"E9.6.2.10"),sQuery(id+"F0.wireOp",EDGE,"E9.9.2.10"),sQuery(id+"F0.wireOp",EDGE,"E9.0.2.11"),sQuery(id+"F0.wireOp",EDGE,"E9.3.2.11"),sQuery(id+"F0.wireOp",EDGE,"E9.6.2.11"),sQuery(id+"F0.wireOp",EDGE,"E9.9.2.11"),sQuery(id+"F0.wireOp",EDGE,"E9.0.2.12"),sQuery(id+"F0.wireOp",EDGE,"E9.3.2.12"),sQuery(id+"F0.wireOp",EDGE,"E9.6.2.12"),sQuery(id+"F0.wireOp",EDGE,"E9.9.2.12"),sQuery(id+"F0.wireOp",EDGE,"E9.0.2.13"),sQuery(id+"F0.wireOp",EDGE,"E9.3.2.13"),sQuery(id+"F0.wireOp",EDGE,"E9.6.2.13"),sQuery(id+"F0.wireOp",EDGE,"E9.9.2.13"),sQuery(id+"F0.wireOp",EDGE,"E9.0.2.14"),sQuery(id+"F0.wireOp",EDGE,"E9.3.2.14"),sQuery(id+"F0.wireOp",EDGE,"E9.6.2.14"),sQuery(id+"F0.wireOp",EDGE,"E9.9.2.14"),sQuery(id+"F0.wireOp",EDGE,"E9.0.2.15"),sQuery(id+"F0.wireOp",EDGE,"E9.3.2.15"),sQuery(id+"F0.wireOp",EDGE,"E9.6.2.15"),sQuery(id+"F0.wireOp",EDGE,"E9.9.2.15"),sQuery(id+"F0.wireOp",EDGE,"E9.0.2.16"),sQuery(id+"F0.wireOp",EDGE,"E9.3.2.16"),sQuery(id+"F0.wireOp",EDGE,"E9.6.2.16"),sQuery(id+"F0.wireOp",EDGE,"E9.9.2.16"),sQuery(id+"F0.wireOp",EDGE,"E9.0.2.17"),sQuery(id+"F0.wireOp",EDGE,"E9.3.2.17"),sQuery(id+"F0.wireOp",EDGE,"E9.6.2.17"),sQuery(id+"F0.wireOp",EDGE,"E9.9.2.17"),sQuery(id+"F0.wireOp",EDGE,"E9.0.2.18"),sQuery(id+"F0.wireOp",EDGE,"E9.3.2.18"),sQuery(id+"F0.wireOp",EDGE,"E9.6.2.18"),sQuery(id+"F0.wireOp",EDGE,"E9.9.2.18"),sQuery(id+"F0.wireOp",EDGE,"E9.0.2.19"),sQuery(id+"F0.wireOp",EDGE,"E9.3.2.19"),sQuery(id+"F0.wireOp",EDGE,"E9.6.2.19"),sQuery(id+"F0.wireOp",EDGE,"E9.9.2.19"),sQuery(id+"F0.wireOp",EDGE,"E9.0.2.20"),sQuery(id+"F0.wireOp",EDGE,"E9.3.2.20"),sQuery(id+"F0.wireOp",EDGE,"E9.6.2.20"),sQuery(id+"F0.wireOp",EDGE,"E9.9.2.20"),sQuery(id+"F0.wireOp",EDGE,"E9.0.2.21"),sQuery(id+"F0.wireOp",EDGE,"E9.3.2.21"),sQuery(id+"F0.wireOp",EDGE,"E9.6.2.21"),sQuery(id+"F0.wireOp",EDGE,"E9.9.2.21"),sQuery(id+"F0.wireOp",EDGE,"E9.0.2.22"),sQuery(id+"F0.wireOp",EDGE,"E9.3.2.22"),sQuery(id+"F0.wireOp",EDGE,"E9.6.2.22"),sQuery(id+"F0.wireOp",EDGE,"E9.9.2.22"),sQuery(id+"F0.wireOp",EDGE,"E9.0.2.23"),sQuery(id+"F0.wireOp",EDGE,"E9.3.2.23"),sQuery(id+"F0.wireOp",EDGE,"E9.6.2.23"),sQuery(id+"F0.wireOp",EDGE,"E9.9.2.23"),sQuery(id+"F0.wireOp",EDGE,"E9.0.2.24"),sQuery(id+"F0.wireOp",EDGE,"E9.3.2.24"),sQuery(id+"F0.wireOp",EDGE,"E9.6.2.24"),sQuery(id+"F0.wireOp",EDGE,"E9.9.2.24"),sQuery(id+"F0.wireOp",EDGE,"E9.0.2.25"),sQuery(id+"F0.wireOp",EDGE,"E9.3.2.25"),sQuery(id+"F0.wireOp",EDGE,"E9.6.2.25"),sQuery(id+"F0.wireOp",EDGE,"E9.9.2.25"),sQuery(id+"F0.wireOp",EDGE,"E9.0.2.26"),sQuery(id+"F0.wireOp",EDGE,"E9.3.2.26"),sQuery(id+"F0.wireOp",EDGE,"E9.6.2.26"),sQuery(id+"F0.wireOp",EDGE,"E9.9.2.26"),sQuery(id+"F0.wireOp",EDGE,"E9.0.2.27"),sQuery(id+"F0.wireOp",EDGE,"E9.3.2.27"),sQuery(id+"F0.wireOp",EDGE,"E9.6.2.27"),sQuery(id+"F0.wireOp",EDGE,"E9.9.2.27"),sQuery(id+"F0.wireOp",EDGE,"E9.0.2.28"),sQuery(id+"F0.wireOp",EDGE,"E9.3.2.28"),sQuery(id+"F0.wireOp",EDGE,"E9.6.2.28"),sQuery(id+"F0.wireOp",EDGE,"E9.9.2.28"),sQuery(id+"F0.wireOp",EDGE,"E9.0.2.29"),sQuery(id+"F0.wireOp",EDGE,"E9.3.2.29"),sQuery(id+"F0.wireOp",EDGE,"E9.6.2.29"),sQuery(id+"F0.wireOp",EDGE,"E9.9.2.29"),sQuery(id+"F0.wireOp",EDGE,"E9.0.2.30"),sQuery(id+"F0.wireOp",EDGE,"E9.3.2.30"),sQuery(id+"F0.wireOp",EDGE,"E9.6.2.30"),sQuery(id+"F0.wireOp",EDGE,"E9.9.2.30"),sQuery(id+"F0.wireOp",EDGE,"E9.0.2.31"),sQuery(id+"F0.wireOp",EDGE,"E9.3.2.31"),sQuery(id+"F0.wireOp",EDGE,"E9.6.2.31"),sQuery(id+"F0.wireOp",EDGE,"E9.9.2.31"),sQuery(id+"F0.wireOp",EDGE,"E9.0.3.0"),sQuery(id+"F0.wireOp",EDGE,"E9.3.3.0"),sQuery(id+"F0.wireOp",EDGE,"E9.6.3.0"),sQuery(id+"F0.wireOp",EDGE,"E9.9.3.0"),sQuery(id+"F0.wireOp",EDGE,"E9.0.3.1"),sQuery(id+"F0.wireOp",EDGE,"E9.3.3.1"),sQuery(id+"F0.wireOp",EDGE,"E9.6.3.1"),sQuery(id+"F0.wireOp",EDGE,"E9.9.3.1"),sQuery(id+"F0.wireOp",EDGE,"E9.0.3.2"),sQuery(id+"F0.wireOp",EDGE,"E9.3.3.2"),sQuery(id+"F0.wireOp",EDGE,"E9.6.3.2"),sQuery(id+"F0.wireOp",EDGE,"E9.9.3.2"),sQuery(id+"F0.wireOp",EDGE,"E9.0.3.3"),sQuery(id+"F0.wireOp",EDGE,"E9.3.3.3"),sQuery(id+"F0.wireOp",EDGE,"E9.6.3.3"),sQuery(id+"F0.wireOp",EDGE,"E9.9.3.3"),sQuery(id+"F0.wireOp",EDGE,"E9.0.3.4"),sQuery(id+"F0.wireOp",EDGE,"E9.3.3.4"),sQuery(id+"F0.wireOp",EDGE,"E9.6.3.4"),sQuery(id+"F0.wireOp",EDGE,"E9.9.3.4"),sQuery(id+"F0.wireOp",EDGE,"E9.0.3.5"),sQuery(id+"F0.wireOp",EDGE,"E9.3.3.5"),sQuery(id+"F0.wireOp",EDGE,"E9.6.3.5"),sQuery(id+"F0.wireOp",EDGE,"E9.9.3.5"),sQuery(id+"F0.wireOp",EDGE,"E9.0.3.6"),sQuery(id+"F0.wireOp",EDGE,"E9.3.3.6"),sQuery(id+"F0.wireOp",EDGE,"E9.6.3.6"),sQuery(id+"F0.wireOp",EDGE,"E9.9.3.6"),sQuery(id+"F0.wireOp",EDGE,"E9.0.3.7"),sQuery(id+"F0.wireOp",EDGE,"E9.3.3.7"),sQuery(id+"F0.wireOp",EDGE,"E9.6.3.7"),sQuery(id+"F0.wireOp",EDGE,"E9.9.3.7"),sQuery(id+"F0.wireOp",EDGE,"E9.0.3.8"),sQuery(id+"F0.wireOp",EDGE,"E9.3.3.8"),sQuery(id+"F0.wireOp",EDGE,"E9.6.3.8"),sQuery(id+"F0.wireOp",EDGE,"E9.9.3.8"),sQuery(id+"F0.wireOp",EDGE,"E9.0.3.9"),sQuery(id+"F0.wireOp",EDGE,"E9.3.3.9"),sQuery(id+"F0.wireOp",EDGE,"E9.6.3.9"),sQuery(id+"F0.wireOp",EDGE,"E9.9.3.9"),sQuery(id+"F0.wireOp",EDGE,"E9.0.3.10"),sQuery(id+"F0.wireOp",EDGE,"E9.3.3.10"),sQuery(id+"F0.wireOp",EDGE,"E9.6.3.10"),sQuery(id+"F0.wireOp",EDGE,"E9.9.3.10"),sQuery(id+"F0.wireOp",EDGE,"E9.0.3.11"),sQuery(id+"F0.wireOp",EDGE,"E9.3.3.11"),sQuery(id+"F0.wireOp",EDGE,"E9.6.3.11"),sQuery(id+"F0.wireOp",EDGE,"E9.9.3.11"),sQuery(id+"F0.wireOp",EDGE,"E9.0.3.12"),sQuery(id+"F0.wireOp",EDGE,"E9.3.3.12"),sQuery(id+"F0.wireOp",EDGE,"E9.6.3.12"),sQuery(id+"F0.wireOp",EDGE,"E9.9.3.12"),sQuery(id+"F0.wireOp",EDGE,"E9.0.3.13"),sQuery(id+"F0.wireOp",EDGE,"E9.3.3.13"),sQuery(id+"F0.wireOp",EDGE,"E9.6.3.13"),sQuery(id+"F0.wireOp",EDGE,"E9.9.3.13"),sQuery(id+"F0.wireOp",EDGE,"E9.0.3.14"),sQuery(id+"F0.wireOp",EDGE,"E9.3.3.14"),sQuery(id+"F0.wireOp",EDGE,"E9.6.3.14"),sQuery(id+"F0.wireOp",EDGE,"E9.9.3.14"),sQuery(id+"F0.wireOp",EDGE,"E9.0.3.15"),sQuery(id+"F0.wireOp",EDGE,"E9.3.3.15"),sQuery(id+"F0.wireOp",EDGE,"E9.6.3.15"),sQuery(id+"F0.wireOp",EDGE,"E9.9.3.15"),sQuery(id+"F0.wireOp",EDGE,"E9.0.3.16"),sQuery(id+"F0.wireOp",EDGE,"E9.3.3.16"),sQuery(id+"F0.wireOp",EDGE,"E9.6.3.16"),sQuery(id+"F0.wireOp",EDGE,"E9.9.3.16"),sQuery(id+"F0.wireOp",EDGE,"E9.0.3.17"),sQuery(id+"F0.wireOp",EDGE,"E9.3.3.17"),sQuery(id+"F0.wireOp",EDGE,"E9.6.3.17"),sQuery(id+"F0.wireOp",EDGE,"E9.9.3.17"),sQuery(id+"F0.wireOp",EDGE,"E9.0.3.18"),sQuery(id+"F0.wireOp",EDGE,"E9.3.3.18"),sQuery(id+"F0.wireOp",EDGE,"E9.6.3.18"),sQuery(id+"F0.wireOp",EDGE,"E9.9.3.18"),sQuery(id+"F0.wireOp",EDGE,"E9.0.3.19"),sQuery(id+"F0.wireOp",EDGE,"E9.3.3.19"),sQuery(id+"F0.wireOp",EDGE,"E9.6.3.19"),sQuery(id+"F0.wireOp",EDGE,"E9.9.3.19"),sQuery(id+"F0.wireOp",EDGE,"E9.0.3.20"),sQuery(id+"F0.wireOp",EDGE,"E9.3.3.20"),sQuery(id+"F0.wireOp",EDGE,"E9.6.3.20"),sQuery(id+"F0.wireOp",EDGE,"E9.9.3.20"),sQuery(id+"F0.wireOp",EDGE,"E9.0.3.21"),sQuery(id+"F0.wireOp",EDGE,"E9.3.3.21"),sQuery(id+"F0.wireOp",EDGE,"E9.6.3.21"),sQuery(id+"F0.wireOp",EDGE,"E9.9.3.21"),sQuery(id+"F0.wireOp",EDGE,"E9.0.3.22"),sQuery(id+"F0.wireOp",EDGE,"E9.3.3.22"),sQuery(id+"F0.wireOp",EDGE,"E9.6.3.22"),sQuery(id+"F0.wireOp",EDGE,"E9.9.3.22"),sQuery(id+"F0.wireOp",EDGE,"E9.0.3.23"),sQuery(id+"F0.wireOp",EDGE,"E9.3.3.23"),sQuery(id+"F0.wireOp",EDGE,"E9.6.3.23"),sQuery(id+"F0.wireOp",EDGE,"E9.9.3.23"),sQuery(id+"F0.wireOp",EDGE,"E9.0.3.24"),sQuery(id+"F0.wireOp",EDGE,"E9.3.3.24"),sQuery(id+"F0.wireOp",EDGE,"E9.6.3.24"),sQuery(id+"F0.wireOp",EDGE,"E9.9.3.24"),sQuery(id+"F0.wireOp",EDGE,"E9.0.3.25"),sQuery(id+"F0.wireOp",EDGE,"E9.3.3.25"),sQuery(id+"F0.wireOp",EDGE,"E9.6.3.25"),sQuery(id+"F0.wireOp",EDGE,"E9.9.3.25"),sQuery(id+"F0.wireOp",EDGE,"E9.0.3.26"),sQuery(id+"F0.wireOp",EDGE,"E9.3.3.26"),sQuery(id+"F0.wireOp",EDGE,"E9.6.3.26"),sQuery(id+"F0.wireOp",EDGE,"E9.9.3.26"),sQuery(id+"F0.wireOp",EDGE,"E9.0.3.27"),sQuery(id+"F0.wireOp",EDGE,"E9.3.3.27"),sQuery(id+"F0.wireOp",EDGE,"E9.6.3.27"),sQuery(id+"F0.wireOp",EDGE,"E9.9.3.27"),sQuery(id+"F0.wireOp",EDGE,"E9.0.3.28"),sQuery(id+"F0.wireOp",EDGE,"E9.3.3.28"),sQuery(id+"F0.wireOp",EDGE,"E9.6.3.28"),sQuery(id+"F0.wireOp",EDGE,"E9.9.3.28"),sQuery(id+"F0.wireOp",EDGE,"E9.0.3.29"),sQuery(id+"F0.wireOp",EDGE,"E9.3.3.29"),sQuery(id+"F0.wireOp",EDGE,"E9.6.3.29"),sQuery(id+"F0.wireOp",EDGE,"E9.9.3.29"),sQuery(id+"F0.wireOp",EDGE,"E9.0.3.30"),sQuery(id+"F0.wireOp",EDGE,"E9.3.3.30"),sQuery(id+"F0.wireOp",EDGE,"E9.6.3.30"),sQuery(id+"F0.wireOp",EDGE,"E9.9.3.30"),sQuery(id+"F0.wireOp",EDGE,"E9.0.3.31"),sQuery(id+"F0.wireOp",EDGE,"E9.3.3.31"),sQuery(id+"F0.wireOp",EDGE,"E9.6.3.31"),sQuery(id+"F0.wireOp",EDGE,"E9.9.3.31"),sQuery(id+"F0.wireOp",EDGE,"E9.0.4.0"),sQuery(id+"F0.wireOp",EDGE,"E9.3.4.0"),sQuery(id+"F0.wireOp",EDGE,"E9.6.4.0"),sQuery(id+"F0.wireOp",EDGE,"E9.9.4.0"),sQuery(id+"F0.wireOp",EDGE,"E9.0.4.1"),sQuery(id+"F0.wireOp",EDGE,"E9.3.4.1"),sQuery(id+"F0.wireOp",EDGE,"E9.6.4.1"),sQuery(id+"F0.wireOp",EDGE,"E9.9.4.1"),sQuery(id+"F0.wireOp",EDGE,"E9.0.4.2"),sQuery(id+"F0.wireOp",EDGE,"E9.3.4.2"),sQuery(id+"F0.wireOp",EDGE,"E9.6.4.2"),sQuery(id+"F0.wireOp",EDGE,"E9.9.4.2"),sQuery(id+"F0.wireOp",EDGE,"E9.0.4.3"),sQuery(id+"F0.wireOp",EDGE,"E9.3.4.3"),sQuery(id+"F0.wireOp",EDGE,"E9.6.4.3"),sQuery(id+"F0.wireOp",EDGE,"E9.9.4.3"),sQuery(id+"F0.wireOp",EDGE,"E9.0.4.4"),sQuery(id+"F0.wireOp",EDGE,"E9.3.4.4"),sQuery(id+"F0.wireOp",EDGE,"E9.6.4.4"),sQuery(id+"F0.wireOp",EDGE,"E9.9.4.4"),sQuery(id+"F0.wireOp",EDGE,"E9.0.4.5"),sQuery(id+"F0.wireOp",EDGE,"E9.3.4.5"),sQuery(id+"F0.wireOp",EDGE,"E9.6.4.5"),sQuery(id+"F0.wireOp",EDGE,"E9.9.4.5"),sQuery(id+"F0.wireOp",EDGE,"E9.0.4.6"),sQuery(id+"F0.wireOp",EDGE,"E9.3.4.6"),sQuery(id+"F0.wireOp",EDGE,"E9.6.4.6"),sQuery(id+"F0.wireOp",EDGE,"E9.9.4.6"),sQuery(id+"F0.wireOp",EDGE,"E9.0.4.7"),sQuery(id+"F0.wireOp",EDGE,"E9.3.4.7"),sQuery(id+"F0.wireOp",EDGE,"E9.6.4.7"),sQuery(id+"F0.wireOp",EDGE,"E9.9.4.7"),sQuery(id+"F0.wireOp",EDGE,"E9.0.4.8"),sQuery(id+"F0.wireOp",EDGE,"E9.3.4.8"),sQuery(id+"F0.wireOp",EDGE,"E9.6.4.8"),sQuery(id+"F0.wireOp",EDGE,"E9.9.4.8"),sQuery(id+"F0.wireOp",EDGE,"E9.0.4.9"),sQuery(id+"F0.wireOp",EDGE,"E9.3.4.9"),sQuery(id+"F0.wireOp",EDGE,"E9.6.4.9"),sQuery(id+"F0.wireOp",EDGE,"E9.9.4.9"),sQuery(id+"F0.wireOp",EDGE,"E9.0.4.10"),sQuery(id+"F0.wireOp",EDGE,"E9.3.4.10"),sQuery(id+"F0.wireOp",EDGE,"E9.6.4.10"),sQuery(id+"F0.wireOp",EDGE,"E9.9.4.10"),sQuery(id+"F0.wireOp",EDGE,"E9.0.4.11"),sQuery(id+"F0.wireOp",EDGE,"E9.3.4.11"),sQuery(id+"F0.wireOp",EDGE,"E9.6.4.11"),sQuery(id+"F0.wireOp",EDGE,"E9.9.4.11"),sQuery(id+"F0.wireOp",EDGE,"E9.0.4.12"),sQuery(id+"F0.wireOp",EDGE,"E9.3.4.12"),sQuery(id+"F0.wireOp",EDGE,"E9.6.4.12"),sQuery(id+"F0.wireOp",EDGE,"E9.9.4.12"),sQuery(id+"F0.wireOp",EDGE,"E9.0.4.13"),sQuery(id+"F0.wireOp",EDGE,"E9.3.4.13"),sQuery(id+"F0.wireOp",EDGE,"E9.6.4.13"),sQuery(id+"F0.wireOp",EDGE,"E9.9.4.13"),sQuery(id+"F0.wireOp",EDGE,"E9.0.4.14"),sQuery(id+"F0.wireOp",EDGE,"E9.3.4.14"),sQuery(id+"F0.wireOp",EDGE,"E9.6.4.14"),sQuery(id+"F0.wireOp",EDGE,"E9.9.4.14"),sQuery(id+"F0.wireOp",EDGE,"E9.0.4.15"),sQuery(id+"F0.wireOp",EDGE,"E9.3.4.15"),sQuery(id+"F0.wireOp",EDGE,"E9.6.4.15"),sQuery(id+"F0.wireOp",EDGE,"E9.9.4.15"),sQuery(id+"F0.wireOp",EDGE,"E9.0.4.16"),sQuery(id+"F0.wireOp",EDGE,"E9.3.4.16"),sQuery(id+"F0.wireOp",EDGE,"E9.6.4.16"),sQuery(id+"F0.wireOp",EDGE,"E9.9.4.16"),sQuery(id+"F0.wireOp",EDGE,"E9.0.4.17"),sQuery(id+"F0.wireOp",EDGE,"E9.3.4.17"),sQuery(id+"F0.wireOp",EDGE,"E9.6.4.17"),sQuery(id+"F0.wireOp",EDGE,"E9.9.4.17"),sQuery(id+"F0.wireOp",EDGE,"E9.0.4.18"),sQuery(id+"F0.wireOp",EDGE,"E9.3.4.18"),sQuery(id+"F0.wireOp",EDGE,"E9.6.4.18"),sQuery(id+"F0.wireOp",EDGE,"E9.9.4.18"),sQuery(id+"F0.wireOp",EDGE,"E9.0.4.19"),sQuery(id+"F0.wireOp",EDGE,"E9.3.4.19"),sQuery(id+"F0.wireOp",EDGE,"E9.6.4.19"),sQuery(id+"F0.wireOp",EDGE,"E9.9.4.19"),sQuery(id+"F0.wireOp",EDGE,"E9.0.4.20"),sQuery(id+"F0.wireOp",EDGE,"E9.3.4.20"),sQuery(id+"F0.wireOp",EDGE,"E9.6.4.20"),sQuery(id+"F0.wireOp",EDGE,"E9.9.4.20"),sQuery(id+"F0.wireOp",EDGE,"E9.0.4.21"),sQuery(id+"F0.wireOp",EDGE,"E9.3.4.21"),sQuery(id+"F0.wireOp",EDGE,"E9.6.4.21"),sQuery(id+"F0.wireOp",EDGE,"E9.9.4.21"),sQuery(id+"F0.wireOp",EDGE,"E9.0.4.22"),sQuery(id+"F0.wireOp",EDGE,"E9.3.4.22"),sQuery(id+"F0.wireOp",EDGE,"E9.6.4.22"),sQuery(id+"F0.wireOp",EDGE,"E9.9.4.22"),sQuery(id+"F0.wireOp",EDGE,"E9.0.4.23"),sQuery(id+"F0.wireOp",EDGE,"E9.3.4.23"),sQuery(id+"F0.wireOp",EDGE,"E9.6.4.23"),sQuery(id+"F0.wireOp",EDGE,"E9.9.4.23"),sQuery(id+"F0.wireOp",EDGE,"E9.0.4.24"),sQuery(id+"F0.wireOp",EDGE,"E9.3.4.24"),sQuery(id+"F0.wireOp",EDGE,"E9.6.4.24"),sQuery(id+"F0.wireOp",EDGE,"E9.9.4.24"),sQuery(id+"F0.wireOp",EDGE,"E9.0.4.25"),sQuery(id+"F0.wireOp",EDGE,"E9.3.4.25"),sQuery(id+"F0.wireOp",EDGE,"E9.6.4.25"),sQuery(id+"F0.wireOp",EDGE,"E9.9.4.25"),sQuery(id+"F0.wireOp",EDGE,"E9.0.4.26"),sQuery(id+"F0.wireOp",EDGE,"E9.3.4.26"),sQuery(id+"F0.wireOp",EDGE,"E9.6.4.26"),sQuery(id+"F0.wireOp",EDGE,"E9.9.4.26"),sQuery(id+"F0.wireOp",EDGE,"E9.0.4.27"),sQuery(id+"F0.wireOp",EDGE,"E9.3.4.27"),sQuery(id+"F0.wireOp",EDGE,"E9.6.4.27"),sQuery(id+"F0.wireOp",EDGE,"E9.9.4.27"),sQuery(id+"F0.wireOp",EDGE,"E9.0.4.28"),sQuery(id+"F0.wireOp",EDGE,"E9.3.4.28"),sQuery(id+"F0.wireOp",EDGE,"E9.6.4.28"),sQuery(id+"F0.wireOp",EDGE,"E9.9.4.28"),sQuery(id+"F0.wireOp",EDGE,"E9.0.4.29"),sQuery(id+"F0.wireOp",EDGE,"E9.3.4.29"),sQuery(id+"F0.wireOp",EDGE,"E9.6.4.29"),sQuery(id+"F0.wireOp",EDGE,"E9.9.4.29"),sQuery(id+"F0.wireOp",EDGE,"E9.0.4.30"),sQuery(id+"F0.wireOp",EDGE,"E9.3.4.30"),sQuery(id+"F0.wireOp",EDGE,"E9.6.4.30"),sQuery(id+"F0.wireOp",EDGE,"E9.9.4.30"),sQuery(id+"F0.wireOp",EDGE,"E9.0.4.31"),sQuery(id+"F0.wireOp",EDGE,"E9.3.4.31"),sQuery(id+"F0.wireOp",EDGE,"E9.6.4.31"),sQuery(id+"F0.wireOp",EDGE,"E9.9.4.31"),sQuery(id+"F0.wireOp",EDGE,"E9.0.5.0"),sQuery(id+"F0.wireOp",EDGE,"E9.3.5.0"),sQuery(id+"F0.wireOp",EDGE,"E9.6.5.0"),sQuery(id+"F0.wireOp",EDGE,"E9.9.5.0"),sQuery(id+"F0.wireOp",EDGE,"E9.0.5.1"),sQuery(id+"F0.wireOp",EDGE,"E9.3.5.1"),sQuery(id+"F0.wireOp",EDGE,"E9.6.5.1"),sQuery(id+"F0.wireOp",EDGE,"E9.9.5.1"),sQuery(id+"F0.wireOp",EDGE,"E9.0.5.2"),sQuery(id+"F0.wireOp",EDGE,"E9.3.5.2"),sQuery(id+"F0.wireOp",EDGE,"E9.6.5.2"),sQuery(id+"F0.wireOp",EDGE,"E9.9.5.2"),sQuery(id+"F0.wireOp",EDGE,"E9.0.5.3"),sQuery(id+"F0.wireOp",EDGE,"E9.3.5.3"),sQuery(id+"F0.wireOp",EDGE,"E9.6.5.3"),sQuery(id+"F0.wireOp",EDGE,"E9.9.5.3"),sQuery(id+"F0.wireOp",EDGE,"E9.0.5.4"),sQuery(id+"F0.wireOp",EDGE,"E9.3.5.4"),sQuery(id+"F0.wireOp",EDGE,"E9.6.5.4"),sQuery(id+"F0.wireOp",EDGE,"E9.9.5.4"),sQuery(id+"F0.wireOp",EDGE,"E9.0.5.5"),sQuery(id+"F0.wireOp",EDGE,"E9.3.5.5"),sQuery(id+"F0.wireOp",EDGE,"E9.6.5.5"),sQuery(id+"F0.wireOp",EDGE,"E9.9.5.5"),sQuery(id+"F0.wireOp",EDGE,"E9.0.5.6"),sQuery(id+"F0.wireOp",EDGE,"E9.3.5.6"),sQuery(id+"F0.wireOp",EDGE,"E9.6.5.6"),sQuery(id+"F0.wireOp",EDGE,"E9.9.5.6"),sQuery(id+"F0.wireOp",EDGE,"E9.0.5.7"),sQuery(id+"F0.wireOp",EDGE,"E9.3.5.7"),sQuery(id+"F0.wireOp",EDGE,"E9.6.5.7"),sQuery(id+"F0.wireOp",EDGE,"E9.9.5.7"),sQuery(id+"F0.wireOp",EDGE,"E9.0.5.8"),sQuery(id+"F0.wireOp",EDGE,"E9.3.5.8"),sQuery(id+"F0.wireOp",EDGE,"E9.6.5.8"),sQuery(id+"F0.wireOp",EDGE,"E9.9.5.8"),sQuery(id+"F0.wireOp",EDGE,"E9.0.5.9"),sQuery(id+"F0.wireOp",EDGE,"E9.3.5.9"),sQuery(id+"F0.wireOp",EDGE,"E9.6.5.9"),sQuery(id+"F0.wireOp",EDGE,"E9.9.5.9"),sQuery(id+"F0.wireOp",EDGE,"E9.0.5.10"),sQuery(id+"F0.wireOp",EDGE,"E9.3.5.10"),sQuery(id+"F0.wireOp",EDGE,"E9.6.5.10"),sQuery(id+"F0.wireOp",EDGE,"E9.9.5.10"),sQuery(id+"F0.wireOp",EDGE,"E9.0.5.11"),sQuery(id+"F0.wireOp",EDGE,"E9.3.5.11"),sQuery(id+"F0.wireOp",EDGE,"E9.6.5.11"),sQuery(id+"F0.wireOp",EDGE,"E9.9.5.11"),sQuery(id+"F0.wireOp",EDGE,"E9.0.5.12"),sQuery(id+"F0.wireOp",EDGE,"E9.3.5.12"),sQuery(id+"F0.wireOp",EDGE,"E9.6.5.12"),sQuery(id+"F0.wireOp",EDGE,"E9.9.5.12"),sQuery(id+"F0.wireOp",EDGE,"E9.0.5.13"),sQuery(id+"F0.wireOp",EDGE,"E9.3.5.13"),sQuery(id+"F0.wireOp",EDGE,"E9.6.5.13"),sQuery(id+"F0.wireOp",EDGE,"E9.9.5.13"),sQuery(id+"F0.wireOp",EDGE,"E9.0.5.14"),sQuery(id+"F0.wireOp",EDGE,"E9.3.5.14"),sQuery(id+"F0.wireOp",EDGE,"E9.6.5.14"),sQuery(id+"F0.wireOp",EDGE,"E9.9.5.14"),sQuery(id+"F0.wireOp",EDGE,"E9.0.5.15"),sQuery(id+"F0.wireOp",EDGE,"E9.3.5.15"),sQuery(id+"F0.wireOp",EDGE,"E9.6.5.15"),sQuery(id+"F0.wireOp",EDGE,"E9.9.5.15"),sQuery(id+"F0.wireOp",EDGE,"E9.0.5.16"),sQuery(id+"F0.wireOp",EDGE,"E9.3.5.16"),sQuery(id+"F0.wireOp",EDGE,"E9.6.5.16"),sQuery(id+"F0.wireOp",EDGE,"E9.9.5.16"),sQuery(id+"F0.wireOp",EDGE,"E9.0.5.17"),sQuery(id+"F0.wireOp",EDGE,"E9.3.5.17"),sQuery(id+"F0.wireOp",EDGE,"E9.6.5.17"),sQuery(id+"F0.wireOp",EDGE,"E9.9.5.17"),sQuery(id+"F0.wireOp",EDGE,"E9.0.5.18"),sQuery(id+"F0.wireOp",EDGE,"E9.3.5.18"),sQuery(id+"F0.wireOp",EDGE,"E9.6.5.18"),sQuery(id+"F0.wireOp",EDGE,"E9.9.5.18"),sQuery(id+"F0.wireOp",EDGE,"E9.0.5.19"),sQuery(id+"F0.wireOp",EDGE,"E9.3.5.19"),sQuery(id+"F0.wireOp",EDGE,"E9.6.5.19"),sQuery(id+"F0.wireOp",EDGE,"E9.9.5.19"),sQuery(id+"F0.wireOp",EDGE,"E9.0.5.20"),sQuery(id+"F0.wireOp",EDGE,"E9.3.5.20"),sQuery(id+"F0.wireOp",EDGE,"E9.6.5.20"),sQuery(id+"F0.wireOp",EDGE,"E9.9.5.20"),sQuery(id+"F0.wireOp",EDGE,"E9.0.5.21"),sQuery(id+"F0.wireOp",EDGE,"E9.3.5.21"),sQuery(id+"F0.wireOp",EDGE,"E9.6.5.21"),sQuery(id+"F0.wireOp",EDGE,"E9.9.5.21"),sQuery(id+"F0.wireOp",EDGE,"E9.0.5.22"),sQuery(id+"F0.wireOp",EDGE,"E9.3.5.22"),sQuery(id+"F0.wireOp",EDGE,"E9.6.5.22"),sQuery(id+"F0.wireOp",EDGE,"E9.9.5.22"),sQuery(id+"F0.wireOp",EDGE,"E9.0.5.23"),sQuery(id+"F0.wireOp",EDGE,"E9.3.5.23"),sQuery(id+"F0.wireOp",EDGE,"E9.6.5.23"),sQuery(id+"F0.wireOp",EDGE,"E9.9.5.23"),sQuery(id+"F0.wireOp",EDGE,"E9.0.5.24"),sQuery(id+"F0.wireOp",EDGE,"E9.3.5.24"),sQuery(id+"F0.wireOp",EDGE,"E9.6.5.24"),sQuery(id+"F0.wireOp",EDGE,"E9.9.5.24"),sQuery(id+"F0.wireOp",EDGE,"E9.0.5.25"),sQuery(id+"F0.wireOp",EDGE,"E9.3.5.25"),sQuery(id+"F0.wireOp",EDGE,"E9.6.5.25"),sQuery(id+"F0.wireOp",EDGE,"E9.9.5.25"),sQuery(id+"F0.wireOp",EDGE,"E9.0.5.26"),sQuery(id+"F0.wireOp",EDGE,"E9.3.5.26"),sQuery(id+"F0.wireOp",EDGE,"E9.6.5.26"),sQuery(id+"F0.wireOp",EDGE,"E9.9.5.26"),sQuery(id+"F0.wireOp",EDGE,"E9.0.5.27"),sQuery(id+"F0.wireOp",EDGE,"E9.3.5.27"),sQuery(id+"F0.wireOp",EDGE,"E9.6.5.27"),sQuery(id+"F0.wireOp",EDGE,"E9.9.5.27"),sQuery(id+"F0.wireOp",EDGE,"E9.0.5.28"),sQuery(id+"F0.wireOp",EDGE,"E9.3.5.28"),sQuery(id+"F0.wireOp",EDGE,"E9.6.5.28"),sQuery(id+"F0.wireOp",EDGE,"E9.9.5.28"),sQuery(id+"F0.wireOp",EDGE,"E9.0.5.29"),sQuery(id+"F0.wireOp",EDGE,"E9.3.5.29"),sQuery(id+"F0.wireOp",EDGE,"E9.6.5.29"),sQuery(id+"F0.wireOp",EDGE,"E9.9.5.29"),sQuery(id+"F0.wireOp",EDGE,"E9.0.5.30"),sQuery(id+"F0.wireOp",EDGE,"E9.3.5.30"),sQuery(id+"F0.wireOp",EDGE,"E9.6.5.30"),sQuery(id+"F0.wireOp",EDGE,"E9.9.5.30"),sQuery(id+"F0.wireOp",EDGE,"E9.0.5.31"),sQuery(id+"F0.wireOp",EDGE,"E9.3.5.31"),sQuery(id+"F0.wireOp",EDGE,"E9.6.5.31"),sQuery(id+"F0.wireOp",EDGE,"E9.9.5.31"),sQuery(id+"F0.wireOp",EDGE,"E9.0.6.0"),sQuery(id+"F0.wireOp",EDGE,"E9.3.6.0"),sQuery(id+"F0.wireOp",EDGE,"E9.6.6.0"),sQuery(id+"F0.wireOp",EDGE,"E9.9.6.0"),sQuery(id+"F0.wireOp",EDGE,"E9.0.6.1"),sQuery(id+"F0.wireOp",EDGE,"E9.3.6.1"),sQuery(id+"F0.wireOp",EDGE,"E9.6.6.1"),sQuery(id+"F0.wireOp",EDGE,"E9.9.6.1"),sQuery(id+"F0.wireOp",EDGE,"E9.0.6.2"),sQuery(id+"F0.wireOp",EDGE,"E9.3.6.2"),sQuery(id+"F0.wireOp",EDGE,"E9.6.6.2"),sQuery(id+"F0.wireOp",EDGE,"E9.9.6.2"),sQuery(id+"F0.wireOp",EDGE,"E9.0.6.3"),sQuery(id+"F0.wireOp",EDGE,"E9.3.6.3"),sQuery(id+"F0.wireOp",EDGE,"E9.6.6.3"),sQuery(id+"F0.wireOp",EDGE,"E9.9.6.3"),sQuery(id+"F0.wireOp",EDGE,"E9.0.6.4"),sQuery(id+"F0.wireOp",EDGE,"E9.3.6.4"),sQuery(id+"F0.wireOp",EDGE,"E9.6.6.4"),sQuery(id+"F0.wireOp",EDGE,"E9.9.6.4"),sQuery(id+"F0.wireOp",EDGE,"E9.0.6.5"),sQuery(id+"F0.wireOp",EDGE,"E9.3.6.5"),sQuery(id+"F0.wireOp",EDGE,"E9.6.6.5"),sQuery(id+"F0.wireOp",EDGE,"E9.9.6.5"),sQuery(id+"F0.wireOp",EDGE,"E9.0.6.6"),sQuery(id+"F0.wireOp",EDGE,"E9.3.6.6"),sQuery(id+"F0.wireOp",EDGE,"E9.6.6.6"),sQuery(id+"F0.wireOp",EDGE,"E9.9.6.6"),sQuery(id+"F0.wireOp",EDGE,"E9.0.6.7"),sQuery(id+"F0.wireOp",EDGE,"E9.3.6.7"),sQuery(id+"F0.wireOp",EDGE,"E9.6.6.7"),sQuery(id+"F0.wireOp",EDGE,"E9.9.6.7"),sQuery(id+"F0.wireOp",EDGE,"E9.0.6.8"),sQuery(id+"F0.wireOp",EDGE,"E9.3.6.8"),sQuery(id+"F0.wireOp",EDGE,"E9.6.6.8"),sQuery(id+"F0.wireOp",EDGE,"E9.9.6.8"),sQuery(id+"F0.wireOp",EDGE,"E9.0.6.9"),sQuery(id+"F0.wireOp",EDGE,"E9.3.6.9"),sQuery(id+"F0.wireOp",EDGE,"E9.6.6.9"),sQuery(id+"F0.wireOp",EDGE,"E9.9.6.9"),sQuery(id+"F0.wireOp",EDGE,"E9.0.6.10"),sQuery(id+"F0.wireOp",EDGE,"E9.3.6.10"),sQuery(id+"F0.wireOp",EDGE,"E9.6.6.10"),sQuery(id+"F0.wireOp",EDGE,"E9.9.6.10"),sQuery(id+"F0.wireOp",EDGE,"E9.0.6.11"),sQuery(id+"F0.wireOp",EDGE,"E9.3.6.11"),sQuery(id+"F0.wireOp",EDGE,"E9.6.6.11"),sQuery(id+"F0.wireOp",EDGE,"E9.9.6.11"),sQuery(id+"F0.wireOp",EDGE,"E9.0.6.12"),sQuery(id+"F0.wireOp",EDGE,"E9.3.6.12"),sQuery(id+"F0.wireOp",EDGE,"E9.6.6.12"),sQuery(id+"F0.wireOp",EDGE,"E9.9.6.12"),sQuery(id+"F0.wireOp",EDGE,"E9.0.6.13"),sQuery(id+"F0.wireOp",EDGE,"E9.3.6.13"),sQuery(id+"F0.wireOp",EDGE,"E9.6.6.13"),sQuery(id+"F0.wireOp",EDGE,"E9.9.6.13"),sQuery(id+"F0.wireOp",EDGE,"E9.0.6.14"),sQuery(id+"F0.wireOp",EDGE,"E9.3.6.14"),sQuery(id+"F0.wireOp",EDGE,"E9.6.6.14"),sQuery(id+"F0.wireOp",EDGE,"E9.9.6.14"),sQuery(id+"F0.wireOp",EDGE,"E9.0.6.15"),sQuery(id+"F0.wireOp",EDGE,"E9.3.6.15"),sQuery(id+"F0.wireOp",EDGE,"E9.6.6.15"),sQuery(id+"F0.wireOp",EDGE,"E9.9.6.15"),sQuery(id+"F0.wireOp",EDGE,"E9.0.6.16"),sQuery(id+"F0.wireOp",EDGE,"E9.3.6.16"),sQuery(id+"F0.wireOp",EDGE,"E9.6.6.16"),sQuery(id+"F0.wireOp",EDGE,"E9.9.6.16"),sQuery(id+"F0.wireOp",EDGE,"E9.0.6.17"),sQuery(id+"F0.wireOp",EDGE,"E9.3.6.17"),sQuery(id+"F0.wireOp",EDGE,"E9.6.6.17"),sQuery(id+"F0.wireOp",EDGE,"E9.9.6.17"),sQuery(id+"F0.wireOp",EDGE,"E9.0.6.18"),sQuery(id+"F0.wireOp",EDGE,"E9.3.6.18"),sQuery(id+"F0.wireOp",EDGE,"E9.6.6.18"),sQuery(id+"F0.wireOp",EDGE,"E9.9.6.18"),sQuery(id+"F0.wireOp",EDGE,"E9.0.6.19"),sQuery(id+"F0.wireOp",EDGE,"E9.3.6.19"),sQuery(id+"F0.wireOp",EDGE,"E9.6.6.19"),sQuery(id+"F0.wireOp",EDGE,"E9.9.6.19"),sQuery(id+"F0.wireOp",EDGE,"E9.0.6.20"),sQuery(id+"F0.wireOp",EDGE,"E9.3.6.20"),sQuery(id+"F0.wireOp",EDGE,"E9.6.6.20"),sQuery(id+"F0.wireOp",EDGE,"E9.9.6.20"),sQuery(id+"F0.wireOp",EDGE,"E9.0.6.21"),sQuery(id+"F0.wireOp",EDGE,"E9.3.6.21"),sQuery(id+"F0.wireOp",EDGE,"E9.6.6.21"),sQuery(id+"F0.wireOp",EDGE,"E9.9.6.21"),sQuery(id+"F0.wireOp",EDGE,"E9.0.6.22"),sQuery(id+"F0.wireOp",EDGE,"E9.3.6.22"),sQuery(id+"F0.wireOp",EDGE,"E9.6.6.22"),sQuery(id+"F0.wireOp",EDGE,"E9.9.6.22"),sQuery(id+"F0.wireOp",EDGE,"E9.0.6.23"),sQuery(id+"F0.wireOp",EDGE,"E9.3.6.23"),sQuery(id+"F0.wireOp",EDGE,"E9.6.6.23"),sQuery(id+"F0.wireOp",EDGE,"E9.9.6.23"),sQuery(id+"F0.wireOp",EDGE,"E9.0.6.24"),sQuery(id+"F0.wireOp",EDGE,"E9.3.6.24"),sQuery(id+"F0.wireOp",EDGE,"E9.6.6.24"),sQuery(id+"F0.wireOp",EDGE,"E9.9.6.24"),sQuery(id+"F0.wireOp",EDGE,"E9.0.6.25"),sQuery(id+"F0.wireOp",EDGE,"E9.3.6.25"),sQuery(id+"F0.wireOp",EDGE,"E9.6.6.25"),sQuery(id+"F0.wireOp",EDGE,"E9.9.6.25"),sQuery(id+"F0.wireOp",EDGE,"E9.0.6.26"),sQuery(id+"F0.wireOp",EDGE,"E9.3.6.26"),sQuery(id+"F0.wireOp",EDGE,"E9.6.6.26"),sQuery(id+"F0.wireOp",EDGE,"E9.9.6.26"),sQuery(id+"F0.wireOp",EDGE,"E9.0.6.27"),sQuery(id+"F0.wireOp",EDGE,"E9.3.6.27"),sQuery(id+"F0.wireOp",EDGE,"E9.6.6.27"),sQuery(id+"F0.wireOp",EDGE,"E9.9.6.27"),sQuery(id+"F0.wireOp",EDGE,"E9.0.6.28"),sQuery(id+"F0.wireOp",EDGE,"E9.3.6.28"),sQuery(id+"F0.wireOp",EDGE,"E9.6.6.28"),sQuery(id+"F0.wireOp",EDGE,"E9.9.6.28"),sQuery(id+"F0.wireOp",EDGE,"E9.0.6.29"),sQuery(id+"F0.wireOp",EDGE,"E9.3.6.29"),sQuery(id+"F0.wireOp",EDGE,"E9.6.6.29"),sQuery(id+"F0.wireOp",EDGE,"E9.9.6.29"),sQuery(id+"F0.wireOp",EDGE,"E9.0.6.30"),sQuery(id+"F0.wireOp",EDGE,"E9.3.6.30"),sQuery(id+"F0.wireOp",EDGE,"E9.6.6.30"),sQuery(id+"F0.wireOp",EDGE,"E9.9.6.30"),sQuery(id+"F0.wireOp",EDGE,"E9.0.6.31"),sQuery(id+"F0.wireOp",EDGE,"E9.3.6.31"),sQuery(id+"F0.wireOp",EDGE,"E9.6.6.31"),sQuery(id+"F0.wireOp",EDGE,"E9.9.6.31"),sQuery(id+"F0.wireOp",EDGE,"E9.0.7.0"),sQuery(id+"F0.wireOp",EDGE,"E9.3.7.0"),sQuery(id+"F0.wireOp",EDGE,"E9.6.7.0"),sQuery(id+"F0.wireOp",EDGE,"E9.9.7.0"),sQuery(id+"F0.wireOp",EDGE,"E9.0.7.1"),sQuery(id+"F0.wireOp",EDGE,"E9.3.7.1"),sQuery(id+"F0.wireOp",EDGE,"E9.6.7.1"),sQuery(id+"F0.wireOp",EDGE,"E9.9.7.1"),sQuery(id+"F0.wireOp",EDGE,"E9.0.7.2"),sQuery(id+"F0.wireOp",EDGE,"E9.3.7.2"),sQuery(id+"F0.wireOp",EDGE,"E9.6.7.2"),sQuery(id+"F0.wireOp",EDGE,"E9.9.7.2"),sQuery(id+"F0.wireOp",EDGE,"E9.0.7.3"),sQuery(id+"F0.wireOp",EDGE,"E9.3.7.3"),sQuery(id+"F0.wireOp",EDGE,"E9.6.7.3"),sQuery(id+"F0.wireOp",EDGE,"E9.9.7.3"),sQuery(id+"F0.wireOp",EDGE,"E9.0.7.4"),sQuery(id+"F0.wireOp",EDGE,"E9.3.7.4"),sQuery(id+"F0.wireOp",EDGE,"E9.6.7.4"),sQuery(id+"F0.wireOp",EDGE,"E9.9.7.4"),sQuery(id+"F0.wireOp",EDGE,"E9.0.7.5"),sQuery(id+"F0.wireOp",EDGE,"E9.3.7.5"),sQuery(id+"F0.wireOp",EDGE,"E9.6.7.5"),sQuery(id+"F0.wireOp",EDGE,"E9.9.7.5"),sQuery(id+"F0.wireOp",EDGE,"E9.0.7.6"),sQuery(id+"F0.wireOp",EDGE,"E9.3.7.6"),sQuery(id+"F0.wireOp",EDGE,"E9.6.7.6"),sQuery(id+"F0.wireOp",EDGE,"E9.9.7.6"),sQuery(id+"F0.wireOp",EDGE,"E9.0.7.7"),sQuery(id+"F0.wireOp",EDGE,"E9.3.7.7"),sQuery(id+"F0.wireOp",EDGE,"E9.6.7.7"),sQuery(id+"F0.wireOp",EDGE,"E9.9.7.7"),sQuery(id+"F0.wireOp",EDGE,"E9.0.7.8"),sQuery(id+"F0.wireOp",EDGE,"E9.3.7.8"),sQuery(id+"F0.wireOp",EDGE,"E9.6.7.8"),sQuery(id+"F0.wireOp",EDGE,"E9.9.7.8"),sQuery(id+"F0.wireOp",EDGE,"E9.0.7.9"),sQuery(id+"F0.wireOp",EDGE,"E9.3.7.9"),sQuery(id+"F0.wireOp",EDGE,"E9.6.7.9"),sQuery(id+"F0.wireOp",EDGE,"E9.9.7.9"),sQuery(id+"F0.wireOp",EDGE,"E9.0.7.10"),sQuery(id+"F0.wireOp",EDGE,"E9.3.7.10"),sQuery(id+"F0.wireOp",EDGE,"E9.6.7.10"),sQuery(id+"F0.wireOp",EDGE,"E9.9.7.10"),sQuery(id+"F0.wireOp",EDGE,"E9.0.7.11"),sQuery(id+"F0.wireOp",EDGE,"E9.3.7.11"),sQuery(id+"F0.wireOp",EDGE,"E9.6.7.11"),sQuery(id+"F0.wireOp",EDGE,"E9.9.7.11"),sQuery(id+"F0.wireOp",EDGE,"E9.0.7.12"),sQuery(id+"F0.wireOp",EDGE,"E9.3.7.12"),sQuery(id+"F0.wireOp",EDGE,"E9.6.7.12"),sQuery(id+"F0.wireOp",EDGE,"E9.9.7.12"),sQuery(id+"F0.wireOp",EDGE,"E9.0.7.13"),sQuery(id+"F0.wireOp",EDGE,"E9.3.7.13"),sQuery(id+"F0.wireOp",EDGE,"E9.6.7.13"),sQuery(id+"F0.wireOp",EDGE,"E9.9.7.13"),sQuery(id+"F0.wireOp",EDGE,"E9.0.7.14"),sQuery(id+"F0.wireOp",EDGE,"E9.3.7.14"),sQuery(id+"F0.wireOp",EDGE,"E9.6.7.14"),sQuery(id+"F0.wireOp",EDGE,"E9.9.7.14"),sQuery(id+"F0.wireOp",EDGE,"E9.0.7.15"),sQuery(id+"F0.wireOp",EDGE,"E9.3.7.15"),sQuery(id+"F0.wireOp",EDGE,"E9.6.7.15"),sQuery(id+"F0.wireOp",EDGE,"E9.9.7.15"),sQuery(id+"F0.wireOp",EDGE,"E9.0.7.16"),sQuery(id+"F0.wireOp",EDGE,"E9.3.7.16"),sQuery(id+"F0.wireOp",EDGE,"E9.6.7.16"),sQuery(id+"F0.wireOp",EDGE,"E9.9.7.16"),sQuery(id+"F0.wireOp",EDGE,"E9.0.7.17"),sQuery(id+"F0.wireOp",EDGE,"E9.3.7.17"),sQuery(id+"F0.wireOp",EDGE,"E9.6.7.17"),sQuery(id+"F0.wireOp",EDGE,"E9.9.7.17"),sQuery(id+"F0.wireOp",EDGE,"E9.0.7.18"),sQuery(id+"F0.wireOp",EDGE,"E9.3.7.18"),sQuery(id+"F0.wireOp",EDGE,"E9.6.7.18"),sQuery(id+"F0.wireOp",EDGE,"E9.9.7.18"),sQuery(id+"F0.wireOp",EDGE,"E9.0.7.19"),sQuery(id+"F0.wireOp",EDGE,"E9.3.7.19"),sQuery(id+"F0.wireOp",EDGE,"E9.6.7.19"),sQuery(id+"F0.wireOp",EDGE,"E9.9.7.19"),sQuery(id+"F0.wireOp",EDGE,"E9.0.7.20"),sQuery(id+"F0.wireOp",EDGE,"E9.3.7.20"),sQuery(id+"F0.wireOp",EDGE,"E9.6.7.20"),sQuery(id+"F0.wireOp",EDGE,"E9.9.7.20"),sQuery(id+"F0.wireOp",EDGE,"E9.0.7.21"),sQuery(id+"F0.wireOp",EDGE,"E9.3.7.21"),sQuery(id+"F0.wireOp",EDGE,"E9.6.7.21"),sQuery(id+"F0.wireOp",EDGE,"E9.9.7.21"),sQuery(id+"F0.wireOp",EDGE,"E9.0.7.22"),sQuery(id+"F0.wireOp",EDGE,"E9.3.7.22"),sQuery(id+"F0.wireOp",EDGE,"E9.6.7.22"),sQuery(id+"F0.wireOp",EDGE,"E9.9.7.22"),sQuery(id+"F0.wireOp",EDGE,"E9.0.7.23"),sQuery(id+"F0.wireOp",EDGE,"E9.3.7.23"),sQuery(id+"F0.wireOp",EDGE,"E9.6.7.23"),sQuery(id+"F0.wireOp",EDGE,"E9.9.7.23"),sQuery(id+"F0.wireOp",EDGE,"E9.0.7.24"),sQuery(id+"F0.wireOp",EDGE,"E9.3.7.24"),sQuery(id+"F0.wireOp",EDGE,"E9.6.7.24"),sQuery(id+"F0.wireOp",EDGE,"E9.9.7.24"),sQuery(id+"F0.wireOp",EDGE,"E9.0.7.25"),sQuery(id+"F0.wireOp",EDGE,"E9.3.7.25"),sQuery(id+"F0.wireOp",EDGE,"E9.6.7.25"),sQuery(id+"F0.wireOp",EDGE,"E9.9.7.25"),sQuery(id+"F0.wireOp",EDGE,"E9.0.7.26"),sQuery(id+"F0.wireOp",EDGE,"E9.3.7.26"),sQuery(id+"F0.wireOp",EDGE,"E9.6.7.26"),sQuery(id+"F0.wireOp",EDGE,"E9.9.7.26"),sQuery(id+"F0.wireOp",EDGE,"E9.0.7.27"),sQuery(id+"F0.wireOp",EDGE,"E9.3.7.27"),sQuery(id+"F0.wireOp",EDGE,"E9.6.7.27"),sQuery(id+"F0.wireOp",EDGE,"E9.9.7.27"),sQuery(id+"F0.wireOp",EDGE,"E9.0.7.28"),sQuery(id+"F0.wireOp",EDGE,"E9.3.7.28"),sQuery(id+"F0.wireOp",EDGE,"E9.6.7.28"),sQuery(id+"F0.wireOp",EDGE,"E9.9.7.28"),sQuery(id+"F0.wireOp",EDGE,"E9.0.7.29"),sQuery(id+"F0.wireOp",EDGE,"E9.3.7.29"),sQuery(id+"F0.wireOp",EDGE,"E9.6.7.29"),sQuery(id+"F0.wireOp",EDGE,"E9.9.7.29"),sQuery(id+"F0.wireOp",EDGE,"E9.0.7.30"),sQuery(id+"F0.wireOp",EDGE,"E9.3.7.30"),sQuery(id+"F0.wireOp",EDGE,"E9.6.7.30"),sQuery(id+"F0.wireOp",EDGE,"E9.9.7.30"),sQuery(id+"F0.wireOp",EDGE,"E9.0.7.31"),sQuery(id+"F0.wireOp",EDGE,"E9.3.7.31"),sQuery(id+"F0.wireOp",EDGE,"E9.6.7.31"),sQuery(id+"F0.wireOp",EDGE,"E9.9.7.31"),sQuery(id+"F0.wireOp",EDGE,"E9.0.8.0"),sQuery(id+"F0.wireOp",EDGE,"E9.3.8.0"),sQuery(id+"F0.wireOp",EDGE,"E9.6.8.0"),sQuery(id+"F0.wireOp",EDGE,"E9.9.8.0"),sQuery(id+"F0.wireOp",EDGE,"E9.0.8.1"),sQuery(id+"F0.wireOp",EDGE,"E9.3.8.1"),sQuery(id+"F0.wireOp",EDGE,"E9.6.8.1"),sQuery(id+"F0.wireOp",EDGE,"E9.9.8.1"),sQuery(id+"F0.wireOp",EDGE,"E9.0.8.2"),sQuery(id+"F0.wireOp",EDGE,"E9.3.8.2"),sQuery(id+"F0.wireOp",EDGE,"E9.6.8.2"),sQuery(id+"F0.wireOp",EDGE,"E9.9.8.2"),sQuery(id+"F0.wireOp",EDGE,"E9.0.8.3"),sQuery(id+"F0.wireOp",EDGE,"E9.3.8.3"),sQuery(id+"F0.wireOp",EDGE,"E9.6.8.3"),sQuery(id+"F0.wireOp",EDGE,"E9.9.8.3"),sQuery(id+"F0.wireOp",EDGE,"E9.0.8.4"),sQuery(id+"F0.wireOp",EDGE,"E9.3.8.4"),sQuery(id+"F0.wireOp",EDGE,"E9.6.8.4"),sQuery(id+"F0.wireOp",EDGE,"E9.9.8.4"),sQuery(id+"F0.wireOp",EDGE,"E9.0.8.5"),sQuery(id+"F0.wireOp",EDGE,"E9.3.8.5"),sQuery(id+"F0.wireOp",EDGE,"E9.6.8.5"),sQuery(id+"F0.wireOp",EDGE,"E9.9.8.5"),sQuery(id+"F0.wireOp",EDGE,"E9.0.8.6"),sQuery(id+"F0.wireOp",EDGE,"E9.3.8.6"),sQuery(id+"F0.wireOp",EDGE,"E9.6.8.6"),sQuery(id+"F0.wireOp",EDGE,"E9.9.8.6"),sQuery(id+"F0.wireOp",EDGE,"E9.0.8.7"),sQuery(id+"F0.wireOp",EDGE,"E9.3.8.7"),sQuery(id+"F0.wireOp",EDGE,"E9.6.8.7"),sQuery(id+"F0.wireOp",EDGE,"E9.9.8.7"),sQuery(id+"F0.wireOp",EDGE,"E9.0.8.8"),sQuery(id+"F0.wireOp",EDGE,"E9.3.8.8"),sQuery(id+"F0.wireOp",EDGE,"E9.6.8.8"),sQuery(id+"F0.wireOp",EDGE,"E9.9.8.8"),sQuery(id+"F0.wireOp",EDGE,"E9.0.8.9"),sQuery(id+"F0.wireOp",EDGE,"E9.3.8.9"),sQuery(id+"F0.wireOp",EDGE,"E9.6.8.9"),sQuery(id+"F0.wireOp",EDGE,"E9.9.8.9"),sQuery(id+"F0.wireOp",EDGE,"E9.0.8.10"),sQuery(id+"F0.wireOp",EDGE,"E9.3.8.10"),sQuery(id+"F0.wireOp",EDGE,"E9.6.8.10"),sQuery(id+"F0.wireOp",EDGE,"E9.9.8.10"),sQuery(id+"F0.wireOp",EDGE,"E9.0.8.11"),sQuery(id+"F0.wireOp",EDGE,"E9.3.8.11"),sQuery(id+"F0.wireOp",EDGE,"E9.6.8.11"),sQuery(id+"F0.wireOp",EDGE,"E9.9.8.11"),sQuery(id+"F0.wireOp",EDGE,"E9.0.8.12"),sQuery(id+"F0.wireOp",EDGE,"E9.3.8.12"),sQuery(id+"F0.wireOp",EDGE,"E9.6.8.12"),sQuery(id+"F0.wireOp",EDGE,"E9.9.8.12"),sQuery(id+"F0.wireOp",EDGE,"E9.0.8.13"),sQuery(id+"F0.wireOp",EDGE,"E9.3.8.13"),sQuery(id+"F0.wireOp",EDGE,"E9.6.8.13"),sQuery(id+"F0.wireOp",EDGE,"E9.9.8.13"),sQuery(id+"F0.wireOp",EDGE,"E9.0.8.14"),sQuery(id+"F0.wireOp",EDGE,"E9.3.8.14"),sQuery(id+"F0.wireOp",EDGE,"E9.6.8.14"),sQuery(id+"F0.wireOp",EDGE,"E9.9.8.14"),sQuery(id+"F0.wireOp",EDGE,"E9.0.8.15"),sQuery(id+"F0.wireOp",EDGE,"E9.3.8.15"),sQuery(id+"F0.wireOp",EDGE,"E9.6.8.15"),sQuery(id+"F0.wireOp",EDGE,"E9.9.8.15"),sQuery(id+"F0.wireOp",EDGE,"E9.0.8.16"),sQuery(id+"F0.wireOp",EDGE,"E9.3.8.16"),sQuery(id+"F0.wireOp",EDGE,"E9.6.8.16"),sQuery(id+"F0.wireOp",EDGE,"E9.9.8.16"),sQuery(id+"F0.wireOp",EDGE,"E9.0.8.17"),sQuery(id+"F0.wireOp",EDGE,"E9.3.8.17"),sQuery(id+"F0.wireOp",EDGE,"E9.6.8.17"),sQuery(id+"F0.wireOp",EDGE,"E9.9.8.17"),sQuery(id+"F0.wireOp",EDGE,"E9.0.8.18"),sQuery(id+"F0.wireOp",EDGE,"E9.3.8.18"),sQuery(id+"F0.wireOp",EDGE,"E9.6.8.18"),sQuery(id+"F0.wireOp",EDGE,"E9.9.8.18"),sQuery(id+"F0.wireOp",EDGE,"E9.0.8.19"),sQuery(id+"F0.wireOp",EDGE,"E9.3.8.19"),sQuery(id+"F0.wireOp",EDGE,"E9.6.8.19"),sQuery(id+"F0.wireOp",EDGE,"E9.9.8.19"),sQuery(id+"F0.wireOp",EDGE,"E9.0.8.20"),sQuery(id+"F0.wireOp",EDGE,"E9.3.8.20"),sQuery(id+"F0.wireOp",EDGE,"E9.6.8.20"),sQuery(id+"F0.wireOp",EDGE,"E9.9.8.20"),sQuery(id+"F0.wireOp",EDGE,"E9.0.8.21"),sQuery(id+"F0.wireOp",EDGE,"E9.3.8.21"),sQuery(id+"F0.wireOp",EDGE,"E9.6.8.21"),sQuery(id+"F0.wireOp",EDGE,"E9.9.8.21"),sQuery(id+"F0.wireOp",EDGE,"E9.0.8.22"),sQuery(id+"F0.wireOp",EDGE,"E9.3.8.22"),sQuery(id+"F0.wireOp",EDGE,"E9.6.8.22"),sQuery(id+"F0.wireOp",EDGE,"E9.9.8.22"),sQuery(id+"F0.wireOp",EDGE,"E9.0.8.23"),sQuery(id+"F0.wireOp",EDGE,"E9.3.8.23"),sQuery(id+"F0.wireOp",EDGE,"E9.6.8.23"),sQuery(id+"F0.wireOp",EDGE,"E9.9.8.23"),sQuery(id+"F0.wireOp",EDGE,"E9.0.8.24"),sQuery(id+"F0.wireOp",EDGE,"E9.3.8.24"),sQuery(id+"F0.wireOp",EDGE,"E9.6.8.24"),sQuery(id+"F0.wireOp",EDGE,"E9.9.8.24"),sQuery(id+"F0.wireOp",EDGE,"E9.0.8.25"),sQuery(id+"F0.wireOp",EDGE,"E9.3.8.25"),sQuery(id+"F0.wireOp",EDGE,"E9.6.8.25"),sQuery(id+"F0.wireOp",EDGE,"E9.9.8.25"),sQuery(id+"F0.wireOp",EDGE,"E9.0.8.26"),sQuery(id+"F0.wireOp",EDGE,"E9.3.8.26"),sQuery(id+"F0.wireOp",EDGE,"E9.6.8.26"),sQuery(id+"F0.wireOp",EDGE,"E9.9.8.26"),sQuery(id+"F0.wireOp",EDGE,"E9.0.8.27"),sQuery(id+"F0.wireOp",EDGE,"E9.3.8.27"),sQuery(id+"F0.wireOp",EDGE,"E9.6.8.27"),sQuery(id+"F0.wireOp",EDGE,"E9.9.8.27"),sQuery(id+"F0.wireOp",EDGE,"E9.0.8.28"),sQuery(id+"F0.wireOp",EDGE,"E9.3.8.28"),sQuery(id+"F0.wireOp",EDGE,"E9.6.8.28"),sQuery(id+"F0.wireOp",EDGE,"E9.9.8.28"),sQuery(id+"F0.wireOp",EDGE,"E9.0.8.29"),sQuery(id+"F0.wireOp",EDGE,"E9.3.8.29"),sQuery(id+"F0.wireOp",EDGE,"E9.6.8.29"),sQuery(id+"F0.wireOp",EDGE,"E9.9.8.29"),sQuery(id+"F0.wireOp",EDGE,"E9.0.8.30"),sQuery(id+"F0.wireOp",EDGE,"E9.3.8.30"),sQuery(id+"F0.wireOp",EDGE,"E9.6.8.30"),sQuery(id+"F0.wireOp",EDGE,"E9.9.8.30"),sQuery(id+"F0.wireOp",EDGE,"E9.0.8.31"),sQuery(id+"F0.wireOp",EDGE,"E9.3.8.31"),sQuery(id+"F0.wireOp",EDGE,"E9.6.8.31"),sQuery(id+"F0.wireOp",EDGE,"E9.9.8.31"),sQuery(id+"F0.wireOp",EDGE,"E9.0.9.0"),sQuery(id+"F0.wireOp",EDGE,"E9.3.9.0"),sQuery(id+"F0.wireOp",EDGE,"E9.6.9.0"),sQuery(id+"F0.wireOp",EDGE,"E9.9.9.0"),sQuery(id+"F0.wireOp",EDGE,"E9.0.9.1"),sQuery(id+"F0.wireOp",EDGE,"E9.3.9.1"),sQuery(id+"F0.wireOp",EDGE,"E9.6.9.1"),sQuery(id+"F0.wireOp",EDGE,"E9.9.9.1"),sQuery(id+"F0.wireOp",EDGE,"E9.0.9.2"),sQuery(id+"F0.wireOp",EDGE,"E9.3.9.2"),sQuery(id+"F0.wireOp",EDGE,"E9.6.9.2"),sQuery(id+"F0.wireOp",EDGE,"E9.9.9.2"),sQuery(id+"F0.wireOp",EDGE,"E9.0.9.3"),sQuery(id+"F0.wireOp",EDGE,"E9.3.9.3"),sQuery(id+"F0.wireOp",EDGE,"E9.6.9.3"),sQuery(id+"F0.wireOp",EDGE,"E9.9.9.3"),sQuery(id+"F0.wireOp",EDGE,"E9.0.9.4"),sQuery(id+"F0.wireOp",EDGE,"E9.3.9.4"),sQuery(id+"F0.wireOp",EDGE,"E9.6.9.4"),sQuery(id+"F0.wireOp",EDGE,"E9.9.9.4"),sQuery(id+"F0.wireOp",EDGE,"E9.0.9.5"),sQuery(id+"F0.wireOp",EDGE,"E9.3.9.5"),sQuery(id+"F0.wireOp",EDGE,"E9.6.9.5"),sQuery(id+"F0.wireOp",EDGE,"E9.9.9.5"),sQuery(id+"F0.wireOp",EDGE,"E9.0.9.6"),sQuery(id+"F0.wireOp",EDGE,"E9.3.9.6"),sQuery(id+"F0.wireOp",EDGE,"E9.6.9.6"),sQuery(id+"F0.wireOp",EDGE,"E9.9.9.6"),sQuery(id+"F0.wireOp",EDGE,"E9.0.9.7"),sQuery(id+"F0.wireOp",EDGE,"E9.3.9.7"),sQuery(id+"F0.wireOp",EDGE,"E9.6.9.7"),sQuery(id+"F0.wireOp",EDGE,"E9.9.9.7"),sQuery(id+"F0.wireOp",EDGE,"E9.0.9.8"),sQuery(id+"F0.wireOp",EDGE,"E9.3.9.8"),sQuery(id+"F0.wireOp",EDGE,"E9.6.9.8"),sQuery(id+"F0.wireOp",EDGE,"E9.9.9.8"),sQuery(id+"F0.wireOp",EDGE,"E9.0.9.9"),sQuery(id+"F0.wireOp",EDGE,"E9.3.9.9"),sQuery(id+"F0.wireOp",EDGE,"E9.6.9.9"),sQuery(id+"F0.wireOp",EDGE,"E9.9.9.9"),sQuery(id+"F0.wireOp",EDGE,"E9.0.9.10"),sQuery(id+"F0.wireOp",EDGE,"E9.3.9.10"),sQuery(id+"F0.wireOp",EDGE,"E9.6.9.10"),sQuery(id+"F0.wireOp",EDGE,"E9.9.9.10"),sQuery(id+"F0.wireOp",EDGE,"E9.0.9.11"),sQuery(id+"F0.wireOp",EDGE,"E9.3.9.11"),sQuery(id+"F0.wireOp",EDGE,"E9.6.9.11"),sQuery(id+"F0.wireOp",EDGE,"E9.9.9.11"),sQuery(id+"F0.wireOp",EDGE,"E9.0.9.12"),sQuery(id+"F0.wireOp",EDGE,"E9.3.9.12"),sQuery(id+"F0.wireOp",EDGE,"E9.6.9.12"),sQuery(id+"F0.wireOp",EDGE,"E9.9.9.12"),sQuery(id+"F0.wireOp",EDGE,"E9.0.9.13"),sQuery(id+"F0.wireOp",EDGE,"E9.3.9.13"),sQuery(id+"F0.wireOp",EDGE,"E9.6.9.13"),sQuery(id+"F0.wireOp",EDGE,"E9.9.9.13"),sQuery(id+"F0.wireOp",EDGE,"E9.0.9.14"),sQuery(id+"F0.wireOp",EDGE,"E9.3.9.14"),sQuery(id+"F0.wireOp",EDGE,"E9.6.9.14"),sQuery(id+"F0.wireOp",EDGE,"E9.9.9.14"),sQuery(id+"F0.wireOp",EDGE,"E9.0.9.15"),sQuery(id+"F0.wireOp",EDGE,"E9.3.9.15"),sQuery(id+"F0.wireOp",EDGE,"E9.6.9.15"),sQuery(id+"F0.wireOp",EDGE,"E9.9.9.15"),sQuery(id+"F0.wireOp",EDGE,"E9.0.9.16"),sQuery(id+"F0.wireOp",EDGE,"E9.3.9.16"),sQuery(id+"F0.wireOp",EDGE,"E9.6.9.16"),sQuery(id+"F0.wireOp",EDGE,"E9.9.9.16"),sQuery(id+"F0.wireOp",EDGE,"E9.0.9.17"),sQuery(id+"F0.wireOp",EDGE,"E9.3.9.17"),sQuery(id+"F0.wireOp",EDGE,"E9.6.9.17"),sQuery(id+"F0.wireOp",EDGE,"E9.9.9.17"),sQuery(id+"F0.wireOp",EDGE,"E9.0.9.18"),sQuery(id+"F0.wireOp",EDGE,"E9.3.9.18"),sQuery(id+"F0.wireOp",EDGE,"E9.6.9.18"),sQuery(id+"F0.wireOp",EDGE,"E9.9.9.18"),sQuery(id+"F0.wireOp",EDGE,"E9.0.9.19"),sQuery(id+"F0.wireOp",EDGE,"E9.3.9.19"),sQuery(id+"F0.wireOp",EDGE,"E9.6.9.19"),sQuery(id+"F0.wireOp",EDGE,"E9.9.9.19"),sQuery(id+"F0.wireOp",EDGE,"E9.0.9.20"),sQuery(id+"F0.wireOp",EDGE,"E9.3.9.20"),sQuery(id+"F0.wireOp",EDGE,"E9.6.9.20"),sQuery(id+"F0.wireOp",EDGE,"E9.9.9.20"),sQuery(id+"F0.wireOp",EDGE,"E9.0.9.21"),sQuery(id+"F0.wireOp",EDGE,"E9.3.9.21"),sQuery(id+"F0.wireOp",EDGE,"E9.6.9.21"),sQuery(id+"F0.wireOp",EDGE,"E9.9.9.21"),sQuery(id+"F0.wireOp",EDGE,"E9.0.9.22"),sQuery(id+"F0.wireOp",EDGE,"E9.3.9.22"),sQuery(id+"F0.wireOp",EDGE,"E9.6.9.22"),sQuery(id+"F0.wireOp",EDGE,"E9.9.9.22"),sQuery(id+"F0.wireOp",EDGE,"E9.0.9.23"),sQuery(id+"F0.wireOp",EDGE,"E9.3.9.23"),sQuery(id+"F0.wireOp",EDGE,"E9.6.9.23"),sQuery(id+"F0.wireOp",EDGE,"E9.9.9.23"),sQuery(id+"F0.wireOp",EDGE,"E9.0.9.24"),sQuery(id+"F0.wireOp",EDGE,"E9.3.9.24"),sQuery(id+"F0.wireOp",EDGE,"E9.6.9.24"),sQuery(id+"F0.wireOp",EDGE,"E9.9.9.24"),sQuery(id+"F0.wireOp",EDGE,"E9.0.9.25"),sQuery(id+"F0.wireOp",EDGE,"E9.3.9.25"),sQuery(id+"F0.wireOp",EDGE,"E9.6.9.25"),sQuery(id+"F0.wireOp",EDGE,"E9.9.9.25"),sQuery(id+"F0.wireOp",EDGE,"E9.0.9.26"),sQuery(id+"F0.wireOp",EDGE,"E9.3.9.26"),sQuery(id+"F0.wireOp",EDGE,"E9.6.9.26"),sQuery(id+"F0.wireOp",EDGE,"E9.9.9.26"),sQuery(id+"F0.wireOp",EDGE,"E9.0.9.27"),sQuery(id+"F0.wireOp",EDGE,"E9.3.9.27"),sQuery(id+"F0.wireOp",EDGE,"E9.6.9.27"),sQuery(id+"F0.wireOp",EDGE,"E9.9.9.27"),sQuery(id+"F0.wireOp",EDGE,"E9.0.9.28"),sQuery(id+"F0.wireOp",EDGE,"E9.3.9.28"),sQuery(id+"F0.wireOp",EDGE,"E9.6.9.28"),sQuery(id+"F0.wireOp",EDGE,"E9.9.9.28"),sQuery(id+"F0.wireOp",EDGE,"E9.0.9.29"),sQuery(id+"F0.wireOp",EDGE,"E9.3.9.29"),sQuery(id+"F0.wireOp",EDGE,"E9.6.9.29"),sQuery(id+"F0.wireOp",EDGE,"E9.9.9.29"),sQuery(id+"F0.wireOp",EDGE,"E9.0.9.30"),sQuery(id+"F0.wireOp",EDGE,"E9.3.9.30"),sQuery(id+"F0.wireOp",EDGE,"E9.6.9.30"),sQuery(id+"F0.wireOp",EDGE,"E9.9.9.30"),sQuery(id+"F0.wireOp",EDGE,"E9.0.9.31"),sQuery(id+"F0.wireOp",EDGE,"E9.3.9.31"),sQuery(id+"F0.wireOp",EDGE,"E9.6.9.31"),sQuery(id+"F0.wireOp",EDGE,"E9.9.9.31"),sQuery(id+"F0.wireOp",EDGE,"E9.0.10.0"),sQuery(id+"F0.wireOp",EDGE,"E9.3.10.0"),sQuery(id+"F0.wireOp",EDGE,"E9.6.10.0"),sQuery(id+"F0.wireOp",EDGE,"E9.9.10.0"),sQuery(id+"F0.wireOp",EDGE,"E9.0.10.1"),sQuery(id+"F0.wireOp",EDGE,"E9.3.10.1"),sQuery(id+"F0.wireOp",EDGE,"E9.6.10.1"),sQuery(id+"F0.wireOp",EDGE,"E9.9.10.1"),sQuery(id+"F0.wireOp",EDGE,"E9.0.10.2"),sQuery(id+"F0.wireOp",EDGE,"E9.3.10.2"),sQuery(id+"F0.wireOp",EDGE,"E9.6.10.2"),sQuery(id+"F0.wireOp",EDGE,"E9.9.10.2"),sQuery(id+"F0.wireOp",EDGE,"E9.0.10.3"),sQuery(id+"F0.wireOp",EDGE,"E9.3.10.3"),sQuery(id+"F0.wireOp",EDGE,"E9.6.10.3"),sQuery(id+"F0.wireOp",EDGE,"E9.9.10.3"),sQuery(id+"F0.wireOp",EDGE,"E9.0.10.4"),sQuery(id+"F0.wireOp",EDGE,"E9.3.10.4"),sQuery(id+"F0.wireOp",EDGE,"E9.6.10.4"),sQuery(id+"F0.wireOp",EDGE,"E9.9.10.4"),sQuery(id+"F0.wireOp",EDGE,"E9.0.10.5"),sQuery(id+"F0.wireOp",EDGE,"E9.3.10.5"),sQuery(id+"F0.wireOp",EDGE,"E9.6.10.5"),sQuery(id+"F0.wireOp",EDGE,"E9.9.10.5"),sQuery(id+"F0.wireOp",EDGE,"E9.0.10.6"),sQuery(id+"F0.wireOp",EDGE,"E9.3.10.6"),sQuery(id+"F0.wireOp",EDGE,"E9.6.10.6"),sQuery(id+"F0.wireOp",EDGE,"E9.9.10.6"),sQuery(id+"F0.wireOp",EDGE,"E9.0.10.7"),sQuery(id+"F0.wireOp",EDGE,"E9.3.10.7"),sQuery(id+"F0.wireOp",EDGE,"E9.6.10.7"),sQuery(id+"F0.wireOp",EDGE,"E9.9.10.7"),sQuery(id+"F0.wireOp",EDGE,"E9.0.10.8"),sQuery(id+"F0.wireOp",EDGE,"E9.3.10.8"),sQuery(id+"F0.wireOp",EDGE,"E9.6.10.8"),sQuery(id+"F0.wireOp",EDGE,"E9.9.10.8"),sQuery(id+"F0.wireOp",EDGE,"E9.0.10.9"),sQuery(id+"F0.wireOp",EDGE,"E9.3.10.9"),sQuery(id+"F0.wireOp",EDGE,"E9.6.10.9"),sQuery(id+"F0.wireOp",EDGE,"E9.9.10.9"),sQuery(id+"F0.wireOp",EDGE,"E9.0.10.10"),sQuery(id+"F0.wireOp",EDGE,"E9.3.10.10"),sQuery(id+"F0.wireOp",EDGE,"E9.6.10.10"),sQuery(id+"F0.wireOp",EDGE,"E9.9.10.10"),sQuery(id+"F0.wireOp",EDGE,"E9.0.10.11"),sQuery(id+"F0.wireOp",EDGE,"E9.3.10.11"),sQuery(id+"F0.wireOp",EDGE,"E9.6.10.11"),sQuery(id+"F0.wireOp",EDGE,"E9.9.10.11"),sQuery(id+"F0.wireOp",EDGE,"E9.0.10.12"),sQuery(id+"F0.wireOp",EDGE,"E9.3.10.12"),sQuery(id+"F0.wireOp",EDGE,"E9.6.10.12"),sQuery(id+"F0.wireOp",EDGE,"E9.9.10.12"),sQuery(id+"F0.wireOp",EDGE,"E9.0.10.13"),sQuery(id+"F0.wireOp",EDGE,"E9.3.10.13"),sQuery(id+"F0.wireOp",EDGE,"E9.6.10.13"),sQuery(id+"F0.wireOp",EDGE,"E9.9.10.13"),sQuery(id+"F0.wireOp",EDGE,"E9.0.10.14"),sQuery(id+"F0.wireOp",EDGE,"E9.3.10.14"),sQuery(id+"F0.wireOp",EDGE,"E9.6.10.14"),sQuery(id+"F0.wireOp",EDGE,"E9.9.10.14"),sQuery(id+"F0.wireOp",EDGE,"E9.0.10.15"),sQuery(id+"F0.wireOp",EDGE,"E9.3.10.15"),sQuery(id+"F0.wireOp",EDGE,"E9.6.10.15"),sQuery(id+"F0.wireOp",EDGE,"E9.9.10.15"),sQuery(id+"F0.wireOp",EDGE,"E9.0.10.16"),sQuery(id+"F0.wireOp",EDGE,"E9.3.10.16"),sQuery(id+"F0.wireOp",EDGE,"E9.6.10.16"),sQuery(id+"F0.wireOp",EDGE,"E9.9.10.16"),sQuery(id+"F0.wireOp",EDGE,"E9.0.10.17"),sQuery(id+"F0.wireOp",EDGE,"E9.3.10.17"),sQuery(id+"F0.wireOp",EDGE,"E9.6.10.17"),sQuery(id+"F0.wireOp",EDGE,"E9.9.10.17"),sQuery(id+"F0.wireOp",EDGE,"E9.0.10.18"),sQuery(id+"F0.wireOp",EDGE,"E9.3.10.18"),sQuery(id+"F0.wireOp",EDGE,"E9.6.10.18"),sQuery(id+"F0.wireOp",EDGE,"E9.9.10.18"),sQuery(id+"F0.wireOp",EDGE,"E9.0.10.19"),sQuery(id+"F0.wireOp",EDGE,"E9.3.10.19"),sQuery(id+"F0.wireOp",EDGE,"E9.6.10.19"),sQuery(id+"F0.wireOp",EDGE,"E9.9.10.19"),sQuery(id+"F0.wireOp",EDGE,"E9.0.10.20"),sQuery(id+"F0.wireOp",EDGE,"E9.3.10.20"),sQuery(id+"F0.wireOp",EDGE,"E9.6.10.20"),sQuery(id+"F0.wireOp",EDGE,"E9.9.10.20"),sQuery(id+"F0.wireOp",EDGE,"E9.0.10.21"),sQuery(id+"F0.wireOp",EDGE,"E9.3.10.21"),sQuery(id+"F0.wireOp",EDGE,"E9.6.10.21"),sQuery(id+"F0.wireOp",EDGE,"E9.9.10.21"),sQuery(id+"F0.wireOp",EDGE,"E9.0.10.22"),sQuery(id+"F0.wireOp",EDGE,"E9.3.10.22"),sQuery(id+"F0.wireOp",EDGE,"E9.6.10.22"),sQuery(id+"F0.wireOp",EDGE,"E9.9.10.22"),sQuery(id+"F0.wireOp",EDGE,"E9.0.10.23"),sQuery(id+"F0.wireOp",EDGE,"E9.3.10.23"),sQuery(id+"F0.wireOp",EDGE,"E9.6.10.23"),sQuery(id+"F0.wireOp",EDGE,"E9.9.10.23"),sQuery(id+"F0.wireOp",EDGE,"E9.0.10.24"),sQuery(id+"F0.wireOp",EDGE,"E9.3.10.24"),sQuery(id+"F0.wireOp",EDGE,"E9.6.10.24"),sQuery(id+"F0.wireOp",EDGE,"E9.9.10.24"),sQuery(id+"F0.wireOp",EDGE,"E9.0.10.25"),sQuery(id+"F0.wireOp",EDGE,"E9.3.10.25"),sQuery(id+"F0.wireOp",EDGE,"E9.6.10.25"),sQuery(id+"F0.wireOp",EDGE,"E9.9.10.25"),sQuery(id+"F0.wireOp",EDGE,"E9.0.10.26"),sQuery(id+"F0.wireOp",EDGE,"E9.3.10.26"),sQuery(id+"F0.wireOp",EDGE,"E9.6.10.26"),sQuery(id+"F0.wireOp",EDGE,"E9.9.10.26"),sQuery(id+"F0.wireOp",EDGE,"E9.0.10.27"),sQuery(id+"F0.wireOp",EDGE,"E9.3.10.27"),sQuery(id+"F0.wireOp",EDGE,"E9.6.10.27"),sQuery(id+"F0.wireOp",EDGE,"E9.9.10.27"),sQuery(id+"F0.wireOp",EDGE,"E9.0.10.28"),sQuery(id+"F0.wireOp",EDGE,"E9.3.10.28"),sQuery(id+"F0.wireOp",EDGE,"E9.6.10.28"),sQuery(id+"F0.wireOp",EDGE,"E9.9.10.28"),sQuery(id+"F0.wireOp",EDGE,"E9.0.10.29"),sQuery(id+"F0.wireOp",EDGE,"E9.3.10.29"),sQuery(id+"F0.wireOp",EDGE,"E9.6.10.29"),sQuery(id+"F0.wireOp",EDGE,"E9.9.10.29"),sQuery(id+"F0.wireOp",EDGE,"E9.0.10.30"),sQuery(id+"F0.wireOp",EDGE,"E9.3.10.30"),sQuery(id+"F0.wireOp",EDGE,"E9.6.10.30"),sQuery(id+"F0.wireOp",EDGE,"E9.9.10.30"),sQuery(id+"F0.wireOp",EDGE,"E9.0.10.31"),sQuery(id+"F0.wireOp",EDGE,"E9.3.10.31"),sQuery(id+"F0.wireOp",EDGE,"E9.6.10.31"),sQuery(id+"F0.wireOp",EDGE,"E9.9.10.31"),sQuery(id+"F0.wireOp",EDGE,"E9.0.11.0"),sQuery(id+"F0.wireOp",EDGE,"E9.3.11.0"),sQuery(id+"F0.wireOp",EDGE,"E9.6.11.0"),sQuery(id+"F0.wireOp",EDGE,"E9.9.11.0"),sQuery(id+"F0.wireOp",EDGE,"E9.0.11.1"),sQuery(id+"F0.wireOp",EDGE,"E9.3.11.1"),sQuery(id+"F0.wireOp",EDGE,"E9.6.11.1"),sQuery(id+"F0.wireOp",EDGE,"E9.9.11.1"),sQuery(id+"F0.wireOp",EDGE,"E9.0.11.2"),sQuery(id+"F0.wireOp",EDGE,"E9.3.11.2"),sQuery(id+"F0.wireOp",EDGE,"E9.6.11.2"),sQuery(id+"F0.wireOp",EDGE,"E9.9.11.2"),sQuery(id+"F0.wireOp",EDGE,"E9.0.11.3"),sQuery(id+"F0.wireOp",EDGE,"E9.3.11.3"),sQuery(id+"F0.wireOp",EDGE,"E9.6.11.3"),sQuery(id+"F0.wireOp",EDGE,"E9.9.11.3"),sQuery(id+"F0.wireOp",EDGE,"E9.0.11.4"),sQuery(id+"F0.wireOp",EDGE,"E9.3.11.4"),sQuery(id+"F0.wireOp",EDGE,"E9.6.11.4"),sQuery(id+"F0.wireOp",EDGE,"E9.9.11.4"),sQuery(id+"F0.wireOp",EDGE,"E9.0.11.5"),sQuery(id+"F0.wireOp",EDGE,"E9.3.11.5"),sQuery(id+"F0.wireOp",EDGE,"E9.6.11.5"),sQuery(id+"F0.wireOp",EDGE,"E9.9.11.5"),sQuery(id+"F0.wireOp",EDGE,"E9.0.11.6"),sQuery(id+"F0.wireOp",EDGE,"E9.3.11.6"),sQuery(id+"F0.wireOp",EDGE,"E9.6.11.6"),sQuery(id+"F0.wireOp",EDGE,"E9.9.11.6"),sQuery(id+"F0.wireOp",EDGE,"E9.0.11.7"),sQuery(id+"F0.wireOp",EDGE,"E9.3.11.7"),sQuery(id+"F0.wireOp",EDGE,"E9.6.11.7"),sQuery(id+"F0.wireOp",EDGE,"E9.9.11.7"),sQuery(id+"F0.wireOp",EDGE,"E9.0.11.8"),sQuery(id+"F0.wireOp",EDGE,"E9.3.11.8"),sQuery(id+"F0.wireOp",EDGE,"E9.6.11.8"),sQuery(id+"F0.wireOp",EDGE,"E9.9.11.8"),sQuery(id+"F0.wireOp",EDGE,"E9.0.11.9"),sQuery(id+"F0.wireOp",EDGE,"E9.3.11.9"),sQuery(id+"F0.wireOp",EDGE,"E9.6.11.9"),sQuery(id+"F0.wireOp",EDGE,"E9.9.11.9"),sQuery(id+"F0.wireOp",EDGE,"E9.0.11.10"),sQuery(id+"F0.wireOp",EDGE,"E9.3.11.10"),sQuery(id+"F0.wireOp",EDGE,"E9.6.11.10"),sQuery(id+"F0.wireOp",EDGE,"E9.9.11.10"),sQuery(id+"F0.wireOp",EDGE,"E9.0.11.11"),sQuery(id+"F0.wireOp",EDGE,"E9.3.11.11"),sQuery(id+"F0.wireOp",EDGE,"E9.6.11.11"),sQuery(id+"F0.wireOp",EDGE,"E9.9.11.11"),sQuery(id+"F0.wireOp",EDGE,"E9.0.11.12"),sQuery(id+"F0.wireOp",EDGE,"E9.3.11.12"),sQuery(id+"F0.wireOp",EDGE,"E9.6.11.12"),sQuery(id+"F0.wireOp",EDGE,"E9.9.11.12"),sQuery(id+"F0.wireOp",EDGE,"E9.0.11.13"),sQuery(id+"F0.wireOp",EDGE,"E9.3.11.13"),sQuery(id+"F0.wireOp",EDGE,"E9.6.11.13"),sQuery(id+"F0.wireOp",EDGE,"E9.9.11.13"),sQuery(id+"F0.wireOp",EDGE,"E9.0.11.14"),sQuery(id+"F0.wireOp",EDGE,"E9.3.11.14"),sQuery(id+"F0.wireOp",EDGE,"E9.6.11.14"),sQuery(id+"F0.wireOp",EDGE,"E9.9.11.14"),sQuery(id+"F0.wireOp",EDGE,"E9.0.11.15"),sQuery(id+"F0.wireOp",EDGE,"E9.3.11.15"),sQuery(id+"F0.wireOp",EDGE,"E9.6.11.15"),sQuery(id+"F0.wireOp",EDGE,"E9.9.11.15"),sQuery(id+"F0.wireOp",EDGE,"E9.0.11.16"),sQuery(id+"F0.wireOp",EDGE,"E9.3.11.16"),sQuery(id+"F0.wireOp",EDGE,"E9.6.11.16"),sQuery(id+"F0.wireOp",EDGE,"E9.9.11.16"),sQuery(id+"F0.wireOp",EDGE,"E9.0.11.17"),sQuery(id+"F0.wireOp",EDGE,"E9.3.11.17"),sQuery(id+"F0.wireOp",EDGE,"E9.6.11.17"),sQuery(id+"F0.wireOp",EDGE,"E9.9.11.17"),sQuery(id+"F0.wireOp",EDGE,"E9.0.11.18"),sQuery(id+"F0.wireOp",EDGE,"E9.3.11.18"),sQuery(id+"F0.wireOp",EDGE,"E9.6.11.18"),sQuery(id+"F0.wireOp",EDGE,"E9.9.11.18"),sQuery(id+"F0.wireOp",EDGE,"E9.0.11.19"),sQuery(id+"F0.wireOp",EDGE,"E9.3.11.19"),sQuery(id+"F0.wireOp",EDGE,"E9.6.11.19"),sQuery(id+"F0.wireOp",EDGE,"E9.9.11.19"),sQuery(id+"F0.wireOp",EDGE,"E9.0.11.20"),sQuery(id+"F0.wireOp",EDGE,"E9.3.11.20"),sQuery(id+"F0.wireOp",EDGE,"E9.6.11.20"),sQuery(id+"F0.wireOp",EDGE,"E9.9.11.20"),sQuery(id+"F0.wireOp",EDGE,"E9.0.11.21"),sQuery(id+"F0.wireOp",EDGE,"E9.3.11.21"),sQuery(id+"F0.wireOp",EDGE,"E9.6.11.21"),sQuery(id+"F0.wireOp",EDGE,"E9.9.11.21"),sQuery(id+"F0.wireOp",EDGE,"E9.0.11.22"),sQuery(id+"F0.wireOp",EDGE,"E9.3.11.22"),sQuery(id+"F0.wireOp",EDGE,"E9.6.11.22"),sQuery(id+"F0.wireOp",EDGE,"E9.9.11.22"),sQuery(id+"F0.wireOp",EDGE,"E9.0.11.23"),sQuery(id+"F0.wireOp",EDGE,"E9.3.11.23"),sQuery(id+"F0.wireOp",EDGE,"E9.6.11.23"),sQuery(id+"F0.wireOp",EDGE,"E9.9.11.23"),sQuery(id+"F0.wireOp",EDGE,"E9.0.11.24"),sQuery(id+"F0.wireOp",EDGE,"E9.3.11.24"),sQuery(id+"F0.wireOp",EDGE,"E9.6.11.24"),sQuery(id+"F0.wireOp",EDGE,"E9.9.11.24"),sQuery(id+"F0.wireOp",EDGE,"E9.0.11.25"),sQuery(id+"F0.wireOp",EDGE,"E9.3.11.25"),sQuery(id+"F0.wireOp",EDGE,"E9.6.11.25"),sQuery(id+"F0.wireOp",EDGE,"E9.9.11.25"),sQuery(id+"F0.wireOp",EDGE,"E9.0.11.26"),sQuery(id+"F0.wireOp",EDGE,"E9.3.11.26"),sQuery(id+"F0.wireOp",EDGE,"E9.6.11.26"),sQuery(id+"F0.wireOp",EDGE,"E9.9.11.26"),sQuery(id+"F0.wireOp",EDGE,"E9.0.11.27"),sQuery(id+"F0.wireOp",EDGE,"E9.3.11.27"),sQuery(id+"F0.wireOp",EDGE,"E9.6.11.27"),sQuery(id+"F0.wireOp",EDGE,"E9.9.11.27"),sQuery(id+"F0.wireOp",EDGE,"E9.0.11.28"),sQuery(id+"F0.wireOp",EDGE,"E9.3.11.28"),sQuery(id+"F0.wireOp",EDGE,"E9.6.11.28"),sQuery(id+"F0.wireOp",EDGE,"E9.9.11.28"),sQuery(id+"F0.wireOp",EDGE,"E9.0.11.29"),sQuery(id+"F0.wireOp",EDGE,"E9.3.11.29"),sQuery(id+"F0.wireOp",EDGE,"E9.6.11.29"),sQuery(id+"F0.wireOp",EDGE,"E9.9.11.29"),sQuery(id+"F0.wireOp",EDGE,"E9.0.11.30"),sQuery(id+"F0.wireOp",EDGE,"E9.3.11.30"),sQuery(id+"F0.wireOp",EDGE,"E9.6.11.30"),sQuery(id+"F0.wireOp",EDGE,"E9.9.11.30"),sQuery(id+"F0.wireOp",EDGE,"E9.0.11.31"),sQuery(id+"F0.wireOp",EDGE,"E9.3.11.31"),sQuery(id+"F0.wireOp",EDGE,"E9.6.11.31"),sQuery(id+"F0.wireOp",EDGE,"E9.9.11.31"),sQuery(id+"F0.wireOp",EDGE,"E9.0.12.0"),sQuery(id+"F0.wireOp",EDGE,"E9.3.12.0"),sQuery(id+"F0.wireOp",EDGE,"E9.6.12.0"),sQuery(id+"F0.wireOp",EDGE,"E9.9.12.0"),sQuery(id+"F0.wireOp",EDGE,"E9.0.12.1"),sQuery(id+"F0.wireOp",EDGE,"E9.3.12.1"),sQuery(id+"F0.wireOp",EDGE,"E9.6.12.1"),sQuery(id+"F0.wireOp",EDGE,"E9.9.12.1"),sQuery(id+"F0.wireOp",EDGE,"E9.0.12.2"),sQuery(id+"F0.wireOp",EDGE,"E9.3.12.2"),sQuery(id+"F0.wireOp",EDGE,"E9.6.12.2"),sQuery(id+"F0.wireOp",EDGE,"E9.9.12.2"),sQuery(id+"F0.wireOp",EDGE,"E9.0.12.3"),sQuery(id+"F0.wireOp",EDGE,"E9.3.12.3"),sQuery(id+"F0.wireOp",EDGE,"E9.6.12.3"),sQuery(id+"F0.wireOp",EDGE,"E9.9.12.3"),sQuery(id+"F0.wireOp",EDGE,"E9.0.12.4"),sQuery(id+"F0.wireOp",EDGE,"E9.3.12.4"),sQuery(id+"F0.wireOp",EDGE,"E9.6.12.4"),sQuery(id+"F0.wireOp",EDGE,"E9.9.12.4"),sQuery(id+"F0.wireOp",EDGE,"E9.0.12.5"),sQuery(id+"F0.wireOp",EDGE,"E9.3.12.5"),sQuery(id+"F0.wireOp",EDGE,"E9.6.12.5"),sQuery(id+"F0.wireOp",EDGE,"E9.9.12.5"),sQuery(id+"F0.wireOp",EDGE,"E9.0.12.6"),sQuery(id+"F0.wireOp",EDGE,"E9.3.12.6"),sQuery(id+"F0.wireOp",EDGE,"E9.6.12.6"),sQuery(id+"F0.wireOp",EDGE,"E9.9.12.6"),sQuery(id+"F0.wireOp",EDGE,"E9.0.12.7"),sQuery(id+"F0.wireOp",EDGE,"E9.3.12.7"),sQuery(id+"F0.wireOp",EDGE,"E9.6.12.7"),sQuery(id+"F0.wireOp",EDGE,"E9.9.12.7"),sQuery(id+"F0.wireOp",EDGE,"E9.0.12.8"),sQuery(id+"F0.wireOp",EDGE,"E9.3.12.8"),sQuery(id+"F0.wireOp",EDGE,"E9.6.12.8"),sQuery(id+"F0.wireOp",EDGE,"E9.9.12.8"),sQuery(id+"F0.wireOp",EDGE,"E9.0.12.9"),sQuery(id+"F0.wireOp",EDGE,"E9.3.12.9"),sQuery(id+"F0.wireOp",EDGE,"E9.6.12.9"),sQuery(id+"F0.wireOp",EDGE,"E9.9.12.9"),sQuery(id+"F0.wireOp",EDGE,"E9.0.12.10"),sQuery(id+"F0.wireOp",EDGE,"E9.3.12.10"),sQuery(id+"F0.wireOp",EDGE,"E9.6.12.10"),sQuery(id+"F0.wireOp",EDGE,"E9.9.12.10"),sQuery(id+"F0.wireOp",EDGE,"E9.0.12.11"),sQuery(id+"F0.wireOp",EDGE,"E9.3.12.11"),sQuery(id+"F0.wireOp",EDGE,"E9.6.12.11"),sQuery(id+"F0.wireOp",EDGE,"E9.9.12.11"),sQuery(id+"F0.wireOp",EDGE,"E9.0.12.12"),sQuery(id+"F0.wireOp",EDGE,"E9.3.12.12"),sQuery(id+"F0.wireOp",EDGE,"E9.6.12.12"),sQuery(id+"F0.wireOp",EDGE,"E9.9.12.12"),sQuery(id+"F0.wireOp",EDGE,"E9.0.12.13"),sQuery(id+"F0.wireOp",EDGE,"E9.3.12.13"),sQuery(id+"F0.wireOp",EDGE,"E9.6.12.13"),sQuery(id+"F0.wireOp",EDGE,"E9.9.12.13"),sQuery(id+"F0.wireOp",EDGE,"E9.0.12.14"),sQuery(id+"F0.wireOp",EDGE,"E9.3.12.14"),sQuery(id+"F0.wireOp",EDGE,"E9.6.12.14"),sQuery(id+"F0.wireOp",EDGE,"E9.9.12.14"),sQuery(id+"F0.wireOp",EDGE,"E9.0.12.15"),sQuery(id+"F0.wireOp",EDGE,"E9.3.12.15"),sQuery(id+"F0.wireOp",EDGE,"E9.6.12.15"),sQuery(id+"F0.wireOp",EDGE,"E9.9.12.15"),sQuery(id+"F0.wireOp",EDGE,"E9.0.12.16"),sQuery(id+"F0.wireOp",EDGE,"E9.3.12.16"),sQuery(id+"F0.wireOp",EDGE,"E9.6.12.16"),sQuery(id+"F0.wireOp",EDGE,"E9.9.12.16"),sQuery(id+"F0.wireOp",EDGE,"E9.0.12.17"),sQuery(id+"F0.wireOp",EDGE,"E9.3.12.17"),sQuery(id+"F0.wireOp",EDGE,"E9.6.12.17"),sQuery(id+"F0.wireOp",EDGE,"E9.9.12.17"),sQuery(id+"F0.wireOp",EDGE,"E9.0.12.18"),sQuery(id+"F0.wireOp",EDGE,"E9.3.12.18"),sQuery(id+"F0.wireOp",EDGE,"E9.6.12.18"),sQuery(id+"F0.wireOp",EDGE,"E9.9.12.18"),sQuery(id+"F0.wireOp",EDGE,"E9.0.12.19"),sQuery(id+"F0.wireOp",EDGE,"E9.3.12.19"),sQuery(id+"F0.wireOp",EDGE,"E9.6.12.19"),sQuery(id+"F0.wireOp",EDGE,"E9.9.12.19"),sQuery(id+"F0.wireOp",EDGE,"E9.0.12.20"),sQuery(id+"F0.wireOp",EDGE,"E9.3.12.20"),sQuery(id+"F0.wireOp",EDGE,"E9.6.12.20"),sQuery(id+"F0.wireOp",EDGE,"E9.9.12.20"),sQuery(id+"F0.wireOp",EDGE,"E9.0.12.21"),sQuery(id+"F0.wireOp",EDGE,"E9.3.12.21"),sQuery(id+"F0.wireOp",EDGE,"E9.6.12.21"),sQuery(id+"F0.wireOp",EDGE,"E9.9.12.21"),sQuery(id+"F0.wireOp",EDGE,"E9.0.12.22"),sQuery(id+"F0.wireOp",EDGE,"E9.3.12.22"),sQuery(id+"F0.wireOp",EDGE,"E9.6.12.22"),sQuery(id+"F0.wireOp",EDGE,"E9.9.12.22"),sQuery(id+"F0.wireOp",EDGE,"E9.0.12.23"),sQuery(id+"F0.wireOp",EDGE,"E9.3.12.23"),sQuery(id+"F0.wireOp",EDGE,"E9.6.12.23"),sQuery(id+"F0.wireOp",EDGE,"E9.9.12.23"),sQuery(id+"F0.wireOp",EDGE,"E9.0.12.24"),sQuery(id+"F0.wireOp",EDGE,"E9.3.12.24"),sQuery(id+"F0.wireOp",EDGE,"E9.6.12.24"),sQuery(id+"F0.wireOp",EDGE,"E9.9.12.24"),sQuery(id+"F0.wireOp",EDGE,"E9.0.12.25"),sQuery(id+"F0.wireOp",EDGE,"E9.3.12.25"),sQuery(id+"F0.wireOp",EDGE,"E9.6.12.25"),sQuery(id+"F0.wireOp",EDGE,"E9.9.12.25"),sQuery(id+"F0.wireOp",EDGE,"E9.0.12.26"),sQuery(id+"F0.wireOp",EDGE,"E9.3.12.26"),sQuery(id+"F0.wireOp",EDGE,"E9.6.12.26"),sQuery(id+"F0.wireOp",EDGE,"E9.9.12.26"),sQuery(id+"F0.wireOp",EDGE,"E9.0.12.27"),sQuery(id+"F0.wireOp",EDGE,"E9.3.12.27"),sQuery(id+"F0.wireOp",EDGE,"E9.6.12.27"),sQuery(id+"F0.wireOp",EDGE,"E9.9.12.27"),sQuery(id+"F0.wireOp",EDGE,"E9.0.12.28"),sQuery(id+"F0.wireOp",EDGE,"E9.3.12.28"),sQuery(id+"F0.wireOp",EDGE,"E9.6.12.28"),sQuery(id+"F0.wireOp",EDGE,"E9.9.12.28"),sQuery(id+"F0.wireOp",EDGE,"E9.0.12.29"),sQuery(id+"F0.wireOp",EDGE,"E9.3.12.29"),sQuery(id+"F0.wireOp",EDGE,"E9.6.12.29"),sQuery(id+"F0.wireOp",EDGE,"E9.9.12.29"),sQuery(id+"F0.wireOp",EDGE,"E9.0.12.30"),sQuery(id+"F0.wireOp",EDGE,"E9.3.12.30"),sQuery(id+"F0.wireOp",EDGE,"E9.6.12.30"),sQuery(id+"F0.wireOp",EDGE,"E9.9.12.30"),sQuery(id+"F0.wireOp",EDGE,"E9.0.12.31"),sQuery(id+"F0.wireOp",EDGE,"E9.3.12.31"),sQuery(id+"F0.wireOp",EDGE,"E9.6.12.31"),sQuery(id+"F0.wireOp",EDGE,"E9.9.12.31"),sQuery(id+"F0.wireOp",EDGE,"E9.0.13.0"),sQuery(id+"F0.wireOp",EDGE,"E9.3.13.0"),sQuery(id+"F0.wireOp",EDGE,"E9.6.13.0"),sQuery(id+"F0.wireOp",EDGE,"E9.9.13.0"),sQuery(id+"F0.wireOp",EDGE,"E9.0.13.1"),sQuery(id+"F0.wireOp",EDGE,"E9.3.13.1"),sQuery(id+"F0.wireOp",EDGE,"E9.6.13.1"),sQuery(id+"F0.wireOp",EDGE,"E9.9.13.1"),sQuery(id+"F0.wireOp",EDGE,"E9.0.13.2"),sQuery(id+"F0.wireOp",EDGE,"E9.3.13.2"),sQuery(id+"F0.wireOp",EDGE,"E9.6.13.2"),sQuery(id+"F0.wireOp",EDGE,"E9.9.13.2"),sQuery(id+"F0.wireOp",EDGE,"E9.0.13.3"),sQuery(id+"F0.wireOp",EDGE,"E9.3.13.3"),sQuery(id+"F0.wireOp",EDGE,"E9.6.13.3"),sQuery(id+"F0.wireOp",EDGE,"E9.9.13.3"),sQuery(id+"F0.wireOp",EDGE,"E9.0.13.4"),sQuery(id+"F0.wireOp",EDGE,"E9.3.13.4"),sQuery(id+"F0.wireOp",EDGE,"E9.6.13.4"),sQuery(id+"F0.wireOp",EDGE,"E9.9.13.4"),sQuery(id+"F0.wireOp",EDGE,"E9.0.13.5"),sQuery(id+"F0.wireOp",EDGE,"E9.3.13.5"),sQuery(id+"F0.wireOp",EDGE,"E9.6.13.5"),sQuery(id+"F0.wireOp",EDGE,"E9.9.13.5"),sQuery(id+"F0.wireOp",EDGE,"E9.0.13.6"),sQuery(id+"F0.wireOp",EDGE,"E9.3.13.6"),sQuery(id+"F0.wireOp",EDGE,"E9.6.13.6"),sQuery(id+"F0.wireOp",EDGE,"E9.9.13.6"),sQuery(id+"F0.wireOp",EDGE,"E9.0.13.7"),sQuery(id+"F0.wireOp",EDGE,"E9.3.13.7"),sQuery(id+"F0.wireOp",EDGE,"E9.6.13.7"),sQuery(id+"F0.wireOp",EDGE,"E9.9.13.7"),sQuery(id+"F0.wireOp",EDGE,"E9.0.13.8"),sQuery(id+"F0.wireOp",EDGE,"E9.3.13.8"),sQuery(id+"F0.wireOp",EDGE,"E9.6.13.8"),sQuery(id+"F0.wireOp",EDGE,"E9.9.13.8"),sQuery(id+"F0.wireOp",EDGE,"E9.0.13.9"),sQuery(id+"F0.wireOp",EDGE,"E9.3.13.9"),sQuery(id+"F0.wireOp",EDGE,"E9.6.13.9"),sQuery(id+"F0.wireOp",EDGE,"E9.9.13.9"),sQuery(id+"F0.wireOp",EDGE,"E9.0.13.10"),sQuery(id+"F0.wireOp",EDGE,"E9.3.13.10"),sQuery(id+"F0.wireOp",EDGE,"E9.6.13.10"),sQuery(id+"F0.wireOp",EDGE,"E9.9.13.10"),sQuery(id+"F0.wireOp",EDGE,"E9.0.13.11"),sQuery(id+"F0.wireOp",EDGE,"E9.3.13.11"),sQuery(id+"F0.wireOp",EDGE,"E9.6.13.11"),sQuery(id+"F0.wireOp",EDGE,"E9.9.13.11"),sQuery(id+"F0.wireOp",EDGE,"E9.0.13.12"),sQuery(id+"F0.wireOp",EDGE,"E9.3.13.12"),sQuery(id+"F0.wireOp",EDGE,"E9.6.13.12"),sQuery(id+"F0.wireOp",EDGE,"E9.9.13.12"),sQuery(id+"F0.wireOp",EDGE,"E9.0.13.13"),sQuery(id+"F0.wireOp",EDGE,"E9.3.13.13"),sQuery(id+"F0.wireOp",EDGE,"E9.6.13.13"),sQuery(id+"F0.wireOp",EDGE,"E9.9.13.13"),sQuery(id+"F0.wireOp",EDGE,"E9.0.13.14"),sQuery(id+"F0.wireOp",EDGE,"E9.3.13.14"),sQuery(id+"F0.wireOp",EDGE,"E9.6.13.14"),sQuery(id+"F0.wireOp",EDGE,"E9.9.13.14"),sQuery(id+"F0.wireOp",EDGE,"E9.0.13.15"),sQuery(id+"F0.wireOp",EDGE,"E9.3.13.15"),sQuery(id+"F0.wireOp",EDGE,"E9.6.13.15"),sQuery(id+"F0.wireOp",EDGE,"E9.9.13.15"),sQuery(id+"F0.wireOp",EDGE,"E9.0.13.16"),sQuery(id+"F0.wireOp",EDGE,"E9.3.13.16"),sQuery(id+"F0.wireOp",EDGE,"E9.6.13.16"),sQuery(id+"F0.wireOp",EDGE,"E9.9.13.16"),sQuery(id+"F0.wireOp",EDGE,"E9.0.13.17"),sQuery(id+"F0.wireOp",EDGE,"E9.3.13.17"),sQuery(id+"F0.wireOp",EDGE,"E9.6.13.17"),sQuery(id+"F0.wireOp",EDGE,"E9.9.13.17"),sQuery(id+"F0.wireOp",EDGE,"E9.0.13.18"),sQuery(id+"F0.wireOp",EDGE,"E9.3.13.18"),sQuery(id+"F0.wireOp",EDGE,"E9.6.13.18"),sQuery(id+"F0.wireOp",EDGE,"E9.9.13.18"),sQuery(id+"F0.wireOp",EDGE,"E9.0.13.19"),sQuery(id+"F0.wireOp",EDGE,"E9.3.13.19"),sQuery(id+"F0.wireOp",EDGE,"E9.6.13.19"),sQuery(id+"F0.wireOp",EDGE,"E9.9.13.19"),sQuery(id+"F0.wireOp",EDGE,"E9.0.13.20"),sQuery(id+"F0.wireOp",EDGE,"E9.3.13.20"),sQuery(id+"F0.wireOp",EDGE,"E9.6.13.20"),sQuery(id+"F0.wireOp",EDGE,"E9.9.13.20"),sQuery(id+"F0.wireOp",EDGE,"E9.0.13.21"),sQuery(id+"F0.wireOp",EDGE,"E9.3.13.21"),sQuery(id+"F0.wireOp",EDGE,"E9.6.13.21"),sQuery(id+"F0.wireOp",EDGE,"E9.9.13.21"),sQuery(id+"F0.wireOp",EDGE,"E9.0.13.22"),sQuery(id+"F0.wireOp",EDGE,"E9.3.13.22"),sQuery(id+"F0.wireOp",EDGE,"E9.6.13.22"),sQuery(id+"F0.wireOp",EDGE,"E9.9.13.22"),sQuery(id+"F0.wireOp",EDGE,"E9.0.13.23"),sQuery(id+"F0.wireOp",EDGE,"E9.3.13.23"),sQuery(id+"F0.wireOp",EDGE,"E9.6.13.23"),sQuery(id+"F0.wireOp",EDGE,"E9.9.13.23"),sQuery(id+"F0.wireOp",EDGE,"E9.0.13.24"),sQuery(id+"F0.wireOp",EDGE,"E9.3.13.24"),sQuery(id+"F0.wireOp",EDGE,"E9.6.13.24"),sQuery(id+"F0.wireOp",EDGE,"E9.9.13.24"),sQuery(id+"F0.wireOp",EDGE,"E9.0.13.25"),sQuery(id+"F0.wireOp",EDGE,"E9.3.13.25"),sQuery(id+"F0.wireOp",EDGE,"E9.6.13.25"),sQuery(id+"F0.wireOp",EDGE,"E9.9.13.25"),sQuery(id+"F0.wireOp",EDGE,"E9.0.13.26"),sQuery(id+"F0.wireOp",EDGE,"E9.3.13.26"),sQuery(id+"F0.wireOp",EDGE,"E9.6.13.26"),sQuery(id+"F0.wireOp",EDGE,"E9.9.13.26"),sQuery(id+"F0.wireOp",EDGE,"E9.0.13.27"),sQuery(id+"F0.wireOp",EDGE,"E9.3.13.27"),sQuery(id+"F0.wireOp",EDGE,"E9.6.13.27"),sQuery(id+"F0.wireOp",EDGE,"E9.9.13.27"),sQuery(id+"F0.wireOp",EDGE,"E9.0.13.28"),sQuery(id+"F0.wireOp",EDGE,"E9.3.13.28"),sQuery(id+"F0.wireOp",EDGE,"E9.6.13.28"),sQuery(id+"F0.wireOp",EDGE,"E9.9.13.28"),sQuery(id+"F0.wireOp",EDGE,"E9.0.13.29"),sQuery(id+"F0.wireOp",EDGE,"E9.3.13.29"),sQuery(id+"F0.wireOp",EDGE,"E9.6.13.29"),sQuery(id+"F0.wireOp",EDGE,"E9.9.13.29"),sQuery(id+"F0.wireOp",EDGE,"E9.0.13.30"),sQuery(id+"F0.wireOp",EDGE,"E9.3.13.30"),sQuery(id+"F0.wireOp",EDGE,"E9.6.13.30"),sQuery(id+"F0.wireOp",EDGE,"E9.9.13.30"),sQuery(id+"F0.wireOp",EDGE,"E9.0.13.31"),sQuery(id+"F0.wireOp",EDGE,"E9.3.13.31"),sQuery(id+"F0.wireOp",EDGE,"E9.6.13.31"),sQuery(id+"F0.wireOp",EDGE,"E9.9.13.31"),sQuery(id+"F0.wireOp",EDGE,"E9.0.14.0"),sQuery(id+"F0.wireOp",EDGE,"E9.3.14.0"),sQuery(id+"F0.wireOp",EDGE,"E9.6.14.0"),sQuery(id+"F0.wireOp",EDGE,"E9.9.14.0"),sQuery(id+"F0.wireOp",EDGE,"E9.0.14.1"),sQuery(id+"F0.wireOp",EDGE,"E9.3.14.1"),sQuery(id+"F0.wireOp",EDGE,"E9.6.14.1"),sQuery(id+"F0.wireOp",EDGE,"E9.9.14.1"),sQuery(id+"F0.wireOp",EDGE,"E9.0.14.2"),sQuery(id+"F0.wireOp",EDGE,"E9.3.14.2"),sQuery(id+"F0.wireOp",EDGE,"E9.6.14.2"),sQuery(id+"F0.wireOp",EDGE,"E9.9.14.2"),sQuery(id+"F0.wireOp",EDGE,"E9.0.14.3"),sQuery(id+"F0.wireOp",EDGE,"E9.3.14.3"),sQuery(id+"F0.wireOp",EDGE,"E9.6.14.3"),sQuery(id+"F0.wireOp",EDGE,"E9.9.14.3"),sQuery(id+"F0.wireOp",EDGE,"E9.0.14.4"),sQuery(id+"F0.wireOp",EDGE,"E9.3.14.4"),sQuery(id+"F0.wireOp",EDGE,"E9.6.14.4"),sQuery(id+"F0.wireOp",EDGE,"E9.9.14.4"),sQuery(id+"F0.wireOp",EDGE,"E9.0.14.5"),sQuery(id+"F0.wireOp",EDGE,"E9.3.14.5"),sQuery(id+"F0.wireOp",EDGE,"E9.6.14.5"),sQuery(id+"F0.wireOp",EDGE,"E9.9.14.5"),sQuery(id+"F0.wireOp",EDGE,"E9.0.14.6"),sQuery(id+"F0.wireOp",EDGE,"E9.3.14.6"),sQuery(id+"F0.wireOp",EDGE,"E9.6.14.6"),sQuery(id+"F0.wireOp",EDGE,"E9.9.14.6"),sQuery(id+"F0.wireOp",EDGE,"E9.0.14.7"),sQuery(id+"F0.wireOp",EDGE,"E9.3.14.7"),sQuery(id+"F0.wireOp",EDGE,"E9.6.14.7"),sQuery(id+"F0.wireOp",EDGE,"E9.9.14.7"),sQuery(id+"F0.wireOp",EDGE,"E9.0.14.8"),sQuery(id+"F0.wireOp",EDGE,"E9.3.14.8"),sQuery(id+"F0.wireOp",EDGE,"E9.6.14.8"),sQuery(id+"F0.wireOp",EDGE,"E9.9.14.8"),sQuery(id+"F0.wireOp",EDGE,"E9.0.14.9"),sQuery(id+"F0.wireOp",EDGE,"E9.3.14.9"),sQuery(id+"F0.wireOp",EDGE,"E9.6.14.9"),sQuery(id+"F0.wireOp",EDGE,"E9.9.14.9"),sQuery(id+"F0.wireOp",EDGE,"E9.0.14.10"),sQuery(id+"F0.wireOp",EDGE,"E9.3.14.10"),sQuery(id+"F0.wireOp",EDGE,"E9.6.14.10"),sQuery(id+"F0.wireOp",EDGE,"E9.9.14.10"),sQuery(id+"F0.wireOp",EDGE,"E9.0.14.11"),sQuery(id+"F0.wireOp",EDGE,"E9.3.14.11"),sQuery(id+"F0.wireOp",EDGE,"E9.6.14.11"),sQuery(id+"F0.wireOp",EDGE,"E9.9.14.11"),sQuery(id+"F0.wireOp",EDGE,"E9.0.14.12"),sQuery(id+"F0.wireOp",EDGE,"E9.3.14.12"),sQuery(id+"F0.wireOp",EDGE,"E9.6.14.12"),sQuery(id+"F0.wireOp",EDGE,"E9.9.14.12"),sQuery(id+"F0.wireOp",EDGE,"E9.0.14.13"),sQuery(id+"F0.wireOp",EDGE,"E9.3.14.13"),sQuery(id+"F0.wireOp",EDGE,"E9.6.14.13"),sQuery(id+"F0.wireOp",EDGE,"E9.9.14.13"),sQuery(id+"F0.wireOp",EDGE,"E9.0.14.14"),sQuery(id+"F0.wireOp",EDGE,"E9.3.14.14"),sQuery(id+"F0.wireOp",EDGE,"E9.6.14.14"),sQuery(id+"F0.wireOp",EDGE,"E9.9.14.14"),sQuery(id+"F0.wireOp",EDGE,"E9.0.14.15"),sQuery(id+"F0.wireOp",EDGE,"E9.3.14.15"),sQuery(id+"F0.wireOp",EDGE,"E9.6.14.15"),sQuery(id+"F0.wireOp",EDGE,"E9.9.14.15"),sQuery(id+"F0.wireOp",EDGE,"E9.0.14.16"),sQuery(id+"F0.wireOp",EDGE,"E9.3.14.16"),sQuery(id+"F0.wireOp",EDGE,"E9.6.14.16"),sQuery(id+"F0.wireOp",EDGE,"E9.9.14.16"),sQuery(id+"F0.wireOp",EDGE,"E9.0.14.17"),sQuery(id+"F0.wireOp",EDGE,"E9.3.14.17"),sQuery(id+"F0.wireOp",EDGE,"E9.6.14.17"),sQuery(id+"F0.wireOp",EDGE,"E9.9.14.17"),sQuery(id+"F0.wireOp",EDGE,"E9.0.14.18"),sQuery(id+"F0.wireOp",EDGE,"E9.3.14.18"),sQuery(id+"F0.wireOp",EDGE,"E9.6.14.18"),sQuery(id+"F0.wireOp",EDGE,"E9.9.14.18"),sQuery(id+"F0.wireOp",EDGE,"E9.0.14.19"),sQuery(id+"F0.wireOp",EDGE,"E9.3.14.19"),sQuery(id+"F0.wireOp",EDGE,"E9.6.14.19"),sQuery(id+"F0.wireOp",EDGE,"E9.9.14.19"),sQuery(id+"F0.wireOp",EDGE,"E9.0.14.20"),sQuery(id+"F0.wireOp",EDGE,"E9.3.14.20"),sQuery(id+"F0.wireOp",EDGE,"E9.6.14.20"),sQuery(id+"F0.wireOp",EDGE,"E9.9.14.20"),sQuery(id+"F0.wireOp",EDGE,"E9.0.14.21"),sQuery(id+"F0.wireOp",EDGE,"E9.3.14.21"),sQuery(id+"F0.wireOp",EDGE,"E9.6.14.21"),sQuery(id+"F0.wireOp",EDGE,"E9.9.14.21"),sQuery(id+"F0.wireOp",EDGE,"E9.0.14.22"),sQuery(id+"F0.wireOp",EDGE,"E9.3.14.22"),sQuery(id+"F0.wireOp",EDGE,"E9.6.14.22"),sQuery(id+"F0.wireOp",EDGE,"E9.9.14.22"),sQuery(id+"F0.wireOp",EDGE,"E9.0.14.23"),sQuery(id+"F0.wireOp",EDGE,"E9.3.14.23"),sQuery(id+"F0.wireOp",EDGE,"E9.6.14.23"),sQuery(id+"F0.wireOp",EDGE,"E9.9.14.23"),sQuery(id+"F0.wireOp",EDGE,"E9.0.14.24"),sQuery(id+"F0.wireOp",EDGE,"E9.3.14.24"),sQuery(id+"F0.wireOp",EDGE,"E9.6.14.24"),sQuery(id+"F0.wireOp",EDGE,"E9.9.14.24"),sQuery(id+"F0.wireOp",EDGE,"E9.0.14.25"),sQuery(id+"F0.wireOp",EDGE,"E9.3.14.25"),sQuery(id+"F0.wireOp",EDGE,"E9.6.14.25"),sQuery(id+"F0.wireOp",EDGE,"E9.9.14.25"),sQuery(id+"F0.wireOp",EDGE,"E9.0.14.26"),sQuery(id+"F0.wireOp",EDGE,"E9.3.14.26"),sQuery(id+"F0.wireOp",EDGE,"E9.6.14.26"),sQuery(id+"F0.wireOp",EDGE,"E9.9.14.26"),sQuery(id+"F0.wireOp",EDGE,"E9.0.14.27"),sQuery(id+"F0.wireOp",EDGE,"E9.3.14.27"),sQuery(id+"F0.wireOp",EDGE,"E9.6.14.27"),sQuery(id+"F0.wireOp",EDGE,"E9.9.14.27"),sQuery(id+"F0.wireOp",EDGE,"E9.0.14.28"),sQuery(id+"F0.wireOp",EDGE,"E9.3.14.28"),sQuery(id+"F0.wireOp",EDGE,"E9.6.14.28"),sQuery(id+"F0.wireOp",EDGE,"E9.9.14.28"),sQuery(id+"F0.wireOp",EDGE,"E9.0.14.29"),sQuery(id+"F0.wireOp",EDGE,"E9.3.14.29"),sQuery(id+"F0.wireOp",EDGE,"E9.6.14.29"),sQuery(id+"F0.wireOp",EDGE,"E9.9.14.29"),sQuery(id+"F0.wireOp",EDGE,"E9.0.14.30"),sQuery(id+"F0.wireOp",EDGE,"E9.3.14.30"),sQuery(id+"F0.wireOp",EDGE,"E9.6.14.30"),sQuery(id+"F0.wireOp",EDGE,"E9.9.14.30"),sQuery(id+"F0.wireOp",EDGE,"E9.0.14.31"),sQuery(id+"F0.wireOp",EDGE,"E9.3.14.31"),sQuery(id+"F0.wireOp",EDGE,"E9.6.14.31"),sQuery(id+"F0.wireOp",EDGE,"E9.9.14.31"),sQuery(id+"F0.wireOp",EDGE,"073a8239-eeac-400b-97e6-9f9c82d259df.0.15.0"),sQuery(id+"F0.wireOp",EDGE,"073a8239-eeac-400b-97e6-9f9c82d259df.3.15.0"),sQuery(id+"F0.wireOp",EDGE,"073a8239-eeac-400b-97e6-9f9c82d259df.6.15.0"),sQuery(id+"F0.wireOp",EDGE,"073a8239-eeac-400b-97e6-9f9c82d259df.9.15.0"),sQuery(id+"F0.wireOp",EDGE,"073a8239-eeac-400b-97e6-9f9c82d259df.0.15.1"),sQuery(id+"F0.wireOp",EDGE,"073a8239-eeac-400b-97e6-9f9c82d259df.3.15.1"),sQuery(id+"F0.wireOp",EDGE,"073a8239-eeac-400b-97e6-9f9c82d259df.6.15.1"),sQuery(id+"F0.wireOp",EDGE,"073a8239-eeac-400b-97e6-9f9c82d259df.9.15.1"),sQuery(id+"F0.wireOp",EDGE,"073a8239-eeac-400b-97e6-9f9c82d259df.0.15.2"),sQuery(id+"F0.wireOp",EDGE,"073a8239-eeac-400b-97e6-9f9c82d259df.3.15.2"),sQuery(id+"F0.wireOp",EDGE,"073a8239-eeac-400b-97e6-9f9c82d259df.6.15.2"),sQuery(id+"F0.wireOp",EDGE,"073a8239-eeac-400b-97e6-9f9c82d259df.9.15.2"),sQuery(id+"F0.wireOp",EDGE,"073a8239-eeac-400b-97e6-9f9c82d259df.0.15.3"),sQuery(id+"F0.wireOp",EDGE,"073a8239-eeac-400b-97e6-9f9c82d259df.3.15.3"),sQuery(id+"F0.wireOp",EDGE,"073a8239-eeac-400b-97e6-9f9c82d259df.6.15.3"),sQuery(id+"F0.wireOp",EDGE,"073a8239-eeac-400b-97e6-9f9c82d259df.9.15.3"),sQuery(id+"F0.wireOp",EDGE,"073a8239-eeac-400b-97e6-9f9c82d259df.0.15.4"),sQuery(id+"F0.wireOp",EDGE,"073a8239-eeac-400b-97e6-9f9c82d259df.3.15.4"),sQuery(id+"F0.wireOp",EDGE,"073a8239-eeac-400b-97e6-9f9c82d259df.6.15.4"),sQuery(id+"F0.wireOp",EDGE,"073a8239-eeac-400b-97e6-9f9c82d259df.9.15.4"),sQuery(id+"F0.wireOp",EDGE,"073a8239-eeac-400b-97e6-9f9c82d259df.0.15.5"),sQuery(id+"F0.wireOp",EDGE,"073a8239-eeac-400b-97e6-9f9c82d259df.3.15.5"),sQuery(id+"F0.wireOp",EDGE,"073a8239-eeac-400b-97e6-9f9c82d259df.6.15.5"),sQuery(id+"F0.wireOp",EDGE,"073a8239-eeac-400b-97e6-9f9c82d259df.9.15.5"),sQuery(id+"F0.wireOp",EDGE,"073a8239-eeac-400b-97e6-9f9c82d259df.0.15.6"),sQuery(id+"F0.wireOp",EDGE,"073a8239-eeac-400b-97e6-9f9c82d259df.3.15.6"),sQuery(id+"F0.wireOp",EDGE,"073a8239-eeac-400b-97e6-9f9c82d259df.6.15.6"),sQuery(id+"F0.wireOp",EDGE,"073a8239-eeac-400b-97e6-9f9c82d259df.9.15.6"),sQuery(id+"F0.wireOp",EDGE,"073a8239-eeac-400b-97e6-9f9c82d259df.0.15.7"),sQuery(id+"F0.wireOp",EDGE,"073a8239-eeac-400b-97e6-9f9c82d259df.3.15.7"),sQuery(id+"F0.wireOp",EDGE,"073a8239-eeac-400b-97e6-9f9c82d259df.6.15.7"),sQuery(id+"F0.wireOp",EDGE,"073a8239-eeac-400b-97e6-9f9c82d259df.9.15.7"),sQuery(id+"F0.wireOp",EDGE,"073a8239-eeac-400b-97e6-9f9c82d259df.0.15.8"),sQuery(id+"F0.wireOp",EDGE,"073a8239-eeac-400b-97e6-9f9c82d259df.3.15.8"),sQuery(id+"F0.wireOp",EDGE,"073a8239-eeac-400b-97e6-9f9c82d259df.6.15.8"),sQuery(id+"F0.wireOp",EDGE,"073a8239-eeac-400b-97e6-9f9c82d259df.9.15.8"),sQuery(id+"F0.wireOp",EDGE,"073a8239-eeac-400b-97e6-9f9c82d259df.0.15.9"),sQuery(id+"F0.wireOp",EDGE,"073a8239-eeac-400b-97e6-9f9c82d259df.3.15.9"),sQuery(id+"F0.wireOp",EDGE,"073a8239-eeac-400b-97e6-9f9c82d259df.6.15.9"),sQuery(id+"F0.wireOp",EDGE,"073a8239-eeac-400b-97e6-9f9c82d259df.9.15.9"),sQuery(id+"F0.wireOp",EDGE,"073a8239-eeac-400b-97e6-9f9c82d259df.0.15.10"),sQuery(id+"F0.wireOp",EDGE,"073a8239-eeac-400b-97e6-9f9c82d259df.3.15.10"),sQuery(id+"F0.wireOp",EDGE,"073a8239-eeac-400b-97e6-9f9c82d259df.6.15.10"),sQuery(id+"F0.wireOp",EDGE,"073a8239-eeac-400b-97e6-9f9c82d259df.9.15.10"),sQuery(id+"F0.wireOp",EDGE,"073a8239-eeac-400b-97e6-9f9c82d259df.0.15.11"),sQuery(id+"F0.wireOp",EDGE,"073a8239-eeac-400b-97e6-9f9c82d259df.3.15.11"),sQuery(id+"F0.wireOp",EDGE,"073a8239-eeac-400b-97e6-9f9c82d259df.6.15.11"),sQuery(id+"F0.wireOp",EDGE,"073a8239-eeac-400b-97e6-9f9c82d259df.9.15.11"),sQuery(id+"F0.wireOp",EDGE,"073a8239-eeac-400b-97e6-9f9c82d259df.0.15.12"),sQuery(id+"F0.wireOp",EDGE,"073a8239-eeac-400b-97e6-9f9c82d259df.3.15.12"),sQuery(id+"F0.wireOp",EDGE,"073a8239-eeac-400b-97e6-9f9c82d259df.6.15.12"),sQuery(id+"F0.wireOp",EDGE,"073a8239-eeac-400b-97e6-9f9c82d259df.9.15.12"),sQuery(id+"F0.wireOp",EDGE,"073a8239-eeac-400b-97e6-9f9c82d259df.0.15.13"),sQuery(id+"F0.wireOp",EDGE,"073a8239-eeac-400b-97e6-9f9c82d259df.3.15.13"),sQuery(id+"F0.wireOp",EDGE,"073a8239-eeac-400b-97e6-9f9c82d259df.6.15.13"),sQuery(id+"F0.wireOp",EDGE,"073a8239-eeac-400b-97e6-9f9c82d259df.9.15.13"),sQuery(id+"F0.wireOp",EDGE,"073a8239-eeac-400b-97e6-9f9c82d259df.0.15.14"),sQuery(id+"F0.wireOp",EDGE,"073a8239-eeac-400b-97e6-9f9c82d259df.3.15.14"),sQuery(id+"F0.wireOp",EDGE,"073a8239-eeac-400b-97e6-9f9c82d259df.6.15.14"),sQuery(id+"F0.wireOp",EDGE,"073a8239-eeac-400b-97e6-9f9c82d259df.9.15.14"),sQuery(id+"F0.wireOp",EDGE,"073a8239-eeac-400b-97e6-9f9c82d259df.0.15.15"),sQuery(id+"F0.wireOp",EDGE,"073a8239-eeac-400b-97e6-9f9c82d259df.3.15.15"),sQuery(id+"F0.wireOp",EDGE,"073a8239-eeac-400b-97e6-9f9c82d259df.6.15.15"),sQuery(id+"F0.wireOp",EDGE,"073a8239-eeac-400b-97e6-9f9c82d259df.9.15.15"),sQuery(id+"F0.wireOp",EDGE,"073a8239-eeac-400b-97e6-9f9c82d259df.0.15.16"),sQuery(id+"F0.wireOp",EDGE,"073a8239-eeac-400b-97e6-9f9c82d259df.3.15.16"),sQuery(id+"F0.wireOp",EDGE,"073a8239-eeac-400b-97e6-9f9c82d259df.6.15.16"),sQuery(id+"F0.wireOp",EDGE,"073a8239-eeac-400b-97e6-9f9c82d259df.9.15.16"),sQuery(id+"F0.wireOp",EDGE,"073a8239-eeac-400b-97e6-9f9c82d259df.0.15.17"),sQuery(id+"F0.wireOp",EDGE,"073a8239-eeac-400b-97e6-9f9c82d259df.3.15.17"),sQuery(id+"F0.wireOp",EDGE,"073a8239-eeac-400b-97e6-9f9c82d259df.6.15.17"),sQuery(id+"F0.wireOp",EDGE,"073a8239-eeac-400b-97e6-9f9c82d259df.9.15.17"),sQuery(id+"F0.wireOp",EDGE,"073a8239-eeac-400b-97e6-9f9c82d259df.0.15.18"),sQuery(id+"F0.wireOp",EDGE,"073a8239-eeac-400b-97e6-9f9c82d259df.3.15.18"),sQuery(id+"F0.wireOp",EDGE,"073a8239-eeac-400b-97e6-9f9c82d259df.6.15.18"),sQuery(id+"F0.wireOp",EDGE,"073a8239-eeac-400b-97e6-9f9c82d259df.9.15.18"),sQuery(id+"F0.wireOp",EDGE,"073a8239-eeac-400b-97e6-9f9c82d259df.0.15.19"),sQuery(id+"F0.wireOp",EDGE,"073a8239-eeac-400b-97e6-9f9c82d259df.3.15.19"),sQuery(id+"F0.wireOp",EDGE,"073a8239-eeac-400b-97e6-9f9c82d259df.6.15.19"),sQuery(id+"F0.wireOp",EDGE,"073a8239-eeac-400b-97e6-9f9c82d259df.9.15.19"),sQuery(id+"F0.wireOp",EDGE,"073a8239-eeac-400b-97e6-9f9c82d259df.0.15.20"),sQuery(id+"F0.wireOp",EDGE,"073a8239-eeac-400b-97e6-9f9c82d259df.3.15.20"),sQuery(id+"F0.wireOp",EDGE,"073a8239-eeac-400b-97e6-9f9c82d259df.6.15.20"),sQuery(id+"F0.wireOp",EDGE,"073a8239-eeac-400b-97e6-9f9c82d259df.9.15.20"),sQuery(id+"F0.wireOp",EDGE,"073a8239-eeac-400b-97e6-9f9c82d259df.0.15.21"),sQuery(id+"F0.wireOp",EDGE,"073a8239-eeac-400b-97e6-9f9c82d259df.3.15.21"),sQuery(id+"F0.wireOp",EDGE,"073a8239-eeac-400b-97e6-9f9c82d259df.6.15.21"),sQuery(id+"F0.wireOp",EDGE,"073a8239-eeac-400b-97e6-9f9c82d259df.9.15.21"),sQuery(id+"F0.wireOp",EDGE,"073a8239-eeac-400b-97e6-9f9c82d259df.0.15.22"),sQuery(id+"F0.wireOp",EDGE,"073a8239-eeac-400b-97e6-9f9c82d259df.3.15.22"),sQuery(id+"F0.wireOp",EDGE,"073a8239-eeac-400b-97e6-9f9c82d259df.6.15.22"),sQuery(id+"F0.wireOp",EDGE,"073a8239-eeac-400b-97e6-9f9c82d259df.9.15.22"),sQuery(id+"F0.wireOp",EDGE,"073a8239-eeac-400b-97e6-9f9c82d259df.0.15.23"),sQuery(id+"F0.wireOp",EDGE,"073a8239-eeac-400b-97e6-9f9c82d259df.3.15.23"),sQuery(id+"F0.wireOp",EDGE,"073a8239-eeac-400b-97e6-9f9c82d259df.6.15.23"),sQuery(id+"F0.wireOp",EDGE,"073a8239-eeac-400b-97e6-9f9c82d259df.9.15.23"),sQuery(id+"F0.wireOp",EDGE,"073a8239-eeac-400b-97e6-9f9c82d259df.0.15.24"),sQuery(id+"F0.wireOp",EDGE,"073a8239-eeac-400b-97e6-9f9c82d259df.3.15.24"),sQuery(id+"F0.wireOp",EDGE,"073a8239-eeac-400b-97e6-9f9c82d259df.6.15.24"),sQuery(id+"F0.wireOp",EDGE,"073a8239-eeac-400b-97e6-9f9c82d259df.9.15.24"),sQuery(id+"F0.wireOp",EDGE,"073a8239-eeac-400b-97e6-9f9c82d259df.0.15.25"),sQuery(id+"F0.wireOp",EDGE,"073a8239-eeac-400b-97e6-9f9c82d259df.3.15.25"),sQuery(id+"F0.wireOp",EDGE,"073a8239-eeac-400b-97e6-9f9c82d259df.6.15.25"),sQuery(id+"F0.wireOp",EDGE,"073a8239-eeac-400b-97e6-9f9c82d259df.9.15.25"),sQuery(id+"F0.wireOp",EDGE,"073a8239-eeac-400b-97e6-9f9c82d259df.0.15.26"),sQuery(id+"F0.wireOp",EDGE,"073a8239-eeac-400b-97e6-9f9c82d259df.3.15.26"),sQuery(id+"F0.wireOp",EDGE,"073a8239-eeac-400b-97e6-9f9c82d259df.6.15.26"),sQuery(id+"F0.wireOp",EDGE,"073a8239-eeac-400b-97e6-9f9c82d259df.9.15.26"),sQuery(id+"F0.wireOp",EDGE,"073a8239-eeac-400b-97e6-9f9c82d259df.0.15.27"),sQuery(id+"F0.wireOp",EDGE,"073a8239-eeac-400b-97e6-9f9c82d259df.3.15.27"),sQuery(id+"F0.wireOp",EDGE,"073a8239-eeac-400b-97e6-9f9c82d259df.6.15.27"),sQuery(id+"F0.wireOp",EDGE,"073a8239-eeac-400b-97e6-9f9c82d259df.9.15.27"),sQuery(id+"F0.wireOp",EDGE,"073a8239-eeac-400b-97e6-9f9c82d259df.0.15.28"),sQuery(id+"F0.wireOp",EDGE,"073a8239-eeac-400b-97e6-9f9c82d259df.3.15.28"),sQuery(id+"F0.wireOp",EDGE,"073a8239-eeac-400b-97e6-9f9c82d259df.6.15.28"),sQuery(id+"F0.wireOp",EDGE,"073a8239-eeac-400b-97e6-9f9c82d259df.9.15.28"),sQuery(id+"F0.wireOp",EDGE,"073a8239-eeac-400b-97e6-9f9c82d259df.0.15.29"),sQuery(id+"F0.wireOp",EDGE,"073a8239-eeac-400b-97e6-9f9c82d259df.3.15.29"),sQuery(id+"F0.wireOp",EDGE,"073a8239-eeac-400b-97e6-9f9c82d259df.6.15.29"),sQuery(id+"F0.wireOp",EDGE,"073a8239-eeac-400b-97e6-9f9c82d259df.9.15.29"),sQuery(id+"F0.wireOp",EDGE,"073a8239-eeac-400b-97e6-9f9c82d259df.0.15.30"),sQuery(id+"F0.wireOp",EDGE,"073a8239-eeac-400b-97e6-9f9c82d259df.3.15.30"),sQuery(id+"F0.wireOp",EDGE,"073a8239-eeac-400b-97e6-9f9c82d259df.6.15.30"),sQuery(id+"F0.wireOp",EDGE,"073a8239-eeac-400b-97e6-9f9c82d259df.9.15.30"),sQuery(id+"F0.wireOp",EDGE,"073a8239-eeac-400b-97e6-9f9c82d259df.0.15.31"),sQuery(id+"F0.wireOp",EDGE,"073a8239-eeac-400b-97e6-9f9c82d259df.3.15.31"),sQuery(id+"F0.wireOp",EDGE,"073a8239-eeac-400b-97e6-9f9c82d259df.6.15.31"),sQuery(id+"F0.wireOp",EDGE,"073a8239-eeac-400b-97e6-9f9c82d259df.9.15.31"),sQuery(id+"F0.wireOp",EDGE,"073a8239-eeac-400b-97e6-9f9c82d259df.0.16.0"),sQuery(id+"F0.wireOp",EDGE,"073a8239-eeac-400b-97e6-9f9c82d259df.3.16.0"),sQuery(id+"F0.wireOp",EDGE,"073a8239-eeac-400b-97e6-9f9c82d259df.6.16.0"),sQuery(id+"F0.wireOp",EDGE,"073a8239-eeac-400b-97e6-9f9c82d259df.9.16.0"),sQuery(id+"F0.wireOp",EDGE,"073a8239-eeac-400b-97e6-9f9c82d259df.0.16.1"),sQuery(id+"F0.wireOp",EDGE,"073a8239-eeac-400b-97e6-9f9c82d259df.3.16.1"),sQuery(id+"F0.wireOp",EDGE,"073a8239-eeac-400b-97e6-9f9c82d259df.6.16.1"),sQuery(id+"F0.wireOp",EDGE,"073a8239-eeac-400b-97e6-9f9c82d259df.9.16.1"),sQuery(id+"F0.wireOp",EDGE,"073a8239-eeac-400b-97e6-9f9c82d259df.0.16.2"),sQuery(id+"F0.wireOp",EDGE,"073a8239-eeac-400b-97e6-9f9c82d259df.3.16.2"),sQuery(id+"F0.wireOp",EDGE,"073a8239-eeac-400b-97e6-9f9c82d259df.6.16.2"),sQuery(id+"F0.wireOp",EDGE,"073a8239-eeac-400b-97e6-9f9c82d259df.9.16.2"),sQuery(id+"F0.wireOp",EDGE,"073a8239-eeac-400b-97e6-9f9c82d259df.0.16.3"),sQuery(id+"F0.wireOp",EDGE,"073a8239-eeac-400b-97e6-9f9c82d259df.3.16.3"),sQuery(id+"F0.wireOp",EDGE,"073a8239-eeac-400b-97e6-9f9c82d259df.6.16.3"),sQuery(id+"F0.wireOp",EDGE,"073a8239-eeac-400b-97e6-9f9c82d259df.9.16.3"),sQuery(id+"F0.wireOp",EDGE,"073a8239-eeac-400b-97e6-9f9c82d259df.0.16.4"),sQuery(id+"F0.wireOp",EDGE,"073a8239-eeac-400b-97e6-9f9c82d259df.3.16.4"),sQuery(id+"F0.wireOp",EDGE,"073a8239-eeac-400b-97e6-9f9c82d259df.6.16.4"),sQuery(id+"F0.wireOp",EDGE,"073a8239-eeac-400b-97e6-9f9c82d259df.9.16.4"),sQuery(id+"F0.wireOp",EDGE,"073a8239-eeac-400b-97e6-9f9c82d259df.0.16.5"),sQuery(id+"F0.wireOp",EDGE,"073a8239-eeac-400b-97e6-9f9c82d259df.3.16.5"),sQuery(id+"F0.wireOp",EDGE,"073a8239-eeac-400b-97e6-9f9c82d259df.6.16.5"),sQuery(id+"F0.wireOp",EDGE,"073a8239-eeac-400b-97e6-9f9c82d259df.9.16.5"),sQuery(id+"F0.wireOp",EDGE,"073a8239-eeac-400b-97e6-9f9c82d259df.0.16.6"),sQuery(id+"F0.wireOp",EDGE,"073a8239-eeac-400b-97e6-9f9c82d259df.3.16.6"),sQuery(id+"F0.wireOp",EDGE,"073a8239-eeac-400b-97e6-9f9c82d259df.6.16.6"),sQuery(id+"F0.wireOp",EDGE,"073a8239-eeac-400b-97e6-9f9c82d259df.9.16.6"),sQuery(id+"F0.wireOp",EDGE,"073a8239-eeac-400b-97e6-9f9c82d259df.0.16.7"),sQuery(id+"F0.wireOp",EDGE,"073a8239-eeac-400b-97e6-9f9c82d259df.3.16.7"),sQuery(id+"F0.wireOp",EDGE,"073a8239-eeac-400b-97e6-9f9c82d259df.6.16.7"),sQuery(id+"F0.wireOp",EDGE,"073a8239-eeac-400b-97e6-9f9c82d259df.9.16.7"),sQuery(id+"F0.wireOp",EDGE,"073a8239-eeac-400b-97e6-9f9c82d259df.0.16.8"),sQuery(id+"F0.wireOp",EDGE,"073a8239-eeac-400b-97e6-9f9c82d259df.3.16.8"),sQuery(id+"F0.wireOp",EDGE,"073a8239-eeac-400b-97e6-9f9c82d259df.6.16.8"),sQuery(id+"F0.wireOp",EDGE,"073a8239-eeac-400b-97e6-9f9c82d259df.9.16.8"),sQuery(id+"F0.wireOp",EDGE,"073a8239-eeac-400b-97e6-9f9c82d259df.0.16.9"),sQuery(id+"F0.wireOp",EDGE,"073a8239-eeac-400b-97e6-9f9c82d259df.3.16.9"),sQuery(id+"F0.wireOp",EDGE,"073a8239-eeac-400b-97e6-9f9c82d259df.6.16.9"),sQuery(id+"F0.wireOp",EDGE,"073a8239-eeac-400b-97e6-9f9c82d259df.9.16.9"),sQuery(id+"F0.wireOp",EDGE,"073a8239-eeac-400b-97e6-9f9c82d259df.0.16.10"),sQuery(id+"F0.wireOp",EDGE,"073a8239-eeac-400b-97e6-9f9c82d259df.3.16.10"),sQuery(id+"F0.wireOp",EDGE,"073a8239-eeac-400b-97e6-9f9c82d259df.6.16.10"),sQuery(id+"F0.wireOp",EDGE,"073a8239-eeac-400b-97e6-9f9c82d259df.9.16.10"),sQuery(id+"F0.wireOp",EDGE,"073a8239-eeac-400b-97e6-9f9c82d259df.0.16.11"),sQuery(id+"F0.wireOp",EDGE,"073a8239-eeac-400b-97e6-9f9c82d259df.3.16.11"),sQuery(id+"F0.wireOp",EDGE,"073a8239-eeac-400b-97e6-9f9c82d259df.6.16.11"),sQuery(id+"F0.wireOp",EDGE,"073a8239-eeac-400b-97e6-9f9c82d259df.9.16.11"),sQuery(id+"F0.wireOp",EDGE,"073a8239-eeac-400b-97e6-9f9c82d259df.0.16.12"),sQuery(id+"F0.wireOp",EDGE,"073a8239-eeac-400b-97e6-9f9c82d259df.3.16.12"),sQuery(id+"F0.wireOp",EDGE,"073a8239-eeac-400b-97e6-9f9c82d259df.6.16.12"),sQuery(id+"F0.wireOp",EDGE,"073a8239-eeac-400b-97e6-9f9c82d259df.9.16.12"),sQuery(id+"F0.wireOp",EDGE,"073a8239-eeac-400b-97e6-9f9c82d259df.0.16.13"),sQuery(id+"F0.wireOp",EDGE,"073a8239-eeac-400b-97e6-9f9c82d259df.3.16.13"),sQuery(id+"F0.wireOp",EDGE,"073a8239-eeac-400b-97e6-9f9c82d259df.6.16.13"),sQuery(id+"F0.wireOp",EDGE,"073a8239-eeac-400b-97e6-9f9c82d259df.9.16.13"),sQuery(id+"F0.wireOp",EDGE,"073a8239-eeac-400b-97e6-9f9c82d259df.0.16.14"),sQuery(id+"F0.wireOp",EDGE,"073a8239-eeac-400b-97e6-9f9c82d259df.3.16.14"),sQuery(id+"F0.wireOp",EDGE,"073a8239-eeac-400b-97e6-9f9c82d259df.6.16.14"),sQuery(id+"F0.wireOp",EDGE,"073a8239-eeac-400b-97e6-9f9c82d259df.9.16.14"),sQuery(id+"F0.wireOp",EDGE,"073a8239-eeac-400b-97e6-9f9c82d259df.0.16.15"),sQuery(id+"F0.wireOp",EDGE,"073a8239-eeac-400b-97e6-9f9c82d259df.3.16.15"),sQuery(id+"F0.wireOp",EDGE,"073a8239-eeac-400b-97e6-9f9c82d259df.6.16.15"),sQuery(id+"F0.wireOp",EDGE,"073a8239-eeac-400b-97e6-9f9c82d259df.9.16.15"),sQuery(id+"F0.wireOp",EDGE,"073a8239-eeac-400b-97e6-9f9c82d259df.0.16.16"),sQuery(id+"F0.wireOp",EDGE,"073a8239-eeac-400b-97e6-9f9c82d259df.3.16.16"),sQuery(id+"F0.wireOp",EDGE,"073a8239-eeac-400b-97e6-9f9c82d259df.6.16.16"),sQuery(id+"F0.wireOp",EDGE,"073a8239-eeac-400b-97e6-9f9c82d259df.9.16.16"),sQuery(id+"F0.wireOp",EDGE,"073a8239-eeac-400b-97e6-9f9c82d259df.0.16.17"),sQuery(id+"F0.wireOp",EDGE,"073a8239-eeac-400b-97e6-9f9c82d259df.3.16.17"),sQuery(id+"F0.wireOp",EDGE,"073a8239-eeac-400b-97e6-9f9c82d259df.6.16.17"),sQuery(id+"F0.wireOp",EDGE,"073a8239-eeac-400b-97e6-9f9c82d259df.9.16.17"),sQuery(id+"F0.wireOp",EDGE,"073a8239-eeac-400b-97e6-9f9c82d259df.0.16.18"),sQuery(id+"F0.wireOp",EDGE,"073a8239-eeac-400b-97e6-9f9c82d259df.3.16.18"),sQuery(id+"F0.wireOp",EDGE,"073a8239-eeac-400b-97e6-9f9c82d259df.6.16.18"),sQuery(id+"F0.wireOp",EDGE,"073a8239-eeac-400b-97e6-9f9c82d259df.9.16.18"),sQuery(id+"F0.wireOp",EDGE,"073a8239-eeac-400b-97e6-9f9c82d259df.0.16.19"),sQuery(id+"F0.wireOp",EDGE,"073a8239-eeac-400b-97e6-9f9c82d259df.3.16.19"),sQuery(id+"F0.wireOp",EDGE,"073a8239-eeac-400b-97e6-9f9c82d259df.6.16.19"),sQuery(id+"F0.wireOp",EDGE,"073a8239-eeac-400b-97e6-9f9c82d259df.9.16.19"),sQuery(id+"F0.wireOp",EDGE,"073a8239-eeac-400b-97e6-9f9c82d259df.0.16.20"),sQuery(id+"F0.wireOp",EDGE,"073a8239-eeac-400b-97e6-9f9c82d259df.3.16.20"),sQuery(id+"F0.wireOp",EDGE,"073a8239-eeac-400b-97e6-9f9c82d259df.6.16.20"),sQuery(id+"F0.wireOp",EDGE,"073a8239-eeac-400b-97e6-9f9c82d259df.9.16.20"),sQuery(id+"F0.wireOp",EDGE,"073a8239-eeac-400b-97e6-9f9c82d259df.0.16.21"),sQuery(id+"F0.wireOp",EDGE,"073a8239-eeac-400b-97e6-9f9c82d259df.3.16.21"),sQuery(id+"F0.wireOp",EDGE,"073a8239-eeac-400b-97e6-9f9c82d259df.6.16.21"),sQuery(id+"F0.wireOp",EDGE,"073a8239-eeac-400b-97e6-9f9c82d259df.9.16.21"),sQuery(id+"F0.wireOp",EDGE,"073a8239-eeac-400b-97e6-9f9c82d259df.0.16.22"),sQuery(id+"F0.wireOp",EDGE,"073a8239-eeac-400b-97e6-9f9c82d259df.3.16.22"),sQuery(id+"F0.wireOp",EDGE,"073a8239-eeac-400b-97e6-9f9c82d259df.6.16.22"),sQuery(id+"F0.wireOp",EDGE,"073a8239-eeac-400b-97e6-9f9c82d259df.9.16.22"),sQuery(id+"F0.wireOp",EDGE,"073a8239-eeac-400b-97e6-9f9c82d259df.0.16.23"),sQuery(id+"F0.wireOp",EDGE,"073a8239-eeac-400b-97e6-9f9c82d259df.3.16.23"),sQuery(id+"F0.wireOp",EDGE,"073a8239-eeac-400b-97e6-9f9c82d259df.6.16.23"),sQuery(id+"F0.wireOp",EDGE,"073a8239-eeac-400b-97e6-9f9c82d259df.9.16.23"),sQuery(id+"F0.wireOp",EDGE,"073a8239-eeac-400b-97e6-9f9c82d259df.0.16.24"),sQuery(id+"F0.wireOp",EDGE,"073a8239-eeac-400b-97e6-9f9c82d259df.3.16.24"),sQuery(id+"F0.wireOp",EDGE,"073a8239-eeac-400b-97e6-9f9c82d259df.6.16.24"),sQuery(id+"F0.wireOp",EDGE,"073a8239-eeac-400b-97e6-9f9c82d259df.9.16.24"),sQuery(id+"F0.wireOp",EDGE,"073a8239-eeac-400b-97e6-9f9c82d259df.0.16.25"),sQuery(id+"F0.wireOp",EDGE,"073a8239-eeac-400b-97e6-9f9c82d259df.3.16.25"),sQuery(id+"F0.wireOp",EDGE,"073a8239-eeac-400b-97e6-9f9c82d259df.6.16.25"),sQuery(id+"F0.wireOp",EDGE,"073a8239-eeac-400b-97e6-9f9c82d259df.9.16.25"),sQuery(id+"F0.wireOp",EDGE,"073a8239-eeac-400b-97e6-9f9c82d259df.0.16.26"),sQuery(id+"F0.wireOp",EDGE,"073a8239-eeac-400b-97e6-9f9c82d259df.3.16.26"),sQuery(id+"F0.wireOp",EDGE,"073a8239-eeac-400b-97e6-9f9c82d259df.6.16.26"),sQuery(id+"F0.wireOp",EDGE,"073a8239-eeac-400b-97e6-9f9c82d259df.9.16.26"),sQuery(id+"F0.wireOp",EDGE,"073a8239-eeac-400b-97e6-9f9c82d259df.0.16.27"),sQuery(id+"F0.wireOp",EDGE,"073a8239-eeac-400b-97e6-9f9c82d259df.3.16.27"),sQuery(id+"F0.wireOp",EDGE,"073a8239-eeac-400b-97e6-9f9c82d259df.6.16.27"),sQuery(id+"F0.wireOp",EDGE,"073a8239-eeac-400b-97e6-9f9c82d259df.9.16.27"),sQuery(id+"F0.wireOp",EDGE,"073a8239-eeac-400b-97e6-9f9c82d259df.0.16.28"),sQuery(id+"F0.wireOp",EDGE,"073a8239-eeac-400b-97e6-9f9c82d259df.3.16.28"),sQuery(id+"F0.wireOp",EDGE,"073a8239-eeac-400b-97e6-9f9c82d259df.6.16.28"),sQuery(id+"F0.wireOp",EDGE,"073a8239-eeac-400b-97e6-9f9c82d259df.9.16.28"),sQuery(id+"F0.wireOp",EDGE,"073a8239-eeac-400b-97e6-9f9c82d259df.0.16.29"),sQuery(id+"F0.wireOp",EDGE,"073a8239-eeac-400b-97e6-9f9c82d259df.3.16.29"),sQuery(id+"F0.wireOp",EDGE,"073a8239-eeac-400b-97e6-9f9c82d259df.6.16.29"),sQuery(id+"F0.wireOp",EDGE,"073a8239-eeac-400b-97e6-9f9c82d259df.9.16.29"),sQuery(id+"F0.wireOp",EDGE,"073a8239-eeac-400b-97e6-9f9c82d259df.0.16.30"),sQuery(id+"F0.wireOp",EDGE,"073a8239-eeac-400b-97e6-9f9c82d259df.3.16.30"),sQuery(id+"F0.wireOp",EDGE,"073a8239-eeac-400b-97e6-9f9c82d259df.6.16.30"),sQuery(id+"F0.wireOp",EDGE,"073a8239-eeac-400b-97e6-9f9c82d259df.9.16.30"),sQuery(id+"F0.wireOp",EDGE,"073a8239-eeac-400b-97e6-9f9c82d259df.0.16.31"),sQuery(id+"F0.wireOp",EDGE,"073a8239-eeac-400b-97e6-9f9c82d259df.3.16.31"),sQuery(id+"F0.wireOp",EDGE,"073a8239-eeac-400b-97e6-9f9c82d259df.6.16.31"),sQuery(id+"F0.wireOp",EDGE,"073a8239-eeac-400b-97e6-9f9c82d259df.9.16.31"),sQuery(id+"F0.wireOp",EDGE,"073a8239-eeac-400b-97e6-9f9c82d259df.0.17.0"),sQuery(id+"F0.wireOp",EDGE,"073a8239-eeac-400b-97e6-9f9c82d259df.3.17.0"),sQuery(id+"F0.wireOp",EDGE,"073a8239-eeac-400b-97e6-9f9c82d259df.6.17.0"),sQuery(id+"F0.wireOp",EDGE,"073a8239-eeac-400b-97e6-9f9c82d259df.9.17.0"),sQuery(id+"F0.wireOp",EDGE,"073a8239-eeac-400b-97e6-9f9c82d259df.0.17.1"),sQuery(id+"F0.wireOp",EDGE,"073a8239-eeac-400b-97e6-9f9c82d259df.3.17.1"),sQuery(id+"F0.wireOp",EDGE,"073a8239-eeac-400b-97e6-9f9c82d259df.6.17.1"),sQuery(id+"F0.wireOp",EDGE,"073a8239-eeac-400b-97e6-9f9c82d259df.9.17.1"),sQuery(id+"F0.wireOp",EDGE,"073a8239-eeac-400b-97e6-9f9c82d259df.0.17.2"),sQuery(id+"F0.wireOp",EDGE,"073a8239-eeac-400b-97e6-9f9c82d259df.3.17.2"),sQuery(id+"F0.wireOp",EDGE,"073a8239-eeac-400b-97e6-9f9c82d259df.6.17.2"),sQuery(id+"F0.wireOp",EDGE,"073a8239-eeac-400b-97e6-9f9c82d259df.9.17.2"),sQuery(id+"F0.wireOp",EDGE,"073a8239-eeac-400b-97e6-9f9c82d259df.0.17.3"),sQuery(id+"F0.wireOp",EDGE,"073a8239-eeac-400b-97e6-9f9c82d259df.3.17.3"),sQuery(id+"F0.wireOp",EDGE,"073a8239-eeac-400b-97e6-9f9c82d259df.6.17.3"),sQuery(id+"F0.wireOp",EDGE,"073a8239-eeac-400b-97e6-9f9c82d259df.9.17.3"),sQuery(id+"F0.wireOp",EDGE,"073a8239-eeac-400b-97e6-9f9c82d259df.0.17.4"),sQuery(id+"F0.wireOp",EDGE,"073a8239-eeac-400b-97e6-9f9c82d259df.3.17.4"),sQuery(id+"F0.wireOp",EDGE,"073a8239-eeac-400b-97e6-9f9c82d259df.6.17.4"),sQuery(id+"F0.wireOp",EDGE,"073a8239-eeac-400b-97e6-9f9c82d259df.9.17.4"),sQuery(id+"F0.wireOp",EDGE,"073a8239-eeac-400b-97e6-9f9c82d259df.0.17.5"),sQuery(id+"F0.wireOp",EDGE,"073a8239-eeac-400b-97e6-9f9c82d259df.3.17.5"),sQuery(id+"F0.wireOp",EDGE,"073a8239-eeac-400b-97e6-9f9c82d259df.6.17.5"),sQuery(id+"F0.wireOp",EDGE,"073a8239-eeac-400b-97e6-9f9c82d259df.9.17.5"),sQuery(id+"F0.wireOp",EDGE,"073a8239-eeac-400b-97e6-9f9c82d259df.0.17.6"),sQuery(id+"F0.wireOp",EDGE,"073a8239-eeac-400b-97e6-9f9c82d259df.3.17.6"),sQuery(id+"F0.wireOp",EDGE,"073a8239-eeac-400b-97e6-9f9c82d259df.6.17.6"),sQuery(id+"F0.wireOp",EDGE,"073a8239-eeac-400b-97e6-9f9c82d259df.9.17.6"),sQuery(id+"F0.wireOp",EDGE,"073a8239-eeac-400b-97e6-9f9c82d259df.0.17.7"),sQuery(id+"F0.wireOp",EDGE,"073a8239-eeac-400b-97e6-9f9c82d259df.3.17.7"),sQuery(id+"F0.wireOp",EDGE,"073a8239-eeac-400b-97e6-9f9c82d259df.6.17.7"),sQuery(id+"F0.wireOp",EDGE,"073a8239-eeac-400b-97e6-9f9c82d259df.9.17.7"),sQuery(id+"F0.wireOp",EDGE,"073a8239-eeac-400b-97e6-9f9c82d259df.0.17.8"),sQuery(id+"F0.wireOp",EDGE,"073a8239-eeac-400b-97e6-9f9c82d259df.3.17.8"),sQuery(id+"F0.wireOp",EDGE,"073a8239-eeac-400b-97e6-9f9c82d259df.6.17.8"),sQuery(id+"F0.wireOp",EDGE,"073a8239-eeac-400b-97e6-9f9c82d259df.9.17.8"),sQuery(id+"F0.wireOp",EDGE,"073a8239-eeac-400b-97e6-9f9c82d259df.0.17.9"),sQuery(id+"F0.wireOp",EDGE,"073a8239-eeac-400b-97e6-9f9c82d259df.3.17.9"),sQuery(id+"F0.wireOp",EDGE,"073a8239-eeac-400b-97e6-9f9c82d259df.6.17.9"),sQuery(id+"F0.wireOp",EDGE,"073a8239-eeac-400b-97e6-9f9c82d259df.9.17.9"),sQuery(id+"F0.wireOp",EDGE,"073a8239-eeac-400b-97e6-9f9c82d259df.0.17.10"),sQuery(id+"F0.wireOp",EDGE,"073a8239-eeac-400b-97e6-9f9c82d259df.3.17.10"),sQuery(id+"F0.wireOp",EDGE,"073a8239-eeac-400b-97e6-9f9c82d259df.6.17.10"),sQuery(id+"F0.wireOp",EDGE,"073a8239-eeac-400b-97e6-9f9c82d259df.9.17.10"),sQuery(id+"F0.wireOp",EDGE,"073a8239-eeac-400b-97e6-9f9c82d259df.0.17.11"),sQuery(id+"F0.wireOp",EDGE,"073a8239-eeac-400b-97e6-9f9c82d259df.3.17.11"),sQuery(id+"F0.wireOp",EDGE,"073a8239-eeac-400b-97e6-9f9c82d259df.6.17.11"),sQuery(id+"F0.wireOp",EDGE,"073a8239-eeac-400b-97e6-9f9c82d259df.9.17.11"),sQuery(id+"F0.wireOp",EDGE,"073a8239-eeac-400b-97e6-9f9c82d259df.0.17.12"),sQuery(id+"F0.wireOp",EDGE,"073a8239-eeac-400b-97e6-9f9c82d259df.3.17.12"),sQuery(id+"F0.wireOp",EDGE,"073a8239-eeac-400b-97e6-9f9c82d259df.6.17.12"),sQuery(id+"F0.wireOp",EDGE,"073a8239-eeac-400b-97e6-9f9c82d259df.9.17.12"),sQuery(id+"F0.wireOp",EDGE,"073a8239-eeac-400b-97e6-9f9c82d259df.0.17.13"),sQuery(id+"F0.wireOp",EDGE,"073a8239-eeac-400b-97e6-9f9c82d259df.3.17.13"),sQuery(id+"F0.wireOp",EDGE,"073a8239-eeac-400b-97e6-9f9c82d259df.6.17.13"),sQuery(id+"F0.wireOp",EDGE,"073a8239-eeac-400b-97e6-9f9c82d259df.9.17.13"),sQuery(id+"F0.wireOp",EDGE,"073a8239-eeac-400b-97e6-9f9c82d259df.0.17.14"),sQuery(id+"F0.wireOp",EDGE,"073a8239-eeac-400b-97e6-9f9c82d259df.3.17.14"),sQuery(id+"F0.wireOp",EDGE,"073a8239-eeac-400b-97e6-9f9c82d259df.6.17.14"),sQuery(id+"F0.wireOp",EDGE,"073a8239-eeac-400b-97e6-9f9c82d259df.9.17.14"),sQuery(id+"F0.wireOp",EDGE,"073a8239-eeac-400b-97e6-9f9c82d259df.0.17.15"),sQuery(id+"F0.wireOp",EDGE,"073a8239-eeac-400b-97e6-9f9c82d259df.3.17.15"),sQuery(id+"F0.wireOp",EDGE,"073a8239-eeac-400b-97e6-9f9c82d259df.6.17.15"),sQuery(id+"F0.wireOp",EDGE,"073a8239-eeac-400b-97e6-9f9c82d259df.9.17.15"),sQuery(id+"F0.wireOp",EDGE,"073a8239-eeac-400b-97e6-9f9c82d259df.0.17.16"),sQuery(id+"F0.wireOp",EDGE,"073a8239-eeac-400b-97e6-9f9c82d259df.3.17.16"),sQuery(id+"F0.wireOp",EDGE,"073a8239-eeac-400b-97e6-9f9c82d259df.6.17.16"),sQuery(id+"F0.wireOp",EDGE,"073a8239-eeac-400b-97e6-9f9c82d259df.9.17.16"),sQuery(id+"F0.wireOp",EDGE,"073a8239-eeac-400b-97e6-9f9c82d259df.0.17.17"),sQuery(id+"F0.wireOp",EDGE,"073a8239-eeac-400b-97e6-9f9c82d259df.3.17.17"),sQuery(id+"F0.wireOp",EDGE,"073a8239-eeac-400b-97e6-9f9c82d259df.6.17.17"),sQuery(id+"F0.wireOp",EDGE,"073a8239-eeac-400b-97e6-9f9c82d259df.9.17.17"),sQuery(id+"F0.wireOp",EDGE,"073a8239-eeac-400b-97e6-9f9c82d259df.0.17.18"),sQuery(id+"F0.wireOp",EDGE,"073a8239-eeac-400b-97e6-9f9c82d259df.3.17.18"),sQuery(id+"F0.wireOp",EDGE,"073a8239-eeac-400b-97e6-9f9c82d259df.6.17.18"),sQuery(id+"F0.wireOp",EDGE,"073a8239-eeac-400b-97e6-9f9c82d259df.9.17.18"),sQuery(id+"F0.wireOp",EDGE,"073a8239-eeac-400b-97e6-9f9c82d259df.0.17.19"),sQuery(id+"F0.wireOp",EDGE,"073a8239-eeac-400b-97e6-9f9c82d259df.3.17.19"),sQuery(id+"F0.wireOp",EDGE,"073a8239-eeac-400b-97e6-9f9c82d259df.6.17.19"),sQuery(id+"F0.wireOp",EDGE,"073a8239-eeac-400b-97e6-9f9c82d259df.9.17.19"),sQuery(id+"F0.wireOp",EDGE,"073a8239-eeac-400b-97e6-9f9c82d259df.0.17.20"),sQuery(id+"F0.wireOp",EDGE,"073a8239-eeac-400b-97e6-9f9c82d259df.3.17.20"),sQuery(id+"F0.wireOp",EDGE,"073a8239-eeac-400b-97e6-9f9c82d259df.6.17.20"),sQuery(id+"F0.wireOp",EDGE,"073a8239-eeac-400b-97e6-9f9c82d259df.9.17.20"),sQuery(id+"F0.wireOp",EDGE,"073a8239-eeac-400b-97e6-9f9c82d259df.0.17.21"),sQuery(id+"F0.wireOp",EDGE,"073a8239-eeac-400b-97e6-9f9c82d259df.3.17.21"),sQuery(id+"F0.wireOp",EDGE,"073a8239-eeac-400b-97e6-9f9c82d259df.6.17.21"),sQuery(id+"F0.wireOp",EDGE,"073a8239-eeac-400b-97e6-9f9c82d259df.9.17.21"),sQuery(id+"F0.wireOp",EDGE,"073a8239-eeac-400b-97e6-9f9c82d259df.0.17.22"),sQuery(id+"F0.wireOp",EDGE,"073a8239-eeac-400b-97e6-9f9c82d259df.3.17.22"),sQuery(id+"F0.wireOp",EDGE,"073a8239-eeac-400b-97e6-9f9c82d259df.6.17.22"),sQuery(id+"F0.wireOp",EDGE,"073a8239-eeac-400b-97e6-9f9c82d259df.9.17.22"),sQuery(id+"F0.wireOp",EDGE,"073a8239-eeac-400b-97e6-9f9c82d259df.0.17.23"),sQuery(id+"F0.wireOp",EDGE,"073a8239-eeac-400b-97e6-9f9c82d259df.3.17.23"),sQuery(id+"F0.wireOp",EDGE,"073a8239-eeac-400b-97e6-9f9c82d259df.6.17.23"),sQuery(id+"F0.wireOp",EDGE,"073a8239-eeac-400b-97e6-9f9c82d259df.9.17.23"),sQuery(id+"F0.wireOp",EDGE,"073a8239-eeac-400b-97e6-9f9c82d259df.0.17.24"),sQuery(id+"F0.wireOp",EDGE,"073a8239-eeac-400b-97e6-9f9c82d259df.3.17.24"),sQuery(id+"F0.wireOp",EDGE,"073a8239-eeac-400b-97e6-9f9c82d259df.6.17.24"),sQuery(id+"F0.wireOp",EDGE,"073a8239-eeac-400b-97e6-9f9c82d259df.9.17.24"),sQuery(id+"F0.wireOp",EDGE,"073a8239-eeac-400b-97e6-9f9c82d259df.0.17.25"),sQuery(id+"F0.wireOp",EDGE,"073a8239-eeac-400b-97e6-9f9c82d259df.3.17.25"),sQuery(id+"F0.wireOp",EDGE,"073a8239-eeac-400b-97e6-9f9c82d259df.6.17.25"),sQuery(id+"F0.wireOp",EDGE,"073a8239-eeac-400b-97e6-9f9c82d259df.9.17.25"),sQuery(id+"F0.wireOp",EDGE,"073a8239-eeac-400b-97e6-9f9c82d259df.0.17.26"),sQuery(id+"F0.wireOp",EDGE,"073a8239-eeac-400b-97e6-9f9c82d259df.3.17.26"),sQuery(id+"F0.wireOp",EDGE,"073a8239-eeac-400b-97e6-9f9c82d259df.6.17.26"),sQuery(id+"F0.wireOp",EDGE,"073a8239-eeac-400b-97e6-9f9c82d259df.9.17.26"),sQuery(id+"F0.wireOp",EDGE,"073a8239-eeac-400b-97e6-9f9c82d259df.0.17.27"),sQuery(id+"F0.wireOp",EDGE,"073a8239-eeac-400b-97e6-9f9c82d259df.3.17.27"),sQuery(id+"F0.wireOp",EDGE,"073a8239-eeac-400b-97e6-9f9c82d259df.6.17.27"),sQuery(id+"F0.wireOp",EDGE,"073a8239-eeac-400b-97e6-9f9c82d259df.9.17.27"),sQuery(id+"F0.wireOp",EDGE,"073a8239-eeac-400b-97e6-9f9c82d259df.0.17.28"),sQuery(id+"F0.wireOp",EDGE,"073a8239-eeac-400b-97e6-9f9c82d259df.3.17.28"),sQuery(id+"F0.wireOp",EDGE,"073a8239-eeac-400b-97e6-9f9c82d259df.6.17.28"),sQuery(id+"F0.wireOp",EDGE,"073a8239-eeac-400b-97e6-9f9c82d259df.9.17.28"),sQuery(id+"F0.wireOp",EDGE,"073a8239-eeac-400b-97e6-9f9c82d259df.0.17.29"),sQuery(id+"F0.wireOp",EDGE,"073a8239-eeac-400b-97e6-9f9c82d259df.3.17.29"),sQuery(id+"F0.wireOp",EDGE,"073a8239-eeac-400b-97e6-9f9c82d259df.6.17.29"),sQuery(id+"F0.wireOp",EDGE,"073a8239-eeac-400b-97e6-9f9c82d259df.9.17.29"),sQuery(id+"F0.wireOp",EDGE,"073a8239-eeac-400b-97e6-9f9c82d259df.0.17.30"),sQuery(id+"F0.wireOp",EDGE,"073a8239-eeac-400b-97e6-9f9c82d259df.3.17.30"),sQuery(id+"F0.wireOp",EDGE,"073a8239-eeac-400b-97e6-9f9c82d259df.6.17.30"),sQuery(id+"F0.wireOp",EDGE,"073a8239-eeac-400b-97e6-9f9c82d259df.9.17.30"),sQuery(id+"F0.wireOp",EDGE,"073a8239-eeac-400b-97e6-9f9c82d259df.0.17.31"),sQuery(id+"F0.wireOp",EDGE,"073a8239-eeac-400b-97e6-9f9c82d259df.3.17.31"),sQuery(id+"F0.wireOp",EDGE,"073a8239-eeac-400b-97e6-9f9c82d259df.6.17.31"),sQuery(id+"F0.wireOp",EDGE,"073a8239-eeac-400b-97e6-9f9c82d259df.9.17.31"),sQuery(id+"F0.wireOp",EDGE,"073a8239-eeac-400b-97e6-9f9c82d259df.0.18.0"),sQuery(id+"F0.wireOp",EDGE,"073a8239-eeac-400b-97e6-9f9c82d259df.3.18.0"),sQuery(id+"F0.wireOp",EDGE,"073a8239-eeac-400b-97e6-9f9c82d259df.6.18.0"),sQuery(id+"F0.wireOp",EDGE,"073a8239-eeac-400b-97e6-9f9c82d259df.9.18.0"),sQuery(id+"F0.wireOp",EDGE,"073a8239-eeac-400b-97e6-9f9c82d259df.0.18.1"),sQuery(id+"F0.wireOp",EDGE,"073a8239-eeac-400b-97e6-9f9c82d259df.3.18.1"),sQuery(id+"F0.wireOp",EDGE,"073a8239-eeac-400b-97e6-9f9c82d259df.6.18.1"),sQuery(id+"F0.wireOp",EDGE,"073a8239-eeac-400b-97e6-9f9c82d259df.9.18.1"),sQuery(id+"F0.wireOp",EDGE,"073a8239-eeac-400b-97e6-9f9c82d259df.0.18.2"),sQuery(id+"F0.wireOp",EDGE,"073a8239-eeac-400b-97e6-9f9c82d259df.3.18.2"),sQuery(id+"F0.wireOp",EDGE,"073a8239-eeac-400b-97e6-9f9c82d259df.6.18.2"),sQuery(id+"F0.wireOp",EDGE,"073a8239-eeac-400b-97e6-9f9c82d259df.9.18.2"),sQuery(id+"F0.wireOp",EDGE,"073a8239-eeac-400b-97e6-9f9c82d259df.0.18.3"),sQuery(id+"F0.wireOp",EDGE,"073a8239-eeac-400b-97e6-9f9c82d259df.3.18.3"),sQuery(id+"F0.wireOp",EDGE,"073a8239-eeac-400b-97e6-9f9c82d259df.6.18.3"),sQuery(id+"F0.wireOp",EDGE,"073a8239-eeac-400b-97e6-9f9c82d259df.9.18.3"),sQuery(id+"F0.wireOp",EDGE,"073a8239-eeac-400b-97e6-9f9c82d259df.0.18.4"),sQuery(id+"F0.wireOp",EDGE,"073a8239-eeac-400b-97e6-9f9c82d259df.3.18.4"),sQuery(id+"F0.wireOp",EDGE,"073a8239-eeac-400b-97e6-9f9c82d259df.6.18.4"),sQuery(id+"F0.wireOp",EDGE,"073a8239-eeac-400b-97e6-9f9c82d259df.9.18.4"),sQuery(id+"F0.wireOp",EDGE,"073a8239-eeac-400b-97e6-9f9c82d259df.0.18.5"),sQuery(id+"F0.wireOp",EDGE,"073a8239-eeac-400b-97e6-9f9c82d259df.3.18.5"),sQuery(id+"F0.wireOp",EDGE,"073a8239-eeac-400b-97e6-9f9c82d259df.6.18.5"),sQuery(id+"F0.wireOp",EDGE,"073a8239-eeac-400b-97e6-9f9c82d259df.9.18.5"),sQuery(id+"F0.wireOp",EDGE,"073a8239-eeac-400b-97e6-9f9c82d259df.0.18.6"),sQuery(id+"F0.wireOp",EDGE,"073a8239-eeac-400b-97e6-9f9c82d259df.3.18.6"),sQuery(id+"F0.wireOp",EDGE,"073a8239-eeac-400b-97e6-9f9c82d259df.6.18.6"),sQuery(id+"F0.wireOp",EDGE,"073a8239-eeac-400b-97e6-9f9c82d259df.9.18.6"),sQuery(id+"F0.wireOp",EDGE,"073a8239-eeac-400b-97e6-9f9c82d259df.0.18.7"),sQuery(id+"F0.wireOp",EDGE,"073a8239-eeac-400b-97e6-9f9c82d259df.3.18.7"),sQuery(id+"F0.wireOp",EDGE,"073a8239-eeac-400b-97e6-9f9c82d259df.6.18.7"),sQuery(id+"F0.wireOp",EDGE,"073a8239-eeac-400b-97e6-9f9c82d259df.9.18.7"),sQuery(id+"F0.wireOp",EDGE,"073a8239-eeac-400b-97e6-9f9c82d259df.0.18.8"),sQuery(id+"F0.wireOp",EDGE,"073a8239-eeac-400b-97e6-9f9c82d259df.3.18.8"),sQuery(id+"F0.wireOp",EDGE,"073a8239-eeac-400b-97e6-9f9c82d259df.6.18.8"),sQuery(id+"F0.wireOp",EDGE,"073a8239-eeac-400b-97e6-9f9c82d259df.9.18.8"),sQuery(id+"F0.wireOp",EDGE,"073a8239-eeac-400b-97e6-9f9c82d259df.0.18.9"),sQuery(id+"F0.wireOp",EDGE,"073a8239-eeac-400b-97e6-9f9c82d259df.3.18.9"),sQuery(id+"F0.wireOp",EDGE,"073a8239-eeac-400b-97e6-9f9c82d259df.6.18.9"),sQuery(id+"F0.wireOp",EDGE,"073a8239-eeac-400b-97e6-9f9c82d259df.9.18.9"),sQuery(id+"F0.wireOp",EDGE,"073a8239-eeac-400b-97e6-9f9c82d259df.0.18.10"),sQuery(id+"F0.wireOp",EDGE,"073a8239-eeac-400b-97e6-9f9c82d259df.3.18.10"),sQuery(id+"F0.wireOp",EDGE,"073a8239-eeac-400b-97e6-9f9c82d259df.6.18.10"),sQuery(id+"F0.wireOp",EDGE,"073a8239-eeac-400b-97e6-9f9c82d259df.9.18.10"),sQuery(id+"F0.wireOp",EDGE,"073a8239-eeac-400b-97e6-9f9c82d259df.0.18.11"),sQuery(id+"F0.wireOp",EDGE,"073a8239-eeac-400b-97e6-9f9c82d259df.3.18.11"),sQuery(id+"F0.wireOp",EDGE,"073a8239-eeac-400b-97e6-9f9c82d259df.6.18.11"),sQuery(id+"F0.wireOp",EDGE,"073a8239-eeac-400b-97e6-9f9c82d259df.9.18.11"),sQuery(id+"F0.wireOp",EDGE,"073a8239-eeac-400b-97e6-9f9c82d259df.0.18.12"),sQuery(id+"F0.wireOp",EDGE,"073a8239-eeac-400b-97e6-9f9c82d259df.3.18.12"),sQuery(id+"F0.wireOp",EDGE,"073a8239-eeac-400b-97e6-9f9c82d259df.6.18.12"),sQuery(id+"F0.wireOp",EDGE,"073a8239-eeac-400b-97e6-9f9c82d259df.9.18.12"),sQuery(id+"F0.wireOp",EDGE,"073a8239-eeac-400b-97e6-9f9c82d259df.0.18.13"),sQuery(id+"F0.wireOp",EDGE,"073a8239-eeac-400b-97e6-9f9c82d259df.3.18.13"),sQuery(id+"F0.wireOp",EDGE,"073a8239-eeac-400b-97e6-9f9c82d259df.6.18.13"),sQuery(id+"F0.wireOp",EDGE,"073a8239-eeac-400b-97e6-9f9c82d259df.9.18.13"),sQuery(id+"F0.wireOp",EDGE,"073a8239-eeac-400b-97e6-9f9c82d259df.0.18.14"),sQuery(id+"F0.wireOp",EDGE,"073a8239-eeac-400b-97e6-9f9c82d259df.3.18.14"),sQuery(id+"F0.wireOp",EDGE,"073a8239-eeac-400b-97e6-9f9c82d259df.6.18.14"),sQuery(id+"F0.wireOp",EDGE,"073a8239-eeac-400b-97e6-9f9c82d259df.9.18.14"),sQuery(id+"F0.wireOp",EDGE,"073a8239-eeac-400b-97e6-9f9c82d259df.0.18.15"),sQuery(id+"F0.wireOp",EDGE,"073a8239-eeac-400b-97e6-9f9c82d259df.3.18.15"),sQuery(id+"F0.wireOp",EDGE,"073a8239-eeac-400b-97e6-9f9c82d259df.6.18.15"),sQuery(id+"F0.wireOp",EDGE,"073a8239-eeac-400b-97e6-9f9c82d259df.9.18.15"),sQuery(id+"F0.wireOp",EDGE,"073a8239-eeac-400b-97e6-9f9c82d259df.0.18.16"),sQuery(id+"F0.wireOp",EDGE,"073a8239-eeac-400b-97e6-9f9c82d259df.3.18.16"),sQuery(id+"F0.wireOp",EDGE,"073a8239-eeac-400b-97e6-9f9c82d259df.6.18.16"),sQuery(id+"F0.wireOp",EDGE,"073a8239-eeac-400b-97e6-9f9c82d259df.9.18.16"),sQuery(id+"F0.wireOp",EDGE,"073a8239-eeac-400b-97e6-9f9c82d259df.0.18.17"),sQuery(id+"F0.wireOp",EDGE,"073a8239-eeac-400b-97e6-9f9c82d259df.3.18.17"),sQuery(id+"F0.wireOp",EDGE,"073a8239-eeac-400b-97e6-9f9c82d259df.6.18.17"),sQuery(id+"F0.wireOp",EDGE,"073a8239-eeac-400b-97e6-9f9c82d259df.9.18.17"),sQuery(id+"F0.wireOp",EDGE,"073a8239-eeac-400b-97e6-9f9c82d259df.0.18.18"),sQuery(id+"F0.wireOp",EDGE,"073a8239-eeac-400b-97e6-9f9c82d259df.3.18.18"),sQuery(id+"F0.wireOp",EDGE,"073a8239-eeac-400b-97e6-9f9c82d259df.6.18.18"),sQuery(id+"F0.wireOp",EDGE,"073a8239-eeac-400b-97e6-9f9c82d259df.9.18.18"),sQuery(id+"F0.wireOp",EDGE,"073a8239-eeac-400b-97e6-9f9c82d259df.0.18.19"),sQuery(id+"F0.wireOp",EDGE,"073a8239-eeac-400b-97e6-9f9c82d259df.3.18.19"),sQuery(id+"F0.wireOp",EDGE,"073a8239-eeac-400b-97e6-9f9c82d259df.6.18.19"),sQuery(id+"F0.wireOp",EDGE,"073a8239-eeac-400b-97e6-9f9c82d259df.9.18.19"),sQuery(id+"F0.wireOp",EDGE,"073a8239-eeac-400b-97e6-9f9c82d259df.0.18.20"),sQuery(id+"F0.wireOp",EDGE,"073a8239-eeac-400b-97e6-9f9c82d259df.3.18.20"),sQuery(id+"F0.wireOp",EDGE,"073a8239-eeac-400b-97e6-9f9c82d259df.6.18.20"),sQuery(id+"F0.wireOp",EDGE,"073a8239-eeac-400b-97e6-9f9c82d259df.9.18.20"),sQuery(id+"F0.wireOp",EDGE,"073a8239-eeac-400b-97e6-9f9c82d259df.0.18.21"),sQuery(id+"F0.wireOp",EDGE,"073a8239-eeac-400b-97e6-9f9c82d259df.3.18.21"),sQuery(id+"F0.wireOp",EDGE,"073a8239-eeac-400b-97e6-9f9c82d259df.6.18.21"),sQuery(id+"F0.wireOp",EDGE,"073a8239-eeac-400b-97e6-9f9c82d259df.9.18.21"),sQuery(id+"F0.wireOp",EDGE,"073a8239-eeac-400b-97e6-9f9c82d259df.0.18.22"),sQuery(id+"F0.wireOp",EDGE,"073a8239-eeac-400b-97e6-9f9c82d259df.3.18.22"),sQuery(id+"F0.wireOp",EDGE,"073a8239-eeac-400b-97e6-9f9c82d259df.6.18.22"),sQuery(id+"F0.wireOp",EDGE,"073a8239-eeac-400b-97e6-9f9c82d259df.9.18.22"),sQuery(id+"F0.wireOp",EDGE,"073a8239-eeac-400b-97e6-9f9c82d259df.0.18.23"),sQuery(id+"F0.wireOp",EDGE,"073a8239-eeac-400b-97e6-9f9c82d259df.3.18.23"),sQuery(id+"F0.wireOp",EDGE,"073a8239-eeac-400b-97e6-9f9c82d259df.6.18.23"),sQuery(id+"F0.wireOp",EDGE,"073a8239-eeac-400b-97e6-9f9c82d259df.9.18.23"),sQuery(id+"F0.wireOp",EDGE,"073a8239-eeac-400b-97e6-9f9c82d259df.0.18.24"),sQuery(id+"F0.wireOp",EDGE,"073a8239-eeac-400b-97e6-9f9c82d259df.3.18.24"),sQuery(id+"F0.wireOp",EDGE,"073a8239-eeac-400b-97e6-9f9c82d259df.6.18.24"),sQuery(id+"F0.wireOp",EDGE,"073a8239-eeac-400b-97e6-9f9c82d259df.9.18.24"),sQuery(id+"F0.wireOp",EDGE,"073a8239-eeac-400b-97e6-9f9c82d259df.0.18.25"),sQuery(id+"F0.wireOp",EDGE,"073a8239-eeac-400b-97e6-9f9c82d259df.3.18.25"),sQuery(id+"F0.wireOp",EDGE,"073a8239-eeac-400b-97e6-9f9c82d259df.6.18.25"),sQuery(id+"F0.wireOp",EDGE,"073a8239-eeac-400b-97e6-9f9c82d259df.9.18.25"),sQuery(id+"F0.wireOp",EDGE,"073a8239-eeac-400b-97e6-9f9c82d259df.0.18.26"),sQuery(id+"F0.wireOp",EDGE,"073a8239-eeac-400b-97e6-9f9c82d259df.3.18.26"),sQuery(id+"F0.wireOp",EDGE,"073a8239-eeac-400b-97e6-9f9c82d259df.6.18.26"),sQuery(id+"F0.wireOp",EDGE,"073a8239-eeac-400b-97e6-9f9c82d259df.9.18.26"),sQuery(id+"F0.wireOp",EDGE,"073a8239-eeac-400b-97e6-9f9c82d259df.0.18.27"),sQuery(id+"F0.wireOp",EDGE,"073a8239-eeac-400b-97e6-9f9c82d259df.3.18.27"),sQuery(id+"F0.wireOp",EDGE,"073a8239-eeac-400b-97e6-9f9c82d259df.6.18.27"),sQuery(id+"F0.wireOp",EDGE,"073a8239-eeac-400b-97e6-9f9c82d259df.9.18.27"),sQuery(id+"F0.wireOp",EDGE,"073a8239-eeac-400b-97e6-9f9c82d259df.0.18.28"),sQuery(id+"F0.wireOp",EDGE,"073a8239-eeac-400b-97e6-9f9c82d259df.3.18.28"),sQuery(id+"F0.wireOp",EDGE,"073a8239-eeac-400b-97e6-9f9c82d259df.6.18.28"),sQuery(id+"F0.wireOp",EDGE,"073a8239-eeac-400b-97e6-9f9c82d259df.9.18.28"),sQuery(id+"F0.wireOp",EDGE,"073a8239-eeac-400b-97e6-9f9c82d259df.0.18.29"),sQuery(id+"F0.wireOp",EDGE,"073a8239-eeac-400b-97e6-9f9c82d259df.3.18.29"),sQuery(id+"F0.wireOp",EDGE,"073a8239-eeac-400b-97e6-9f9c82d259df.6.18.29"),sQuery(id+"F0.wireOp",EDGE,"073a8239-eeac-400b-97e6-9f9c82d259df.9.18.29"),sQuery(id+"F0.wireOp",EDGE,"073a8239-eeac-400b-97e6-9f9c82d259df.0.18.30"),sQuery(id+"F0.wireOp",EDGE,"073a8239-eeac-400b-97e6-9f9c82d259df.3.18.30"),sQuery(id+"F0.wireOp",EDGE,"073a8239-eeac-400b-97e6-9f9c82d259df.6.18.30"),sQuery(id+"F0.wireOp",EDGE,"073a8239-eeac-400b-97e6-9f9c82d259df.9.18.30"),sQuery(id+"F0.wireOp",EDGE,"073a8239-eeac-400b-97e6-9f9c82d259df.0.18.31"),sQuery(id+"F0.wireOp",EDGE,"073a8239-eeac-400b-97e6-9f9c82d259df.3.18.31"),sQuery(id+"F0.wireOp",EDGE,"073a8239-eeac-400b-97e6-9f9c82d259df.6.18.31"),sQuery(id+"F0.wireOp",EDGE,"073a8239-eeac-400b-97e6-9f9c82d259df.9.18.31"),sQuery(id+"F0.wireOp",EDGE,"073a8239-eeac-400b-97e6-9f9c82d259df.0.19.0"),sQuery(id+"F0.wireOp",EDGE,"073a8239-eeac-400b-97e6-9f9c82d259df.3.19.0"),sQuery(id+"F0.wireOp",EDGE,"073a8239-eeac-400b-97e6-9f9c82d259df.6.19.0"),sQuery(id+"F0.wireOp",EDGE,"073a8239-eeac-400b-97e6-9f9c82d259df.9.19.0"),sQuery(id+"F0.wireOp",EDGE,"073a8239-eeac-400b-97e6-9f9c82d259df.0.19.1"),sQuery(id+"F0.wireOp",EDGE,"073a8239-eeac-400b-97e6-9f9c82d259df.3.19.1"),sQuery(id+"F0.wireOp",EDGE,"073a8239-eeac-400b-97e6-9f9c82d259df.6.19.1"),sQuery(id+"F0.wireOp",EDGE,"073a8239-eeac-400b-97e6-9f9c82d259df.9.19.1"),sQuery(id+"F0.wireOp",EDGE,"073a8239-eeac-400b-97e6-9f9c82d259df.0.19.2"),sQuery(id+"F0.wireOp",EDGE,"073a8239-eeac-400b-97e6-9f9c82d259df.3.19.2"),sQuery(id+"F0.wireOp",EDGE,"073a8239-eeac-400b-97e6-9f9c82d259df.6.19.2"),sQuery(id+"F0.wireOp",EDGE,"073a8239-eeac-400b-97e6-9f9c82d259df.9.19.2"),sQuery(id+"F0.wireOp",EDGE,"073a8239-eeac-400b-97e6-9f9c82d259df.0.19.3"),sQuery(id+"F0.wireOp",EDGE,"073a8239-eeac-400b-97e6-9f9c82d259df.3.19.3"),sQuery(id+"F0.wireOp",EDGE,"073a8239-eeac-400b-97e6-9f9c82d259df.6.19.3"),sQuery(id+"F0.wireOp",EDGE,"073a8239-eeac-400b-97e6-9f9c82d259df.9.19.3"),sQuery(id+"F0.wireOp",EDGE,"073a8239-eeac-400b-97e6-9f9c82d259df.0.19.4"),sQuery(id+"F0.wireOp",EDGE,"073a8239-eeac-400b-97e6-9f9c82d259df.3.19.4"),sQuery(id+"F0.wireOp",EDGE,"073a8239-eeac-400b-97e6-9f9c82d259df.6.19.4"),sQuery(id+"F0.wireOp",EDGE,"073a8239-eeac-400b-97e6-9f9c82d259df.9.19.4"),sQuery(id+"F0.wireOp",EDGE,"073a8239-eeac-400b-97e6-9f9c82d259df.0.19.5"),sQuery(id+"F0.wireOp",EDGE,"073a8239-eeac-400b-97e6-9f9c82d259df.3.19.5"),sQuery(id+"F0.wireOp",EDGE,"073a8239-eeac-400b-97e6-9f9c82d259df.6.19.5"),sQuery(id+"F0.wireOp",EDGE,"073a8239-eeac-400b-97e6-9f9c82d259df.9.19.5"),sQuery(id+"F0.wireOp",EDGE,"073a8239-eeac-400b-97e6-9f9c82d259df.0.19.6"),sQuery(id+"F0.wireOp",EDGE,"073a8239-eeac-400b-97e6-9f9c82d259df.3.19.6"),sQuery(id+"F0.wireOp",EDGE,"073a8239-eeac-400b-97e6-9f9c82d259df.6.19.6"),sQuery(id+"F0.wireOp",EDGE,"073a8239-eeac-400b-97e6-9f9c82d259df.9.19.6"),sQuery(id+"F0.wireOp",EDGE,"073a8239-eeac-400b-97e6-9f9c82d259df.0.19.7"),sQuery(id+"F0.wireOp",EDGE,"073a8239-eeac-400b-97e6-9f9c82d259df.3.19.7"),sQuery(id+"F0.wireOp",EDGE,"073a8239-eeac-400b-97e6-9f9c82d259df.6.19.7"),sQuery(id+"F0.wireOp",EDGE,"073a8239-eeac-400b-97e6-9f9c82d259df.9.19.7"),sQuery(id+"F0.wireOp",EDGE,"073a8239-eeac-400b-97e6-9f9c82d259df.0.19.8"),sQuery(id+"F0.wireOp",EDGE,"073a8239-eeac-400b-97e6-9f9c82d259df.3.19.8"),sQuery(id+"F0.wireOp",EDGE,"073a8239-eeac-400b-97e6-9f9c82d259df.6.19.8"),sQuery(id+"F0.wireOp",EDGE,"073a8239-eeac-400b-97e6-9f9c82d259df.9.19.8"),sQuery(id+"F0.wireOp",EDGE,"073a8239-eeac-400b-97e6-9f9c82d259df.0.19.9"),sQuery(id+"F0.wireOp",EDGE,"073a8239-eeac-400b-97e6-9f9c82d259df.3.19.9"),sQuery(id+"F0.wireOp",EDGE,"073a8239-eeac-400b-97e6-9f9c82d259df.6.19.9"),sQuery(id+"F0.wireOp",EDGE,"073a8239-eeac-400b-97e6-9f9c82d259df.9.19.9"),sQuery(id+"F0.wireOp",EDGE,"073a8239-eeac-400b-97e6-9f9c82d259df.0.19.10"),sQuery(id+"F0.wireOp",EDGE,"073a8239-eeac-400b-97e6-9f9c82d259df.3.19.10"),sQuery(id+"F0.wireOp",EDGE,"073a8239-eeac-400b-97e6-9f9c82d259df.6.19.10"),sQuery(id+"F0.wireOp",EDGE,"073a8239-eeac-400b-97e6-9f9c82d259df.9.19.10"),sQuery(id+"F0.wireOp",EDGE,"073a8239-eeac-400b-97e6-9f9c82d259df.0.19.11"),sQuery(id+"F0.wireOp",EDGE,"073a8239-eeac-400b-97e6-9f9c82d259df.3.19.11"),sQuery(id+"F0.wireOp",EDGE,"073a8239-eeac-400b-97e6-9f9c82d259df.6.19.11"),sQuery(id+"F0.wireOp",EDGE,"073a8239-eeac-400b-97e6-9f9c82d259df.9.19.11"),sQuery(id+"F0.wireOp",EDGE,"073a8239-eeac-400b-97e6-9f9c82d259df.0.19.12"),sQuery(id+"F0.wireOp",EDGE,"073a8239-eeac-400b-97e6-9f9c82d259df.3.19.12"),sQuery(id+"F0.wireOp",EDGE,"073a8239-eeac-400b-97e6-9f9c82d259df.6.19.12"),sQuery(id+"F0.wireOp",EDGE,"073a8239-eeac-400b-97e6-9f9c82d259df.9.19.12"),sQuery(id+"F0.wireOp",EDGE,"073a8239-eeac-400b-97e6-9f9c82d259df.0.19.13"),sQuery(id+"F0.wireOp",EDGE,"073a8239-eeac-400b-97e6-9f9c82d259df.3.19.13"),sQuery(id+"F0.wireOp",EDGE,"073a8239-eeac-400b-97e6-9f9c82d259df.6.19.13"),sQuery(id+"F0.wireOp",EDGE,"073a8239-eeac-400b-97e6-9f9c82d259df.9.19.13"),sQuery(id+"F0.wireOp",EDGE,"073a8239-eeac-400b-97e6-9f9c82d259df.0.19.14"),sQuery(id+"F0.wireOp",EDGE,"073a8239-eeac-400b-97e6-9f9c82d259df.3.19.14"),sQuery(id+"F0.wireOp",EDGE,"073a8239-eeac-400b-97e6-9f9c82d259df.6.19.14"),sQuery(id+"F0.wireOp",EDGE,"073a8239-eeac-400b-97e6-9f9c82d259df.9.19.14"),sQuery(id+"F0.wireOp",EDGE,"073a8239-eeac-400b-97e6-9f9c82d259df.0.19.15"),sQuery(id+"F0.wireOp",EDGE,"073a8239-eeac-400b-97e6-9f9c82d259df.3.19.15"),sQuery(id+"F0.wireOp",EDGE,"073a8239-eeac-400b-97e6-9f9c82d259df.6.19.15"),sQuery(id+"F0.wireOp",EDGE,"073a8239-eeac-400b-97e6-9f9c82d259df.9.19.15"),sQuery(id+"F0.wireOp",EDGE,"073a8239-eeac-400b-97e6-9f9c82d259df.0.19.16"),sQuery(id+"F0.wireOp",EDGE,"073a8239-eeac-400b-97e6-9f9c82d259df.3.19.16"),sQuery(id+"F0.wireOp",EDGE,"073a8239-eeac-400b-97e6-9f9c82d259df.6.19.16"),sQuery(id+"F0.wireOp",EDGE,"073a8239-eeac-400b-97e6-9f9c82d259df.9.19.16"),sQuery(id+"F0.wireOp",EDGE,"073a8239-eeac-400b-97e6-9f9c82d259df.0.19.17"),sQuery(id+"F0.wireOp",EDGE,"073a8239-eeac-400b-97e6-9f9c82d259df.3.19.17"),sQuery(id+"F0.wireOp",EDGE,"073a8239-eeac-400b-97e6-9f9c82d259df.6.19.17"),sQuery(id+"F0.wireOp",EDGE,"073a8239-eeac-400b-97e6-9f9c82d259df.9.19.17"),sQuery(id+"F0.wireOp",EDGE,"073a8239-eeac-400b-97e6-9f9c82d259df.0.19.18"),sQuery(id+"F0.wireOp",EDGE,"073a8239-eeac-400b-97e6-9f9c82d259df.3.19.18"),sQuery(id+"F0.wireOp",EDGE,"073a8239-eeac-400b-97e6-9f9c82d259df.6.19.18"),sQuery(id+"F0.wireOp",EDGE,"073a8239-eeac-400b-97e6-9f9c82d259df.9.19.18"),sQuery(id+"F0.wireOp",EDGE,"073a8239-eeac-400b-97e6-9f9c82d259df.0.19.19"),sQuery(id+"F0.wireOp",EDGE,"073a8239-eeac-400b-97e6-9f9c82d259df.3.19.19"),sQuery(id+"F0.wireOp",EDGE,"073a8239-eeac-400b-97e6-9f9c82d259df.6.19.19"),sQuery(id+"F0.wireOp",EDGE,"073a8239-eeac-400b-97e6-9f9c82d259df.9.19.19"),sQuery(id+"F0.wireOp",EDGE,"073a8239-eeac-400b-97e6-9f9c82d259df.0.19.20"),sQuery(id+"F0.wireOp",EDGE,"073a8239-eeac-400b-97e6-9f9c82d259df.3.19.20"),sQuery(id+"F0.wireOp",EDGE,"073a8239-eeac-400b-97e6-9f9c82d259df.6.19.20"),sQuery(id+"F0.wireOp",EDGE,"073a8239-eeac-400b-97e6-9f9c82d259df.9.19.20"),sQuery(id+"F0.wireOp",EDGE,"073a8239-eeac-400b-97e6-9f9c82d259df.0.19.21"),sQuery(id+"F0.wireOp",EDGE,"073a8239-eeac-400b-97e6-9f9c82d259df.3.19.21"),sQuery(id+"F0.wireOp",EDGE,"073a8239-eeac-400b-97e6-9f9c82d259df.6.19.21"),sQuery(id+"F0.wireOp",EDGE,"073a8239-eeac-400b-97e6-9f9c82d259df.9.19.21"),sQuery(id+"F0.wireOp",EDGE,"073a8239-eeac-400b-97e6-9f9c82d259df.0.19.22"),sQuery(id+"F0.wireOp",EDGE,"073a8239-eeac-400b-97e6-9f9c82d259df.3.19.22"),sQuery(id+"F0.wireOp",EDGE,"073a8239-eeac-400b-97e6-9f9c82d259df.6.19.22"),sQuery(id+"F0.wireOp",EDGE,"073a8239-eeac-400b-97e6-9f9c82d259df.9.19.22"),sQuery(id+"F0.wireOp",EDGE,"073a8239-eeac-400b-97e6-9f9c82d259df.0.19.23"),sQuery(id+"F0.wireOp",EDGE,"073a8239-eeac-400b-97e6-9f9c82d259df.3.19.23"),sQuery(id+"F0.wireOp",EDGE,"073a8239-eeac-400b-97e6-9f9c82d259df.6.19.23"),sQuery(id+"F0.wireOp",EDGE,"073a8239-eeac-400b-97e6-9f9c82d259df.9.19.23"),sQuery(id+"F0.wireOp",EDGE,"073a8239-eeac-400b-97e6-9f9c82d259df.0.19.24"),sQuery(id+"F0.wireOp",EDGE,"073a8239-eeac-400b-97e6-9f9c82d259df.3.19.24"),sQuery(id+"F0.wireOp",EDGE,"073a8239-eeac-400b-97e6-9f9c82d259df.6.19.24"),sQuery(id+"F0.wireOp",EDGE,"073a8239-eeac-400b-97e6-9f9c82d259df.9.19.24"),sQuery(id+"F0.wireOp",EDGE,"073a8239-eeac-400b-97e6-9f9c82d259df.0.19.25"),sQuery(id+"F0.wireOp",EDGE,"073a8239-eeac-400b-97e6-9f9c82d259df.3.19.25"),sQuery(id+"F0.wireOp",EDGE,"073a8239-eeac-400b-97e6-9f9c82d259df.6.19.25"),sQuery(id+"F0.wireOp",EDGE,"073a8239-eeac-400b-97e6-9f9c82d259df.9.19.25"),sQuery(id+"F0.wireOp",EDGE,"073a8239-eeac-400b-97e6-9f9c82d259df.0.19.26"),sQuery(id+"F0.wireOp",EDGE,"073a8239-eeac-400b-97e6-9f9c82d259df.3.19.26"),sQuery(id+"F0.wireOp",EDGE,"073a8239-eeac-400b-97e6-9f9c82d259df.6.19.26"),sQuery(id+"F0.wireOp",EDGE,"073a8239-eeac-400b-97e6-9f9c82d259df.9.19.26"),sQuery(id+"F0.wireOp",EDGE,"073a8239-eeac-400b-97e6-9f9c82d259df.0.19.27"),sQuery(id+"F0.wireOp",EDGE,"073a8239-eeac-400b-97e6-9f9c82d259df.3.19.27"),sQuery(id+"F0.wireOp",EDGE,"073a8239-eeac-400b-97e6-9f9c82d259df.6.19.27"),sQuery(id+"F0.wireOp",EDGE,"073a8239-eeac-400b-97e6-9f9c82d259df.9.19.27"),sQuery(id+"F0.wireOp",EDGE,"073a8239-eeac-400b-97e6-9f9c82d259df.0.19.28"),sQuery(id+"F0.wireOp",EDGE,"073a8239-eeac-400b-97e6-9f9c82d259df.3.19.28"),sQuery(id+"F0.wireOp",EDGE,"073a8239-eeac-400b-97e6-9f9c82d259df.6.19.28"),sQuery(id+"F0.wireOp",EDGE,"073a8239-eeac-400b-97e6-9f9c82d259df.9.19.28"),sQuery(id+"F0.wireOp",EDGE,"073a8239-eeac-400b-97e6-9f9c82d259df.0.19.29"),sQuery(id+"F0.wireOp",EDGE,"073a8239-eeac-400b-97e6-9f9c82d259df.3.19.29"),sQuery(id+"F0.wireOp",EDGE,"073a8239-eeac-400b-97e6-9f9c82d259df.6.19.29"),sQuery(id+"F0.wireOp",EDGE,"073a8239-eeac-400b-97e6-9f9c82d259df.9.19.29"),sQuery(id+"F0.wireOp",EDGE,"073a8239-eeac-400b-97e6-9f9c82d259df.0.19.30"),sQuery(id+"F0.wireOp",EDGE,"073a8239-eeac-400b-97e6-9f9c82d259df.3.19.30"),sQuery(id+"F0.wireOp",EDGE,"073a8239-eeac-400b-97e6-9f9c82d259df.6.19.30"),sQuery(id+"F0.wireOp",EDGE,"073a8239-eeac-400b-97e6-9f9c82d259df.9.19.30"),sQuery(id+"F0.wireOp",EDGE,"073a8239-eeac-400b-97e6-9f9c82d259df.0.19.31"),sQuery(id+"F0.wireOp",EDGE,"073a8239-eeac-400b-97e6-9f9c82d259df.3.19.31"),sQuery(id+"F0.wireOp",EDGE,"073a8239-eeac-400b-97e6-9f9c82d259df.6.19.31"),sQuery(id+"F0.wireOp",EDGE,"073a8239-eeac-400b-97e6-9f9c82d259df.9.19.31"),sQuery(id+"F0.wireOp",EDGE,"afc6e781-25c3-4dd1-969d-5b2406180a6c.0.20.0"),sQuery(id+"F0.wireOp",EDGE,"afc6e781-25c3-4dd1-969d-5b2406180a6c.3.20.0"),sQuery(id+"F0.wireOp",EDGE,"afc6e781-25c3-4dd1-969d-5b2406180a6c.6.20.0"),sQuery(id+"F0.wireOp",EDGE,"afc6e781-25c3-4dd1-969d-5b2406180a6c.9.20.0"),sQuery(id+"F0.wireOp",EDGE,"afc6e781-25c3-4dd1-969d-5b2406180a6c.0.20.1"),sQuery(id+"F0.wireOp",EDGE,"afc6e781-25c3-4dd1-969d-5b2406180a6c.3.20.1"),sQuery(id+"F0.wireOp",EDGE,"afc6e781-25c3-4dd1-969d-5b2406180a6c.6.20.1"),sQuery(id+"F0.wireOp",EDGE,"afc6e781-25c3-4dd1-969d-5b2406180a6c.9.20.1"),sQuery(id+"F0.wireOp",EDGE,"afc6e781-25c3-4dd1-969d-5b2406180a6c.0.20.2"),sQuery(id+"F0.wireOp",EDGE,"afc6e781-25c3-4dd1-969d-5b2406180a6c.3.20.2"),sQuery(id+"F0.wireOp",EDGE,"afc6e781-25c3-4dd1-969d-5b2406180a6c.6.20.2"),sQuery(id+"F0.wireOp",EDGE,"afc6e781-25c3-4dd1-969d-5b2406180a6c.9.20.2"),sQuery(id+"F0.wireOp",EDGE,"afc6e781-25c3-4dd1-969d-5b2406180a6c.0.20.3"),sQuery(id+"F0.wireOp",EDGE,"afc6e781-25c3-4dd1-969d-5b2406180a6c.3.20.3"),sQuery(id+"F0.wireOp",EDGE,"afc6e781-25c3-4dd1-969d-5b2406180a6c.6.20.3"),sQuery(id+"F0.wireOp",EDGE,"afc6e781-25c3-4dd1-969d-5b2406180a6c.9.20.3"),sQuery(id+"F0.wireOp",EDGE,"afc6e781-25c3-4dd1-969d-5b2406180a6c.0.20.4"),sQuery(id+"F0.wireOp",EDGE,"afc6e781-25c3-4dd1-969d-5b2406180a6c.3.20.4"),sQuery(id+"F0.wireOp",EDGE,"afc6e781-25c3-4dd1-969d-5b2406180a6c.6.20.4"),sQuery(id+"F0.wireOp",EDGE,"afc6e781-25c3-4dd1-969d-5b2406180a6c.9.20.4"),sQuery(id+"F0.wireOp",EDGE,"afc6e781-25c3-4dd1-969d-5b2406180a6c.0.20.5"),sQuery(id+"F0.wireOp",EDGE,"afc6e781-25c3-4dd1-969d-5b2406180a6c.3.20.5"),sQuery(id+"F0.wireOp",EDGE,"afc6e781-25c3-4dd1-969d-5b2406180a6c.6.20.5"),sQuery(id+"F0.wireOp",EDGE,"afc6e781-25c3-4dd1-969d-5b2406180a6c.9.20.5"),sQuery(id+"F0.wireOp",EDGE,"afc6e781-25c3-4dd1-969d-5b2406180a6c.0.20.6"),sQuery(id+"F0.wireOp",EDGE,"afc6e781-25c3-4dd1-969d-5b2406180a6c.3.20.6"),sQuery(id+"F0.wireOp",EDGE,"afc6e781-25c3-4dd1-969d-5b2406180a6c.6.20.6"),sQuery(id+"F0.wireOp",EDGE,"afc6e781-25c3-4dd1-969d-5b2406180a6c.9.20.6"),sQuery(id+"F0.wireOp",EDGE,"afc6e781-25c3-4dd1-969d-5b2406180a6c.0.20.7"),sQuery(id+"F0.wireOp",EDGE,"afc6e781-25c3-4dd1-969d-5b2406180a6c.3.20.7"),sQuery(id+"F0.wireOp",EDGE,"afc6e781-25c3-4dd1-969d-5b2406180a6c.6.20.7"),sQuery(id+"F0.wireOp",EDGE,"afc6e781-25c3-4dd1-969d-5b2406180a6c.9.20.7"),sQuery(id+"F0.wireOp",EDGE,"afc6e781-25c3-4dd1-969d-5b2406180a6c.0.20.8"),sQuery(id+"F0.wireOp",EDGE,"afc6e781-25c3-4dd1-969d-5b2406180a6c.3.20.8"),sQuery(id+"F0.wireOp",EDGE,"afc6e781-25c3-4dd1-969d-5b2406180a6c.6.20.8"),sQuery(id+"F0.wireOp",EDGE,"afc6e781-25c3-4dd1-969d-5b2406180a6c.9.20.8"),sQuery(id+"F0.wireOp",EDGE,"afc6e781-25c3-4dd1-969d-5b2406180a6c.0.20.9"),sQuery(id+"F0.wireOp",EDGE,"afc6e781-25c3-4dd1-969d-5b2406180a6c.3.20.9"),sQuery(id+"F0.wireOp",EDGE,"afc6e781-25c3-4dd1-969d-5b2406180a6c.6.20.9"),sQuery(id+"F0.wireOp",EDGE,"afc6e781-25c3-4dd1-969d-5b2406180a6c.9.20.9"),sQuery(id+"F0.wireOp",EDGE,"afc6e781-25c3-4dd1-969d-5b2406180a6c.0.20.10"),sQuery(id+"F0.wireOp",EDGE,"afc6e781-25c3-4dd1-969d-5b2406180a6c.3.20.10"),sQuery(id+"F0.wireOp",EDGE,"afc6e781-25c3-4dd1-969d-5b2406180a6c.6.20.10"),sQuery(id+"F0.wireOp",EDGE,"afc6e781-25c3-4dd1-969d-5b2406180a6c.9.20.10"),sQuery(id+"F0.wireOp",EDGE,"afc6e781-25c3-4dd1-969d-5b2406180a6c.0.20.11"),sQuery(id+"F0.wireOp",EDGE,"afc6e781-25c3-4dd1-969d-5b2406180a6c.3.20.11"),sQuery(id+"F0.wireOp",EDGE,"afc6e781-25c3-4dd1-969d-5b2406180a6c.6.20.11"),sQuery(id+"F0.wireOp",EDGE,"afc6e781-25c3-4dd1-969d-5b2406180a6c.9.20.11"),sQuery(id+"F0.wireOp",EDGE,"afc6e781-25c3-4dd1-969d-5b2406180a6c.0.20.12"),sQuery(id+"F0.wireOp",EDGE,"afc6e781-25c3-4dd1-969d-5b2406180a6c.3.20.12"),sQuery(id+"F0.wireOp",EDGE,"afc6e781-25c3-4dd1-969d-5b2406180a6c.6.20.12"),sQuery(id+"F0.wireOp",EDGE,"afc6e781-25c3-4dd1-969d-5b2406180a6c.9.20.12"),sQuery(id+"F0.wireOp",EDGE,"afc6e781-25c3-4dd1-969d-5b2406180a6c.0.20.13"),sQuery(id+"F0.wireOp",EDGE,"afc6e781-25c3-4dd1-969d-5b2406180a6c.3.20.13"),sQuery(id+"F0.wireOp",EDGE,"afc6e781-25c3-4dd1-969d-5b2406180a6c.6.20.13"),sQuery(id+"F0.wireOp",EDGE,"afc6e781-25c3-4dd1-969d-5b2406180a6c.9.20.13"),sQuery(id+"F0.wireOp",EDGE,"afc6e781-25c3-4dd1-969d-5b2406180a6c.0.20.14"),sQuery(id+"F0.wireOp",EDGE,"afc6e781-25c3-4dd1-969d-5b2406180a6c.3.20.14"),sQuery(id+"F0.wireOp",EDGE,"afc6e781-25c3-4dd1-969d-5b2406180a6c.6.20.14"),sQuery(id+"F0.wireOp",EDGE,"afc6e781-25c3-4dd1-969d-5b2406180a6c.9.20.14"),sQuery(id+"F0.wireOp",EDGE,"afc6e781-25c3-4dd1-969d-5b2406180a6c.0.20.15"),sQuery(id+"F0.wireOp",EDGE,"afc6e781-25c3-4dd1-969d-5b2406180a6c.3.20.15"),sQuery(id+"F0.wireOp",EDGE,"afc6e781-25c3-4dd1-969d-5b2406180a6c.6.20.15"),sQuery(id+"F0.wireOp",EDGE,"afc6e781-25c3-4dd1-969d-5b2406180a6c.9.20.15"),sQuery(id+"F0.wireOp",EDGE,"afc6e781-25c3-4dd1-969d-5b2406180a6c.0.20.16"),sQuery(id+"F0.wireOp",EDGE,"afc6e781-25c3-4dd1-969d-5b2406180a6c.3.20.16"),sQuery(id+"F0.wireOp",EDGE,"afc6e781-25c3-4dd1-969d-5b2406180a6c.6.20.16"),sQuery(id+"F0.wireOp",EDGE,"afc6e781-25c3-4dd1-969d-5b2406180a6c.9.20.16"),sQuery(id+"F0.wireOp",EDGE,"afc6e781-25c3-4dd1-969d-5b2406180a6c.0.20.17"),sQuery(id+"F0.wireOp",EDGE,"afc6e781-25c3-4dd1-969d-5b2406180a6c.3.20.17"),sQuery(id+"F0.wireOp",EDGE,"afc6e781-25c3-4dd1-969d-5b2406180a6c.6.20.17"),sQuery(id+"F0.wireOp",EDGE,"afc6e781-25c3-4dd1-969d-5b2406180a6c.9.20.17"),sQuery(id+"F0.wireOp",EDGE,"afc6e781-25c3-4dd1-969d-5b2406180a6c.0.20.18"),sQuery(id+"F0.wireOp",EDGE,"afc6e781-25c3-4dd1-969d-5b2406180a6c.3.20.18"),sQuery(id+"F0.wireOp",EDGE,"afc6e781-25c3-4dd1-969d-5b2406180a6c.6.20.18"),sQuery(id+"F0.wireOp",EDGE,"afc6e781-25c3-4dd1-969d-5b2406180a6c.9.20.18"),sQuery(id+"F0.wireOp",EDGE,"afc6e781-25c3-4dd1-969d-5b2406180a6c.0.20.19"),sQuery(id+"F0.wireOp",EDGE,"afc6e781-25c3-4dd1-969d-5b2406180a6c.3.20.19"),sQuery(id+"F0.wireOp",EDGE,"afc6e781-25c3-4dd1-969d-5b2406180a6c.6.20.19"),sQuery(id+"F0.wireOp",EDGE,"afc6e781-25c3-4dd1-969d-5b2406180a6c.9.20.19"),sQuery(id+"F0.wireOp",EDGE,"afc6e781-25c3-4dd1-969d-5b2406180a6c.0.20.20"),sQuery(id+"F0.wireOp",EDGE,"afc6e781-25c3-4dd1-969d-5b2406180a6c.3.20.20"),sQuery(id+"F0.wireOp",EDGE,"afc6e781-25c3-4dd1-969d-5b2406180a6c.6.20.20"),sQuery(id+"F0.wireOp",EDGE,"afc6e781-25c3-4dd1-969d-5b2406180a6c.9.20.20"),sQuery(id+"F0.wireOp",EDGE,"afc6e781-25c3-4dd1-969d-5b2406180a6c.0.20.21"),sQuery(id+"F0.wireOp",EDGE,"afc6e781-25c3-4dd1-969d-5b2406180a6c.3.20.21"),sQuery(id+"F0.wireOp",EDGE,"afc6e781-25c3-4dd1-969d-5b2406180a6c.6.20.21"),sQuery(id+"F0.wireOp",EDGE,"afc6e781-25c3-4dd1-969d-5b2406180a6c.9.20.21"),sQuery(id+"F0.wireOp",EDGE,"afc6e781-25c3-4dd1-969d-5b2406180a6c.0.20.22"),sQuery(id+"F0.wireOp",EDGE,"afc6e781-25c3-4dd1-969d-5b2406180a6c.3.20.22"),sQuery(id+"F0.wireOp",EDGE,"afc6e781-25c3-4dd1-969d-5b2406180a6c.6.20.22"),sQuery(id+"F0.wireOp",EDGE,"afc6e781-25c3-4dd1-969d-5b2406180a6c.9.20.22"),sQuery(id+"F0.wireOp",EDGE,"afc6e781-25c3-4dd1-969d-5b2406180a6c.0.20.23"),sQuery(id+"F0.wireOp",EDGE,"afc6e781-25c3-4dd1-969d-5b2406180a6c.3.20.23"),sQuery(id+"F0.wireOp",EDGE,"afc6e781-25c3-4dd1-969d-5b2406180a6c.6.20.23"),sQuery(id+"F0.wireOp",EDGE,"afc6e781-25c3-4dd1-969d-5b2406180a6c.9.20.23"),sQuery(id+"F0.wireOp",EDGE,"afc6e781-25c3-4dd1-969d-5b2406180a6c.0.20.24"),sQuery(id+"F0.wireOp",EDGE,"afc6e781-25c3-4dd1-969d-5b2406180a6c.3.20.24"),sQuery(id+"F0.wireOp",EDGE,"afc6e781-25c3-4dd1-969d-5b2406180a6c.6.20.24"),sQuery(id+"F0.wireOp",EDGE,"afc6e781-25c3-4dd1-969d-5b2406180a6c.9.20.24"),sQuery(id+"F0.wireOp",EDGE,"afc6e781-25c3-4dd1-969d-5b2406180a6c.0.20.25"),sQuery(id+"F0.wireOp",EDGE,"afc6e781-25c3-4dd1-969d-5b2406180a6c.3.20.25"),sQuery(id+"F0.wireOp",EDGE,"afc6e781-25c3-4dd1-969d-5b2406180a6c.6.20.25"),sQuery(id+"F0.wireOp",EDGE,"afc6e781-25c3-4dd1-969d-5b2406180a6c.9.20.25"),sQuery(id+"F0.wireOp",EDGE,"afc6e781-25c3-4dd1-969d-5b2406180a6c.0.20.26"),sQuery(id+"F0.wireOp",EDGE,"afc6e781-25c3-4dd1-969d-5b2406180a6c.3.20.26"),sQuery(id+"F0.wireOp",EDGE,"afc6e781-25c3-4dd1-969d-5b2406180a6c.6.20.26"),sQuery(id+"F0.wireOp",EDGE,"afc6e781-25c3-4dd1-969d-5b2406180a6c.9.20.26"),sQuery(id+"F0.wireOp",EDGE,"afc6e781-25c3-4dd1-969d-5b2406180a6c.0.20.27"),sQuery(id+"F0.wireOp",EDGE,"afc6e781-25c3-4dd1-969d-5b2406180a6c.3.20.27"),sQuery(id+"F0.wireOp",EDGE,"afc6e781-25c3-4dd1-969d-5b2406180a6c.6.20.27"),sQuery(id+"F0.wireOp",EDGE,"afc6e781-25c3-4dd1-969d-5b2406180a6c.9.20.27"),sQuery(id+"F0.wireOp",EDGE,"afc6e781-25c3-4dd1-969d-5b2406180a6c.0.20.28"),sQuery(id+"F0.wireOp",EDGE,"afc6e781-25c3-4dd1-969d-5b2406180a6c.3.20.28"),sQuery(id+"F0.wireOp",EDGE,"afc6e781-25c3-4dd1-969d-5b2406180a6c.6.20.28"),sQuery(id+"F0.wireOp",EDGE,"afc6e781-25c3-4dd1-969d-5b2406180a6c.9.20.28"),sQuery(id+"F0.wireOp",EDGE,"afc6e781-25c3-4dd1-969d-5b2406180a6c.0.20.29"),sQuery(id+"F0.wireOp",EDGE,"afc6e781-25c3-4dd1-969d-5b2406180a6c.3.20.29"),sQuery(id+"F0.wireOp",EDGE,"afc6e781-25c3-4dd1-969d-5b2406180a6c.6.20.29"),sQuery(id+"F0.wireOp",EDGE,"afc6e781-25c3-4dd1-969d-5b2406180a6c.9.20.29"),sQuery(id+"F0.wireOp",EDGE,"afc6e781-25c3-4dd1-969d-5b2406180a6c.0.20.30"),sQuery(id+"F0.wireOp",EDGE,"afc6e781-25c3-4dd1-969d-5b2406180a6c.3.20.30"),sQuery(id+"F0.wireOp",EDGE,"afc6e781-25c3-4dd1-969d-5b2406180a6c.6.20.30"),sQuery(id+"F0.wireOp",EDGE,"afc6e781-25c3-4dd1-969d-5b2406180a6c.9.20.30"),sQuery(id+"F0.wireOp",EDGE,"afc6e781-25c3-4dd1-969d-5b2406180a6c.0.20.31"),sQuery(id+"F0.wireOp",EDGE,"afc6e781-25c3-4dd1-969d-5b2406180a6c.3.20.31"),sQuery(id+"F0.wireOp",EDGE,"afc6e781-25c3-4dd1-969d-5b2406180a6c.6.20.31"),sQuery(id+"F0.wireOp",EDGE,"afc6e781-25c3-4dd1-969d-5b2406180a6c.9.20.31"),sQuery(id+"F0.wireOp",EDGE,"afc6e781-25c3-4dd1-969d-5b2406180a6c.0.21.0"),sQuery(id+"F0.wireOp",EDGE,"afc6e781-25c3-4dd1-969d-5b2406180a6c.3.21.0"),sQuery(id+"F0.wireOp",EDGE,"afc6e781-25c3-4dd1-969d-5b2406180a6c.6.21.0"),sQuery(id+"F0.wireOp",EDGE,"afc6e781-25c3-4dd1-969d-5b2406180a6c.9.21.0"),sQuery(id+"F0.wireOp",EDGE,"afc6e781-25c3-4dd1-969d-5b2406180a6c.0.21.1"),sQuery(id+"F0.wireOp",EDGE,"afc6e781-25c3-4dd1-969d-5b2406180a6c.3.21.1"),sQuery(id+"F0.wireOp",EDGE,"afc6e781-25c3-4dd1-969d-5b2406180a6c.6.21.1"),sQuery(id+"F0.wireOp",EDGE,"afc6e781-25c3-4dd1-969d-5b2406180a6c.9.21.1"),sQuery(id+"F0.wireOp",EDGE,"afc6e781-25c3-4dd1-969d-5b2406180a6c.0.21.2"),sQuery(id+"F0.wireOp",EDGE,"afc6e781-25c3-4dd1-969d-5b2406180a6c.3.21.2"),sQuery(id+"F0.wireOp",EDGE,"afc6e781-25c3-4dd1-969d-5b2406180a6c.6.21.2"),sQuery(id+"F0.wireOp",EDGE,"afc6e781-25c3-4dd1-969d-5b2406180a6c.9.21.2"),sQuery(id+"F0.wireOp",EDGE,"afc6e781-25c3-4dd1-969d-5b2406180a6c.0.21.3"),sQuery(id+"F0.wireOp",EDGE,"afc6e781-25c3-4dd1-969d-5b2406180a6c.3.21.3"),sQuery(id+"F0.wireOp",EDGE,"afc6e781-25c3-4dd1-969d-5b2406180a6c.6.21.3"),sQuery(id+"F0.wireOp",EDGE,"afc6e781-25c3-4dd1-969d-5b2406180a6c.9.21.3"),sQuery(id+"F0.wireOp",EDGE,"afc6e781-25c3-4dd1-969d-5b2406180a6c.0.21.4"),sQuery(id+"F0.wireOp",EDGE,"afc6e781-25c3-4dd1-969d-5b2406180a6c.3.21.4"),sQuery(id+"F0.wireOp",EDGE,"afc6e781-25c3-4dd1-969d-5b2406180a6c.6.21.4"),sQuery(id+"F0.wireOp",EDGE,"afc6e781-25c3-4dd1-969d-5b2406180a6c.9.21.4"),sQuery(id+"F0.wireOp",EDGE,"afc6e781-25c3-4dd1-969d-5b2406180a6c.0.21.5"),sQuery(id+"F0.wireOp",EDGE,"afc6e781-25c3-4dd1-969d-5b2406180a6c.3.21.5"),sQuery(id+"F0.wireOp",EDGE,"afc6e781-25c3-4dd1-969d-5b2406180a6c.6.21.5"),sQuery(id+"F0.wireOp",EDGE,"afc6e781-25c3-4dd1-969d-5b2406180a6c.9.21.5"),sQuery(id+"F0.wireOp",EDGE,"afc6e781-25c3-4dd1-969d-5b2406180a6c.0.21.6"),sQuery(id+"F0.wireOp",EDGE,"afc6e781-25c3-4dd1-969d-5b2406180a6c.3.21.6"),sQuery(id+"F0.wireOp",EDGE,"afc6e781-25c3-4dd1-969d-5b2406180a6c.6.21.6"),sQuery(id+"F0.wireOp",EDGE,"afc6e781-25c3-4dd1-969d-5b2406180a6c.9.21.6"),sQuery(id+"F0.wireOp",EDGE,"afc6e781-25c3-4dd1-969d-5b2406180a6c.0.21.7"),sQuery(id+"F0.wireOp",EDGE,"afc6e781-25c3-4dd1-969d-5b2406180a6c.3.21.7"),sQuery(id+"F0.wireOp",EDGE,"afc6e781-25c3-4dd1-969d-5b2406180a6c.6.21.7"),sQuery(id+"F0.wireOp",EDGE,"afc6e781-25c3-4dd1-969d-5b2406180a6c.9.21.7"),sQuery(id+"F0.wireOp",EDGE,"afc6e781-25c3-4dd1-969d-5b2406180a6c.0.21.8"),sQuery(id+"F0.wireOp",EDGE,"afc6e781-25c3-4dd1-969d-5b2406180a6c.3.21.8"),sQuery(id+"F0.wireOp",EDGE,"afc6e781-25c3-4dd1-969d-5b2406180a6c.6.21.8"),sQuery(id+"F0.wireOp",EDGE,"afc6e781-25c3-4dd1-969d-5b2406180a6c.9.21.8"),sQuery(id+"F0.wireOp",EDGE,"afc6e781-25c3-4dd1-969d-5b2406180a6c.0.21.9"),sQuery(id+"F0.wireOp",EDGE,"afc6e781-25c3-4dd1-969d-5b2406180a6c.3.21.9"),sQuery(id+"F0.wireOp",EDGE,"afc6e781-25c3-4dd1-969d-5b2406180a6c.6.21.9"),sQuery(id+"F0.wireOp",EDGE,"afc6e781-25c3-4dd1-969d-5b2406180a6c.9.21.9"),sQuery(id+"F0.wireOp",EDGE,"afc6e781-25c3-4dd1-969d-5b2406180a6c.0.21.10"),sQuery(id+"F0.wireOp",EDGE,"afc6e781-25c3-4dd1-969d-5b2406180a6c.3.21.10"),sQuery(id+"F0.wireOp",EDGE,"afc6e781-25c3-4dd1-969d-5b2406180a6c.6.21.10"),sQuery(id+"F0.wireOp",EDGE,"afc6e781-25c3-4dd1-969d-5b2406180a6c.9.21.10"),sQuery(id+"F0.wireOp",EDGE,"afc6e781-25c3-4dd1-969d-5b2406180a6c.0.21.11"),sQuery(id+"F0.wireOp",EDGE,"afc6e781-25c3-4dd1-969d-5b2406180a6c.3.21.11"),sQuery(id+"F0.wireOp",EDGE,"afc6e781-25c3-4dd1-969d-5b2406180a6c.6.21.11"),sQuery(id+"F0.wireOp",EDGE,"afc6e781-25c3-4dd1-969d-5b2406180a6c.9.21.11"),sQuery(id+"F0.wireOp",EDGE,"afc6e781-25c3-4dd1-969d-5b2406180a6c.0.21.12"),sQuery(id+"F0.wireOp",EDGE,"afc6e781-25c3-4dd1-969d-5b2406180a6c.3.21.12"),sQuery(id+"F0.wireOp",EDGE,"afc6e781-25c3-4dd1-969d-5b2406180a6c.6.21.12"),sQuery(id+"F0.wireOp",EDGE,"afc6e781-25c3-4dd1-969d-5b2406180a6c.9.21.12"),sQuery(id+"F0.wireOp",EDGE,"afc6e781-25c3-4dd1-969d-5b2406180a6c.0.21.13"),sQuery(id+"F0.wireOp",EDGE,"afc6e781-25c3-4dd1-969d-5b2406180a6c.3.21.13"),sQuery(id+"F0.wireOp",EDGE,"afc6e781-25c3-4dd1-969d-5b2406180a6c.6.21.13"),sQuery(id+"F0.wireOp",EDGE,"afc6e781-25c3-4dd1-969d-5b2406180a6c.9.21.13"),sQuery(id+"F0.wireOp",EDGE,"afc6e781-25c3-4dd1-969d-5b2406180a6c.0.21.14"),sQuery(id+"F0.wireOp",EDGE,"afc6e781-25c3-4dd1-969d-5b2406180a6c.3.21.14"),sQuery(id+"F0.wireOp",EDGE,"afc6e781-25c3-4dd1-969d-5b2406180a6c.6.21.14"),sQuery(id+"F0.wireOp",EDGE,"afc6e781-25c3-4dd1-969d-5b2406180a6c.9.21.14"),sQuery(id+"F0.wireOp",EDGE,"afc6e781-25c3-4dd1-969d-5b2406180a6c.0.21.15"),sQuery(id+"F0.wireOp",EDGE,"afc6e781-25c3-4dd1-969d-5b2406180a6c.3.21.15"),sQuery(id+"F0.wireOp",EDGE,"afc6e781-25c3-4dd1-969d-5b2406180a6c.6.21.15"),sQuery(id+"F0.wireOp",EDGE,"afc6e781-25c3-4dd1-969d-5b2406180a6c.9.21.15"),sQuery(id+"F0.wireOp",EDGE,"afc6e781-25c3-4dd1-969d-5b2406180a6c.0.21.16"),sQuery(id+"F0.wireOp",EDGE,"afc6e781-25c3-4dd1-969d-5b2406180a6c.3.21.16"),sQuery(id+"F0.wireOp",EDGE,"afc6e781-25c3-4dd1-969d-5b2406180a6c.6.21.16"),sQuery(id+"F0.wireOp",EDGE,"afc6e781-25c3-4dd1-969d-5b2406180a6c.9.21.16"),sQuery(id+"F0.wireOp",EDGE,"afc6e781-25c3-4dd1-969d-5b2406180a6c.0.21.17"),sQuery(id+"F0.wireOp",EDGE,"afc6e781-25c3-4dd1-969d-5b2406180a6c.3.21.17"),sQuery(id+"F0.wireOp",EDGE,"afc6e781-25c3-4dd1-969d-5b2406180a6c.6.21.17"),sQuery(id+"F0.wireOp",EDGE,"afc6e781-25c3-4dd1-969d-5b2406180a6c.9.21.17"),sQuery(id+"F0.wireOp",EDGE,"afc6e781-25c3-4dd1-969d-5b2406180a6c.0.21.18"),sQuery(id+"F0.wireOp",EDGE,"afc6e781-25c3-4dd1-969d-5b2406180a6c.3.21.18"),sQuery(id+"F0.wireOp",EDGE,"afc6e781-25c3-4dd1-969d-5b2406180a6c.6.21.18"),sQuery(id+"F0.wireOp",EDGE,"afc6e781-25c3-4dd1-969d-5b2406180a6c.9.21.18"),sQuery(id+"F0.wireOp",EDGE,"afc6e781-25c3-4dd1-969d-5b2406180a6c.0.21.19"),sQuery(id+"F0.wireOp",EDGE,"afc6e781-25c3-4dd1-969d-5b2406180a6c.3.21.19"),sQuery(id+"F0.wireOp",EDGE,"afc6e781-25c3-4dd1-969d-5b2406180a6c.6.21.19"),sQuery(id+"F0.wireOp",EDGE,"afc6e781-25c3-4dd1-969d-5b2406180a6c.9.21.19"),sQuery(id+"F0.wireOp",EDGE,"afc6e781-25c3-4dd1-969d-5b2406180a6c.0.21.20"),sQuery(id+"F0.wireOp",EDGE,"afc6e781-25c3-4dd1-969d-5b2406180a6c.3.21.20"),sQuery(id+"F0.wireOp",EDGE,"afc6e781-25c3-4dd1-969d-5b2406180a6c.6.21.20"),sQuery(id+"F0.wireOp",EDGE,"afc6e781-25c3-4dd1-969d-5b2406180a6c.9.21.20"),sQuery(id+"F0.wireOp",EDGE,"afc6e781-25c3-4dd1-969d-5b2406180a6c.0.21.21"),sQuery(id+"F0.wireOp",EDGE,"afc6e781-25c3-4dd1-969d-5b2406180a6c.3.21.21"),sQuery(id+"F0.wireOp",EDGE,"afc6e781-25c3-4dd1-969d-5b2406180a6c.6.21.21"),sQuery(id+"F0.wireOp",EDGE,"afc6e781-25c3-4dd1-969d-5b2406180a6c.9.21.21"),sQuery(id+"F0.wireOp",EDGE,"afc6e781-25c3-4dd1-969d-5b2406180a6c.0.21.22"),sQuery(id+"F0.wireOp",EDGE,"afc6e781-25c3-4dd1-969d-5b2406180a6c.3.21.22"),sQuery(id+"F0.wireOp",EDGE,"afc6e781-25c3-4dd1-969d-5b2406180a6c.6.21.22"),sQuery(id+"F0.wireOp",EDGE,"afc6e781-25c3-4dd1-969d-5b2406180a6c.9.21.22"),sQuery(id+"F0.wireOp",EDGE,"afc6e781-25c3-4dd1-969d-5b2406180a6c.0.21.23"),sQuery(id+"F0.wireOp",EDGE,"afc6e781-25c3-4dd1-969d-5b2406180a6c.3.21.23"),sQuery(id+"F0.wireOp",EDGE,"afc6e781-25c3-4dd1-969d-5b2406180a6c.6.21.23"),sQuery(id+"F0.wireOp",EDGE,"afc6e781-25c3-4dd1-969d-5b2406180a6c.9.21.23"),sQuery(id+"F0.wireOp",EDGE,"afc6e781-25c3-4dd1-969d-5b2406180a6c.0.21.24"),sQuery(id+"F0.wireOp",EDGE,"afc6e781-25c3-4dd1-969d-5b2406180a6c.3.21.24"),sQuery(id+"F0.wireOp",EDGE,"afc6e781-25c3-4dd1-969d-5b2406180a6c.6.21.24"),sQuery(id+"F0.wireOp",EDGE,"afc6e781-25c3-4dd1-969d-5b2406180a6c.9.21.24"),sQuery(id+"F0.wireOp",EDGE,"afc6e781-25c3-4dd1-969d-5b2406180a6c.0.21.25"),sQuery(id+"F0.wireOp",EDGE,"afc6e781-25c3-4dd1-969d-5b2406180a6c.3.21.25"),sQuery(id+"F0.wireOp",EDGE,"afc6e781-25c3-4dd1-969d-5b2406180a6c.6.21.25"),sQuery(id+"F0.wireOp",EDGE,"afc6e781-25c3-4dd1-969d-5b2406180a6c.9.21.25"),sQuery(id+"F0.wireOp",EDGE,"afc6e781-25c3-4dd1-969d-5b2406180a6c.0.21.26"),sQuery(id+"F0.wireOp",EDGE,"afc6e781-25c3-4dd1-969d-5b2406180a6c.3.21.26"),sQuery(id+"F0.wireOp",EDGE,"afc6e781-25c3-4dd1-969d-5b2406180a6c.6.21.26"),sQuery(id+"F0.wireOp",EDGE,"afc6e781-25c3-4dd1-969d-5b2406180a6c.9.21.26"),sQuery(id+"F0.wireOp",EDGE,"afc6e781-25c3-4dd1-969d-5b2406180a6c.0.21.27"),sQuery(id+"F0.wireOp",EDGE,"afc6e781-25c3-4dd1-969d-5b2406180a6c.3.21.27"),sQuery(id+"F0.wireOp",EDGE,"afc6e781-25c3-4dd1-969d-5b2406180a6c.6.21.27"),sQuery(id+"F0.wireOp",EDGE,"afc6e781-25c3-4dd1-969d-5b2406180a6c.9.21.27"),sQuery(id+"F0.wireOp",EDGE,"afc6e781-25c3-4dd1-969d-5b2406180a6c.0.21.28"),sQuery(id+"F0.wireOp",EDGE,"afc6e781-25c3-4dd1-969d-5b2406180a6c.3.21.28"),sQuery(id+"F0.wireOp",EDGE,"afc6e781-25c3-4dd1-969d-5b2406180a6c.6.21.28"),sQuery(id+"F0.wireOp",EDGE,"afc6e781-25c3-4dd1-969d-5b2406180a6c.9.21.28"),sQuery(id+"F0.wireOp",EDGE,"afc6e781-25c3-4dd1-969d-5b2406180a6c.0.21.29"),sQuery(id+"F0.wireOp",EDGE,"afc6e781-25c3-4dd1-969d-5b2406180a6c.3.21.29"),sQuery(id+"F0.wireOp",EDGE,"afc6e781-25c3-4dd1-969d-5b2406180a6c.6.21.29"),sQuery(id+"F0.wireOp",EDGE,"afc6e781-25c3-4dd1-969d-5b2406180a6c.9.21.29"),sQuery(id+"F0.wireOp",EDGE,"afc6e781-25c3-4dd1-969d-5b2406180a6c.0.21.30"),sQuery(id+"F0.wireOp",EDGE,"afc6e781-25c3-4dd1-969d-5b2406180a6c.3.21.30"),sQuery(id+"F0.wireOp",EDGE,"afc6e781-25c3-4dd1-969d-5b2406180a6c.6.21.30"),sQuery(id+"F0.wireOp",EDGE,"afc6e781-25c3-4dd1-969d-5b2406180a6c.9.21.30"),sQuery(id+"F0.wireOp",EDGE,"afc6e781-25c3-4dd1-969d-5b2406180a6c.0.21.31"),sQuery(id+"F0.wireOp",EDGE,"afc6e781-25c3-4dd1-969d-5b2406180a6c.3.21.31"),sQuery(id+"F0.wireOp",EDGE,"afc6e781-25c3-4dd1-969d-5b2406180a6c.6.21.31"),sQuery(id+"F0.wireOp",EDGE,"afc6e781-25c3-4dd1-969d-5b2406180a6c.9.21.31"),sQuery(id+"F0.wireOp",EDGE,"afc6e781-25c3-4dd1-969d-5b2406180a6c.0.22.0"),sQuery(id+"F0.wireOp",EDGE,"afc6e781-25c3-4dd1-969d-5b2406180a6c.3.22.0"),sQuery(id+"F0.wireOp",EDGE,"afc6e781-25c3-4dd1-969d-5b2406180a6c.6.22.0"),sQuery(id+"F0.wireOp",EDGE,"afc6e781-25c3-4dd1-969d-5b2406180a6c.9.22.0"),sQuery(id+"F0.wireOp",EDGE,"afc6e781-25c3-4dd1-969d-5b2406180a6c.0.22.1"),sQuery(id+"F0.wireOp",EDGE,"afc6e781-25c3-4dd1-969d-5b2406180a6c.3.22.1"),sQuery(id+"F0.wireOp",EDGE,"afc6e781-25c3-4dd1-969d-5b2406180a6c.6.22.1"),sQuery(id+"F0.wireOp",EDGE,"afc6e781-25c3-4dd1-969d-5b2406180a6c.9.22.1"),sQuery(id+"F0.wireOp",EDGE,"afc6e781-25c3-4dd1-969d-5b2406180a6c.0.22.2"),sQuery(id+"F0.wireOp",EDGE,"afc6e781-25c3-4dd1-969d-5b2406180a6c.3.22.2"),sQuery(id+"F0.wireOp",EDGE,"afc6e781-25c3-4dd1-969d-5b2406180a6c.6.22.2"),sQuery(id+"F0.wireOp",EDGE,"afc6e781-25c3-4dd1-969d-5b2406180a6c.9.22.2"),sQuery(id+"F0.wireOp",EDGE,"afc6e781-25c3-4dd1-969d-5b2406180a6c.0.22.3"),sQuery(id+"F0.wireOp",EDGE,"afc6e781-25c3-4dd1-969d-5b2406180a6c.3.22.3"),sQuery(id+"F0.wireOp",EDGE,"afc6e781-25c3-4dd1-969d-5b2406180a6c.6.22.3"),sQuery(id+"F0.wireOp",EDGE,"afc6e781-25c3-4dd1-969d-5b2406180a6c.9.22.3"),sQuery(id+"F0.wireOp",EDGE,"afc6e781-25c3-4dd1-969d-5b2406180a6c.0.22.4"),sQuery(id+"F0.wireOp",EDGE,"afc6e781-25c3-4dd1-969d-5b2406180a6c.3.22.4"),sQuery(id+"F0.wireOp",EDGE,"afc6e781-25c3-4dd1-969d-5b2406180a6c.6.22.4"),sQuery(id+"F0.wireOp",EDGE,"afc6e781-25c3-4dd1-969d-5b2406180a6c.9.22.4"),sQuery(id+"F0.wireOp",EDGE,"afc6e781-25c3-4dd1-969d-5b2406180a6c.0.22.5"),sQuery(id+"F0.wireOp",EDGE,"afc6e781-25c3-4dd1-969d-5b2406180a6c.3.22.5"),sQuery(id+"F0.wireOp",EDGE,"afc6e781-25c3-4dd1-969d-5b2406180a6c.6.22.5"),sQuery(id+"F0.wireOp",EDGE,"afc6e781-25c3-4dd1-969d-5b2406180a6c.9.22.5"),sQuery(id+"F0.wireOp",EDGE,"afc6e781-25c3-4dd1-969d-5b2406180a6c.0.22.6"),sQuery(id+"F0.wireOp",EDGE,"afc6e781-25c3-4dd1-969d-5b2406180a6c.3.22.6"),sQuery(id+"F0.wireOp",EDGE,"afc6e781-25c3-4dd1-969d-5b2406180a6c.6.22.6"),sQuery(id+"F0.wireOp",EDGE,"afc6e781-25c3-4dd1-969d-5b2406180a6c.9.22.6"),sQuery(id+"F0.wireOp",EDGE,"afc6e781-25c3-4dd1-969d-5b2406180a6c.0.22.7"),sQuery(id+"F0.wireOp",EDGE,"afc6e781-25c3-4dd1-969d-5b2406180a6c.3.22.7"),sQuery(id+"F0.wireOp",EDGE,"afc6e781-25c3-4dd1-969d-5b2406180a6c.6.22.7"),sQuery(id+"F0.wireOp",EDGE,"afc6e781-25c3-4dd1-969d-5b2406180a6c.9.22.7"),sQuery(id+"F0.wireOp",EDGE,"afc6e781-25c3-4dd1-969d-5b2406180a6c.0.22.8"),sQuery(id+"F0.wireOp",EDGE,"afc6e781-25c3-4dd1-969d-5b2406180a6c.3.22.8"),sQuery(id+"F0.wireOp",EDGE,"afc6e781-25c3-4dd1-969d-5b2406180a6c.6.22.8"),sQuery(id+"F0.wireOp",EDGE,"afc6e781-25c3-4dd1-969d-5b2406180a6c.9.22.8"),sQuery(id+"F0.wireOp",EDGE,"afc6e781-25c3-4dd1-969d-5b2406180a6c.0.22.9"),sQuery(id+"F0.wireOp",EDGE,"afc6e781-25c3-4dd1-969d-5b2406180a6c.3.22.9"),sQuery(id+"F0.wireOp",EDGE,"afc6e781-25c3-4dd1-969d-5b2406180a6c.6.22.9"),sQuery(id+"F0.wireOp",EDGE,"afc6e781-25c3-4dd1-969d-5b2406180a6c.9.22.9"),sQuery(id+"F0.wireOp",EDGE,"afc6e781-25c3-4dd1-969d-5b2406180a6c.0.22.10"),sQuery(id+"F0.wireOp",EDGE,"afc6e781-25c3-4dd1-969d-5b2406180a6c.3.22.10"),sQuery(id+"F0.wireOp",EDGE,"afc6e781-25c3-4dd1-969d-5b2406180a6c.6.22.10"),sQuery(id+"F0.wireOp",EDGE,"afc6e781-25c3-4dd1-969d-5b2406180a6c.9.22.10"),sQuery(id+"F0.wireOp",EDGE,"afc6e781-25c3-4dd1-969d-5b2406180a6c.0.22.11"),sQuery(id+"F0.wireOp",EDGE,"afc6e781-25c3-4dd1-969d-5b2406180a6c.3.22.11"),sQuery(id+"F0.wireOp",EDGE,"afc6e781-25c3-4dd1-969d-5b2406180a6c.6.22.11"),sQuery(id+"F0.wireOp",EDGE,"afc6e781-25c3-4dd1-969d-5b2406180a6c.9.22.11"),sQuery(id+"F0.wireOp",EDGE,"afc6e781-25c3-4dd1-969d-5b2406180a6c.0.22.12"),sQuery(id+"F0.wireOp",EDGE,"afc6e781-25c3-4dd1-969d-5b2406180a6c.3.22.12"),sQuery(id+"F0.wireOp",EDGE,"afc6e781-25c3-4dd1-969d-5b2406180a6c.6.22.12"),sQuery(id+"F0.wireOp",EDGE,"afc6e781-25c3-4dd1-969d-5b2406180a6c.9.22.12"),sQuery(id+"F0.wireOp",EDGE,"afc6e781-25c3-4dd1-969d-5b2406180a6c.0.22.13"),sQuery(id+"F0.wireOp",EDGE,"afc6e781-25c3-4dd1-969d-5b2406180a6c.3.22.13"),sQuery(id+"F0.wireOp",EDGE,"afc6e781-25c3-4dd1-969d-5b2406180a6c.6.22.13"),sQuery(id+"F0.wireOp",EDGE,"afc6e781-25c3-4dd1-969d-5b2406180a6c.9.22.13"),sQuery(id+"F0.wireOp",EDGE,"afc6e781-25c3-4dd1-969d-5b2406180a6c.0.22.14"),sQuery(id+"F0.wireOp",EDGE,"afc6e781-25c3-4dd1-969d-5b2406180a6c.3.22.14"),sQuery(id+"F0.wireOp",EDGE,"afc6e781-25c3-4dd1-969d-5b2406180a6c.6.22.14"),sQuery(id+"F0.wireOp",EDGE,"afc6e781-25c3-4dd1-969d-5b2406180a6c.9.22.14"),sQuery(id+"F0.wireOp",EDGE,"afc6e781-25c3-4dd1-969d-5b2406180a6c.0.22.15"),sQuery(id+"F0.wireOp",EDGE,"afc6e781-25c3-4dd1-969d-5b2406180a6c.3.22.15"),sQuery(id+"F0.wireOp",EDGE,"afc6e781-25c3-4dd1-969d-5b2406180a6c.6.22.15"),sQuery(id+"F0.wireOp",EDGE,"afc6e781-25c3-4dd1-969d-5b2406180a6c.9.22.15"),sQuery(id+"F0.wireOp",EDGE,"afc6e781-25c3-4dd1-969d-5b2406180a6c.0.22.16"),sQuery(id+"F0.wireOp",EDGE,"afc6e781-25c3-4dd1-969d-5b2406180a6c.3.22.16"),sQuery(id+"F0.wireOp",EDGE,"afc6e781-25c3-4dd1-969d-5b2406180a6c.6.22.16"),sQuery(id+"F0.wireOp",EDGE,"afc6e781-25c3-4dd1-969d-5b2406180a6c.9.22.16"),sQuery(id+"F0.wireOp",EDGE,"afc6e781-25c3-4dd1-969d-5b2406180a6c.0.22.17"),sQuery(id+"F0.wireOp",EDGE,"afc6e781-25c3-4dd1-969d-5b2406180a6c.3.22.17"),sQuery(id+"F0.wireOp",EDGE,"afc6e781-25c3-4dd1-969d-5b2406180a6c.6.22.17"),sQuery(id+"F0.wireOp",EDGE,"afc6e781-25c3-4dd1-969d-5b2406180a6c.9.22.17"),sQuery(id+"F0.wireOp",EDGE,"afc6e781-25c3-4dd1-969d-5b2406180a6c.0.22.18"),sQuery(id+"F0.wireOp",EDGE,"afc6e781-25c3-4dd1-969d-5b2406180a6c.3.22.18"),sQuery(id+"F0.wireOp",EDGE,"afc6e781-25c3-4dd1-969d-5b2406180a6c.6.22.18"),sQuery(id+"F0.wireOp",EDGE,"afc6e781-25c3-4dd1-969d-5b2406180a6c.9.22.18"),sQuery(id+"F0.wireOp",EDGE,"afc6e781-25c3-4dd1-969d-5b2406180a6c.0.22.19"),sQuery(id+"F0.wireOp",EDGE,"afc6e781-25c3-4dd1-969d-5b2406180a6c.3.22.19"),sQuery(id+"F0.wireOp",EDGE,"afc6e781-25c3-4dd1-969d-5b2406180a6c.6.22.19"),sQuery(id+"F0.wireOp",EDGE,"afc6e781-25c3-4dd1-969d-5b2406180a6c.9.22.19"),sQuery(id+"F0.wireOp",EDGE,"afc6e781-25c3-4dd1-969d-5b2406180a6c.0.22.20"),sQuery(id+"F0.wireOp",EDGE,"afc6e781-25c3-4dd1-969d-5b2406180a6c.3.22.20"),sQuery(id+"F0.wireOp",EDGE,"afc6e781-25c3-4dd1-969d-5b2406180a6c.6.22.20"),sQuery(id+"F0.wireOp",EDGE,"afc6e781-25c3-4dd1-969d-5b2406180a6c.9.22.20"),sQuery(id+"F0.wireOp",EDGE,"afc6e781-25c3-4dd1-969d-5b2406180a6c.0.22.21"),sQuery(id+"F0.wireOp",EDGE,"afc6e781-25c3-4dd1-969d-5b2406180a6c.3.22.21"),sQuery(id+"F0.wireOp",EDGE,"afc6e781-25c3-4dd1-969d-5b2406180a6c.6.22.21"),sQuery(id+"F0.wireOp",EDGE,"afc6e781-25c3-4dd1-969d-5b2406180a6c.9.22.21"),sQuery(id+"F0.wireOp",EDGE,"afc6e781-25c3-4dd1-969d-5b2406180a6c.0.22.22"),sQuery(id+"F0.wireOp",EDGE,"afc6e781-25c3-4dd1-969d-5b2406180a6c.3.22.22"),sQuery(id+"F0.wireOp",EDGE,"afc6e781-25c3-4dd1-969d-5b2406180a6c.6.22.22"),sQuery(id+"F0.wireOp",EDGE,"afc6e781-25c3-4dd1-969d-5b2406180a6c.9.22.22"),sQuery(id+"F0.wireOp",EDGE,"afc6e781-25c3-4dd1-969d-5b2406180a6c.0.22.23"),sQuery(id+"F0.wireOp",EDGE,"afc6e781-25c3-4dd1-969d-5b2406180a6c.3.22.23"),sQuery(id+"F0.wireOp",EDGE,"afc6e781-25c3-4dd1-969d-5b2406180a6c.6.22.23"),sQuery(id+"F0.wireOp",EDGE,"afc6e781-25c3-4dd1-969d-5b2406180a6c.9.22.23"),sQuery(id+"F0.wireOp",EDGE,"afc6e781-25c3-4dd1-969d-5b2406180a6c.0.22.24"),sQuery(id+"F0.wireOp",EDGE,"afc6e781-25c3-4dd1-969d-5b2406180a6c.3.22.24"),sQuery(id+"F0.wireOp",EDGE,"afc6e781-25c3-4dd1-969d-5b2406180a6c.6.22.24"),sQuery(id+"F0.wireOp",EDGE,"afc6e781-25c3-4dd1-969d-5b2406180a6c.9.22.24"),sQuery(id+"F0.wireOp",EDGE,"afc6e781-25c3-4dd1-969d-5b2406180a6c.0.22.25"),sQuery(id+"F0.wireOp",EDGE,"afc6e781-25c3-4dd1-969d-5b2406180a6c.3.22.25"),sQuery(id+"F0.wireOp",EDGE,"afc6e781-25c3-4dd1-969d-5b2406180a6c.6.22.25"),sQuery(id+"F0.wireOp",EDGE,"afc6e781-25c3-4dd1-969d-5b2406180a6c.9.22.25"),sQuery(id+"F0.wireOp",EDGE,"afc6e781-25c3-4dd1-969d-5b2406180a6c.0.22.26"),sQuery(id+"F0.wireOp",EDGE,"afc6e781-25c3-4dd1-969d-5b2406180a6c.3.22.26"),sQuery(id+"F0.wireOp",EDGE,"afc6e781-25c3-4dd1-969d-5b2406180a6c.6.22.26"),sQuery(id+"F0.wireOp",EDGE,"afc6e781-25c3-4dd1-969d-5b2406180a6c.9.22.26"),sQuery(id+"F0.wireOp",EDGE,"afc6e781-25c3-4dd1-969d-5b2406180a6c.0.22.27"),sQuery(id+"F0.wireOp",EDGE,"afc6e781-25c3-4dd1-969d-5b2406180a6c.3.22.27"),sQuery(id+"F0.wireOp",EDGE,"afc6e781-25c3-4dd1-969d-5b2406180a6c.6.22.27"),sQuery(id+"F0.wireOp",EDGE,"afc6e781-25c3-4dd1-969d-5b2406180a6c.9.22.27"),sQuery(id+"F0.wireOp",EDGE,"afc6e781-25c3-4dd1-969d-5b2406180a6c.0.22.28"),sQuery(id+"F0.wireOp",EDGE,"afc6e781-25c3-4dd1-969d-5b2406180a6c.3.22.28"),sQuery(id+"F0.wireOp",EDGE,"afc6e781-25c3-4dd1-969d-5b2406180a6c.6.22.28"),sQuery(id+"F0.wireOp",EDGE,"afc6e781-25c3-4dd1-969d-5b2406180a6c.9.22.28"),sQuery(id+"F0.wireOp",EDGE,"afc6e781-25c3-4dd1-969d-5b2406180a6c.0.22.29"),sQuery(id+"F0.wireOp",EDGE,"afc6e781-25c3-4dd1-969d-5b2406180a6c.3.22.29"),sQuery(id+"F0.wireOp",EDGE,"afc6e781-25c3-4dd1-969d-5b2406180a6c.6.22.29"),sQuery(id+"F0.wireOp",EDGE,"afc6e781-25c3-4dd1-969d-5b2406180a6c.9.22.29"),sQuery(id+"F0.wireOp",EDGE,"afc6e781-25c3-4dd1-969d-5b2406180a6c.0.22.30"),sQuery(id+"F0.wireOp",EDGE,"afc6e781-25c3-4dd1-969d-5b2406180a6c.3.22.30"),sQuery(id+"F0.wireOp",EDGE,"afc6e781-25c3-4dd1-969d-5b2406180a6c.6.22.30"),sQuery(id+"F0.wireOp",EDGE,"afc6e781-25c3-4dd1-969d-5b2406180a6c.9.22.30"),sQuery(id+"F0.wireOp",EDGE,"afc6e781-25c3-4dd1-969d-5b2406180a6c.0.22.31"),sQuery(id+"F0.wireOp",EDGE,"afc6e781-25c3-4dd1-969d-5b2406180a6c.3.22.31"),sQuery(id+"F0.wireOp",EDGE,"afc6e781-25c3-4dd1-969d-5b2406180a6c.6.22.31"),sQuery(id+"F0.wireOp",EDGE,"afc6e781-25c3-4dd1-969d-5b2406180a6c.9.22.31"),sQuery(id+"F0.wireOp",EDGE,"afc6e781-25c3-4dd1-969d-5b2406180a6c.0.23.0"),sQuery(id+"F0.wireOp",EDGE,"afc6e781-25c3-4dd1-969d-5b2406180a6c.3.23.0"),sQuery(id+"F0.wireOp",EDGE,"afc6e781-25c3-4dd1-969d-5b2406180a6c.6.23.0"),sQuery(id+"F0.wireOp",EDGE,"afc6e781-25c3-4dd1-969d-5b2406180a6c.9.23.0"),sQuery(id+"F0.wireOp",EDGE,"afc6e781-25c3-4dd1-969d-5b2406180a6c.0.23.1"),sQuery(id+"F0.wireOp",EDGE,"afc6e781-25c3-4dd1-969d-5b2406180a6c.3.23.1"),sQuery(id+"F0.wireOp",EDGE,"afc6e781-25c3-4dd1-969d-5b2406180a6c.6.23.1"),sQuery(id+"F0.wireOp",EDGE,"afc6e781-25c3-4dd1-969d-5b2406180a6c.9.23.1"),sQuery(id+"F0.wireOp",EDGE,"afc6e781-25c3-4dd1-969d-5b2406180a6c.0.23.2"),sQuery(id+"F0.wireOp",EDGE,"afc6e781-25c3-4dd1-969d-5b2406180a6c.3.23.2"),sQuery(id+"F0.wireOp",EDGE,"afc6e781-25c3-4dd1-969d-5b2406180a6c.6.23.2"),sQuery(id+"F0.wireOp",EDGE,"afc6e781-25c3-4dd1-969d-5b2406180a6c.9.23.2"),sQuery(id+"F0.wireOp",EDGE,"afc6e781-25c3-4dd1-969d-5b2406180a6c.0.23.3"),sQuery(id+"F0.wireOp",EDGE,"afc6e781-25c3-4dd1-969d-5b2406180a6c.3.23.3"),sQuery(id+"F0.wireOp",EDGE,"afc6e781-25c3-4dd1-969d-5b2406180a6c.6.23.3"),sQuery(id+"F0.wireOp",EDGE,"afc6e781-25c3-4dd1-969d-5b2406180a6c.9.23.3"),sQuery(id+"F0.wireOp",EDGE,"afc6e781-25c3-4dd1-969d-5b2406180a6c.0.23.4"),sQuery(id+"F0.wireOp",EDGE,"afc6e781-25c3-4dd1-969d-5b2406180a6c.3.23.4"),sQuery(id+"F0.wireOp",EDGE,"afc6e781-25c3-4dd1-969d-5b2406180a6c.6.23.4"),sQuery(id+"F0.wireOp",EDGE,"afc6e781-25c3-4dd1-969d-5b2406180a6c.9.23.4"),sQuery(id+"F0.wireOp",EDGE,"afc6e781-25c3-4dd1-969d-5b2406180a6c.0.23.5"),sQuery(id+"F0.wireOp",EDGE,"afc6e781-25c3-4dd1-969d-5b2406180a6c.3.23.5"),sQuery(id+"F0.wireOp",EDGE,"afc6e781-25c3-4dd1-969d-5b2406180a6c.6.23.5"),sQuery(id+"F0.wireOp",EDGE,"afc6e781-25c3-4dd1-969d-5b2406180a6c.9.23.5"),sQuery(id+"F0.wireOp",EDGE,"afc6e781-25c3-4dd1-969d-5b2406180a6c.0.23.6"),sQuery(id+"F0.wireOp",EDGE,"afc6e781-25c3-4dd1-969d-5b2406180a6c.3.23.6"),sQuery(id+"F0.wireOp",EDGE,"afc6e781-25c3-4dd1-969d-5b2406180a6c.6.23.6"),sQuery(id+"F0.wireOp",EDGE,"afc6e781-25c3-4dd1-969d-5b2406180a6c.9.23.6"),sQuery(id+"F0.wireOp",EDGE,"afc6e781-25c3-4dd1-969d-5b2406180a6c.0.23.7"),sQuery(id+"F0.wireOp",EDGE,"afc6e781-25c3-4dd1-969d-5b2406180a6c.3.23.7"),sQuery(id+"F0.wireOp",EDGE,"afc6e781-25c3-4dd1-969d-5b2406180a6c.6.23.7"),sQuery(id+"F0.wireOp",EDGE,"afc6e781-25c3-4dd1-969d-5b2406180a6c.9.23.7"),sQuery(id+"F0.wireOp",EDGE,"afc6e781-25c3-4dd1-969d-5b2406180a6c.0.23.8"),sQuery(id+"F0.wireOp",EDGE,"afc6e781-25c3-4dd1-969d-5b2406180a6c.3.23.8"),sQuery(id+"F0.wireOp",EDGE,"afc6e781-25c3-4dd1-969d-5b2406180a6c.6.23.8"),sQuery(id+"F0.wireOp",EDGE,"afc6e781-25c3-4dd1-969d-5b2406180a6c.9.23.8"),sQuery(id+"F0.wireOp",EDGE,"afc6e781-25c3-4dd1-969d-5b2406180a6c.0.23.9"),sQuery(id+"F0.wireOp",EDGE,"afc6e781-25c3-4dd1-969d-5b2406180a6c.3.23.9"),sQuery(id+"F0.wireOp",EDGE,"afc6e781-25c3-4dd1-969d-5b2406180a6c.6.23.9"),sQuery(id+"F0.wireOp",EDGE,"afc6e781-25c3-4dd1-969d-5b2406180a6c.9.23.9"),sQuery(id+"F0.wireOp",EDGE,"afc6e781-25c3-4dd1-969d-5b2406180a6c.0.23.10"),sQuery(id+"F0.wireOp",EDGE,"afc6e781-25c3-4dd1-969d-5b2406180a6c.3.23.10"),sQuery(id+"F0.wireOp",EDGE,"afc6e781-25c3-4dd1-969d-5b2406180a6c.6.23.10"),sQuery(id+"F0.wireOp",EDGE,"afc6e781-25c3-4dd1-969d-5b2406180a6c.9.23.10"),sQuery(id+"F0.wireOp",EDGE,"afc6e781-25c3-4dd1-969d-5b2406180a6c.0.23.11"),sQuery(id+"F0.wireOp",EDGE,"afc6e781-25c3-4dd1-969d-5b2406180a6c.3.23.11"),sQuery(id+"F0.wireOp",EDGE,"afc6e781-25c3-4dd1-969d-5b2406180a6c.6.23.11"),sQuery(id+"F0.wireOp",EDGE,"afc6e781-25c3-4dd1-969d-5b2406180a6c.9.23.11"),sQuery(id+"F0.wireOp",EDGE,"afc6e781-25c3-4dd1-969d-5b2406180a6c.0.23.12"),sQuery(id+"F0.wireOp",EDGE,"afc6e781-25c3-4dd1-969d-5b2406180a6c.3.23.12"),sQuery(id+"F0.wireOp",EDGE,"afc6e781-25c3-4dd1-969d-5b2406180a6c.6.23.12"),sQuery(id+"F0.wireOp",EDGE,"afc6e781-25c3-4dd1-969d-5b2406180a6c.9.23.12"),sQuery(id+"F0.wireOp",EDGE,"afc6e781-25c3-4dd1-969d-5b2406180a6c.0.23.13"),sQuery(id+"F0.wireOp",EDGE,"afc6e781-25c3-4dd1-969d-5b2406180a6c.3.23.13"),sQuery(id+"F0.wireOp",EDGE,"afc6e781-25c3-4dd1-969d-5b2406180a6c.6.23.13"),sQuery(id+"F0.wireOp",EDGE,"afc6e781-25c3-4dd1-969d-5b2406180a6c.9.23.13"),sQuery(id+"F0.wireOp",EDGE,"afc6e781-25c3-4dd1-969d-5b2406180a6c.0.23.14"),sQuery(id+"F0.wireOp",EDGE,"afc6e781-25c3-4dd1-969d-5b2406180a6c.3.23.14"),sQuery(id+"F0.wireOp",EDGE,"afc6e781-25c3-4dd1-969d-5b2406180a6c.6.23.14"),sQuery(id+"F0.wireOp",EDGE,"afc6e781-25c3-4dd1-969d-5b2406180a6c.9.23.14"),sQuery(id+"F0.wireOp",EDGE,"afc6e781-25c3-4dd1-969d-5b2406180a6c.0.23.15"),sQuery(id+"F0.wireOp",EDGE,"afc6e781-25c3-4dd1-969d-5b2406180a6c.3.23.15"),sQuery(id+"F0.wireOp",EDGE,"afc6e781-25c3-4dd1-969d-5b2406180a6c.6.23.15"),sQuery(id+"F0.wireOp",EDGE,"afc6e781-25c3-4dd1-969d-5b2406180a6c.9.23.15"),sQuery(id+"F0.wireOp",EDGE,"afc6e781-25c3-4dd1-969d-5b2406180a6c.0.23.16"),sQuery(id+"F0.wireOp",EDGE,"afc6e781-25c3-4dd1-969d-5b2406180a6c.3.23.16"),sQuery(id+"F0.wireOp",EDGE,"afc6e781-25c3-4dd1-969d-5b2406180a6c.6.23.16"),sQuery(id+"F0.wireOp",EDGE,"afc6e781-25c3-4dd1-969d-5b2406180a6c.9.23.16"),sQuery(id+"F0.wireOp",EDGE,"afc6e781-25c3-4dd1-969d-5b2406180a6c.0.23.17"),sQuery(id+"F0.wireOp",EDGE,"afc6e781-25c3-4dd1-969d-5b2406180a6c.3.23.17"),sQuery(id+"F0.wireOp",EDGE,"afc6e781-25c3-4dd1-969d-5b2406180a6c.6.23.17"),sQuery(id+"F0.wireOp",EDGE,"afc6e781-25c3-4dd1-969d-5b2406180a6c.9.23.17"),sQuery(id+"F0.wireOp",EDGE,"afc6e781-25c3-4dd1-969d-5b2406180a6c.0.23.18"),sQuery(id+"F0.wireOp",EDGE,"afc6e781-25c3-4dd1-969d-5b2406180a6c.3.23.18"),sQuery(id+"F0.wireOp",EDGE,"afc6e781-25c3-4dd1-969d-5b2406180a6c.6.23.18"),sQuery(id+"F0.wireOp",EDGE,"afc6e781-25c3-4dd1-969d-5b2406180a6c.9.23.18"),sQuery(id+"F0.wireOp",EDGE,"afc6e781-25c3-4dd1-969d-5b2406180a6c.0.23.19"),sQuery(id+"F0.wireOp",EDGE,"afc6e781-25c3-4dd1-969d-5b2406180a6c.3.23.19"),sQuery(id+"F0.wireOp",EDGE,"afc6e781-25c3-4dd1-969d-5b2406180a6c.6.23.19"),sQuery(id+"F0.wireOp",EDGE,"afc6e781-25c3-4dd1-969d-5b2406180a6c.9.23.19"),sQuery(id+"F0.wireOp",EDGE,"afc6e781-25c3-4dd1-969d-5b2406180a6c.0.23.20"),sQuery(id+"F0.wireOp",EDGE,"afc6e781-25c3-4dd1-969d-5b2406180a6c.3.23.20"),sQuery(id+"F0.wireOp",EDGE,"afc6e781-25c3-4dd1-969d-5b2406180a6c.6.23.20"),sQuery(id+"F0.wireOp",EDGE,"afc6e781-25c3-4dd1-969d-5b2406180a6c.9.23.20"),sQuery(id+"F0.wireOp",EDGE,"afc6e781-25c3-4dd1-969d-5b2406180a6c.0.23.21"),sQuery(id+"F0.wireOp",EDGE,"afc6e781-25c3-4dd1-969d-5b2406180a6c.3.23.21"),sQuery(id+"F0.wireOp",EDGE,"afc6e781-25c3-4dd1-969d-5b2406180a6c.6.23.21"),sQuery(id+"F0.wireOp",EDGE,"afc6e781-25c3-4dd1-969d-5b2406180a6c.9.23.21"),sQuery(id+"F0.wireOp",EDGE,"afc6e781-25c3-4dd1-969d-5b2406180a6c.0.23.22"),sQuery(id+"F0.wireOp",EDGE,"afc6e781-25c3-4dd1-969d-5b2406180a6c.3.23.22"),sQuery(id+"F0.wireOp",EDGE,"afc6e781-25c3-4dd1-969d-5b2406180a6c.6.23.22"),sQuery(id+"F0.wireOp",EDGE,"afc6e781-25c3-4dd1-969d-5b2406180a6c.9.23.22"),sQuery(id+"F0.wireOp",EDGE,"afc6e781-25c3-4dd1-969d-5b2406180a6c.0.23.23"),sQuery(id+"F0.wireOp",EDGE,"afc6e781-25c3-4dd1-969d-5b2406180a6c.3.23.23"),sQuery(id+"F0.wireOp",EDGE,"afc6e781-25c3-4dd1-969d-5b2406180a6c.6.23.23"),sQuery(id+"F0.wireOp",EDGE,"afc6e781-25c3-4dd1-969d-5b2406180a6c.9.23.23"),sQuery(id+"F0.wireOp",EDGE,"afc6e781-25c3-4dd1-969d-5b2406180a6c.0.23.24"),sQuery(id+"F0.wireOp",EDGE,"afc6e781-25c3-4dd1-969d-5b2406180a6c.3.23.24"),sQuery(id+"F0.wireOp",EDGE,"afc6e781-25c3-4dd1-969d-5b2406180a6c.6.23.24"),sQuery(id+"F0.wireOp",EDGE,"afc6e781-25c3-4dd1-969d-5b2406180a6c.9.23.24"),sQuery(id+"F0.wireOp",EDGE,"afc6e781-25c3-4dd1-969d-5b2406180a6c.0.23.25"),sQuery(id+"F0.wireOp",EDGE,"afc6e781-25c3-4dd1-969d-5b2406180a6c.3.23.25"),sQuery(id+"F0.wireOp",EDGE,"afc6e781-25c3-4dd1-969d-5b2406180a6c.6.23.25"),sQuery(id+"F0.wireOp",EDGE,"afc6e781-25c3-4dd1-969d-5b2406180a6c.9.23.25"),sQuery(id+"F0.wireOp",EDGE,"afc6e781-25c3-4dd1-969d-5b2406180a6c.0.23.26"),sQuery(id+"F0.wireOp",EDGE,"afc6e781-25c3-4dd1-969d-5b2406180a6c.3.23.26"),sQuery(id+"F0.wireOp",EDGE,"afc6e781-25c3-4dd1-969d-5b2406180a6c.6.23.26"),sQuery(id+"F0.wireOp",EDGE,"afc6e781-25c3-4dd1-969d-5b2406180a6c.9.23.26"),sQuery(id+"F0.wireOp",EDGE,"afc6e781-25c3-4dd1-969d-5b2406180a6c.0.23.27"),sQuery(id+"F0.wireOp",EDGE,"afc6e781-25c3-4dd1-969d-5b2406180a6c.3.23.27"),sQuery(id+"F0.wireOp",EDGE,"afc6e781-25c3-4dd1-969d-5b2406180a6c.6.23.27"),sQuery(id+"F0.wireOp",EDGE,"afc6e781-25c3-4dd1-969d-5b2406180a6c.9.23.27"),sQuery(id+"F0.wireOp",EDGE,"afc6e781-25c3-4dd1-969d-5b2406180a6c.0.23.28"),sQuery(id+"F0.wireOp",EDGE,"afc6e781-25c3-4dd1-969d-5b2406180a6c.3.23.28"),sQuery(id+"F0.wireOp",EDGE,"afc6e781-25c3-4dd1-969d-5b2406180a6c.6.23.28"),sQuery(id+"F0.wireOp",EDGE,"afc6e781-25c3-4dd1-969d-5b2406180a6c.9.23.28"),sQuery(id+"F0.wireOp",EDGE,"afc6e781-25c3-4dd1-969d-5b2406180a6c.0.23.29"),sQuery(id+"F0.wireOp",EDGE,"afc6e781-25c3-4dd1-969d-5b2406180a6c.3.23.29"),sQuery(id+"F0.wireOp",EDGE,"afc6e781-25c3-4dd1-969d-5b2406180a6c.6.23.29"),sQuery(id+"F0.wireOp",EDGE,"afc6e781-25c3-4dd1-969d-5b2406180a6c.9.23.29"),sQuery(id+"F0.wireOp",EDGE,"afc6e781-25c3-4dd1-969d-5b2406180a6c.0.23.30"),sQuery(id+"F0.wireOp",EDGE,"afc6e781-25c3-4dd1-969d-5b2406180a6c.3.23.30"),sQuery(id+"F0.wireOp",EDGE,"afc6e781-25c3-4dd1-969d-5b2406180a6c.6.23.30"),sQuery(id+"F0.wireOp",EDGE,"afc6e781-25c3-4dd1-969d-5b2406180a6c.9.23.30"),sQuery(id+"F0.wireOp",EDGE,"afc6e781-25c3-4dd1-969d-5b2406180a6c.0.23.31"),sQuery(id+"F0.wireOp",EDGE,"afc6e781-25c3-4dd1-969d-5b2406180a6c.3.23.31"),sQuery(id+"F0.wireOp",EDGE,"afc6e781-25c3-4dd1-969d-5b2406180a6c.6.23.31"),sQuery(id+"F0.wireOp",EDGE,"afc6e781-25c3-4dd1-969d-5b2406180a6c.9.23.31"),sQuery(id+"F0.wireOp",EDGE,"afc6e781-25c3-4dd1-969d-5b2406180a6c.0.24.0"),sQuery(id+"F0.wireOp",EDGE,"afc6e781-25c3-4dd1-969d-5b2406180a6c.3.24.0"),sQuery(id+"F0.wireOp",EDGE,"afc6e781-25c3-4dd1-969d-5b2406180a6c.6.24.0"),sQuery(id+"F0.wireOp",EDGE,"afc6e781-25c3-4dd1-969d-5b2406180a6c.9.24.0"),sQuery(id+"F0.wireOp",EDGE,"afc6e781-25c3-4dd1-969d-5b2406180a6c.0.24.1"),sQuery(id+"F0.wireOp",EDGE,"afc6e781-25c3-4dd1-969d-5b2406180a6c.3.24.1"),sQuery(id+"F0.wireOp",EDGE,"afc6e781-25c3-4dd1-969d-5b2406180a6c.6.24.1"),sQuery(id+"F0.wireOp",EDGE,"afc6e781-25c3-4dd1-969d-5b2406180a6c.9.24.1"),sQuery(id+"F0.wireOp",EDGE,"afc6e781-25c3-4dd1-969d-5b2406180a6c.0.24.2"),sQuery(id+"F0.wireOp",EDGE,"afc6e781-25c3-4dd1-969d-5b2406180a6c.3.24.2"),sQuery(id+"F0.wireOp",EDGE,"afc6e781-25c3-4dd1-969d-5b2406180a6c.6.24.2"),sQuery(id+"F0.wireOp",EDGE,"afc6e781-25c3-4dd1-969d-5b2406180a6c.9.24.2"),sQuery(id+"F0.wireOp",EDGE,"afc6e781-25c3-4dd1-969d-5b2406180a6c.0.24.3"),sQuery(id+"F0.wireOp",EDGE,"afc6e781-25c3-4dd1-969d-5b2406180a6c.3.24.3"),sQuery(id+"F0.wireOp",EDGE,"afc6e781-25c3-4dd1-969d-5b2406180a6c.6.24.3"),sQuery(id+"F0.wireOp",EDGE,"afc6e781-25c3-4dd1-969d-5b2406180a6c.9.24.3"),sQuery(id+"F0.wireOp",EDGE,"afc6e781-25c3-4dd1-969d-5b2406180a6c.0.24.4"),sQuery(id+"F0.wireOp",EDGE,"afc6e781-25c3-4dd1-969d-5b2406180a6c.3.24.4"),sQuery(id+"F0.wireOp",EDGE,"afc6e781-25c3-4dd1-969d-5b2406180a6c.6.24.4"),sQuery(id+"F0.wireOp",EDGE,"afc6e781-25c3-4dd1-969d-5b2406180a6c.9.24.4"),sQuery(id+"F0.wireOp",EDGE,"afc6e781-25c3-4dd1-969d-5b2406180a6c.0.24.5"),sQuery(id+"F0.wireOp",EDGE,"afc6e781-25c3-4dd1-969d-5b2406180a6c.3.24.5"),sQuery(id+"F0.wireOp",EDGE,"afc6e781-25c3-4dd1-969d-5b2406180a6c.6.24.5"),sQuery(id+"F0.wireOp",EDGE,"afc6e781-25c3-4dd1-969d-5b2406180a6c.9.24.5"),sQuery(id+"F0.wireOp",EDGE,"afc6e781-25c3-4dd1-969d-5b2406180a6c.0.24.6"),sQuery(id+"F0.wireOp",EDGE,"afc6e781-25c3-4dd1-969d-5b2406180a6c.3.24.6"),sQuery(id+"F0.wireOp",EDGE,"afc6e781-25c3-4dd1-969d-5b2406180a6c.6.24.6"),sQuery(id+"F0.wireOp",EDGE,"afc6e781-25c3-4dd1-969d-5b2406180a6c.9.24.6"),sQuery(id+"F0.wireOp",EDGE,"afc6e781-25c3-4dd1-969d-5b2406180a6c.0.24.7"),sQuery(id+"F0.wireOp",EDGE,"afc6e781-25c3-4dd1-969d-5b2406180a6c.3.24.7"),sQuery(id+"F0.wireOp",EDGE,"afc6e781-25c3-4dd1-969d-5b2406180a6c.6.24.7"),sQuery(id+"F0.wireOp",EDGE,"afc6e781-25c3-4dd1-969d-5b2406180a6c.9.24.7"),sQuery(id+"F0.wireOp",EDGE,"afc6e781-25c3-4dd1-969d-5b2406180a6c.0.24.8"),sQuery(id+"F0.wireOp",EDGE,"afc6e781-25c3-4dd1-969d-5b2406180a6c.3.24.8"),sQuery(id+"F0.wireOp",EDGE,"afc6e781-25c3-4dd1-969d-5b2406180a6c.6.24.8"),sQuery(id+"F0.wireOp",EDGE,"afc6e781-25c3-4dd1-969d-5b2406180a6c.9.24.8"),sQuery(id+"F0.wireOp",EDGE,"afc6e781-25c3-4dd1-969d-5b2406180a6c.0.24.9"),sQuery(id+"F0.wireOp",EDGE,"afc6e781-25c3-4dd1-969d-5b2406180a6c.3.24.9"),sQuery(id+"F0.wireOp",EDGE,"afc6e781-25c3-4dd1-969d-5b2406180a6c.6.24.9"),sQuery(id+"F0.wireOp",EDGE,"afc6e781-25c3-4dd1-969d-5b2406180a6c.9.24.9"),sQuery(id+"F0.wireOp",EDGE,"afc6e781-25c3-4dd1-969d-5b2406180a6c.0.24.10"),sQuery(id+"F0.wireOp",EDGE,"afc6e781-25c3-4dd1-969d-5b2406180a6c.3.24.10"),sQuery(id+"F0.wireOp",EDGE,"afc6e781-25c3-4dd1-969d-5b2406180a6c.6.24.10"),sQuery(id+"F0.wireOp",EDGE,"afc6e781-25c3-4dd1-969d-5b2406180a6c.9.24.10"),sQuery(id+"F0.wireOp",EDGE,"afc6e781-25c3-4dd1-969d-5b2406180a6c.0.24.11"),sQuery(id+"F0.wireOp",EDGE,"afc6e781-25c3-4dd1-969d-5b2406180a6c.3.24.11"),sQuery(id+"F0.wireOp",EDGE,"afc6e781-25c3-4dd1-969d-5b2406180a6c.6.24.11"),sQuery(id+"F0.wireOp",EDGE,"afc6e781-25c3-4dd1-969d-5b2406180a6c.9.24.11"),sQuery(id+"F0.wireOp",EDGE,"afc6e781-25c3-4dd1-969d-5b2406180a6c.0.24.12"),sQuery(id+"F0.wireOp",EDGE,"afc6e781-25c3-4dd1-969d-5b2406180a6c.3.24.12"),sQuery(id+"F0.wireOp",EDGE,"afc6e781-25c3-4dd1-969d-5b2406180a6c.6.24.12"),sQuery(id+"F0.wireOp",EDGE,"afc6e781-25c3-4dd1-969d-5b2406180a6c.9.24.12"),sQuery(id+"F0.wireOp",EDGE,"afc6e781-25c3-4dd1-969d-5b2406180a6c.0.24.13"),sQuery(id+"F0.wireOp",EDGE,"afc6e781-25c3-4dd1-969d-5b2406180a6c.3.24.13"),sQuery(id+"F0.wireOp",EDGE,"afc6e781-25c3-4dd1-969d-5b2406180a6c.6.24.13"),sQuery(id+"F0.wireOp",EDGE,"afc6e781-25c3-4dd1-969d-5b2406180a6c.9.24.13"),sQuery(id+"F0.wireOp",EDGE,"afc6e781-25c3-4dd1-969d-5b2406180a6c.0.24.14"),sQuery(id+"F0.wireOp",EDGE,"afc6e781-25c3-4dd1-969d-5b2406180a6c.3.24.14"),sQuery(id+"F0.wireOp",EDGE,"afc6e781-25c3-4dd1-969d-5b2406180a6c.6.24.14"),sQuery(id+"F0.wireOp",EDGE,"afc6e781-25c3-4dd1-969d-5b2406180a6c.9.24.14"),sQuery(id+"F0.wireOp",EDGE,"afc6e781-25c3-4dd1-969d-5b2406180a6c.0.24.15"),sQuery(id+"F0.wireOp",EDGE,"afc6e781-25c3-4dd1-969d-5b2406180a6c.3.24.15"),sQuery(id+"F0.wireOp",EDGE,"afc6e781-25c3-4dd1-969d-5b2406180a6c.6.24.15"),sQuery(id+"F0.wireOp",EDGE,"afc6e781-25c3-4dd1-969d-5b2406180a6c.9.24.15"),sQuery(id+"F0.wireOp",EDGE,"afc6e781-25c3-4dd1-969d-5b2406180a6c.0.24.16"),sQuery(id+"F0.wireOp",EDGE,"afc6e781-25c3-4dd1-969d-5b2406180a6c.3.24.16"),sQuery(id+"F0.wireOp",EDGE,"afc6e781-25c3-4dd1-969d-5b2406180a6c.6.24.16"),sQuery(id+"F0.wireOp",EDGE,"afc6e781-25c3-4dd1-969d-5b2406180a6c.9.24.16"),sQuery(id+"F0.wireOp",EDGE,"afc6e781-25c3-4dd1-969d-5b2406180a6c.0.24.17"),sQuery(id+"F0.wireOp",EDGE,"afc6e781-25c3-4dd1-969d-5b2406180a6c.3.24.17"),sQuery(id+"F0.wireOp",EDGE,"afc6e781-25c3-4dd1-969d-5b2406180a6c.6.24.17"),sQuery(id+"F0.wireOp",EDGE,"afc6e781-25c3-4dd1-969d-5b2406180a6c.9.24.17"),sQuery(id+"F0.wireOp",EDGE,"afc6e781-25c3-4dd1-969d-5b2406180a6c.0.24.18"),sQuery(id+"F0.wireOp",EDGE,"afc6e781-25c3-4dd1-969d-5b2406180a6c.3.24.18"),sQuery(id+"F0.wireOp",EDGE,"afc6e781-25c3-4dd1-969d-5b2406180a6c.6.24.18"),sQuery(id+"F0.wireOp",EDGE,"afc6e781-25c3-4dd1-969d-5b2406180a6c.9.24.18"),sQuery(id+"F0.wireOp",EDGE,"afc6e781-25c3-4dd1-969d-5b2406180a6c.0.24.19"),sQuery(id+"F0.wireOp",EDGE,"afc6e781-25c3-4dd1-969d-5b2406180a6c.3.24.19"),sQuery(id+"F0.wireOp",EDGE,"afc6e781-25c3-4dd1-969d-5b2406180a6c.6.24.19"),sQuery(id+"F0.wireOp",EDGE,"afc6e781-25c3-4dd1-969d-5b2406180a6c.9.24.19"),sQuery(id+"F0.wireOp",EDGE,"afc6e781-25c3-4dd1-969d-5b2406180a6c.0.24.20"),sQuery(id+"F0.wireOp",EDGE,"afc6e781-25c3-4dd1-969d-5b2406180a6c.3.24.20"),sQuery(id+"F0.wireOp",EDGE,"afc6e781-25c3-4dd1-969d-5b2406180a6c.6.24.20"),sQuery(id+"F0.wireOp",EDGE,"afc6e781-25c3-4dd1-969d-5b2406180a6c.9.24.20"),sQuery(id+"F0.wireOp",EDGE,"afc6e781-25c3-4dd1-969d-5b2406180a6c.0.24.21"),sQuery(id+"F0.wireOp",EDGE,"afc6e781-25c3-4dd1-969d-5b2406180a6c.3.24.21"),sQuery(id+"F0.wireOp",EDGE,"afc6e781-25c3-4dd1-969d-5b2406180a6c.6.24.21"),sQuery(id+"F0.wireOp",EDGE,"afc6e781-25c3-4dd1-969d-5b2406180a6c.9.24.21"),sQuery(id+"F0.wireOp",EDGE,"afc6e781-25c3-4dd1-969d-5b2406180a6c.0.24.22"),sQuery(id+"F0.wireOp",EDGE,"afc6e781-25c3-4dd1-969d-5b2406180a6c.3.24.22"),sQuery(id+"F0.wireOp",EDGE,"afc6e781-25c3-4dd1-969d-5b2406180a6c.6.24.22"),sQuery(id+"F0.wireOp",EDGE,"afc6e781-25c3-4dd1-969d-5b2406180a6c.9.24.22"),sQuery(id+"F0.wireOp",EDGE,"afc6e781-25c3-4dd1-969d-5b2406180a6c.0.24.23"),sQuery(id+"F0.wireOp",EDGE,"afc6e781-25c3-4dd1-969d-5b2406180a6c.3.24.23"),sQuery(id+"F0.wireOp",EDGE,"afc6e781-25c3-4dd1-969d-5b2406180a6c.6.24.23"),sQuery(id+"F0.wireOp",EDGE,"afc6e781-25c3-4dd1-969d-5b2406180a6c.9.24.23"),sQuery(id+"F0.wireOp",EDGE,"afc6e781-25c3-4dd1-969d-5b2406180a6c.0.24.24"),sQuery(id+"F0.wireOp",EDGE,"afc6e781-25c3-4dd1-969d-5b2406180a6c.3.24.24"),sQuery(id+"F0.wireOp",EDGE,"afc6e781-25c3-4dd1-969d-5b2406180a6c.6.24.24"),sQuery(id+"F0.wireOp",EDGE,"afc6e781-25c3-4dd1-969d-5b2406180a6c.9.24.24"),sQuery(id+"F0.wireOp",EDGE,"afc6e781-25c3-4dd1-969d-5b2406180a6c.0.24.25"),sQuery(id+"F0.wireOp",EDGE,"afc6e781-25c3-4dd1-969d-5b2406180a6c.3.24.25"),sQuery(id+"F0.wireOp",EDGE,"afc6e781-25c3-4dd1-969d-5b2406180a6c.6.24.25"),sQuery(id+"F0.wireOp",EDGE,"afc6e781-25c3-4dd1-969d-5b2406180a6c.9.24.25"),sQuery(id+"F0.wireOp",EDGE,"afc6e781-25c3-4dd1-969d-5b2406180a6c.0.24.26"),sQuery(id+"F0.wireOp",EDGE,"afc6e781-25c3-4dd1-969d-5b2406180a6c.3.24.26"),sQuery(id+"F0.wireOp",EDGE,"afc6e781-25c3-4dd1-969d-5b2406180a6c.6.24.26"),sQuery(id+"F0.wireOp",EDGE,"afc6e781-25c3-4dd1-969d-5b2406180a6c.9.24.26"),sQuery(id+"F0.wireOp",EDGE,"afc6e781-25c3-4dd1-969d-5b2406180a6c.0.24.27"),sQuery(id+"F0.wireOp",EDGE,"afc6e781-25c3-4dd1-969d-5b2406180a6c.3.24.27"),sQuery(id+"F0.wireOp",EDGE,"afc6e781-25c3-4dd1-969d-5b2406180a6c.6.24.27"),sQuery(id+"F0.wireOp",EDGE,"afc6e781-25c3-4dd1-969d-5b2406180a6c.9.24.27"),sQuery(id+"F0.wireOp",EDGE,"afc6e781-25c3-4dd1-969d-5b2406180a6c.0.24.28"),sQuery(id+"F0.wireOp",EDGE,"afc6e781-25c3-4dd1-969d-5b2406180a6c.3.24.28"),sQuery(id+"F0.wireOp",EDGE,"afc6e781-25c3-4dd1-969d-5b2406180a6c.6.24.28"),sQuery(id+"F0.wireOp",EDGE,"afc6e781-25c3-4dd1-969d-5b2406180a6c.9.24.28"),sQuery(id+"F0.wireOp",EDGE,"afc6e781-25c3-4dd1-969d-5b2406180a6c.0.24.29"),sQuery(id+"F0.wireOp",EDGE,"afc6e781-25c3-4dd1-969d-5b2406180a6c.3.24.29"),sQuery(id+"F0.wireOp",EDGE,"afc6e781-25c3-4dd1-969d-5b2406180a6c.6.24.29"),sQuery(id+"F0.wireOp",EDGE,"afc6e781-25c3-4dd1-969d-5b2406180a6c.9.24.29"),sQuery(id+"F0.wireOp",EDGE,"afc6e781-25c3-4dd1-969d-5b2406180a6c.0.24.30"),sQuery(id+"F0.wireOp",EDGE,"afc6e781-25c3-4dd1-969d-5b2406180a6c.3.24.30"),sQuery(id+"F0.wireOp",EDGE,"afc6e781-25c3-4dd1-969d-5b2406180a6c.6.24.30"),sQuery(id+"F0.wireOp",EDGE,"afc6e781-25c3-4dd1-969d-5b2406180a6c.9.24.30"),sQuery(id+"F0.wireOp",EDGE,"afc6e781-25c3-4dd1-969d-5b2406180a6c.0.24.31"),sQuery(id+"F0.wireOp",EDGE,"afc6e781-25c3-4dd1-969d-5b2406180a6c.3.24.31"),sQuery(id+"F0.wireOp",EDGE,"afc6e781-25c3-4dd1-969d-5b2406180a6c.6.24.31"),sQuery(id+"F0.wireOp",EDGE,"afc6e781-25c3-4dd1-969d-5b2406180a6c.9.24.31")])],"isStart":true});
            var sketch = newSketch(context, id + "F2", { "sketchPlane" : qUnion([Q0])});
            skLineSegment(sketch, "E15.bottom", {"start": v(-261, 198) * mm, "end": v(-317, 198) * mm});
            skLineSegment(sketch, "E15.top", {"start": v(-261, 226) * mm, "end": v(-317, 226) * mm});
            skLineSegment(sketch, "E15.left", {"start": v(-261, 198) * mm, "end": v(-261, 226) * mm});
            skLineSegment(sketch, "E15.right", {"start": v(-317, 198) * mm, "end": v(-317, 226) * mm});
            skLineSegment(sketch, "E16.bottom", {"start": v(-317, 124) * mm, "end": v(-261, 124) * mm});
            skLineSegment(sketch, "E16.top", {"start": v(-317, 100) * mm, "end": v(-261, 100) * mm});
            skLineSegment(sketch, "E16.left", {"start": v(-317, 124) * mm, "end": v(-317, 100) * mm});
            skLineSegment(sketch, "E16.right", {"start": v(-261, 124) * mm, "end": v(-261, 100) * mm});
            skLineSegment(sketch, "E17.bottom", {"start": v(-317, -30) * mm, "end": v(-261, -30) * mm});
            skLineSegment(sketch, "E17.top", {"start": v(-317, -54) * mm, "end": v(-261, -54) * mm});
            skLineSegment(sketch, "E17.left", {"start": v(-317, -30) * mm, "end": v(-317, -54) * mm});
            skLineSegment(sketch, "E17.right", {"start": v(-261, -30) * mm, "end": v(-261, -54) * mm});
            skLineSegment(sketch, "E18", {"start": v(-315, 226) * mm, "end": v(-315, -226) * mm, "construction": true});
            skLineSegment(sketch, "E19", {"start": v(-300, -226) * mm, "end": v(-300, 226) * mm, "construction": true});
            skLineSegment(sketch, "E20", {"start": v(-285, -226) * mm, "end": v(-285, 226) * mm, "construction": true});
            skLineSegment(sketch, "E21", {"start": v(285, 226) * mm, "end": v(285, -226) * mm, "construction": true});
            skLineSegment(sketch, "E22", {"start": v(300, -226) * mm, "end": v(300, 226) * mm, "construction": true});
            skLineSegment(sketch, "E23", {"start": v(315, 226) * mm, "end": v(315, -226) * mm, "construction": true});
            skLineSegment(sketch, "E24", {"start": v(-315, 212) * mm, "end": v(315, 212) * mm, "construction": true});
            skLineSegment(sketch, "E25", {"start": v(-315, 122) * mm, "end": v(315, 122) * mm, "construction": true});
            skLineSegment(sketch, "E26", {"start": v(-315, -19.5) * mm, "end": v(315, -19.5) * mm, "construction": true});
            skLineSegment(sketch, "E27", {"start": v(-315, 41.5) * mm, "end": v(315, 41.5) * mm, "construction": true});
            skLineSegment(sketch, "E28", {"start": v(-315, 2.72) * mm, "end": v(315, 2.72) * mm, "construction": true});
            skCircle(sketch, "E29", {"center": v(-300, 212) * mm, "radius": 3.5 * mm, "construction": true});
            skCircle(sketch, "E30", {"center": v(-300, 122) * mm, "radius": 3.5 * mm, "construction": true});
            skCircle(sketch, "E31", {"center": v(-300, -19.5) * mm, "radius": 3.5 * mm, "construction": true});
            skSolve(sketch);
        }
        {
            var Q0;
            Q0 = qSketchRegion(id + "F2", true);
            extrude(context, id + "F3", {"entities" : qUnion([Q0]), "operationType" : NewBodyOperationType.REMOVE, "oppositeDirection" : true, "depth" : 1.5 * mm});
        }
    });
